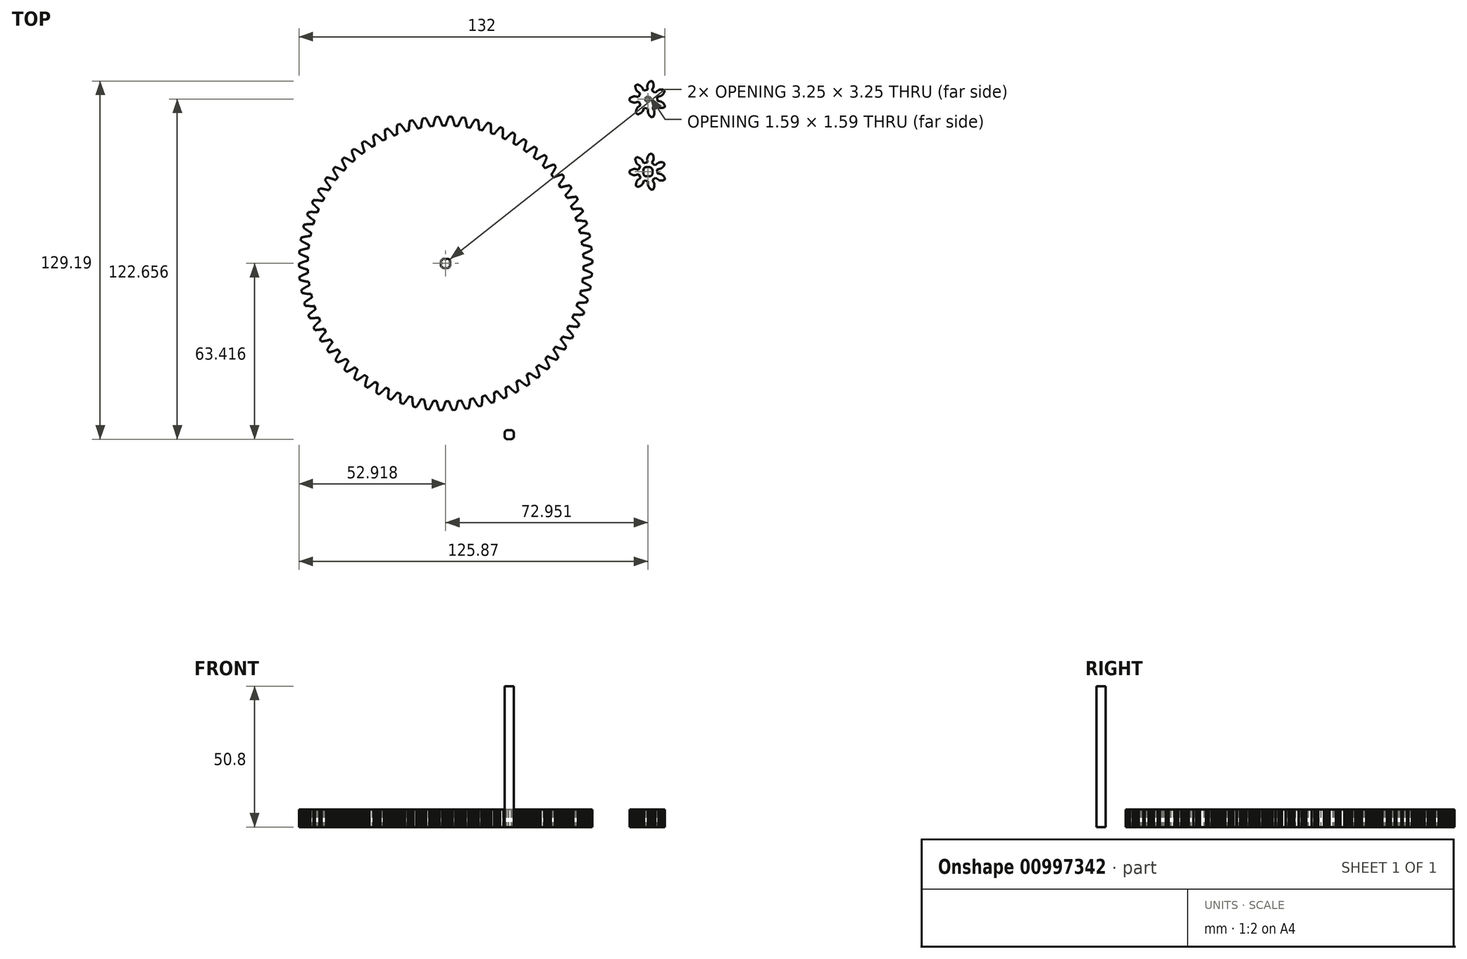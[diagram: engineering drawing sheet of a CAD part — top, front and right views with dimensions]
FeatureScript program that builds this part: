
annotation { "Feature Type Name" : "Feature", "Feature Type Description" : "" }
export const myFeature = defineFeature(function(context is Context, id is Id, definition is map)
    precondition{}
    {
        {
            var Q0;
            Q0=qCreatedBy(makeId("Top.planeOp"),FACE);
            var sketch = newSketch(context, id + "F0", { "sketchPlane" : qUnion([Q0])});
            skLineSegment(sketch, "E0", {"start": v(50.77, 50.5) * mm, "end": v(50.67, 50.68) * mm});
            skLineSegment(sketch, "E1", {"start": v(50.67, 50.68) * mm, "end": v(50.56, 50.86) * mm});
            skLineSegment(sketch, "E2", {"start": v(50.56, 50.86) * mm, "end": v(50.46, 51.01) * mm});
            skLineSegment(sketch, "E3", {"start": v(50.46, 51.01) * mm, "end": v(50.35, 51.16) * mm});
            skLineSegment(sketch, "E4", {"start": v(50.35, 51.16) * mm, "end": v(50.24, 51.28) * mm});
            skLineSegment(sketch, "E5", {"start": v(50.24, 51.28) * mm, "end": v(50.14, 51.4) * mm});
            skLineSegment(sketch, "E6", {"start": v(50.14, 51.4) * mm, "end": v(50.04, 51.5) * mm});
            skLineSegment(sketch, "E7", {"start": v(50.04, 51.5) * mm, "end": v(49.94, 51.58) * mm});
            skLineSegment(sketch, "E8", {"start": v(49.94, 51.58) * mm, "end": v(49.85, 51.66) * mm});
            skLineSegment(sketch, "E9", {"start": v(49.85, 51.66) * mm, "end": v(49.76, 51.72) * mm});
            skLineSegment(sketch, "E10", {"start": v(49.76, 51.72) * mm, "end": v(49.68, 51.77) * mm});
            skLineSegment(sketch, "E11", {"start": v(49.68, 51.77) * mm, "end": v(49.61, 51.81) * mm});
            skLineSegment(sketch, "E12", {"start": v(49.61, 51.81) * mm, "end": v(49.55, 51.85) * mm});
            skLineSegment(sketch, "E13", {"start": v(49.55, 51.85) * mm, "end": v(49.5, 51.87) * mm});
            skLineSegment(sketch, "E14", {"start": v(49.5, 51.87) * mm, "end": v(49.45, 51.89) * mm});
            skLineSegment(sketch, "E15", {"start": v(49.45, 51.89) * mm, "end": v(49.42, 51.9) * mm});
            skLineSegment(sketch, "E16", {"start": v(49.42, 51.9) * mm, "end": v(49.4, 51.9) * mm});
            skLineSegment(sketch, "E17", {"start": v(49.4, 51.9) * mm, "end": v(49.4, 51.9) * mm});
            skLineSegment(sketch, "E18", {"start": v(49.4, 51.9) * mm, "end": v(48.03, 52.16) * mm});
            skLineSegment(sketch, "E19", {"start": v(48.03, 52.16) * mm, "end": v(48, 53.63) * mm});
            skLineSegment(sketch, "E20", {"start": v(48, 53.63) * mm, "end": v(49.33, 53.97) * mm});
            skLineSegment(sketch, "E21", {"start": v(49.33, 53.97) * mm, "end": v(49.34, 53.97) * mm});
            skLineSegment(sketch, "E22", {"start": v(49.34, 53.97) * mm, "end": v(49.36, 53.98) * mm});
            skLineSegment(sketch, "E23", {"start": v(49.36, 53.98) * mm, "end": v(49.4, 53.99) * mm});
            skLineSegment(sketch, "E24", {"start": v(49.4, 53.99) * mm, "end": v(49.44, 54) * mm});
            skLineSegment(sketch, "E25", {"start": v(49.44, 54) * mm, "end": v(49.5, 54.03) * mm});
            skLineSegment(sketch, "E26", {"start": v(49.5, 54.03) * mm, "end": v(49.55, 54.07) * mm});
            skLineSegment(sketch, "E27", {"start": v(49.55, 54.07) * mm, "end": v(49.62, 54.12) * mm});
            skLineSegment(sketch, "E28", {"start": v(49.62, 54.12) * mm, "end": v(49.7, 54.17) * mm});
            skLineSegment(sketch, "E29", {"start": v(49.7, 54.17) * mm, "end": v(49.78, 54.24) * mm});
            skLineSegment(sketch, "E30", {"start": v(49.78, 54.24) * mm, "end": v(49.87, 54.32) * mm});
            skLineSegment(sketch, "E31", {"start": v(49.87, 54.32) * mm, "end": v(49.96, 54.41) * mm});
            skLineSegment(sketch, "E32", {"start": v(49.96, 54.41) * mm, "end": v(50.05, 54.52) * mm});
            skLineSegment(sketch, "E33", {"start": v(50.05, 54.52) * mm, "end": v(50.15, 54.64) * mm});
            skLineSegment(sketch, "E34", {"start": v(50.15, 54.64) * mm, "end": v(50.25, 54.77) * mm});
            skLineSegment(sketch, "E35", {"start": v(50.25, 54.77) * mm, "end": v(50.35, 54.92) * mm});
            skLineSegment(sketch, "E36", {"start": v(50.35, 54.92) * mm, "end": v(50.45, 55.08) * mm});
            skLineSegment(sketch, "E37", {"start": v(50.45, 55.08) * mm, "end": v(50.54, 55.26) * mm});
            skLineSegment(sketch, "E38", {"start": v(50.54, 55.26) * mm, "end": v(50.63, 55.45) * mm});
            skLineSegment(sketch, "E39", {"start": v(50.63, 55.45) * mm, "end": v(50.63, 55.62) * mm});
            skLineSegment(sketch, "E40", {"start": v(50.63, 55.62) * mm, "end": v(50.4, 56.06) * mm});
            skLineSegment(sketch, "E41", {"start": v(50.4, 56.06) * mm, "end": v(50.27, 56.16) * mm});
            skLineSegment(sketch, "E42", {"start": v(50.27, 56.16) * mm, "end": v(50.06, 56.2) * mm});
            skLineSegment(sketch, "E43", {"start": v(50.06, 56.2) * mm, "end": v(49.86, 56.22) * mm});
            skLineSegment(sketch, "E44", {"start": v(49.86, 56.22) * mm, "end": v(49.67, 56.24) * mm});
            skLineSegment(sketch, "E45", {"start": v(49.67, 56.24) * mm, "end": v(49.5, 56.24) * mm});
            skLineSegment(sketch, "E46", {"start": v(49.5, 56.24) * mm, "end": v(49.32, 56.24) * mm});
            skLineSegment(sketch, "E47", {"start": v(49.32, 56.24) * mm, "end": v(49.17, 56.23) * mm});
            skLineSegment(sketch, "E48", {"start": v(49.17, 56.23) * mm, "end": v(49.03, 56.21) * mm});
            skLineSegment(sketch, "E49", {"start": v(49.03, 56.21) * mm, "end": v(48.9, 56.19) * mm});
            skLineSegment(sketch, "E50", {"start": v(48.9, 56.19) * mm, "end": v(48.78, 56.16) * mm});
            skLineSegment(sketch, "E51", {"start": v(48.78, 56.16) * mm, "end": v(48.68, 56.14) * mm});
            skLineSegment(sketch, "E52", {"start": v(48.68, 56.14) * mm, "end": v(48.6, 56.1) * mm});
            skLineSegment(sketch, "E53", {"start": v(48.6, 56.1) * mm, "end": v(48.52, 56.08) * mm});
            skLineSegment(sketch, "E54", {"start": v(48.52, 56.08) * mm, "end": v(48.45, 56.05) * mm});
            skLineSegment(sketch, "E55", {"start": v(48.45, 56.05) * mm, "end": v(48.4, 56.02) * mm});
            skLineSegment(sketch, "E56", {"start": v(48.4, 56.02) * mm, "end": v(48.36, 56) * mm});
            skLineSegment(sketch, "E57", {"start": v(48.36, 56) * mm, "end": v(48.33, 55.98) * mm});
            skLineSegment(sketch, "E58", {"start": v(48.33, 55.98) * mm, "end": v(48.31, 55.97) * mm});
            skLineSegment(sketch, "E59", {"start": v(48.31, 55.97) * mm, "end": v(48.3, 55.96) * mm});
            skLineSegment(sketch, "E60", {"start": v(48.3, 55.96) * mm, "end": v(47.26, 55.06) * mm});
            skLineSegment(sketch, "E61", {"start": v(47.26, 55.06) * mm, "end": v(46.08, 55.94) * mm});
            skLineSegment(sketch, "E62", {"start": v(46.08, 55.94) * mm, "end": v(46.66, 57.2) * mm});
            skLineSegment(sketch, "E63", {"start": v(46.66, 57.2) * mm, "end": v(46.66, 57.2) * mm});
            skLineSegment(sketch, "E64", {"start": v(46.66, 57.2) * mm, "end": v(46.67, 57.23) * mm});
            skLineSegment(sketch, "E65", {"start": v(46.67, 57.23) * mm, "end": v(46.68, 57.26) * mm});
            skLineSegment(sketch, "E66", {"start": v(46.68, 57.26) * mm, "end": v(46.7, 57.3) * mm});
            skLineSegment(sketch, "E67", {"start": v(46.7, 57.3) * mm, "end": v(46.7, 57.36) * mm});
            skLineSegment(sketch, "E68", {"start": v(46.7, 57.36) * mm, "end": v(46.71, 57.43) * mm});
            skLineSegment(sketch, "E69", {"start": v(46.71, 57.43) * mm, "end": v(46.72, 57.52) * mm});
            skLineSegment(sketch, "E70", {"start": v(46.72, 57.52) * mm, "end": v(46.72, 57.61) * mm});
            skLineSegment(sketch, "E71", {"start": v(46.72, 57.61) * mm, "end": v(46.72, 57.72) * mm});
            skLineSegment(sketch, "E72", {"start": v(46.72, 57.72) * mm, "end": v(46.72, 57.83) * mm});
            skLineSegment(sketch, "E73", {"start": v(46.72, 57.83) * mm, "end": v(46.7, 57.96) * mm});
            skLineSegment(sketch, "E74", {"start": v(46.7, 57.96) * mm, "end": v(46.68, 58.1) * mm});
            skLineSegment(sketch, "E75", {"start": v(46.68, 58.1) * mm, "end": v(46.65, 58.26) * mm});
            skLineSegment(sketch, "E76", {"start": v(46.65, 58.26) * mm, "end": v(46.6, 58.42) * mm});
            skLineSegment(sketch, "E77", {"start": v(46.6, 58.42) * mm, "end": v(46.55, 58.59) * mm});
            skLineSegment(sketch, "E78", {"start": v(46.55, 58.59) * mm, "end": v(46.48, 58.77) * mm});
            skLineSegment(sketch, "E79", {"start": v(46.48, 58.77) * mm, "end": v(46.4, 58.95) * mm});
            skLineSegment(sketch, "E80", {"start": v(46.4, 58.95) * mm, "end": v(46.3, 59.14) * mm});
            skLineSegment(sketch, "E81", {"start": v(46.3, 59.14) * mm, "end": v(46.17, 59.24) * mm});
            skLineSegment(sketch, "E82", {"start": v(46.17, 59.24) * mm, "end": v(45.7, 59.34) * mm});
            skLineSegment(sketch, "E83", {"start": v(45.7, 59.34) * mm, "end": v(45.53, 59.3) * mm});
            skLineSegment(sketch, "E84", {"start": v(45.53, 59.3) * mm, "end": v(45.37, 59.16) * mm});
            skLineSegment(sketch, "E85", {"start": v(45.37, 59.16) * mm, "end": v(45.22, 59.02) * mm});
            skLineSegment(sketch, "E86", {"start": v(45.22, 59.02) * mm, "end": v(45.1, 58.88) * mm});
            skLineSegment(sketch, "E87", {"start": v(45.1, 58.88) * mm, "end": v(44.98, 58.74) * mm});
            skLineSegment(sketch, "E88", {"start": v(44.98, 58.74) * mm, "end": v(44.88, 58.6) * mm});
            skLineSegment(sketch, "E89", {"start": v(44.88, 58.6) * mm, "end": v(44.79, 58.48) * mm});
            skLineSegment(sketch, "E90", {"start": v(44.79, 58.48) * mm, "end": v(44.71, 58.36) * mm});
            skLineSegment(sketch, "E91", {"start": v(44.71, 58.36) * mm, "end": v(44.65, 58.25) * mm});
            skLineSegment(sketch, "E92", {"start": v(44.65, 58.25) * mm, "end": v(44.6, 58.14) * mm});
            skLineSegment(sketch, "E93", {"start": v(44.6, 58.14) * mm, "end": v(44.56, 58.04) * mm});
            skLineSegment(sketch, "E94", {"start": v(44.56, 58.04) * mm, "end": v(44.52, 57.95) * mm});
            skLineSegment(sketch, "E95", {"start": v(44.52, 57.95) * mm, "end": v(44.5, 57.88) * mm});
            skLineSegment(sketch, "E96", {"start": v(44.5, 57.88) * mm, "end": v(44.48, 57.8) * mm});
            skLineSegment(sketch, "E97", {"start": v(44.48, 57.8) * mm, "end": v(44.47, 57.75) * mm});
            skLineSegment(sketch, "E98", {"start": v(44.47, 57.75) * mm, "end": v(44.46, 57.7) * mm});
            skLineSegment(sketch, "E99", {"start": v(44.46, 57.7) * mm, "end": v(44.46, 57.67) * mm});
            skLineSegment(sketch, "E100", {"start": v(44.46, 57.67) * mm, "end": v(44.46, 57.65) * mm});
            skLineSegment(sketch, "E101", {"start": v(44.46, 57.65) * mm, "end": v(44.46, 57.64) * mm});
            skLineSegment(sketch, "E102", {"start": v(44.46, 57.64) * mm, "end": v(44.5, 56.26) * mm});
            skLineSegment(sketch, "E103", {"start": v(44.5, 56.26) * mm, "end": v(43.09, 55.9) * mm});
            skLineSegment(sketch, "E104", {"start": v(43.09, 55.9) * mm, "end": v(42.47, 57.13) * mm});
            skLineSegment(sketch, "E105", {"start": v(42.47, 57.13) * mm, "end": v(42.46, 57.13) * mm});
            skLineSegment(sketch, "E106", {"start": v(42.46, 57.13) * mm, "end": v(42.45, 57.15) * mm});
            skLineSegment(sketch, "E107", {"start": v(42.45, 57.15) * mm, "end": v(42.43, 57.18) * mm});
            skLineSegment(sketch, "E108", {"start": v(42.43, 57.18) * mm, "end": v(42.4, 57.22) * mm});
            skLineSegment(sketch, "E109", {"start": v(42.4, 57.22) * mm, "end": v(42.36, 57.26) * mm});
            skLineSegment(sketch, "E110", {"start": v(42.36, 57.26) * mm, "end": v(42.31, 57.31) * mm});
            skLineSegment(sketch, "E111", {"start": v(42.31, 57.31) * mm, "end": v(42.25, 57.37) * mm});
            skLineSegment(sketch, "E112", {"start": v(42.25, 57.37) * mm, "end": v(42.18, 57.43) * mm});
            skLineSegment(sketch, "E113", {"start": v(42.18, 57.43) * mm, "end": v(42.1, 57.5) * mm});
            skLineSegment(sketch, "E114", {"start": v(42.1, 57.5) * mm, "end": v(42, 57.56) * mm});
            skLineSegment(sketch, "E115", {"start": v(42, 57.56) * mm, "end": v(41.9, 57.63) * mm});
            skLineSegment(sketch, "E116", {"start": v(41.9, 57.63) * mm, "end": v(41.77, 57.7) * mm});
            skLineSegment(sketch, "E117", {"start": v(41.77, 57.7) * mm, "end": v(41.63, 57.77) * mm});
            skLineSegment(sketch, "E118", {"start": v(41.63, 57.77) * mm, "end": v(41.48, 57.84) * mm});
            skLineSegment(sketch, "E119", {"start": v(41.48, 57.84) * mm, "end": v(41.31, 57.9) * mm});
            skLineSegment(sketch, "E120", {"start": v(41.31, 57.9) * mm, "end": v(41.13, 57.96) * mm});
            skLineSegment(sketch, "E121", {"start": v(41.13, 57.96) * mm, "end": v(40.93, 58.02) * mm});
            skLineSegment(sketch, "E122", {"start": v(40.93, 58.02) * mm, "end": v(40.72, 58.06) * mm});
            skLineSegment(sketch, "E123", {"start": v(40.72, 58.06) * mm, "end": v(40.56, 58.02) * mm});
            skLineSegment(sketch, "E124", {"start": v(40.56, 58.02) * mm, "end": v(40.2, 57.7) * mm});
            skLineSegment(sketch, "E125", {"start": v(40.2, 57.7) * mm, "end": v(40.12, 57.55) * mm});
            skLineSegment(sketch, "E126", {"start": v(40.12, 57.55) * mm, "end": v(40.13, 57.34) * mm});
            skLineSegment(sketch, "E127", {"start": v(40.13, 57.34) * mm, "end": v(40.15, 57.13) * mm});
            skLineSegment(sketch, "E128", {"start": v(40.15, 57.13) * mm, "end": v(40.18, 56.95) * mm});
            skLineSegment(sketch, "E129", {"start": v(40.18, 56.95) * mm, "end": v(40.21, 56.77) * mm});
            skLineSegment(sketch, "E130", {"start": v(40.21, 56.77) * mm, "end": v(40.25, 56.6) * mm});
            skLineSegment(sketch, "E131", {"start": v(40.25, 56.6) * mm, "end": v(40.3, 56.46) * mm});
            skLineSegment(sketch, "E132", {"start": v(40.3, 56.46) * mm, "end": v(40.34, 56.33) * mm});
            skLineSegment(sketch, "E133", {"start": v(40.34, 56.33) * mm, "end": v(40.4, 56.2) * mm});
            skLineSegment(sketch, "E134", {"start": v(40.4, 56.2) * mm, "end": v(40.44, 56.1) * mm});
            skLineSegment(sketch, "E135", {"start": v(40.44, 56.1) * mm, "end": v(40.5, 56) * mm});
            skLineSegment(sketch, "E136", {"start": v(40.5, 56) * mm, "end": v(40.54, 55.93) * mm});
            skLineSegment(sketch, "E137", {"start": v(40.54, 55.93) * mm, "end": v(40.59, 55.86) * mm});
            skLineSegment(sketch, "E138", {"start": v(40.59, 55.86) * mm, "end": v(40.63, 55.8) * mm});
            skLineSegment(sketch, "E139", {"start": v(40.63, 55.8) * mm, "end": v(40.67, 55.76) * mm});
            skLineSegment(sketch, "E140", {"start": v(40.67, 55.76) * mm, "end": v(40.7, 55.72) * mm});
            skLineSegment(sketch, "E141", {"start": v(40.7, 55.72) * mm, "end": v(40.72, 55.7) * mm});
            skLineSegment(sketch, "E142", {"start": v(40.72, 55.7) * mm, "end": v(40.74, 55.68) * mm});
            skLineSegment(sketch, "E143", {"start": v(40.74, 55.68) * mm, "end": v(40.75, 55.68) * mm});
            skLineSegment(sketch, "E144", {"start": v(40.75, 55.68) * mm, "end": v(41.86, 54.86) * mm});
            skLineSegment(sketch, "E145", {"start": v(41.86, 54.86) * mm, "end": v(41.26, 53.52) * mm});
            skLineSegment(sketch, "E146", {"start": v(41.26, 53.52) * mm, "end": v(39.9, 53.8) * mm});
            skLineSegment(sketch, "E147", {"start": v(39.9, 53.8) * mm, "end": v(39.9, 53.8) * mm});
            skLineSegment(sketch, "E148", {"start": v(39.9, 53.8) * mm, "end": v(39.88, 53.8) * mm});
            skLineSegment(sketch, "E149", {"start": v(39.88, 53.8) * mm, "end": v(39.84, 53.8) * mm});
            skLineSegment(sketch, "E150", {"start": v(39.84, 53.8) * mm, "end": v(39.8, 53.8) * mm});
            skLineSegment(sketch, "E151", {"start": v(39.8, 53.8) * mm, "end": v(39.74, 53.8) * mm});
            skLineSegment(sketch, "E152", {"start": v(39.74, 53.8) * mm, "end": v(39.67, 53.8) * mm});
            skLineSegment(sketch, "E153", {"start": v(39.67, 53.8) * mm, "end": v(39.59, 53.79) * mm});
            skLineSegment(sketch, "E154", {"start": v(39.59, 53.79) * mm, "end": v(39.5, 53.77) * mm});
            skLineSegment(sketch, "E155", {"start": v(39.5, 53.77) * mm, "end": v(39.39, 53.74) * mm});
            skLineSegment(sketch, "E156", {"start": v(39.39, 53.74) * mm, "end": v(39.28, 53.71) * mm});
            skLineSegment(sketch, "E157", {"start": v(39.28, 53.71) * mm, "end": v(39.15, 53.67) * mm});
            skLineSegment(sketch, "E158", {"start": v(39.15, 53.67) * mm, "end": v(39.02, 53.62) * mm});
            skLineSegment(sketch, "E159", {"start": v(39.02, 53.62) * mm, "end": v(38.88, 53.55) * mm});
            skLineSegment(sketch, "E160", {"start": v(38.88, 53.55) * mm, "end": v(38.73, 53.47) * mm});
            skLineSegment(sketch, "E161", {"start": v(38.73, 53.47) * mm, "end": v(38.58, 53.38) * mm});
            skLineSegment(sketch, "E162", {"start": v(38.58, 53.38) * mm, "end": v(38.42, 53.28) * mm});
            skLineSegment(sketch, "E163", {"start": v(38.42, 53.28) * mm, "end": v(38.26, 53.16) * mm});
            skLineSegment(sketch, "E164", {"start": v(38.26, 53.16) * mm, "end": v(38.1, 53.02) * mm});
            skLineSegment(sketch, "E165", {"start": v(38.1, 53.02) * mm, "end": v(38.03, 52.87) * mm});
            skLineSegment(sketch, "E166", {"start": v(38.03, 52.87) * mm, "end": v(38.04, 52.38) * mm});
            skLineSegment(sketch, "E167", {"start": v(38.04, 52.38) * mm, "end": v(38.11, 52.23) * mm});
            skLineSegment(sketch, "E168", {"start": v(38.11, 52.23) * mm, "end": v(38.29, 52.1) * mm});
            skLineSegment(sketch, "E169", {"start": v(38.29, 52.1) * mm, "end": v(38.46, 52) * mm});
            skLineSegment(sketch, "E170", {"start": v(38.46, 52) * mm, "end": v(38.62, 51.9) * mm});
            skLineSegment(sketch, "E171", {"start": v(38.62, 51.9) * mm, "end": v(38.78, 51.82) * mm});
            skLineSegment(sketch, "E172", {"start": v(38.78, 51.82) * mm, "end": v(38.93, 51.75) * mm});
            skLineSegment(sketch, "E173", {"start": v(38.93, 51.75) * mm, "end": v(39.07, 51.69) * mm});
            skLineSegment(sketch, "E174", {"start": v(39.07, 51.69) * mm, "end": v(39.2, 51.64) * mm});
            skLineSegment(sketch, "E175", {"start": v(39.2, 51.64) * mm, "end": v(39.33, 51.6) * mm});
            skLineSegment(sketch, "E176", {"start": v(39.33, 51.6) * mm, "end": v(39.45, 51.58) * mm});
            skLineSegment(sketch, "E177", {"start": v(39.45, 51.58) * mm, "end": v(39.55, 51.56) * mm});
            skLineSegment(sketch, "E178", {"start": v(39.55, 51.56) * mm, "end": v(39.65, 51.55) * mm});
            skLineSegment(sketch, "E179", {"start": v(39.65, 51.55) * mm, "end": v(39.73, 51.54) * mm});
            skLineSegment(sketch, "E180", {"start": v(39.73, 51.54) * mm, "end": v(39.8, 51.54) * mm});
            skLineSegment(sketch, "E181", {"start": v(39.8, 51.54) * mm, "end": v(39.86, 51.54) * mm});
            skLineSegment(sketch, "E182", {"start": v(39.86, 51.54) * mm, "end": v(39.9, 51.54) * mm});
            skLineSegment(sketch, "E183", {"start": v(39.9, 51.54) * mm, "end": v(39.94, 51.55) * mm});
            skLineSegment(sketch, "E184", {"start": v(39.94, 51.55) * mm, "end": v(39.96, 51.55) * mm});
            skLineSegment(sketch, "E185", {"start": v(39.96, 51.55) * mm, "end": v(39.97, 51.55) * mm});
            skLineSegment(sketch, "E186", {"start": v(39.97, 51.55) * mm, "end": v(41.3, 51.91) * mm});
            skLineSegment(sketch, "E187", {"start": v(41.3, 51.91) * mm, "end": v(41.98, 50.6) * mm});
            skLineSegment(sketch, "E188", {"start": v(41.98, 50.6) * mm, "end": v(40.91, 49.73) * mm});
            skLineSegment(sketch, "E189", {"start": v(40.91, 49.73) * mm, "end": v(40.9, 49.72) * mm});
            skLineSegment(sketch, "E190", {"start": v(40.9, 49.72) * mm, "end": v(40.9, 49.7) * mm});
            skLineSegment(sketch, "E191", {"start": v(40.9, 49.7) * mm, "end": v(40.87, 49.68) * mm});
            skLineSegment(sketch, "E192", {"start": v(40.87, 49.68) * mm, "end": v(40.84, 49.64) * mm});
            skLineSegment(sketch, "E193", {"start": v(40.84, 49.64) * mm, "end": v(40.8, 49.6) * mm});
            skLineSegment(sketch, "E194", {"start": v(40.8, 49.6) * mm, "end": v(40.76, 49.54) * mm});
            skLineSegment(sketch, "E195", {"start": v(40.76, 49.54) * mm, "end": v(40.72, 49.47) * mm});
            skLineSegment(sketch, "E196", {"start": v(40.72, 49.47) * mm, "end": v(40.68, 49.38) * mm});
            skLineSegment(sketch, "E197", {"start": v(40.68, 49.38) * mm, "end": v(40.63, 49.29) * mm});
            skLineSegment(sketch, "E198", {"start": v(40.63, 49.29) * mm, "end": v(40.59, 49.18) * mm});
            skLineSegment(sketch, "E199", {"start": v(40.59, 49.18) * mm, "end": v(40.54, 49.05) * mm});
            skLineSegment(sketch, "E200", {"start": v(40.54, 49.05) * mm, "end": v(40.5, 48.92) * mm});
            skLineSegment(sketch, "E201", {"start": v(40.5, 48.92) * mm, "end": v(40.47, 48.77) * mm});
            skLineSegment(sketch, "E202", {"start": v(40.47, 48.77) * mm, "end": v(40.44, 48.6) * mm});
            skLineSegment(sketch, "E203", {"start": v(40.44, 48.6) * mm, "end": v(40.41, 48.43) * mm});
            skLineSegment(sketch, "E204", {"start": v(40.41, 48.43) * mm, "end": v(40.4, 48.24) * mm});
            skLineSegment(sketch, "E205", {"start": v(40.4, 48.24) * mm, "end": v(40.39, 48.03) * mm});
            skLineSegment(sketch, "E206", {"start": v(40.39, 48.03) * mm, "end": v(40.39, 47.82) * mm});
            skLineSegment(sketch, "E207", {"start": v(40.39, 47.82) * mm, "end": v(40.47, 47.67) * mm});
            skLineSegment(sketch, "E208", {"start": v(40.47, 47.67) * mm, "end": v(40.86, 47.38) * mm});
            skLineSegment(sketch, "E209", {"start": v(40.86, 47.38) * mm, "end": v(41.02, 47.34) * mm});
            skLineSegment(sketch, "E210", {"start": v(41.02, 47.34) * mm, "end": v(41.23, 47.4) * mm});
            skLineSegment(sketch, "E211", {"start": v(41.23, 47.4) * mm, "end": v(41.42, 47.46) * mm});
            skLineSegment(sketch, "E212", {"start": v(41.42, 47.46) * mm, "end": v(41.6, 47.53) * mm});
            skLineSegment(sketch, "E213", {"start": v(41.6, 47.53) * mm, "end": v(41.76, 47.6) * mm});
            skLineSegment(sketch, "E214", {"start": v(41.76, 47.6) * mm, "end": v(41.9, 47.68) * mm});
            skLineSegment(sketch, "E215", {"start": v(41.9, 47.68) * mm, "end": v(42.04, 47.76) * mm});
            skLineSegment(sketch, "E216", {"start": v(42.04, 47.76) * mm, "end": v(42.16, 47.83) * mm});
            skLineSegment(sketch, "E217", {"start": v(42.16, 47.83) * mm, "end": v(42.27, 47.9) * mm});
            skLineSegment(sketch, "E218", {"start": v(42.27, 47.9) * mm, "end": v(42.36, 47.98) * mm});
            skLineSegment(sketch, "E219", {"start": v(42.36, 47.98) * mm, "end": v(42.44, 48.05) * mm});
            skLineSegment(sketch, "E220", {"start": v(42.44, 48.05) * mm, "end": v(42.51, 48.12) * mm});
            skLineSegment(sketch, "E221", {"start": v(42.51, 48.12) * mm, "end": v(42.57, 48.18) * mm});
            skLineSegment(sketch, "E222", {"start": v(42.57, 48.18) * mm, "end": v(42.61, 48.23) * mm});
            skLineSegment(sketch, "E223", {"start": v(42.61, 48.23) * mm, "end": v(42.65, 48.28) * mm});
            skLineSegment(sketch, "E224", {"start": v(42.65, 48.28) * mm, "end": v(42.67, 48.32) * mm});
            skLineSegment(sketch, "E225", {"start": v(42.67, 48.32) * mm, "end": v(42.7, 48.35) * mm});
            skLineSegment(sketch, "E226", {"start": v(42.7, 48.35) * mm, "end": v(42.7, 48.37) * mm});
            skLineSegment(sketch, "E227", {"start": v(42.7, 48.37) * mm, "end": v(42.7, 48.37) * mm});
            skLineSegment(sketch, "E228", {"start": v(42.7, 48.37) * mm, "end": v(43.26, 49.64) * mm});
            skLineSegment(sketch, "E229", {"start": v(43.26, 49.64) * mm, "end": v(44.7, 49.35) * mm});
            skLineSegment(sketch, "E230", {"start": v(44.7, 49.35) * mm, "end": v(44.72, 47.97) * mm});
            skLineSegment(sketch, "E231", {"start": v(44.72, 47.97) * mm, "end": v(44.73, 47.96) * mm});
            skLineSegment(sketch, "E232", {"start": v(44.73, 47.96) * mm, "end": v(44.73, 47.94) * mm});
            skLineSegment(sketch, "E233", {"start": v(44.73, 47.94) * mm, "end": v(44.73, 47.9) * mm});
            skLineSegment(sketch, "E234", {"start": v(44.73, 47.9) * mm, "end": v(44.74, 47.86) * mm});
            skLineSegment(sketch, "E235", {"start": v(44.74, 47.86) * mm, "end": v(44.76, 47.8) * mm});
            skLineSegment(sketch, "E236", {"start": v(44.76, 47.8) * mm, "end": v(44.78, 47.74) * mm});
            skLineSegment(sketch, "E237", {"start": v(44.78, 47.74) * mm, "end": v(44.8, 47.66) * mm});
            skLineSegment(sketch, "E238", {"start": v(44.8, 47.66) * mm, "end": v(44.85, 47.57) * mm});
            skLineSegment(sketch, "E239", {"start": v(44.85, 47.57) * mm, "end": v(44.9, 47.48) * mm});
            skLineSegment(sketch, "E240", {"start": v(44.9, 47.48) * mm, "end": v(44.95, 47.37) * mm});
            skLineSegment(sketch, "E241", {"start": v(44.95, 47.37) * mm, "end": v(45.02, 47.26) * mm});
            skLineSegment(sketch, "E242", {"start": v(45.02, 47.26) * mm, "end": v(45.1, 47.15) * mm});
            skLineSegment(sketch, "E243", {"start": v(45.1, 47.15) * mm, "end": v(45.2, 47.03) * mm});
            skLineSegment(sketch, "E244", {"start": v(45.2, 47.03) * mm, "end": v(45.3, 46.9) * mm});
            skLineSegment(sketch, "E245", {"start": v(45.3, 46.9) * mm, "end": v(45.43, 46.77) * mm});
            skLineSegment(sketch, "E246", {"start": v(45.43, 46.77) * mm, "end": v(45.57, 46.64) * mm});
            skLineSegment(sketch, "E247", {"start": v(45.57, 46.64) * mm, "end": v(45.72, 46.5) * mm});
            skLineSegment(sketch, "E248", {"start": v(45.72, 46.5) * mm, "end": v(45.89, 46.37) * mm});
            skLineSegment(sketch, "E249", {"start": v(45.89, 46.37) * mm, "end": v(46.05, 46.34) * mm});
            skLineSegment(sketch, "E250", {"start": v(46.05, 46.34) * mm, "end": v(46.52, 46.47) * mm});
            skLineSegment(sketch, "E251", {"start": v(46.52, 46.47) * mm, "end": v(46.65, 46.57) * mm});
            skLineSegment(sketch, "E252", {"start": v(46.65, 46.57) * mm, "end": v(46.74, 46.77) * mm});
            skLineSegment(sketch, "E253", {"start": v(46.74, 46.77) * mm, "end": v(46.8, 46.96) * mm});
            skLineSegment(sketch, "E254", {"start": v(46.8, 46.96) * mm, "end": v(46.87, 47.14) * mm});
            skLineSegment(sketch, "E255", {"start": v(46.87, 47.14) * mm, "end": v(46.91, 47.31) * mm});
            skLineSegment(sketch, "E256", {"start": v(46.91, 47.31) * mm, "end": v(46.94, 47.48) * mm});
            skLineSegment(sketch, "E257", {"start": v(46.94, 47.48) * mm, "end": v(46.97, 47.63) * mm});
            skLineSegment(sketch, "E258", {"start": v(46.97, 47.63) * mm, "end": v(46.98, 47.77) * mm});
            skLineSegment(sketch, "E259", {"start": v(46.98, 47.77) * mm, "end": v(47, 47.9) * mm});
            skLineSegment(sketch, "E260", {"start": v(47, 47.9) * mm, "end": v(47, 48.02) * mm});
            skLineSegment(sketch, "E261", {"start": v(47, 48.02) * mm, "end": v(46.99, 48.12) * mm});
            skLineSegment(sketch, "E262", {"start": v(46.99, 48.12) * mm, "end": v(46.98, 48.22) * mm});
            skLineSegment(sketch, "E263", {"start": v(46.98, 48.22) * mm, "end": v(46.97, 48.3) * mm});
            skLineSegment(sketch, "E264", {"start": v(46.97, 48.3) * mm, "end": v(46.95, 48.37) * mm});
            skLineSegment(sketch, "E265", {"start": v(46.95, 48.37) * mm, "end": v(46.94, 48.43) * mm});
            skLineSegment(sketch, "E266", {"start": v(46.94, 48.43) * mm, "end": v(46.92, 48.47) * mm});
            skLineSegment(sketch, "E267", {"start": v(46.92, 48.47) * mm, "end": v(46.91, 48.5) * mm});
            skLineSegment(sketch, "E268", {"start": v(46.91, 48.5) * mm, "end": v(46.9, 48.52) * mm});
            skLineSegment(sketch, "E269", {"start": v(46.9, 48.52) * mm, "end": v(46.9, 48.53) * mm});
            skLineSegment(sketch, "E270", {"start": v(46.9, 48.53) * mm, "end": v(46.25, 49.75) * mm});
            skLineSegment(sketch, "E271", {"start": v(46.25, 49.75) * mm, "end": v(47.38, 50.7) * mm});
            skLineSegment(sketch, "E272", {"start": v(47.38, 50.7) * mm, "end": v(48.47, 49.86) * mm});
            skLineSegment(sketch, "E273", {"start": v(48.47, 49.86) * mm, "end": v(48.48, 49.85) * mm});
            skLineSegment(sketch, "E274", {"start": v(48.48, 49.85) * mm, "end": v(48.5, 49.84) * mm});
            skLineSegment(sketch, "E275", {"start": v(48.5, 49.84) * mm, "end": v(48.53, 49.82) * mm});
            skLineSegment(sketch, "E276", {"start": v(48.53, 49.82) * mm, "end": v(48.57, 49.8) * mm});
            skLineSegment(sketch, "E277", {"start": v(48.57, 49.8) * mm, "end": v(48.62, 49.78) * mm});
            skLineSegment(sketch, "E278", {"start": v(48.62, 49.78) * mm, "end": v(48.7, 49.76) * mm});
            skLineSegment(sketch, "E279", {"start": v(48.7, 49.76) * mm, "end": v(48.77, 49.73) * mm});
            skLineSegment(sketch, "E280", {"start": v(48.77, 49.73) * mm, "end": v(48.86, 49.7) * mm});
            skLineSegment(sketch, "E281", {"start": v(48.86, 49.7) * mm, "end": v(48.96, 49.68) * mm});
            skLineSegment(sketch, "E282", {"start": v(48.96, 49.68) * mm, "end": v(49.08, 49.66) * mm});
            skLineSegment(sketch, "E283", {"start": v(49.08, 49.66) * mm, "end": v(49.21, 49.65) * mm});
            skLineSegment(sketch, "E284", {"start": v(49.21, 49.65) * mm, "end": v(49.35, 49.64) * mm});
            skLineSegment(sketch, "E285", {"start": v(49.35, 49.64) * mm, "end": v(49.5, 49.64) * mm});
            skLineSegment(sketch, "E286", {"start": v(49.5, 49.64) * mm, "end": v(49.67, 49.64) * mm});
            skLineSegment(sketch, "E287", {"start": v(49.67, 49.64) * mm, "end": v(49.85, 49.66) * mm});
            skLineSegment(sketch, "E288", {"start": v(49.85, 49.66) * mm, "end": v(50.04, 49.68) * mm});
            skLineSegment(sketch, "E289", {"start": v(50.04, 49.68) * mm, "end": v(50.24, 49.72) * mm});
            skLineSegment(sketch, "E290", {"start": v(50.24, 49.72) * mm, "end": v(50.45, 49.77) * mm});
            skLineSegment(sketch, "E291", {"start": v(50.45, 49.77) * mm, "end": v(50.57, 49.88) * mm});
            skLineSegment(sketch, "E292", {"start": v(50.57, 49.88) * mm, "end": v(50.77, 50.33) * mm});
            skLineSegment(sketch, "E293", {"start": v(50.77, 50.33) * mm, "end": v(50.77, 50.5) * mm});
            skLineSegment(sketch, "E294", {"start": v(50.77, 24.31) * mm, "end": v(50.67, 24.5) * mm});
            skLineSegment(sketch, "E295", {"start": v(50.67, 24.5) * mm, "end": v(50.56, 24.67) * mm});
            skLineSegment(sketch, "E296", {"start": v(50.56, 24.67) * mm, "end": v(50.46, 24.83) * mm});
            skLineSegment(sketch, "E297", {"start": v(50.46, 24.83) * mm, "end": v(50.35, 24.97) * mm});
            skLineSegment(sketch, "E298", {"start": v(50.35, 24.97) * mm, "end": v(50.24, 25.1) * mm});
            skLineSegment(sketch, "E299", {"start": v(50.24, 25.1) * mm, "end": v(50.14, 25.22) * mm});
            skLineSegment(sketch, "E300", {"start": v(50.14, 25.22) * mm, "end": v(50.04, 25.32) * mm});
            skLineSegment(sketch, "E301", {"start": v(50.04, 25.32) * mm, "end": v(49.94, 25.4) * mm});
            skLineSegment(sketch, "E302", {"start": v(49.94, 25.4) * mm, "end": v(49.85, 25.48) * mm});
            skLineSegment(sketch, "E303", {"start": v(49.85, 25.48) * mm, "end": v(49.76, 25.54) * mm});
            skLineSegment(sketch, "E304", {"start": v(49.76, 25.54) * mm, "end": v(49.68, 25.6) * mm});
            skLineSegment(sketch, "E305", {"start": v(49.68, 25.6) * mm, "end": v(49.61, 25.63) * mm});
            skLineSegment(sketch, "E306", {"start": v(49.61, 25.63) * mm, "end": v(49.55, 25.66) * mm});
            skLineSegment(sketch, "E307", {"start": v(49.55, 25.66) * mm, "end": v(49.5, 25.69) * mm});
            skLineSegment(sketch, "E308", {"start": v(49.5, 25.69) * mm, "end": v(49.45, 25.7) * mm});
            skLineSegment(sketch, "E309", {"start": v(49.45, 25.7) * mm, "end": v(49.42, 25.72) * mm});
            skLineSegment(sketch, "E310", {"start": v(49.42, 25.72) * mm, "end": v(49.4, 25.72) * mm});
            skLineSegment(sketch, "E311", {"start": v(49.4, 25.72) * mm, "end": v(49.4, 25.73) * mm});
            skLineSegment(sketch, "E312", {"start": v(49.4, 25.73) * mm, "end": v(48.03, 25.98) * mm});
            skLineSegment(sketch, "E313", {"start": v(48.03, 25.98) * mm, "end": v(48, 27.45) * mm});
            skLineSegment(sketch, "E314", {"start": v(48, 27.45) * mm, "end": v(49.33, 27.78) * mm});
            skLineSegment(sketch, "E315", {"start": v(49.33, 27.78) * mm, "end": v(49.34, 27.79) * mm});
            skLineSegment(sketch, "E316", {"start": v(49.34, 27.79) * mm, "end": v(49.36, 27.8) * mm});
            skLineSegment(sketch, "E317", {"start": v(49.36, 27.8) * mm, "end": v(49.4, 27.8) * mm});
            skLineSegment(sketch, "E318", {"start": v(49.4, 27.8) * mm, "end": v(49.44, 27.83) * mm});
            skLineSegment(sketch, "E319", {"start": v(49.44, 27.83) * mm, "end": v(49.5, 27.85) * mm});
            skLineSegment(sketch, "E320", {"start": v(49.5, 27.85) * mm, "end": v(49.55, 27.89) * mm});
            skLineSegment(sketch, "E321", {"start": v(49.55, 27.89) * mm, "end": v(49.62, 27.93) * mm});
            skLineSegment(sketch, "E322", {"start": v(49.62, 27.93) * mm, "end": v(49.7, 27.99) * mm});
            skLineSegment(sketch, "E323", {"start": v(49.7, 27.99) * mm, "end": v(49.78, 28.06) * mm});
            skLineSegment(sketch, "E324", {"start": v(49.78, 28.06) * mm, "end": v(49.87, 28.14) * mm});
            skLineSegment(sketch, "E325", {"start": v(49.87, 28.14) * mm, "end": v(49.96, 28.23) * mm});
            skLineSegment(sketch, "E326", {"start": v(49.96, 28.23) * mm, "end": v(50.05, 28.33) * mm});
            skLineSegment(sketch, "E327", {"start": v(50.05, 28.33) * mm, "end": v(50.15, 28.45) * mm});
            skLineSegment(sketch, "E328", {"start": v(50.15, 28.45) * mm, "end": v(50.25, 28.59) * mm});
            skLineSegment(sketch, "E329", {"start": v(50.25, 28.59) * mm, "end": v(50.35, 28.74) * mm});
            skLineSegment(sketch, "E330", {"start": v(50.35, 28.74) * mm, "end": v(50.45, 28.9) * mm});
            skLineSegment(sketch, "E331", {"start": v(50.45, 28.9) * mm, "end": v(50.54, 29.08) * mm});
            skLineSegment(sketch, "E332", {"start": v(50.54, 29.08) * mm, "end": v(50.63, 29.27) * mm});
            skLineSegment(sketch, "E333", {"start": v(50.63, 29.27) * mm, "end": v(50.63, 29.44) * mm});
            skLineSegment(sketch, "E334", {"start": v(50.63, 29.44) * mm, "end": v(50.4, 29.87) * mm});
            skLineSegment(sketch, "E335", {"start": v(50.4, 29.87) * mm, "end": v(50.27, 29.98) * mm});
            skLineSegment(sketch, "E336", {"start": v(50.27, 29.98) * mm, "end": v(50.06, 30.01) * mm});
            skLineSegment(sketch, "E337", {"start": v(50.06, 30.01) * mm, "end": v(49.86, 30.04) * mm});
            skLineSegment(sketch, "E338", {"start": v(49.86, 30.04) * mm, "end": v(49.67, 30.05) * mm});
            skLineSegment(sketch, "E339", {"start": v(49.67, 30.05) * mm, "end": v(49.5, 30.06) * mm});
            skLineSegment(sketch, "E340", {"start": v(49.5, 30.06) * mm, "end": v(49.32, 30.06) * mm});
            skLineSegment(sketch, "E341", {"start": v(49.32, 30.06) * mm, "end": v(49.17, 30.05) * mm});
            skLineSegment(sketch, "E342", {"start": v(49.17, 30.05) * mm, "end": v(49.03, 30.03) * mm});
            skLineSegment(sketch, "E343", {"start": v(49.03, 30.03) * mm, "end": v(48.9, 30) * mm});
            skLineSegment(sketch, "E344", {"start": v(48.9, 30) * mm, "end": v(48.78, 29.98) * mm});
            skLineSegment(sketch, "E345", {"start": v(48.78, 29.98) * mm, "end": v(48.68, 29.95) * mm});
            skLineSegment(sketch, "E346", {"start": v(48.68, 29.95) * mm, "end": v(48.6, 29.92) * mm});
            skLineSegment(sketch, "E347", {"start": v(48.6, 29.92) * mm, "end": v(48.52, 29.9) * mm});
            skLineSegment(sketch, "E348", {"start": v(48.52, 29.9) * mm, "end": v(48.45, 29.87) * mm});
            skLineSegment(sketch, "E349", {"start": v(48.45, 29.87) * mm, "end": v(48.4, 29.84) * mm});
            skLineSegment(sketch, "E350", {"start": v(48.4, 29.84) * mm, "end": v(48.36, 29.82) * mm});
            skLineSegment(sketch, "E351", {"start": v(48.36, 29.82) * mm, "end": v(48.33, 29.8) * mm});
            skLineSegment(sketch, "E352", {"start": v(48.33, 29.8) * mm, "end": v(48.31, 29.78) * mm});
            skLineSegment(sketch, "E353", {"start": v(48.31, 29.78) * mm, "end": v(48.3, 29.78) * mm});
            skLineSegment(sketch, "E354", {"start": v(48.3, 29.78) * mm, "end": v(47.26, 28.88) * mm});
            skLineSegment(sketch, "E355", {"start": v(47.26, 28.88) * mm, "end": v(46.08, 29.76) * mm});
            skLineSegment(sketch, "E356", {"start": v(46.08, 29.76) * mm, "end": v(46.66, 31.02) * mm});
            skLineSegment(sketch, "E357", {"start": v(46.66, 31.02) * mm, "end": v(46.66, 31.03) * mm});
            skLineSegment(sketch, "E358", {"start": v(46.66, 31.03) * mm, "end": v(46.67, 31.05) * mm});
            skLineSegment(sketch, "E359", {"start": v(46.67, 31.05) * mm, "end": v(46.68, 31.08) * mm});
            skLineSegment(sketch, "E360", {"start": v(46.68, 31.08) * mm, "end": v(46.7, 31.12) * mm});
            skLineSegment(sketch, "E361", {"start": v(46.7, 31.12) * mm, "end": v(46.7, 31.18) * mm});
            skLineSegment(sketch, "E362", {"start": v(46.7, 31.18) * mm, "end": v(46.71, 31.25) * mm});
            skLineSegment(sketch, "E363", {"start": v(46.71, 31.25) * mm, "end": v(46.72, 31.33) * mm});
            skLineSegment(sketch, "E364", {"start": v(46.72, 31.33) * mm, "end": v(46.72, 31.43) * mm});
            skLineSegment(sketch, "E365", {"start": v(46.72, 31.43) * mm, "end": v(46.72, 31.53) * mm});
            skLineSegment(sketch, "E366", {"start": v(46.72, 31.53) * mm, "end": v(46.72, 31.65) * mm});
            skLineSegment(sketch, "E367", {"start": v(46.72, 31.65) * mm, "end": v(46.7, 31.78) * mm});
            skLineSegment(sketch, "E368", {"start": v(46.7, 31.78) * mm, "end": v(46.68, 31.92) * mm});
            skLineSegment(sketch, "E369", {"start": v(46.68, 31.92) * mm, "end": v(46.65, 32.07) * mm});
            skLineSegment(sketch, "E370", {"start": v(46.65, 32.07) * mm, "end": v(46.6, 32.23) * mm});
            skLineSegment(sketch, "E371", {"start": v(46.6, 32.23) * mm, "end": v(46.55, 32.4) * mm});
            skLineSegment(sketch, "E372", {"start": v(46.55, 32.4) * mm, "end": v(46.48, 32.58) * mm});
            skLineSegment(sketch, "E373", {"start": v(46.48, 32.58) * mm, "end": v(46.4, 32.77) * mm});
            skLineSegment(sketch, "E374", {"start": v(46.4, 32.77) * mm, "end": v(46.3, 32.96) * mm});
            skLineSegment(sketch, "E375", {"start": v(46.3, 32.96) * mm, "end": v(46.17, 33.06) * mm});
            skLineSegment(sketch, "E376", {"start": v(46.17, 33.06) * mm, "end": v(45.7, 33.15) * mm});
            skLineSegment(sketch, "E377", {"start": v(45.7, 33.15) * mm, "end": v(45.53, 33.12) * mm});
            skLineSegment(sketch, "E378", {"start": v(45.53, 33.12) * mm, "end": v(45.37, 32.97) * mm});
            skLineSegment(sketch, "E379", {"start": v(45.37, 32.97) * mm, "end": v(45.22, 32.83) * mm});
            skLineSegment(sketch, "E380", {"start": v(45.22, 32.83) * mm, "end": v(45.1, 32.7) * mm});
            skLineSegment(sketch, "E381", {"start": v(45.1, 32.7) * mm, "end": v(44.98, 32.56) * mm});
            skLineSegment(sketch, "E382", {"start": v(44.98, 32.56) * mm, "end": v(44.88, 32.43) * mm});
            skLineSegment(sketch, "E383", {"start": v(44.88, 32.43) * mm, "end": v(44.79, 32.3) * mm});
            skLineSegment(sketch, "E384", {"start": v(44.79, 32.3) * mm, "end": v(44.71, 32.18) * mm});
            skLineSegment(sketch, "E385", {"start": v(44.71, 32.18) * mm, "end": v(44.65, 32.06) * mm});
            skLineSegment(sketch, "E386", {"start": v(44.65, 32.06) * mm, "end": v(44.6, 31.96) * mm});
            skLineSegment(sketch, "E387", {"start": v(44.6, 31.96) * mm, "end": v(44.56, 31.86) * mm});
            skLineSegment(sketch, "E388", {"start": v(44.56, 31.86) * mm, "end": v(44.52, 31.77) * mm});
            skLineSegment(sketch, "E389", {"start": v(44.52, 31.77) * mm, "end": v(44.5, 31.7) * mm});
            skLineSegment(sketch, "E390", {"start": v(44.5, 31.7) * mm, "end": v(44.48, 31.63) * mm});
            skLineSegment(sketch, "E391", {"start": v(44.48, 31.63) * mm, "end": v(44.47, 31.57) * mm});
            skLineSegment(sketch, "E392", {"start": v(44.47, 31.57) * mm, "end": v(44.46, 31.52) * mm});
            skLineSegment(sketch, "E393", {"start": v(44.46, 31.52) * mm, "end": v(44.46, 31.49) * mm});
            skLineSegment(sketch, "E394", {"start": v(44.46, 31.49) * mm, "end": v(44.46, 31.47) * mm});
            skLineSegment(sketch, "E395", {"start": v(44.46, 31.47) * mm, "end": v(44.46, 31.46) * mm});
            skLineSegment(sketch, "E396", {"start": v(44.46, 31.46) * mm, "end": v(44.5, 30.08) * mm});
            skLineSegment(sketch, "E397", {"start": v(44.5, 30.08) * mm, "end": v(43.09, 29.7) * mm});
            skLineSegment(sketch, "E398", {"start": v(43.09, 29.7) * mm, "end": v(42.47, 30.94) * mm});
            skLineSegment(sketch, "E399", {"start": v(42.47, 30.94) * mm, "end": v(42.46, 30.95) * mm});
            skLineSegment(sketch, "E400", {"start": v(42.46, 30.95) * mm, "end": v(42.45, 30.97) * mm});
            skLineSegment(sketch, "E401", {"start": v(42.45, 30.97) * mm, "end": v(42.43, 31) * mm});
            skLineSegment(sketch, "E402", {"start": v(42.43, 31) * mm, "end": v(42.4, 31.04) * mm});
            skLineSegment(sketch, "E403", {"start": v(42.4, 31.04) * mm, "end": v(42.36, 31.08) * mm});
            skLineSegment(sketch, "E404", {"start": v(42.36, 31.08) * mm, "end": v(42.31, 31.13) * mm});
            skLineSegment(sketch, "E405", {"start": v(42.31, 31.13) * mm, "end": v(42.25, 31.19) * mm});
            skLineSegment(sketch, "E406", {"start": v(42.25, 31.19) * mm, "end": v(42.18, 31.25) * mm});
            skLineSegment(sketch, "E407", {"start": v(42.18, 31.25) * mm, "end": v(42.1, 31.31) * mm});
            skLineSegment(sketch, "E408", {"start": v(42.1, 31.31) * mm, "end": v(42, 31.38) * mm});
            skLineSegment(sketch, "E409", {"start": v(42, 31.38) * mm, "end": v(41.9, 31.45) * mm});
            skLineSegment(sketch, "E410", {"start": v(41.9, 31.45) * mm, "end": v(41.77, 31.52) * mm});
            skLineSegment(sketch, "E411", {"start": v(41.77, 31.52) * mm, "end": v(41.63, 31.6) * mm});
            skLineSegment(sketch, "E412", {"start": v(41.63, 31.6) * mm, "end": v(41.48, 31.66) * mm});
            skLineSegment(sketch, "E413", {"start": v(41.48, 31.66) * mm, "end": v(41.31, 31.72) * mm});
            skLineSegment(sketch, "E414", {"start": v(41.31, 31.72) * mm, "end": v(41.13, 31.78) * mm});
            skLineSegment(sketch, "E415", {"start": v(41.13, 31.78) * mm, "end": v(40.93, 31.83) * mm});
            skLineSegment(sketch, "E416", {"start": v(40.93, 31.83) * mm, "end": v(40.72, 31.88) * mm});
            skLineSegment(sketch, "E417", {"start": v(40.72, 31.88) * mm, "end": v(40.56, 31.83) * mm});
            skLineSegment(sketch, "E418", {"start": v(40.56, 31.83) * mm, "end": v(40.2, 31.52) * mm});
            skLineSegment(sketch, "E419", {"start": v(40.2, 31.52) * mm, "end": v(40.12, 31.37) * mm});
            skLineSegment(sketch, "E420", {"start": v(40.12, 31.37) * mm, "end": v(40.13, 31.15) * mm});
            skLineSegment(sketch, "E421", {"start": v(40.13, 31.15) * mm, "end": v(40.15, 30.95) * mm});
            skLineSegment(sketch, "E422", {"start": v(40.15, 30.95) * mm, "end": v(40.18, 30.76) * mm});
            skLineSegment(sketch, "E423", {"start": v(40.18, 30.76) * mm, "end": v(40.21, 30.59) * mm});
            skLineSegment(sketch, "E424", {"start": v(40.21, 30.59) * mm, "end": v(40.25, 30.43) * mm});
            skLineSegment(sketch, "E425", {"start": v(40.25, 30.43) * mm, "end": v(40.3, 30.28) * mm});
            skLineSegment(sketch, "E426", {"start": v(40.3, 30.28) * mm, "end": v(40.34, 30.15) * mm});
            skLineSegment(sketch, "E427", {"start": v(40.34, 30.15) * mm, "end": v(40.4, 30.02) * mm});
            skLineSegment(sketch, "E428", {"start": v(40.4, 30.02) * mm, "end": v(40.44, 29.92) * mm});
            skLineSegment(sketch, "E429", {"start": v(40.44, 29.92) * mm, "end": v(40.5, 29.82) * mm});
            skLineSegment(sketch, "E430", {"start": v(40.5, 29.82) * mm, "end": v(40.54, 29.74) * mm});
            skLineSegment(sketch, "E431", {"start": v(40.54, 29.74) * mm, "end": v(40.59, 29.68) * mm});
            skLineSegment(sketch, "E432", {"start": v(40.59, 29.68) * mm, "end": v(40.63, 29.62) * mm});
            skLineSegment(sketch, "E433", {"start": v(40.63, 29.62) * mm, "end": v(40.67, 29.57) * mm});
            skLineSegment(sketch, "E434", {"start": v(40.67, 29.57) * mm, "end": v(40.7, 29.54) * mm});
            skLineSegment(sketch, "E435", {"start": v(40.7, 29.54) * mm, "end": v(40.72, 29.52) * mm});
            skLineSegment(sketch, "E436", {"start": v(40.72, 29.52) * mm, "end": v(40.74, 29.5) * mm});
            skLineSegment(sketch, "E437", {"start": v(40.74, 29.5) * mm, "end": v(40.75, 29.5) * mm});
            skLineSegment(sketch, "E438", {"start": v(40.75, 29.5) * mm, "end": v(41.86, 28.67) * mm});
            skLineSegment(sketch, "E439", {"start": v(41.86, 28.67) * mm, "end": v(41.26, 27.33) * mm});
            skLineSegment(sketch, "E440", {"start": v(41.26, 27.33) * mm, "end": v(39.9, 27.62) * mm});
            skLineSegment(sketch, "E441", {"start": v(39.9, 27.62) * mm, "end": v(39.9, 27.62) * mm});
            skLineSegment(sketch, "E442", {"start": v(39.9, 27.62) * mm, "end": v(39.88, 27.62) * mm});
            skLineSegment(sketch, "E443", {"start": v(39.88, 27.62) * mm, "end": v(39.84, 27.62) * mm});
            skLineSegment(sketch, "E444", {"start": v(39.84, 27.62) * mm, "end": v(39.8, 27.62) * mm});
            skLineSegment(sketch, "E445", {"start": v(39.8, 27.62) * mm, "end": v(39.74, 27.62) * mm});
            skLineSegment(sketch, "E446", {"start": v(39.74, 27.62) * mm, "end": v(39.67, 27.62) * mm});
            skLineSegment(sketch, "E447", {"start": v(39.67, 27.62) * mm, "end": v(39.59, 27.6) * mm});
            skLineSegment(sketch, "E448", {"start": v(39.59, 27.6) * mm, "end": v(39.5, 27.59) * mm});
            skLineSegment(sketch, "E449", {"start": v(39.5, 27.59) * mm, "end": v(39.39, 27.56) * mm});
            skLineSegment(sketch, "E450", {"start": v(39.39, 27.56) * mm, "end": v(39.28, 27.53) * mm});
            skLineSegment(sketch, "E451", {"start": v(39.28, 27.53) * mm, "end": v(39.15, 27.49) * mm});
            skLineSegment(sketch, "E452", {"start": v(39.15, 27.49) * mm, "end": v(39.02, 27.43) * mm});
            skLineSegment(sketch, "E453", {"start": v(39.02, 27.43) * mm, "end": v(38.88, 27.37) * mm});
            skLineSegment(sketch, "E454", {"start": v(38.88, 27.37) * mm, "end": v(38.73, 27.3) * mm});
            skLineSegment(sketch, "E455", {"start": v(38.73, 27.3) * mm, "end": v(38.58, 27.2) * mm});
            skLineSegment(sketch, "E456", {"start": v(38.58, 27.2) * mm, "end": v(38.42, 27.1) * mm});
            skLineSegment(sketch, "E457", {"start": v(38.42, 27.1) * mm, "end": v(38.26, 26.97) * mm});
            skLineSegment(sketch, "E458", {"start": v(38.26, 26.97) * mm, "end": v(38.1, 26.84) * mm});
            skLineSegment(sketch, "E459", {"start": v(38.1, 26.84) * mm, "end": v(38.03, 26.69) * mm});
            skLineSegment(sketch, "E460", {"start": v(38.03, 26.69) * mm, "end": v(38.04, 26.2) * mm});
            skLineSegment(sketch, "E461", {"start": v(38.04, 26.2) * mm, "end": v(38.11, 26.05) * mm});
            skLineSegment(sketch, "E462", {"start": v(38.11, 26.05) * mm, "end": v(38.29, 25.92) * mm});
            skLineSegment(sketch, "E463", {"start": v(38.29, 25.92) * mm, "end": v(38.46, 25.81) * mm});
            skLineSegment(sketch, "E464", {"start": v(38.46, 25.81) * mm, "end": v(38.62, 25.72) * mm});
            skLineSegment(sketch, "E465", {"start": v(38.62, 25.72) * mm, "end": v(38.78, 25.63) * mm});
            skLineSegment(sketch, "E466", {"start": v(38.78, 25.63) * mm, "end": v(38.93, 25.56) * mm});
            skLineSegment(sketch, "E467", {"start": v(38.93, 25.56) * mm, "end": v(39.07, 25.5) * mm});
            skLineSegment(sketch, "E468", {"start": v(39.07, 25.5) * mm, "end": v(39.2, 25.46) * mm});
            skLineSegment(sketch, "E469", {"start": v(39.2, 25.46) * mm, "end": v(39.33, 25.42) * mm});
            skLineSegment(sketch, "E470", {"start": v(39.33, 25.42) * mm, "end": v(39.45, 25.4) * mm});
            skLineSegment(sketch, "E471", {"start": v(39.45, 25.4) * mm, "end": v(39.55, 25.38) * mm});
            skLineSegment(sketch, "E472", {"start": v(39.55, 25.38) * mm, "end": v(39.65, 25.37) * mm});
            skLineSegment(sketch, "E473", {"start": v(39.65, 25.37) * mm, "end": v(39.73, 25.36) * mm});
            skLineSegment(sketch, "E474", {"start": v(39.73, 25.36) * mm, "end": v(39.8, 25.36) * mm});
            skLineSegment(sketch, "E475", {"start": v(39.8, 25.36) * mm, "end": v(39.86, 25.36) * mm});
            skLineSegment(sketch, "E476", {"start": v(39.86, 25.36) * mm, "end": v(39.9, 25.36) * mm});
            skLineSegment(sketch, "E477", {"start": v(39.9, 25.36) * mm, "end": v(39.94, 25.37) * mm});
            skLineSegment(sketch, "E478", {"start": v(39.94, 25.37) * mm, "end": v(39.96, 25.37) * mm});
            skLineSegment(sketch, "E479", {"start": v(39.96, 25.37) * mm, "end": v(39.97, 25.37) * mm});
            skLineSegment(sketch, "E480", {"start": v(39.97, 25.37) * mm, "end": v(41.3, 25.73) * mm});
            skLineSegment(sketch, "E481", {"start": v(41.3, 25.73) * mm, "end": v(41.98, 24.42) * mm});
            skLineSegment(sketch, "E482", {"start": v(41.98, 24.42) * mm, "end": v(40.91, 23.54) * mm});
            skLineSegment(sketch, "E483", {"start": v(40.91, 23.54) * mm, "end": v(40.9, 23.54) * mm});
            skLineSegment(sketch, "E484", {"start": v(40.9, 23.54) * mm, "end": v(40.9, 23.52) * mm});
            skLineSegment(sketch, "E485", {"start": v(40.9, 23.52) * mm, "end": v(40.87, 23.5) * mm});
            skLineSegment(sketch, "E486", {"start": v(40.87, 23.5) * mm, "end": v(40.84, 23.46) * mm});
            skLineSegment(sketch, "E487", {"start": v(40.84, 23.46) * mm, "end": v(40.8, 23.41) * mm});
            skLineSegment(sketch, "E488", {"start": v(40.8, 23.41) * mm, "end": v(40.76, 23.35) * mm});
            skLineSegment(sketch, "E489", {"start": v(40.76, 23.35) * mm, "end": v(40.72, 23.28) * mm});
            skLineSegment(sketch, "E490", {"start": v(40.72, 23.28) * mm, "end": v(40.68, 23.2) * mm});
            skLineSegment(sketch, "E491", {"start": v(40.68, 23.2) * mm, "end": v(40.63, 23.1) * mm});
            skLineSegment(sketch, "E492", {"start": v(40.63, 23.1) * mm, "end": v(40.59, 23) * mm});
            skLineSegment(sketch, "E493", {"start": v(40.59, 23) * mm, "end": v(40.54, 22.87) * mm});
            skLineSegment(sketch, "E494", {"start": v(40.54, 22.87) * mm, "end": v(40.5, 22.73) * mm});
            skLineSegment(sketch, "E495", {"start": v(40.5, 22.73) * mm, "end": v(40.47, 22.58) * mm});
            skLineSegment(sketch, "E496", {"start": v(40.47, 22.58) * mm, "end": v(40.44, 22.42) * mm});
            skLineSegment(sketch, "E497", {"start": v(40.44, 22.42) * mm, "end": v(40.41, 22.24) * mm});
            skLineSegment(sketch, "E498", {"start": v(40.41, 22.24) * mm, "end": v(40.4, 22.05) * mm});
            skLineSegment(sketch, "E499", {"start": v(40.4, 22.05) * mm, "end": v(40.39, 21.85) * mm});
            skLineSegment(sketch, "E500", {"start": v(40.39, 21.85) * mm, "end": v(40.39, 21.64) * mm});
            skLineSegment(sketch, "E501", {"start": v(40.39, 21.64) * mm, "end": v(40.47, 21.5) * mm});
            skLineSegment(sketch, "E502", {"start": v(40.47, 21.5) * mm, "end": v(40.86, 21.2) * mm});
            skLineSegment(sketch, "E503", {"start": v(40.86, 21.2) * mm, "end": v(41.02, 21.16) * mm});
            skLineSegment(sketch, "E504", {"start": v(41.02, 21.16) * mm, "end": v(41.23, 21.22) * mm});
            skLineSegment(sketch, "E505", {"start": v(41.23, 21.22) * mm, "end": v(41.42, 21.28) * mm});
            skLineSegment(sketch, "E506", {"start": v(41.42, 21.28) * mm, "end": v(41.6, 21.35) * mm});
            skLineSegment(sketch, "E507", {"start": v(41.6, 21.35) * mm, "end": v(41.76, 21.42) * mm});
            skLineSegment(sketch, "E508", {"start": v(41.76, 21.42) * mm, "end": v(41.9, 21.5) * mm});
            skLineSegment(sketch, "E509", {"start": v(41.9, 21.5) * mm, "end": v(42.04, 21.58) * mm});
            skLineSegment(sketch, "E510", {"start": v(42.04, 21.58) * mm, "end": v(42.16, 21.65) * mm});
            skLineSegment(sketch, "E511", {"start": v(42.16, 21.65) * mm, "end": v(42.27, 21.73) * mm});
            skLineSegment(sketch, "E512", {"start": v(42.27, 21.73) * mm, "end": v(42.36, 21.8) * mm});
            skLineSegment(sketch, "E513", {"start": v(42.36, 21.8) * mm, "end": v(42.44, 21.87) * mm});
            skLineSegment(sketch, "E514", {"start": v(42.44, 21.87) * mm, "end": v(42.51, 21.94) * mm});
            skLineSegment(sketch, "E515", {"start": v(42.51, 21.94) * mm, "end": v(42.57, 22) * mm});
            skLineSegment(sketch, "E516", {"start": v(42.57, 22) * mm, "end": v(42.61, 22.05) * mm});
            skLineSegment(sketch, "E517", {"start": v(42.61, 22.05) * mm, "end": v(42.65, 22.1) * mm});
            skLineSegment(sketch, "E518", {"start": v(42.65, 22.1) * mm, "end": v(42.67, 22.13) * mm});
            skLineSegment(sketch, "E519", {"start": v(42.67, 22.13) * mm, "end": v(42.7, 22.16) * mm});
            skLineSegment(sketch, "E520", {"start": v(42.7, 22.16) * mm, "end": v(42.7, 22.18) * mm});
            skLineSegment(sketch, "E521", {"start": v(42.7, 22.18) * mm, "end": v(42.7, 22.2) * mm});
            skLineSegment(sketch, "E522", {"start": v(42.7, 22.2) * mm, "end": v(43.26, 23.46) * mm});
            skLineSegment(sketch, "E523", {"start": v(43.26, 23.46) * mm, "end": v(44.7, 23.17) * mm});
            skLineSegment(sketch, "E524", {"start": v(44.7, 23.17) * mm, "end": v(44.72, 21.79) * mm});
            skLineSegment(sketch, "E525", {"start": v(44.72, 21.79) * mm, "end": v(44.73, 21.78) * mm});
            skLineSegment(sketch, "E526", {"start": v(44.73, 21.78) * mm, "end": v(44.73, 21.76) * mm});
            skLineSegment(sketch, "E527", {"start": v(44.73, 21.76) * mm, "end": v(44.73, 21.72) * mm});
            skLineSegment(sketch, "E528", {"start": v(44.73, 21.72) * mm, "end": v(44.74, 21.68) * mm});
            skLineSegment(sketch, "E529", {"start": v(44.74, 21.68) * mm, "end": v(44.76, 21.62) * mm});
            skLineSegment(sketch, "E530", {"start": v(44.76, 21.62) * mm, "end": v(44.78, 21.55) * mm});
            skLineSegment(sketch, "E531", {"start": v(44.78, 21.55) * mm, "end": v(44.8, 21.48) * mm});
            skLineSegment(sketch, "E532", {"start": v(44.8, 21.48) * mm, "end": v(44.85, 21.4) * mm});
            skLineSegment(sketch, "E533", {"start": v(44.85, 21.4) * mm, "end": v(44.9, 21.3) * mm});
            skLineSegment(sketch, "E534", {"start": v(44.9, 21.3) * mm, "end": v(44.95, 21.2) * mm});
            skLineSegment(sketch, "E535", {"start": v(44.95, 21.2) * mm, "end": v(45.02, 21.08) * mm});
            skLineSegment(sketch, "E536", {"start": v(45.02, 21.08) * mm, "end": v(45.1, 20.97) * mm});
            skLineSegment(sketch, "E537", {"start": v(45.1, 20.97) * mm, "end": v(45.2, 20.84) * mm});
            skLineSegment(sketch, "E538", {"start": v(45.2, 20.84) * mm, "end": v(45.3, 20.72) * mm});
            skLineSegment(sketch, "E539", {"start": v(45.3, 20.72) * mm, "end": v(45.43, 20.59) * mm});
            skLineSegment(sketch, "E540", {"start": v(45.43, 20.59) * mm, "end": v(45.57, 20.46) * mm});
            skLineSegment(sketch, "E541", {"start": v(45.57, 20.46) * mm, "end": v(45.72, 20.32) * mm});
            skLineSegment(sketch, "E542", {"start": v(45.72, 20.32) * mm, "end": v(45.89, 20.2) * mm});
            skLineSegment(sketch, "E543", {"start": v(45.89, 20.2) * mm, "end": v(46.05, 20.16) * mm});
            skLineSegment(sketch, "E544", {"start": v(46.05, 20.16) * mm, "end": v(46.52, 20.28) * mm});
            skLineSegment(sketch, "E545", {"start": v(46.52, 20.28) * mm, "end": v(46.65, 20.39) * mm});
            skLineSegment(sketch, "E546", {"start": v(46.65, 20.39) * mm, "end": v(46.74, 20.59) * mm});
            skLineSegment(sketch, "E547", {"start": v(46.74, 20.59) * mm, "end": v(46.8, 20.78) * mm});
            skLineSegment(sketch, "E548", {"start": v(46.8, 20.78) * mm, "end": v(46.87, 20.96) * mm});
            skLineSegment(sketch, "E549", {"start": v(46.87, 20.96) * mm, "end": v(46.91, 21.13) * mm});
            skLineSegment(sketch, "E550", {"start": v(46.91, 21.13) * mm, "end": v(46.94, 21.3) * mm});
            skLineSegment(sketch, "E551", {"start": v(46.94, 21.3) * mm, "end": v(46.97, 21.45) * mm});
            skLineSegment(sketch, "E552", {"start": v(46.97, 21.45) * mm, "end": v(46.98, 21.59) * mm});
            skLineSegment(sketch, "E553", {"start": v(46.98, 21.59) * mm, "end": v(47, 21.72) * mm});
            skLineSegment(sketch, "E554", {"start": v(47, 21.72) * mm, "end": v(47, 21.84) * mm});
            skLineSegment(sketch, "E555", {"start": v(47, 21.84) * mm, "end": v(46.99, 21.94) * mm});
            skLineSegment(sketch, "E556", {"start": v(46.99, 21.94) * mm, "end": v(46.98, 22.04) * mm});
            skLineSegment(sketch, "E557", {"start": v(46.98, 22.04) * mm, "end": v(46.97, 22.12) * mm});
            skLineSegment(sketch, "E558", {"start": v(46.97, 22.12) * mm, "end": v(46.95, 22.19) * mm});
            skLineSegment(sketch, "E559", {"start": v(46.95, 22.19) * mm, "end": v(46.94, 22.24) * mm});
            skLineSegment(sketch, "E560", {"start": v(46.94, 22.24) * mm, "end": v(46.92, 22.29) * mm});
            skLineSegment(sketch, "E561", {"start": v(46.92, 22.29) * mm, "end": v(46.91, 22.32) * mm});
            skLineSegment(sketch, "E562", {"start": v(46.91, 22.32) * mm, "end": v(46.9, 22.34) * mm});
            skLineSegment(sketch, "E563", {"start": v(46.9, 22.34) * mm, "end": v(46.9, 22.35) * mm});
            skLineSegment(sketch, "E564", {"start": v(46.9, 22.35) * mm, "end": v(46.25, 23.57) * mm});
            skLineSegment(sketch, "E565", {"start": v(46.25, 23.57) * mm, "end": v(47.38, 24.52) * mm});
            skLineSegment(sketch, "E566", {"start": v(47.38, 24.52) * mm, "end": v(48.47, 23.68) * mm});
            skLineSegment(sketch, "E567", {"start": v(48.47, 23.68) * mm, "end": v(48.48, 23.67) * mm});
            skLineSegment(sketch, "E568", {"start": v(48.48, 23.67) * mm, "end": v(48.5, 23.66) * mm});
            skLineSegment(sketch, "E569", {"start": v(48.5, 23.66) * mm, "end": v(48.53, 23.64) * mm});
            skLineSegment(sketch, "E570", {"start": v(48.53, 23.64) * mm, "end": v(48.57, 23.62) * mm});
            skLineSegment(sketch, "E571", {"start": v(48.57, 23.62) * mm, "end": v(48.62, 23.6) * mm});
            skLineSegment(sketch, "E572", {"start": v(48.62, 23.6) * mm, "end": v(48.7, 23.57) * mm});
            skLineSegment(sketch, "E573", {"start": v(48.7, 23.57) * mm, "end": v(48.77, 23.55) * mm});
            skLineSegment(sketch, "E574", {"start": v(48.77, 23.55) * mm, "end": v(48.86, 23.52) * mm});
            skLineSegment(sketch, "E575", {"start": v(48.86, 23.52) * mm, "end": v(48.96, 23.5) * mm});
            skLineSegment(sketch, "E576", {"start": v(48.96, 23.5) * mm, "end": v(49.08, 23.48) * mm});
            skLineSegment(sketch, "E577", {"start": v(49.08, 23.48) * mm, "end": v(49.21, 23.47) * mm});
            skLineSegment(sketch, "E578", {"start": v(49.21, 23.47) * mm, "end": v(49.35, 23.46) * mm});
            skLineSegment(sketch, "E579", {"start": v(49.35, 23.46) * mm, "end": v(49.5, 23.45) * mm});
            skLineSegment(sketch, "E580", {"start": v(49.5, 23.45) * mm, "end": v(49.67, 23.46) * mm});
            skLineSegment(sketch, "E581", {"start": v(49.67, 23.46) * mm, "end": v(49.85, 23.48) * mm});
            skLineSegment(sketch, "E582", {"start": v(49.85, 23.48) * mm, "end": v(50.04, 23.5) * mm});
            skLineSegment(sketch, "E583", {"start": v(50.04, 23.5) * mm, "end": v(50.24, 23.54) * mm});
            skLineSegment(sketch, "E584", {"start": v(50.24, 23.54) * mm, "end": v(50.45, 23.59) * mm});
            skLineSegment(sketch, "E585", {"start": v(50.45, 23.59) * mm, "end": v(50.57, 23.7) * mm});
            skLineSegment(sketch, "E586", {"start": v(50.57, 23.7) * mm, "end": v(50.77, 24.14) * mm});
            skLineSegment(sketch, "E587", {"start": v(50.77, 24.14) * mm, "end": v(50.77, 24.31) * mm});
            skLineSegment(sketch, "E588", {"start": v(21.43, -7.66) * mm, "end": v(21.45, -7.42) * mm});
            skLineSegment(sketch, "E589", {"start": v(21.45, -7.42) * mm, "end": v(21.5, -7.4) * mm});
            skLineSegment(sketch, "E590", {"start": v(21.5, -7.4) * mm, "end": v(21.56, -7.4) * mm});
            skLineSegment(sketch, "E591", {"start": v(21.56, -7.4) * mm, "end": v(21.62, -7.38) * mm});
            skLineSegment(sketch, "E592", {"start": v(21.62, -7.38) * mm, "end": v(21.68, -7.37) * mm});
            skLineSegment(sketch, "E593", {"start": v(21.68, -7.37) * mm, "end": v(21.75, -7.35) * mm});
            skLineSegment(sketch, "E594", {"start": v(21.75, -7.35) * mm, "end": v(21.8, -7.33) * mm});
            skLineSegment(sketch, "E595", {"start": v(21.8, -7.33) * mm, "end": v(21.87, -7.32) * mm});
            skLineSegment(sketch, "E596", {"start": v(21.87, -7.32) * mm, "end": v(21.94, -7.3) * mm});
            skLineSegment(sketch, "E597", {"start": v(21.94, -7.3) * mm, "end": v(22, -7.28) * mm});
            skLineSegment(sketch, "E598", {"start": v(22, -7.28) * mm, "end": v(22.07, -7.26) * mm});
            skLineSegment(sketch, "E599", {"start": v(22.07, -7.26) * mm, "end": v(22.14, -7.24) * mm});
            skLineSegment(sketch, "E600", {"start": v(22.14, -7.24) * mm, "end": v(22.21, -7.22) * mm});
            skLineSegment(sketch, "E601", {"start": v(22.21, -7.22) * mm, "end": v(22.28, -7.2) * mm});
            skLineSegment(sketch, "E602", {"start": v(22.28, -7.2) * mm, "end": v(22.36, -7.18) * mm});
            skLineSegment(sketch, "E603", {"start": v(22.36, -7.18) * mm, "end": v(22.43, -7.16) * mm});
            skLineSegment(sketch, "E604", {"start": v(22.43, -7.16) * mm, "end": v(22.5, -7.14) * mm});
            skLineSegment(sketch, "E605", {"start": v(22.5, -7.14) * mm, "end": v(22.58, -7.12) * mm});
            skLineSegment(sketch, "E606", {"start": v(22.58, -7.12) * mm, "end": v(22.66, -7.1) * mm});
            skLineSegment(sketch, "E607", {"start": v(22.66, -7.1) * mm, "end": v(22.73, -7.07) * mm});
            skLineSegment(sketch, "E608", {"start": v(22.73, -7.07) * mm, "end": v(22.81, -7.04) * mm});
            skLineSegment(sketch, "E609", {"start": v(22.81, -7.04) * mm, "end": v(22.89, -7.01) * mm});
            skLineSegment(sketch, "E610", {"start": v(22.89, -7.01) * mm, "end": v(22.97, -6.99) * mm});
            skLineSegment(sketch, "E611", {"start": v(22.97, -6.99) * mm, "end": v(23.05, -6.96) * mm});
            skLineSegment(sketch, "E612", {"start": v(23.05, -6.96) * mm, "end": v(23.13, -6.93) * mm});
            skLineSegment(sketch, "E613", {"start": v(23.13, -6.93) * mm, "end": v(23.22, -6.9) * mm});
            skLineSegment(sketch, "E614", {"start": v(23.22, -6.9) * mm, "end": v(23.3, -6.87) * mm});
            skLineSegment(sketch, "E615", {"start": v(23.3, -6.87) * mm, "end": v(23.39, -6.84) * mm});
            skLineSegment(sketch, "E616", {"start": v(23.39, -6.84) * mm, "end": v(23.47, -6.8) * mm});
            skLineSegment(sketch, "E617", {"start": v(23.47, -6.8) * mm, "end": v(23.56, -6.77) * mm});
            skLineSegment(sketch, "E618", {"start": v(23.56, -6.77) * mm, "end": v(23.65, -6.74) * mm});
            skLineSegment(sketch, "E619", {"start": v(23.65, -6.74) * mm, "end": v(23.74, -6.7) * mm});
            skLineSegment(sketch, "E620", {"start": v(23.74, -6.7) * mm, "end": v(23.83, -6.67) * mm});
            skLineSegment(sketch, "E621", {"start": v(23.83, -6.67) * mm, "end": v(23.92, -6.63) * mm});
            skLineSegment(sketch, "E622", {"start": v(23.92, -6.63) * mm, "end": v(24, -6.6) * mm});
            skLineSegment(sketch, "E623", {"start": v(24, -6.6) * mm, "end": v(24.1, -6.56) * mm});
            skLineSegment(sketch, "E624", {"start": v(24.1, -6.56) * mm, "end": v(24.2, -6.52) * mm});
            skLineSegment(sketch, "E625", {"start": v(24.2, -6.52) * mm, "end": v(24.3, -6.48) * mm});
            skLineSegment(sketch, "E626", {"start": v(24.3, -6.48) * mm, "end": v(24.39, -6.44) * mm});
            skLineSegment(sketch, "E627", {"start": v(24.39, -6.44) * mm, "end": v(24.48, -6.4) * mm});
            skLineSegment(sketch, "E628", {"start": v(24.48, -6.4) * mm, "end": v(24.58, -6.35) * mm});
            skLineSegment(sketch, "E629", {"start": v(24.58, -6.35) * mm, "end": v(24.6, -6.3) * mm});
            skLineSegment(sketch, "E630", {"start": v(24.6, -6.3) * mm, "end": v(24.6, -5.27) * mm});
            skLineSegment(sketch, "E631", {"start": v(24.6, -5.27) * mm, "end": v(24.57, -5.22) * mm});
            skLineSegment(sketch, "E632", {"start": v(24.57, -5.22) * mm, "end": v(24.47, -5.18) * mm});
            skLineSegment(sketch, "E633", {"start": v(24.47, -5.18) * mm, "end": v(24.37, -5.14) * mm});
            skLineSegment(sketch, "E634", {"start": v(24.37, -5.14) * mm, "end": v(24.27, -5.1) * mm});
            skLineSegment(sketch, "E635", {"start": v(24.27, -5.1) * mm, "end": v(24.18, -5.07) * mm});
            skLineSegment(sketch, "E636", {"start": v(24.18, -5.07) * mm, "end": v(24.08, -5.03) * mm});
            skLineSegment(sketch, "E637", {"start": v(24.08, -5.03) * mm, "end": v(23.99, -5) * mm});
            skLineSegment(sketch, "E638", {"start": v(23.99, -5) * mm, "end": v(23.9, -4.96) * mm});
            skLineSegment(sketch, "E639", {"start": v(23.9, -4.96) * mm, "end": v(23.8, -4.92) * mm});
            skLineSegment(sketch, "E640", {"start": v(23.8, -4.92) * mm, "end": v(23.71, -4.9) * mm});
            skLineSegment(sketch, "E641", {"start": v(23.71, -4.9) * mm, "end": v(23.62, -4.86) * mm});
            skLineSegment(sketch, "E642", {"start": v(23.62, -4.86) * mm, "end": v(23.54, -4.83) * mm});
            skLineSegment(sketch, "E643", {"start": v(23.54, -4.83) * mm, "end": v(23.45, -4.8) * mm});
            skLineSegment(sketch, "E644", {"start": v(23.45, -4.8) * mm, "end": v(23.36, -4.77) * mm});
            skLineSegment(sketch, "E645", {"start": v(23.36, -4.77) * mm, "end": v(23.28, -4.74) * mm});
            skLineSegment(sketch, "E646", {"start": v(23.28, -4.74) * mm, "end": v(23.19, -4.7) * mm});
            skLineSegment(sketch, "E647", {"start": v(23.19, -4.7) * mm, "end": v(23.1, -4.68) * mm});
            skLineSegment(sketch, "E648", {"start": v(23.1, -4.68) * mm, "end": v(23.02, -4.65) * mm});
            skLineSegment(sketch, "E649", {"start": v(23.02, -4.65) * mm, "end": v(22.94, -4.63) * mm});
            skLineSegment(sketch, "E650", {"start": v(22.94, -4.63) * mm, "end": v(22.86, -4.6) * mm});
            skLineSegment(sketch, "E651", {"start": v(22.86, -4.6) * mm, "end": v(22.78, -4.58) * mm});
            skLineSegment(sketch, "E652", {"start": v(22.78, -4.58) * mm, "end": v(22.7, -4.55) * mm});
            skLineSegment(sketch, "E653", {"start": v(22.7, -4.55) * mm, "end": v(22.62, -4.53) * mm});
            skLineSegment(sketch, "E654", {"start": v(22.62, -4.53) * mm, "end": v(22.55, -4.5) * mm});
            skLineSegment(sketch, "E655", {"start": v(22.55, -4.5) * mm, "end": v(22.47, -4.49) * mm});
            skLineSegment(sketch, "E656", {"start": v(22.47, -4.49) * mm, "end": v(22.4, -4.47) * mm});
            skLineSegment(sketch, "E657", {"start": v(22.4, -4.47) * mm, "end": v(22.32, -4.45) * mm});
            skLineSegment(sketch, "E658", {"start": v(22.32, -4.45) * mm, "end": v(22.25, -4.43) * mm});
            skLineSegment(sketch, "E659", {"start": v(22.25, -4.43) * mm, "end": v(22.18, -4.4) * mm});
            skLineSegment(sketch, "E660", {"start": v(22.18, -4.4) * mm, "end": v(22.1, -4.39) * mm});
            skLineSegment(sketch, "E661", {"start": v(22.1, -4.39) * mm, "end": v(22.04, -4.37) * mm});
            skLineSegment(sketch, "E662", {"start": v(22.04, -4.37) * mm, "end": v(21.97, -4.36) * mm});
            skLineSegment(sketch, "E663", {"start": v(21.97, -4.36) * mm, "end": v(21.9, -4.34) * mm});
            skLineSegment(sketch, "E664", {"start": v(21.9, -4.34) * mm, "end": v(21.84, -4.32) * mm});
            skLineSegment(sketch, "E665", {"start": v(21.84, -4.32) * mm, "end": v(21.77, -4.3) * mm});
            skLineSegment(sketch, "E666", {"start": v(21.77, -4.3) * mm, "end": v(21.7, -4.3) * mm});
            skLineSegment(sketch, "E667", {"start": v(21.7, -4.3) * mm, "end": v(21.65, -4.28) * mm});
            skLineSegment(sketch, "E668", {"start": v(21.65, -4.28) * mm, "end": v(21.58, -4.27) * mm});
            skLineSegment(sketch, "E669", {"start": v(21.58, -4.27) * mm, "end": v(21.52, -4.25) * mm});
            skLineSegment(sketch, "E670", {"start": v(21.52, -4.25) * mm, "end": v(21.46, -4.24) * mm});
            skLineSegment(sketch, "E671", {"start": v(21.46, -4.24) * mm, "end": v(21.4, -4.23) * mm});
            skLineSegment(sketch, "E672", {"start": v(21.4, -4.23) * mm, "end": v(21.39, -4) * mm});
            skLineSegment(sketch, "E673", {"start": v(21.39, -4) * mm, "end": v(21.34, -3.2) * mm});
            skLineSegment(sketch, "E674", {"start": v(21.34, -3.2) * mm, "end": v(21.33, -2.96) * mm});
            skLineSegment(sketch, "E675", {"start": v(21.33, -2.96) * mm, "end": v(21.39, -2.94) * mm});
            skLineSegment(sketch, "E676", {"start": v(21.39, -2.94) * mm, "end": v(21.45, -2.92) * mm});
            skLineSegment(sketch, "E677", {"start": v(21.45, -2.92) * mm, "end": v(21.5, -2.9) * mm});
            skLineSegment(sketch, "E678", {"start": v(21.5, -2.9) * mm, "end": v(21.57, -2.88) * mm});
            skLineSegment(sketch, "E679", {"start": v(21.57, -2.88) * mm, "end": v(21.63, -2.86) * mm});
            skLineSegment(sketch, "E680", {"start": v(21.63, -2.86) * mm, "end": v(21.69, -2.84) * mm});
            skLineSegment(sketch, "E681", {"start": v(21.69, -2.84) * mm, "end": v(21.75, -2.82) * mm});
            skLineSegment(sketch, "E682", {"start": v(21.75, -2.82) * mm, "end": v(21.82, -2.8) * mm});
            skLineSegment(sketch, "E683", {"start": v(21.82, -2.8) * mm, "end": v(21.88, -2.77) * mm});
            skLineSegment(sketch, "E684", {"start": v(21.88, -2.77) * mm, "end": v(21.95, -2.74) * mm});
            skLineSegment(sketch, "E685", {"start": v(21.95, -2.74) * mm, "end": v(22.01, -2.72) * mm});
            skLineSegment(sketch, "E686", {"start": v(22.01, -2.72) * mm, "end": v(22.08, -2.7) * mm});
            skLineSegment(sketch, "E687", {"start": v(22.08, -2.7) * mm, "end": v(22.15, -2.67) * mm});
            skLineSegment(sketch, "E688", {"start": v(22.15, -2.67) * mm, "end": v(22.22, -2.64) * mm});
            skLineSegment(sketch, "E689", {"start": v(22.22, -2.64) * mm, "end": v(22.3, -2.6) * mm});
            skLineSegment(sketch, "E690", {"start": v(22.3, -2.6) * mm, "end": v(22.36, -2.58) * mm});
            skLineSegment(sketch, "E691", {"start": v(22.36, -2.58) * mm, "end": v(22.44, -2.55) * mm});
            skLineSegment(sketch, "E692", {"start": v(22.44, -2.55) * mm, "end": v(22.5, -2.52) * mm});
            skLineSegment(sketch, "E693", {"start": v(22.5, -2.52) * mm, "end": v(22.58, -2.49) * mm});
            skLineSegment(sketch, "E694", {"start": v(22.58, -2.49) * mm, "end": v(22.66, -2.46) * mm});
            skLineSegment(sketch, "E695", {"start": v(22.66, -2.46) * mm, "end": v(22.74, -2.42) * mm});
            skLineSegment(sketch, "E696", {"start": v(22.74, -2.42) * mm, "end": v(22.81, -2.39) * mm});
            skLineSegment(sketch, "E697", {"start": v(22.81, -2.39) * mm, "end": v(22.9, -2.35) * mm});
            skLineSegment(sketch, "E698", {"start": v(22.9, -2.35) * mm, "end": v(22.97, -2.32) * mm});
            skLineSegment(sketch, "E699", {"start": v(22.97, -2.32) * mm, "end": v(23.05, -2.28) * mm});
            skLineSegment(sketch, "E700", {"start": v(23.05, -2.28) * mm, "end": v(23.13, -2.24) * mm});
            skLineSegment(sketch, "E701", {"start": v(23.13, -2.24) * mm, "end": v(23.21, -2.2) * mm});
            skLineSegment(sketch, "E702", {"start": v(23.21, -2.2) * mm, "end": v(23.3, -2.16) * mm});
            skLineSegment(sketch, "E703", {"start": v(23.3, -2.16) * mm, "end": v(23.38, -2.12) * mm});
            skLineSegment(sketch, "E704", {"start": v(23.38, -2.12) * mm, "end": v(23.47, -2.08) * mm});
            skLineSegment(sketch, "E705", {"start": v(23.47, -2.08) * mm, "end": v(23.55, -2.04) * mm});
            skLineSegment(sketch, "E706", {"start": v(23.55, -2.04) * mm, "end": v(23.64, -2) * mm});
            skLineSegment(sketch, "E707", {"start": v(23.64, -2) * mm, "end": v(23.73, -1.95) * mm});
            skLineSegment(sketch, "E708", {"start": v(23.73, -1.95) * mm, "end": v(23.81, -1.9) * mm});
            skLineSegment(sketch, "E709", {"start": v(23.81, -1.9) * mm, "end": v(23.9, -1.86) * mm});
            skLineSegment(sketch, "E710", {"start": v(23.9, -1.86) * mm, "end": v(24, -1.81) * mm});
            skLineSegment(sketch, "E711", {"start": v(24, -1.81) * mm, "end": v(24.08, -1.76) * mm});
            skLineSegment(sketch, "E712", {"start": v(24.08, -1.76) * mm, "end": v(24.17, -1.71) * mm});
            skLineSegment(sketch, "E713", {"start": v(24.17, -1.71) * mm, "end": v(24.27, -1.66) * mm});
            skLineSegment(sketch, "E714", {"start": v(24.27, -1.66) * mm, "end": v(24.36, -1.61) * mm});
            skLineSegment(sketch, "E715", {"start": v(24.36, -1.61) * mm, "end": v(24.38, -1.56) * mm});
            skLineSegment(sketch, "E716", {"start": v(24.38, -1.56) * mm, "end": v(24.27, -0.53) * mm});
            skLineSegment(sketch, "E717", {"start": v(24.27, -0.53) * mm, "end": v(24.24, -0.49) * mm});
            skLineSegment(sketch, "E718", {"start": v(24.24, -0.49) * mm, "end": v(24.14, -0.46) * mm});
            skLineSegment(sketch, "E719", {"start": v(24.14, -0.46) * mm, "end": v(24.04, -0.43) * mm});
            skLineSegment(sketch, "E720", {"start": v(24.04, -0.43) * mm, "end": v(23.94, -0.4) * mm});
            skLineSegment(sketch, "E721", {"start": v(23.94, -0.4) * mm, "end": v(23.84, -0.37) * mm});
            skLineSegment(sketch, "E722", {"start": v(23.84, -0.37) * mm, "end": v(23.75, -0.34) * mm});
            skLineSegment(sketch, "E723", {"start": v(23.75, -0.34) * mm, "end": v(23.65, -0.31) * mm});
            skLineSegment(sketch, "E724", {"start": v(23.65, -0.31) * mm, "end": v(23.55, -0.28) * mm});
            skLineSegment(sketch, "E725", {"start": v(23.55, -0.28) * mm, "end": v(23.46, -0.26) * mm});
            skLineSegment(sketch, "E726", {"start": v(23.46, -0.26) * mm, "end": v(23.37, -0.23) * mm});
            skLineSegment(sketch, "E727", {"start": v(23.37, -0.23) * mm, "end": v(23.27, -0.2) * mm});
            skLineSegment(sketch, "E728", {"start": v(23.27, -0.2) * mm, "end": v(23.18, -0.19) * mm});
            skLineSegment(sketch, "E729", {"start": v(23.18, -0.19) * mm, "end": v(23.1, -0.16) * mm});
            skLineSegment(sketch, "E730", {"start": v(23.1, -0.16) * mm, "end": v(23, -0.14) * mm});
            skLineSegment(sketch, "E731", {"start": v(23, -0.14) * mm, "end": v(22.92, -0.12) * mm});
            skLineSegment(sketch, "E732", {"start": v(22.92, -0.12) * mm, "end": v(22.83, -0.1) * mm});
            skLineSegment(sketch, "E733", {"start": v(22.83, -0.1) * mm, "end": v(22.74, -0.08) * mm});
            skLineSegment(sketch, "E734", {"start": v(22.74, -0.08) * mm, "end": v(22.66, -0.06) * mm});
            skLineSegment(sketch, "E735", {"start": v(22.66, -0.06) * mm, "end": v(22.57, -0.04) * mm});
            skLineSegment(sketch, "E736", {"start": v(22.57, -0.04) * mm, "end": v(22.5, -0.02) * mm});
            skLineSegment(sketch, "E737", {"start": v(22.5, -0.02) * mm, "end": v(22.4, 0) * mm});
            skLineSegment(sketch, "E738", {"start": v(22.4, 0) * mm, "end": v(22.33, 0.01) * mm});
            skLineSegment(sketch, "E739", {"start": v(22.33, 0.01) * mm, "end": v(22.25, 0.03) * mm});
            skLineSegment(sketch, "E740", {"start": v(22.25, 0.03) * mm, "end": v(22.17, 0.04) * mm});
            skLineSegment(sketch, "E741", {"start": v(22.17, 0.04) * mm, "end": v(22.1, 0.06) * mm});
            skLineSegment(sketch, "E742", {"start": v(22.1, 0.06) * mm, "end": v(22.02, 0.07) * mm});
            skLineSegment(sketch, "E743", {"start": v(22.02, 0.07) * mm, "end": v(21.94, 0.08) * mm});
            skLineSegment(sketch, "E744", {"start": v(21.94, 0.08) * mm, "end": v(21.87, 0.1) * mm});
            skLineSegment(sketch, "E745", {"start": v(21.87, 0.1) * mm, "end": v(21.8, 0.1) * mm});
            skLineSegment(sketch, "E746", {"start": v(21.8, 0.1) * mm, "end": v(21.72, 0.12) * mm});
            skLineSegment(sketch, "E747", {"start": v(21.72, 0.12) * mm, "end": v(21.65, 0.13) * mm});
            skLineSegment(sketch, "E748", {"start": v(21.65, 0.13) * mm, "end": v(21.58, 0.14) * mm});
            skLineSegment(sketch, "E749", {"start": v(21.58, 0.14) * mm, "end": v(21.51, 0.15) * mm});
            skLineSegment(sketch, "E750", {"start": v(21.51, 0.15) * mm, "end": v(21.45, 0.16) * mm});
            skLineSegment(sketch, "E751", {"start": v(21.45, 0.16) * mm, "end": v(21.38, 0.17) * mm});
            skLineSegment(sketch, "E752", {"start": v(21.38, 0.17) * mm, "end": v(21.32, 0.18) * mm});
            skLineSegment(sketch, "E753", {"start": v(21.32, 0.18) * mm, "end": v(21.25, 0.19) * mm});
            skLineSegment(sketch, "E754", {"start": v(21.25, 0.19) * mm, "end": v(21.19, 0.2) * mm});
            skLineSegment(sketch, "E755", {"start": v(21.19, 0.2) * mm, "end": v(21.13, 0.2) * mm});
            skLineSegment(sketch, "E756", {"start": v(21.13, 0.2) * mm, "end": v(21.07, 0.21) * mm});
            skLineSegment(sketch, "E757", {"start": v(21.07, 0.21) * mm, "end": v(21, 0.22) * mm});
            skLineSegment(sketch, "E758", {"start": v(21, 0.22) * mm, "end": v(20.97, 0.45) * mm});
            skLineSegment(sketch, "E759", {"start": v(20.97, 0.45) * mm, "end": v(20.85, 1.25) * mm});
            skLineSegment(sketch, "E760", {"start": v(20.85, 1.25) * mm, "end": v(20.82, 1.48) * mm});
            skLineSegment(sketch, "E761", {"start": v(20.82, 1.48) * mm, "end": v(20.88, 1.5) * mm});
            skLineSegment(sketch, "E762", {"start": v(20.88, 1.5) * mm, "end": v(20.93, 1.53) * mm});
            skLineSegment(sketch, "E763", {"start": v(20.93, 1.53) * mm, "end": v(20.99, 1.55) * mm});
            skLineSegment(sketch, "E764", {"start": v(20.99, 1.55) * mm, "end": v(21.05, 1.58) * mm});
            skLineSegment(sketch, "E765", {"start": v(21.05, 1.58) * mm, "end": v(21.1, 1.6) * mm});
            skLineSegment(sketch, "E766", {"start": v(21.1, 1.6) * mm, "end": v(21.17, 1.63) * mm});
            skLineSegment(sketch, "E767", {"start": v(21.17, 1.63) * mm, "end": v(21.23, 1.66) * mm});
            skLineSegment(sketch, "E768", {"start": v(21.23, 1.66) * mm, "end": v(21.29, 1.69) * mm});
            skLineSegment(sketch, "E769", {"start": v(21.29, 1.69) * mm, "end": v(21.35, 1.72) * mm});
            skLineSegment(sketch, "E770", {"start": v(21.35, 1.72) * mm, "end": v(21.41, 1.75) * mm});
            skLineSegment(sketch, "E771", {"start": v(21.41, 1.75) * mm, "end": v(21.48, 1.78) * mm});
            skLineSegment(sketch, "E772", {"start": v(21.48, 1.78) * mm, "end": v(21.54, 1.8) * mm});
            skLineSegment(sketch, "E773", {"start": v(21.54, 1.8) * mm, "end": v(21.6, 1.84) * mm});
            skLineSegment(sketch, "E774", {"start": v(21.6, 1.84) * mm, "end": v(21.68, 1.88) * mm});
            skLineSegment(sketch, "E775", {"start": v(21.68, 1.88) * mm, "end": v(21.74, 1.91) * mm});
            skLineSegment(sketch, "E776", {"start": v(21.74, 1.91) * mm, "end": v(21.81, 1.95) * mm});
            skLineSegment(sketch, "E777", {"start": v(21.81, 1.95) * mm, "end": v(21.88, 1.98) * mm});
            skLineSegment(sketch, "E778", {"start": v(21.88, 1.98) * mm, "end": v(21.95, 2.02) * mm});
            skLineSegment(sketch, "E779", {"start": v(21.95, 2.02) * mm, "end": v(22.03, 2.06) * mm});
            skLineSegment(sketch, "E780", {"start": v(22.03, 2.06) * mm, "end": v(22.1, 2.1) * mm});
            skLineSegment(sketch, "E781", {"start": v(22.1, 2.1) * mm, "end": v(22.17, 2.14) * mm});
            skLineSegment(sketch, "E782", {"start": v(22.17, 2.14) * mm, "end": v(22.24, 2.18) * mm});
            skLineSegment(sketch, "E783", {"start": v(22.24, 2.18) * mm, "end": v(22.32, 2.22) * mm});
            skLineSegment(sketch, "E784", {"start": v(22.32, 2.22) * mm, "end": v(22.4, 2.26) * mm});
            skLineSegment(sketch, "E785", {"start": v(22.4, 2.26) * mm, "end": v(22.47, 2.3) * mm});
            skLineSegment(sketch, "E786", {"start": v(22.47, 2.3) * mm, "end": v(22.55, 2.35) * mm});
            skLineSegment(sketch, "E787", {"start": v(22.55, 2.35) * mm, "end": v(22.63, 2.4) * mm});
            skLineSegment(sketch, "E788", {"start": v(22.63, 2.4) * mm, "end": v(22.7, 2.45) * mm});
            skLineSegment(sketch, "E789", {"start": v(22.7, 2.45) * mm, "end": v(22.79, 2.5) * mm});
            skLineSegment(sketch, "E790", {"start": v(22.79, 2.5) * mm, "end": v(22.87, 2.54) * mm});
            skLineSegment(sketch, "E791", {"start": v(22.87, 2.54) * mm, "end": v(22.95, 2.6) * mm});
            skLineSegment(sketch, "E792", {"start": v(22.95, 2.6) * mm, "end": v(23.03, 2.64) * mm});
            skLineSegment(sketch, "E793", {"start": v(23.03, 2.64) * mm, "end": v(23.11, 2.7) * mm});
            skLineSegment(sketch, "E794", {"start": v(23.11, 2.7) * mm, "end": v(23.2, 2.75) * mm});
            skLineSegment(sketch, "E795", {"start": v(23.2, 2.75) * mm, "end": v(23.28, 2.8) * mm});
            skLineSegment(sketch, "E796", {"start": v(23.28, 2.8) * mm, "end": v(23.37, 2.86) * mm});
            skLineSegment(sketch, "E797", {"start": v(23.37, 2.86) * mm, "end": v(23.45, 2.92) * mm});
            skLineSegment(sketch, "E798", {"start": v(23.45, 2.92) * mm, "end": v(23.54, 2.97) * mm});
            skLineSegment(sketch, "E799", {"start": v(23.54, 2.97) * mm, "end": v(23.63, 3.03) * mm});
            skLineSegment(sketch, "E800", {"start": v(23.63, 3.03) * mm, "end": v(23.72, 3.1) * mm});
            skLineSegment(sketch, "E801", {"start": v(23.72, 3.1) * mm, "end": v(23.73, 3.14) * mm});
            skLineSegment(sketch, "E802", {"start": v(23.73, 3.14) * mm, "end": v(23.53, 4.16) * mm});
            skLineSegment(sketch, "E803", {"start": v(23.53, 4.16) * mm, "end": v(23.5, 4.2) * mm});
            skLineSegment(sketch, "E804", {"start": v(23.5, 4.2) * mm, "end": v(23.4, 4.22) * mm});
            skLineSegment(sketch, "E805", {"start": v(23.4, 4.22) * mm, "end": v(23.3, 4.24) * mm});
            skLineSegment(sketch, "E806", {"start": v(23.3, 4.24) * mm, "end": v(23.2, 4.26) * mm});
            skLineSegment(sketch, "E807", {"start": v(23.2, 4.26) * mm, "end": v(23.1, 4.28) * mm});
            skLineSegment(sketch, "E808", {"start": v(23.1, 4.28) * mm, "end": v(23, 4.3) * mm});
            skLineSegment(sketch, "E809", {"start": v(23, 4.3) * mm, "end": v(22.9, 4.32) * mm});
            skLineSegment(sketch, "E810", {"start": v(22.9, 4.32) * mm, "end": v(22.8, 4.34) * mm});
            skLineSegment(sketch, "E811", {"start": v(22.8, 4.34) * mm, "end": v(22.7, 4.36) * mm});
            skLineSegment(sketch, "E812", {"start": v(22.7, 4.36) * mm, "end": v(22.6, 4.37) * mm});
            skLineSegment(sketch, "E813", {"start": v(22.6, 4.37) * mm, "end": v(22.5, 4.4) * mm});
            skLineSegment(sketch, "E814", {"start": v(22.5, 4.4) * mm, "end": v(22.42, 4.4) * mm});
            skLineSegment(sketch, "E815", {"start": v(22.42, 4.4) * mm, "end": v(22.32, 4.42) * mm});
            skLineSegment(sketch, "E816", {"start": v(22.32, 4.42) * mm, "end": v(22.23, 4.43) * mm});
            skLineSegment(sketch, "E817", {"start": v(22.23, 4.43) * mm, "end": v(22.14, 4.45) * mm});
            skLineSegment(sketch, "E818", {"start": v(22.14, 4.45) * mm, "end": v(22.05, 4.46) * mm});
            skLineSegment(sketch, "E819", {"start": v(22.05, 4.46) * mm, "end": v(21.97, 4.47) * mm});
            skLineSegment(sketch, "E820", {"start": v(21.97, 4.47) * mm, "end": v(21.88, 4.48) * mm});
            skLineSegment(sketch, "E821", {"start": v(21.88, 4.48) * mm, "end": v(21.8, 4.5) * mm});
            skLineSegment(sketch, "E822", {"start": v(21.8, 4.5) * mm, "end": v(21.71, 4.5) * mm});
            skLineSegment(sketch, "E823", {"start": v(21.71, 4.5) * mm, "end": v(21.63, 4.52) * mm});
            skLineSegment(sketch, "E824", {"start": v(21.63, 4.52) * mm, "end": v(21.55, 4.52) * mm});
            skLineSegment(sketch, "E825", {"start": v(21.55, 4.52) * mm, "end": v(21.47, 4.53) * mm});
            skLineSegment(sketch, "E826", {"start": v(21.47, 4.53) * mm, "end": v(21.39, 4.54) * mm});
            skLineSegment(sketch, "E827", {"start": v(21.39, 4.54) * mm, "end": v(21.3, 4.55) * mm});
            skLineSegment(sketch, "E828", {"start": v(21.3, 4.55) * mm, "end": v(21.23, 4.56) * mm});
            skLineSegment(sketch, "E829", {"start": v(21.23, 4.56) * mm, "end": v(21.15, 4.56) * mm});
            skLineSegment(sketch, "E830", {"start": v(21.15, 4.56) * mm, "end": v(21.08, 4.57) * mm});
            skLineSegment(sketch, "E831", {"start": v(21.08, 4.57) * mm, "end": v(21, 4.58) * mm});
            skLineSegment(sketch, "E832", {"start": v(21, 4.58) * mm, "end": v(20.93, 4.58) * mm});
            skLineSegment(sketch, "E833", {"start": v(20.93, 4.58) * mm, "end": v(20.86, 4.59) * mm});
            skLineSegment(sketch, "E834", {"start": v(20.86, 4.59) * mm, "end": v(20.8, 4.59) * mm});
            skLineSegment(sketch, "E835", {"start": v(20.8, 4.59) * mm, "end": v(20.72, 4.6) * mm});
            skLineSegment(sketch, "E836", {"start": v(20.72, 4.6) * mm, "end": v(20.66, 4.6) * mm});
            skLineSegment(sketch, "E837", {"start": v(20.66, 4.6) * mm, "end": v(20.59, 4.6) * mm});
            skLineSegment(sketch, "E838", {"start": v(20.59, 4.6) * mm, "end": v(20.52, 4.6) * mm});
            skLineSegment(sketch, "E839", {"start": v(20.52, 4.6) * mm, "end": v(20.46, 4.6) * mm});
            skLineSegment(sketch, "E840", {"start": v(20.46, 4.6) * mm, "end": v(20.4, 4.6) * mm});
            skLineSegment(sketch, "E841", {"start": v(20.4, 4.6) * mm, "end": v(20.33, 4.6) * mm});
            skLineSegment(sketch, "E842", {"start": v(20.33, 4.6) * mm, "end": v(20.27, 4.61) * mm});
            skLineSegment(sketch, "E843", {"start": v(20.27, 4.61) * mm, "end": v(20.21, 4.61) * mm});
            skLineSegment(sketch, "E844", {"start": v(20.21, 4.61) * mm, "end": v(20.15, 4.84) * mm});
            skLineSegment(sketch, "E845", {"start": v(20.15, 4.84) * mm, "end": v(19.96, 5.62) * mm});
            skLineSegment(sketch, "E846", {"start": v(19.96, 5.62) * mm, "end": v(19.91, 5.85) * mm});
            skLineSegment(sketch, "E847", {"start": v(19.91, 5.85) * mm, "end": v(19.97, 5.88) * mm});
            skLineSegment(sketch, "E848", {"start": v(19.97, 5.88) * mm, "end": v(20.02, 5.9) * mm});
            skLineSegment(sketch, "E849", {"start": v(20.02, 5.9) * mm, "end": v(20.07, 5.94) * mm});
            skLineSegment(sketch, "E850", {"start": v(20.07, 5.94) * mm, "end": v(20.13, 5.97) * mm});
            skLineSegment(sketch, "E851", {"start": v(20.13, 5.97) * mm, "end": v(20.19, 6) * mm});
            skLineSegment(sketch, "E852", {"start": v(20.19, 6) * mm, "end": v(20.24, 6.03) * mm});
            skLineSegment(sketch, "E853", {"start": v(20.24, 6.03) * mm, "end": v(20.3, 6.07) * mm});
            skLineSegment(sketch, "E854", {"start": v(20.3, 6.07) * mm, "end": v(20.36, 6.1) * mm});
            skLineSegment(sketch, "E855", {"start": v(20.36, 6.1) * mm, "end": v(20.42, 6.13) * mm});
            skLineSegment(sketch, "E856", {"start": v(20.42, 6.13) * mm, "end": v(20.48, 6.17) * mm});
            skLineSegment(sketch, "E857", {"start": v(20.48, 6.17) * mm, "end": v(20.54, 6.2) * mm});
            skLineSegment(sketch, "E858", {"start": v(20.54, 6.2) * mm, "end": v(20.6, 6.25) * mm});
            skLineSegment(sketch, "E859", {"start": v(20.6, 6.25) * mm, "end": v(20.67, 6.28) * mm});
            skLineSegment(sketch, "E860", {"start": v(20.67, 6.28) * mm, "end": v(20.73, 6.32) * mm});
            skLineSegment(sketch, "E861", {"start": v(20.73, 6.32) * mm, "end": v(20.8, 6.36) * mm});
            skLineSegment(sketch, "E862", {"start": v(20.8, 6.36) * mm, "end": v(20.86, 6.4) * mm});
            skLineSegment(sketch, "E863", {"start": v(20.86, 6.4) * mm, "end": v(20.93, 6.45) * mm});
            skLineSegment(sketch, "E864", {"start": v(20.93, 6.45) * mm, "end": v(21, 6.5) * mm});
            skLineSegment(sketch, "E865", {"start": v(21, 6.5) * mm, "end": v(21.06, 6.54) * mm});
            skLineSegment(sketch, "E866", {"start": v(21.06, 6.54) * mm, "end": v(21.13, 6.58) * mm});
            skLineSegment(sketch, "E867", {"start": v(21.13, 6.58) * mm, "end": v(21.2, 6.63) * mm});
            skLineSegment(sketch, "E868", {"start": v(21.2, 6.63) * mm, "end": v(21.27, 6.68) * mm});
            skLineSegment(sketch, "E869", {"start": v(21.27, 6.68) * mm, "end": v(21.34, 6.72) * mm});
            skLineSegment(sketch, "E870", {"start": v(21.34, 6.72) * mm, "end": v(21.41, 6.77) * mm});
            skLineSegment(sketch, "E871", {"start": v(21.41, 6.77) * mm, "end": v(21.48, 6.83) * mm});
            skLineSegment(sketch, "E872", {"start": v(21.48, 6.83) * mm, "end": v(21.56, 6.88) * mm});
            skLineSegment(sketch, "E873", {"start": v(21.56, 6.88) * mm, "end": v(21.63, 6.93) * mm});
            skLineSegment(sketch, "E874", {"start": v(21.63, 6.93) * mm, "end": v(21.7, 6.98) * mm});
            skLineSegment(sketch, "E875", {"start": v(21.7, 6.98) * mm, "end": v(21.78, 7.04) * mm});
            skLineSegment(sketch, "E876", {"start": v(21.78, 7.04) * mm, "end": v(21.86, 7.1) * mm});
            skLineSegment(sketch, "E877", {"start": v(21.86, 7.1) * mm, "end": v(21.93, 7.15) * mm});
            skLineSegment(sketch, "E878", {"start": v(21.93, 7.15) * mm, "end": v(22.01, 7.21) * mm});
            skLineSegment(sketch, "E879", {"start": v(22.01, 7.21) * mm, "end": v(22.09, 7.27) * mm});
            skLineSegment(sketch, "E880", {"start": v(22.09, 7.27) * mm, "end": v(22.17, 7.33) * mm});
            skLineSegment(sketch, "E881", {"start": v(22.17, 7.33) * mm, "end": v(22.25, 7.4) * mm});
            skLineSegment(sketch, "E882", {"start": v(22.25, 7.4) * mm, "end": v(22.33, 7.45) * mm});
            skLineSegment(sketch, "E883", {"start": v(22.33, 7.45) * mm, "end": v(22.4, 7.52) * mm});
            skLineSegment(sketch, "E884", {"start": v(22.4, 7.52) * mm, "end": v(22.49, 7.58) * mm});
            skLineSegment(sketch, "E885", {"start": v(22.49, 7.58) * mm, "end": v(22.57, 7.65) * mm});
            skLineSegment(sketch, "E886", {"start": v(22.57, 7.65) * mm, "end": v(22.65, 7.72) * mm});
            skLineSegment(sketch, "E887", {"start": v(22.65, 7.72) * mm, "end": v(22.66, 7.77) * mm});
            skLineSegment(sketch, "E888", {"start": v(22.66, 7.77) * mm, "end": v(22.38, 8.77) * mm});
            skLineSegment(sketch, "E889", {"start": v(22.38, 8.77) * mm, "end": v(22.34, 8.8) * mm});
            skLineSegment(sketch, "E890", {"start": v(22.34, 8.8) * mm, "end": v(22.23, 8.81) * mm});
            skLineSegment(sketch, "E891", {"start": v(22.23, 8.81) * mm, "end": v(22.13, 8.83) * mm});
            skLineSegment(sketch, "E892", {"start": v(22.13, 8.83) * mm, "end": v(22.03, 8.84) * mm});
            skLineSegment(sketch, "E893", {"start": v(22.03, 8.84) * mm, "end": v(21.92, 8.85) * mm});
            skLineSegment(sketch, "E894", {"start": v(21.92, 8.85) * mm, "end": v(21.82, 8.86) * mm});
            skLineSegment(sketch, "E895", {"start": v(21.82, 8.86) * mm, "end": v(21.72, 8.87) * mm});
            skLineSegment(sketch, "E896", {"start": v(21.72, 8.87) * mm, "end": v(21.62, 8.88) * mm});
            skLineSegment(sketch, "E897", {"start": v(21.62, 8.88) * mm, "end": v(21.53, 8.89) * mm});
            skLineSegment(sketch, "E898", {"start": v(21.53, 8.89) * mm, "end": v(21.43, 8.9) * mm});
            skLineSegment(sketch, "E899", {"start": v(21.43, 8.9) * mm, "end": v(21.33, 8.9) * mm});
            skLineSegment(sketch, "E900", {"start": v(21.33, 8.9) * mm, "end": v(21.24, 8.9) * mm});
            skLineSegment(sketch, "E901", {"start": v(21.24, 8.9) * mm, "end": v(21.15, 8.92) * mm});
            skLineSegment(sketch, "E902", {"start": v(21.15, 8.92) * mm, "end": v(21.06, 8.92) * mm});
            skLineSegment(sketch, "E903", {"start": v(21.06, 8.92) * mm, "end": v(20.96, 8.93) * mm});
            skLineSegment(sketch, "E904", {"start": v(20.96, 8.93) * mm, "end": v(20.88, 8.93) * mm});
            skLineSegment(sketch, "E905", {"start": v(20.88, 8.93) * mm, "end": v(20.79, 8.94) * mm});
            skLineSegment(sketch, "E906", {"start": v(20.79, 8.94) * mm, "end": v(20.7, 8.94) * mm});
            skLineSegment(sketch, "E907", {"start": v(20.7, 8.94) * mm, "end": v(20.61, 8.94) * mm});
            skLineSegment(sketch, "E908", {"start": v(20.61, 8.94) * mm, "end": v(20.53, 8.95) * mm});
            skLineSegment(sketch, "E909", {"start": v(20.53, 8.95) * mm, "end": v(20.45, 8.95) * mm});
            skLineSegment(sketch, "E910", {"start": v(20.45, 8.95) * mm, "end": v(20.36, 8.95) * mm});
            skLineSegment(sketch, "E911", {"start": v(20.36, 8.95) * mm, "end": v(20.28, 8.95) * mm});
            skLineSegment(sketch, "E912", {"start": v(20.28, 8.95) * mm, "end": v(20.2, 8.95) * mm});
            skLineSegment(sketch, "E913", {"start": v(20.2, 8.95) * mm, "end": v(20.12, 8.95) * mm});
            skLineSegment(sketch, "E914", {"start": v(20.12, 8.95) * mm, "end": v(20.05, 8.95) * mm});
            skLineSegment(sketch, "E915", {"start": v(20.05, 8.95) * mm, "end": v(19.97, 8.95) * mm});
            skLineSegment(sketch, "E916", {"start": v(19.97, 8.95) * mm, "end": v(19.9, 8.95) * mm});
            skLineSegment(sketch, "E917", {"start": v(19.9, 8.95) * mm, "end": v(19.82, 8.95) * mm});
            skLineSegment(sketch, "E918", {"start": v(19.82, 8.95) * mm, "end": v(19.75, 8.95) * mm});
            skLineSegment(sketch, "E919", {"start": v(19.75, 8.95) * mm, "end": v(19.68, 8.95) * mm});
            skLineSegment(sketch, "E920", {"start": v(19.68, 8.95) * mm, "end": v(19.6, 8.95) * mm});
            skLineSegment(sketch, "E921", {"start": v(19.6, 8.95) * mm, "end": v(19.54, 8.94) * mm});
            skLineSegment(sketch, "E922", {"start": v(19.54, 8.94) * mm, "end": v(19.47, 8.94) * mm});
            skLineSegment(sketch, "E923", {"start": v(19.47, 8.94) * mm, "end": v(19.4, 8.94) * mm});
            skLineSegment(sketch, "E924", {"start": v(19.4, 8.94) * mm, "end": v(19.34, 8.94) * mm});
            skLineSegment(sketch, "E925", {"start": v(19.34, 8.94) * mm, "end": v(19.27, 8.93) * mm});
            skLineSegment(sketch, "E926", {"start": v(19.27, 8.93) * mm, "end": v(19.2, 8.93) * mm});
            skLineSegment(sketch, "E927", {"start": v(19.2, 8.93) * mm, "end": v(19.15, 8.93) * mm});
            skLineSegment(sketch, "E928", {"start": v(19.15, 8.93) * mm, "end": v(19.09, 8.92) * mm});
            skLineSegment(sketch, "E929", {"start": v(19.09, 8.92) * mm, "end": v(19.03, 8.92) * mm});
            skLineSegment(sketch, "E930", {"start": v(19.03, 8.92) * mm, "end": v(18.95, 9.14) * mm});
            skLineSegment(sketch, "E931", {"start": v(18.95, 9.14) * mm, "end": v(18.69, 9.9) * mm});
            skLineSegment(sketch, "E932", {"start": v(18.69, 9.9) * mm, "end": v(18.62, 10.12) * mm});
            skLineSegment(sketch, "E933", {"start": v(18.62, 10.12) * mm, "end": v(18.67, 10.16) * mm});
            skLineSegment(sketch, "E934", {"start": v(18.67, 10.16) * mm, "end": v(18.72, 10.2) * mm});
            skLineSegment(sketch, "E935", {"start": v(18.72, 10.2) * mm, "end": v(18.77, 10.23) * mm});
            skLineSegment(sketch, "E936", {"start": v(18.77, 10.23) * mm, "end": v(18.82, 10.26) * mm});
            skLineSegment(sketch, "E937", {"start": v(18.82, 10.26) * mm, "end": v(18.88, 10.3) * mm});
            skLineSegment(sketch, "E938", {"start": v(18.88, 10.3) * mm, "end": v(18.93, 10.33) * mm});
            skLineSegment(sketch, "E939", {"start": v(18.93, 10.33) * mm, "end": v(18.98, 10.37) * mm});
            skLineSegment(sketch, "E940", {"start": v(18.98, 10.37) * mm, "end": v(19.04, 10.41) * mm});
            skLineSegment(sketch, "E941", {"start": v(19.04, 10.41) * mm, "end": v(19.1, 10.45) * mm});
            skLineSegment(sketch, "E942", {"start": v(19.1, 10.45) * mm, "end": v(19.15, 10.5) * mm});
            skLineSegment(sketch, "E943", {"start": v(19.15, 10.5) * mm, "end": v(19.21, 10.54) * mm});
            skLineSegment(sketch, "E944", {"start": v(19.21, 10.54) * mm, "end": v(19.27, 10.58) * mm});
            skLineSegment(sketch, "E945", {"start": v(19.27, 10.58) * mm, "end": v(19.33, 10.62) * mm});
            skLineSegment(sketch, "E946", {"start": v(19.33, 10.62) * mm, "end": v(19.39, 10.67) * mm});
            skLineSegment(sketch, "E947", {"start": v(19.39, 10.67) * mm, "end": v(19.45, 10.71) * mm});
            skLineSegment(sketch, "E948", {"start": v(19.45, 10.71) * mm, "end": v(19.51, 10.76) * mm});
            skLineSegment(sketch, "E949", {"start": v(19.51, 10.76) * mm, "end": v(19.57, 10.81) * mm});
            skLineSegment(sketch, "E950", {"start": v(19.57, 10.81) * mm, "end": v(19.64, 10.86) * mm});
            skLineSegment(sketch, "E951", {"start": v(19.64, 10.86) * mm, "end": v(19.7, 10.91) * mm});
            skLineSegment(sketch, "E952", {"start": v(19.7, 10.91) * mm, "end": v(19.76, 10.96) * mm});
            skLineSegment(sketch, "E953", {"start": v(19.76, 10.96) * mm, "end": v(19.83, 11.01) * mm});
            skLineSegment(sketch, "E954", {"start": v(19.83, 11.01) * mm, "end": v(19.9, 11.07) * mm});
            skLineSegment(sketch, "E955", {"start": v(19.9, 11.07) * mm, "end": v(19.96, 11.12) * mm});
            skLineSegment(sketch, "E956", {"start": v(19.96, 11.12) * mm, "end": v(20.03, 11.18) * mm});
            skLineSegment(sketch, "E957", {"start": v(20.03, 11.18) * mm, "end": v(20.1, 11.24) * mm});
            skLineSegment(sketch, "E958", {"start": v(20.1, 11.24) * mm, "end": v(20.16, 11.3) * mm});
            skLineSegment(sketch, "E959", {"start": v(20.16, 11.3) * mm, "end": v(20.23, 11.35) * mm});
            skLineSegment(sketch, "E960", {"start": v(20.23, 11.35) * mm, "end": v(20.3, 11.41) * mm});
            skLineSegment(sketch, "E961", {"start": v(20.3, 11.41) * mm, "end": v(20.37, 11.47) * mm});
            skLineSegment(sketch, "E962", {"start": v(20.37, 11.47) * mm, "end": v(20.44, 11.54) * mm});
            skLineSegment(sketch, "E963", {"start": v(20.44, 11.54) * mm, "end": v(20.51, 11.6) * mm});
            skLineSegment(sketch, "E964", {"start": v(20.51, 11.6) * mm, "end": v(20.58, 11.67) * mm});
            skLineSegment(sketch, "E965", {"start": v(20.58, 11.67) * mm, "end": v(20.66, 11.73) * mm});
            skLineSegment(sketch, "E966", {"start": v(20.66, 11.73) * mm, "end": v(20.73, 11.8) * mm});
            skLineSegment(sketch, "E967", {"start": v(20.73, 11.8) * mm, "end": v(20.8, 11.87) * mm});
            skLineSegment(sketch, "E968", {"start": v(20.8, 11.87) * mm, "end": v(20.88, 11.94) * mm});
            skLineSegment(sketch, "E969", {"start": v(20.88, 11.94) * mm, "end": v(20.95, 12) * mm});
            skLineSegment(sketch, "E970", {"start": v(20.95, 12) * mm, "end": v(21.03, 12.08) * mm});
            skLineSegment(sketch, "E971", {"start": v(21.03, 12.08) * mm, "end": v(21.1, 12.15) * mm});
            skLineSegment(sketch, "E972", {"start": v(21.1, 12.15) * mm, "end": v(21.18, 12.23) * mm});
            skLineSegment(sketch, "E973", {"start": v(21.18, 12.23) * mm, "end": v(21.19, 12.28) * mm});
            skLineSegment(sketch, "E974", {"start": v(21.19, 12.28) * mm, "end": v(20.8, 13.25) * mm});
            skLineSegment(sketch, "E975", {"start": v(20.8, 13.25) * mm, "end": v(20.77, 13.28) * mm});
            skLineSegment(sketch, "E976", {"start": v(20.77, 13.28) * mm, "end": v(20.66, 13.28) * mm});
            skLineSegment(sketch, "E977", {"start": v(20.66, 13.28) * mm, "end": v(20.56, 13.29) * mm});
            skLineSegment(sketch, "E978", {"start": v(20.56, 13.29) * mm, "end": v(20.45, 13.29) * mm});
            skLineSegment(sketch, "E979", {"start": v(20.45, 13.29) * mm, "end": v(20.35, 13.29) * mm});
            skLineSegment(sketch, "E980", {"start": v(20.35, 13.29) * mm, "end": v(20.25, 13.3) * mm});
            skLineSegment(sketch, "E981", {"start": v(20.25, 13.3) * mm, "end": v(20.15, 13.3) * mm});
            skLineSegment(sketch, "E982", {"start": v(20.15, 13.3) * mm, "end": v(20.05, 13.3) * mm});
            skLineSegment(sketch, "E983", {"start": v(20.05, 13.3) * mm, "end": v(19.95, 13.3) * mm});
            skLineSegment(sketch, "E984", {"start": v(19.95, 13.3) * mm, "end": v(19.86, 13.3) * mm});
            skLineSegment(sketch, "E985", {"start": v(19.86, 13.3) * mm, "end": v(19.76, 13.3) * mm});
            skLineSegment(sketch, "E986", {"start": v(19.76, 13.3) * mm, "end": v(19.66, 13.29) * mm});
            skLineSegment(sketch, "E987", {"start": v(19.66, 13.29) * mm, "end": v(19.57, 13.29) * mm});
            skLineSegment(sketch, "E988", {"start": v(19.57, 13.29) * mm, "end": v(19.48, 13.28) * mm});
            skLineSegment(sketch, "E989", {"start": v(19.48, 13.28) * mm, "end": v(19.39, 13.28) * mm});
            skLineSegment(sketch, "E990", {"start": v(19.39, 13.28) * mm, "end": v(19.3, 13.28) * mm});
            skLineSegment(sketch, "E991", {"start": v(19.3, 13.28) * mm, "end": v(19.21, 13.27) * mm});
            skLineSegment(sketch, "E992", {"start": v(19.21, 13.27) * mm, "end": v(19.12, 13.27) * mm});
            skLineSegment(sketch, "E993", {"start": v(19.12, 13.27) * mm, "end": v(19.04, 13.27) * mm});
            skLineSegment(sketch, "E994", {"start": v(19.04, 13.27) * mm, "end": v(18.95, 13.26) * mm});
            skLineSegment(sketch, "E995", {"start": v(18.95, 13.26) * mm, "end": v(18.87, 13.26) * mm});
            skLineSegment(sketch, "E996", {"start": v(18.87, 13.26) * mm, "end": v(18.79, 13.25) * mm});
            skLineSegment(sketch, "E997", {"start": v(18.79, 13.25) * mm, "end": v(18.7, 13.25) * mm});
            skLineSegment(sketch, "E998", {"start": v(18.7, 13.25) * mm, "end": v(18.63, 13.24) * mm});
            skLineSegment(sketch, "E999", {"start": v(18.63, 13.24) * mm, "end": v(18.55, 13.23) * mm});
            skLineSegment(sketch, "E1000", {"start": v(18.55, 13.23) * mm, "end": v(18.47, 13.23) * mm});
            skLineSegment(sketch, "E1001", {"start": v(18.47, 13.23) * mm, "end": v(18.4, 13.22) * mm});
            skLineSegment(sketch, "E1002", {"start": v(18.4, 13.22) * mm, "end": v(18.32, 13.21) * mm});
            skLineSegment(sketch, "E1003", {"start": v(18.32, 13.21) * mm, "end": v(18.25, 13.2) * mm});
            skLineSegment(sketch, "E1004", {"start": v(18.25, 13.2) * mm, "end": v(18.18, 13.2) * mm});
            skLineSegment(sketch, "E1005", {"start": v(18.18, 13.2) * mm, "end": v(18.1, 13.19) * mm});
            skLineSegment(sketch, "E1006", {"start": v(18.1, 13.19) * mm, "end": v(18.03, 13.18) * mm});
            skLineSegment(sketch, "E1007", {"start": v(18.03, 13.18) * mm, "end": v(17.97, 13.17) * mm});
            skLineSegment(sketch, "E1008", {"start": v(17.97, 13.17) * mm, "end": v(17.9, 13.16) * mm});
            skLineSegment(sketch, "E1009", {"start": v(17.9, 13.16) * mm, "end": v(17.83, 13.15) * mm});
            skLineSegment(sketch, "E1010", {"start": v(17.83, 13.15) * mm, "end": v(17.77, 13.15) * mm});
            skLineSegment(sketch, "E1011", {"start": v(17.77, 13.15) * mm, "end": v(17.7, 13.14) * mm});
            skLineSegment(sketch, "E1012", {"start": v(17.7, 13.14) * mm, "end": v(17.64, 13.13) * mm});
            skLineSegment(sketch, "E1013", {"start": v(17.64, 13.13) * mm, "end": v(17.58, 13.12) * mm});
            skLineSegment(sketch, "E1014", {"start": v(17.58, 13.12) * mm, "end": v(17.52, 13.1) * mm});
            skLineSegment(sketch, "E1015", {"start": v(17.52, 13.1) * mm, "end": v(17.46, 13.1) * mm});
            skLineSegment(sketch, "E1016", {"start": v(17.46, 13.1) * mm, "end": v(17.36, 13.3) * mm});
            skLineSegment(sketch, "E1017", {"start": v(17.36, 13.3) * mm, "end": v(17.03, 14.05) * mm});
            skLineSegment(sketch, "E1018", {"start": v(17.03, 14.05) * mm, "end": v(16.95, 14.26) * mm});
            skLineSegment(sketch, "E1019", {"start": v(16.95, 14.26) * mm, "end": v(17, 14.3) * mm});
            skLineSegment(sketch, "E1020", {"start": v(17, 14.3) * mm, "end": v(17.04, 14.34) * mm});
            skLineSegment(sketch, "E1021", {"start": v(17.04, 14.34) * mm, "end": v(17.09, 14.38) * mm});
            skLineSegment(sketch, "E1022", {"start": v(17.09, 14.38) * mm, "end": v(17.14, 14.42) * mm});
            skLineSegment(sketch, "E1023", {"start": v(17.14, 14.42) * mm, "end": v(17.19, 14.46) * mm});
            skLineSegment(sketch, "E1024", {"start": v(17.19, 14.46) * mm, "end": v(17.24, 14.5) * mm});
            skLineSegment(sketch, "E1025", {"start": v(17.24, 14.5) * mm, "end": v(17.29, 14.54) * mm});
            skLineSegment(sketch, "E1026", {"start": v(17.29, 14.54) * mm, "end": v(17.34, 14.59) * mm});
            skLineSegment(sketch, "E1027", {"start": v(17.34, 14.59) * mm, "end": v(17.4, 14.63) * mm});
            skLineSegment(sketch, "E1028", {"start": v(17.4, 14.63) * mm, "end": v(17.45, 14.68) * mm});
            skLineSegment(sketch, "E1029", {"start": v(17.45, 14.68) * mm, "end": v(17.5, 14.73) * mm});
            skLineSegment(sketch, "E1030", {"start": v(17.5, 14.73) * mm, "end": v(17.55, 14.78) * mm});
            skLineSegment(sketch, "E1031", {"start": v(17.55, 14.78) * mm, "end": v(17.6, 14.82) * mm});
            skLineSegment(sketch, "E1032", {"start": v(17.6, 14.82) * mm, "end": v(17.66, 14.88) * mm});
            skLineSegment(sketch, "E1033", {"start": v(17.66, 14.88) * mm, "end": v(17.72, 14.93) * mm});
            skLineSegment(sketch, "E1034", {"start": v(17.72, 14.93) * mm, "end": v(17.78, 14.98) * mm});
            skLineSegment(sketch, "E1035", {"start": v(17.78, 14.98) * mm, "end": v(17.83, 15.03) * mm});
            skLineSegment(sketch, "E1036", {"start": v(17.83, 15.03) * mm, "end": v(17.9, 15.09) * mm});
            skLineSegment(sketch, "E1037", {"start": v(17.9, 15.09) * mm, "end": v(17.95, 15.14) * mm});
            skLineSegment(sketch, "E1038", {"start": v(17.95, 15.14) * mm, "end": v(18.01, 15.2) * mm});
            skLineSegment(sketch, "E1039", {"start": v(18.01, 15.2) * mm, "end": v(18.07, 15.26) * mm});
            skLineSegment(sketch, "E1040", {"start": v(18.07, 15.26) * mm, "end": v(18.13, 15.32) * mm});
            skLineSegment(sketch, "E1041", {"start": v(18.13, 15.32) * mm, "end": v(18.2, 15.38) * mm});
            skLineSegment(sketch, "E1042", {"start": v(18.2, 15.38) * mm, "end": v(18.25, 15.44) * mm});
            skLineSegment(sketch, "E1043", {"start": v(18.25, 15.44) * mm, "end": v(18.32, 15.5) * mm});
            skLineSegment(sketch, "E1044", {"start": v(18.32, 15.5) * mm, "end": v(18.38, 15.57) * mm});
            skLineSegment(sketch, "E1045", {"start": v(18.38, 15.57) * mm, "end": v(18.44, 15.63) * mm});
            skLineSegment(sketch, "E1046", {"start": v(18.44, 15.63) * mm, "end": v(18.5, 15.7) * mm});
            skLineSegment(sketch, "E1047", {"start": v(18.5, 15.7) * mm, "end": v(18.57, 15.77) * mm});
            skLineSegment(sketch, "E1048", {"start": v(18.57, 15.77) * mm, "end": v(18.63, 15.84) * mm});
            skLineSegment(sketch, "E1049", {"start": v(18.63, 15.84) * mm, "end": v(18.7, 15.9) * mm});
            skLineSegment(sketch, "E1050", {"start": v(18.7, 15.9) * mm, "end": v(18.77, 15.98) * mm});
            skLineSegment(sketch, "E1051", {"start": v(18.77, 15.98) * mm, "end": v(18.83, 16.05) * mm});
            skLineSegment(sketch, "E1052", {"start": v(18.83, 16.05) * mm, "end": v(18.9, 16.12) * mm});
            skLineSegment(sketch, "E1053", {"start": v(18.9, 16.12) * mm, "end": v(18.97, 16.2) * mm});
            skLineSegment(sketch, "E1054", {"start": v(18.97, 16.2) * mm, "end": v(19.03, 16.27) * mm});
            skLineSegment(sketch, "E1055", {"start": v(19.03, 16.27) * mm, "end": v(19.1, 16.35) * mm});
            skLineSegment(sketch, "E1056", {"start": v(19.1, 16.35) * mm, "end": v(19.17, 16.43) * mm});
            skLineSegment(sketch, "E1057", {"start": v(19.17, 16.43) * mm, "end": v(19.24, 16.5) * mm});
            skLineSegment(sketch, "E1058", {"start": v(19.24, 16.5) * mm, "end": v(19.3, 16.59) * mm});
            skLineSegment(sketch, "E1059", {"start": v(19.3, 16.59) * mm, "end": v(19.3, 16.64) * mm});
            skLineSegment(sketch, "E1060", {"start": v(19.3, 16.64) * mm, "end": v(18.85, 17.57) * mm});
            skLineSegment(sketch, "E1061", {"start": v(18.85, 17.57) * mm, "end": v(18.8, 17.6) * mm});
            skLineSegment(sketch, "E1062", {"start": v(18.8, 17.6) * mm, "end": v(18.7, 17.6) * mm});
            skLineSegment(sketch, "E1063", {"start": v(18.7, 17.6) * mm, "end": v(18.6, 17.59) * mm});
            skLineSegment(sketch, "E1064", {"start": v(18.6, 17.59) * mm, "end": v(18.49, 17.58) * mm});
            skLineSegment(sketch, "E1065", {"start": v(18.49, 17.58) * mm, "end": v(18.39, 17.57) * mm});
            skLineSegment(sketch, "E1066", {"start": v(18.39, 17.57) * mm, "end": v(18.29, 17.56) * mm});
            skLineSegment(sketch, "E1067", {"start": v(18.29, 17.56) * mm, "end": v(18.19, 17.56) * mm});
            skLineSegment(sketch, "E1068", {"start": v(18.19, 17.56) * mm, "end": v(18.09, 17.55) * mm});
            skLineSegment(sketch, "E1069", {"start": v(18.09, 17.55) * mm, "end": v(17.99, 17.54) * mm});
            skLineSegment(sketch, "E1070", {"start": v(17.99, 17.54) * mm, "end": v(17.9, 17.53) * mm});
            skLineSegment(sketch, "E1071", {"start": v(17.9, 17.53) * mm, "end": v(17.8, 17.52) * mm});
            skLineSegment(sketch, "E1072", {"start": v(17.8, 17.52) * mm, "end": v(17.7, 17.51) * mm});
            skLineSegment(sketch, "E1073", {"start": v(17.7, 17.51) * mm, "end": v(17.61, 17.5) * mm});
            skLineSegment(sketch, "E1074", {"start": v(17.61, 17.5) * mm, "end": v(17.52, 17.49) * mm});
            skLineSegment(sketch, "E1075", {"start": v(17.52, 17.49) * mm, "end": v(17.43, 17.48) * mm});
            skLineSegment(sketch, "E1076", {"start": v(17.43, 17.48) * mm, "end": v(17.34, 17.47) * mm});
            skLineSegment(sketch, "E1077", {"start": v(17.34, 17.47) * mm, "end": v(17.25, 17.46) * mm});
            skLineSegment(sketch, "E1078", {"start": v(17.25, 17.46) * mm, "end": v(17.17, 17.44) * mm});
            skLineSegment(sketch, "E1079", {"start": v(17.17, 17.44) * mm, "end": v(17.08, 17.43) * mm});
            skLineSegment(sketch, "E1080", {"start": v(17.08, 17.43) * mm, "end": v(17, 17.42) * mm});
            skLineSegment(sketch, "E1081", {"start": v(17, 17.42) * mm, "end": v(16.92, 17.4) * mm});
            skLineSegment(sketch, "E1082", {"start": v(16.92, 17.4) * mm, "end": v(16.83, 17.4) * mm});
            skLineSegment(sketch, "E1083", {"start": v(16.83, 17.4) * mm, "end": v(16.75, 17.38) * mm});
            skLineSegment(sketch, "E1084", {"start": v(16.75, 17.38) * mm, "end": v(16.68, 17.37) * mm});
            skLineSegment(sketch, "E1085", {"start": v(16.68, 17.37) * mm, "end": v(16.6, 17.35) * mm});
            skLineSegment(sketch, "E1086", {"start": v(16.6, 17.35) * mm, "end": v(16.52, 17.34) * mm});
            skLineSegment(sketch, "E1087", {"start": v(16.52, 17.34) * mm, "end": v(16.45, 17.33) * mm});
            skLineSegment(sketch, "E1088", {"start": v(16.45, 17.33) * mm, "end": v(16.37, 17.31) * mm});
            skLineSegment(sketch, "E1089", {"start": v(16.37, 17.31) * mm, "end": v(16.3, 17.3) * mm});
            skLineSegment(sketch, "E1090", {"start": v(16.3, 17.3) * mm, "end": v(16.23, 17.28) * mm});
            skLineSegment(sketch, "E1091", {"start": v(16.23, 17.28) * mm, "end": v(16.16, 17.27) * mm});
            skLineSegment(sketch, "E1092", {"start": v(16.16, 17.27) * mm, "end": v(16.09, 17.26) * mm});
            skLineSegment(sketch, "E1093", {"start": v(16.09, 17.26) * mm, "end": v(16.02, 17.24) * mm});
            skLineSegment(sketch, "E1094", {"start": v(16.02, 17.24) * mm, "end": v(15.96, 17.23) * mm});
            skLineSegment(sketch, "E1095", {"start": v(15.96, 17.23) * mm, "end": v(15.9, 17.21) * mm});
            skLineSegment(sketch, "E1096", {"start": v(15.9, 17.21) * mm, "end": v(15.83, 17.2) * mm});
            skLineSegment(sketch, "E1097", {"start": v(15.83, 17.2) * mm, "end": v(15.76, 17.18) * mm});
            skLineSegment(sketch, "E1098", {"start": v(15.76, 17.18) * mm, "end": v(15.7, 17.17) * mm});
            skLineSegment(sketch, "E1099", {"start": v(15.7, 17.17) * mm, "end": v(15.64, 17.15) * mm});
            skLineSegment(sketch, "E1100", {"start": v(15.64, 17.15) * mm, "end": v(15.58, 17.14) * mm});
            skLineSegment(sketch, "E1101", {"start": v(15.58, 17.14) * mm, "end": v(15.53, 17.12) * mm});
            skLineSegment(sketch, "E1102", {"start": v(15.53, 17.12) * mm, "end": v(15.4, 17.32) * mm});
            skLineSegment(sketch, "E1103", {"start": v(15.4, 17.32) * mm, "end": v(15.02, 18.03) * mm});
            skLineSegment(sketch, "E1104", {"start": v(15.02, 18.03) * mm, "end": v(14.9, 18.24) * mm});
            skLineSegment(sketch, "E1105", {"start": v(14.9, 18.24) * mm, "end": v(14.95, 18.28) * mm});
            skLineSegment(sketch, "E1106", {"start": v(14.95, 18.28) * mm, "end": v(15, 18.32) * mm});
            skLineSegment(sketch, "E1107", {"start": v(15, 18.32) * mm, "end": v(15.04, 18.36) * mm});
            skLineSegment(sketch, "E1108", {"start": v(15.04, 18.36) * mm, "end": v(15.09, 18.4) * mm});
            skLineSegment(sketch, "E1109", {"start": v(15.09, 18.4) * mm, "end": v(15.13, 18.45) * mm});
            skLineSegment(sketch, "E1110", {"start": v(15.13, 18.45) * mm, "end": v(15.18, 18.5) * mm});
            skLineSegment(sketch, "E1111", {"start": v(15.18, 18.5) * mm, "end": v(15.22, 18.55) * mm});
            skLineSegment(sketch, "E1112", {"start": v(15.22, 18.55) * mm, "end": v(15.27, 18.6) * mm});
            skLineSegment(sketch, "E1113", {"start": v(15.27, 18.6) * mm, "end": v(15.32, 18.65) * mm});
            skLineSegment(sketch, "E1114", {"start": v(15.32, 18.65) * mm, "end": v(15.37, 18.7) * mm});
            skLineSegment(sketch, "E1115", {"start": v(15.37, 18.7) * mm, "end": v(15.42, 18.75) * mm});
            skLineSegment(sketch, "E1116", {"start": v(15.42, 18.75) * mm, "end": v(15.47, 18.8) * mm});
            skLineSegment(sketch, "E1117", {"start": v(15.47, 18.8) * mm, "end": v(15.52, 18.86) * mm});
            skLineSegment(sketch, "E1118", {"start": v(15.52, 18.86) * mm, "end": v(15.57, 18.91) * mm});
            skLineSegment(sketch, "E1119", {"start": v(15.57, 18.91) * mm, "end": v(15.62, 18.97) * mm});
            skLineSegment(sketch, "E1120", {"start": v(15.62, 18.97) * mm, "end": v(15.67, 19.02) * mm});
            skLineSegment(sketch, "E1121", {"start": v(15.67, 19.02) * mm, "end": v(15.72, 19.08) * mm});
            skLineSegment(sketch, "E1122", {"start": v(15.72, 19.08) * mm, "end": v(15.78, 19.14) * mm});
            skLineSegment(sketch, "E1123", {"start": v(15.78, 19.14) * mm, "end": v(15.83, 19.2) * mm});
            skLineSegment(sketch, "E1124", {"start": v(15.83, 19.2) * mm, "end": v(15.89, 19.27) * mm});
            skLineSegment(sketch, "E1125", {"start": v(15.89, 19.27) * mm, "end": v(15.94, 19.33) * mm});
            skLineSegment(sketch, "E1126", {"start": v(15.94, 19.33) * mm, "end": v(16, 19.4) * mm});
            skLineSegment(sketch, "E1127", {"start": v(16, 19.4) * mm, "end": v(16.05, 19.46) * mm});
            skLineSegment(sketch, "E1128", {"start": v(16.05, 19.46) * mm, "end": v(16.1, 19.53) * mm});
            skLineSegment(sketch, "E1129", {"start": v(16.1, 19.53) * mm, "end": v(16.16, 19.6) * mm});
            skLineSegment(sketch, "E1130", {"start": v(16.16, 19.6) * mm, "end": v(16.22, 19.66) * mm});
            skLineSegment(sketch, "E1131", {"start": v(16.22, 19.66) * mm, "end": v(16.28, 19.73) * mm});
            skLineSegment(sketch, "E1132", {"start": v(16.28, 19.73) * mm, "end": v(16.33, 19.8) * mm});
            skLineSegment(sketch, "E1133", {"start": v(16.33, 19.8) * mm, "end": v(16.4, 19.88) * mm});
            skLineSegment(sketch, "E1134", {"start": v(16.4, 19.88) * mm, "end": v(16.45, 19.95) * mm});
            skLineSegment(sketch, "E1135", {"start": v(16.45, 19.95) * mm, "end": v(16.5, 20.03) * mm});
            skLineSegment(sketch, "E1136", {"start": v(16.5, 20.03) * mm, "end": v(16.57, 20.1) * mm});
            skLineSegment(sketch, "E1137", {"start": v(16.57, 20.1) * mm, "end": v(16.63, 20.18) * mm});
            skLineSegment(sketch, "E1138", {"start": v(16.63, 20.18) * mm, "end": v(16.69, 20.26) * mm});
            skLineSegment(sketch, "E1139", {"start": v(16.69, 20.26) * mm, "end": v(16.75, 20.34) * mm});
            skLineSegment(sketch, "E1140", {"start": v(16.75, 20.34) * mm, "end": v(16.8, 20.43) * mm});
            skLineSegment(sketch, "E1141", {"start": v(16.8, 20.43) * mm, "end": v(16.87, 20.5) * mm});
            skLineSegment(sketch, "E1142", {"start": v(16.87, 20.5) * mm, "end": v(16.93, 20.6) * mm});
            skLineSegment(sketch, "E1143", {"start": v(16.93, 20.6) * mm, "end": v(16.99, 20.68) * mm});
            skLineSegment(sketch, "E1144", {"start": v(16.99, 20.68) * mm, "end": v(17.05, 20.77) * mm});
            skLineSegment(sketch, "E1145", {"start": v(17.05, 20.77) * mm, "end": v(17.05, 20.82) * mm});
            skLineSegment(sketch, "E1146", {"start": v(17.05, 20.82) * mm, "end": v(16.5, 21.7) * mm});
            skLineSegment(sketch, "E1147", {"start": v(16.5, 21.7) * mm, "end": v(16.46, 21.73) * mm});
            skLineSegment(sketch, "E1148", {"start": v(16.46, 21.73) * mm, "end": v(16.36, 21.71) * mm});
            skLineSegment(sketch, "E1149", {"start": v(16.36, 21.71) * mm, "end": v(16.25, 21.7) * mm});
            skLineSegment(sketch, "E1150", {"start": v(16.25, 21.7) * mm, "end": v(16.15, 21.68) * mm});
            skLineSegment(sketch, "E1151", {"start": v(16.15, 21.68) * mm, "end": v(16.05, 21.66) * mm});
            skLineSegment(sketch, "E1152", {"start": v(16.05, 21.66) * mm, "end": v(15.95, 21.65) * mm});
            skLineSegment(sketch, "E1153", {"start": v(15.95, 21.65) * mm, "end": v(15.85, 21.63) * mm});
            skLineSegment(sketch, "E1154", {"start": v(15.85, 21.63) * mm, "end": v(15.75, 21.61) * mm});
            skLineSegment(sketch, "E1155", {"start": v(15.75, 21.61) * mm, "end": v(15.65, 21.6) * mm});
            skLineSegment(sketch, "E1156", {"start": v(15.65, 21.6) * mm, "end": v(15.56, 21.58) * mm});
            skLineSegment(sketch, "E1157", {"start": v(15.56, 21.58) * mm, "end": v(15.47, 21.56) * mm});
            skLineSegment(sketch, "E1158", {"start": v(15.47, 21.56) * mm, "end": v(15.37, 21.54) * mm});
            skLineSegment(sketch, "E1159", {"start": v(15.37, 21.54) * mm, "end": v(15.28, 21.52) * mm});
            skLineSegment(sketch, "E1160", {"start": v(15.28, 21.52) * mm, "end": v(15.2, 21.5) * mm});
            skLineSegment(sketch, "E1161", {"start": v(15.2, 21.5) * mm, "end": v(15.1, 21.48) * mm});
            skLineSegment(sketch, "E1162", {"start": v(15.1, 21.48) * mm, "end": v(15.01, 21.46) * mm});
            skLineSegment(sketch, "E1163", {"start": v(15.01, 21.46) * mm, "end": v(14.93, 21.44) * mm});
            skLineSegment(sketch, "E1164", {"start": v(14.93, 21.44) * mm, "end": v(14.84, 21.42) * mm});
            skLineSegment(sketch, "E1165", {"start": v(14.84, 21.42) * mm, "end": v(14.76, 21.4) * mm});
            skLineSegment(sketch, "E1166", {"start": v(14.76, 21.4) * mm, "end": v(14.68, 21.38) * mm});
            skLineSegment(sketch, "E1167", {"start": v(14.68, 21.38) * mm, "end": v(14.6, 21.36) * mm});
            skLineSegment(sketch, "E1168", {"start": v(14.6, 21.36) * mm, "end": v(14.52, 21.34) * mm});
            skLineSegment(sketch, "E1169", {"start": v(14.52, 21.34) * mm, "end": v(14.44, 21.32) * mm});
            skLineSegment(sketch, "E1170", {"start": v(14.44, 21.32) * mm, "end": v(14.36, 21.3) * mm});
            skLineSegment(sketch, "E1171", {"start": v(14.36, 21.3) * mm, "end": v(14.28, 21.28) * mm});
            skLineSegment(sketch, "E1172", {"start": v(14.28, 21.28) * mm, "end": v(14.2, 21.26) * mm});
            skLineSegment(sketch, "E1173", {"start": v(14.2, 21.26) * mm, "end": v(14.14, 21.24) * mm});
            skLineSegment(sketch, "E1174", {"start": v(14.14, 21.24) * mm, "end": v(14.06, 21.22) * mm});
            skLineSegment(sketch, "E1175", {"start": v(14.06, 21.22) * mm, "end": v(14, 21.2) * mm});
            skLineSegment(sketch, "E1176", {"start": v(14, 21.2) * mm, "end": v(13.92, 21.18) * mm});
            skLineSegment(sketch, "E1177", {"start": v(13.92, 21.18) * mm, "end": v(13.85, 21.16) * mm});
            skLineSegment(sketch, "E1178", {"start": v(13.85, 21.16) * mm, "end": v(13.79, 21.14) * mm});
            skLineSegment(sketch, "E1179", {"start": v(13.79, 21.14) * mm, "end": v(13.72, 21.12) * mm});
            skLineSegment(sketch, "E1180", {"start": v(13.72, 21.12) * mm, "end": v(13.66, 21.1) * mm});
            skLineSegment(sketch, "E1181", {"start": v(13.66, 21.1) * mm, "end": v(13.6, 21.08) * mm});
            skLineSegment(sketch, "E1182", {"start": v(13.6, 21.08) * mm, "end": v(13.53, 21.06) * mm});
            skLineSegment(sketch, "E1183", {"start": v(13.53, 21.06) * mm, "end": v(13.47, 21.04) * mm});
            skLineSegment(sketch, "E1184", {"start": v(13.47, 21.04) * mm, "end": v(13.41, 21.02) * mm});
            skLineSegment(sketch, "E1185", {"start": v(13.41, 21.02) * mm, "end": v(13.35, 21) * mm});
            skLineSegment(sketch, "E1186", {"start": v(13.35, 21) * mm, "end": v(13.3, 20.98) * mm});
            skLineSegment(sketch, "E1187", {"start": v(13.3, 20.98) * mm, "end": v(13.24, 20.96) * mm});
            skLineSegment(sketch, "E1188", {"start": v(13.24, 20.96) * mm, "end": v(13.1, 21.15) * mm});
            skLineSegment(sketch, "E1189", {"start": v(13.1, 21.15) * mm, "end": v(12.65, 21.82) * mm});
            skLineSegment(sketch, "E1190", {"start": v(12.65, 21.82) * mm, "end": v(12.52, 22.01) * mm});
            skLineSegment(sketch, "E1191", {"start": v(12.52, 22.01) * mm, "end": v(12.56, 22.06) * mm});
            skLineSegment(sketch, "E1192", {"start": v(12.56, 22.06) * mm, "end": v(12.6, 22.1) * mm});
            skLineSegment(sketch, "E1193", {"start": v(12.6, 22.1) * mm, "end": v(12.64, 22.15) * mm});
            skLineSegment(sketch, "E1194", {"start": v(12.64, 22.15) * mm, "end": v(12.68, 22.2) * mm});
            skLineSegment(sketch, "E1195", {"start": v(12.68, 22.2) * mm, "end": v(12.72, 22.25) * mm});
            skLineSegment(sketch, "E1196", {"start": v(12.72, 22.25) * mm, "end": v(12.77, 22.3) * mm});
            skLineSegment(sketch, "E1197", {"start": v(12.77, 22.3) * mm, "end": v(12.8, 22.35) * mm});
            skLineSegment(sketch, "E1198", {"start": v(12.8, 22.35) * mm, "end": v(12.85, 22.4) * mm});
            skLineSegment(sketch, "E1199", {"start": v(12.85, 22.4) * mm, "end": v(12.9, 22.46) * mm});
            skLineSegment(sketch, "E1200", {"start": v(12.9, 22.46) * mm, "end": v(12.94, 22.51) * mm});
            skLineSegment(sketch, "E1201", {"start": v(12.94, 22.51) * mm, "end": v(12.98, 22.57) * mm});
            skLineSegment(sketch, "E1202", {"start": v(12.98, 22.57) * mm, "end": v(13.03, 22.62) * mm});
            skLineSegment(sketch, "E1203", {"start": v(13.03, 22.62) * mm, "end": v(13.07, 22.68) * mm});
            skLineSegment(sketch, "E1204", {"start": v(13.07, 22.68) * mm, "end": v(13.12, 22.74) * mm});
            skLineSegment(sketch, "E1205", {"start": v(13.12, 22.74) * mm, "end": v(13.17, 22.8) * mm});
            skLineSegment(sketch, "E1206", {"start": v(13.17, 22.8) * mm, "end": v(13.21, 22.86) * mm});
            skLineSegment(sketch, "E1207", {"start": v(13.21, 22.86) * mm, "end": v(13.26, 22.93) * mm});
            skLineSegment(sketch, "E1208", {"start": v(13.26, 22.93) * mm, "end": v(13.3, 23) * mm});
            skLineSegment(sketch, "E1209", {"start": v(13.3, 23) * mm, "end": v(13.36, 23.06) * mm});
            skLineSegment(sketch, "E1210", {"start": v(13.36, 23.06) * mm, "end": v(13.4, 23.12) * mm});
            skLineSegment(sketch, "E1211", {"start": v(13.4, 23.12) * mm, "end": v(13.45, 23.2) * mm});
            skLineSegment(sketch, "E1212", {"start": v(13.45, 23.2) * mm, "end": v(13.5, 23.26) * mm});
            skLineSegment(sketch, "E1213", {"start": v(13.5, 23.26) * mm, "end": v(13.55, 23.33) * mm});
            skLineSegment(sketch, "E1214", {"start": v(13.55, 23.33) * mm, "end": v(13.6, 23.4) * mm});
            skLineSegment(sketch, "E1215", {"start": v(13.6, 23.4) * mm, "end": v(13.65, 23.48) * mm});
            skLineSegment(sketch, "E1216", {"start": v(13.65, 23.48) * mm, "end": v(13.7, 23.55) * mm});
            skLineSegment(sketch, "E1217", {"start": v(13.7, 23.55) * mm, "end": v(13.75, 23.63) * mm});
            skLineSegment(sketch, "E1218", {"start": v(13.75, 23.63) * mm, "end": v(13.8, 23.7) * mm});
            skLineSegment(sketch, "E1219", {"start": v(13.8, 23.7) * mm, "end": v(13.85, 23.78) * mm});
            skLineSegment(sketch, "E1220", {"start": v(13.85, 23.78) * mm, "end": v(13.9, 23.86) * mm});
            skLineSegment(sketch, "E1221", {"start": v(13.9, 23.86) * mm, "end": v(13.96, 23.94) * mm});
            skLineSegment(sketch, "E1222", {"start": v(13.96, 23.94) * mm, "end": v(14, 24.02) * mm});
            skLineSegment(sketch, "E1223", {"start": v(14, 24.02) * mm, "end": v(14.06, 24.1) * mm});
            skLineSegment(sketch, "E1224", {"start": v(14.06, 24.1) * mm, "end": v(14.11, 24.19) * mm});
            skLineSegment(sketch, "E1225", {"start": v(14.11, 24.19) * mm, "end": v(14.16, 24.27) * mm});
            skLineSegment(sketch, "E1226", {"start": v(14.16, 24.27) * mm, "end": v(14.22, 24.36) * mm});
            skLineSegment(sketch, "E1227", {"start": v(14.22, 24.36) * mm, "end": v(14.27, 24.45) * mm});
            skLineSegment(sketch, "E1228", {"start": v(14.27, 24.45) * mm, "end": v(14.32, 24.54) * mm});
            skLineSegment(sketch, "E1229", {"start": v(14.32, 24.54) * mm, "end": v(14.38, 24.63) * mm});
            skLineSegment(sketch, "E1230", {"start": v(14.38, 24.63) * mm, "end": v(14.43, 24.72) * mm});
            skLineSegment(sketch, "E1231", {"start": v(14.43, 24.72) * mm, "end": v(14.42, 24.77) * mm});
            skLineSegment(sketch, "E1232", {"start": v(14.42, 24.77) * mm, "end": v(13.8, 25.6) * mm});
            skLineSegment(sketch, "E1233", {"start": v(13.8, 25.6) * mm, "end": v(13.76, 25.63) * mm});
            skLineSegment(sketch, "E1234", {"start": v(13.76, 25.63) * mm, "end": v(13.65, 25.6) * mm});
            skLineSegment(sketch, "E1235", {"start": v(13.65, 25.6) * mm, "end": v(13.55, 25.58) * mm});
            skLineSegment(sketch, "E1236", {"start": v(13.55, 25.58) * mm, "end": v(13.45, 25.55) * mm});
            skLineSegment(sketch, "E1237", {"start": v(13.45, 25.55) * mm, "end": v(13.35, 25.53) * mm});
            skLineSegment(sketch, "E1238", {"start": v(13.35, 25.53) * mm, "end": v(13.25, 25.5) * mm});
            skLineSegment(sketch, "E1239", {"start": v(13.25, 25.5) * mm, "end": v(13.15, 25.47) * mm});
            skLineSegment(sketch, "E1240", {"start": v(13.15, 25.47) * mm, "end": v(13.06, 25.45) * mm});
            skLineSegment(sketch, "E1241", {"start": v(13.06, 25.45) * mm, "end": v(12.96, 25.42) * mm});
            skLineSegment(sketch, "E1242", {"start": v(12.96, 25.42) * mm, "end": v(12.87, 25.4) * mm});
            skLineSegment(sketch, "E1243", {"start": v(12.87, 25.4) * mm, "end": v(12.78, 25.37) * mm});
            skLineSegment(sketch, "E1244", {"start": v(12.78, 25.37) * mm, "end": v(12.69, 25.34) * mm});
            skLineSegment(sketch, "E1245", {"start": v(12.69, 25.34) * mm, "end": v(12.6, 25.32) * mm});
            skLineSegment(sketch, "E1246", {"start": v(12.6, 25.32) * mm, "end": v(12.51, 25.29) * mm});
            skLineSegment(sketch, "E1247", {"start": v(12.51, 25.29) * mm, "end": v(12.43, 25.26) * mm});
            skLineSegment(sketch, "E1248", {"start": v(12.43, 25.26) * mm, "end": v(12.34, 25.23) * mm});
            skLineSegment(sketch, "E1249", {"start": v(12.34, 25.23) * mm, "end": v(12.26, 25.2) * mm});
            skLineSegment(sketch, "E1250", {"start": v(12.26, 25.2) * mm, "end": v(12.17, 25.18) * mm});
            skLineSegment(sketch, "E1251", {"start": v(12.17, 25.18) * mm, "end": v(12.1, 25.15) * mm});
            skLineSegment(sketch, "E1252", {"start": v(12.1, 25.15) * mm, "end": v(12.01, 25.13) * mm});
            skLineSegment(sketch, "E1253", {"start": v(12.01, 25.13) * mm, "end": v(11.93, 25.1) * mm});
            skLineSegment(sketch, "E1254", {"start": v(11.93, 25.1) * mm, "end": v(11.85, 25.07) * mm});
            skLineSegment(sketch, "E1255", {"start": v(11.85, 25.07) * mm, "end": v(11.78, 25.04) * mm});
            skLineSegment(sketch, "E1256", {"start": v(11.78, 25.04) * mm, "end": v(11.7, 25.02) * mm});
            skLineSegment(sketch, "E1257", {"start": v(11.7, 25.02) * mm, "end": v(11.63, 25) * mm});
            skLineSegment(sketch, "E1258", {"start": v(11.63, 25) * mm, "end": v(11.56, 24.96) * mm});
            skLineSegment(sketch, "E1259", {"start": v(11.56, 24.96) * mm, "end": v(11.48, 24.94) * mm});
            skLineSegment(sketch, "E1260", {"start": v(11.48, 24.94) * mm, "end": v(11.41, 24.9) * mm});
            skLineSegment(sketch, "E1261", {"start": v(11.41, 24.9) * mm, "end": v(11.35, 24.88) * mm});
            skLineSegment(sketch, "E1262", {"start": v(11.35, 24.88) * mm, "end": v(11.28, 24.86) * mm});
            skLineSegment(sketch, "E1263", {"start": v(11.28, 24.86) * mm, "end": v(11.21, 24.83) * mm});
            skLineSegment(sketch, "E1264", {"start": v(11.21, 24.83) * mm, "end": v(11.15, 24.8) * mm});
            skLineSegment(sketch, "E1265", {"start": v(11.15, 24.8) * mm, "end": v(11.08, 24.78) * mm});
            skLineSegment(sketch, "E1266", {"start": v(11.08, 24.78) * mm, "end": v(11.02, 24.75) * mm});
            skLineSegment(sketch, "E1267", {"start": v(11.02, 24.75) * mm, "end": v(10.96, 24.72) * mm});
            skLineSegment(sketch, "E1268", {"start": v(10.96, 24.72) * mm, "end": v(10.9, 24.7) * mm});
            skLineSegment(sketch, "E1269", {"start": v(10.9, 24.7) * mm, "end": v(10.84, 24.67) * mm});
            skLineSegment(sketch, "E1270", {"start": v(10.84, 24.67) * mm, "end": v(10.78, 24.65) * mm});
            skLineSegment(sketch, "E1271", {"start": v(10.78, 24.65) * mm, "end": v(10.72, 24.62) * mm});
            skLineSegment(sketch, "E1272", {"start": v(10.72, 24.62) * mm, "end": v(10.67, 24.6) * mm});
            skLineSegment(sketch, "E1273", {"start": v(10.67, 24.6) * mm, "end": v(10.62, 24.57) * mm});
            skLineSegment(sketch, "E1274", {"start": v(10.62, 24.57) * mm, "end": v(10.46, 24.75) * mm});
            skLineSegment(sketch, "E1275", {"start": v(10.46, 24.75) * mm, "end": v(9.95, 25.37) * mm});
            skLineSegment(sketch, "E1276", {"start": v(9.95, 25.37) * mm, "end": v(9.8, 25.56) * mm});
            skLineSegment(sketch, "E1277", {"start": v(9.8, 25.56) * mm, "end": v(9.84, 25.6) * mm});
            skLineSegment(sketch, "E1278", {"start": v(9.84, 25.6) * mm, "end": v(9.88, 25.66) * mm});
            skLineSegment(sketch, "E1279", {"start": v(9.88, 25.66) * mm, "end": v(9.92, 25.7) * mm});
            skLineSegment(sketch, "E1280", {"start": v(9.92, 25.7) * mm, "end": v(9.95, 25.76) * mm});
            skLineSegment(sketch, "E1281", {"start": v(9.95, 25.76) * mm, "end": v(9.99, 25.81) * mm});
            skLineSegment(sketch, "E1282", {"start": v(9.99, 25.81) * mm, "end": v(10.03, 25.86) * mm});
            skLineSegment(sketch, "E1283", {"start": v(10.03, 25.86) * mm, "end": v(10.06, 25.92) * mm});
            skLineSegment(sketch, "E1284", {"start": v(10.06, 25.92) * mm, "end": v(10.1, 25.98) * mm});
            skLineSegment(sketch, "E1285", {"start": v(10.1, 25.98) * mm, "end": v(10.14, 26.03) * mm});
            skLineSegment(sketch, "E1286", {"start": v(10.14, 26.03) * mm, "end": v(10.18, 26.1) * mm});
            skLineSegment(sketch, "E1287", {"start": v(10.18, 26.1) * mm, "end": v(10.22, 26.15) * mm});
            skLineSegment(sketch, "E1288", {"start": v(10.22, 26.15) * mm, "end": v(10.26, 26.21) * mm});
            skLineSegment(sketch, "E1289", {"start": v(10.26, 26.21) * mm, "end": v(10.3, 26.28) * mm});
            skLineSegment(sketch, "E1290", {"start": v(10.3, 26.28) * mm, "end": v(10.34, 26.34) * mm});
            skLineSegment(sketch, "E1291", {"start": v(10.34, 26.34) * mm, "end": v(10.38, 26.4) * mm});
            skLineSegment(sketch, "E1292", {"start": v(10.38, 26.4) * mm, "end": v(10.42, 26.47) * mm});
            skLineSegment(sketch, "E1293", {"start": v(10.42, 26.47) * mm, "end": v(10.46, 26.54) * mm});
            skLineSegment(sketch, "E1294", {"start": v(10.46, 26.54) * mm, "end": v(10.5, 26.6) * mm});
            skLineSegment(sketch, "E1295", {"start": v(10.5, 26.6) * mm, "end": v(10.54, 26.67) * mm});
            skLineSegment(sketch, "E1296", {"start": v(10.54, 26.67) * mm, "end": v(10.59, 26.74) * mm});
            skLineSegment(sketch, "E1297", {"start": v(10.59, 26.74) * mm, "end": v(10.63, 26.82) * mm});
            skLineSegment(sketch, "E1298", {"start": v(10.63, 26.82) * mm, "end": v(10.67, 26.9) * mm});
            skLineSegment(sketch, "E1299", {"start": v(10.67, 26.9) * mm, "end": v(10.71, 26.96) * mm});
            skLineSegment(sketch, "E1300", {"start": v(10.71, 26.96) * mm, "end": v(10.76, 27.04) * mm});
            skLineSegment(sketch, "E1301", {"start": v(10.76, 27.04) * mm, "end": v(10.8, 27.12) * mm});
            skLineSegment(sketch, "E1302", {"start": v(10.8, 27.12) * mm, "end": v(10.84, 27.2) * mm});
            skLineSegment(sketch, "E1303", {"start": v(10.84, 27.2) * mm, "end": v(10.89, 27.28) * mm});
            skLineSegment(sketch, "E1304", {"start": v(10.89, 27.28) * mm, "end": v(10.93, 27.36) * mm});
            skLineSegment(sketch, "E1305", {"start": v(10.93, 27.36) * mm, "end": v(10.97, 27.44) * mm});
            skLineSegment(sketch, "E1306", {"start": v(10.97, 27.44) * mm, "end": v(11.02, 27.52) * mm});
            skLineSegment(sketch, "E1307", {"start": v(11.02, 27.52) * mm, "end": v(11.06, 27.6) * mm});
            skLineSegment(sketch, "E1308", {"start": v(11.06, 27.6) * mm, "end": v(11.1, 27.7) * mm});
            skLineSegment(sketch, "E1309", {"start": v(11.1, 27.7) * mm, "end": v(11.15, 27.78) * mm});
            skLineSegment(sketch, "E1310", {"start": v(11.15, 27.78) * mm, "end": v(11.2, 27.87) * mm});
            skLineSegment(sketch, "E1311", {"start": v(11.2, 27.87) * mm, "end": v(11.24, 27.96) * mm});
            skLineSegment(sketch, "E1312", {"start": v(11.24, 27.96) * mm, "end": v(11.29, 28.05) * mm});
            skLineSegment(sketch, "E1313", {"start": v(11.29, 28.05) * mm, "end": v(11.33, 28.14) * mm});
            skLineSegment(sketch, "E1314", {"start": v(11.33, 28.14) * mm, "end": v(11.38, 28.24) * mm});
            skLineSegment(sketch, "E1315", {"start": v(11.38, 28.24) * mm, "end": v(11.42, 28.33) * mm});
            skLineSegment(sketch, "E1316", {"start": v(11.42, 28.33) * mm, "end": v(11.46, 28.43) * mm});
            skLineSegment(sketch, "E1317", {"start": v(11.46, 28.43) * mm, "end": v(11.45, 28.48) * mm});
            skLineSegment(sketch, "E1318", {"start": v(11.45, 28.48) * mm, "end": v(10.76, 29.25) * mm});
            skLineSegment(sketch, "E1319", {"start": v(10.76, 29.25) * mm, "end": v(10.71, 29.27) * mm});
            skLineSegment(sketch, "E1320", {"start": v(10.71, 29.27) * mm, "end": v(10.61, 29.23) * mm});
            skLineSegment(sketch, "E1321", {"start": v(10.61, 29.23) * mm, "end": v(10.51, 29.2) * mm});
            skLineSegment(sketch, "E1322", {"start": v(10.51, 29.2) * mm, "end": v(10.41, 29.17) * mm});
            skLineSegment(sketch, "E1323", {"start": v(10.41, 29.17) * mm, "end": v(10.32, 29.13) * mm});
            skLineSegment(sketch, "E1324", {"start": v(10.32, 29.13) * mm, "end": v(10.22, 29.1) * mm});
            skLineSegment(sketch, "E1325", {"start": v(10.22, 29.1) * mm, "end": v(10.13, 29.06) * mm});
            skLineSegment(sketch, "E1326", {"start": v(10.13, 29.06) * mm, "end": v(10.03, 29.03) * mm});
            skLineSegment(sketch, "E1327", {"start": v(10.03, 29.03) * mm, "end": v(9.94, 29) * mm});
            skLineSegment(sketch, "E1328", {"start": v(9.94, 29) * mm, "end": v(9.85, 28.96) * mm});
            skLineSegment(sketch, "E1329", {"start": v(9.85, 28.96) * mm, "end": v(9.76, 28.92) * mm});
            skLineSegment(sketch, "E1330", {"start": v(9.76, 28.92) * mm, "end": v(9.68, 28.89) * mm});
            skLineSegment(sketch, "E1331", {"start": v(9.68, 28.89) * mm, "end": v(9.59, 28.85) * mm});
            skLineSegment(sketch, "E1332", {"start": v(9.59, 28.85) * mm, "end": v(9.5, 28.82) * mm});
            skLineSegment(sketch, "E1333", {"start": v(9.5, 28.82) * mm, "end": v(9.42, 28.79) * mm});
            skLineSegment(sketch, "E1334", {"start": v(9.42, 28.79) * mm, "end": v(9.34, 28.75) * mm});
            skLineSegment(sketch, "E1335", {"start": v(9.34, 28.75) * mm, "end": v(9.26, 28.72) * mm});
            skLineSegment(sketch, "E1336", {"start": v(9.26, 28.72) * mm, "end": v(9.18, 28.68) * mm});
            skLineSegment(sketch, "E1337", {"start": v(9.18, 28.68) * mm, "end": v(9.1, 28.65) * mm});
            skLineSegment(sketch, "E1338", {"start": v(9.1, 28.65) * mm, "end": v(9.02, 28.61) * mm});
            skLineSegment(sketch, "E1339", {"start": v(9.02, 28.61) * mm, "end": v(8.94, 28.58) * mm});
            skLineSegment(sketch, "E1340", {"start": v(8.94, 28.58) * mm, "end": v(8.87, 28.55) * mm});
            skLineSegment(sketch, "E1341", {"start": v(8.87, 28.55) * mm, "end": v(8.8, 28.51) * mm});
            skLineSegment(sketch, "E1342", {"start": v(8.8, 28.51) * mm, "end": v(8.72, 28.48) * mm});
            skLineSegment(sketch, "E1343", {"start": v(8.72, 28.48) * mm, "end": v(8.65, 28.44) * mm});
            skLineSegment(sketch, "E1344", {"start": v(8.65, 28.44) * mm, "end": v(8.58, 28.41) * mm});
            skLineSegment(sketch, "E1345", {"start": v(8.58, 28.41) * mm, "end": v(8.51, 28.38) * mm});
            skLineSegment(sketch, "E1346", {"start": v(8.51, 28.38) * mm, "end": v(8.44, 28.34) * mm});
            skLineSegment(sketch, "E1347", {"start": v(8.44, 28.34) * mm, "end": v(8.38, 28.31) * mm});
            skLineSegment(sketch, "E1348", {"start": v(8.38, 28.31) * mm, "end": v(8.31, 28.28) * mm});
            skLineSegment(sketch, "E1349", {"start": v(8.31, 28.28) * mm, "end": v(8.25, 28.25) * mm});
            skLineSegment(sketch, "E1350", {"start": v(8.25, 28.25) * mm, "end": v(8.19, 28.21) * mm});
            skLineSegment(sketch, "E1351", {"start": v(8.19, 28.21) * mm, "end": v(8.13, 28.18) * mm});
            skLineSegment(sketch, "E1352", {"start": v(8.13, 28.18) * mm, "end": v(8.07, 28.15) * mm});
            skLineSegment(sketch, "E1353", {"start": v(8.07, 28.15) * mm, "end": v(8, 28.12) * mm});
            skLineSegment(sketch, "E1354", {"start": v(8, 28.12) * mm, "end": v(7.95, 28.09) * mm});
            skLineSegment(sketch, "E1355", {"start": v(7.95, 28.09) * mm, "end": v(7.9, 28.06) * mm});
            skLineSegment(sketch, "E1356", {"start": v(7.9, 28.06) * mm, "end": v(7.84, 28.03) * mm});
            skLineSegment(sketch, "E1357", {"start": v(7.84, 28.03) * mm, "end": v(7.78, 28) * mm});
            skLineSegment(sketch, "E1358", {"start": v(7.78, 28) * mm, "end": v(7.73, 27.97) * mm});
            skLineSegment(sketch, "E1359", {"start": v(7.73, 27.97) * mm, "end": v(7.68, 27.94) * mm});
            skLineSegment(sketch, "E1360", {"start": v(7.68, 27.94) * mm, "end": v(7.51, 28.1) * mm});
            skLineSegment(sketch, "E1361", {"start": v(7.51, 28.1) * mm, "end": v(6.95, 28.67) * mm});
            skLineSegment(sketch, "E1362", {"start": v(6.95, 28.67) * mm, "end": v(6.79, 28.85) * mm});
            skLineSegment(sketch, "E1363", {"start": v(6.79, 28.85) * mm, "end": v(6.82, 28.9) * mm});
            skLineSegment(sketch, "E1364", {"start": v(6.82, 28.9) * mm, "end": v(6.85, 28.95) * mm});
            skLineSegment(sketch, "E1365", {"start": v(6.85, 28.95) * mm, "end": v(6.88, 29) * mm});
            skLineSegment(sketch, "E1366", {"start": v(6.88, 29) * mm, "end": v(6.91, 29.06) * mm});
            skLineSegment(sketch, "E1367", {"start": v(6.91, 29.06) * mm, "end": v(6.94, 29.11) * mm});
            skLineSegment(sketch, "E1368", {"start": v(6.94, 29.11) * mm, "end": v(6.98, 29.17) * mm});
            skLineSegment(sketch, "E1369", {"start": v(6.98, 29.17) * mm, "end": v(7, 29.23) * mm});
            skLineSegment(sketch, "E1370", {"start": v(7, 29.23) * mm, "end": v(7.04, 29.29) * mm});
            skLineSegment(sketch, "E1371", {"start": v(7.04, 29.29) * mm, "end": v(7.08, 29.35) * mm});
            skLineSegment(sketch, "E1372", {"start": v(7.08, 29.35) * mm, "end": v(7.1, 29.41) * mm});
            skLineSegment(sketch, "E1373", {"start": v(7.1, 29.41) * mm, "end": v(7.14, 29.47) * mm});
            skLineSegment(sketch, "E1374", {"start": v(7.14, 29.47) * mm, "end": v(7.18, 29.54) * mm});
            skLineSegment(sketch, "E1375", {"start": v(7.18, 29.54) * mm, "end": v(7.21, 29.6) * mm});
            skLineSegment(sketch, "E1376", {"start": v(7.21, 29.6) * mm, "end": v(7.25, 29.67) * mm});
            skLineSegment(sketch, "E1377", {"start": v(7.25, 29.67) * mm, "end": v(7.28, 29.74) * mm});
            skLineSegment(sketch, "E1378", {"start": v(7.28, 29.74) * mm, "end": v(7.31, 29.8) * mm});
            skLineSegment(sketch, "E1379", {"start": v(7.31, 29.8) * mm, "end": v(7.35, 29.88) * mm});
            skLineSegment(sketch, "E1380", {"start": v(7.35, 29.88) * mm, "end": v(7.38, 29.95) * mm});
            skLineSegment(sketch, "E1381", {"start": v(7.38, 29.95) * mm, "end": v(7.42, 30.02) * mm});
            skLineSegment(sketch, "E1382", {"start": v(7.42, 30.02) * mm, "end": v(7.46, 30.1) * mm});
            skLineSegment(sketch, "E1383", {"start": v(7.46, 30.1) * mm, "end": v(7.5, 30.17) * mm});
            skLineSegment(sketch, "E1384", {"start": v(7.5, 30.17) * mm, "end": v(7.53, 30.25) * mm});
            skLineSegment(sketch, "E1385", {"start": v(7.53, 30.25) * mm, "end": v(7.56, 30.33) * mm});
            skLineSegment(sketch, "E1386", {"start": v(7.56, 30.33) * mm, "end": v(7.6, 30.4) * mm});
            skLineSegment(sketch, "E1387", {"start": v(7.6, 30.4) * mm, "end": v(7.64, 30.49) * mm});
            skLineSegment(sketch, "E1388", {"start": v(7.64, 30.49) * mm, "end": v(7.67, 30.57) * mm});
            skLineSegment(sketch, "E1389", {"start": v(7.67, 30.57) * mm, "end": v(7.7, 30.65) * mm});
            skLineSegment(sketch, "E1390", {"start": v(7.7, 30.65) * mm, "end": v(7.74, 30.74) * mm});
            skLineSegment(sketch, "E1391", {"start": v(7.74, 30.74) * mm, "end": v(7.78, 30.82) * mm});
            skLineSegment(sketch, "E1392", {"start": v(7.78, 30.82) * mm, "end": v(7.82, 30.91) * mm});
            skLineSegment(sketch, "E1393", {"start": v(7.82, 30.91) * mm, "end": v(7.85, 31) * mm});
            skLineSegment(sketch, "E1394", {"start": v(7.85, 31) * mm, "end": v(7.89, 31.09) * mm});
            skLineSegment(sketch, "E1395", {"start": v(7.89, 31.09) * mm, "end": v(7.93, 31.18) * mm});
            skLineSegment(sketch, "E1396", {"start": v(7.93, 31.18) * mm, "end": v(7.96, 31.27) * mm});
            skLineSegment(sketch, "E1397", {"start": v(7.96, 31.27) * mm, "end": v(8, 31.37) * mm});
            skLineSegment(sketch, "E1398", {"start": v(8, 31.37) * mm, "end": v(8.03, 31.46) * mm});
            skLineSegment(sketch, "E1399", {"start": v(8.03, 31.46) * mm, "end": v(8.07, 31.56) * mm});
            skLineSegment(sketch, "E1400", {"start": v(8.07, 31.56) * mm, "end": v(8.1, 31.65) * mm});
            skLineSegment(sketch, "E1401", {"start": v(8.1, 31.65) * mm, "end": v(8.14, 31.75) * mm});
            skLineSegment(sketch, "E1402", {"start": v(8.14, 31.75) * mm, "end": v(8.18, 31.85) * mm});
            skLineSegment(sketch, "E1403", {"start": v(8.18, 31.85) * mm, "end": v(8.17, 31.9) * mm});
            skLineSegment(sketch, "E1404", {"start": v(8.17, 31.9) * mm, "end": v(7.4, 32.61) * mm});
            skLineSegment(sketch, "E1405", {"start": v(7.4, 32.61) * mm, "end": v(7.36, 32.62) * mm});
            skLineSegment(sketch, "E1406", {"start": v(7.36, 32.62) * mm, "end": v(7.26, 32.58) * mm});
            skLineSegment(sketch, "E1407", {"start": v(7.26, 32.58) * mm, "end": v(7.16, 32.54) * mm});
            skLineSegment(sketch, "E1408", {"start": v(7.16, 32.54) * mm, "end": v(7.07, 32.5) * mm});
            skLineSegment(sketch, "E1409", {"start": v(7.07, 32.5) * mm, "end": v(6.97, 32.45) * mm});
            skLineSegment(sketch, "E1410", {"start": v(6.97, 32.45) * mm, "end": v(6.88, 32.4) * mm});
            skLineSegment(sketch, "E1411", {"start": v(6.88, 32.4) * mm, "end": v(6.8, 32.36) * mm});
            skLineSegment(sketch, "E1412", {"start": v(6.8, 32.36) * mm, "end": v(6.7, 32.32) * mm});
            skLineSegment(sketch, "E1413", {"start": v(6.7, 32.32) * mm, "end": v(6.61, 32.28) * mm});
            skLineSegment(sketch, "E1414", {"start": v(6.61, 32.28) * mm, "end": v(6.53, 32.24) * mm});
            skLineSegment(sketch, "E1415", {"start": v(6.53, 32.24) * mm, "end": v(6.44, 32.2) * mm});
            skLineSegment(sketch, "E1416", {"start": v(6.44, 32.2) * mm, "end": v(6.36, 32.15) * mm});
            skLineSegment(sketch, "E1417", {"start": v(6.36, 32.15) * mm, "end": v(6.27, 32.1) * mm});
            skLineSegment(sketch, "E1418", {"start": v(6.27, 32.1) * mm, "end": v(6.2, 32.07) * mm});
            skLineSegment(sketch, "E1419", {"start": v(6.2, 32.07) * mm, "end": v(6.11, 32.03) * mm});
            skLineSegment(sketch, "E1420", {"start": v(6.11, 32.03) * mm, "end": v(6.03, 31.98) * mm});
            skLineSegment(sketch, "E1421", {"start": v(6.03, 31.98) * mm, "end": v(5.95, 31.94) * mm});
            skLineSegment(sketch, "E1422", {"start": v(5.95, 31.94) * mm, "end": v(5.88, 31.9) * mm});
            skLineSegment(sketch, "E1423", {"start": v(5.88, 31.9) * mm, "end": v(5.8, 31.86) * mm});
            skLineSegment(sketch, "E1424", {"start": v(5.8, 31.86) * mm, "end": v(5.73, 31.82) * mm});
            skLineSegment(sketch, "E1425", {"start": v(5.73, 31.82) * mm, "end": v(5.65, 31.78) * mm});
            skLineSegment(sketch, "E1426", {"start": v(5.65, 31.78) * mm, "end": v(5.58, 31.74) * mm});
            skLineSegment(sketch, "E1427", {"start": v(5.58, 31.74) * mm, "end": v(5.51, 31.7) * mm});
            skLineSegment(sketch, "E1428", {"start": v(5.51, 31.7) * mm, "end": v(5.44, 31.66) * mm});
            skLineSegment(sketch, "E1429", {"start": v(5.44, 31.66) * mm, "end": v(5.38, 31.62) * mm});
            skLineSegment(sketch, "E1430", {"start": v(5.38, 31.62) * mm, "end": v(5.3, 31.58) * mm});
            skLineSegment(sketch, "E1431", {"start": v(5.3, 31.58) * mm, "end": v(5.24, 31.54) * mm});
            skLineSegment(sketch, "E1432", {"start": v(5.24, 31.54) * mm, "end": v(5.18, 31.5) * mm});
            skLineSegment(sketch, "E1433", {"start": v(5.18, 31.5) * mm, "end": v(5.12, 31.46) * mm});
            skLineSegment(sketch, "E1434", {"start": v(5.12, 31.46) * mm, "end": v(5.05, 31.42) * mm});
            skLineSegment(sketch, "E1435", {"start": v(5.05, 31.42) * mm, "end": v(5, 31.38) * mm});
            skLineSegment(sketch, "E1436", {"start": v(5, 31.38) * mm, "end": v(4.93, 31.35) * mm});
            skLineSegment(sketch, "E1437", {"start": v(4.93, 31.35) * mm, "end": v(4.88, 31.3) * mm});
            skLineSegment(sketch, "E1438", {"start": v(4.88, 31.3) * mm, "end": v(4.82, 31.27) * mm});
            skLineSegment(sketch, "E1439", {"start": v(4.82, 31.27) * mm, "end": v(4.76, 31.24) * mm});
            skLineSegment(sketch, "E1440", {"start": v(4.76, 31.24) * mm, "end": v(4.7, 31.2) * mm});
            skLineSegment(sketch, "E1441", {"start": v(4.7, 31.2) * mm, "end": v(4.66, 31.16) * mm});
            skLineSegment(sketch, "E1442", {"start": v(4.66, 31.16) * mm, "end": v(4.6, 31.13) * mm});
            skLineSegment(sketch, "E1443", {"start": v(4.6, 31.13) * mm, "end": v(4.55, 31.1) * mm});
            skLineSegment(sketch, "E1444", {"start": v(4.55, 31.1) * mm, "end": v(4.5, 31.06) * mm});
            skLineSegment(sketch, "E1445", {"start": v(4.5, 31.06) * mm, "end": v(4.45, 31.02) * mm});
            skLineSegment(sketch, "E1446", {"start": v(4.45, 31.02) * mm, "end": v(4.27, 31.17) * mm});
            skLineSegment(sketch, "E1447", {"start": v(4.27, 31.17) * mm, "end": v(3.66, 31.7) * mm});
            skLineSegment(sketch, "E1448", {"start": v(3.66, 31.7) * mm, "end": v(3.48, 31.85) * mm});
            skLineSegment(sketch, "E1449", {"start": v(3.48, 31.85) * mm, "end": v(3.5, 31.9) * mm});
            skLineSegment(sketch, "E1450", {"start": v(3.5, 31.9) * mm, "end": v(3.54, 31.96) * mm});
            skLineSegment(sketch, "E1451", {"start": v(3.54, 31.96) * mm, "end": v(3.56, 32.02) * mm});
            skLineSegment(sketch, "E1452", {"start": v(3.56, 32.02) * mm, "end": v(3.59, 32.07) * mm});
            skLineSegment(sketch, "E1453", {"start": v(3.59, 32.07) * mm, "end": v(3.62, 32.13) * mm});
            skLineSegment(sketch, "E1454", {"start": v(3.62, 32.13) * mm, "end": v(3.64, 32.2) * mm});
            skLineSegment(sketch, "E1455", {"start": v(3.64, 32.2) * mm, "end": v(3.67, 32.25) * mm});
            skLineSegment(sketch, "E1456", {"start": v(3.67, 32.25) * mm, "end": v(3.7, 32.31) * mm});
            skLineSegment(sketch, "E1457", {"start": v(3.7, 32.31) * mm, "end": v(3.73, 32.38) * mm});
            skLineSegment(sketch, "E1458", {"start": v(3.73, 32.38) * mm, "end": v(3.75, 32.44) * mm});
            skLineSegment(sketch, "E1459", {"start": v(3.75, 32.44) * mm, "end": v(3.78, 32.5) * mm});
            skLineSegment(sketch, "E1460", {"start": v(3.78, 32.5) * mm, "end": v(3.8, 32.58) * mm});
            skLineSegment(sketch, "E1461", {"start": v(3.8, 32.58) * mm, "end": v(3.84, 32.64) * mm});
            skLineSegment(sketch, "E1462", {"start": v(3.84, 32.64) * mm, "end": v(3.87, 32.71) * mm});
            skLineSegment(sketch, "E1463", {"start": v(3.87, 32.71) * mm, "end": v(3.9, 32.78) * mm});
            skLineSegment(sketch, "E1464", {"start": v(3.9, 32.78) * mm, "end": v(3.92, 32.86) * mm});
            skLineSegment(sketch, "E1465", {"start": v(3.92, 32.86) * mm, "end": v(3.95, 32.93) * mm});
            skLineSegment(sketch, "E1466", {"start": v(3.95, 32.93) * mm, "end": v(3.98, 33) * mm});
            skLineSegment(sketch, "E1467", {"start": v(3.98, 33) * mm, "end": v(4, 33.08) * mm});
            skLineSegment(sketch, "E1468", {"start": v(4, 33.08) * mm, "end": v(4.04, 33.16) * mm});
            skLineSegment(sketch, "E1469", {"start": v(4.04, 33.16) * mm, "end": v(4.07, 33.24) * mm});
            skLineSegment(sketch, "E1470", {"start": v(4.07, 33.24) * mm, "end": v(4.1, 33.32) * mm});
            skLineSegment(sketch, "E1471", {"start": v(4.1, 33.32) * mm, "end": v(4.12, 33.4) * mm});
            skLineSegment(sketch, "E1472", {"start": v(4.12, 33.4) * mm, "end": v(4.15, 33.48) * mm});
            skLineSegment(sketch, "E1473", {"start": v(4.15, 33.48) * mm, "end": v(4.18, 33.56) * mm});
            skLineSegment(sketch, "E1474", {"start": v(4.18, 33.56) * mm, "end": v(4.2, 33.65) * mm});
            skLineSegment(sketch, "E1475", {"start": v(4.2, 33.65) * mm, "end": v(4.24, 33.73) * mm});
            skLineSegment(sketch, "E1476", {"start": v(4.24, 33.73) * mm, "end": v(4.27, 33.82) * mm});
            skLineSegment(sketch, "E1477", {"start": v(4.27, 33.82) * mm, "end": v(4.3, 33.9) * mm});
            skLineSegment(sketch, "E1478", {"start": v(4.3, 33.9) * mm, "end": v(4.32, 34) * mm});
            skLineSegment(sketch, "E1479", {"start": v(4.32, 34) * mm, "end": v(4.35, 34.1) * mm});
            skLineSegment(sketch, "E1480", {"start": v(4.35, 34.1) * mm, "end": v(4.38, 34.18) * mm});
            skLineSegment(sketch, "E1481", {"start": v(4.38, 34.18) * mm, "end": v(4.4, 34.28) * mm});
            skLineSegment(sketch, "E1482", {"start": v(4.4, 34.28) * mm, "end": v(4.44, 34.37) * mm});
            skLineSegment(sketch, "E1483", {"start": v(4.44, 34.37) * mm, "end": v(4.46, 34.47) * mm});
            skLineSegment(sketch, "E1484", {"start": v(4.46, 34.47) * mm, "end": v(4.5, 34.57) * mm});
            skLineSegment(sketch, "E1485", {"start": v(4.5, 34.57) * mm, "end": v(4.52, 34.67) * mm});
            skLineSegment(sketch, "E1486", {"start": v(4.52, 34.67) * mm, "end": v(4.55, 34.77) * mm});
            skLineSegment(sketch, "E1487", {"start": v(4.55, 34.77) * mm, "end": v(4.57, 34.87) * mm});
            skLineSegment(sketch, "E1488", {"start": v(4.57, 34.87) * mm, "end": v(4.6, 34.97) * mm});
            skLineSegment(sketch, "E1489", {"start": v(4.6, 34.97) * mm, "end": v(4.58, 35.02) * mm});
            skLineSegment(sketch, "E1490", {"start": v(4.58, 35.02) * mm, "end": v(3.76, 35.66) * mm});
            skLineSegment(sketch, "E1491", {"start": v(3.76, 35.66) * mm, "end": v(3.71, 35.66) * mm});
            skLineSegment(sketch, "E1492", {"start": v(3.71, 35.66) * mm, "end": v(3.62, 35.61) * mm});
            skLineSegment(sketch, "E1493", {"start": v(3.62, 35.61) * mm, "end": v(3.53, 35.56) * mm});
            skLineSegment(sketch, "E1494", {"start": v(3.53, 35.56) * mm, "end": v(3.44, 35.5) * mm});
            skLineSegment(sketch, "E1495", {"start": v(3.44, 35.5) * mm, "end": v(3.35, 35.46) * mm});
            skLineSegment(sketch, "E1496", {"start": v(3.35, 35.46) * mm, "end": v(3.26, 35.4) * mm});
            skLineSegment(sketch, "E1497", {"start": v(3.26, 35.4) * mm, "end": v(3.17, 35.36) * mm});
            skLineSegment(sketch, "E1498", {"start": v(3.17, 35.36) * mm, "end": v(3.09, 35.3) * mm});
            skLineSegment(sketch, "E1499", {"start": v(3.09, 35.3) * mm, "end": v(3, 35.25) * mm});
            skLineSegment(sketch, "E1500", {"start": v(3, 35.25) * mm, "end": v(2.92, 35.2) * mm});
            skLineSegment(sketch, "E1501", {"start": v(2.92, 35.2) * mm, "end": v(2.84, 35.15) * mm});
            skLineSegment(sketch, "E1502", {"start": v(2.84, 35.15) * mm, "end": v(2.76, 35.1) * mm});
            skLineSegment(sketch, "E1503", {"start": v(2.76, 35.1) * mm, "end": v(2.68, 35.05) * mm});
            skLineSegment(sketch, "E1504", {"start": v(2.68, 35.05) * mm, "end": v(2.6, 35) * mm});
            skLineSegment(sketch, "E1505", {"start": v(2.6, 35) * mm, "end": v(2.53, 34.96) * mm});
            skLineSegment(sketch, "E1506", {"start": v(2.53, 34.96) * mm, "end": v(2.45, 34.9) * mm});
            skLineSegment(sketch, "E1507", {"start": v(2.45, 34.9) * mm, "end": v(2.38, 34.86) * mm});
            skLineSegment(sketch, "E1508", {"start": v(2.38, 34.86) * mm, "end": v(2.3, 34.81) * mm});
            skLineSegment(sketch, "E1509", {"start": v(2.3, 34.81) * mm, "end": v(2.23, 34.76) * mm});
            skLineSegment(sketch, "E1510", {"start": v(2.23, 34.76) * mm, "end": v(2.16, 34.72) * mm});
            skLineSegment(sketch, "E1511", {"start": v(2.16, 34.72) * mm, "end": v(2.1, 34.67) * mm});
            skLineSegment(sketch, "E1512", {"start": v(2.1, 34.67) * mm, "end": v(2.03, 34.62) * mm});
            skLineSegment(sketch, "E1513", {"start": v(2.03, 34.62) * mm, "end": v(1.96, 34.58) * mm});
            skLineSegment(sketch, "E1514", {"start": v(1.96, 34.58) * mm, "end": v(1.9, 34.53) * mm});
            skLineSegment(sketch, "E1515", {"start": v(1.9, 34.53) * mm, "end": v(1.83, 34.48) * mm});
            skLineSegment(sketch, "E1516", {"start": v(1.83, 34.48) * mm, "end": v(1.77, 34.44) * mm});
            skLineSegment(sketch, "E1517", {"start": v(1.77, 34.44) * mm, "end": v(1.7, 34.4) * mm});
            skLineSegment(sketch, "E1518", {"start": v(1.7, 34.4) * mm, "end": v(1.64, 34.35) * mm});
            skLineSegment(sketch, "E1519", {"start": v(1.64, 34.35) * mm, "end": v(1.58, 34.3) * mm});
            skLineSegment(sketch, "E1520", {"start": v(1.58, 34.3) * mm, "end": v(1.53, 34.26) * mm});
            skLineSegment(sketch, "E1521", {"start": v(1.53, 34.26) * mm, "end": v(1.47, 34.22) * mm});
            skLineSegment(sketch, "E1522", {"start": v(1.47, 34.22) * mm, "end": v(1.41, 34.17) * mm});
            skLineSegment(sketch, "E1523", {"start": v(1.41, 34.17) * mm, "end": v(1.36, 34.13) * mm});
            skLineSegment(sketch, "E1524", {"start": v(1.36, 34.13) * mm, "end": v(1.3, 34.1) * mm});
            skLineSegment(sketch, "E1525", {"start": v(1.3, 34.1) * mm, "end": v(1.25, 34.05) * mm});
            skLineSegment(sketch, "E1526", {"start": v(1.25, 34.05) * mm, "end": v(1.2, 34) * mm});
            skLineSegment(sketch, "E1527", {"start": v(1.2, 34) * mm, "end": v(1.15, 33.97) * mm});
            skLineSegment(sketch, "E1528", {"start": v(1.15, 33.97) * mm, "end": v(1.1, 33.93) * mm});
            skLineSegment(sketch, "E1529", {"start": v(1.1, 33.93) * mm, "end": v(1.06, 33.89) * mm});
            skLineSegment(sketch, "E1530", {"start": v(1.06, 33.89) * mm, "end": v(1, 33.85) * mm});
            skLineSegment(sketch, "E1531", {"start": v(1, 33.85) * mm, "end": v(0.96, 33.81) * mm});
            skLineSegment(sketch, "E1532", {"start": v(0.96, 33.81) * mm, "end": v(0.77, 33.94) * mm});
            skLineSegment(sketch, "E1533", {"start": v(0.77, 33.94) * mm, "end": v(0.11, 34.4) * mm});
            skLineSegment(sketch, "E1534", {"start": v(0.11, 34.4) * mm, "end": v(-0.08, 34.55) * mm});
            skLineSegment(sketch, "E1535", {"start": v(-0.08, 34.55) * mm, "end": v(-0.06, 34.6) * mm});
            skLineSegment(sketch, "E1536", {"start": v(-0.06, 34.6) * mm, "end": v(-0.03, 34.66) * mm});
            skLineSegment(sketch, "E1537", {"start": v(-0.03, 34.66) * mm, "end": v(-0.01, 34.72) * mm});
            skLineSegment(sketch, "E1538", {"start": v(-0.01, 34.72) * mm, "end": v(0, 34.78) * mm});
            skLineSegment(sketch, "E1539", {"start": v(0, 34.78) * mm, "end": v(0.03, 34.84) * mm});
            skLineSegment(sketch, "E1540", {"start": v(0.03, 34.84) * mm, "end": v(0.05, 34.9) * mm});
            skLineSegment(sketch, "E1541", {"start": v(0.05, 34.9) * mm, "end": v(0.07, 34.96) * mm});
            skLineSegment(sketch, "E1542", {"start": v(0.07, 34.96) * mm, "end": v(0.1, 35.03) * mm});
            skLineSegment(sketch, "E1543", {"start": v(0.1, 35.03) * mm, "end": v(0.12, 35.1) * mm});
            skLineSegment(sketch, "E1544", {"start": v(0.12, 35.1) * mm, "end": v(0.14, 35.16) * mm});
            skLineSegment(sketch, "E1545", {"start": v(0.14, 35.16) * mm, "end": v(0.16, 35.23) * mm});
            skLineSegment(sketch, "E1546", {"start": v(0.16, 35.23) * mm, "end": v(0.18, 35.3) * mm});
            skLineSegment(sketch, "E1547", {"start": v(0.18, 35.3) * mm, "end": v(0.2, 35.37) * mm});
            skLineSegment(sketch, "E1548", {"start": v(0.2, 35.37) * mm, "end": v(0.23, 35.44) * mm});
            skLineSegment(sketch, "E1549", {"start": v(0.23, 35.44) * mm, "end": v(0.25, 35.51) * mm});
            skLineSegment(sketch, "E1550", {"start": v(0.25, 35.51) * mm, "end": v(0.27, 35.59) * mm});
            skLineSegment(sketch, "E1551", {"start": v(0.27, 35.59) * mm, "end": v(0.3, 35.66) * mm});
            skLineSegment(sketch, "E1552", {"start": v(0.3, 35.66) * mm, "end": v(0.31, 35.74) * mm});
            skLineSegment(sketch, "E1553", {"start": v(0.31, 35.74) * mm, "end": v(0.34, 35.82) * mm});
            skLineSegment(sketch, "E1554", {"start": v(0.34, 35.82) * mm, "end": v(0.36, 35.9) * mm});
            skLineSegment(sketch, "E1555", {"start": v(0.36, 35.9) * mm, "end": v(0.38, 35.98) * mm});
            skLineSegment(sketch, "E1556", {"start": v(0.38, 35.98) * mm, "end": v(0.4, 36.06) * mm});
            skLineSegment(sketch, "E1557", {"start": v(0.4, 36.06) * mm, "end": v(0.42, 36.14) * mm});
            skLineSegment(sketch, "E1558", {"start": v(0.42, 36.14) * mm, "end": v(0.44, 36.23) * mm});
            skLineSegment(sketch, "E1559", {"start": v(0.44, 36.23) * mm, "end": v(0.46, 36.31) * mm});
            skLineSegment(sketch, "E1560", {"start": v(0.46, 36.31) * mm, "end": v(0.49, 36.4) * mm});
            skLineSegment(sketch, "E1561", {"start": v(0.49, 36.4) * mm, "end": v(0.5, 36.49) * mm});
            skLineSegment(sketch, "E1562", {"start": v(0.5, 36.49) * mm, "end": v(0.53, 36.58) * mm});
            skLineSegment(sketch, "E1563", {"start": v(0.53, 36.58) * mm, "end": v(0.55, 36.67) * mm});
            skLineSegment(sketch, "E1564", {"start": v(0.55, 36.67) * mm, "end": v(0.57, 36.76) * mm});
            skLineSegment(sketch, "E1565", {"start": v(0.57, 36.76) * mm, "end": v(0.59, 36.86) * mm});
            skLineSegment(sketch, "E1566", {"start": v(0.59, 36.86) * mm, "end": v(0.6, 36.95) * mm});
            skLineSegment(sketch, "E1567", {"start": v(0.6, 36.95) * mm, "end": v(0.63, 37.05) * mm});
            skLineSegment(sketch, "E1568", {"start": v(0.63, 37.05) * mm, "end": v(0.65, 37.14) * mm});
            skLineSegment(sketch, "E1569", {"start": v(0.65, 37.14) * mm, "end": v(0.67, 37.24) * mm});
            skLineSegment(sketch, "E1570", {"start": v(0.67, 37.24) * mm, "end": v(0.68, 37.34) * mm});
            skLineSegment(sketch, "E1571", {"start": v(0.68, 37.34) * mm, "end": v(0.7, 37.44) * mm});
            skLineSegment(sketch, "E1572", {"start": v(0.7, 37.44) * mm, "end": v(0.72, 37.55) * mm});
            skLineSegment(sketch, "E1573", {"start": v(0.72, 37.55) * mm, "end": v(0.74, 37.65) * mm});
            skLineSegment(sketch, "E1574", {"start": v(0.74, 37.65) * mm, "end": v(0.76, 37.75) * mm});
            skLineSegment(sketch, "E1575", {"start": v(0.76, 37.75) * mm, "end": v(0.73, 37.8) * mm});
            skLineSegment(sketch, "E1576", {"start": v(0.73, 37.8) * mm, "end": v(-0.14, 38.36) * mm});
            skLineSegment(sketch, "E1577", {"start": v(-0.14, 38.36) * mm, "end": v(-0.2, 38.36) * mm});
            skLineSegment(sketch, "E1578", {"start": v(-0.2, 38.36) * mm, "end": v(-0.28, 38.3) * mm});
            skLineSegment(sketch, "E1579", {"start": v(-0.28, 38.3) * mm, "end": v(-0.37, 38.24) * mm});
            skLineSegment(sketch, "E1580", {"start": v(-0.37, 38.24) * mm, "end": v(-0.45, 38.19) * mm});
            skLineSegment(sketch, "E1581", {"start": v(-0.45, 38.19) * mm, "end": v(-0.54, 38.13) * mm});
            skLineSegment(sketch, "E1582", {"start": v(-0.54, 38.13) * mm, "end": v(-0.62, 38.07) * mm});
            skLineSegment(sketch, "E1583", {"start": v(-0.62, 38.07) * mm, "end": v(-0.7, 38) * mm});
            skLineSegment(sketch, "E1584", {"start": v(-0.7, 38) * mm, "end": v(-0.78, 37.95) * mm});
            skLineSegment(sketch, "E1585", {"start": v(-0.78, 37.95) * mm, "end": v(-0.86, 37.9) * mm});
            skLineSegment(sketch, "E1586", {"start": v(-0.86, 37.9) * mm, "end": v(-0.94, 37.84) * mm});
            skLineSegment(sketch, "E1587", {"start": v(-0.94, 37.84) * mm, "end": v(-1.01, 37.78) * mm});
            skLineSegment(sketch, "E1588", {"start": v(-1.01, 37.78) * mm, "end": v(-1.1, 37.72) * mm});
            skLineSegment(sketch, "E1589", {"start": v(-1.1, 37.72) * mm, "end": v(-1.16, 37.67) * mm});
            skLineSegment(sketch, "E1590", {"start": v(-1.16, 37.67) * mm, "end": v(-1.24, 37.6) * mm});
            skLineSegment(sketch, "E1591", {"start": v(-1.24, 37.6) * mm, "end": v(-1.3, 37.55) * mm});
            skLineSegment(sketch, "E1592", {"start": v(-1.3, 37.55) * mm, "end": v(-1.38, 37.5) * mm});
            skLineSegment(sketch, "E1593", {"start": v(-1.38, 37.5) * mm, "end": v(-1.45, 37.44) * mm});
            skLineSegment(sketch, "E1594", {"start": v(-1.45, 37.44) * mm, "end": v(-1.52, 37.39) * mm});
            skLineSegment(sketch, "E1595", {"start": v(-1.52, 37.39) * mm, "end": v(-1.58, 37.34) * mm});
            skLineSegment(sketch, "E1596", {"start": v(-1.58, 37.34) * mm, "end": v(-1.65, 37.28) * mm});
            skLineSegment(sketch, "E1597", {"start": v(-1.65, 37.28) * mm, "end": v(-1.71, 37.23) * mm});
            skLineSegment(sketch, "E1598", {"start": v(-1.71, 37.23) * mm, "end": v(-1.78, 37.18) * mm});
            skLineSegment(sketch, "E1599", {"start": v(-1.78, 37.18) * mm, "end": v(-1.84, 37.12) * mm});
            skLineSegment(sketch, "E1600", {"start": v(-1.84, 37.12) * mm, "end": v(-1.9, 37.07) * mm});
            skLineSegment(sketch, "E1601", {"start": v(-1.9, 37.07) * mm, "end": v(-1.96, 37.02) * mm});
            skLineSegment(sketch, "E1602", {"start": v(-1.96, 37.02) * mm, "end": v(-2.02, 36.97) * mm});
            skLineSegment(sketch, "E1603", {"start": v(-2.02, 36.97) * mm, "end": v(-2.08, 36.92) * mm});
            skLineSegment(sketch, "E1604", {"start": v(-2.08, 36.92) * mm, "end": v(-2.13, 36.87) * mm});
            skLineSegment(sketch, "E1605", {"start": v(-2.13, 36.87) * mm, "end": v(-2.19, 36.82) * mm});
            skLineSegment(sketch, "E1606", {"start": v(-2.19, 36.82) * mm, "end": v(-2.24, 36.77) * mm});
            skLineSegment(sketch, "E1607", {"start": v(-2.24, 36.77) * mm, "end": v(-2.3, 36.72) * mm});
            skLineSegment(sketch, "E1608", {"start": v(-2.3, 36.72) * mm, "end": v(-2.35, 36.68) * mm});
            skLineSegment(sketch, "E1609", {"start": v(-2.35, 36.68) * mm, "end": v(-2.4, 36.63) * mm});
            skLineSegment(sketch, "E1610", {"start": v(-2.4, 36.63) * mm, "end": v(-2.45, 36.58) * mm});
            skLineSegment(sketch, "E1611", {"start": v(-2.45, 36.58) * mm, "end": v(-2.5, 36.54) * mm});
            skLineSegment(sketch, "E1612", {"start": v(-2.5, 36.54) * mm, "end": v(-2.54, 36.5) * mm});
            skLineSegment(sketch, "E1613", {"start": v(-2.54, 36.5) * mm, "end": v(-2.59, 36.45) * mm});
            skLineSegment(sketch, "E1614", {"start": v(-2.59, 36.45) * mm, "end": v(-2.63, 36.4) * mm});
            skLineSegment(sketch, "E1615", {"start": v(-2.63, 36.4) * mm, "end": v(-2.68, 36.36) * mm});
            skLineSegment(sketch, "E1616", {"start": v(-2.68, 36.36) * mm, "end": v(-2.72, 36.32) * mm});
            skLineSegment(sketch, "E1617", {"start": v(-2.72, 36.32) * mm, "end": v(-2.76, 36.27) * mm});
            skLineSegment(sketch, "E1618", {"start": v(-2.76, 36.27) * mm, "end": v(-2.97, 36.38) * mm});
            skLineSegment(sketch, "E1619", {"start": v(-2.97, 36.38) * mm, "end": v(-3.66, 36.79) * mm});
            skLineSegment(sketch, "E1620", {"start": v(-3.66, 36.79) * mm, "end": v(-3.86, 36.91) * mm});
            skLineSegment(sketch, "E1621", {"start": v(-3.86, 36.91) * mm, "end": v(-3.85, 36.97) * mm});
            skLineSegment(sketch, "E1622", {"start": v(-3.85, 36.97) * mm, "end": v(-3.83, 37.03) * mm});
            skLineSegment(sketch, "E1623", {"start": v(-3.83, 37.03) * mm, "end": v(-3.82, 37.09) * mm});
            skLineSegment(sketch, "E1624", {"start": v(-3.82, 37.09) * mm, "end": v(-3.8, 37.15) * mm});
            skLineSegment(sketch, "E1625", {"start": v(-3.8, 37.15) * mm, "end": v(-3.78, 37.21) * mm});
            skLineSegment(sketch, "E1626", {"start": v(-3.78, 37.21) * mm, "end": v(-3.77, 37.28) * mm});
            skLineSegment(sketch, "E1627", {"start": v(-3.77, 37.28) * mm, "end": v(-3.75, 37.34) * mm});
            skLineSegment(sketch, "E1628", {"start": v(-3.75, 37.34) * mm, "end": v(-3.74, 37.4) * mm});
            skLineSegment(sketch, "E1629", {"start": v(-3.74, 37.4) * mm, "end": v(-3.72, 37.47) * mm});
            skLineSegment(sketch, "E1630", {"start": v(-3.72, 37.47) * mm, "end": v(-3.7, 37.54) * mm});
            skLineSegment(sketch, "E1631", {"start": v(-3.7, 37.54) * mm, "end": v(-3.69, 37.61) * mm});
            skLineSegment(sketch, "E1632", {"start": v(-3.69, 37.61) * mm, "end": v(-3.67, 37.68) * mm});
            skLineSegment(sketch, "E1633", {"start": v(-3.67, 37.68) * mm, "end": v(-3.66, 37.76) * mm});
            skLineSegment(sketch, "E1634", {"start": v(-3.66, 37.76) * mm, "end": v(-3.64, 37.83) * mm});
            skLineSegment(sketch, "E1635", {"start": v(-3.64, 37.83) * mm, "end": v(-3.63, 37.9) * mm});
            skLineSegment(sketch, "E1636", {"start": v(-3.63, 37.9) * mm, "end": v(-3.61, 37.98) * mm});
            skLineSegment(sketch, "E1637", {"start": v(-3.61, 37.98) * mm, "end": v(-3.6, 38.06) * mm});
            skLineSegment(sketch, "E1638", {"start": v(-3.6, 38.06) * mm, "end": v(-3.58, 38.14) * mm});
            skLineSegment(sketch, "E1639", {"start": v(-3.58, 38.14) * mm, "end": v(-3.57, 38.22) * mm});
            skLineSegment(sketch, "E1640", {"start": v(-3.57, 38.22) * mm, "end": v(-3.55, 38.3) * mm});
            skLineSegment(sketch, "E1641", {"start": v(-3.55, 38.3) * mm, "end": v(-3.54, 38.38) * mm});
            skLineSegment(sketch, "E1642", {"start": v(-3.54, 38.38) * mm, "end": v(-3.52, 38.46) * mm});
            skLineSegment(sketch, "E1643", {"start": v(-3.52, 38.46) * mm, "end": v(-3.51, 38.55) * mm});
            skLineSegment(sketch, "E1644", {"start": v(-3.51, 38.55) * mm, "end": v(-3.5, 38.63) * mm});
            skLineSegment(sketch, "E1645", {"start": v(-3.5, 38.63) * mm, "end": v(-3.48, 38.72) * mm});
            skLineSegment(sketch, "E1646", {"start": v(-3.48, 38.72) * mm, "end": v(-3.47, 38.8) * mm});
            skLineSegment(sketch, "E1647", {"start": v(-3.47, 38.8) * mm, "end": v(-3.46, 38.9) * mm});
            skLineSegment(sketch, "E1648", {"start": v(-3.46, 38.9) * mm, "end": v(-3.44, 39) * mm});
            skLineSegment(sketch, "E1649", {"start": v(-3.44, 39) * mm, "end": v(-3.43, 39.08) * mm});
            skLineSegment(sketch, "E1650", {"start": v(-3.43, 39.08) * mm, "end": v(-3.42, 39.18) * mm});
            skLineSegment(sketch, "E1651", {"start": v(-3.42, 39.18) * mm, "end": v(-3.4, 39.27) * mm});
            skLineSegment(sketch, "E1652", {"start": v(-3.4, 39.27) * mm, "end": v(-3.4, 39.37) * mm});
            skLineSegment(sketch, "E1653", {"start": v(-3.4, 39.37) * mm, "end": v(-3.39, 39.47) * mm});
            skLineSegment(sketch, "E1654", {"start": v(-3.39, 39.47) * mm, "end": v(-3.38, 39.56) * mm});
            skLineSegment(sketch, "E1655", {"start": v(-3.38, 39.56) * mm, "end": v(-3.37, 39.66) * mm});
            skLineSegment(sketch, "E1656", {"start": v(-3.37, 39.66) * mm, "end": v(-3.36, 39.76) * mm});
            skLineSegment(sketch, "E1657", {"start": v(-3.36, 39.76) * mm, "end": v(-3.35, 39.87) * mm});
            skLineSegment(sketch, "E1658", {"start": v(-3.35, 39.87) * mm, "end": v(-3.34, 39.97) * mm});
            skLineSegment(sketch, "E1659", {"start": v(-3.34, 39.97) * mm, "end": v(-3.33, 40.08) * mm});
            skLineSegment(sketch, "E1660", {"start": v(-3.33, 40.08) * mm, "end": v(-3.32, 40.18) * mm});
            skLineSegment(sketch, "E1661", {"start": v(-3.32, 40.18) * mm, "end": v(-3.35, 40.22) * mm});
            skLineSegment(sketch, "E1662", {"start": v(-3.35, 40.22) * mm, "end": v(-4.27, 40.7) * mm});
            skLineSegment(sketch, "E1663", {"start": v(-4.27, 40.7) * mm, "end": v(-4.32, 40.7) * mm});
            skLineSegment(sketch, "E1664", {"start": v(-4.32, 40.7) * mm, "end": v(-4.4, 40.64) * mm});
            skLineSegment(sketch, "E1665", {"start": v(-4.4, 40.64) * mm, "end": v(-4.48, 40.57) * mm});
            skLineSegment(sketch, "E1666", {"start": v(-4.48, 40.57) * mm, "end": v(-4.56, 40.5) * mm});
            skLineSegment(sketch, "E1667", {"start": v(-4.56, 40.5) * mm, "end": v(-4.64, 40.44) * mm});
            skLineSegment(sketch, "E1668", {"start": v(-4.64, 40.44) * mm, "end": v(-4.72, 40.37) * mm});
            skLineSegment(sketch, "E1669", {"start": v(-4.72, 40.37) * mm, "end": v(-4.8, 40.3) * mm});
            skLineSegment(sketch, "E1670", {"start": v(-4.8, 40.3) * mm, "end": v(-4.87, 40.24) * mm});
            skLineSegment(sketch, "E1671", {"start": v(-4.87, 40.24) * mm, "end": v(-4.94, 40.18) * mm});
            skLineSegment(sketch, "E1672", {"start": v(-4.94, 40.18) * mm, "end": v(-5.02, 40.11) * mm});
            skLineSegment(sketch, "E1673", {"start": v(-5.02, 40.11) * mm, "end": v(-5.09, 40.05) * mm});
            skLineSegment(sketch, "E1674", {"start": v(-5.09, 40.05) * mm, "end": v(-5.16, 39.98) * mm});
            skLineSegment(sketch, "E1675", {"start": v(-5.16, 39.98) * mm, "end": v(-5.23, 39.92) * mm});
            skLineSegment(sketch, "E1676", {"start": v(-5.23, 39.92) * mm, "end": v(-5.3, 39.86) * mm});
            skLineSegment(sketch, "E1677", {"start": v(-5.3, 39.86) * mm, "end": v(-5.36, 39.8) * mm});
            skLineSegment(sketch, "E1678", {"start": v(-5.36, 39.8) * mm, "end": v(-5.43, 39.74) * mm});
            skLineSegment(sketch, "E1679", {"start": v(-5.43, 39.74) * mm, "end": v(-5.5, 39.68) * mm});
            skLineSegment(sketch, "E1680", {"start": v(-5.5, 39.68) * mm, "end": v(-5.55, 39.62) * mm});
            skLineSegment(sketch, "E1681", {"start": v(-5.55, 39.62) * mm, "end": v(-5.61, 39.56) * mm});
            skLineSegment(sketch, "E1682", {"start": v(-5.61, 39.56) * mm, "end": v(-5.68, 39.5) * mm});
            skLineSegment(sketch, "E1683", {"start": v(-5.68, 39.5) * mm, "end": v(-5.73, 39.44) * mm});
            skLineSegment(sketch, "E1684", {"start": v(-5.73, 39.44) * mm, "end": v(-5.8, 39.38) * mm});
            skLineSegment(sketch, "E1685", {"start": v(-5.8, 39.38) * mm, "end": v(-5.85, 39.32) * mm});
            skLineSegment(sketch, "E1686", {"start": v(-5.85, 39.32) * mm, "end": v(-5.9, 39.26) * mm});
            skLineSegment(sketch, "E1687", {"start": v(-5.9, 39.26) * mm, "end": v(-5.96, 39.2) * mm});
            skLineSegment(sketch, "E1688", {"start": v(-5.96, 39.2) * mm, "end": v(-6.01, 39.15) * mm});
            skLineSegment(sketch, "E1689", {"start": v(-6.01, 39.15) * mm, "end": v(-6.07, 39.1) * mm});
            skLineSegment(sketch, "E1690", {"start": v(-6.07, 39.1) * mm, "end": v(-6.12, 39.04) * mm});
            skLineSegment(sketch, "E1691", {"start": v(-6.12, 39.04) * mm, "end": v(-6.17, 38.99) * mm});
            skLineSegment(sketch, "E1692", {"start": v(-6.17, 38.99) * mm, "end": v(-6.22, 38.93) * mm});
            skLineSegment(sketch, "E1693", {"start": v(-6.22, 38.93) * mm, "end": v(-6.27, 38.88) * mm});
            skLineSegment(sketch, "E1694", {"start": v(-6.27, 38.88) * mm, "end": v(-6.31, 38.83) * mm});
            skLineSegment(sketch, "E1695", {"start": v(-6.31, 38.83) * mm, "end": v(-6.36, 38.78) * mm});
            skLineSegment(sketch, "E1696", {"start": v(-6.36, 38.78) * mm, "end": v(-6.4, 38.73) * mm});
            skLineSegment(sketch, "E1697", {"start": v(-6.4, 38.73) * mm, "end": v(-6.45, 38.68) * mm});
            skLineSegment(sketch, "E1698", {"start": v(-6.45, 38.68) * mm, "end": v(-6.5, 38.63) * mm});
            skLineSegment(sketch, "E1699", {"start": v(-6.5, 38.63) * mm, "end": v(-6.54, 38.58) * mm});
            skLineSegment(sketch, "E1700", {"start": v(-6.54, 38.58) * mm, "end": v(-6.58, 38.53) * mm});
            skLineSegment(sketch, "E1701", {"start": v(-6.58, 38.53) * mm, "end": v(-6.62, 38.48) * mm});
            skLineSegment(sketch, "E1702", {"start": v(-6.62, 38.48) * mm, "end": v(-6.65, 38.44) * mm});
            skLineSegment(sketch, "E1703", {"start": v(-6.65, 38.44) * mm, "end": v(-6.7, 38.4) * mm});
            skLineSegment(sketch, "E1704", {"start": v(-6.7, 38.4) * mm, "end": v(-6.9, 38.48) * mm});
            skLineSegment(sketch, "E1705", {"start": v(-6.9, 38.48) * mm, "end": v(-7.64, 38.82) * mm});
            skLineSegment(sketch, "E1706", {"start": v(-7.64, 38.82) * mm, "end": v(-7.85, 38.93) * mm});
            skLineSegment(sketch, "E1707", {"start": v(-7.85, 38.93) * mm, "end": v(-7.84, 38.99) * mm});
            skLineSegment(sketch, "E1708", {"start": v(-7.84, 38.99) * mm, "end": v(-7.83, 39.05) * mm});
            skLineSegment(sketch, "E1709", {"start": v(-7.83, 39.05) * mm, "end": v(-7.82, 39.1) * mm});
            skLineSegment(sketch, "E1710", {"start": v(-7.82, 39.1) * mm, "end": v(-7.8, 39.17) * mm});
            skLineSegment(sketch, "E1711", {"start": v(-7.8, 39.17) * mm, "end": v(-7.8, 39.24) * mm});
            skLineSegment(sketch, "E1712", {"start": v(-7.8, 39.24) * mm, "end": v(-7.78, 39.3) * mm});
            skLineSegment(sketch, "E1713", {"start": v(-7.78, 39.3) * mm, "end": v(-7.77, 39.37) * mm});
            skLineSegment(sketch, "E1714", {"start": v(-7.77, 39.37) * mm, "end": v(-7.76, 39.43) * mm});
            skLineSegment(sketch, "E1715", {"start": v(-7.76, 39.43) * mm, "end": v(-7.75, 39.5) * mm});
            skLineSegment(sketch, "E1716", {"start": v(-7.75, 39.5) * mm, "end": v(-7.74, 39.57) * mm});
            skLineSegment(sketch, "E1717", {"start": v(-7.74, 39.57) * mm, "end": v(-7.74, 39.64) * mm});
            skLineSegment(sketch, "E1718", {"start": v(-7.74, 39.64) * mm, "end": v(-7.73, 39.71) * mm});
            skLineSegment(sketch, "E1719", {"start": v(-7.73, 39.71) * mm, "end": v(-7.72, 39.79) * mm});
            skLineSegment(sketch, "E1720", {"start": v(-7.72, 39.79) * mm, "end": v(-7.7, 39.86) * mm});
            skLineSegment(sketch, "E1721", {"start": v(-7.7, 39.86) * mm, "end": v(-7.7, 39.94) * mm});
            skLineSegment(sketch, "E1722", {"start": v(-7.7, 39.94) * mm, "end": v(-7.7, 40.02) * mm});
            skLineSegment(sketch, "E1723", {"start": v(-7.7, 40.02) * mm, "end": v(-7.68, 40.1) * mm});
            skLineSegment(sketch, "E1724", {"start": v(-7.68, 40.1) * mm, "end": v(-7.68, 40.17) * mm});
            skLineSegment(sketch, "E1725", {"start": v(-7.68, 40.17) * mm, "end": v(-7.67, 40.25) * mm});
            skLineSegment(sketch, "E1726", {"start": v(-7.67, 40.25) * mm, "end": v(-7.66, 40.34) * mm});
            skLineSegment(sketch, "E1727", {"start": v(-7.66, 40.34) * mm, "end": v(-7.65, 40.42) * mm});
            skLineSegment(sketch, "E1728", {"start": v(-7.65, 40.42) * mm, "end": v(-7.65, 40.5) * mm});
            skLineSegment(sketch, "E1729", {"start": v(-7.65, 40.5) * mm, "end": v(-7.64, 40.59) * mm});
            skLineSegment(sketch, "E1730", {"start": v(-7.64, 40.59) * mm, "end": v(-7.64, 40.68) * mm});
            skLineSegment(sketch, "E1731", {"start": v(-7.64, 40.68) * mm, "end": v(-7.63, 40.76) * mm});
            skLineSegment(sketch, "E1732", {"start": v(-7.63, 40.76) * mm, "end": v(-7.63, 40.85) * mm});
            skLineSegment(sketch, "E1733", {"start": v(-7.63, 40.85) * mm, "end": v(-7.62, 40.95) * mm});
            skLineSegment(sketch, "E1734", {"start": v(-7.62, 40.95) * mm, "end": v(-7.62, 41.04) * mm});
            skLineSegment(sketch, "E1735", {"start": v(-7.62, 41.04) * mm, "end": v(-7.61, 41.13) * mm});
            skLineSegment(sketch, "E1736", {"start": v(-7.61, 41.13) * mm, "end": v(-7.6, 41.22) * mm});
            skLineSegment(sketch, "E1737", {"start": v(-7.6, 41.22) * mm, "end": v(-7.6, 41.32) * mm});
            skLineSegment(sketch, "E1738", {"start": v(-7.6, 41.32) * mm, "end": v(-7.6, 41.42) * mm});
            skLineSegment(sketch, "E1739", {"start": v(-7.6, 41.42) * mm, "end": v(-7.6, 41.51) * mm});
            skLineSegment(sketch, "E1740", {"start": v(-7.6, 41.51) * mm, "end": v(-7.6, 41.61) * mm});
            skLineSegment(sketch, "E1741", {"start": v(-7.6, 41.61) * mm, "end": v(-7.6, 41.71) * mm});
            skLineSegment(sketch, "E1742", {"start": v(-7.6, 41.71) * mm, "end": v(-7.6, 41.82) * mm});
            skLineSegment(sketch, "E1743", {"start": v(-7.6, 41.82) * mm, "end": v(-7.6, 41.92) * mm});
            skLineSegment(sketch, "E1744", {"start": v(-7.6, 41.92) * mm, "end": v(-7.6, 42.02) * mm});
            skLineSegment(sketch, "E1745", {"start": v(-7.6, 42.02) * mm, "end": v(-7.6, 42.13) * mm});
            skLineSegment(sketch, "E1746", {"start": v(-7.6, 42.13) * mm, "end": v(-7.6, 42.23) * mm});
            skLineSegment(sketch, "E1747", {"start": v(-7.6, 42.23) * mm, "end": v(-7.63, 42.27) * mm});
            skLineSegment(sketch, "E1748", {"start": v(-7.63, 42.27) * mm, "end": v(-8.6, 42.67) * mm});
            skLineSegment(sketch, "E1749", {"start": v(-8.6, 42.67) * mm, "end": v(-8.64, 42.66) * mm});
            skLineSegment(sketch, "E1750", {"start": v(-8.64, 42.66) * mm, "end": v(-8.72, 42.59) * mm});
            skLineSegment(sketch, "E1751", {"start": v(-8.72, 42.59) * mm, "end": v(-8.8, 42.52) * mm});
            skLineSegment(sketch, "E1752", {"start": v(-8.8, 42.52) * mm, "end": v(-8.87, 42.44) * mm});
            skLineSegment(sketch, "E1753", {"start": v(-8.87, 42.44) * mm, "end": v(-8.94, 42.37) * mm});
            skLineSegment(sketch, "E1754", {"start": v(-8.94, 42.37) * mm, "end": v(-9, 42.3) * mm});
            skLineSegment(sketch, "E1755", {"start": v(-9, 42.3) * mm, "end": v(-9.08, 42.23) * mm});
            skLineSegment(sketch, "E1756", {"start": v(-9.08, 42.23) * mm, "end": v(-9.15, 42.15) * mm});
            skLineSegment(sketch, "E1757", {"start": v(-9.15, 42.15) * mm, "end": v(-9.22, 42.08) * mm});
            skLineSegment(sketch, "E1758", {"start": v(-9.22, 42.08) * mm, "end": v(-9.28, 42.01) * mm});
            skLineSegment(sketch, "E1759", {"start": v(-9.28, 42.01) * mm, "end": v(-9.35, 41.94) * mm});
            skLineSegment(sketch, "E1760", {"start": v(-9.35, 41.94) * mm, "end": v(-9.41, 41.87) * mm});
            skLineSegment(sketch, "E1761", {"start": v(-9.41, 41.87) * mm, "end": v(-9.48, 41.8) * mm});
            skLineSegment(sketch, "E1762", {"start": v(-9.48, 41.8) * mm, "end": v(-9.54, 41.74) * mm});
            skLineSegment(sketch, "E1763", {"start": v(-9.54, 41.74) * mm, "end": v(-9.6, 41.67) * mm});
            skLineSegment(sketch, "E1764", {"start": v(-9.6, 41.67) * mm, "end": v(-9.66, 41.6) * mm});
            skLineSegment(sketch, "E1765", {"start": v(-9.66, 41.6) * mm, "end": v(-9.72, 41.54) * mm});
            skLineSegment(sketch, "E1766", {"start": v(-9.72, 41.54) * mm, "end": v(-9.77, 41.47) * mm});
            skLineSegment(sketch, "E1767", {"start": v(-9.77, 41.47) * mm, "end": v(-9.83, 41.4) * mm});
            skLineSegment(sketch, "E1768", {"start": v(-9.83, 41.4) * mm, "end": v(-9.88, 41.34) * mm});
            skLineSegment(sketch, "E1769", {"start": v(-9.88, 41.34) * mm, "end": v(-9.94, 41.28) * mm});
            skLineSegment(sketch, "E1770", {"start": v(-9.94, 41.28) * mm, "end": v(-10, 41.21) * mm});
            skLineSegment(sketch, "E1771", {"start": v(-10, 41.21) * mm, "end": v(-10.04, 41.15) * mm});
            skLineSegment(sketch, "E1772", {"start": v(-10.04, 41.15) * mm, "end": v(-10.1, 41.09) * mm});
            skLineSegment(sketch, "E1773", {"start": v(-10.1, 41.09) * mm, "end": v(-10.14, 41.03) * mm});
            skLineSegment(sketch, "E1774", {"start": v(-10.14, 41.03) * mm, "end": v(-10.2, 40.97) * mm});
            skLineSegment(sketch, "E1775", {"start": v(-10.2, 40.97) * mm, "end": v(-10.24, 40.9) * mm});
            skLineSegment(sketch, "E1776", {"start": v(-10.24, 40.9) * mm, "end": v(-10.28, 40.85) * mm});
            skLineSegment(sketch, "E1777", {"start": v(-10.28, 40.85) * mm, "end": v(-10.33, 40.8) * mm});
            skLineSegment(sketch, "E1778", {"start": v(-10.33, 40.8) * mm, "end": v(-10.37, 40.73) * mm});
            skLineSegment(sketch, "E1779", {"start": v(-10.37, 40.73) * mm, "end": v(-10.42, 40.68) * mm});
            skLineSegment(sketch, "E1780", {"start": v(-10.42, 40.68) * mm, "end": v(-10.46, 40.62) * mm});
            skLineSegment(sketch, "E1781", {"start": v(-10.46, 40.62) * mm, "end": v(-10.5, 40.56) * mm});
            skLineSegment(sketch, "E1782", {"start": v(-10.5, 40.56) * mm, "end": v(-10.54, 40.5) * mm});
            skLineSegment(sketch, "E1783", {"start": v(-10.54, 40.5) * mm, "end": v(-10.58, 40.46) * mm});
            skLineSegment(sketch, "E1784", {"start": v(-10.58, 40.46) * mm, "end": v(-10.62, 40.4) * mm});
            skLineSegment(sketch, "E1785", {"start": v(-10.62, 40.4) * mm, "end": v(-10.66, 40.35) * mm});
            skLineSegment(sketch, "E1786", {"start": v(-10.66, 40.35) * mm, "end": v(-10.7, 40.3) * mm});
            skLineSegment(sketch, "E1787", {"start": v(-10.7, 40.3) * mm, "end": v(-10.73, 40.25) * mm});
            skLineSegment(sketch, "E1788", {"start": v(-10.73, 40.25) * mm, "end": v(-10.76, 40.2) * mm});
            skLineSegment(sketch, "E1789", {"start": v(-10.76, 40.2) * mm, "end": v(-10.8, 40.15) * mm});
            skLineSegment(sketch, "E1790", {"start": v(-10.8, 40.15) * mm, "end": v(-11.02, 40.22) * mm});
            skLineSegment(sketch, "E1791", {"start": v(-11.02, 40.22) * mm, "end": v(-11.78, 40.5) * mm});
            skLineSegment(sketch, "E1792", {"start": v(-11.78, 40.5) * mm, "end": v(-12, 40.58) * mm});
            skLineSegment(sketch, "E1793", {"start": v(-12, 40.58) * mm, "end": v(-12, 40.64) * mm});
            skLineSegment(sketch, "E1794", {"start": v(-12, 40.64) * mm, "end": v(-11.99, 40.7) * mm});
            skLineSegment(sketch, "E1795", {"start": v(-11.99, 40.7) * mm, "end": v(-11.98, 40.76) * mm});
            skLineSegment(sketch, "E1796", {"start": v(-11.98, 40.76) * mm, "end": v(-11.98, 40.83) * mm});
            skLineSegment(sketch, "E1797", {"start": v(-11.98, 40.83) * mm, "end": v(-11.97, 40.9) * mm});
            skLineSegment(sketch, "E1798", {"start": v(-11.97, 40.9) * mm, "end": v(-11.97, 40.96) * mm});
            skLineSegment(sketch, "E1799", {"start": v(-11.97, 40.96) * mm, "end": v(-11.96, 41.02) * mm});
            skLineSegment(sketch, "E1800", {"start": v(-11.96, 41.02) * mm, "end": v(-11.96, 41.1) * mm});
            skLineSegment(sketch, "E1801", {"start": v(-11.96, 41.1) * mm, "end": v(-11.95, 41.16) * mm});
            skLineSegment(sketch, "E1802", {"start": v(-11.95, 41.16) * mm, "end": v(-11.95, 41.23) * mm});
            skLineSegment(sketch, "E1803", {"start": v(-11.95, 41.23) * mm, "end": v(-11.95, 41.3) * mm});
            skLineSegment(sketch, "E1804", {"start": v(-11.95, 41.3) * mm, "end": v(-11.95, 41.37) * mm});
            skLineSegment(sketch, "E1805", {"start": v(-11.95, 41.37) * mm, "end": v(-11.94, 41.45) * mm});
            skLineSegment(sketch, "E1806", {"start": v(-11.94, 41.45) * mm, "end": v(-11.94, 41.52) * mm});
            skLineSegment(sketch, "E1807", {"start": v(-11.94, 41.52) * mm, "end": v(-11.94, 41.6) * mm});
            skLineSegment(sketch, "E1808", {"start": v(-11.94, 41.6) * mm, "end": v(-11.94, 41.68) * mm});
            skLineSegment(sketch, "E1809", {"start": v(-11.94, 41.68) * mm, "end": v(-11.94, 41.76) * mm});
            skLineSegment(sketch, "E1810", {"start": v(-11.94, 41.76) * mm, "end": v(-11.94, 41.84) * mm});
            skLineSegment(sketch, "E1811", {"start": v(-11.94, 41.84) * mm, "end": v(-11.94, 41.92) * mm});
            skLineSegment(sketch, "E1812", {"start": v(-11.94, 41.92) * mm, "end": v(-11.94, 42) * mm});
            skLineSegment(sketch, "E1813", {"start": v(-11.94, 42) * mm, "end": v(-11.94, 42.08) * mm});
            skLineSegment(sketch, "E1814", {"start": v(-11.94, 42.08) * mm, "end": v(-11.94, 42.17) * mm});
            skLineSegment(sketch, "E1815", {"start": v(-11.94, 42.17) * mm, "end": v(-11.94, 42.25) * mm});
            skLineSegment(sketch, "E1816", {"start": v(-11.94, 42.25) * mm, "end": v(-11.94, 42.34) * mm});
            skLineSegment(sketch, "E1817", {"start": v(-11.94, 42.34) * mm, "end": v(-11.94, 42.43) * mm});
            skLineSegment(sketch, "E1818", {"start": v(-11.94, 42.43) * mm, "end": v(-11.95, 42.52) * mm});
            skLineSegment(sketch, "E1819", {"start": v(-11.95, 42.52) * mm, "end": v(-11.95, 42.6) * mm});
            skLineSegment(sketch, "E1820", {"start": v(-11.95, 42.6) * mm, "end": v(-11.96, 42.7) * mm});
            skLineSegment(sketch, "E1821", {"start": v(-11.96, 42.7) * mm, "end": v(-11.96, 42.8) * mm});
            skLineSegment(sketch, "E1822", {"start": v(-11.96, 42.8) * mm, "end": v(-11.96, 42.89) * mm});
            skLineSegment(sketch, "E1823", {"start": v(-11.96, 42.89) * mm, "end": v(-11.97, 42.98) * mm});
            skLineSegment(sketch, "E1824", {"start": v(-11.97, 42.98) * mm, "end": v(-11.98, 43.08) * mm});
            skLineSegment(sketch, "E1825", {"start": v(-11.98, 43.08) * mm, "end": v(-11.98, 43.18) * mm});
            skLineSegment(sketch, "E1826", {"start": v(-11.98, 43.18) * mm, "end": v(-11.99, 43.28) * mm});
            skLineSegment(sketch, "E1827", {"start": v(-11.99, 43.28) * mm, "end": v(-12, 43.38) * mm});
            skLineSegment(sketch, "E1828", {"start": v(-12, 43.38) * mm, "end": v(-12, 43.48) * mm});
            skLineSegment(sketch, "E1829", {"start": v(-12, 43.48) * mm, "end": v(-12.02, 43.58) * mm});
            skLineSegment(sketch, "E1830", {"start": v(-12.02, 43.58) * mm, "end": v(-12.02, 43.68) * mm});
            skLineSegment(sketch, "E1831", {"start": v(-12.02, 43.68) * mm, "end": v(-12.04, 43.79) * mm});
            skLineSegment(sketch, "E1832", {"start": v(-12.04, 43.79) * mm, "end": v(-12.05, 43.9) * mm});
            skLineSegment(sketch, "E1833", {"start": v(-12.05, 43.9) * mm, "end": v(-12.08, 43.93) * mm});
            skLineSegment(sketch, "E1834", {"start": v(-12.08, 43.93) * mm, "end": v(-13.07, 44.24) * mm});
            skLineSegment(sketch, "E1835", {"start": v(-13.07, 44.24) * mm, "end": v(-13.12, 44.23) * mm});
            skLineSegment(sketch, "E1836", {"start": v(-13.12, 44.23) * mm, "end": v(-13.2, 44.15) * mm});
            skLineSegment(sketch, "E1837", {"start": v(-13.2, 44.15) * mm, "end": v(-13.26, 44.07) * mm});
            skLineSegment(sketch, "E1838", {"start": v(-13.26, 44.07) * mm, "end": v(-13.33, 43.99) * mm});
            skLineSegment(sketch, "E1839", {"start": v(-13.33, 43.99) * mm, "end": v(-13.4, 43.9) * mm});
            skLineSegment(sketch, "E1840", {"start": v(-13.4, 43.9) * mm, "end": v(-13.46, 43.83) * mm});
            skLineSegment(sketch, "E1841", {"start": v(-13.46, 43.83) * mm, "end": v(-13.52, 43.75) * mm});
            skLineSegment(sketch, "E1842", {"start": v(-13.52, 43.75) * mm, "end": v(-13.58, 43.68) * mm});
            skLineSegment(sketch, "E1843", {"start": v(-13.58, 43.68) * mm, "end": v(-13.64, 43.6) * mm});
            skLineSegment(sketch, "E1844", {"start": v(-13.64, 43.6) * mm, "end": v(-13.7, 43.52) * mm});
            skLineSegment(sketch, "E1845", {"start": v(-13.7, 43.52) * mm, "end": v(-13.76, 43.45) * mm});
            skLineSegment(sketch, "E1846", {"start": v(-13.76, 43.45) * mm, "end": v(-13.82, 43.37) * mm});
            skLineSegment(sketch, "E1847", {"start": v(-13.82, 43.37) * mm, "end": v(-13.87, 43.3) * mm});
            skLineSegment(sketch, "E1848", {"start": v(-13.87, 43.3) * mm, "end": v(-13.93, 43.23) * mm});
            skLineSegment(sketch, "E1849", {"start": v(-13.93, 43.23) * mm, "end": v(-13.98, 43.15) * mm});
            skLineSegment(sketch, "E1850", {"start": v(-13.98, 43.15) * mm, "end": v(-14.04, 43.08) * mm});
            skLineSegment(sketch, "E1851", {"start": v(-14.04, 43.08) * mm, "end": v(-14.1, 43) * mm});
            skLineSegment(sketch, "E1852", {"start": v(-14.1, 43) * mm, "end": v(-14.14, 42.94) * mm});
            skLineSegment(sketch, "E1853", {"start": v(-14.14, 42.94) * mm, "end": v(-14.2, 42.87) * mm});
            skLineSegment(sketch, "E1854", {"start": v(-14.2, 42.87) * mm, "end": v(-14.24, 42.8) * mm});
            skLineSegment(sketch, "E1855", {"start": v(-14.24, 42.8) * mm, "end": v(-14.29, 42.73) * mm});
            skLineSegment(sketch, "E1856", {"start": v(-14.29, 42.73) * mm, "end": v(-14.34, 42.66) * mm});
            skLineSegment(sketch, "E1857", {"start": v(-14.34, 42.66) * mm, "end": v(-14.38, 42.6) * mm});
            skLineSegment(sketch, "E1858", {"start": v(-14.38, 42.6) * mm, "end": v(-14.43, 42.53) * mm});
            skLineSegment(sketch, "E1859", {"start": v(-14.43, 42.53) * mm, "end": v(-14.47, 42.47) * mm});
            skLineSegment(sketch, "E1860", {"start": v(-14.47, 42.47) * mm, "end": v(-14.51, 42.4) * mm});
            skLineSegment(sketch, "E1861", {"start": v(-14.51, 42.4) * mm, "end": v(-14.55, 42.34) * mm});
            skLineSegment(sketch, "E1862", {"start": v(-14.55, 42.34) * mm, "end": v(-14.6, 42.27) * mm});
            skLineSegment(sketch, "E1863", {"start": v(-14.6, 42.27) * mm, "end": v(-14.64, 42.21) * mm});
            skLineSegment(sketch, "E1864", {"start": v(-14.64, 42.21) * mm, "end": v(-14.68, 42.15) * mm});
            skLineSegment(sketch, "E1865", {"start": v(-14.68, 42.15) * mm, "end": v(-14.71, 42.09) * mm});
            skLineSegment(sketch, "E1866", {"start": v(-14.71, 42.09) * mm, "end": v(-14.75, 42.03) * mm});
            skLineSegment(sketch, "E1867", {"start": v(-14.75, 42.03) * mm, "end": v(-14.79, 41.97) * mm});
            skLineSegment(sketch, "E1868", {"start": v(-14.79, 41.97) * mm, "end": v(-14.82, 41.91) * mm});
            skLineSegment(sketch, "E1869", {"start": v(-14.82, 41.91) * mm, "end": v(-14.86, 41.86) * mm});
            skLineSegment(sketch, "E1870", {"start": v(-14.86, 41.86) * mm, "end": v(-14.89, 41.8) * mm});
            skLineSegment(sketch, "E1871", {"start": v(-14.89, 41.8) * mm, "end": v(-14.92, 41.74) * mm});
            skLineSegment(sketch, "E1872", {"start": v(-14.92, 41.74) * mm, "end": v(-14.95, 41.69) * mm});
            skLineSegment(sketch, "E1873", {"start": v(-14.95, 41.69) * mm, "end": v(-14.98, 41.64) * mm});
            skLineSegment(sketch, "E1874", {"start": v(-14.98, 41.64) * mm, "end": v(-15.01, 41.58) * mm});
            skLineSegment(sketch, "E1875", {"start": v(-15.01, 41.58) * mm, "end": v(-15.04, 41.53) * mm});
            skLineSegment(sketch, "E1876", {"start": v(-15.04, 41.53) * mm, "end": v(-15.27, 41.58) * mm});
            skLineSegment(sketch, "E1877", {"start": v(-15.27, 41.58) * mm, "end": v(-16.05, 41.79) * mm});
            skLineSegment(sketch, "E1878", {"start": v(-16.05, 41.79) * mm, "end": v(-16.28, 41.86) * mm});
            skLineSegment(sketch, "E1879", {"start": v(-16.28, 41.86) * mm, "end": v(-16.28, 41.92) * mm});
            skLineSegment(sketch, "E1880", {"start": v(-16.28, 41.92) * mm, "end": v(-16.28, 41.98) * mm});
            skLineSegment(sketch, "E1881", {"start": v(-16.28, 41.98) * mm, "end": v(-16.28, 42.04) * mm});
            skLineSegment(sketch, "E1882", {"start": v(-16.28, 42.04) * mm, "end": v(-16.28, 42.1) * mm});
            skLineSegment(sketch, "E1883", {"start": v(-16.28, 42.1) * mm, "end": v(-16.28, 42.17) * mm});
            skLineSegment(sketch, "E1884", {"start": v(-16.28, 42.17) * mm, "end": v(-16.28, 42.23) * mm});
            skLineSegment(sketch, "E1885", {"start": v(-16.28, 42.23) * mm, "end": v(-16.28, 42.3) * mm});
            skLineSegment(sketch, "E1886", {"start": v(-16.28, 42.3) * mm, "end": v(-16.28, 42.37) * mm});
            skLineSegment(sketch, "E1887", {"start": v(-16.28, 42.37) * mm, "end": v(-16.29, 42.43) * mm});
            skLineSegment(sketch, "E1888", {"start": v(-16.29, 42.43) * mm, "end": v(-16.3, 42.5) * mm});
            skLineSegment(sketch, "E1889", {"start": v(-16.3, 42.5) * mm, "end": v(-16.3, 42.58) * mm});
            skLineSegment(sketch, "E1890", {"start": v(-16.3, 42.58) * mm, "end": v(-16.3, 42.65) * mm});
            skLineSegment(sketch, "E1891", {"start": v(-16.3, 42.65) * mm, "end": v(-16.3, 42.72) * mm});
            skLineSegment(sketch, "E1892", {"start": v(-16.3, 42.72) * mm, "end": v(-16.3, 42.8) * mm});
            skLineSegment(sketch, "E1893", {"start": v(-16.3, 42.8) * mm, "end": v(-16.31, 42.87) * mm});
            skLineSegment(sketch, "E1894", {"start": v(-16.31, 42.87) * mm, "end": v(-16.32, 42.95) * mm});
            skLineSegment(sketch, "E1895", {"start": v(-16.32, 42.95) * mm, "end": v(-16.32, 43.03) * mm});
            skLineSegment(sketch, "E1896", {"start": v(-16.32, 43.03) * mm, "end": v(-16.33, 43.1) * mm});
            skLineSegment(sketch, "E1897", {"start": v(-16.33, 43.1) * mm, "end": v(-16.34, 43.19) * mm});
            skLineSegment(sketch, "E1898", {"start": v(-16.34, 43.19) * mm, "end": v(-16.34, 43.27) * mm});
            skLineSegment(sketch, "E1899", {"start": v(-16.34, 43.27) * mm, "end": v(-16.35, 43.36) * mm});
            skLineSegment(sketch, "E1900", {"start": v(-16.35, 43.36) * mm, "end": v(-16.36, 43.44) * mm});
            skLineSegment(sketch, "E1901", {"start": v(-16.36, 43.44) * mm, "end": v(-16.37, 43.52) * mm});
            skLineSegment(sketch, "E1902", {"start": v(-16.37, 43.52) * mm, "end": v(-16.38, 43.61) * mm});
            skLineSegment(sketch, "E1903", {"start": v(-16.38, 43.61) * mm, "end": v(-16.4, 43.7) * mm});
            skLineSegment(sketch, "E1904", {"start": v(-16.4, 43.7) * mm, "end": v(-16.4, 43.79) * mm});
            skLineSegment(sketch, "E1905", {"start": v(-16.4, 43.79) * mm, "end": v(-16.41, 43.88) * mm});
            skLineSegment(sketch, "E1906", {"start": v(-16.41, 43.88) * mm, "end": v(-16.43, 43.97) * mm});
            skLineSegment(sketch, "E1907", {"start": v(-16.43, 43.97) * mm, "end": v(-16.44, 44.06) * mm});
            skLineSegment(sketch, "E1908", {"start": v(-16.44, 44.06) * mm, "end": v(-16.45, 44.15) * mm});
            skLineSegment(sketch, "E1909", {"start": v(-16.45, 44.15) * mm, "end": v(-16.47, 44.25) * mm});
            skLineSegment(sketch, "E1910", {"start": v(-16.47, 44.25) * mm, "end": v(-16.48, 44.35) * mm});
            skLineSegment(sketch, "E1911", {"start": v(-16.48, 44.35) * mm, "end": v(-16.5, 44.44) * mm});
            skLineSegment(sketch, "E1912", {"start": v(-16.5, 44.44) * mm, "end": v(-16.51, 44.54) * mm});
            skLineSegment(sketch, "E1913", {"start": v(-16.51, 44.54) * mm, "end": v(-16.53, 44.64) * mm});
            skLineSegment(sketch, "E1914", {"start": v(-16.53, 44.64) * mm, "end": v(-16.55, 44.74) * mm});
            skLineSegment(sketch, "E1915", {"start": v(-16.55, 44.74) * mm, "end": v(-16.56, 44.84) * mm});
            skLineSegment(sketch, "E1916", {"start": v(-16.56, 44.84) * mm, "end": v(-16.58, 44.94) * mm});
            skLineSegment(sketch, "E1917", {"start": v(-16.58, 44.94) * mm, "end": v(-16.6, 45.05) * mm});
            skLineSegment(sketch, "E1918", {"start": v(-16.6, 45.05) * mm, "end": v(-16.62, 45.15) * mm});
            skLineSegment(sketch, "E1919", {"start": v(-16.62, 45.15) * mm, "end": v(-16.66, 45.18) * mm});
            skLineSegment(sketch, "E1920", {"start": v(-16.66, 45.18) * mm, "end": v(-17.68, 45.4) * mm});
            skLineSegment(sketch, "E1921", {"start": v(-17.68, 45.4) * mm, "end": v(-17.73, 45.39) * mm});
            skLineSegment(sketch, "E1922", {"start": v(-17.73, 45.39) * mm, "end": v(-17.79, 45.3) * mm});
            skLineSegment(sketch, "E1923", {"start": v(-17.79, 45.3) * mm, "end": v(-17.85, 45.21) * mm});
            skLineSegment(sketch, "E1924", {"start": v(-17.85, 45.21) * mm, "end": v(-17.9, 45.13) * mm});
            skLineSegment(sketch, "E1925", {"start": v(-17.9, 45.13) * mm, "end": v(-17.96, 45.04) * mm});
            skLineSegment(sketch, "E1926", {"start": v(-17.96, 45.04) * mm, "end": v(-18.02, 44.96) * mm});
            skLineSegment(sketch, "E1927", {"start": v(-18.02, 44.96) * mm, "end": v(-18.08, 44.88) * mm});
            skLineSegment(sketch, "E1928", {"start": v(-18.08, 44.88) * mm, "end": v(-18.13, 44.8) * mm});
            skLineSegment(sketch, "E1929", {"start": v(-18.13, 44.8) * mm, "end": v(-18.19, 44.71) * mm});
            skLineSegment(sketch, "E1930", {"start": v(-18.19, 44.71) * mm, "end": v(-18.24, 44.63) * mm});
            skLineSegment(sketch, "E1931", {"start": v(-18.24, 44.63) * mm, "end": v(-18.3, 44.55) * mm});
            skLineSegment(sketch, "E1932", {"start": v(-18.3, 44.55) * mm, "end": v(-18.34, 44.47) * mm});
            skLineSegment(sketch, "E1933", {"start": v(-18.34, 44.47) * mm, "end": v(-18.4, 44.4) * mm});
            skLineSegment(sketch, "E1934", {"start": v(-18.4, 44.4) * mm, "end": v(-18.44, 44.31) * mm});
            skLineSegment(sketch, "E1935", {"start": v(-18.44, 44.31) * mm, "end": v(-18.49, 44.24) * mm});
            skLineSegment(sketch, "E1936", {"start": v(-18.49, 44.24) * mm, "end": v(-18.53, 44.16) * mm});
            skLineSegment(sketch, "E1937", {"start": v(-18.53, 44.16) * mm, "end": v(-18.58, 44.09) * mm});
            skLineSegment(sketch, "E1938", {"start": v(-18.58, 44.09) * mm, "end": v(-18.62, 44.01) * mm});
            skLineSegment(sketch, "E1939", {"start": v(-18.62, 44.01) * mm, "end": v(-18.67, 43.94) * mm});
            skLineSegment(sketch, "E1940", {"start": v(-18.67, 43.94) * mm, "end": v(-18.71, 43.86) * mm});
            skLineSegment(sketch, "E1941", {"start": v(-18.71, 43.86) * mm, "end": v(-18.75, 43.8) * mm});
            skLineSegment(sketch, "E1942", {"start": v(-18.75, 43.8) * mm, "end": v(-18.8, 43.72) * mm});
            skLineSegment(sketch, "E1943", {"start": v(-18.8, 43.72) * mm, "end": v(-18.83, 43.65) * mm});
            skLineSegment(sketch, "E1944", {"start": v(-18.83, 43.65) * mm, "end": v(-18.87, 43.58) * mm});
            skLineSegment(sketch, "E1945", {"start": v(-18.87, 43.58) * mm, "end": v(-18.9, 43.5) * mm});
            skLineSegment(sketch, "E1946", {"start": v(-18.9, 43.5) * mm, "end": v(-18.95, 43.44) * mm});
            skLineSegment(sketch, "E1947", {"start": v(-18.95, 43.44) * mm, "end": v(-18.98, 43.37) * mm});
            skLineSegment(sketch, "E1948", {"start": v(-18.98, 43.37) * mm, "end": v(-19.02, 43.3) * mm});
            skLineSegment(sketch, "E1949", {"start": v(-19.02, 43.3) * mm, "end": v(-19.05, 43.24) * mm});
            skLineSegment(sketch, "E1950", {"start": v(-19.05, 43.24) * mm, "end": v(-19.08, 43.18) * mm});
            skLineSegment(sketch, "E1951", {"start": v(-19.08, 43.18) * mm, "end": v(-19.12, 43.11) * mm});
            skLineSegment(sketch, "E1952", {"start": v(-19.12, 43.11) * mm, "end": v(-19.15, 43.05) * mm});
            skLineSegment(sketch, "E1953", {"start": v(-19.15, 43.05) * mm, "end": v(-19.18, 42.99) * mm});
            skLineSegment(sketch, "E1954", {"start": v(-19.18, 42.99) * mm, "end": v(-19.2, 42.93) * mm});
            skLineSegment(sketch, "E1955", {"start": v(-19.2, 42.93) * mm, "end": v(-19.24, 42.87) * mm});
            skLineSegment(sketch, "E1956", {"start": v(-19.24, 42.87) * mm, "end": v(-19.27, 42.8) * mm});
            skLineSegment(sketch, "E1957", {"start": v(-19.27, 42.8) * mm, "end": v(-19.3, 42.75) * mm});
            skLineSegment(sketch, "E1958", {"start": v(-19.3, 42.75) * mm, "end": v(-19.32, 42.7) * mm});
            skLineSegment(sketch, "E1959", {"start": v(-19.32, 42.7) * mm, "end": v(-19.35, 42.64) * mm});
            skLineSegment(sketch, "E1960", {"start": v(-19.35, 42.64) * mm, "end": v(-19.37, 42.58) * mm});
            skLineSegment(sketch, "E1961", {"start": v(-19.37, 42.58) * mm, "end": v(-19.4, 42.53) * mm});
            skLineSegment(sketch, "E1962", {"start": v(-19.4, 42.53) * mm, "end": v(-19.63, 42.56) * mm});
            skLineSegment(sketch, "E1963", {"start": v(-19.63, 42.56) * mm, "end": v(-20.42, 42.7) * mm});
            skLineSegment(sketch, "E1964", {"start": v(-20.42, 42.7) * mm, "end": v(-20.65, 42.74) * mm});
            skLineSegment(sketch, "E1965", {"start": v(-20.65, 42.74) * mm, "end": v(-20.66, 42.8) * mm});
            skLineSegment(sketch, "E1966", {"start": v(-20.66, 42.8) * mm, "end": v(-20.66, 42.86) * mm});
            skLineSegment(sketch, "E1967", {"start": v(-20.66, 42.86) * mm, "end": v(-20.67, 42.92) * mm});
            skLineSegment(sketch, "E1968", {"start": v(-20.67, 42.92) * mm, "end": v(-20.68, 42.98) * mm});
            skLineSegment(sketch, "E1969", {"start": v(-20.68, 42.98) * mm, "end": v(-20.68, 43.05) * mm});
            skLineSegment(sketch, "E1970", {"start": v(-20.68, 43.05) * mm, "end": v(-20.7, 43.11) * mm});
            skLineSegment(sketch, "E1971", {"start": v(-20.7, 43.11) * mm, "end": v(-20.7, 43.18) * mm});
            skLineSegment(sketch, "E1972", {"start": v(-20.7, 43.18) * mm, "end": v(-20.7, 43.25) * mm});
            skLineSegment(sketch, "E1973", {"start": v(-20.7, 43.25) * mm, "end": v(-20.72, 43.32) * mm});
            skLineSegment(sketch, "E1974", {"start": v(-20.72, 43.32) * mm, "end": v(-20.73, 43.39) * mm});
            skLineSegment(sketch, "E1975", {"start": v(-20.73, 43.39) * mm, "end": v(-20.73, 43.46) * mm});
            skLineSegment(sketch, "E1976", {"start": v(-20.73, 43.46) * mm, "end": v(-20.75, 43.53) * mm});
            skLineSegment(sketch, "E1977", {"start": v(-20.75, 43.53) * mm, "end": v(-20.76, 43.6) * mm});
            skLineSegment(sketch, "E1978", {"start": v(-20.76, 43.6) * mm, "end": v(-20.77, 43.68) * mm});
            skLineSegment(sketch, "E1979", {"start": v(-20.77, 43.68) * mm, "end": v(-20.78, 43.75) * mm});
            skLineSegment(sketch, "E1980", {"start": v(-20.78, 43.75) * mm, "end": v(-20.8, 43.83) * mm});
            skLineSegment(sketch, "E1981", {"start": v(-20.8, 43.83) * mm, "end": v(-20.8, 43.9) * mm});
            skLineSegment(sketch, "E1982", {"start": v(-20.8, 43.9) * mm, "end": v(-20.82, 43.98) * mm});
            skLineSegment(sketch, "E1983", {"start": v(-20.82, 43.98) * mm, "end": v(-20.83, 44.06) * mm});
            skLineSegment(sketch, "E1984", {"start": v(-20.83, 44.06) * mm, "end": v(-20.85, 44.14) * mm});
            skLineSegment(sketch, "E1985", {"start": v(-20.85, 44.14) * mm, "end": v(-20.86, 44.23) * mm});
            skLineSegment(sketch, "E1986", {"start": v(-20.86, 44.23) * mm, "end": v(-20.88, 44.3) * mm});
            skLineSegment(sketch, "E1987", {"start": v(-20.88, 44.3) * mm, "end": v(-20.9, 44.4) * mm});
            skLineSegment(sketch, "E1988", {"start": v(-20.9, 44.4) * mm, "end": v(-20.91, 44.48) * mm});
            skLineSegment(sketch, "E1989", {"start": v(-20.91, 44.48) * mm, "end": v(-20.93, 44.57) * mm});
            skLineSegment(sketch, "E1990", {"start": v(-20.93, 44.57) * mm, "end": v(-20.95, 44.65) * mm});
            skLineSegment(sketch, "E1991", {"start": v(-20.95, 44.65) * mm, "end": v(-20.97, 44.74) * mm});
            skLineSegment(sketch, "E1992", {"start": v(-20.97, 44.74) * mm, "end": v(-21, 44.83) * mm});
            skLineSegment(sketch, "E1993", {"start": v(-21, 44.83) * mm, "end": v(-21.01, 44.92) * mm});
            skLineSegment(sketch, "E1994", {"start": v(-21.01, 44.92) * mm, "end": v(-21.03, 45.01) * mm});
            skLineSegment(sketch, "E1995", {"start": v(-21.03, 45.01) * mm, "end": v(-21.06, 45.1) * mm});
            skLineSegment(sketch, "E1996", {"start": v(-21.06, 45.1) * mm, "end": v(-21.08, 45.2) * mm});
            skLineSegment(sketch, "E1997", {"start": v(-21.08, 45.2) * mm, "end": v(-21.1, 45.3) * mm});
            skLineSegment(sketch, "E1998", {"start": v(-21.1, 45.3) * mm, "end": v(-21.13, 45.4) * mm});
            skLineSegment(sketch, "E1999", {"start": v(-21.13, 45.4) * mm, "end": v(-21.15, 45.49) * mm});
            skLineSegment(sketch, "E2000", {"start": v(-21.15, 45.49) * mm, "end": v(-21.18, 45.59) * mm});
            skLineSegment(sketch, "E2001", {"start": v(-21.18, 45.59) * mm, "end": v(-21.2, 45.69) * mm});
            skLineSegment(sketch, "E2002", {"start": v(-21.2, 45.69) * mm, "end": v(-21.24, 45.79) * mm});
            skLineSegment(sketch, "E2003", {"start": v(-21.24, 45.79) * mm, "end": v(-21.26, 45.89) * mm});
            skLineSegment(sketch, "E2004", {"start": v(-21.26, 45.89) * mm, "end": v(-21.3, 46) * mm});
            skLineSegment(sketch, "E2005", {"start": v(-21.3, 46) * mm, "end": v(-21.33, 46.02) * mm});
            skLineSegment(sketch, "E2006", {"start": v(-21.33, 46.02) * mm, "end": v(-22.37, 46.15) * mm});
            skLineSegment(sketch, "E2007", {"start": v(-22.37, 46.15) * mm, "end": v(-22.41, 46.13) * mm});
            skLineSegment(sketch, "E2008", {"start": v(-22.41, 46.13) * mm, "end": v(-22.47, 46.04) * mm});
            skLineSegment(sketch, "E2009", {"start": v(-22.47, 46.04) * mm, "end": v(-22.52, 45.94) * mm});
            skLineSegment(sketch, "E2010", {"start": v(-22.52, 45.94) * mm, "end": v(-22.57, 45.85) * mm});
            skLineSegment(sketch, "E2011", {"start": v(-22.57, 45.85) * mm, "end": v(-22.62, 45.76) * mm});
            skLineSegment(sketch, "E2012", {"start": v(-22.62, 45.76) * mm, "end": v(-22.67, 45.68) * mm});
            skLineSegment(sketch, "E2013", {"start": v(-22.67, 45.68) * mm, "end": v(-22.72, 45.59) * mm});
            skLineSegment(sketch, "E2014", {"start": v(-22.72, 45.59) * mm, "end": v(-22.77, 45.5) * mm});
            skLineSegment(sketch, "E2015", {"start": v(-22.77, 45.5) * mm, "end": v(-22.81, 45.41) * mm});
            skLineSegment(sketch, "E2016", {"start": v(-22.81, 45.41) * mm, "end": v(-22.86, 45.33) * mm});
            skLineSegment(sketch, "E2017", {"start": v(-22.86, 45.33) * mm, "end": v(-22.9, 45.24) * mm});
            skLineSegment(sketch, "E2018", {"start": v(-22.9, 45.24) * mm, "end": v(-22.94, 45.16) * mm});
            skLineSegment(sketch, "E2019", {"start": v(-22.94, 45.16) * mm, "end": v(-22.99, 45.08) * mm});
            skLineSegment(sketch, "E2020", {"start": v(-22.99, 45.08) * mm, "end": v(-23.03, 45) * mm});
            skLineSegment(sketch, "E2021", {"start": v(-23.03, 45) * mm, "end": v(-23.07, 44.91) * mm});
            skLineSegment(sketch, "E2022", {"start": v(-23.07, 44.91) * mm, "end": v(-23.1, 44.83) * mm});
            skLineSegment(sketch, "E2023", {"start": v(-23.1, 44.83) * mm, "end": v(-23.15, 44.75) * mm});
            skLineSegment(sketch, "E2024", {"start": v(-23.15, 44.75) * mm, "end": v(-23.18, 44.68) * mm});
            skLineSegment(sketch, "E2025", {"start": v(-23.18, 44.68) * mm, "end": v(-23.22, 44.6) * mm});
            skLineSegment(sketch, "E2026", {"start": v(-23.22, 44.6) * mm, "end": v(-23.26, 44.52) * mm});
            skLineSegment(sketch, "E2027", {"start": v(-23.26, 44.52) * mm, "end": v(-23.3, 44.45) * mm});
            skLineSegment(sketch, "E2028", {"start": v(-23.3, 44.45) * mm, "end": v(-23.33, 44.37) * mm});
            skLineSegment(sketch, "E2029", {"start": v(-23.33, 44.37) * mm, "end": v(-23.36, 44.3) * mm});
            skLineSegment(sketch, "E2030", {"start": v(-23.36, 44.3) * mm, "end": v(-23.4, 44.22) * mm});
            skLineSegment(sketch, "E2031", {"start": v(-23.4, 44.22) * mm, "end": v(-23.42, 44.15) * mm});
            skLineSegment(sketch, "E2032", {"start": v(-23.42, 44.15) * mm, "end": v(-23.45, 44.08) * mm});
            skLineSegment(sketch, "E2033", {"start": v(-23.45, 44.08) * mm, "end": v(-23.48, 44) * mm});
            skLineSegment(sketch, "E2034", {"start": v(-23.48, 44) * mm, "end": v(-23.51, 43.94) * mm});
            skLineSegment(sketch, "E2035", {"start": v(-23.51, 43.94) * mm, "end": v(-23.54, 43.87) * mm});
            skLineSegment(sketch, "E2036", {"start": v(-23.54, 43.87) * mm, "end": v(-23.57, 43.8) * mm});
            skLineSegment(sketch, "E2037", {"start": v(-23.57, 43.8) * mm, "end": v(-23.6, 43.74) * mm});
            skLineSegment(sketch, "E2038", {"start": v(-23.6, 43.74) * mm, "end": v(-23.62, 43.67) * mm});
            skLineSegment(sketch, "E2039", {"start": v(-23.62, 43.67) * mm, "end": v(-23.65, 43.6) * mm});
            skLineSegment(sketch, "E2040", {"start": v(-23.65, 43.6) * mm, "end": v(-23.67, 43.55) * mm});
            skLineSegment(sketch, "E2041", {"start": v(-23.67, 43.55) * mm, "end": v(-23.7, 43.48) * mm});
            skLineSegment(sketch, "E2042", {"start": v(-23.7, 43.48) * mm, "end": v(-23.72, 43.42) * mm});
            skLineSegment(sketch, "E2043", {"start": v(-23.72, 43.42) * mm, "end": v(-23.74, 43.36) * mm});
            skLineSegment(sketch, "E2044", {"start": v(-23.74, 43.36) * mm, "end": v(-23.76, 43.3) * mm});
            skLineSegment(sketch, "E2045", {"start": v(-23.76, 43.3) * mm, "end": v(-23.78, 43.24) * mm});
            skLineSegment(sketch, "E2046", {"start": v(-23.78, 43.24) * mm, "end": v(-23.8, 43.19) * mm});
            skLineSegment(sketch, "E2047", {"start": v(-23.8, 43.19) * mm, "end": v(-23.82, 43.13) * mm});
            skLineSegment(sketch, "E2048", {"start": v(-23.82, 43.13) * mm, "end": v(-24.06, 43.14) * mm});
            skLineSegment(sketch, "E2049", {"start": v(-24.06, 43.14) * mm, "end": v(-24.86, 43.2) * mm});
            skLineSegment(sketch, "E2050", {"start": v(-24.86, 43.2) * mm, "end": v(-25.1, 43.23) * mm});
            skLineSegment(sketch, "E2051", {"start": v(-25.1, 43.23) * mm, "end": v(-25.1, 43.29) * mm});
            skLineSegment(sketch, "E2052", {"start": v(-25.1, 43.29) * mm, "end": v(-25.11, 43.35) * mm});
            skLineSegment(sketch, "E2053", {"start": v(-25.11, 43.35) * mm, "end": v(-25.13, 43.4) * mm});
            skLineSegment(sketch, "E2054", {"start": v(-25.13, 43.4) * mm, "end": v(-25.14, 43.47) * mm});
            skLineSegment(sketch, "E2055", {"start": v(-25.14, 43.47) * mm, "end": v(-25.15, 43.53) * mm});
            skLineSegment(sketch, "E2056", {"start": v(-25.15, 43.53) * mm, "end": v(-25.16, 43.6) * mm});
            skLineSegment(sketch, "E2057", {"start": v(-25.16, 43.6) * mm, "end": v(-25.18, 43.66) * mm});
            skLineSegment(sketch, "E2058", {"start": v(-25.18, 43.66) * mm, "end": v(-25.2, 43.73) * mm});
            skLineSegment(sketch, "E2059", {"start": v(-25.2, 43.73) * mm, "end": v(-25.2, 43.8) * mm});
            skLineSegment(sketch, "E2060", {"start": v(-25.2, 43.8) * mm, "end": v(-25.22, 43.86) * mm});
            skLineSegment(sketch, "E2061", {"start": v(-25.22, 43.86) * mm, "end": v(-25.24, 43.93) * mm});
            skLineSegment(sketch, "E2062", {"start": v(-25.24, 43.93) * mm, "end": v(-25.25, 44) * mm});
            skLineSegment(sketch, "E2063", {"start": v(-25.25, 44) * mm, "end": v(-25.27, 44.08) * mm});
            skLineSegment(sketch, "E2064", {"start": v(-25.27, 44.08) * mm, "end": v(-25.29, 44.15) * mm});
            skLineSegment(sketch, "E2065", {"start": v(-25.29, 44.15) * mm, "end": v(-25.3, 44.22) * mm});
            skLineSegment(sketch, "E2066", {"start": v(-25.3, 44.22) * mm, "end": v(-25.33, 44.3) * mm});
            skLineSegment(sketch, "E2067", {"start": v(-25.33, 44.3) * mm, "end": v(-25.35, 44.37) * mm});
            skLineSegment(sketch, "E2068", {"start": v(-25.35, 44.37) * mm, "end": v(-25.37, 44.45) * mm});
            skLineSegment(sketch, "E2069", {"start": v(-25.37, 44.45) * mm, "end": v(-25.4, 44.53) * mm});
            skLineSegment(sketch, "E2070", {"start": v(-25.4, 44.53) * mm, "end": v(-25.41, 44.6) * mm});
            skLineSegment(sketch, "E2071", {"start": v(-25.41, 44.6) * mm, "end": v(-25.43, 44.7) * mm});
            skLineSegment(sketch, "E2072", {"start": v(-25.43, 44.7) * mm, "end": v(-25.46, 44.77) * mm});
            skLineSegment(sketch, "E2073", {"start": v(-25.46, 44.77) * mm, "end": v(-25.48, 44.85) * mm});
            skLineSegment(sketch, "E2074", {"start": v(-25.48, 44.85) * mm, "end": v(-25.5, 44.94) * mm});
            skLineSegment(sketch, "E2075", {"start": v(-25.5, 44.94) * mm, "end": v(-25.53, 45.02) * mm});
            skLineSegment(sketch, "E2076", {"start": v(-25.53, 45.02) * mm, "end": v(-25.56, 45.1) * mm});
            skLineSegment(sketch, "E2077", {"start": v(-25.56, 45.1) * mm, "end": v(-25.59, 45.2) * mm});
            skLineSegment(sketch, "E2078", {"start": v(-25.59, 45.2) * mm, "end": v(-25.62, 45.28) * mm});
            skLineSegment(sketch, "E2079", {"start": v(-25.62, 45.28) * mm, "end": v(-25.65, 45.37) * mm});
            skLineSegment(sketch, "E2080", {"start": v(-25.65, 45.37) * mm, "end": v(-25.67, 45.46) * mm});
            skLineSegment(sketch, "E2081", {"start": v(-25.67, 45.46) * mm, "end": v(-25.7, 45.55) * mm});
            skLineSegment(sketch, "E2082", {"start": v(-25.7, 45.55) * mm, "end": v(-25.74, 45.64) * mm});
            skLineSegment(sketch, "E2083", {"start": v(-25.74, 45.64) * mm, "end": v(-25.77, 45.73) * mm});
            skLineSegment(sketch, "E2084", {"start": v(-25.77, 45.73) * mm, "end": v(-25.8, 45.83) * mm});
            skLineSegment(sketch, "E2085", {"start": v(-25.8, 45.83) * mm, "end": v(-25.84, 45.92) * mm});
            skLineSegment(sketch, "E2086", {"start": v(-25.84, 45.92) * mm, "end": v(-25.87, 46.02) * mm});
            skLineSegment(sketch, "E2087", {"start": v(-25.87, 46.02) * mm, "end": v(-25.9, 46.11) * mm});
            skLineSegment(sketch, "E2088", {"start": v(-25.9, 46.11) * mm, "end": v(-25.94, 46.21) * mm});
            skLineSegment(sketch, "E2089", {"start": v(-25.94, 46.21) * mm, "end": v(-25.98, 46.3) * mm});
            skLineSegment(sketch, "E2090", {"start": v(-25.98, 46.3) * mm, "end": v(-26.02, 46.4) * mm});
            skLineSegment(sketch, "E2091", {"start": v(-26.02, 46.4) * mm, "end": v(-26.06, 46.44) * mm});
            skLineSegment(sketch, "E2092", {"start": v(-26.06, 46.44) * mm, "end": v(-27.1, 46.47) * mm});
            skLineSegment(sketch, "E2093", {"start": v(-27.1, 46.47) * mm, "end": v(-27.15, 46.44) * mm});
            skLineSegment(sketch, "E2094", {"start": v(-27.15, 46.44) * mm, "end": v(-27.2, 46.35) * mm});
            skLineSegment(sketch, "E2095", {"start": v(-27.2, 46.35) * mm, "end": v(-27.24, 46.25) * mm});
            skLineSegment(sketch, "E2096", {"start": v(-27.24, 46.25) * mm, "end": v(-27.28, 46.16) * mm});
            skLineSegment(sketch, "E2097", {"start": v(-27.28, 46.16) * mm, "end": v(-27.32, 46.06) * mm});
            skLineSegment(sketch, "E2098", {"start": v(-27.32, 46.06) * mm, "end": v(-27.36, 45.97) * mm});
            skLineSegment(sketch, "E2099", {"start": v(-27.36, 45.97) * mm, "end": v(-27.4, 45.88) * mm});
            skLineSegment(sketch, "E2100", {"start": v(-27.4, 45.88) * mm, "end": v(-27.44, 45.79) * mm});
            skLineSegment(sketch, "E2101", {"start": v(-27.44, 45.79) * mm, "end": v(-27.48, 45.7) * mm});
            skLineSegment(sketch, "E2102", {"start": v(-27.48, 45.7) * mm, "end": v(-27.52, 45.6) * mm});
            skLineSegment(sketch, "E2103", {"start": v(-27.52, 45.6) * mm, "end": v(-27.56, 45.52) * mm});
            skLineSegment(sketch, "E2104", {"start": v(-27.56, 45.52) * mm, "end": v(-27.6, 45.43) * mm});
            skLineSegment(sketch, "E2105", {"start": v(-27.6, 45.43) * mm, "end": v(-27.63, 45.35) * mm});
            skLineSegment(sketch, "E2106", {"start": v(-27.63, 45.35) * mm, "end": v(-27.66, 45.26) * mm});
            skLineSegment(sketch, "E2107", {"start": v(-27.66, 45.26) * mm, "end": v(-27.7, 45.18) * mm});
            skLineSegment(sketch, "E2108", {"start": v(-27.7, 45.18) * mm, "end": v(-27.72, 45.1) * mm});
            skLineSegment(sketch, "E2109", {"start": v(-27.72, 45.1) * mm, "end": v(-27.76, 45.01) * mm});
            skLineSegment(sketch, "E2110", {"start": v(-27.76, 45.01) * mm, "end": v(-27.79, 44.93) * mm});
            skLineSegment(sketch, "E2111", {"start": v(-27.79, 44.93) * mm, "end": v(-27.82, 44.85) * mm});
            skLineSegment(sketch, "E2112", {"start": v(-27.82, 44.85) * mm, "end": v(-27.85, 44.77) * mm});
            skLineSegment(sketch, "E2113", {"start": v(-27.85, 44.77) * mm, "end": v(-27.87, 44.7) * mm});
            skLineSegment(sketch, "E2114", {"start": v(-27.87, 44.7) * mm, "end": v(-27.9, 44.61) * mm});
            skLineSegment(sketch, "E2115", {"start": v(-27.9, 44.61) * mm, "end": v(-27.93, 44.54) * mm});
            skLineSegment(sketch, "E2116", {"start": v(-27.93, 44.54) * mm, "end": v(-27.95, 44.46) * mm});
            skLineSegment(sketch, "E2117", {"start": v(-27.95, 44.46) * mm, "end": v(-27.98, 44.39) * mm});
            skLineSegment(sketch, "E2118", {"start": v(-27.98, 44.39) * mm, "end": v(-28, 44.31) * mm});
            skLineSegment(sketch, "E2119", {"start": v(-28, 44.31) * mm, "end": v(-28.03, 44.24) * mm});
            skLineSegment(sketch, "E2120", {"start": v(-28.03, 44.24) * mm, "end": v(-28.05, 44.17) * mm});
            skLineSegment(sketch, "E2121", {"start": v(-28.05, 44.17) * mm, "end": v(-28.07, 44.1) * mm});
            skLineSegment(sketch, "E2122", {"start": v(-28.07, 44.1) * mm, "end": v(-28.1, 44.03) * mm});
            skLineSegment(sketch, "E2123", {"start": v(-28.1, 44.03) * mm, "end": v(-28.11, 43.96) * mm});
            skLineSegment(sketch, "E2124", {"start": v(-28.11, 43.96) * mm, "end": v(-28.13, 43.9) * mm});
            skLineSegment(sketch, "E2125", {"start": v(-28.13, 43.9) * mm, "end": v(-28.15, 43.83) * mm});
            skLineSegment(sketch, "E2126", {"start": v(-28.15, 43.83) * mm, "end": v(-28.17, 43.76) * mm});
            skLineSegment(sketch, "E2127", {"start": v(-28.17, 43.76) * mm, "end": v(-28.19, 43.7) * mm});
            skLineSegment(sketch, "E2128", {"start": v(-28.19, 43.7) * mm, "end": v(-28.2, 43.63) * mm});
            skLineSegment(sketch, "E2129", {"start": v(-28.2, 43.63) * mm, "end": v(-28.22, 43.57) * mm});
            skLineSegment(sketch, "E2130", {"start": v(-28.22, 43.57) * mm, "end": v(-28.24, 43.5) * mm});
            skLineSegment(sketch, "E2131", {"start": v(-28.24, 43.5) * mm, "end": v(-28.25, 43.45) * mm});
            skLineSegment(sketch, "E2132", {"start": v(-28.25, 43.45) * mm, "end": v(-28.27, 43.4) * mm});
            skLineSegment(sketch, "E2133", {"start": v(-28.27, 43.4) * mm, "end": v(-28.28, 43.33) * mm});
            skLineSegment(sketch, "E2134", {"start": v(-28.28, 43.33) * mm, "end": v(-28.52, 43.32) * mm});
            skLineSegment(sketch, "E2135", {"start": v(-28.52, 43.32) * mm, "end": v(-29.32, 43.31) * mm});
            skLineSegment(sketch, "E2136", {"start": v(-29.32, 43.31) * mm, "end": v(-29.56, 43.32) * mm});
            skLineSegment(sketch, "E2137", {"start": v(-29.56, 43.32) * mm, "end": v(-29.57, 43.37) * mm});
            skLineSegment(sketch, "E2138", {"start": v(-29.57, 43.37) * mm, "end": v(-29.59, 43.43) * mm});
            skLineSegment(sketch, "E2139", {"start": v(-29.59, 43.43) * mm, "end": v(-29.6, 43.5) * mm});
            skLineSegment(sketch, "E2140", {"start": v(-29.6, 43.5) * mm, "end": v(-29.62, 43.55) * mm});
            skLineSegment(sketch, "E2141", {"start": v(-29.62, 43.55) * mm, "end": v(-29.64, 43.62) * mm});
            skLineSegment(sketch, "E2142", {"start": v(-29.64, 43.62) * mm, "end": v(-29.66, 43.68) * mm});
            skLineSegment(sketch, "E2143", {"start": v(-29.66, 43.68) * mm, "end": v(-29.68, 43.74) * mm});
            skLineSegment(sketch, "E2144", {"start": v(-29.68, 43.74) * mm, "end": v(-29.7, 43.8) * mm});
            skLineSegment(sketch, "E2145", {"start": v(-29.7, 43.8) * mm, "end": v(-29.72, 43.87) * mm});
            skLineSegment(sketch, "E2146", {"start": v(-29.72, 43.87) * mm, "end": v(-29.74, 43.94) * mm});
            skLineSegment(sketch, "E2147", {"start": v(-29.74, 43.94) * mm, "end": v(-29.76, 44) * mm});
            skLineSegment(sketch, "E2148", {"start": v(-29.76, 44) * mm, "end": v(-29.79, 44.08) * mm});
            skLineSegment(sketch, "E2149", {"start": v(-29.79, 44.08) * mm, "end": v(-29.81, 44.15) * mm});
            skLineSegment(sketch, "E2150", {"start": v(-29.81, 44.15) * mm, "end": v(-29.84, 44.22) * mm});
            skLineSegment(sketch, "E2151", {"start": v(-29.84, 44.22) * mm, "end": v(-29.86, 44.29) * mm});
            skLineSegment(sketch, "E2152", {"start": v(-29.86, 44.29) * mm, "end": v(-29.89, 44.36) * mm});
            skLineSegment(sketch, "E2153", {"start": v(-29.89, 44.36) * mm, "end": v(-29.91, 44.44) * mm});
            skLineSegment(sketch, "E2154", {"start": v(-29.91, 44.44) * mm, "end": v(-29.94, 44.51) * mm});
            skLineSegment(sketch, "E2155", {"start": v(-29.94, 44.51) * mm, "end": v(-29.97, 44.59) * mm});
            skLineSegment(sketch, "E2156", {"start": v(-29.97, 44.59) * mm, "end": v(-30, 44.66) * mm});
            skLineSegment(sketch, "E2157", {"start": v(-30, 44.66) * mm, "end": v(-30.03, 44.74) * mm});
            skLineSegment(sketch, "E2158", {"start": v(-30.03, 44.74) * mm, "end": v(-30.06, 44.82) * mm});
            skLineSegment(sketch, "E2159", {"start": v(-30.06, 44.82) * mm, "end": v(-30.1, 44.9) * mm});
            skLineSegment(sketch, "E2160", {"start": v(-30.1, 44.9) * mm, "end": v(-30.12, 44.98) * mm});
            skLineSegment(sketch, "E2161", {"start": v(-30.12, 44.98) * mm, "end": v(-30.16, 45.06) * mm});
            skLineSegment(sketch, "E2162", {"start": v(-30.16, 45.06) * mm, "end": v(-30.2, 45.15) * mm});
            skLineSegment(sketch, "E2163", {"start": v(-30.2, 45.15) * mm, "end": v(-30.23, 45.23) * mm});
            skLineSegment(sketch, "E2164", {"start": v(-30.23, 45.23) * mm, "end": v(-30.26, 45.31) * mm});
            skLineSegment(sketch, "E2165", {"start": v(-30.26, 45.31) * mm, "end": v(-30.3, 45.4) * mm});
            skLineSegment(sketch, "E2166", {"start": v(-30.3, 45.4) * mm, "end": v(-30.34, 45.49) * mm});
            skLineSegment(sketch, "E2167", {"start": v(-30.34, 45.49) * mm, "end": v(-30.38, 45.57) * mm});
            skLineSegment(sketch, "E2168", {"start": v(-30.38, 45.57) * mm, "end": v(-30.42, 45.66) * mm});
            skLineSegment(sketch, "E2169", {"start": v(-30.42, 45.66) * mm, "end": v(-30.46, 45.75) * mm});
            skLineSegment(sketch, "E2170", {"start": v(-30.46, 45.75) * mm, "end": v(-30.5, 45.84) * mm});
            skLineSegment(sketch, "E2171", {"start": v(-30.5, 45.84) * mm, "end": v(-30.54, 45.93) * mm});
            skLineSegment(sketch, "E2172", {"start": v(-30.54, 45.93) * mm, "end": v(-30.58, 46.02) * mm});
            skLineSegment(sketch, "E2173", {"start": v(-30.58, 46.02) * mm, "end": v(-30.63, 46.12) * mm});
            skLineSegment(sketch, "E2174", {"start": v(-30.63, 46.12) * mm, "end": v(-30.67, 46.21) * mm});
            skLineSegment(sketch, "E2175", {"start": v(-30.67, 46.21) * mm, "end": v(-30.72, 46.3) * mm});
            skLineSegment(sketch, "E2176", {"start": v(-30.72, 46.3) * mm, "end": v(-30.77, 46.4) * mm});
            skLineSegment(sketch, "E2177", {"start": v(-30.77, 46.4) * mm, "end": v(-30.81, 46.42) * mm});
            skLineSegment(sketch, "E2178", {"start": v(-30.81, 46.42) * mm, "end": v(-31.85, 46.36) * mm});
            skLineSegment(sketch, "E2179", {"start": v(-31.85, 46.36) * mm, "end": v(-31.9, 46.34) * mm});
            skLineSegment(sketch, "E2180", {"start": v(-31.9, 46.34) * mm, "end": v(-31.93, 46.24) * mm});
            skLineSegment(sketch, "E2181", {"start": v(-31.93, 46.24) * mm, "end": v(-31.96, 46.14) * mm});
            skLineSegment(sketch, "E2182", {"start": v(-31.96, 46.14) * mm, "end": v(-32, 46.04) * mm});
            skLineSegment(sketch, "E2183", {"start": v(-32, 46.04) * mm, "end": v(-32.03, 45.94) * mm});
            skLineSegment(sketch, "E2184", {"start": v(-32.03, 45.94) * mm, "end": v(-32.06, 45.85) * mm});
            skLineSegment(sketch, "E2185", {"start": v(-32.06, 45.85) * mm, "end": v(-32.1, 45.75) * mm});
            skLineSegment(sketch, "E2186", {"start": v(-32.1, 45.75) * mm, "end": v(-32.13, 45.66) * mm});
            skLineSegment(sketch, "E2187", {"start": v(-32.13, 45.66) * mm, "end": v(-32.16, 45.56) * mm});
            skLineSegment(sketch, "E2188", {"start": v(-32.16, 45.56) * mm, "end": v(-32.19, 45.47) * mm});
            skLineSegment(sketch, "E2189", {"start": v(-32.19, 45.47) * mm, "end": v(-32.22, 45.38) * mm});
            skLineSegment(sketch, "E2190", {"start": v(-32.22, 45.38) * mm, "end": v(-32.24, 45.29) * mm});
            skLineSegment(sketch, "E2191", {"start": v(-32.24, 45.29) * mm, "end": v(-32.27, 45.2) * mm});
            skLineSegment(sketch, "E2192", {"start": v(-32.27, 45.2) * mm, "end": v(-32.3, 45.11) * mm});
            skLineSegment(sketch, "E2193", {"start": v(-32.3, 45.11) * mm, "end": v(-32.32, 45.02) * mm});
            skLineSegment(sketch, "E2194", {"start": v(-32.32, 45.02) * mm, "end": v(-32.35, 44.94) * mm});
            skLineSegment(sketch, "E2195", {"start": v(-32.35, 44.94) * mm, "end": v(-32.37, 44.85) * mm});
            skLineSegment(sketch, "E2196", {"start": v(-32.37, 44.85) * mm, "end": v(-32.4, 44.77) * mm});
            skLineSegment(sketch, "E2197", {"start": v(-32.4, 44.77) * mm, "end": v(-32.42, 44.69) * mm});
            skLineSegment(sketch, "E2198", {"start": v(-32.42, 44.69) * mm, "end": v(-32.44, 44.6) * mm});
            skLineSegment(sketch, "E2199", {"start": v(-32.44, 44.6) * mm, "end": v(-32.46, 44.52) * mm});
            skLineSegment(sketch, "E2200", {"start": v(-32.46, 44.52) * mm, "end": v(-32.48, 44.44) * mm});
            skLineSegment(sketch, "E2201", {"start": v(-32.48, 44.44) * mm, "end": v(-32.5, 44.37) * mm});
            skLineSegment(sketch, "E2202", {"start": v(-32.5, 44.37) * mm, "end": v(-32.52, 44.29) * mm});
            skLineSegment(sketch, "E2203", {"start": v(-32.52, 44.29) * mm, "end": v(-32.53, 44.21) * mm});
            skLineSegment(sketch, "E2204", {"start": v(-32.53, 44.21) * mm, "end": v(-32.55, 44.14) * mm});
            skLineSegment(sketch, "E2205", {"start": v(-32.55, 44.14) * mm, "end": v(-32.57, 44.06) * mm});
            skLineSegment(sketch, "E2206", {"start": v(-32.57, 44.06) * mm, "end": v(-32.59, 43.99) * mm});
            skLineSegment(sketch, "E2207", {"start": v(-32.59, 43.99) * mm, "end": v(-32.6, 43.92) * mm});
            skLineSegment(sketch, "E2208", {"start": v(-32.6, 43.92) * mm, "end": v(-32.62, 43.84) * mm});
            skLineSegment(sketch, "E2209", {"start": v(-32.62, 43.84) * mm, "end": v(-32.63, 43.77) * mm});
            skLineSegment(sketch, "E2210", {"start": v(-32.63, 43.77) * mm, "end": v(-32.64, 43.7) * mm});
            skLineSegment(sketch, "E2211", {"start": v(-32.64, 43.7) * mm, "end": v(-32.66, 43.64) * mm});
            skLineSegment(sketch, "E2212", {"start": v(-32.66, 43.64) * mm, "end": v(-32.67, 43.57) * mm});
            skLineSegment(sketch, "E2213", {"start": v(-32.67, 43.57) * mm, "end": v(-32.68, 43.5) * mm});
            skLineSegment(sketch, "E2214", {"start": v(-32.68, 43.5) * mm, "end": v(-32.7, 43.44) * mm});
            skLineSegment(sketch, "E2215", {"start": v(-32.7, 43.44) * mm, "end": v(-32.7, 43.38) * mm});
            skLineSegment(sketch, "E2216", {"start": v(-32.7, 43.38) * mm, "end": v(-32.72, 43.31) * mm});
            skLineSegment(sketch, "E2217", {"start": v(-32.72, 43.31) * mm, "end": v(-32.73, 43.25) * mm});
            skLineSegment(sketch, "E2218", {"start": v(-32.73, 43.25) * mm, "end": v(-32.73, 43.2) * mm});
            skLineSegment(sketch, "E2219", {"start": v(-32.73, 43.2) * mm, "end": v(-32.74, 43.13) * mm});
            skLineSegment(sketch, "E2220", {"start": v(-32.74, 43.13) * mm, "end": v(-32.98, 43.1) * mm});
            skLineSegment(sketch, "E2221", {"start": v(-32.98, 43.1) * mm, "end": v(-33.78, 43.02) * mm});
            skLineSegment(sketch, "E2222", {"start": v(-33.78, 43.02) * mm, "end": v(-34.01, 43) * mm});
            skLineSegment(sketch, "E2223", {"start": v(-34.01, 43) * mm, "end": v(-34.03, 43.06) * mm});
            skLineSegment(sketch, "E2224", {"start": v(-34.03, 43.06) * mm, "end": v(-34.05, 43.12) * mm});
            skLineSegment(sketch, "E2225", {"start": v(-34.05, 43.12) * mm, "end": v(-34.08, 43.18) * mm});
            skLineSegment(sketch, "E2226", {"start": v(-34.08, 43.18) * mm, "end": v(-34.1, 43.23) * mm});
            skLineSegment(sketch, "E2227", {"start": v(-34.1, 43.23) * mm, "end": v(-34.12, 43.3) * mm});
            skLineSegment(sketch, "E2228", {"start": v(-34.12, 43.3) * mm, "end": v(-34.15, 43.35) * mm});
            skLineSegment(sketch, "E2229", {"start": v(-34.15, 43.35) * mm, "end": v(-34.17, 43.42) * mm});
            skLineSegment(sketch, "E2230", {"start": v(-34.17, 43.42) * mm, "end": v(-34.2, 43.48) * mm});
            skLineSegment(sketch, "E2231", {"start": v(-34.2, 43.48) * mm, "end": v(-34.22, 43.54) * mm});
            skLineSegment(sketch, "E2232", {"start": v(-34.22, 43.54) * mm, "end": v(-34.25, 43.6) * mm});
            skLineSegment(sketch, "E2233", {"start": v(-34.25, 43.6) * mm, "end": v(-34.28, 43.67) * mm});
            skLineSegment(sketch, "E2234", {"start": v(-34.28, 43.67) * mm, "end": v(-34.3, 43.74) * mm});
            skLineSegment(sketch, "E2235", {"start": v(-34.3, 43.74) * mm, "end": v(-34.34, 43.8) * mm});
            skLineSegment(sketch, "E2236", {"start": v(-34.34, 43.8) * mm, "end": v(-34.37, 43.88) * mm});
            skLineSegment(sketch, "E2237", {"start": v(-34.37, 43.88) * mm, "end": v(-34.4, 43.95) * mm});
            skLineSegment(sketch, "E2238", {"start": v(-34.4, 43.95) * mm, "end": v(-34.43, 44.02) * mm});
            skLineSegment(sketch, "E2239", {"start": v(-34.43, 44.02) * mm, "end": v(-34.47, 44.09) * mm});
            skLineSegment(sketch, "E2240", {"start": v(-34.47, 44.09) * mm, "end": v(-34.5, 44.16) * mm});
            skLineSegment(sketch, "E2241", {"start": v(-34.5, 44.16) * mm, "end": v(-34.54, 44.23) * mm});
            skLineSegment(sketch, "E2242", {"start": v(-34.54, 44.23) * mm, "end": v(-34.57, 44.3) * mm});
            skLineSegment(sketch, "E2243", {"start": v(-34.57, 44.3) * mm, "end": v(-34.6, 44.38) * mm});
            skLineSegment(sketch, "E2244", {"start": v(-34.6, 44.38) * mm, "end": v(-34.65, 44.46) * mm});
            skLineSegment(sketch, "E2245", {"start": v(-34.65, 44.46) * mm, "end": v(-34.69, 44.54) * mm});
            skLineSegment(sketch, "E2246", {"start": v(-34.69, 44.54) * mm, "end": v(-34.73, 44.61) * mm});
            skLineSegment(sketch, "E2247", {"start": v(-34.73, 44.61) * mm, "end": v(-34.77, 44.7) * mm});
            skLineSegment(sketch, "E2248", {"start": v(-34.77, 44.7) * mm, "end": v(-34.8, 44.77) * mm});
            skLineSegment(sketch, "E2249", {"start": v(-34.8, 44.77) * mm, "end": v(-34.85, 44.85) * mm});
            skLineSegment(sketch, "E2250", {"start": v(-34.85, 44.85) * mm, "end": v(-34.9, 44.93) * mm});
            skLineSegment(sketch, "E2251", {"start": v(-34.9, 44.93) * mm, "end": v(-34.94, 45.01) * mm});
            skLineSegment(sketch, "E2252", {"start": v(-34.94, 45.01) * mm, "end": v(-34.98, 45.1) * mm});
            skLineSegment(sketch, "E2253", {"start": v(-34.98, 45.1) * mm, "end": v(-35.03, 45.18) * mm});
            skLineSegment(sketch, "E2254", {"start": v(-35.03, 45.18) * mm, "end": v(-35.08, 45.26) * mm});
            skLineSegment(sketch, "E2255", {"start": v(-35.08, 45.26) * mm, "end": v(-35.13, 45.35) * mm});
            skLineSegment(sketch, "E2256", {"start": v(-35.13, 45.35) * mm, "end": v(-35.17, 45.44) * mm});
            skLineSegment(sketch, "E2257", {"start": v(-35.17, 45.44) * mm, "end": v(-35.23, 45.52) * mm});
            skLineSegment(sketch, "E2258", {"start": v(-35.23, 45.52) * mm, "end": v(-35.28, 45.61) * mm});
            skLineSegment(sketch, "E2259", {"start": v(-35.28, 45.61) * mm, "end": v(-35.33, 45.7) * mm});
            skLineSegment(sketch, "E2260", {"start": v(-35.33, 45.7) * mm, "end": v(-35.38, 45.79) * mm});
            skLineSegment(sketch, "E2261", {"start": v(-35.38, 45.79) * mm, "end": v(-35.44, 45.88) * mm});
            skLineSegment(sketch, "E2262", {"start": v(-35.44, 45.88) * mm, "end": v(-35.5, 45.97) * mm});
            skLineSegment(sketch, "E2263", {"start": v(-35.5, 45.97) * mm, "end": v(-35.54, 45.99) * mm});
            skLineSegment(sketch, "E2264", {"start": v(-35.54, 45.99) * mm, "end": v(-36.57, 45.83) * mm});
            skLineSegment(sketch, "E2265", {"start": v(-36.57, 45.83) * mm, "end": v(-36.6, 45.8) * mm});
            skLineSegment(sketch, "E2266", {"start": v(-36.6, 45.8) * mm, "end": v(-36.64, 45.7) * mm});
            skLineSegment(sketch, "E2267", {"start": v(-36.64, 45.7) * mm, "end": v(-36.66, 45.6) * mm});
            skLineSegment(sketch, "E2268", {"start": v(-36.66, 45.6) * mm, "end": v(-36.69, 45.5) * mm});
            skLineSegment(sketch, "E2269", {"start": v(-36.69, 45.5) * mm, "end": v(-36.71, 45.4) * mm});
            skLineSegment(sketch, "E2270", {"start": v(-36.71, 45.4) * mm, "end": v(-36.74, 45.3) * mm});
            skLineSegment(sketch, "E2271", {"start": v(-36.74, 45.3) * mm, "end": v(-36.76, 45.2) * mm});
            skLineSegment(sketch, "E2272", {"start": v(-36.76, 45.2) * mm, "end": v(-36.78, 45.1) * mm});
            skLineSegment(sketch, "E2273", {"start": v(-36.78, 45.1) * mm, "end": v(-36.8, 45) * mm});
            skLineSegment(sketch, "E2274", {"start": v(-36.8, 45) * mm, "end": v(-36.82, 44.91) * mm});
            skLineSegment(sketch, "E2275", {"start": v(-36.82, 44.91) * mm, "end": v(-36.84, 44.82) * mm});
            skLineSegment(sketch, "E2276", {"start": v(-36.84, 44.82) * mm, "end": v(-36.86, 44.73) * mm});
            skLineSegment(sketch, "E2277", {"start": v(-36.86, 44.73) * mm, "end": v(-36.88, 44.64) * mm});
            skLineSegment(sketch, "E2278", {"start": v(-36.88, 44.64) * mm, "end": v(-36.9, 44.55) * mm});
            skLineSegment(sketch, "E2279", {"start": v(-36.9, 44.55) * mm, "end": v(-36.92, 44.46) * mm});
            skLineSegment(sketch, "E2280", {"start": v(-36.92, 44.46) * mm, "end": v(-36.93, 44.37) * mm});
            skLineSegment(sketch, "E2281", {"start": v(-36.93, 44.37) * mm, "end": v(-36.95, 44.28) * mm});
            skLineSegment(sketch, "E2282", {"start": v(-36.95, 44.28) * mm, "end": v(-36.97, 44.2) * mm});
            skLineSegment(sketch, "E2283", {"start": v(-36.97, 44.2) * mm, "end": v(-36.98, 44.11) * mm});
            skLineSegment(sketch, "E2284", {"start": v(-36.98, 44.11) * mm, "end": v(-37, 44.03) * mm});
            skLineSegment(sketch, "E2285", {"start": v(-37, 44.03) * mm, "end": v(-37, 43.95) * mm});
            skLineSegment(sketch, "E2286", {"start": v(-37, 43.95) * mm, "end": v(-37.02, 43.87) * mm});
            skLineSegment(sketch, "E2287", {"start": v(-37.02, 43.87) * mm, "end": v(-37.03, 43.79) * mm});
            skLineSegment(sketch, "E2288", {"start": v(-37.03, 43.79) * mm, "end": v(-37.05, 43.7) * mm});
            skLineSegment(sketch, "E2289", {"start": v(-37.05, 43.7) * mm, "end": v(-37.06, 43.63) * mm});
            skLineSegment(sketch, "E2290", {"start": v(-37.06, 43.63) * mm, "end": v(-37.07, 43.55) * mm});
            skLineSegment(sketch, "E2291", {"start": v(-37.07, 43.55) * mm, "end": v(-37.08, 43.48) * mm});
            skLineSegment(sketch, "E2292", {"start": v(-37.08, 43.48) * mm, "end": v(-37.09, 43.4) * mm});
            skLineSegment(sketch, "E2293", {"start": v(-37.09, 43.4) * mm, "end": v(-37.1, 43.33) * mm});
            skLineSegment(sketch, "E2294", {"start": v(-37.1, 43.33) * mm, "end": v(-37.1, 43.26) * mm});
            skLineSegment(sketch, "E2295", {"start": v(-37.1, 43.26) * mm, "end": v(-37.11, 43.18) * mm});
            skLineSegment(sketch, "E2296", {"start": v(-37.11, 43.18) * mm, "end": v(-37.12, 43.11) * mm});
            skLineSegment(sketch, "E2297", {"start": v(-37.12, 43.11) * mm, "end": v(-37.13, 43.05) * mm});
            skLineSegment(sketch, "E2298", {"start": v(-37.13, 43.05) * mm, "end": v(-37.13, 42.98) * mm});
            skLineSegment(sketch, "E2299", {"start": v(-37.13, 42.98) * mm, "end": v(-37.14, 42.91) * mm});
            skLineSegment(sketch, "E2300", {"start": v(-37.14, 42.91) * mm, "end": v(-37.15, 42.85) * mm});
            skLineSegment(sketch, "E2301", {"start": v(-37.15, 42.85) * mm, "end": v(-37.15, 42.78) * mm});
            skLineSegment(sketch, "E2302", {"start": v(-37.15, 42.78) * mm, "end": v(-37.16, 42.72) * mm});
            skLineSegment(sketch, "E2303", {"start": v(-37.16, 42.72) * mm, "end": v(-37.16, 42.66) * mm});
            skLineSegment(sketch, "E2304", {"start": v(-37.16, 42.66) * mm, "end": v(-37.17, 42.6) * mm});
            skLineSegment(sketch, "E2305", {"start": v(-37.17, 42.6) * mm, "end": v(-37.17, 42.54) * mm});
            skLineSegment(sketch, "E2306", {"start": v(-37.17, 42.54) * mm, "end": v(-37.4, 42.49) * mm});
            skLineSegment(sketch, "E2307", {"start": v(-37.4, 42.49) * mm, "end": v(-38.19, 42.33) * mm});
            skLineSegment(sketch, "E2308", {"start": v(-38.19, 42.33) * mm, "end": v(-38.42, 42.3) * mm});
            skLineSegment(sketch, "E2309", {"start": v(-38.42, 42.3) * mm, "end": v(-38.45, 42.35) * mm});
            skLineSegment(sketch, "E2310", {"start": v(-38.45, 42.35) * mm, "end": v(-38.47, 42.4) * mm});
            skLineSegment(sketch, "E2311", {"start": v(-38.47, 42.4) * mm, "end": v(-38.5, 42.46) * mm});
            skLineSegment(sketch, "E2312", {"start": v(-38.5, 42.46) * mm, "end": v(-38.53, 42.52) * mm});
            skLineSegment(sketch, "E2313", {"start": v(-38.53, 42.52) * mm, "end": v(-38.56, 42.57) * mm});
            skLineSegment(sketch, "E2314", {"start": v(-38.56, 42.57) * mm, "end": v(-38.59, 42.63) * mm});
            skLineSegment(sketch, "E2315", {"start": v(-38.59, 42.63) * mm, "end": v(-38.62, 42.7) * mm});
            skLineSegment(sketch, "E2316", {"start": v(-38.62, 42.7) * mm, "end": v(-38.65, 42.75) * mm});
            skLineSegment(sketch, "E2317", {"start": v(-38.65, 42.75) * mm, "end": v(-38.68, 42.81) * mm});
            skLineSegment(sketch, "E2318", {"start": v(-38.68, 42.81) * mm, "end": v(-38.71, 42.87) * mm});
            skLineSegment(sketch, "E2319", {"start": v(-38.71, 42.87) * mm, "end": v(-38.75, 42.94) * mm});
            skLineSegment(sketch, "E2320", {"start": v(-38.75, 42.94) * mm, "end": v(-38.78, 43) * mm});
            skLineSegment(sketch, "E2321", {"start": v(-38.78, 43) * mm, "end": v(-38.82, 43.07) * mm});
            skLineSegment(sketch, "E2322", {"start": v(-38.82, 43.07) * mm, "end": v(-38.86, 43.13) * mm});
            skLineSegment(sketch, "E2323", {"start": v(-38.86, 43.13) * mm, "end": v(-38.9, 43.2) * mm});
            skLineSegment(sketch, "E2324", {"start": v(-38.9, 43.2) * mm, "end": v(-38.93, 43.26) * mm});
            skLineSegment(sketch, "E2325", {"start": v(-38.93, 43.26) * mm, "end": v(-38.97, 43.33) * mm});
            skLineSegment(sketch, "E2326", {"start": v(-38.97, 43.33) * mm, "end": v(-39.01, 43.4) * mm});
            skLineSegment(sketch, "E2327", {"start": v(-39.01, 43.4) * mm, "end": v(-39.05, 43.47) * mm});
            skLineSegment(sketch, "E2328", {"start": v(-39.05, 43.47) * mm, "end": v(-39.1, 43.54) * mm});
            skLineSegment(sketch, "E2329", {"start": v(-39.1, 43.54) * mm, "end": v(-39.14, 43.61) * mm});
            skLineSegment(sketch, "E2330", {"start": v(-39.14, 43.61) * mm, "end": v(-39.18, 43.69) * mm});
            skLineSegment(sketch, "E2331", {"start": v(-39.18, 43.69) * mm, "end": v(-39.23, 43.76) * mm});
            skLineSegment(sketch, "E2332", {"start": v(-39.23, 43.76) * mm, "end": v(-39.28, 43.83) * mm});
            skLineSegment(sketch, "E2333", {"start": v(-39.28, 43.83) * mm, "end": v(-39.32, 43.9) * mm});
            skLineSegment(sketch, "E2334", {"start": v(-39.32, 43.9) * mm, "end": v(-39.37, 43.98) * mm});
            skLineSegment(sketch, "E2335", {"start": v(-39.37, 43.98) * mm, "end": v(-39.42, 44.06) * mm});
            skLineSegment(sketch, "E2336", {"start": v(-39.42, 44.06) * mm, "end": v(-39.47, 44.14) * mm});
            skLineSegment(sketch, "E2337", {"start": v(-39.47, 44.14) * mm, "end": v(-39.52, 44.21) * mm});
            skLineSegment(sketch, "E2338", {"start": v(-39.52, 44.21) * mm, "end": v(-39.58, 44.3) * mm});
            skLineSegment(sketch, "E2339", {"start": v(-39.58, 44.3) * mm, "end": v(-39.63, 44.37) * mm});
            skLineSegment(sketch, "E2340", {"start": v(-39.63, 44.37) * mm, "end": v(-39.68, 44.45) * mm});
            skLineSegment(sketch, "E2341", {"start": v(-39.68, 44.45) * mm, "end": v(-39.74, 44.53) * mm});
            skLineSegment(sketch, "E2342", {"start": v(-39.74, 44.53) * mm, "end": v(-39.8, 44.61) * mm});
            skLineSegment(sketch, "E2343", {"start": v(-39.8, 44.61) * mm, "end": v(-39.85, 44.7) * mm});
            skLineSegment(sketch, "E2344", {"start": v(-39.85, 44.7) * mm, "end": v(-39.91, 44.78) * mm});
            skLineSegment(sketch, "E2345", {"start": v(-39.91, 44.78) * mm, "end": v(-39.97, 44.86) * mm});
            skLineSegment(sketch, "E2346", {"start": v(-39.97, 44.86) * mm, "end": v(-40.04, 44.94) * mm});
            skLineSegment(sketch, "E2347", {"start": v(-40.04, 44.94) * mm, "end": v(-40.1, 45.03) * mm});
            skLineSegment(sketch, "E2348", {"start": v(-40.1, 45.03) * mm, "end": v(-40.16, 45.11) * mm});
            skLineSegment(sketch, "E2349", {"start": v(-40.16, 45.11) * mm, "end": v(-40.21, 45.13) * mm});
            skLineSegment(sketch, "E2350", {"start": v(-40.21, 45.13) * mm, "end": v(-41.22, 44.88) * mm});
            skLineSegment(sketch, "E2351", {"start": v(-41.22, 44.88) * mm, "end": v(-41.26, 44.85) * mm});
            skLineSegment(sketch, "E2352", {"start": v(-41.26, 44.85) * mm, "end": v(-41.28, 44.74) * mm});
            skLineSegment(sketch, "E2353", {"start": v(-41.28, 44.74) * mm, "end": v(-41.3, 44.64) * mm});
            skLineSegment(sketch, "E2354", {"start": v(-41.3, 44.64) * mm, "end": v(-41.3, 44.54) * mm});
            skLineSegment(sketch, "E2355", {"start": v(-41.3, 44.54) * mm, "end": v(-41.32, 44.44) * mm});
            skLineSegment(sketch, "E2356", {"start": v(-41.32, 44.44) * mm, "end": v(-41.34, 44.34) * mm});
            skLineSegment(sketch, "E2357", {"start": v(-41.34, 44.34) * mm, "end": v(-41.35, 44.24) * mm});
            skLineSegment(sketch, "E2358", {"start": v(-41.35, 44.24) * mm, "end": v(-41.37, 44.14) * mm});
            skLineSegment(sketch, "E2359", {"start": v(-41.37, 44.14) * mm, "end": v(-41.38, 44.04) * mm});
            skLineSegment(sketch, "E2360", {"start": v(-41.38, 44.04) * mm, "end": v(-41.4, 43.94) * mm});
            skLineSegment(sketch, "E2361", {"start": v(-41.4, 43.94) * mm, "end": v(-41.4, 43.85) * mm});
            skLineSegment(sketch, "E2362", {"start": v(-41.4, 43.85) * mm, "end": v(-41.42, 43.76) * mm});
            skLineSegment(sketch, "E2363", {"start": v(-41.42, 43.76) * mm, "end": v(-41.43, 43.66) * mm});
            skLineSegment(sketch, "E2364", {"start": v(-41.43, 43.66) * mm, "end": v(-41.44, 43.57) * mm});
            skLineSegment(sketch, "E2365", {"start": v(-41.44, 43.57) * mm, "end": v(-41.45, 43.48) * mm});
            skLineSegment(sketch, "E2366", {"start": v(-41.45, 43.48) * mm, "end": v(-41.45, 43.4) * mm});
            skLineSegment(sketch, "E2367", {"start": v(-41.45, 43.4) * mm, "end": v(-41.46, 43.3) * mm});
            skLineSegment(sketch, "E2368", {"start": v(-41.46, 43.3) * mm, "end": v(-41.47, 43.22) * mm});
            skLineSegment(sketch, "E2369", {"start": v(-41.47, 43.22) * mm, "end": v(-41.48, 43.13) * mm});
            skLineSegment(sketch, "E2370", {"start": v(-41.48, 43.13) * mm, "end": v(-41.48, 43.05) * mm});
            skLineSegment(sketch, "E2371", {"start": v(-41.48, 43.05) * mm, "end": v(-41.49, 42.96) * mm});
            skLineSegment(sketch, "E2372", {"start": v(-41.49, 42.96) * mm, "end": v(-41.5, 42.88) * mm});
            skLineSegment(sketch, "E2373", {"start": v(-41.5, 42.88) * mm, "end": v(-41.5, 42.8) * mm});
            skLineSegment(sketch, "E2374", {"start": v(-41.5, 42.8) * mm, "end": v(-41.5, 42.72) * mm});
            skLineSegment(sketch, "E2375", {"start": v(-41.5, 42.72) * mm, "end": v(-41.5, 42.64) * mm});
            skLineSegment(sketch, "E2376", {"start": v(-41.5, 42.64) * mm, "end": v(-41.51, 42.57) * mm});
            skLineSegment(sketch, "E2377", {"start": v(-41.51, 42.57) * mm, "end": v(-41.52, 42.49) * mm});
            skLineSegment(sketch, "E2378", {"start": v(-41.52, 42.49) * mm, "end": v(-41.52, 42.41) * mm});
            skLineSegment(sketch, "E2379", {"start": v(-41.52, 42.41) * mm, "end": v(-41.52, 42.34) * mm});
            skLineSegment(sketch, "E2380", {"start": v(-41.52, 42.34) * mm, "end": v(-41.52, 42.27) * mm});
            skLineSegment(sketch, "E2381", {"start": v(-41.52, 42.27) * mm, "end": v(-41.53, 42.2) * mm});
            skLineSegment(sketch, "E2382", {"start": v(-41.53, 42.2) * mm, "end": v(-41.53, 42.13) * mm});
            skLineSegment(sketch, "E2383", {"start": v(-41.53, 42.13) * mm, "end": v(-41.53, 42.06) * mm});
            skLineSegment(sketch, "E2384", {"start": v(-41.53, 42.06) * mm, "end": v(-41.53, 41.99) * mm});
            skLineSegment(sketch, "E2385", {"start": v(-41.53, 41.99) * mm, "end": v(-41.53, 41.92) * mm});
            skLineSegment(sketch, "E2386", {"start": v(-41.53, 41.92) * mm, "end": v(-41.53, 41.86) * mm});
            skLineSegment(sketch, "E2387", {"start": v(-41.53, 41.86) * mm, "end": v(-41.53, 41.8) * mm});
            skLineSegment(sketch, "E2388", {"start": v(-41.53, 41.8) * mm, "end": v(-41.53, 41.73) * mm});
            skLineSegment(sketch, "E2389", {"start": v(-41.53, 41.73) * mm, "end": v(-41.53, 41.67) * mm});
            skLineSegment(sketch, "E2390", {"start": v(-41.53, 41.67) * mm, "end": v(-41.53, 41.6) * mm});
            skLineSegment(sketch, "E2391", {"start": v(-41.53, 41.6) * mm, "end": v(-41.52, 41.55) * mm});
            skLineSegment(sketch, "E2392", {"start": v(-41.52, 41.55) * mm, "end": v(-41.75, 41.47) * mm});
            skLineSegment(sketch, "E2393", {"start": v(-41.75, 41.47) * mm, "end": v(-42.52, 41.25) * mm});
            skLineSegment(sketch, "E2394", {"start": v(-42.52, 41.25) * mm, "end": v(-42.75, 41.2) * mm});
            skLineSegment(sketch, "E2395", {"start": v(-42.75, 41.2) * mm, "end": v(-42.78, 41.24) * mm});
            skLineSegment(sketch, "E2396", {"start": v(-42.78, 41.24) * mm, "end": v(-42.8, 41.3) * mm});
            skLineSegment(sketch, "E2397", {"start": v(-42.8, 41.3) * mm, "end": v(-42.84, 41.35) * mm});
            skLineSegment(sketch, "E2398", {"start": v(-42.84, 41.35) * mm, "end": v(-42.87, 41.4) * mm});
            skLineSegment(sketch, "E2399", {"start": v(-42.87, 41.4) * mm, "end": v(-42.9, 41.46) * mm});
            skLineSegment(sketch, "E2400", {"start": v(-42.9, 41.46) * mm, "end": v(-42.94, 41.51) * mm});
            skLineSegment(sketch, "E2401", {"start": v(-42.94, 41.51) * mm, "end": v(-42.98, 41.57) * mm});
            skLineSegment(sketch, "E2402", {"start": v(-42.98, 41.57) * mm, "end": v(-43.02, 41.63) * mm});
            skLineSegment(sketch, "E2403", {"start": v(-43.02, 41.63) * mm, "end": v(-43.05, 41.68) * mm});
            skLineSegment(sketch, "E2404", {"start": v(-43.05, 41.68) * mm, "end": v(-43.1, 41.74) * mm});
            skLineSegment(sketch, "E2405", {"start": v(-43.1, 41.74) * mm, "end": v(-43.13, 41.8) * mm});
            skLineSegment(sketch, "E2406", {"start": v(-43.13, 41.8) * mm, "end": v(-43.17, 41.86) * mm});
            skLineSegment(sketch, "E2407", {"start": v(-43.17, 41.86) * mm, "end": v(-43.21, 41.92) * mm});
            skLineSegment(sketch, "E2408", {"start": v(-43.21, 41.92) * mm, "end": v(-43.26, 41.99) * mm});
            skLineSegment(sketch, "E2409", {"start": v(-43.26, 41.99) * mm, "end": v(-43.3, 42.05) * mm});
            skLineSegment(sketch, "E2410", {"start": v(-43.3, 42.05) * mm, "end": v(-43.34, 42.11) * mm});
            skLineSegment(sketch, "E2411", {"start": v(-43.34, 42.11) * mm, "end": v(-43.39, 42.18) * mm});
            skLineSegment(sketch, "E2412", {"start": v(-43.39, 42.18) * mm, "end": v(-43.44, 42.24) * mm});
            skLineSegment(sketch, "E2413", {"start": v(-43.44, 42.24) * mm, "end": v(-43.48, 42.3) * mm});
            skLineSegment(sketch, "E2414", {"start": v(-43.48, 42.3) * mm, "end": v(-43.53, 42.37) * mm});
            skLineSegment(sketch, "E2415", {"start": v(-43.53, 42.37) * mm, "end": v(-43.58, 42.44) * mm});
            skLineSegment(sketch, "E2416", {"start": v(-43.58, 42.44) * mm, "end": v(-43.63, 42.5) * mm});
            skLineSegment(sketch, "E2417", {"start": v(-43.63, 42.5) * mm, "end": v(-43.68, 42.58) * mm});
            skLineSegment(sketch, "E2418", {"start": v(-43.68, 42.58) * mm, "end": v(-43.74, 42.65) * mm});
            skLineSegment(sketch, "E2419", {"start": v(-43.74, 42.65) * mm, "end": v(-43.8, 42.72) * mm});
            skLineSegment(sketch, "E2420", {"start": v(-43.8, 42.72) * mm, "end": v(-43.85, 42.79) * mm});
            skLineSegment(sketch, "E2421", {"start": v(-43.85, 42.79) * mm, "end": v(-43.9, 42.86) * mm});
            skLineSegment(sketch, "E2422", {"start": v(-43.9, 42.86) * mm, "end": v(-43.96, 42.93) * mm});
            skLineSegment(sketch, "E2423", {"start": v(-43.96, 42.93) * mm, "end": v(-44.02, 43) * mm});
            skLineSegment(sketch, "E2424", {"start": v(-44.02, 43) * mm, "end": v(-44.08, 43.08) * mm});
            skLineSegment(sketch, "E2425", {"start": v(-44.08, 43.08) * mm, "end": v(-44.14, 43.15) * mm});
            skLineSegment(sketch, "E2426", {"start": v(-44.14, 43.15) * mm, "end": v(-44.2, 43.23) * mm});
            skLineSegment(sketch, "E2427", {"start": v(-44.2, 43.23) * mm, "end": v(-44.26, 43.3) * mm});
            skLineSegment(sketch, "E2428", {"start": v(-44.26, 43.3) * mm, "end": v(-44.33, 43.38) * mm});
            skLineSegment(sketch, "E2429", {"start": v(-44.33, 43.38) * mm, "end": v(-44.4, 43.45) * mm});
            skLineSegment(sketch, "E2430", {"start": v(-44.4, 43.45) * mm, "end": v(-44.46, 43.53) * mm});
            skLineSegment(sketch, "E2431", {"start": v(-44.46, 43.53) * mm, "end": v(-44.53, 43.6) * mm});
            skLineSegment(sketch, "E2432", {"start": v(-44.53, 43.6) * mm, "end": v(-44.6, 43.69) * mm});
            skLineSegment(sketch, "E2433", {"start": v(-44.6, 43.69) * mm, "end": v(-44.66, 43.76) * mm});
            skLineSegment(sketch, "E2434", {"start": v(-44.66, 43.76) * mm, "end": v(-44.73, 43.84) * mm});
            skLineSegment(sketch, "E2435", {"start": v(-44.73, 43.84) * mm, "end": v(-44.78, 43.85) * mm});
            skLineSegment(sketch, "E2436", {"start": v(-44.78, 43.85) * mm, "end": v(-45.77, 43.52) * mm});
            skLineSegment(sketch, "E2437", {"start": v(-45.77, 43.52) * mm, "end": v(-45.8, 43.48) * mm});
            skLineSegment(sketch, "E2438", {"start": v(-45.8, 43.48) * mm, "end": v(-45.81, 43.38) * mm});
            skLineSegment(sketch, "E2439", {"start": v(-45.81, 43.38) * mm, "end": v(-45.82, 43.27) * mm});
            skLineSegment(sketch, "E2440", {"start": v(-45.82, 43.27) * mm, "end": v(-45.83, 43.17) * mm});
            skLineSegment(sketch, "E2441", {"start": v(-45.83, 43.17) * mm, "end": v(-45.83, 43.06) * mm});
            skLineSegment(sketch, "E2442", {"start": v(-45.83, 43.06) * mm, "end": v(-45.84, 42.96) * mm});
            skLineSegment(sketch, "E2443", {"start": v(-45.84, 42.96) * mm, "end": v(-45.84, 42.86) * mm});
            skLineSegment(sketch, "E2444", {"start": v(-45.84, 42.86) * mm, "end": v(-45.85, 42.76) * mm});
            skLineSegment(sketch, "E2445", {"start": v(-45.85, 42.76) * mm, "end": v(-45.85, 42.67) * mm});
            skLineSegment(sketch, "E2446", {"start": v(-45.85, 42.67) * mm, "end": v(-45.86, 42.57) * mm});
            skLineSegment(sketch, "E2447", {"start": v(-45.86, 42.57) * mm, "end": v(-45.86, 42.47) * mm});
            skLineSegment(sketch, "E2448", {"start": v(-45.86, 42.47) * mm, "end": v(-45.86, 42.38) * mm});
            skLineSegment(sketch, "E2449", {"start": v(-45.86, 42.38) * mm, "end": v(-45.86, 42.29) * mm});
            skLineSegment(sketch, "E2450", {"start": v(-45.86, 42.29) * mm, "end": v(-45.87, 42.2) * mm});
            skLineSegment(sketch, "E2451", {"start": v(-45.87, 42.2) * mm, "end": v(-45.87, 42.1) * mm});
            skLineSegment(sketch, "E2452", {"start": v(-45.87, 42.1) * mm, "end": v(-45.87, 42.01) * mm});
            skLineSegment(sketch, "E2453", {"start": v(-45.87, 42.01) * mm, "end": v(-45.87, 41.93) * mm});
            skLineSegment(sketch, "E2454", {"start": v(-45.87, 41.93) * mm, "end": v(-45.87, 41.84) * mm});
            skLineSegment(sketch, "E2455", {"start": v(-45.87, 41.84) * mm, "end": v(-45.87, 41.75) * mm});
            skLineSegment(sketch, "E2456", {"start": v(-45.87, 41.75) * mm, "end": v(-45.87, 41.67) * mm});
            skLineSegment(sketch, "E2457", {"start": v(-45.87, 41.67) * mm, "end": v(-45.86, 41.58) * mm});
            skLineSegment(sketch, "E2458", {"start": v(-45.86, 41.58) * mm, "end": v(-45.86, 41.5) * mm});
            skLineSegment(sketch, "E2459", {"start": v(-45.86, 41.5) * mm, "end": v(-45.86, 41.42) * mm});
            skLineSegment(sketch, "E2460", {"start": v(-45.86, 41.42) * mm, "end": v(-45.86, 41.34) * mm});
            skLineSegment(sketch, "E2461", {"start": v(-45.86, 41.34) * mm, "end": v(-45.86, 41.26) * mm});
            skLineSegment(sketch, "E2462", {"start": v(-45.86, 41.26) * mm, "end": v(-45.85, 41.18) * mm});
            skLineSegment(sketch, "E2463", {"start": v(-45.85, 41.18) * mm, "end": v(-45.85, 41.1) * mm});
            skLineSegment(sketch, "E2464", {"start": v(-45.85, 41.1) * mm, "end": v(-45.84, 41.03) * mm});
            skLineSegment(sketch, "E2465", {"start": v(-45.84, 41.03) * mm, "end": v(-45.84, 40.96) * mm});
            skLineSegment(sketch, "E2466", {"start": v(-45.84, 40.96) * mm, "end": v(-45.84, 40.89) * mm});
            skLineSegment(sketch, "E2467", {"start": v(-45.84, 40.89) * mm, "end": v(-45.83, 40.82) * mm});
            skLineSegment(sketch, "E2468", {"start": v(-45.83, 40.82) * mm, "end": v(-45.83, 40.75) * mm});
            skLineSegment(sketch, "E2469", {"start": v(-45.83, 40.75) * mm, "end": v(-45.82, 40.68) * mm});
            skLineSegment(sketch, "E2470", {"start": v(-45.82, 40.68) * mm, "end": v(-45.82, 40.6) * mm});
            skLineSegment(sketch, "E2471", {"start": v(-45.82, 40.6) * mm, "end": v(-45.81, 40.54) * mm});
            skLineSegment(sketch, "E2472", {"start": v(-45.81, 40.54) * mm, "end": v(-45.8, 40.48) * mm});
            skLineSegment(sketch, "E2473", {"start": v(-45.8, 40.48) * mm, "end": v(-45.8, 40.41) * mm});
            skLineSegment(sketch, "E2474", {"start": v(-45.8, 40.41) * mm, "end": v(-45.8, 40.35) * mm});
            skLineSegment(sketch, "E2475", {"start": v(-45.8, 40.35) * mm, "end": v(-45.78, 40.29) * mm});
            skLineSegment(sketch, "E2476", {"start": v(-45.78, 40.29) * mm, "end": v(-45.78, 40.23) * mm});
            skLineSegment(sketch, "E2477", {"start": v(-45.78, 40.23) * mm, "end": v(-45.77, 40.17) * mm});
            skLineSegment(sketch, "E2478", {"start": v(-45.77, 40.17) * mm, "end": v(-45.99, 40.08) * mm});
            skLineSegment(sketch, "E2479", {"start": v(-45.99, 40.08) * mm, "end": v(-46.74, 39.79) * mm});
            skLineSegment(sketch, "E2480", {"start": v(-46.74, 39.79) * mm, "end": v(-46.96, 39.7) * mm});
            skLineSegment(sketch, "E2481", {"start": v(-46.96, 39.7) * mm, "end": v(-47, 39.76) * mm});
            skLineSegment(sketch, "E2482", {"start": v(-47, 39.76) * mm, "end": v(-47.03, 39.8) * mm});
            skLineSegment(sketch, "E2483", {"start": v(-47.03, 39.8) * mm, "end": v(-47.07, 39.85) * mm});
            skLineSegment(sketch, "E2484", {"start": v(-47.07, 39.85) * mm, "end": v(-47.1, 39.9) * mm});
            skLineSegment(sketch, "E2485", {"start": v(-47.1, 39.9) * mm, "end": v(-47.14, 39.96) * mm});
            skLineSegment(sketch, "E2486", {"start": v(-47.14, 39.96) * mm, "end": v(-47.18, 40) * mm});
            skLineSegment(sketch, "E2487", {"start": v(-47.18, 40) * mm, "end": v(-47.22, 40.06) * mm});
            skLineSegment(sketch, "E2488", {"start": v(-47.22, 40.06) * mm, "end": v(-47.26, 40.11) * mm});
            skLineSegment(sketch, "E2489", {"start": v(-47.26, 40.11) * mm, "end": v(-47.3, 40.17) * mm});
            skLineSegment(sketch, "E2490", {"start": v(-47.3, 40.17) * mm, "end": v(-47.35, 40.22) * mm});
            skLineSegment(sketch, "E2491", {"start": v(-47.35, 40.22) * mm, "end": v(-47.4, 40.28) * mm});
            skLineSegment(sketch, "E2492", {"start": v(-47.4, 40.28) * mm, "end": v(-47.44, 40.34) * mm});
            skLineSegment(sketch, "E2493", {"start": v(-47.44, 40.34) * mm, "end": v(-47.49, 40.4) * mm});
            skLineSegment(sketch, "E2494", {"start": v(-47.49, 40.4) * mm, "end": v(-47.54, 40.45) * mm});
            skLineSegment(sketch, "E2495", {"start": v(-47.54, 40.45) * mm, "end": v(-47.59, 40.51) * mm});
            skLineSegment(sketch, "E2496", {"start": v(-47.59, 40.51) * mm, "end": v(-47.64, 40.57) * mm});
            skLineSegment(sketch, "E2497", {"start": v(-47.64, 40.57) * mm, "end": v(-47.69, 40.63) * mm});
            skLineSegment(sketch, "E2498", {"start": v(-47.69, 40.63) * mm, "end": v(-47.74, 40.69) * mm});
            skLineSegment(sketch, "E2499", {"start": v(-47.74, 40.69) * mm, "end": v(-47.8, 40.75) * mm});
            skLineSegment(sketch, "E2500", {"start": v(-47.8, 40.75) * mm, "end": v(-47.85, 40.81) * mm});
            skLineSegment(sketch, "E2501", {"start": v(-47.85, 40.81) * mm, "end": v(-47.9, 40.88) * mm});
            skLineSegment(sketch, "E2502", {"start": v(-47.9, 40.88) * mm, "end": v(-47.96, 40.94) * mm});
            skLineSegment(sketch, "E2503", {"start": v(-47.96, 40.94) * mm, "end": v(-48.02, 41) * mm});
            skLineSegment(sketch, "E2504", {"start": v(-48.02, 41) * mm, "end": v(-48.07, 41.07) * mm});
            skLineSegment(sketch, "E2505", {"start": v(-48.07, 41.07) * mm, "end": v(-48.13, 41.13) * mm});
            skLineSegment(sketch, "E2506", {"start": v(-48.13, 41.13) * mm, "end": v(-48.2, 41.2) * mm});
            skLineSegment(sketch, "E2507", {"start": v(-48.2, 41.2) * mm, "end": v(-48.26, 41.26) * mm});
            skLineSegment(sketch, "E2508", {"start": v(-48.26, 41.26) * mm, "end": v(-48.32, 41.33) * mm});
            skLineSegment(sketch, "E2509", {"start": v(-48.32, 41.33) * mm, "end": v(-48.39, 41.4) * mm});
            skLineSegment(sketch, "E2510", {"start": v(-48.39, 41.4) * mm, "end": v(-48.45, 41.46) * mm});
            skLineSegment(sketch, "E2511", {"start": v(-48.45, 41.46) * mm, "end": v(-48.52, 41.53) * mm});
            skLineSegment(sketch, "E2512", {"start": v(-48.52, 41.53) * mm, "end": v(-48.59, 41.6) * mm});
            skLineSegment(sketch, "E2513", {"start": v(-48.59, 41.6) * mm, "end": v(-48.66, 41.67) * mm});
            skLineSegment(sketch, "E2514", {"start": v(-48.66, 41.67) * mm, "end": v(-48.73, 41.74) * mm});
            skLineSegment(sketch, "E2515", {"start": v(-48.73, 41.74) * mm, "end": v(-48.8, 41.81) * mm});
            skLineSegment(sketch, "E2516", {"start": v(-48.8, 41.81) * mm, "end": v(-48.87, 41.88) * mm});
            skLineSegment(sketch, "E2517", {"start": v(-48.87, 41.88) * mm, "end": v(-48.95, 41.95) * mm});
            skLineSegment(sketch, "E2518", {"start": v(-48.95, 41.95) * mm, "end": v(-49.02, 42.02) * mm});
            skLineSegment(sketch, "E2519", {"start": v(-49.02, 42.02) * mm, "end": v(-49.1, 42.1) * mm});
            skLineSegment(sketch, "E2520", {"start": v(-49.1, 42.1) * mm, "end": v(-49.18, 42.17) * mm});
            skLineSegment(sketch, "E2521", {"start": v(-49.18, 42.17) * mm, "end": v(-49.23, 42.17) * mm});
            skLineSegment(sketch, "E2522", {"start": v(-49.23, 42.17) * mm, "end": v(-50.18, 41.75) * mm});
            skLineSegment(sketch, "E2523", {"start": v(-50.18, 41.75) * mm, "end": v(-50.2, 41.71) * mm});
            skLineSegment(sketch, "E2524", {"start": v(-50.2, 41.71) * mm, "end": v(-50.2, 41.6) * mm});
            skLineSegment(sketch, "E2525", {"start": v(-50.2, 41.6) * mm, "end": v(-50.2, 41.5) * mm});
            skLineSegment(sketch, "E2526", {"start": v(-50.2, 41.5) * mm, "end": v(-50.2, 41.4) * mm});
            skLineSegment(sketch, "E2527", {"start": v(-50.2, 41.4) * mm, "end": v(-50.2, 41.3) * mm});
            skLineSegment(sketch, "E2528", {"start": v(-50.2, 41.3) * mm, "end": v(-50.2, 41.2) * mm});
            skLineSegment(sketch, "E2529", {"start": v(-50.2, 41.2) * mm, "end": v(-50.2, 41.1) * mm});
            skLineSegment(sketch, "E2530", {"start": v(-50.2, 41.1) * mm, "end": v(-50.19, 41) * mm});
            skLineSegment(sketch, "E2531", {"start": v(-50.19, 41) * mm, "end": v(-50.18, 40.9) * mm});
            skLineSegment(sketch, "E2532", {"start": v(-50.18, 40.9) * mm, "end": v(-50.18, 40.8) * mm});
            skLineSegment(sketch, "E2533", {"start": v(-50.18, 40.8) * mm, "end": v(-50.17, 40.7) * mm});
            skLineSegment(sketch, "E2534", {"start": v(-50.17, 40.7) * mm, "end": v(-50.17, 40.6) * mm});
            skLineSegment(sketch, "E2535", {"start": v(-50.17, 40.6) * mm, "end": v(-50.16, 40.52) * mm});
            skLineSegment(sketch, "E2536", {"start": v(-50.16, 40.52) * mm, "end": v(-50.15, 40.43) * mm});
            skLineSegment(sketch, "E2537", {"start": v(-50.15, 40.43) * mm, "end": v(-50.15, 40.33) * mm});
            skLineSegment(sketch, "E2538", {"start": v(-50.15, 40.33) * mm, "end": v(-50.14, 40.25) * mm});
            skLineSegment(sketch, "E2539", {"start": v(-50.14, 40.25) * mm, "end": v(-50.13, 40.16) * mm});
            skLineSegment(sketch, "E2540", {"start": v(-50.13, 40.16) * mm, "end": v(-50.12, 40.07) * mm});
            skLineSegment(sketch, "E2541", {"start": v(-50.12, 40.07) * mm, "end": v(-50.12, 39.99) * mm});
            skLineSegment(sketch, "E2542", {"start": v(-50.12, 39.99) * mm, "end": v(-50.1, 39.9) * mm});
            skLineSegment(sketch, "E2543", {"start": v(-50.1, 39.9) * mm, "end": v(-50.1, 39.82) * mm});
            skLineSegment(sketch, "E2544", {"start": v(-50.1, 39.82) * mm, "end": v(-50.09, 39.74) * mm});
            skLineSegment(sketch, "E2545", {"start": v(-50.09, 39.74) * mm, "end": v(-50.08, 39.66) * mm});
            skLineSegment(sketch, "E2546", {"start": v(-50.08, 39.66) * mm, "end": v(-50.07, 39.58) * mm});
            skLineSegment(sketch, "E2547", {"start": v(-50.07, 39.58) * mm, "end": v(-50.06, 39.5) * mm});
            skLineSegment(sketch, "E2548", {"start": v(-50.06, 39.5) * mm, "end": v(-50.05, 39.42) * mm});
            skLineSegment(sketch, "E2549", {"start": v(-50.05, 39.42) * mm, "end": v(-50.04, 39.35) * mm});
            skLineSegment(sketch, "E2550", {"start": v(-50.04, 39.35) * mm, "end": v(-50.03, 39.27) * mm});
            skLineSegment(sketch, "E2551", {"start": v(-50.03, 39.27) * mm, "end": v(-50.02, 39.2) * mm});
            skLineSegment(sketch, "E2552", {"start": v(-50.02, 39.2) * mm, "end": v(-50, 39.13) * mm});
            skLineSegment(sketch, "E2553", {"start": v(-50, 39.13) * mm, "end": v(-50, 39.06) * mm});
            skLineSegment(sketch, "E2554", {"start": v(-50, 39.06) * mm, "end": v(-49.99, 38.99) * mm});
            skLineSegment(sketch, "E2555", {"start": v(-49.99, 38.99) * mm, "end": v(-49.97, 38.92) * mm});
            skLineSegment(sketch, "E2556", {"start": v(-49.97, 38.92) * mm, "end": v(-49.96, 38.85) * mm});
            skLineSegment(sketch, "E2557", {"start": v(-49.96, 38.85) * mm, "end": v(-49.95, 38.78) * mm});
            skLineSegment(sketch, "E2558", {"start": v(-49.95, 38.78) * mm, "end": v(-49.94, 38.72) * mm});
            skLineSegment(sketch, "E2559", {"start": v(-49.94, 38.72) * mm, "end": v(-49.93, 38.66) * mm});
            skLineSegment(sketch, "E2560", {"start": v(-49.93, 38.66) * mm, "end": v(-49.91, 38.6) * mm});
            skLineSegment(sketch, "E2561", {"start": v(-49.91, 38.6) * mm, "end": v(-49.9, 38.53) * mm});
            skLineSegment(sketch, "E2562", {"start": v(-49.9, 38.53) * mm, "end": v(-49.9, 38.48) * mm});
            skLineSegment(sketch, "E2563", {"start": v(-49.9, 38.48) * mm, "end": v(-49.88, 38.42) * mm});
            skLineSegment(sketch, "E2564", {"start": v(-49.88, 38.42) * mm, "end": v(-50.08, 38.3) * mm});
            skLineSegment(sketch, "E2565", {"start": v(-50.08, 38.3) * mm, "end": v(-50.8, 37.95) * mm});
            skLineSegment(sketch, "E2566", {"start": v(-50.8, 37.95) * mm, "end": v(-51.02, 37.85) * mm});
            skLineSegment(sketch, "E2567", {"start": v(-51.02, 37.85) * mm, "end": v(-51.06, 37.9) * mm});
            skLineSegment(sketch, "E2568", {"start": v(-51.06, 37.9) * mm, "end": v(-51.1, 37.94) * mm});
            skLineSegment(sketch, "E2569", {"start": v(-51.1, 37.94) * mm, "end": v(-51.14, 37.99) * mm});
            skLineSegment(sketch, "E2570", {"start": v(-51.14, 37.99) * mm, "end": v(-51.18, 38.03) * mm});
            skLineSegment(sketch, "E2571", {"start": v(-51.18, 38.03) * mm, "end": v(-51.23, 38.08) * mm});
            skLineSegment(sketch, "E2572", {"start": v(-51.23, 38.08) * mm, "end": v(-51.27, 38.13) * mm});
            skLineSegment(sketch, "E2573", {"start": v(-51.27, 38.13) * mm, "end": v(-51.31, 38.18) * mm});
            skLineSegment(sketch, "E2574", {"start": v(-51.31, 38.18) * mm, "end": v(-51.36, 38.23) * mm});
            skLineSegment(sketch, "E2575", {"start": v(-51.36, 38.23) * mm, "end": v(-51.4, 38.28) * mm});
            skLineSegment(sketch, "E2576", {"start": v(-51.4, 38.28) * mm, "end": v(-51.46, 38.33) * mm});
            skLineSegment(sketch, "E2577", {"start": v(-51.46, 38.33) * mm, "end": v(-51.5, 38.38) * mm});
            skLineSegment(sketch, "E2578", {"start": v(-51.5, 38.38) * mm, "end": v(-51.56, 38.43) * mm});
            skLineSegment(sketch, "E2579", {"start": v(-51.56, 38.43) * mm, "end": v(-51.6, 38.49) * mm});
            skLineSegment(sketch, "E2580", {"start": v(-51.6, 38.49) * mm, "end": v(-51.66, 38.54) * mm});
            skLineSegment(sketch, "E2581", {"start": v(-51.66, 38.54) * mm, "end": v(-51.72, 38.6) * mm});
            skLineSegment(sketch, "E2582", {"start": v(-51.72, 38.6) * mm, "end": v(-51.77, 38.65) * mm});
            skLineSegment(sketch, "E2583", {"start": v(-51.77, 38.65) * mm, "end": v(-51.83, 38.7) * mm});
            skLineSegment(sketch, "E2584", {"start": v(-51.83, 38.7) * mm, "end": v(-51.88, 38.76) * mm});
            skLineSegment(sketch, "E2585", {"start": v(-51.88, 38.76) * mm, "end": v(-51.94, 38.82) * mm});
            skLineSegment(sketch, "E2586", {"start": v(-51.94, 38.82) * mm, "end": v(-52, 38.87) * mm});
            skLineSegment(sketch, "E2587", {"start": v(-52, 38.87) * mm, "end": v(-52.06, 38.93) * mm});
            skLineSegment(sketch, "E2588", {"start": v(-52.06, 38.93) * mm, "end": v(-52.13, 38.99) * mm});
            skLineSegment(sketch, "E2589", {"start": v(-52.13, 38.99) * mm, "end": v(-52.19, 39.05) * mm});
            skLineSegment(sketch, "E2590", {"start": v(-52.19, 39.05) * mm, "end": v(-52.25, 39.1) * mm});
            skLineSegment(sketch, "E2591", {"start": v(-52.25, 39.1) * mm, "end": v(-52.32, 39.16) * mm});
            skLineSegment(sketch, "E2592", {"start": v(-52.32, 39.16) * mm, "end": v(-52.39, 39.22) * mm});
            skLineSegment(sketch, "E2593", {"start": v(-52.39, 39.22) * mm, "end": v(-52.45, 39.28) * mm});
            skLineSegment(sketch, "E2594", {"start": v(-52.45, 39.28) * mm, "end": v(-52.52, 39.34) * mm});
            skLineSegment(sketch, "E2595", {"start": v(-52.52, 39.34) * mm, "end": v(-52.6, 39.4) * mm});
            skLineSegment(sketch, "E2596", {"start": v(-52.6, 39.4) * mm, "end": v(-52.66, 39.47) * mm});
            skLineSegment(sketch, "E2597", {"start": v(-52.66, 39.47) * mm, "end": v(-52.74, 39.53) * mm});
            skLineSegment(sketch, "E2598", {"start": v(-52.74, 39.53) * mm, "end": v(-52.81, 39.6) * mm});
            skLineSegment(sketch, "E2599", {"start": v(-52.81, 39.6) * mm, "end": v(-52.89, 39.65) * mm});
            skLineSegment(sketch, "E2600", {"start": v(-52.89, 39.65) * mm, "end": v(-52.96, 39.72) * mm});
            skLineSegment(sketch, "E2601", {"start": v(-52.96, 39.72) * mm, "end": v(-53.04, 39.78) * mm});
            skLineSegment(sketch, "E2602", {"start": v(-53.04, 39.78) * mm, "end": v(-53.12, 39.84) * mm});
            skLineSegment(sketch, "E2603", {"start": v(-53.12, 39.84) * mm, "end": v(-53.2, 39.9) * mm});
            skLineSegment(sketch, "E2604", {"start": v(-53.2, 39.9) * mm, "end": v(-53.28, 39.97) * mm});
            skLineSegment(sketch, "E2605", {"start": v(-53.28, 39.97) * mm, "end": v(-53.36, 40.04) * mm});
            skLineSegment(sketch, "E2606", {"start": v(-53.36, 40.04) * mm, "end": v(-53.45, 40.1) * mm});
            skLineSegment(sketch, "E2607", {"start": v(-53.45, 40.1) * mm, "end": v(-53.5, 40.1) * mm});
            skLineSegment(sketch, "E2608", {"start": v(-53.5, 40.1) * mm, "end": v(-54.4, 39.6) * mm});
            skLineSegment(sketch, "E2609", {"start": v(-54.4, 39.6) * mm, "end": v(-54.43, 39.56) * mm});
            skLineSegment(sketch, "E2610", {"start": v(-54.43, 39.56) * mm, "end": v(-54.42, 39.45) * mm});
            skLineSegment(sketch, "E2611", {"start": v(-54.42, 39.45) * mm, "end": v(-54.41, 39.35) * mm});
            skLineSegment(sketch, "E2612", {"start": v(-54.41, 39.35) * mm, "end": v(-54.4, 39.24) * mm});
            skLineSegment(sketch, "E2613", {"start": v(-54.4, 39.24) * mm, "end": v(-54.39, 39.14) * mm});
            skLineSegment(sketch, "E2614", {"start": v(-54.39, 39.14) * mm, "end": v(-54.38, 39.04) * mm});
            skLineSegment(sketch, "E2615", {"start": v(-54.38, 39.04) * mm, "end": v(-54.36, 38.94) * mm});
            skLineSegment(sketch, "E2616", {"start": v(-54.36, 38.94) * mm, "end": v(-54.35, 38.84) * mm});
            skLineSegment(sketch, "E2617", {"start": v(-54.35, 38.84) * mm, "end": v(-54.34, 38.75) * mm});
            skLineSegment(sketch, "E2618", {"start": v(-54.34, 38.75) * mm, "end": v(-54.32, 38.65) * mm});
            skLineSegment(sketch, "E2619", {"start": v(-54.32, 38.65) * mm, "end": v(-54.3, 38.55) * mm});
            skLineSegment(sketch, "E2620", {"start": v(-54.3, 38.55) * mm, "end": v(-54.3, 38.46) * mm});
            skLineSegment(sketch, "E2621", {"start": v(-54.3, 38.46) * mm, "end": v(-54.28, 38.37) * mm});
            skLineSegment(sketch, "E2622", {"start": v(-54.28, 38.37) * mm, "end": v(-54.27, 38.28) * mm});
            skLineSegment(sketch, "E2623", {"start": v(-54.27, 38.28) * mm, "end": v(-54.25, 38.19) * mm});
            skLineSegment(sketch, "E2624", {"start": v(-54.25, 38.19) * mm, "end": v(-54.24, 38.1) * mm});
            skLineSegment(sketch, "E2625", {"start": v(-54.24, 38.1) * mm, "end": v(-54.22, 38.01) * mm});
            skLineSegment(sketch, "E2626", {"start": v(-54.22, 38.01) * mm, "end": v(-54.2, 37.93) * mm});
            skLineSegment(sketch, "E2627", {"start": v(-54.2, 37.93) * mm, "end": v(-54.19, 37.84) * mm});
            skLineSegment(sketch, "E2628", {"start": v(-54.19, 37.84) * mm, "end": v(-54.17, 37.76) * mm});
            skLineSegment(sketch, "E2629", {"start": v(-54.17, 37.76) * mm, "end": v(-54.16, 37.68) * mm});
            skLineSegment(sketch, "E2630", {"start": v(-54.16, 37.68) * mm, "end": v(-54.14, 37.6) * mm});
            skLineSegment(sketch, "E2631", {"start": v(-54.14, 37.6) * mm, "end": v(-54.12, 37.52) * mm});
            skLineSegment(sketch, "E2632", {"start": v(-54.12, 37.52) * mm, "end": v(-54.1, 37.44) * mm});
            skLineSegment(sketch, "E2633", {"start": v(-54.1, 37.44) * mm, "end": v(-54.1, 37.36) * mm});
            skLineSegment(sketch, "E2634", {"start": v(-54.1, 37.36) * mm, "end": v(-54.07, 37.29) * mm});
            skLineSegment(sketch, "E2635", {"start": v(-54.07, 37.29) * mm, "end": v(-54.06, 37.21) * mm});
            skLineSegment(sketch, "E2636", {"start": v(-54.06, 37.21) * mm, "end": v(-54.04, 37.14) * mm});
            skLineSegment(sketch, "E2637", {"start": v(-54.04, 37.14) * mm, "end": v(-54.02, 37.07) * mm});
            skLineSegment(sketch, "E2638", {"start": v(-54.02, 37.07) * mm, "end": v(-54, 37) * mm});
            skLineSegment(sketch, "E2639", {"start": v(-54, 37) * mm, "end": v(-53.99, 36.93) * mm});
            skLineSegment(sketch, "E2640", {"start": v(-53.99, 36.93) * mm, "end": v(-53.97, 36.86) * mm});
            skLineSegment(sketch, "E2641", {"start": v(-53.97, 36.86) * mm, "end": v(-53.95, 36.8) * mm});
            skLineSegment(sketch, "E2642", {"start": v(-53.95, 36.8) * mm, "end": v(-53.93, 36.73) * mm});
            skLineSegment(sketch, "E2643", {"start": v(-53.93, 36.73) * mm, "end": v(-53.92, 36.66) * mm});
            skLineSegment(sketch, "E2644", {"start": v(-53.92, 36.66) * mm, "end": v(-53.9, 36.6) * mm});
            skLineSegment(sketch, "E2645", {"start": v(-53.9, 36.6) * mm, "end": v(-53.88, 36.54) * mm});
            skLineSegment(sketch, "E2646", {"start": v(-53.88, 36.54) * mm, "end": v(-53.86, 36.48) * mm});
            skLineSegment(sketch, "E2647", {"start": v(-53.86, 36.48) * mm, "end": v(-53.85, 36.42) * mm});
            skLineSegment(sketch, "E2648", {"start": v(-53.85, 36.42) * mm, "end": v(-53.83, 36.36) * mm});
            skLineSegment(sketch, "E2649", {"start": v(-53.83, 36.36) * mm, "end": v(-53.81, 36.3) * mm});
            skLineSegment(sketch, "E2650", {"start": v(-53.81, 36.3) * mm, "end": v(-54, 36.17) * mm});
            skLineSegment(sketch, "E2651", {"start": v(-54, 36.17) * mm, "end": v(-54.7, 35.75) * mm});
            skLineSegment(sketch, "E2652", {"start": v(-54.7, 35.75) * mm, "end": v(-54.9, 35.64) * mm});
            skLineSegment(sketch, "E2653", {"start": v(-54.9, 35.64) * mm, "end": v(-54.94, 35.68) * mm});
            skLineSegment(sketch, "E2654", {"start": v(-54.94, 35.68) * mm, "end": v(-54.98, 35.72) * mm});
            skLineSegment(sketch, "E2655", {"start": v(-54.98, 35.72) * mm, "end": v(-55.03, 35.76) * mm});
            skLineSegment(sketch, "E2656", {"start": v(-55.03, 35.76) * mm, "end": v(-55.08, 35.8) * mm});
            skLineSegment(sketch, "E2657", {"start": v(-55.08, 35.8) * mm, "end": v(-55.12, 35.85) * mm});
            skLineSegment(sketch, "E2658", {"start": v(-55.12, 35.85) * mm, "end": v(-55.17, 35.9) * mm});
            skLineSegment(sketch, "E2659", {"start": v(-55.17, 35.9) * mm, "end": v(-55.22, 35.94) * mm});
            skLineSegment(sketch, "E2660", {"start": v(-55.22, 35.94) * mm, "end": v(-55.27, 35.98) * mm});
            skLineSegment(sketch, "E2661", {"start": v(-55.27, 35.98) * mm, "end": v(-55.32, 36.03) * mm});
            skLineSegment(sketch, "E2662", {"start": v(-55.32, 36.03) * mm, "end": v(-55.38, 36.07) * mm});
            skLineSegment(sketch, "E2663", {"start": v(-55.38, 36.07) * mm, "end": v(-55.43, 36.12) * mm});
            skLineSegment(sketch, "E2664", {"start": v(-55.43, 36.12) * mm, "end": v(-55.49, 36.17) * mm});
            skLineSegment(sketch, "E2665", {"start": v(-55.49, 36.17) * mm, "end": v(-55.54, 36.22) * mm});
            skLineSegment(sketch, "E2666", {"start": v(-55.54, 36.22) * mm, "end": v(-55.6, 36.27) * mm});
            skLineSegment(sketch, "E2667", {"start": v(-55.6, 36.27) * mm, "end": v(-55.66, 36.31) * mm});
            skLineSegment(sketch, "E2668", {"start": v(-55.66, 36.31) * mm, "end": v(-55.72, 36.36) * mm});
            skLineSegment(sketch, "E2669", {"start": v(-55.72, 36.36) * mm, "end": v(-55.78, 36.41) * mm});
            skLineSegment(sketch, "E2670", {"start": v(-55.78, 36.41) * mm, "end": v(-55.84, 36.46) * mm});
            skLineSegment(sketch, "E2671", {"start": v(-55.84, 36.46) * mm, "end": v(-55.9, 36.51) * mm});
            skLineSegment(sketch, "E2672", {"start": v(-55.9, 36.51) * mm, "end": v(-55.97, 36.57) * mm});
            skLineSegment(sketch, "E2673", {"start": v(-55.97, 36.57) * mm, "end": v(-56.03, 36.62) * mm});
            skLineSegment(sketch, "E2674", {"start": v(-56.03, 36.62) * mm, "end": v(-56.1, 36.67) * mm});
            skLineSegment(sketch, "E2675", {"start": v(-56.1, 36.67) * mm, "end": v(-56.17, 36.72) * mm});
            skLineSegment(sketch, "E2676", {"start": v(-56.17, 36.72) * mm, "end": v(-56.24, 36.77) * mm});
            skLineSegment(sketch, "E2677", {"start": v(-56.24, 36.77) * mm, "end": v(-56.3, 36.83) * mm});
            skLineSegment(sketch, "E2678", {"start": v(-56.3, 36.83) * mm, "end": v(-56.38, 36.88) * mm});
            skLineSegment(sketch, "E2679", {"start": v(-56.38, 36.88) * mm, "end": v(-56.45, 36.93) * mm});
            skLineSegment(sketch, "E2680", {"start": v(-56.45, 36.93) * mm, "end": v(-56.53, 36.99) * mm});
            skLineSegment(sketch, "E2681", {"start": v(-56.53, 36.99) * mm, "end": v(-56.6, 37.04) * mm});
            skLineSegment(sketch, "E2682", {"start": v(-56.6, 37.04) * mm, "end": v(-56.68, 37.1) * mm});
            skLineSegment(sketch, "E2683", {"start": v(-56.68, 37.1) * mm, "end": v(-56.76, 37.15) * mm});
            skLineSegment(sketch, "E2684", {"start": v(-56.76, 37.15) * mm, "end": v(-56.84, 37.2) * mm});
            skLineSegment(sketch, "E2685", {"start": v(-56.84, 37.2) * mm, "end": v(-56.92, 37.27) * mm});
            skLineSegment(sketch, "E2686", {"start": v(-56.92, 37.27) * mm, "end": v(-57, 37.32) * mm});
            skLineSegment(sketch, "E2687", {"start": v(-57, 37.32) * mm, "end": v(-57.08, 37.38) * mm});
            skLineSegment(sketch, "E2688", {"start": v(-57.08, 37.38) * mm, "end": v(-57.17, 37.43) * mm});
            skLineSegment(sketch, "E2689", {"start": v(-57.17, 37.43) * mm, "end": v(-57.25, 37.5) * mm});
            skLineSegment(sketch, "E2690", {"start": v(-57.25, 37.5) * mm, "end": v(-57.34, 37.55) * mm});
            skLineSegment(sketch, "E2691", {"start": v(-57.34, 37.55) * mm, "end": v(-57.43, 37.6) * mm});
            skLineSegment(sketch, "E2692", {"start": v(-57.43, 37.6) * mm, "end": v(-57.52, 37.66) * mm});
            skLineSegment(sketch, "E2693", {"start": v(-57.52, 37.66) * mm, "end": v(-57.57, 37.66) * mm});
            skLineSegment(sketch, "E2694", {"start": v(-57.57, 37.66) * mm, "end": v(-58.43, 37.08) * mm});
            skLineSegment(sketch, "E2695", {"start": v(-58.43, 37.08) * mm, "end": v(-58.45, 37.03) * mm});
            skLineSegment(sketch, "E2696", {"start": v(-58.45, 37.03) * mm, "end": v(-58.43, 36.93) * mm});
            skLineSegment(sketch, "E2697", {"start": v(-58.43, 36.93) * mm, "end": v(-58.41, 36.82) * mm});
            skLineSegment(sketch, "E2698", {"start": v(-58.41, 36.82) * mm, "end": v(-58.4, 36.72) * mm});
            skLineSegment(sketch, "E2699", {"start": v(-58.4, 36.72) * mm, "end": v(-58.37, 36.62) * mm});
            skLineSegment(sketch, "E2700", {"start": v(-58.37, 36.62) * mm, "end": v(-58.35, 36.52) * mm});
            skLineSegment(sketch, "E2701", {"start": v(-58.35, 36.52) * mm, "end": v(-58.33, 36.42) * mm});
            skLineSegment(sketch, "E2702", {"start": v(-58.33, 36.42) * mm, "end": v(-58.3, 36.33) * mm});
            skLineSegment(sketch, "E2703", {"start": v(-58.3, 36.33) * mm, "end": v(-58.28, 36.23) * mm});
            skLineSegment(sketch, "E2704", {"start": v(-58.28, 36.23) * mm, "end": v(-58.26, 36.14) * mm});
            skLineSegment(sketch, "E2705", {"start": v(-58.26, 36.14) * mm, "end": v(-58.24, 36.04) * mm});
            skLineSegment(sketch, "E2706", {"start": v(-58.24, 36.04) * mm, "end": v(-58.22, 35.95) * mm});
            skLineSegment(sketch, "E2707", {"start": v(-58.22, 35.95) * mm, "end": v(-58.2, 35.86) * mm});
            skLineSegment(sketch, "E2708", {"start": v(-58.2, 35.86) * mm, "end": v(-58.17, 35.77) * mm});
            skLineSegment(sketch, "E2709", {"start": v(-58.17, 35.77) * mm, "end": v(-58.15, 35.68) * mm});
            skLineSegment(sketch, "E2710", {"start": v(-58.15, 35.68) * mm, "end": v(-58.12, 35.6) * mm});
            skLineSegment(sketch, "E2711", {"start": v(-58.12, 35.6) * mm, "end": v(-58.1, 35.51) * mm});
            skLineSegment(sketch, "E2712", {"start": v(-58.1, 35.51) * mm, "end": v(-58.08, 35.43) * mm});
            skLineSegment(sketch, "E2713", {"start": v(-58.08, 35.43) * mm, "end": v(-58.05, 35.35) * mm});
            skLineSegment(sketch, "E2714", {"start": v(-58.05, 35.35) * mm, "end": v(-58.03, 35.26) * mm});
            skLineSegment(sketch, "E2715", {"start": v(-58.03, 35.26) * mm, "end": v(-58, 35.18) * mm});
            skLineSegment(sketch, "E2716", {"start": v(-58, 35.18) * mm, "end": v(-57.98, 35.1) * mm});
            skLineSegment(sketch, "E2717", {"start": v(-57.98, 35.1) * mm, "end": v(-57.96, 35.03) * mm});
            skLineSegment(sketch, "E2718", {"start": v(-57.96, 35.03) * mm, "end": v(-57.94, 34.95) * mm});
            skLineSegment(sketch, "E2719", {"start": v(-57.94, 34.95) * mm, "end": v(-57.91, 34.88) * mm});
            skLineSegment(sketch, "E2720", {"start": v(-57.91, 34.88) * mm, "end": v(-57.89, 34.8) * mm});
            skLineSegment(sketch, "E2721", {"start": v(-57.89, 34.8) * mm, "end": v(-57.86, 34.73) * mm});
            skLineSegment(sketch, "E2722", {"start": v(-57.86, 34.73) * mm, "end": v(-57.84, 34.66) * mm});
            skLineSegment(sketch, "E2723", {"start": v(-57.84, 34.66) * mm, "end": v(-57.82, 34.59) * mm});
            skLineSegment(sketch, "E2724", {"start": v(-57.82, 34.59) * mm, "end": v(-57.8, 34.52) * mm});
            skLineSegment(sketch, "E2725", {"start": v(-57.8, 34.52) * mm, "end": v(-57.77, 34.45) * mm});
            skLineSegment(sketch, "E2726", {"start": v(-57.77, 34.45) * mm, "end": v(-57.75, 34.39) * mm});
            skLineSegment(sketch, "E2727", {"start": v(-57.75, 34.39) * mm, "end": v(-57.72, 34.32) * mm});
            skLineSegment(sketch, "E2728", {"start": v(-57.72, 34.32) * mm, "end": v(-57.7, 34.26) * mm});
            skLineSegment(sketch, "E2729", {"start": v(-57.7, 34.26) * mm, "end": v(-57.68, 34.2) * mm});
            skLineSegment(sketch, "E2730", {"start": v(-57.68, 34.2) * mm, "end": v(-57.65, 34.13) * mm});
            skLineSegment(sketch, "E2731", {"start": v(-57.65, 34.13) * mm, "end": v(-57.63, 34.07) * mm});
            skLineSegment(sketch, "E2732", {"start": v(-57.63, 34.07) * mm, "end": v(-57.6, 34.01) * mm});
            skLineSegment(sketch, "E2733", {"start": v(-57.6, 34.01) * mm, "end": v(-57.59, 33.96) * mm});
            skLineSegment(sketch, "E2734", {"start": v(-57.59, 33.96) * mm, "end": v(-57.56, 33.9) * mm});
            skLineSegment(sketch, "E2735", {"start": v(-57.56, 33.9) * mm, "end": v(-57.54, 33.85) * mm});
            skLineSegment(sketch, "E2736", {"start": v(-57.54, 33.85) * mm, "end": v(-57.72, 33.7) * mm});
            skLineSegment(sketch, "E2737", {"start": v(-57.72, 33.7) * mm, "end": v(-58.37, 33.22) * mm});
            skLineSegment(sketch, "E2738", {"start": v(-58.37, 33.22) * mm, "end": v(-58.56, 33.08) * mm});
            skLineSegment(sketch, "E2739", {"start": v(-58.56, 33.08) * mm, "end": v(-58.6, 33.12) * mm});
            skLineSegment(sketch, "E2740", {"start": v(-58.6, 33.12) * mm, "end": v(-58.66, 33.16) * mm});
            skLineSegment(sketch, "E2741", {"start": v(-58.66, 33.16) * mm, "end": v(-58.7, 33.2) * mm});
            skLineSegment(sketch, "E2742", {"start": v(-58.7, 33.2) * mm, "end": v(-58.75, 33.24) * mm});
            skLineSegment(sketch, "E2743", {"start": v(-58.75, 33.24) * mm, "end": v(-58.8, 33.27) * mm});
            skLineSegment(sketch, "E2744", {"start": v(-58.8, 33.27) * mm, "end": v(-58.86, 33.31) * mm});
            skLineSegment(sketch, "E2745", {"start": v(-58.86, 33.31) * mm, "end": v(-58.91, 33.35) * mm});
            skLineSegment(sketch, "E2746", {"start": v(-58.91, 33.35) * mm, "end": v(-58.97, 33.4) * mm});
            skLineSegment(sketch, "E2747", {"start": v(-58.97, 33.4) * mm, "end": v(-59.02, 33.44) * mm});
            skLineSegment(sketch, "E2748", {"start": v(-59.02, 33.44) * mm, "end": v(-59.08, 33.48) * mm});
            skLineSegment(sketch, "E2749", {"start": v(-59.08, 33.48) * mm, "end": v(-59.14, 33.52) * mm});
            skLineSegment(sketch, "E2750", {"start": v(-59.14, 33.52) * mm, "end": v(-59.2, 33.56) * mm});
            skLineSegment(sketch, "E2751", {"start": v(-59.2, 33.56) * mm, "end": v(-59.26, 33.6) * mm});
            skLineSegment(sketch, "E2752", {"start": v(-59.26, 33.6) * mm, "end": v(-59.32, 33.65) * mm});
            skLineSegment(sketch, "E2753", {"start": v(-59.32, 33.65) * mm, "end": v(-59.38, 33.7) * mm});
            skLineSegment(sketch, "E2754", {"start": v(-59.38, 33.7) * mm, "end": v(-59.44, 33.73) * mm});
            skLineSegment(sketch, "E2755", {"start": v(-59.44, 33.73) * mm, "end": v(-59.5, 33.78) * mm});
            skLineSegment(sketch, "E2756", {"start": v(-59.5, 33.78) * mm, "end": v(-59.58, 33.82) * mm});
            skLineSegment(sketch, "E2757", {"start": v(-59.58, 33.82) * mm, "end": v(-59.64, 33.87) * mm});
            skLineSegment(sketch, "E2758", {"start": v(-59.64, 33.87) * mm, "end": v(-59.71, 33.91) * mm});
            skLineSegment(sketch, "E2759", {"start": v(-59.71, 33.91) * mm, "end": v(-59.78, 33.96) * mm});
            skLineSegment(sketch, "E2760", {"start": v(-59.78, 33.96) * mm, "end": v(-59.85, 34) * mm});
            skLineSegment(sketch, "E2761", {"start": v(-59.85, 34) * mm, "end": v(-59.93, 34.05) * mm});
            skLineSegment(sketch, "E2762", {"start": v(-59.93, 34.05) * mm, "end": v(-60, 34.1) * mm});
            skLineSegment(sketch, "E2763", {"start": v(-60, 34.1) * mm, "end": v(-60.07, 34.14) * mm});
            skLineSegment(sketch, "E2764", {"start": v(-60.07, 34.14) * mm, "end": v(-60.15, 34.2) * mm});
            skLineSegment(sketch, "E2765", {"start": v(-60.15, 34.2) * mm, "end": v(-60.23, 34.24) * mm});
            skLineSegment(sketch, "E2766", {"start": v(-60.23, 34.24) * mm, "end": v(-60.3, 34.28) * mm});
            skLineSegment(sketch, "E2767", {"start": v(-60.3, 34.28) * mm, "end": v(-60.39, 34.33) * mm});
            skLineSegment(sketch, "E2768", {"start": v(-60.39, 34.33) * mm, "end": v(-60.47, 34.38) * mm});
            skLineSegment(sketch, "E2769", {"start": v(-60.47, 34.38) * mm, "end": v(-60.55, 34.43) * mm});
            skLineSegment(sketch, "E2770", {"start": v(-60.55, 34.43) * mm, "end": v(-60.64, 34.48) * mm});
            skLineSegment(sketch, "E2771", {"start": v(-60.64, 34.48) * mm, "end": v(-60.72, 34.52) * mm});
            skLineSegment(sketch, "E2772", {"start": v(-60.72, 34.52) * mm, "end": v(-60.8, 34.57) * mm});
            skLineSegment(sketch, "E2773", {"start": v(-60.8, 34.57) * mm, "end": v(-60.9, 34.62) * mm});
            skLineSegment(sketch, "E2774", {"start": v(-60.9, 34.62) * mm, "end": v(-60.98, 34.67) * mm});
            skLineSegment(sketch, "E2775", {"start": v(-60.98, 34.67) * mm, "end": v(-61.07, 34.72) * mm});
            skLineSegment(sketch, "E2776", {"start": v(-61.07, 34.72) * mm, "end": v(-61.17, 34.77) * mm});
            skLineSegment(sketch, "E2777", {"start": v(-61.17, 34.77) * mm, "end": v(-61.26, 34.82) * mm});
            skLineSegment(sketch, "E2778", {"start": v(-61.26, 34.82) * mm, "end": v(-61.35, 34.87) * mm});
            skLineSegment(sketch, "E2779", {"start": v(-61.35, 34.87) * mm, "end": v(-61.4, 34.86) * mm});
            skLineSegment(sketch, "E2780", {"start": v(-61.4, 34.86) * mm, "end": v(-62.2, 34.2) * mm});
            skLineSegment(sketch, "E2781", {"start": v(-62.2, 34.2) * mm, "end": v(-62.23, 34.15) * mm});
            skLineSegment(sketch, "E2782", {"start": v(-62.23, 34.15) * mm, "end": v(-62.2, 34.05) * mm});
            skLineSegment(sketch, "E2783", {"start": v(-62.2, 34.05) * mm, "end": v(-62.17, 33.95) * mm});
            skLineSegment(sketch, "E2784", {"start": v(-62.17, 33.95) * mm, "end": v(-62.14, 33.85) * mm});
            skLineSegment(sketch, "E2785", {"start": v(-62.14, 33.85) * mm, "end": v(-62.1, 33.75) * mm});
            skLineSegment(sketch, "E2786", {"start": v(-62.1, 33.75) * mm, "end": v(-62.08, 33.66) * mm});
            skLineSegment(sketch, "E2787", {"start": v(-62.08, 33.66) * mm, "end": v(-62.05, 33.56) * mm});
            skLineSegment(sketch, "E2788", {"start": v(-62.05, 33.56) * mm, "end": v(-62.02, 33.47) * mm});
            skLineSegment(sketch, "E2789", {"start": v(-62.02, 33.47) * mm, "end": v(-61.99, 33.37) * mm});
            skLineSegment(sketch, "E2790", {"start": v(-61.99, 33.37) * mm, "end": v(-61.96, 33.28) * mm});
            skLineSegment(sketch, "E2791", {"start": v(-61.96, 33.28) * mm, "end": v(-61.93, 33.19) * mm});
            skLineSegment(sketch, "E2792", {"start": v(-61.93, 33.19) * mm, "end": v(-61.9, 33.1) * mm});
            skLineSegment(sketch, "E2793", {"start": v(-61.9, 33.1) * mm, "end": v(-61.86, 33.01) * mm});
            skLineSegment(sketch, "E2794", {"start": v(-61.86, 33.01) * mm, "end": v(-61.83, 32.93) * mm});
            skLineSegment(sketch, "E2795", {"start": v(-61.83, 32.93) * mm, "end": v(-61.8, 32.84) * mm});
            skLineSegment(sketch, "E2796", {"start": v(-61.8, 32.84) * mm, "end": v(-61.77, 32.76) * mm});
            skLineSegment(sketch, "E2797", {"start": v(-61.77, 32.76) * mm, "end": v(-61.74, 32.67) * mm});
            skLineSegment(sketch, "E2798", {"start": v(-61.74, 32.67) * mm, "end": v(-61.7, 32.6) * mm});
            skLineSegment(sketch, "E2799", {"start": v(-61.7, 32.6) * mm, "end": v(-61.68, 32.51) * mm});
            skLineSegment(sketch, "E2800", {"start": v(-61.68, 32.51) * mm, "end": v(-61.65, 32.43) * mm});
            skLineSegment(sketch, "E2801", {"start": v(-61.65, 32.43) * mm, "end": v(-61.62, 32.35) * mm});
            skLineSegment(sketch, "E2802", {"start": v(-61.62, 32.35) * mm, "end": v(-61.59, 32.28) * mm});
            skLineSegment(sketch, "E2803", {"start": v(-61.59, 32.28) * mm, "end": v(-61.56, 32.2) * mm});
            skLineSegment(sketch, "E2804", {"start": v(-61.56, 32.2) * mm, "end": v(-61.53, 32.13) * mm});
            skLineSegment(sketch, "E2805", {"start": v(-61.53, 32.13) * mm, "end": v(-61.5, 32.06) * mm});
            skLineSegment(sketch, "E2806", {"start": v(-61.5, 32.06) * mm, "end": v(-61.47, 31.99) * mm});
            skLineSegment(sketch, "E2807", {"start": v(-61.47, 31.99) * mm, "end": v(-61.44, 31.91) * mm});
            skLineSegment(sketch, "E2808", {"start": v(-61.44, 31.91) * mm, "end": v(-61.4, 31.85) * mm});
            skLineSegment(sketch, "E2809", {"start": v(-61.4, 31.85) * mm, "end": v(-61.38, 31.78) * mm});
            skLineSegment(sketch, "E2810", {"start": v(-61.38, 31.78) * mm, "end": v(-61.35, 31.71) * mm});
            skLineSegment(sketch, "E2811", {"start": v(-61.35, 31.71) * mm, "end": v(-61.32, 31.65) * mm});
            skLineSegment(sketch, "E2812", {"start": v(-61.32, 31.65) * mm, "end": v(-61.29, 31.58) * mm});
            skLineSegment(sketch, "E2813", {"start": v(-61.29, 31.58) * mm, "end": v(-61.26, 31.52) * mm});
            skLineSegment(sketch, "E2814", {"start": v(-61.26, 31.52) * mm, "end": v(-61.23, 31.46) * mm});
            skLineSegment(sketch, "E2815", {"start": v(-61.23, 31.46) * mm, "end": v(-61.2, 31.4) * mm});
            skLineSegment(sketch, "E2816", {"start": v(-61.2, 31.4) * mm, "end": v(-61.17, 31.34) * mm});
            skLineSegment(sketch, "E2817", {"start": v(-61.17, 31.34) * mm, "end": v(-61.14, 31.28) * mm});
            skLineSegment(sketch, "E2818", {"start": v(-61.14, 31.28) * mm, "end": v(-61.12, 31.23) * mm});
            skLineSegment(sketch, "E2819", {"start": v(-61.12, 31.23) * mm, "end": v(-61.09, 31.17) * mm});
            skLineSegment(sketch, "E2820", {"start": v(-61.09, 31.17) * mm, "end": v(-61.06, 31.12) * mm});
            skLineSegment(sketch, "E2821", {"start": v(-61.06, 31.12) * mm, "end": v(-61.03, 31.06) * mm});
            skLineSegment(sketch, "E2822", {"start": v(-61.03, 31.06) * mm, "end": v(-61.2, 30.9) * mm});
            skLineSegment(sketch, "E2823", {"start": v(-61.2, 30.9) * mm, "end": v(-61.8, 30.36) * mm});
            skLineSegment(sketch, "E2824", {"start": v(-61.8, 30.36) * mm, "end": v(-61.98, 30.21) * mm});
            skLineSegment(sketch, "E2825", {"start": v(-61.98, 30.21) * mm, "end": v(-62.03, 30.25) * mm});
            skLineSegment(sketch, "E2826", {"start": v(-62.03, 30.25) * mm, "end": v(-62.08, 30.28) * mm});
            skLineSegment(sketch, "E2827", {"start": v(-62.08, 30.28) * mm, "end": v(-62.13, 30.31) * mm});
            skLineSegment(sketch, "E2828", {"start": v(-62.13, 30.31) * mm, "end": v(-62.19, 30.35) * mm});
            skLineSegment(sketch, "E2829", {"start": v(-62.19, 30.35) * mm, "end": v(-62.24, 30.38) * mm});
            skLineSegment(sketch, "E2830", {"start": v(-62.24, 30.38) * mm, "end": v(-62.3, 30.42) * mm});
            skLineSegment(sketch, "E2831", {"start": v(-62.3, 30.42) * mm, "end": v(-62.35, 30.45) * mm});
            skLineSegment(sketch, "E2832", {"start": v(-62.35, 30.45) * mm, "end": v(-62.41, 30.49) * mm});
            skLineSegment(sketch, "E2833", {"start": v(-62.41, 30.49) * mm, "end": v(-62.47, 30.52) * mm});
            skLineSegment(sketch, "E2834", {"start": v(-62.47, 30.52) * mm, "end": v(-62.53, 30.56) * mm});
            skLineSegment(sketch, "E2835", {"start": v(-62.53, 30.56) * mm, "end": v(-62.6, 30.6) * mm});
            skLineSegment(sketch, "E2836", {"start": v(-62.6, 30.6) * mm, "end": v(-62.66, 30.63) * mm});
            skLineSegment(sketch, "E2837", {"start": v(-62.66, 30.63) * mm, "end": v(-62.72, 30.67) * mm});
            skLineSegment(sketch, "E2838", {"start": v(-62.72, 30.67) * mm, "end": v(-62.78, 30.7) * mm});
            skLineSegment(sketch, "E2839", {"start": v(-62.78, 30.7) * mm, "end": v(-62.85, 30.74) * mm});
            skLineSegment(sketch, "E2840", {"start": v(-62.85, 30.74) * mm, "end": v(-62.92, 30.78) * mm});
            skLineSegment(sketch, "E2841", {"start": v(-62.92, 30.78) * mm, "end": v(-62.99, 30.82) * mm});
            skLineSegment(sketch, "E2842", {"start": v(-62.99, 30.82) * mm, "end": v(-63.06, 30.86) * mm});
            skLineSegment(sketch, "E2843", {"start": v(-63.06, 30.86) * mm, "end": v(-63.13, 30.9) * mm});
            skLineSegment(sketch, "E2844", {"start": v(-63.13, 30.9) * mm, "end": v(-63.2, 30.94) * mm});
            skLineSegment(sketch, "E2845", {"start": v(-63.2, 30.94) * mm, "end": v(-63.28, 30.98) * mm});
            skLineSegment(sketch, "E2846", {"start": v(-63.28, 30.98) * mm, "end": v(-63.35, 31.01) * mm});
            skLineSegment(sketch, "E2847", {"start": v(-63.35, 31.01) * mm, "end": v(-63.43, 31.05) * mm});
            skLineSegment(sketch, "E2848", {"start": v(-63.43, 31.05) * mm, "end": v(-63.5, 31.1) * mm});
            skLineSegment(sketch, "E2849", {"start": v(-63.5, 31.1) * mm, "end": v(-63.58, 31.13) * mm});
            skLineSegment(sketch, "E2850", {"start": v(-63.58, 31.13) * mm, "end": v(-63.66, 31.17) * mm});
            skLineSegment(sketch, "E2851", {"start": v(-63.66, 31.17) * mm, "end": v(-63.75, 31.21) * mm});
            skLineSegment(sketch, "E2852", {"start": v(-63.75, 31.21) * mm, "end": v(-63.83, 31.25) * mm});
            skLineSegment(sketch, "E2853", {"start": v(-63.83, 31.25) * mm, "end": v(-63.91, 31.3) * mm});
            skLineSegment(sketch, "E2854", {"start": v(-63.91, 31.3) * mm, "end": v(-64, 31.33) * mm});
            skLineSegment(sketch, "E2855", {"start": v(-64, 31.33) * mm, "end": v(-64.08, 31.37) * mm});
            skLineSegment(sketch, "E2856", {"start": v(-64.08, 31.37) * mm, "end": v(-64.17, 31.41) * mm});
            skLineSegment(sketch, "E2857", {"start": v(-64.17, 31.41) * mm, "end": v(-64.26, 31.45) * mm});
            skLineSegment(sketch, "E2858", {"start": v(-64.26, 31.45) * mm, "end": v(-64.35, 31.5) * mm});
            skLineSegment(sketch, "E2859", {"start": v(-64.35, 31.5) * mm, "end": v(-64.44, 31.54) * mm});
            skLineSegment(sketch, "E2860", {"start": v(-64.44, 31.54) * mm, "end": v(-64.54, 31.58) * mm});
            skLineSegment(sketch, "E2861", {"start": v(-64.54, 31.58) * mm, "end": v(-64.63, 31.62) * mm});
            skLineSegment(sketch, "E2862", {"start": v(-64.63, 31.62) * mm, "end": v(-64.73, 31.66) * mm});
            skLineSegment(sketch, "E2863", {"start": v(-64.73, 31.66) * mm, "end": v(-64.82, 31.7) * mm});
            skLineSegment(sketch, "E2864", {"start": v(-64.82, 31.7) * mm, "end": v(-64.92, 31.74) * mm});
            skLineSegment(sketch, "E2865", {"start": v(-64.92, 31.74) * mm, "end": v(-64.97, 31.73) * mm});
            skLineSegment(sketch, "E2866", {"start": v(-64.97, 31.73) * mm, "end": v(-65.71, 31) * mm});
            skLineSegment(sketch, "E2867", {"start": v(-65.71, 31) * mm, "end": v(-65.73, 30.95) * mm});
            skLineSegment(sketch, "E2868", {"start": v(-65.73, 30.95) * mm, "end": v(-65.69, 30.85) * mm});
            skLineSegment(sketch, "E2869", {"start": v(-65.69, 30.85) * mm, "end": v(-65.65, 30.75) * mm});
            skLineSegment(sketch, "E2870", {"start": v(-65.65, 30.75) * mm, "end": v(-65.61, 30.66) * mm});
            skLineSegment(sketch, "E2871", {"start": v(-65.61, 30.66) * mm, "end": v(-65.57, 30.56) * mm});
            skLineSegment(sketch, "E2872", {"start": v(-65.57, 30.56) * mm, "end": v(-65.53, 30.47) * mm});
            skLineSegment(sketch, "E2873", {"start": v(-65.53, 30.47) * mm, "end": v(-65.5, 30.37) * mm});
            skLineSegment(sketch, "E2874", {"start": v(-65.5, 30.37) * mm, "end": v(-65.46, 30.28) * mm});
            skLineSegment(sketch, "E2875", {"start": v(-65.46, 30.28) * mm, "end": v(-65.42, 30.2) * mm});
            skLineSegment(sketch, "E2876", {"start": v(-65.42, 30.2) * mm, "end": v(-65.38, 30.1) * mm});
            skLineSegment(sketch, "E2877", {"start": v(-65.38, 30.1) * mm, "end": v(-65.34, 30.02) * mm});
            skLineSegment(sketch, "E2878", {"start": v(-65.34, 30.02) * mm, "end": v(-65.3, 29.93) * mm});
            skLineSegment(sketch, "E2879", {"start": v(-65.3, 29.93) * mm, "end": v(-65.26, 29.85) * mm});
            skLineSegment(sketch, "E2880", {"start": v(-65.26, 29.85) * mm, "end": v(-65.23, 29.76) * mm});
            skLineSegment(sketch, "E2881", {"start": v(-65.23, 29.76) * mm, "end": v(-65.19, 29.68) * mm});
            skLineSegment(sketch, "E2882", {"start": v(-65.19, 29.68) * mm, "end": v(-65.15, 29.6) * mm});
            skLineSegment(sketch, "E2883", {"start": v(-65.15, 29.6) * mm, "end": v(-65.11, 29.52) * mm});
            skLineSegment(sketch, "E2884", {"start": v(-65.11, 29.52) * mm, "end": v(-65.07, 29.44) * mm});
            skLineSegment(sketch, "E2885", {"start": v(-65.07, 29.44) * mm, "end": v(-65.04, 29.36) * mm});
            skLineSegment(sketch, "E2886", {"start": v(-65.04, 29.36) * mm, "end": v(-65, 29.29) * mm});
            skLineSegment(sketch, "E2887", {"start": v(-65, 29.29) * mm, "end": v(-64.96, 29.21) * mm});
            skLineSegment(sketch, "E2888", {"start": v(-64.96, 29.21) * mm, "end": v(-64.92, 29.14) * mm});
            skLineSegment(sketch, "E2889", {"start": v(-64.92, 29.14) * mm, "end": v(-64.89, 29.07) * mm});
            skLineSegment(sketch, "E2890", {"start": v(-64.89, 29.07) * mm, "end": v(-64.85, 29) * mm});
            skLineSegment(sketch, "E2891", {"start": v(-64.85, 29) * mm, "end": v(-64.81, 28.93) * mm});
            skLineSegment(sketch, "E2892", {"start": v(-64.81, 28.93) * mm, "end": v(-64.78, 28.86) * mm});
            skLineSegment(sketch, "E2893", {"start": v(-64.78, 28.86) * mm, "end": v(-64.74, 28.8) * mm});
            skLineSegment(sketch, "E2894", {"start": v(-64.74, 28.8) * mm, "end": v(-64.7, 28.73) * mm});
            skLineSegment(sketch, "E2895", {"start": v(-64.7, 28.73) * mm, "end": v(-64.67, 28.66) * mm});
            skLineSegment(sketch, "E2896", {"start": v(-64.67, 28.66) * mm, "end": v(-64.63, 28.6) * mm});
            skLineSegment(sketch, "E2897", {"start": v(-64.63, 28.6) * mm, "end": v(-64.6, 28.54) * mm});
            skLineSegment(sketch, "E2898", {"start": v(-64.6, 28.54) * mm, "end": v(-64.56, 28.47) * mm});
            skLineSegment(sketch, "E2899", {"start": v(-64.56, 28.47) * mm, "end": v(-64.53, 28.41) * mm});
            skLineSegment(sketch, "E2900", {"start": v(-64.53, 28.41) * mm, "end": v(-64.5, 28.36) * mm});
            skLineSegment(sketch, "E2901", {"start": v(-64.5, 28.36) * mm, "end": v(-64.46, 28.3) * mm});
            skLineSegment(sketch, "E2902", {"start": v(-64.46, 28.3) * mm, "end": v(-64.43, 28.24) * mm});
            skLineSegment(sketch, "E2903", {"start": v(-64.43, 28.24) * mm, "end": v(-64.4, 28.19) * mm});
            skLineSegment(sketch, "E2904", {"start": v(-64.4, 28.19) * mm, "end": v(-64.36, 28.13) * mm});
            skLineSegment(sketch, "E2905", {"start": v(-64.36, 28.13) * mm, "end": v(-64.33, 28.08) * mm});
            skLineSegment(sketch, "E2906", {"start": v(-64.33, 28.08) * mm, "end": v(-64.3, 28.03) * mm});
            skLineSegment(sketch, "E2907", {"start": v(-64.3, 28.03) * mm, "end": v(-64.26, 27.98) * mm});
            skLineSegment(sketch, "E2908", {"start": v(-64.26, 27.98) * mm, "end": v(-64.42, 27.8) * mm});
            skLineSegment(sketch, "E2909", {"start": v(-64.42, 27.8) * mm, "end": v(-64.97, 27.21) * mm});
            skLineSegment(sketch, "E2910", {"start": v(-64.97, 27.21) * mm, "end": v(-65.13, 27.05) * mm});
            skLineSegment(sketch, "E2911", {"start": v(-65.13, 27.05) * mm, "end": v(-65.18, 27.08) * mm});
            skLineSegment(sketch, "E2912", {"start": v(-65.18, 27.08) * mm, "end": v(-65.24, 27.1) * mm});
            skLineSegment(sketch, "E2913", {"start": v(-65.24, 27.1) * mm, "end": v(-65.3, 27.13) * mm});
            skLineSegment(sketch, "E2914", {"start": v(-65.3, 27.13) * mm, "end": v(-65.35, 27.16) * mm});
            skLineSegment(sketch, "E2915", {"start": v(-65.35, 27.16) * mm, "end": v(-65.4, 27.2) * mm});
            skLineSegment(sketch, "E2916", {"start": v(-65.4, 27.2) * mm, "end": v(-65.46, 27.22) * mm});
            skLineSegment(sketch, "E2917", {"start": v(-65.46, 27.22) * mm, "end": v(-65.52, 27.25) * mm});
            skLineSegment(sketch, "E2918", {"start": v(-65.52, 27.25) * mm, "end": v(-65.58, 27.28) * mm});
            skLineSegment(sketch, "E2919", {"start": v(-65.58, 27.28) * mm, "end": v(-65.65, 27.31) * mm});
            skLineSegment(sketch, "E2920", {"start": v(-65.65, 27.31) * mm, "end": v(-65.7, 27.34) * mm});
            skLineSegment(sketch, "E2921", {"start": v(-65.7, 27.34) * mm, "end": v(-65.77, 27.37) * mm});
            skLineSegment(sketch, "E2922", {"start": v(-65.77, 27.37) * mm, "end": v(-65.84, 27.4) * mm});
            skLineSegment(sketch, "E2923", {"start": v(-65.84, 27.4) * mm, "end": v(-65.9, 27.44) * mm});
            skLineSegment(sketch, "E2924", {"start": v(-65.9, 27.44) * mm, "end": v(-65.98, 27.47) * mm});
            skLineSegment(sketch, "E2925", {"start": v(-65.98, 27.47) * mm, "end": v(-66.04, 27.5) * mm});
            skLineSegment(sketch, "E2926", {"start": v(-66.04, 27.5) * mm, "end": v(-66.12, 27.53) * mm});
            skLineSegment(sketch, "E2927", {"start": v(-66.12, 27.53) * mm, "end": v(-66.19, 27.56) * mm});
            skLineSegment(sketch, "E2928", {"start": v(-66.19, 27.56) * mm, "end": v(-66.26, 27.6) * mm});
            skLineSegment(sketch, "E2929", {"start": v(-66.26, 27.6) * mm, "end": v(-66.34, 27.63) * mm});
            skLineSegment(sketch, "E2930", {"start": v(-66.34, 27.63) * mm, "end": v(-66.41, 27.66) * mm});
            skLineSegment(sketch, "E2931", {"start": v(-66.41, 27.66) * mm, "end": v(-66.49, 27.7) * mm});
            skLineSegment(sketch, "E2932", {"start": v(-66.49, 27.7) * mm, "end": v(-66.57, 27.72) * mm});
            skLineSegment(sketch, "E2933", {"start": v(-66.57, 27.72) * mm, "end": v(-66.65, 27.76) * mm});
            skLineSegment(sketch, "E2934", {"start": v(-66.65, 27.76) * mm, "end": v(-66.73, 27.79) * mm});
            skLineSegment(sketch, "E2935", {"start": v(-66.73, 27.79) * mm, "end": v(-66.8, 27.82) * mm});
            skLineSegment(sketch, "E2936", {"start": v(-66.8, 27.82) * mm, "end": v(-66.9, 27.85) * mm});
            skLineSegment(sketch, "E2937", {"start": v(-66.9, 27.85) * mm, "end": v(-66.98, 27.89) * mm});
            skLineSegment(sketch, "E2938", {"start": v(-66.98, 27.89) * mm, "end": v(-67.06, 27.92) * mm});
            skLineSegment(sketch, "E2939", {"start": v(-67.06, 27.92) * mm, "end": v(-67.15, 27.95) * mm});
            skLineSegment(sketch, "E2940", {"start": v(-67.15, 27.95) * mm, "end": v(-67.24, 27.98) * mm});
            skLineSegment(sketch, "E2941", {"start": v(-67.24, 27.98) * mm, "end": v(-67.33, 28.02) * mm});
            skLineSegment(sketch, "E2942", {"start": v(-67.33, 28.02) * mm, "end": v(-67.42, 28.05) * mm});
            skLineSegment(sketch, "E2943", {"start": v(-67.42, 28.05) * mm, "end": v(-67.51, 28.08) * mm});
            skLineSegment(sketch, "E2944", {"start": v(-67.51, 28.08) * mm, "end": v(-67.6, 28.11) * mm});
            skLineSegment(sketch, "E2945", {"start": v(-67.6, 28.11) * mm, "end": v(-67.7, 28.14) * mm});
            skLineSegment(sketch, "E2946", {"start": v(-67.7, 28.14) * mm, "end": v(-67.8, 28.18) * mm});
            skLineSegment(sketch, "E2947", {"start": v(-67.8, 28.18) * mm, "end": v(-67.9, 28.2) * mm});
            skLineSegment(sketch, "E2948", {"start": v(-67.9, 28.2) * mm, "end": v(-68, 28.24) * mm});
            skLineSegment(sketch, "E2949", {"start": v(-68, 28.24) * mm, "end": v(-68.1, 28.27) * mm});
            skLineSegment(sketch, "E2950", {"start": v(-68.1, 28.27) * mm, "end": v(-68.2, 28.3) * mm});
            skLineSegment(sketch, "E2951", {"start": v(-68.2, 28.3) * mm, "end": v(-68.24, 28.29) * mm});
            skLineSegment(sketch, "E2952", {"start": v(-68.24, 28.29) * mm, "end": v(-68.92, 27.5) * mm});
            skLineSegment(sketch, "E2953", {"start": v(-68.92, 27.5) * mm, "end": v(-68.93, 27.45) * mm});
            skLineSegment(sketch, "E2954", {"start": v(-68.93, 27.45) * mm, "end": v(-68.88, 27.35) * mm});
            skLineSegment(sketch, "E2955", {"start": v(-68.88, 27.35) * mm, "end": v(-68.83, 27.26) * mm});
            skLineSegment(sketch, "E2956", {"start": v(-68.83, 27.26) * mm, "end": v(-68.79, 27.16) * mm});
            skLineSegment(sketch, "E2957", {"start": v(-68.79, 27.16) * mm, "end": v(-68.74, 27.07) * mm});
            skLineSegment(sketch, "E2958", {"start": v(-68.74, 27.07) * mm, "end": v(-68.7, 26.98) * mm});
            skLineSegment(sketch, "E2959", {"start": v(-68.7, 26.98) * mm, "end": v(-68.65, 26.9) * mm});
            skLineSegment(sketch, "E2960", {"start": v(-68.65, 26.9) * mm, "end": v(-68.6, 26.8) * mm});
            skLineSegment(sketch, "E2961", {"start": v(-68.6, 26.8) * mm, "end": v(-68.55, 26.72) * mm});
            skLineSegment(sketch, "E2962", {"start": v(-68.55, 26.72) * mm, "end": v(-68.5, 26.63) * mm});
            skLineSegment(sketch, "E2963", {"start": v(-68.5, 26.63) * mm, "end": v(-68.46, 26.55) * mm});
            skLineSegment(sketch, "E2964", {"start": v(-68.46, 26.55) * mm, "end": v(-68.41, 26.47) * mm});
            skLineSegment(sketch, "E2965", {"start": v(-68.41, 26.47) * mm, "end": v(-68.37, 26.39) * mm});
            skLineSegment(sketch, "E2966", {"start": v(-68.37, 26.39) * mm, "end": v(-68.32, 26.3) * mm});
            skLineSegment(sketch, "E2967", {"start": v(-68.32, 26.3) * mm, "end": v(-68.28, 26.23) * mm});
            skLineSegment(sketch, "E2968", {"start": v(-68.28, 26.23) * mm, "end": v(-68.23, 26.15) * mm});
            skLineSegment(sketch, "E2969", {"start": v(-68.23, 26.15) * mm, "end": v(-68.19, 26.08) * mm});
            skLineSegment(sketch, "E2970", {"start": v(-68.19, 26.08) * mm, "end": v(-68.14, 26) * mm});
            skLineSegment(sketch, "E2971", {"start": v(-68.14, 26) * mm, "end": v(-68.1, 25.93) * mm});
            skLineSegment(sketch, "E2972", {"start": v(-68.1, 25.93) * mm, "end": v(-68.05, 25.86) * mm});
            skLineSegment(sketch, "E2973", {"start": v(-68.05, 25.86) * mm, "end": v(-68, 25.78) * mm});
            skLineSegment(sketch, "E2974", {"start": v(-68, 25.78) * mm, "end": v(-67.96, 25.71) * mm});
            skLineSegment(sketch, "E2975", {"start": v(-67.96, 25.71) * mm, "end": v(-67.92, 25.65) * mm});
            skLineSegment(sketch, "E2976", {"start": v(-67.92, 25.65) * mm, "end": v(-67.88, 25.58) * mm});
            skLineSegment(sketch, "E2977", {"start": v(-67.88, 25.58) * mm, "end": v(-67.84, 25.51) * mm});
            skLineSegment(sketch, "E2978", {"start": v(-67.84, 25.51) * mm, "end": v(-67.8, 25.45) * mm});
            skLineSegment(sketch, "E2979", {"start": v(-67.8, 25.45) * mm, "end": v(-67.75, 25.38) * mm});
            skLineSegment(sketch, "E2980", {"start": v(-67.75, 25.38) * mm, "end": v(-67.7, 25.32) * mm});
            skLineSegment(sketch, "E2981", {"start": v(-67.7, 25.32) * mm, "end": v(-67.67, 25.26) * mm});
            skLineSegment(sketch, "E2982", {"start": v(-67.67, 25.26) * mm, "end": v(-67.63, 25.2) * mm});
            skLineSegment(sketch, "E2983", {"start": v(-67.63, 25.2) * mm, "end": v(-67.59, 25.14) * mm});
            skLineSegment(sketch, "E2984", {"start": v(-67.59, 25.14) * mm, "end": v(-67.55, 25.08) * mm});
            skLineSegment(sketch, "E2985", {"start": v(-67.55, 25.08) * mm, "end": v(-67.5, 25.03) * mm});
            skLineSegment(sketch, "E2986", {"start": v(-67.5, 25.03) * mm, "end": v(-67.47, 24.97) * mm});
            skLineSegment(sketch, "E2987", {"start": v(-67.47, 24.97) * mm, "end": v(-67.43, 24.92) * mm});
            skLineSegment(sketch, "E2988", {"start": v(-67.43, 24.92) * mm, "end": v(-67.39, 24.87) * mm});
            skLineSegment(sketch, "E2989", {"start": v(-67.39, 24.87) * mm, "end": v(-67.35, 24.81) * mm});
            skLineSegment(sketch, "E2990", {"start": v(-67.35, 24.81) * mm, "end": v(-67.31, 24.76) * mm});
            skLineSegment(sketch, "E2991", {"start": v(-67.31, 24.76) * mm, "end": v(-67.28, 24.71) * mm});
            skLineSegment(sketch, "E2992", {"start": v(-67.28, 24.71) * mm, "end": v(-67.24, 24.66) * mm});
            skLineSegment(sketch, "E2993", {"start": v(-67.24, 24.66) * mm, "end": v(-67.2, 24.62) * mm});
            skLineSegment(sketch, "E2994", {"start": v(-67.2, 24.62) * mm, "end": v(-67.34, 24.43) * mm});
            skLineSegment(sketch, "E2995", {"start": v(-67.34, 24.43) * mm, "end": v(-67.84, 23.8) * mm});
            skLineSegment(sketch, "E2996", {"start": v(-67.84, 23.8) * mm, "end": v(-67.98, 23.61) * mm});
            skLineSegment(sketch, "E2997", {"start": v(-67.98, 23.61) * mm, "end": v(-68.04, 23.64) * mm});
            skLineSegment(sketch, "E2998", {"start": v(-68.04, 23.64) * mm, "end": v(-68.1, 23.66) * mm});
            skLineSegment(sketch, "E2999", {"start": v(-68.1, 23.66) * mm, "end": v(-68.15, 23.68) * mm});
            skLineSegment(sketch, "E3000", {"start": v(-68.15, 23.68) * mm, "end": v(-68.21, 23.7) * mm});
            skLineSegment(sketch, "E3001", {"start": v(-68.21, 23.7) * mm, "end": v(-68.27, 23.73) * mm});
            skLineSegment(sketch, "E3002", {"start": v(-68.27, 23.73) * mm, "end": v(-68.33, 23.76) * mm});
            skLineSegment(sketch, "E3003", {"start": v(-68.33, 23.76) * mm, "end": v(-68.4, 23.78) * mm});
            skLineSegment(sketch, "E3004", {"start": v(-68.4, 23.78) * mm, "end": v(-68.46, 23.8) * mm});
            skLineSegment(sketch, "E3005", {"start": v(-68.46, 23.8) * mm, "end": v(-68.52, 23.83) * mm});
            skLineSegment(sketch, "E3006", {"start": v(-68.52, 23.83) * mm, "end": v(-68.59, 23.85) * mm});
            skLineSegment(sketch, "E3007", {"start": v(-68.59, 23.85) * mm, "end": v(-68.65, 23.88) * mm});
            skLineSegment(sketch, "E3008", {"start": v(-68.65, 23.88) * mm, "end": v(-68.72, 23.9) * mm});
            skLineSegment(sketch, "E3009", {"start": v(-68.72, 23.9) * mm, "end": v(-68.8, 23.93) * mm});
            skLineSegment(sketch, "E3010", {"start": v(-68.8, 23.93) * mm, "end": v(-68.86, 23.95) * mm});
            skLineSegment(sketch, "E3011", {"start": v(-68.86, 23.95) * mm, "end": v(-68.93, 23.98) * mm});
            skLineSegment(sketch, "E3012", {"start": v(-68.93, 23.98) * mm, "end": v(-69, 24) * mm});
            skLineSegment(sketch, "E3013", {"start": v(-69, 24) * mm, "end": v(-69.08, 24.03) * mm});
            skLineSegment(sketch, "E3014", {"start": v(-69.08, 24.03) * mm, "end": v(-69.16, 24.06) * mm});
            skLineSegment(sketch, "E3015", {"start": v(-69.16, 24.06) * mm, "end": v(-69.24, 24.08) * mm});
            skLineSegment(sketch, "E3016", {"start": v(-69.24, 24.08) * mm, "end": v(-69.31, 24.1) * mm});
            skLineSegment(sketch, "E3017", {"start": v(-69.31, 24.1) * mm, "end": v(-69.4, 24.13) * mm});
            skLineSegment(sketch, "E3018", {"start": v(-69.4, 24.13) * mm, "end": v(-69.47, 24.16) * mm});
            skLineSegment(sketch, "E3019", {"start": v(-69.47, 24.16) * mm, "end": v(-69.56, 24.18) * mm});
            skLineSegment(sketch, "E3020", {"start": v(-69.56, 24.18) * mm, "end": v(-69.64, 24.2) * mm});
            skLineSegment(sketch, "E3021", {"start": v(-69.64, 24.2) * mm, "end": v(-69.72, 24.23) * mm});
            skLineSegment(sketch, "E3022", {"start": v(-69.72, 24.23) * mm, "end": v(-69.81, 24.26) * mm});
            skLineSegment(sketch, "E3023", {"start": v(-69.81, 24.26) * mm, "end": v(-69.9, 24.28) * mm});
            skLineSegment(sketch, "E3024", {"start": v(-69.9, 24.28) * mm, "end": v(-69.99, 24.3) * mm});
            skLineSegment(sketch, "E3025", {"start": v(-69.99, 24.3) * mm, "end": v(-70.08, 24.33) * mm});
            skLineSegment(sketch, "E3026", {"start": v(-70.08, 24.33) * mm, "end": v(-70.17, 24.35) * mm});
            skLineSegment(sketch, "E3027", {"start": v(-70.17, 24.35) * mm, "end": v(-70.26, 24.38) * mm});
            skLineSegment(sketch, "E3028", {"start": v(-70.26, 24.38) * mm, "end": v(-70.35, 24.4) * mm});
            skLineSegment(sketch, "E3029", {"start": v(-70.35, 24.4) * mm, "end": v(-70.45, 24.43) * mm});
            skLineSegment(sketch, "E3030", {"start": v(-70.45, 24.43) * mm, "end": v(-70.55, 24.45) * mm});
            skLineSegment(sketch, "E3031", {"start": v(-70.55, 24.45) * mm, "end": v(-70.64, 24.47) * mm});
            skLineSegment(sketch, "E3032", {"start": v(-70.64, 24.47) * mm, "end": v(-70.74, 24.5) * mm});
            skLineSegment(sketch, "E3033", {"start": v(-70.74, 24.5) * mm, "end": v(-70.84, 24.52) * mm});
            skLineSegment(sketch, "E3034", {"start": v(-70.84, 24.52) * mm, "end": v(-70.94, 24.54) * mm});
            skLineSegment(sketch, "E3035", {"start": v(-70.94, 24.54) * mm, "end": v(-71.05, 24.57) * mm});
            skLineSegment(sketch, "E3036", {"start": v(-71.05, 24.57) * mm, "end": v(-71.15, 24.59) * mm});
            skLineSegment(sketch, "E3037", {"start": v(-71.15, 24.59) * mm, "end": v(-71.2, 24.57) * mm});
            skLineSegment(sketch, "E3038", {"start": v(-71.2, 24.57) * mm, "end": v(-71.8, 23.72) * mm});
            skLineSegment(sketch, "E3039", {"start": v(-71.8, 23.72) * mm, "end": v(-71.8, 23.67) * mm});
            skLineSegment(sketch, "E3040", {"start": v(-71.8, 23.67) * mm, "end": v(-71.75, 23.58) * mm});
            skLineSegment(sketch, "E3041", {"start": v(-71.75, 23.58) * mm, "end": v(-71.7, 23.49) * mm});
            skLineSegment(sketch, "E3042", {"start": v(-71.7, 23.49) * mm, "end": v(-71.64, 23.4) * mm});
            skLineSegment(sketch, "E3043", {"start": v(-71.64, 23.4) * mm, "end": v(-71.58, 23.31) * mm});
            skLineSegment(sketch, "E3044", {"start": v(-71.58, 23.31) * mm, "end": v(-71.53, 23.23) * mm});
            skLineSegment(sketch, "E3045", {"start": v(-71.53, 23.23) * mm, "end": v(-71.47, 23.14) * mm});
            skLineSegment(sketch, "E3046", {"start": v(-71.47, 23.14) * mm, "end": v(-71.42, 23.06) * mm});
            skLineSegment(sketch, "E3047", {"start": v(-71.42, 23.06) * mm, "end": v(-71.36, 22.98) * mm});
            skLineSegment(sketch, "E3048", {"start": v(-71.36, 22.98) * mm, "end": v(-71.3, 22.9) * mm});
            skLineSegment(sketch, "E3049", {"start": v(-71.3, 22.9) * mm, "end": v(-71.25, 22.82) * mm});
            skLineSegment(sketch, "E3050", {"start": v(-71.25, 22.82) * mm, "end": v(-71.2, 22.74) * mm});
            skLineSegment(sketch, "E3051", {"start": v(-71.2, 22.74) * mm, "end": v(-71.15, 22.66) * mm});
            skLineSegment(sketch, "E3052", {"start": v(-71.15, 22.66) * mm, "end": v(-71.1, 22.59) * mm});
            skLineSegment(sketch, "E3053", {"start": v(-71.1, 22.59) * mm, "end": v(-71.04, 22.52) * mm});
            skLineSegment(sketch, "E3054", {"start": v(-71.04, 22.52) * mm, "end": v(-71, 22.44) * mm});
            skLineSegment(sketch, "E3055", {"start": v(-71, 22.44) * mm, "end": v(-70.94, 22.37) * mm});
            skLineSegment(sketch, "E3056", {"start": v(-70.94, 22.37) * mm, "end": v(-70.89, 22.3) * mm});
            skLineSegment(sketch, "E3057", {"start": v(-70.89, 22.3) * mm, "end": v(-70.84, 22.23) * mm});
            skLineSegment(sketch, "E3058", {"start": v(-70.84, 22.23) * mm, "end": v(-70.79, 22.16) * mm});
            skLineSegment(sketch, "E3059", {"start": v(-70.79, 22.16) * mm, "end": v(-70.74, 22.1) * mm});
            skLineSegment(sketch, "E3060", {"start": v(-70.74, 22.1) * mm, "end": v(-70.69, 22.03) * mm});
            skLineSegment(sketch, "E3061", {"start": v(-70.69, 22.03) * mm, "end": v(-70.64, 21.97) * mm});
            skLineSegment(sketch, "E3062", {"start": v(-70.64, 21.97) * mm, "end": v(-70.59, 21.9) * mm});
            skLineSegment(sketch, "E3063", {"start": v(-70.59, 21.9) * mm, "end": v(-70.54, 21.84) * mm});
            skLineSegment(sketch, "E3064", {"start": v(-70.54, 21.84) * mm, "end": v(-70.5, 21.78) * mm});
            skLineSegment(sketch, "E3065", {"start": v(-70.5, 21.78) * mm, "end": v(-70.44, 21.72) * mm});
            skLineSegment(sketch, "E3066", {"start": v(-70.44, 21.72) * mm, "end": v(-70.4, 21.66) * mm});
            skLineSegment(sketch, "E3067", {"start": v(-70.4, 21.66) * mm, "end": v(-70.35, 21.6) * mm});
            skLineSegment(sketch, "E3068", {"start": v(-70.35, 21.6) * mm, "end": v(-70.3, 21.55) * mm});
            skLineSegment(sketch, "E3069", {"start": v(-70.3, 21.55) * mm, "end": v(-70.26, 21.5) * mm});
            skLineSegment(sketch, "E3070", {"start": v(-70.26, 21.5) * mm, "end": v(-70.21, 21.44) * mm});
            skLineSegment(sketch, "E3071", {"start": v(-70.21, 21.44) * mm, "end": v(-70.17, 21.39) * mm});
            skLineSegment(sketch, "E3072", {"start": v(-70.17, 21.39) * mm, "end": v(-70.12, 21.34) * mm});
            skLineSegment(sketch, "E3073", {"start": v(-70.12, 21.34) * mm, "end": v(-70.08, 21.29) * mm});
            skLineSegment(sketch, "E3074", {"start": v(-70.08, 21.29) * mm, "end": v(-70.04, 21.24) * mm});
            skLineSegment(sketch, "E3075", {"start": v(-70.04, 21.24) * mm, "end": v(-70, 21.19) * mm});
            skLineSegment(sketch, "E3076", {"start": v(-70, 21.19) * mm, "end": v(-69.95, 21.14) * mm});
            skLineSegment(sketch, "E3077", {"start": v(-69.95, 21.14) * mm, "end": v(-69.91, 21.1) * mm});
            skLineSegment(sketch, "E3078", {"start": v(-69.91, 21.1) * mm, "end": v(-69.87, 21.05) * mm});
            skLineSegment(sketch, "E3079", {"start": v(-69.87, 21.05) * mm, "end": v(-69.83, 21) * mm});
            skLineSegment(sketch, "E3080", {"start": v(-69.83, 21) * mm, "end": v(-69.95, 20.8) * mm});
            skLineSegment(sketch, "E3081", {"start": v(-69.95, 20.8) * mm, "end": v(-70.39, 20.13) * mm});
            skLineSegment(sketch, "E3082", {"start": v(-70.39, 20.13) * mm, "end": v(-70.52, 19.93) * mm});
            skLineSegment(sketch, "E3083", {"start": v(-70.52, 19.93) * mm, "end": v(-70.57, 19.95) * mm});
            skLineSegment(sketch, "E3084", {"start": v(-70.57, 19.95) * mm, "end": v(-70.63, 19.97) * mm});
            skLineSegment(sketch, "E3085", {"start": v(-70.63, 19.97) * mm, "end": v(-70.7, 20) * mm});
            skLineSegment(sketch, "E3086", {"start": v(-70.7, 20) * mm, "end": v(-70.75, 20) * mm});
            skLineSegment(sketch, "E3087", {"start": v(-70.75, 20) * mm, "end": v(-70.81, 20.03) * mm});
            skLineSegment(sketch, "E3088", {"start": v(-70.81, 20.03) * mm, "end": v(-70.88, 20.05) * mm});
            skLineSegment(sketch, "E3089", {"start": v(-70.88, 20.05) * mm, "end": v(-70.94, 20.07) * mm});
            skLineSegment(sketch, "E3090", {"start": v(-70.94, 20.07) * mm, "end": v(-71, 20.08) * mm});
            skLineSegment(sketch, "E3091", {"start": v(-71, 20.08) * mm, "end": v(-71.07, 20.1) * mm});
            skLineSegment(sketch, "E3092", {"start": v(-71.07, 20.1) * mm, "end": v(-71.14, 20.12) * mm});
            skLineSegment(sketch, "E3093", {"start": v(-71.14, 20.12) * mm, "end": v(-71.2, 20.14) * mm});
            skLineSegment(sketch, "E3094", {"start": v(-71.2, 20.14) * mm, "end": v(-71.28, 20.16) * mm});
            skLineSegment(sketch, "E3095", {"start": v(-71.28, 20.16) * mm, "end": v(-71.35, 20.18) * mm});
            skLineSegment(sketch, "E3096", {"start": v(-71.35, 20.18) * mm, "end": v(-71.42, 20.2) * mm});
            skLineSegment(sketch, "E3097", {"start": v(-71.42, 20.2) * mm, "end": v(-71.5, 20.22) * mm});
            skLineSegment(sketch, "E3098", {"start": v(-71.5, 20.22) * mm, "end": v(-71.57, 20.23) * mm});
            skLineSegment(sketch, "E3099", {"start": v(-71.57, 20.23) * mm, "end": v(-71.65, 20.25) * mm});
            skLineSegment(sketch, "E3100", {"start": v(-71.65, 20.25) * mm, "end": v(-71.73, 20.27) * mm});
            skLineSegment(sketch, "E3101", {"start": v(-71.73, 20.27) * mm, "end": v(-71.8, 20.29) * mm});
            skLineSegment(sketch, "E3102", {"start": v(-71.8, 20.29) * mm, "end": v(-71.89, 20.3) * mm});
            skLineSegment(sketch, "E3103", {"start": v(-71.89, 20.3) * mm, "end": v(-71.97, 20.33) * mm});
            skLineSegment(sketch, "E3104", {"start": v(-71.97, 20.33) * mm, "end": v(-72.05, 20.34) * mm});
            skLineSegment(sketch, "E3105", {"start": v(-72.05, 20.34) * mm, "end": v(-72.13, 20.36) * mm});
            skLineSegment(sketch, "E3106", {"start": v(-72.13, 20.36) * mm, "end": v(-72.22, 20.38) * mm});
            skLineSegment(sketch, "E3107", {"start": v(-72.22, 20.38) * mm, "end": v(-72.3, 20.4) * mm});
            skLineSegment(sketch, "E3108", {"start": v(-72.3, 20.4) * mm, "end": v(-72.4, 20.41) * mm});
            skLineSegment(sketch, "E3109", {"start": v(-72.4, 20.41) * mm, "end": v(-72.48, 20.43) * mm});
            skLineSegment(sketch, "E3110", {"start": v(-72.48, 20.43) * mm, "end": v(-72.57, 20.45) * mm});
            skLineSegment(sketch, "E3111", {"start": v(-72.57, 20.45) * mm, "end": v(-72.67, 20.46) * mm});
            skLineSegment(sketch, "E3112", {"start": v(-72.67, 20.46) * mm, "end": v(-72.76, 20.48) * mm});
            skLineSegment(sketch, "E3113", {"start": v(-72.76, 20.48) * mm, "end": v(-72.85, 20.5) * mm});
            skLineSegment(sketch, "E3114", {"start": v(-72.85, 20.5) * mm, "end": v(-72.95, 20.51) * mm});
            skLineSegment(sketch, "E3115", {"start": v(-72.95, 20.51) * mm, "end": v(-73.05, 20.53) * mm});
            skLineSegment(sketch, "E3116", {"start": v(-73.05, 20.53) * mm, "end": v(-73.14, 20.54) * mm});
            skLineSegment(sketch, "E3117", {"start": v(-73.14, 20.54) * mm, "end": v(-73.24, 20.56) * mm});
            skLineSegment(sketch, "E3118", {"start": v(-73.24, 20.56) * mm, "end": v(-73.34, 20.57) * mm});
            skLineSegment(sketch, "E3119", {"start": v(-73.34, 20.57) * mm, "end": v(-73.45, 20.58) * mm});
            skLineSegment(sketch, "E3120", {"start": v(-73.45, 20.58) * mm, "end": v(-73.55, 20.6) * mm});
            skLineSegment(sketch, "E3121", {"start": v(-73.55, 20.6) * mm, "end": v(-73.65, 20.61) * mm});
            skLineSegment(sketch, "E3122", {"start": v(-73.65, 20.61) * mm, "end": v(-73.76, 20.62) * mm});
            skLineSegment(sketch, "E3123", {"start": v(-73.76, 20.62) * mm, "end": v(-73.8, 20.6) * mm});
            skLineSegment(sketch, "E3124", {"start": v(-73.8, 20.6) * mm, "end": v(-74.33, 19.7) * mm});
            skLineSegment(sketch, "E3125", {"start": v(-74.33, 19.7) * mm, "end": v(-74.32, 19.65) * mm});
            skLineSegment(sketch, "E3126", {"start": v(-74.32, 19.65) * mm, "end": v(-74.26, 19.56) * mm});
            skLineSegment(sketch, "E3127", {"start": v(-74.26, 19.56) * mm, "end": v(-74.2, 19.48) * mm});
            skLineSegment(sketch, "E3128", {"start": v(-74.2, 19.48) * mm, "end": v(-74.14, 19.4) * mm});
            skLineSegment(sketch, "E3129", {"start": v(-74.14, 19.4) * mm, "end": v(-74.07, 19.31) * mm});
            skLineSegment(sketch, "E3130", {"start": v(-74.07, 19.31) * mm, "end": v(-74.01, 19.23) * mm});
            skLineSegment(sketch, "E3131", {"start": v(-74.01, 19.23) * mm, "end": v(-73.95, 19.16) * mm});
            skLineSegment(sketch, "E3132", {"start": v(-73.95, 19.16) * mm, "end": v(-73.89, 19.08) * mm});
            skLineSegment(sketch, "E3133", {"start": v(-73.89, 19.08) * mm, "end": v(-73.83, 19) * mm});
            skLineSegment(sketch, "E3134", {"start": v(-73.83, 19) * mm, "end": v(-73.76, 18.93) * mm});
            skLineSegment(sketch, "E3135", {"start": v(-73.76, 18.93) * mm, "end": v(-73.7, 18.85) * mm});
            skLineSegment(sketch, "E3136", {"start": v(-73.7, 18.85) * mm, "end": v(-73.64, 18.78) * mm});
            skLineSegment(sketch, "E3137", {"start": v(-73.64, 18.78) * mm, "end": v(-73.58, 18.7) * mm});
            skLineSegment(sketch, "E3138", {"start": v(-73.58, 18.7) * mm, "end": v(-73.53, 18.64) * mm});
            skLineSegment(sketch, "E3139", {"start": v(-73.53, 18.64) * mm, "end": v(-73.47, 18.57) * mm});
            skLineSegment(sketch, "E3140", {"start": v(-73.47, 18.57) * mm, "end": v(-73.4, 18.5) * mm});
            skLineSegment(sketch, "E3141", {"start": v(-73.4, 18.5) * mm, "end": v(-73.35, 18.43) * mm});
            skLineSegment(sketch, "E3142", {"start": v(-73.35, 18.43) * mm, "end": v(-73.3, 18.37) * mm});
            skLineSegment(sketch, "E3143", {"start": v(-73.3, 18.37) * mm, "end": v(-73.24, 18.3) * mm});
            skLineSegment(sketch, "E3144", {"start": v(-73.24, 18.3) * mm, "end": v(-73.18, 18.24) * mm});
            skLineSegment(sketch, "E3145", {"start": v(-73.18, 18.24) * mm, "end": v(-73.12, 18.18) * mm});
            skLineSegment(sketch, "E3146", {"start": v(-73.12, 18.18) * mm, "end": v(-73.07, 18.12) * mm});
            skLineSegment(sketch, "E3147", {"start": v(-73.07, 18.12) * mm, "end": v(-73.01, 18.06) * mm});
            skLineSegment(sketch, "E3148", {"start": v(-73.01, 18.06) * mm, "end": v(-72.96, 18) * mm});
            skLineSegment(sketch, "E3149", {"start": v(-72.96, 18) * mm, "end": v(-72.9, 17.94) * mm});
            skLineSegment(sketch, "E3150", {"start": v(-72.9, 17.94) * mm, "end": v(-72.85, 17.89) * mm});
            skLineSegment(sketch, "E3151", {"start": v(-72.85, 17.89) * mm, "end": v(-72.8, 17.83) * mm});
            skLineSegment(sketch, "E3152", {"start": v(-72.8, 17.83) * mm, "end": v(-72.75, 17.78) * mm});
            skLineSegment(sketch, "E3153", {"start": v(-72.75, 17.78) * mm, "end": v(-72.7, 17.72) * mm});
            skLineSegment(sketch, "E3154", {"start": v(-72.7, 17.72) * mm, "end": v(-72.64, 17.67) * mm});
            skLineSegment(sketch, "E3155", {"start": v(-72.64, 17.67) * mm, "end": v(-72.6, 17.62) * mm});
            skLineSegment(sketch, "E3156", {"start": v(-72.6, 17.62) * mm, "end": v(-72.54, 17.57) * mm});
            skLineSegment(sketch, "E3157", {"start": v(-72.54, 17.57) * mm, "end": v(-72.5, 17.52) * mm});
            skLineSegment(sketch, "E3158", {"start": v(-72.5, 17.52) * mm, "end": v(-72.44, 17.48) * mm});
            skLineSegment(sketch, "E3159", {"start": v(-72.44, 17.48) * mm, "end": v(-72.4, 17.43) * mm});
            skLineSegment(sketch, "E3160", {"start": v(-72.4, 17.43) * mm, "end": v(-72.35, 17.38) * mm});
            skLineSegment(sketch, "E3161", {"start": v(-72.35, 17.38) * mm, "end": v(-72.3, 17.34) * mm});
            skLineSegment(sketch, "E3162", {"start": v(-72.3, 17.34) * mm, "end": v(-72.26, 17.3) * mm});
            skLineSegment(sketch, "E3163", {"start": v(-72.26, 17.3) * mm, "end": v(-72.21, 17.26) * mm});
            skLineSegment(sketch, "E3164", {"start": v(-72.21, 17.26) * mm, "end": v(-72.17, 17.21) * mm});
            skLineSegment(sketch, "E3165", {"start": v(-72.17, 17.21) * mm, "end": v(-72.12, 17.17) * mm});
            skLineSegment(sketch, "E3166", {"start": v(-72.12, 17.17) * mm, "end": v(-72.22, 16.96) * mm});
            skLineSegment(sketch, "E3167", {"start": v(-72.22, 16.96) * mm, "end": v(-72.6, 16.25) * mm});
            skLineSegment(sketch, "E3168", {"start": v(-72.6, 16.25) * mm, "end": v(-72.71, 16.05) * mm});
            skLineSegment(sketch, "E3169", {"start": v(-72.71, 16.05) * mm, "end": v(-72.77, 16.06) * mm});
            skLineSegment(sketch, "E3170", {"start": v(-72.77, 16.06) * mm, "end": v(-72.83, 16.07) * mm});
            skLineSegment(sketch, "E3171", {"start": v(-72.83, 16.07) * mm, "end": v(-72.89, 16.09) * mm});
            skLineSegment(sketch, "E3172", {"start": v(-72.89, 16.09) * mm, "end": v(-72.95, 16.1) * mm});
            skLineSegment(sketch, "E3173", {"start": v(-72.95, 16.1) * mm, "end": v(-73.01, 16.11) * mm});
            skLineSegment(sketch, "E3174", {"start": v(-73.01, 16.11) * mm, "end": v(-73.08, 16.12) * mm});
            skLineSegment(sketch, "E3175", {"start": v(-73.08, 16.12) * mm, "end": v(-73.14, 16.14) * mm});
            skLineSegment(sketch, "E3176", {"start": v(-73.14, 16.14) * mm, "end": v(-73.21, 16.15) * mm});
            skLineSegment(sketch, "E3177", {"start": v(-73.21, 16.15) * mm, "end": v(-73.28, 16.16) * mm});
            skLineSegment(sketch, "E3178", {"start": v(-73.28, 16.16) * mm, "end": v(-73.35, 16.18) * mm});
            skLineSegment(sketch, "E3179", {"start": v(-73.35, 16.18) * mm, "end": v(-73.42, 16.19) * mm});
            skLineSegment(sketch, "E3180", {"start": v(-73.42, 16.19) * mm, "end": v(-73.49, 16.2) * mm});
            skLineSegment(sketch, "E3181", {"start": v(-73.49, 16.2) * mm, "end": v(-73.56, 16.21) * mm});
            skLineSegment(sketch, "E3182", {"start": v(-73.56, 16.21) * mm, "end": v(-73.64, 16.23) * mm});
            skLineSegment(sketch, "E3183", {"start": v(-73.64, 16.23) * mm, "end": v(-73.71, 16.24) * mm});
            skLineSegment(sketch, "E3184", {"start": v(-73.71, 16.24) * mm, "end": v(-73.79, 16.25) * mm});
            skLineSegment(sketch, "E3185", {"start": v(-73.79, 16.25) * mm, "end": v(-73.87, 16.26) * mm});
            skLineSegment(sketch, "E3186", {"start": v(-73.87, 16.26) * mm, "end": v(-73.95, 16.27) * mm});
            skLineSegment(sketch, "E3187", {"start": v(-73.95, 16.27) * mm, "end": v(-74.03, 16.28) * mm});
            skLineSegment(sketch, "E3188", {"start": v(-74.03, 16.28) * mm, "end": v(-74.1, 16.3) * mm});
            skLineSegment(sketch, "E3189", {"start": v(-74.1, 16.3) * mm, "end": v(-74.2, 16.3) * mm});
            skLineSegment(sketch, "E3190", {"start": v(-74.2, 16.3) * mm, "end": v(-74.27, 16.31) * mm});
            skLineSegment(sketch, "E3191", {"start": v(-74.27, 16.31) * mm, "end": v(-74.36, 16.32) * mm});
            skLineSegment(sketch, "E3192", {"start": v(-74.36, 16.32) * mm, "end": v(-74.45, 16.33) * mm});
            skLineSegment(sketch, "E3193", {"start": v(-74.45, 16.33) * mm, "end": v(-74.53, 16.34) * mm});
            skLineSegment(sketch, "E3194", {"start": v(-74.53, 16.34) * mm, "end": v(-74.62, 16.35) * mm});
            skLineSegment(sketch, "E3195", {"start": v(-74.62, 16.35) * mm, "end": v(-74.71, 16.36) * mm});
            skLineSegment(sketch, "E3196", {"start": v(-74.71, 16.36) * mm, "end": v(-74.8, 16.37) * mm});
            skLineSegment(sketch, "E3197", {"start": v(-74.8, 16.37) * mm, "end": v(-74.9, 16.38) * mm});
            skLineSegment(sketch, "E3198", {"start": v(-74.9, 16.38) * mm, "end": v(-75, 16.39) * mm});
            skLineSegment(sketch, "E3199", {"start": v(-75, 16.39) * mm, "end": v(-75.09, 16.4) * mm});
            skLineSegment(sketch, "E3200", {"start": v(-75.09, 16.4) * mm, "end": v(-75.18, 16.4) * mm});
            skLineSegment(sketch, "E3201", {"start": v(-75.18, 16.4) * mm, "end": v(-75.28, 16.4) * mm});
            skLineSegment(sketch, "E3202", {"start": v(-75.28, 16.4) * mm, "end": v(-75.38, 16.41) * mm});
            skLineSegment(sketch, "E3203", {"start": v(-75.38, 16.41) * mm, "end": v(-75.48, 16.42) * mm});
            skLineSegment(sketch, "E3204", {"start": v(-75.48, 16.42) * mm, "end": v(-75.58, 16.42) * mm});
            skLineSegment(sketch, "E3205", {"start": v(-75.58, 16.42) * mm, "end": v(-75.69, 16.43) * mm});
            skLineSegment(sketch, "E3206", {"start": v(-75.69, 16.43) * mm, "end": v(-75.79, 16.43) * mm});
            skLineSegment(sketch, "E3207", {"start": v(-75.79, 16.43) * mm, "end": v(-75.9, 16.44) * mm});
            skLineSegment(sketch, "E3208", {"start": v(-75.9, 16.44) * mm, "end": v(-76, 16.44) * mm});
            skLineSegment(sketch, "E3209", {"start": v(-76, 16.44) * mm, "end": v(-76.04, 16.41) * mm});
            skLineSegment(sketch, "E3210", {"start": v(-76.04, 16.41) * mm, "end": v(-76.48, 15.47) * mm});
            skLineSegment(sketch, "E3211", {"start": v(-76.48, 15.47) * mm, "end": v(-76.48, 15.42) * mm});
            skLineSegment(sketch, "E3212", {"start": v(-76.48, 15.42) * mm, "end": v(-76.4, 15.34) * mm});
            skLineSegment(sketch, "E3213", {"start": v(-76.4, 15.34) * mm, "end": v(-76.34, 15.26) * mm});
            skLineSegment(sketch, "E3214", {"start": v(-76.34, 15.26) * mm, "end": v(-76.27, 15.18) * mm});
            skLineSegment(sketch, "E3215", {"start": v(-76.27, 15.18) * mm, "end": v(-76.2, 15.1) * mm});
            skLineSegment(sketch, "E3216", {"start": v(-76.2, 15.1) * mm, "end": v(-76.13, 15.03) * mm});
            skLineSegment(sketch, "E3217", {"start": v(-76.13, 15.03) * mm, "end": v(-76.06, 14.96) * mm});
            skLineSegment(sketch, "E3218", {"start": v(-76.06, 14.96) * mm, "end": v(-76, 14.89) * mm});
            skLineSegment(sketch, "E3219", {"start": v(-76, 14.89) * mm, "end": v(-75.92, 14.82) * mm});
            skLineSegment(sketch, "E3220", {"start": v(-75.92, 14.82) * mm, "end": v(-75.86, 14.75) * mm});
            skLineSegment(sketch, "E3221", {"start": v(-75.86, 14.75) * mm, "end": v(-75.79, 14.68) * mm});
            skLineSegment(sketch, "E3222", {"start": v(-75.79, 14.68) * mm, "end": v(-75.72, 14.61) * mm});
            skLineSegment(sketch, "E3223", {"start": v(-75.72, 14.61) * mm, "end": v(-75.66, 14.55) * mm});
            skLineSegment(sketch, "E3224", {"start": v(-75.66, 14.55) * mm, "end": v(-75.6, 14.48) * mm});
            skLineSegment(sketch, "E3225", {"start": v(-75.6, 14.48) * mm, "end": v(-75.53, 14.42) * mm});
            skLineSegment(sketch, "E3226", {"start": v(-75.53, 14.42) * mm, "end": v(-75.46, 14.36) * mm});
            skLineSegment(sketch, "E3227", {"start": v(-75.46, 14.36) * mm, "end": v(-75.4, 14.3) * mm});
            skLineSegment(sketch, "E3228", {"start": v(-75.4, 14.3) * mm, "end": v(-75.33, 14.24) * mm});
            skLineSegment(sketch, "E3229", {"start": v(-75.33, 14.24) * mm, "end": v(-75.27, 14.18) * mm});
            skLineSegment(sketch, "E3230", {"start": v(-75.27, 14.18) * mm, "end": v(-75.21, 14.12) * mm});
            skLineSegment(sketch, "E3231", {"start": v(-75.21, 14.12) * mm, "end": v(-75.15, 14.06) * mm});
            skLineSegment(sketch, "E3232", {"start": v(-75.15, 14.06) * mm, "end": v(-75.09, 14) * mm});
            skLineSegment(sketch, "E3233", {"start": v(-75.09, 14) * mm, "end": v(-75.03, 13.95) * mm});
            skLineSegment(sketch, "E3234", {"start": v(-75.03, 13.95) * mm, "end": v(-74.97, 13.9) * mm});
            skLineSegment(sketch, "E3235", {"start": v(-74.97, 13.9) * mm, "end": v(-74.91, 13.85) * mm});
            skLineSegment(sketch, "E3236", {"start": v(-74.91, 13.85) * mm, "end": v(-74.85, 13.8) * mm});
            skLineSegment(sketch, "E3237", {"start": v(-74.85, 13.8) * mm, "end": v(-74.8, 13.75) * mm});
            skLineSegment(sketch, "E3238", {"start": v(-74.8, 13.75) * mm, "end": v(-74.74, 13.7) * mm});
            skLineSegment(sketch, "E3239", {"start": v(-74.74, 13.7) * mm, "end": v(-74.68, 13.65) * mm});
            skLineSegment(sketch, "E3240", {"start": v(-74.68, 13.65) * mm, "end": v(-74.63, 13.6) * mm});
            skLineSegment(sketch, "E3241", {"start": v(-74.63, 13.6) * mm, "end": v(-74.57, 13.56) * mm});
            skLineSegment(sketch, "E3242", {"start": v(-74.57, 13.56) * mm, "end": v(-74.52, 13.51) * mm});
            skLineSegment(sketch, "E3243", {"start": v(-74.52, 13.51) * mm, "end": v(-74.46, 13.47) * mm});
            skLineSegment(sketch, "E3244", {"start": v(-74.46, 13.47) * mm, "end": v(-74.41, 13.42) * mm});
            skLineSegment(sketch, "E3245", {"start": v(-74.41, 13.42) * mm, "end": v(-74.36, 13.38) * mm});
            skLineSegment(sketch, "E3246", {"start": v(-74.36, 13.38) * mm, "end": v(-74.3, 13.34) * mm});
            skLineSegment(sketch, "E3247", {"start": v(-74.3, 13.34) * mm, "end": v(-74.26, 13.3) * mm});
            skLineSegment(sketch, "E3248", {"start": v(-74.26, 13.3) * mm, "end": v(-74.2, 13.26) * mm});
            skLineSegment(sketch, "E3249", {"start": v(-74.2, 13.26) * mm, "end": v(-74.16, 13.22) * mm});
            skLineSegment(sketch, "E3250", {"start": v(-74.16, 13.22) * mm, "end": v(-74.1, 13.19) * mm});
            skLineSegment(sketch, "E3251", {"start": v(-74.1, 13.19) * mm, "end": v(-74.06, 13.15) * mm});
            skLineSegment(sketch, "E3252", {"start": v(-74.06, 13.15) * mm, "end": v(-74.14, 12.93) * mm});
            skLineSegment(sketch, "E3253", {"start": v(-74.14, 12.93) * mm, "end": v(-74.45, 12.19) * mm});
            skLineSegment(sketch, "E3254", {"start": v(-74.45, 12.19) * mm, "end": v(-74.55, 11.97) * mm});
            skLineSegment(sketch, "E3255", {"start": v(-74.55, 11.97) * mm, "end": v(-74.6, 11.98) * mm});
            skLineSegment(sketch, "E3256", {"start": v(-74.6, 11.98) * mm, "end": v(-74.67, 12) * mm});
            skLineSegment(sketch, "E3257", {"start": v(-74.67, 12) * mm, "end": v(-74.73, 12) * mm});
            skLineSegment(sketch, "E3258", {"start": v(-74.73, 12) * mm, "end": v(-74.8, 12) * mm});
            skLineSegment(sketch, "E3259", {"start": v(-74.8, 12) * mm, "end": v(-74.86, 12.01) * mm});
            skLineSegment(sketch, "E3260", {"start": v(-74.86, 12.01) * mm, "end": v(-74.92, 12.02) * mm});
            skLineSegment(sketch, "E3261", {"start": v(-74.92, 12.02) * mm, "end": v(-74.99, 12.03) * mm});
            skLineSegment(sketch, "E3262", {"start": v(-74.99, 12.03) * mm, "end": v(-75.05, 12.04) * mm});
            skLineSegment(sketch, "E3263", {"start": v(-75.05, 12.04) * mm, "end": v(-75.12, 12.04) * mm});
            skLineSegment(sketch, "E3264", {"start": v(-75.12, 12.04) * mm, "end": v(-75.2, 12.05) * mm});
            skLineSegment(sketch, "E3265", {"start": v(-75.2, 12.05) * mm, "end": v(-75.26, 12.05) * mm});
            skLineSegment(sketch, "E3266", {"start": v(-75.26, 12.05) * mm, "end": v(-75.34, 12.06) * mm});
            skLineSegment(sketch, "E3267", {"start": v(-75.34, 12.06) * mm, "end": v(-75.41, 12.07) * mm});
            skLineSegment(sketch, "E3268", {"start": v(-75.41, 12.07) * mm, "end": v(-75.49, 12.07) * mm});
            skLineSegment(sketch, "E3269", {"start": v(-75.49, 12.07) * mm, "end": v(-75.56, 12.08) * mm});
            skLineSegment(sketch, "E3270", {"start": v(-75.56, 12.08) * mm, "end": v(-75.64, 12.08) * mm});
            skLineSegment(sketch, "E3271", {"start": v(-75.64, 12.08) * mm, "end": v(-75.72, 12.09) * mm});
            skLineSegment(sketch, "E3272", {"start": v(-75.72, 12.09) * mm, "end": v(-75.8, 12.09) * mm});
            skLineSegment(sketch, "E3273", {"start": v(-75.8, 12.09) * mm, "end": v(-75.88, 12.1) * mm});
            skLineSegment(sketch, "E3274", {"start": v(-75.88, 12.1) * mm, "end": v(-75.96, 12.1) * mm});
            skLineSegment(sketch, "E3275", {"start": v(-75.96, 12.1) * mm, "end": v(-76.04, 12.1) * mm});
            skLineSegment(sketch, "E3276", {"start": v(-76.04, 12.1) * mm, "end": v(-76.13, 12.1) * mm});
            skLineSegment(sketch, "E3277", {"start": v(-76.13, 12.1) * mm, "end": v(-76.22, 12.1) * mm});
            skLineSegment(sketch, "E3278", {"start": v(-76.22, 12.1) * mm, "end": v(-76.3, 12.1) * mm});
            skLineSegment(sketch, "E3279", {"start": v(-76.3, 12.1) * mm, "end": v(-76.4, 12.1) * mm});
            skLineSegment(sketch, "E3280", {"start": v(-76.4, 12.1) * mm, "end": v(-76.48, 12.1) * mm});
            skLineSegment(sketch, "E3281", {"start": v(-76.48, 12.1) * mm, "end": v(-76.57, 12.11) * mm});
            skLineSegment(sketch, "E3282", {"start": v(-76.57, 12.11) * mm, "end": v(-76.66, 12.11) * mm});
            skLineSegment(sketch, "E3283", {"start": v(-76.66, 12.11) * mm, "end": v(-76.76, 12.11) * mm});
            skLineSegment(sketch, "E3284", {"start": v(-76.76, 12.11) * mm, "end": v(-76.85, 12.1) * mm});
            skLineSegment(sketch, "E3285", {"start": v(-76.85, 12.1) * mm, "end": v(-76.95, 12.1) * mm});
            skLineSegment(sketch, "E3286", {"start": v(-76.95, 12.1) * mm, "end": v(-77.04, 12.1) * mm});
            skLineSegment(sketch, "E3287", {"start": v(-77.04, 12.1) * mm, "end": v(-77.14, 12.1) * mm});
            skLineSegment(sketch, "E3288", {"start": v(-77.14, 12.1) * mm, "end": v(-77.24, 12.1) * mm});
            skLineSegment(sketch, "E3289", {"start": v(-77.24, 12.1) * mm, "end": v(-77.34, 12.1) * mm});
            skLineSegment(sketch, "E3290", {"start": v(-77.34, 12.1) * mm, "end": v(-77.44, 12.1) * mm});
            skLineSegment(sketch, "E3291", {"start": v(-77.44, 12.1) * mm, "end": v(-77.54, 12.1) * mm});
            skLineSegment(sketch, "E3292", {"start": v(-77.54, 12.1) * mm, "end": v(-77.65, 12.09) * mm});
            skLineSegment(sketch, "E3293", {"start": v(-77.65, 12.09) * mm, "end": v(-77.75, 12.08) * mm});
            skLineSegment(sketch, "E3294", {"start": v(-77.75, 12.08) * mm, "end": v(-77.86, 12.07) * mm});
            skLineSegment(sketch, "E3295", {"start": v(-77.86, 12.07) * mm, "end": v(-77.9, 12.04) * mm});
            skLineSegment(sketch, "E3296", {"start": v(-77.9, 12.04) * mm, "end": v(-78.25, 11.06) * mm});
            skLineSegment(sketch, "E3297", {"start": v(-78.25, 11.06) * mm, "end": v(-78.24, 11.01) * mm});
            skLineSegment(sketch, "E3298", {"start": v(-78.24, 11.01) * mm, "end": v(-78.16, 10.94) * mm});
            skLineSegment(sketch, "E3299", {"start": v(-78.16, 10.94) * mm, "end": v(-78.09, 10.87) * mm});
            skLineSegment(sketch, "E3300", {"start": v(-78.09, 10.87) * mm, "end": v(-78.01, 10.8) * mm});
            skLineSegment(sketch, "E3301", {"start": v(-78.01, 10.8) * mm, "end": v(-77.93, 10.73) * mm});
            skLineSegment(sketch, "E3302", {"start": v(-77.93, 10.73) * mm, "end": v(-77.86, 10.66) * mm});
            skLineSegment(sketch, "E3303", {"start": v(-77.86, 10.66) * mm, "end": v(-77.78, 10.6) * mm});
            skLineSegment(sketch, "E3304", {"start": v(-77.78, 10.6) * mm, "end": v(-77.7, 10.53) * mm});
            skLineSegment(sketch, "E3305", {"start": v(-77.7, 10.53) * mm, "end": v(-77.64, 10.47) * mm});
            skLineSegment(sketch, "E3306", {"start": v(-77.64, 10.47) * mm, "end": v(-77.56, 10.4) * mm});
            skLineSegment(sketch, "E3307", {"start": v(-77.56, 10.4) * mm, "end": v(-77.49, 10.34) * mm});
            skLineSegment(sketch, "E3308", {"start": v(-77.49, 10.34) * mm, "end": v(-77.42, 10.28) * mm});
            skLineSegment(sketch, "E3309", {"start": v(-77.42, 10.28) * mm, "end": v(-77.35, 10.22) * mm});
            skLineSegment(sketch, "E3310", {"start": v(-77.35, 10.22) * mm, "end": v(-77.28, 10.16) * mm});
            skLineSegment(sketch, "E3311", {"start": v(-77.28, 10.16) * mm, "end": v(-77.2, 10.1) * mm});
            skLineSegment(sketch, "E3312", {"start": v(-77.2, 10.1) * mm, "end": v(-77.14, 10.05) * mm});
            skLineSegment(sketch, "E3313", {"start": v(-77.14, 10.05) * mm, "end": v(-77.07, 10) * mm});
            skLineSegment(sketch, "E3314", {"start": v(-77.07, 10) * mm, "end": v(-77, 9.94) * mm});
            skLineSegment(sketch, "E3315", {"start": v(-77, 9.94) * mm, "end": v(-76.93, 9.88) * mm});
            skLineSegment(sketch, "E3316", {"start": v(-76.93, 9.88) * mm, "end": v(-76.86, 9.83) * mm});
            skLineSegment(sketch, "E3317", {"start": v(-76.86, 9.83) * mm, "end": v(-76.8, 9.78) * mm});
            skLineSegment(sketch, "E3318", {"start": v(-76.8, 9.78) * mm, "end": v(-76.73, 9.73) * mm});
            skLineSegment(sketch, "E3319", {"start": v(-76.73, 9.73) * mm, "end": v(-76.67, 9.68) * mm});
            skLineSegment(sketch, "E3320", {"start": v(-76.67, 9.68) * mm, "end": v(-76.6, 9.63) * mm});
            skLineSegment(sketch, "E3321", {"start": v(-76.6, 9.63) * mm, "end": v(-76.54, 9.59) * mm});
            skLineSegment(sketch, "E3322", {"start": v(-76.54, 9.59) * mm, "end": v(-76.48, 9.54) * mm});
            skLineSegment(sketch, "E3323", {"start": v(-76.48, 9.54) * mm, "end": v(-76.42, 9.5) * mm});
            skLineSegment(sketch, "E3324", {"start": v(-76.42, 9.5) * mm, "end": v(-76.36, 9.45) * mm});
            skLineSegment(sketch, "E3325", {"start": v(-76.36, 9.45) * mm, "end": v(-76.3, 9.41) * mm});
            skLineSegment(sketch, "E3326", {"start": v(-76.3, 9.41) * mm, "end": v(-76.24, 9.37) * mm});
            skLineSegment(sketch, "E3327", {"start": v(-76.24, 9.37) * mm, "end": v(-76.18, 9.33) * mm});
            skLineSegment(sketch, "E3328", {"start": v(-76.18, 9.33) * mm, "end": v(-76.12, 9.29) * mm});
            skLineSegment(sketch, "E3329", {"start": v(-76.12, 9.29) * mm, "end": v(-76.06, 9.25) * mm});
            skLineSegment(sketch, "E3330", {"start": v(-76.06, 9.25) * mm, "end": v(-76, 9.21) * mm});
            skLineSegment(sketch, "E3331", {"start": v(-76, 9.21) * mm, "end": v(-75.95, 9.17) * mm});
            skLineSegment(sketch, "E3332", {"start": v(-75.95, 9.17) * mm, "end": v(-75.9, 9.14) * mm});
            skLineSegment(sketch, "E3333", {"start": v(-75.9, 9.14) * mm, "end": v(-75.84, 9.1) * mm});
            skLineSegment(sketch, "E3334", {"start": v(-75.84, 9.1) * mm, "end": v(-75.79, 9.07) * mm});
            skLineSegment(sketch, "E3335", {"start": v(-75.79, 9.07) * mm, "end": v(-75.74, 9.04) * mm});
            skLineSegment(sketch, "E3336", {"start": v(-75.74, 9.04) * mm, "end": v(-75.68, 9) * mm});
            skLineSegment(sketch, "E3337", {"start": v(-75.68, 9) * mm, "end": v(-75.63, 8.97) * mm});
            skLineSegment(sketch, "E3338", {"start": v(-75.63, 8.97) * mm, "end": v(-75.7, 8.75) * mm});
            skLineSegment(sketch, "E3339", {"start": v(-75.7, 8.75) * mm, "end": v(-75.94, 7.98) * mm});
            skLineSegment(sketch, "E3340", {"start": v(-75.94, 7.98) * mm, "end": v(-76.01, 7.76) * mm});
            skLineSegment(sketch, "E3341", {"start": v(-76.01, 7.76) * mm, "end": v(-76.07, 7.76) * mm});
            skLineSegment(sketch, "E3342", {"start": v(-76.07, 7.76) * mm, "end": v(-76.13, 7.76) * mm});
            skLineSegment(sketch, "E3343", {"start": v(-76.13, 7.76) * mm, "end": v(-76.2, 7.76) * mm});
            skLineSegment(sketch, "E3344", {"start": v(-76.2, 7.76) * mm, "end": v(-76.26, 7.77) * mm});
            skLineSegment(sketch, "E3345", {"start": v(-76.26, 7.77) * mm, "end": v(-76.32, 7.77) * mm});
            skLineSegment(sketch, "E3346", {"start": v(-76.32, 7.77) * mm, "end": v(-76.39, 7.77) * mm});
            skLineSegment(sketch, "E3347", {"start": v(-76.39, 7.77) * mm, "end": v(-76.45, 7.77) * mm});
            skLineSegment(sketch, "E3348", {"start": v(-76.45, 7.77) * mm, "end": v(-76.52, 7.77) * mm});
            skLineSegment(sketch, "E3349", {"start": v(-76.52, 7.77) * mm, "end": v(-76.6, 7.77) * mm});
            skLineSegment(sketch, "E3350", {"start": v(-76.6, 7.77) * mm, "end": v(-76.66, 7.77) * mm});
            skLineSegment(sketch, "E3351", {"start": v(-76.66, 7.77) * mm, "end": v(-76.73, 7.77) * mm});
            skLineSegment(sketch, "E3352", {"start": v(-76.73, 7.77) * mm, "end": v(-76.8, 7.77) * mm});
            skLineSegment(sketch, "E3353", {"start": v(-76.8, 7.77) * mm, "end": v(-76.88, 7.77) * mm});
            skLineSegment(sketch, "E3354", {"start": v(-76.88, 7.77) * mm, "end": v(-76.95, 7.77) * mm});
            skLineSegment(sketch, "E3355", {"start": v(-76.95, 7.77) * mm, "end": v(-77.03, 7.77) * mm});
            skLineSegment(sketch, "E3356", {"start": v(-77.03, 7.77) * mm, "end": v(-77.1, 7.76) * mm});
            skLineSegment(sketch, "E3357", {"start": v(-77.1, 7.76) * mm, "end": v(-77.19, 7.76) * mm});
            skLineSegment(sketch, "E3358", {"start": v(-77.19, 7.76) * mm, "end": v(-77.27, 7.76) * mm});
            skLineSegment(sketch, "E3359", {"start": v(-77.27, 7.76) * mm, "end": v(-77.35, 7.76) * mm});
            skLineSegment(sketch, "E3360", {"start": v(-77.35, 7.76) * mm, "end": v(-77.43, 7.75) * mm});
            skLineSegment(sketch, "E3361", {"start": v(-77.43, 7.75) * mm, "end": v(-77.51, 7.75) * mm});
            skLineSegment(sketch, "E3362", {"start": v(-77.51, 7.75) * mm, "end": v(-77.6, 7.74) * mm});
            skLineSegment(sketch, "E3363", {"start": v(-77.6, 7.74) * mm, "end": v(-77.68, 7.74) * mm});
            skLineSegment(sketch, "E3364", {"start": v(-77.68, 7.74) * mm, "end": v(-77.77, 7.73) * mm});
            skLineSegment(sketch, "E3365", {"start": v(-77.77, 7.73) * mm, "end": v(-77.86, 7.72) * mm});
            skLineSegment(sketch, "E3366", {"start": v(-77.86, 7.72) * mm, "end": v(-77.95, 7.72) * mm});
            skLineSegment(sketch, "E3367", {"start": v(-77.95, 7.72) * mm, "end": v(-78.04, 7.71) * mm});
            skLineSegment(sketch, "E3368", {"start": v(-78.04, 7.71) * mm, "end": v(-78.13, 7.7) * mm});
            skLineSegment(sketch, "E3369", {"start": v(-78.13, 7.7) * mm, "end": v(-78.22, 7.7) * mm});
            skLineSegment(sketch, "E3370", {"start": v(-78.22, 7.7) * mm, "end": v(-78.32, 7.68) * mm});
            skLineSegment(sketch, "E3371", {"start": v(-78.32, 7.68) * mm, "end": v(-78.41, 7.67) * mm});
            skLineSegment(sketch, "E3372", {"start": v(-78.41, 7.67) * mm, "end": v(-78.5, 7.66) * mm});
            skLineSegment(sketch, "E3373", {"start": v(-78.5, 7.66) * mm, "end": v(-78.6, 7.65) * mm});
            skLineSegment(sketch, "E3374", {"start": v(-78.6, 7.65) * mm, "end": v(-78.7, 7.64) * mm});
            skLineSegment(sketch, "E3375", {"start": v(-78.7, 7.64) * mm, "end": v(-78.8, 7.63) * mm});
            skLineSegment(sketch, "E3376", {"start": v(-78.8, 7.63) * mm, "end": v(-78.9, 7.62) * mm});
            skLineSegment(sketch, "E3377", {"start": v(-78.9, 7.62) * mm, "end": v(-79, 7.6) * mm});
            skLineSegment(sketch, "E3378", {"start": v(-79, 7.6) * mm, "end": v(-79.1, 7.59) * mm});
            skLineSegment(sketch, "E3379", {"start": v(-79.1, 7.59) * mm, "end": v(-79.21, 7.57) * mm});
            skLineSegment(sketch, "E3380", {"start": v(-79.21, 7.57) * mm, "end": v(-79.32, 7.56) * mm});
            skLineSegment(sketch, "E3381", {"start": v(-79.32, 7.56) * mm, "end": v(-79.35, 7.52) * mm});
            skLineSegment(sketch, "E3382", {"start": v(-79.35, 7.52) * mm, "end": v(-79.62, 6.52) * mm});
            skLineSegment(sketch, "E3383", {"start": v(-79.62, 6.52) * mm, "end": v(-79.6, 6.47) * mm});
            skLineSegment(sketch, "E3384", {"start": v(-79.6, 6.47) * mm, "end": v(-79.52, 6.4) * mm});
            skLineSegment(sketch, "E3385", {"start": v(-79.52, 6.4) * mm, "end": v(-79.44, 6.34) * mm});
            skLineSegment(sketch, "E3386", {"start": v(-79.44, 6.34) * mm, "end": v(-79.36, 6.27) * mm});
            skLineSegment(sketch, "E3387", {"start": v(-79.36, 6.27) * mm, "end": v(-79.27, 6.21) * mm});
            skLineSegment(sketch, "E3388", {"start": v(-79.27, 6.21) * mm, "end": v(-79.2, 6.15) * mm});
            skLineSegment(sketch, "E3389", {"start": v(-79.2, 6.15) * mm, "end": v(-79.11, 6.1) * mm});
            skLineSegment(sketch, "E3390", {"start": v(-79.11, 6.1) * mm, "end": v(-79.03, 6.03) * mm});
            skLineSegment(sketch, "E3391", {"start": v(-79.03, 6.03) * mm, "end": v(-78.95, 5.98) * mm});
            skLineSegment(sketch, "E3392", {"start": v(-78.95, 5.98) * mm, "end": v(-78.87, 5.92) * mm});
            skLineSegment(sketch, "E3393", {"start": v(-78.87, 5.92) * mm, "end": v(-78.8, 5.86) * mm});
            skLineSegment(sketch, "E3394", {"start": v(-78.8, 5.86) * mm, "end": v(-78.72, 5.81) * mm});
            skLineSegment(sketch, "E3395", {"start": v(-78.72, 5.81) * mm, "end": v(-78.64, 5.76) * mm});
            skLineSegment(sketch, "E3396", {"start": v(-78.64, 5.76) * mm, "end": v(-78.57, 5.7) * mm});
            skLineSegment(sketch, "E3397", {"start": v(-78.57, 5.7) * mm, "end": v(-78.5, 5.65) * mm});
            skLineSegment(sketch, "E3398", {"start": v(-78.5, 5.65) * mm, "end": v(-78.42, 5.6) * mm});
            skLineSegment(sketch, "E3399", {"start": v(-78.42, 5.6) * mm, "end": v(-78.34, 5.56) * mm});
            skLineSegment(sketch, "E3400", {"start": v(-78.34, 5.56) * mm, "end": v(-78.27, 5.5) * mm});
            skLineSegment(sketch, "E3401", {"start": v(-78.27, 5.5) * mm, "end": v(-78.2, 5.46) * mm});
            skLineSegment(sketch, "E3402", {"start": v(-78.2, 5.46) * mm, "end": v(-78.13, 5.41) * mm});
            skLineSegment(sketch, "E3403", {"start": v(-78.13, 5.41) * mm, "end": v(-78.06, 5.37) * mm});
            skLineSegment(sketch, "E3404", {"start": v(-78.06, 5.37) * mm, "end": v(-77.99, 5.33) * mm});
            skLineSegment(sketch, "E3405", {"start": v(-77.99, 5.33) * mm, "end": v(-77.92, 5.28) * mm});
            skLineSegment(sketch, "E3406", {"start": v(-77.92, 5.28) * mm, "end": v(-77.85, 5.24) * mm});
            skLineSegment(sketch, "E3407", {"start": v(-77.85, 5.24) * mm, "end": v(-77.78, 5.2) * mm});
            skLineSegment(sketch, "E3408", {"start": v(-77.78, 5.2) * mm, "end": v(-77.72, 5.16) * mm});
            skLineSegment(sketch, "E3409", {"start": v(-77.72, 5.16) * mm, "end": v(-77.65, 5.12) * mm});
            skLineSegment(sketch, "E3410", {"start": v(-77.65, 5.12) * mm, "end": v(-77.59, 5.08) * mm});
            skLineSegment(sketch, "E3411", {"start": v(-77.59, 5.08) * mm, "end": v(-77.52, 5.05) * mm});
            skLineSegment(sketch, "E3412", {"start": v(-77.52, 5.05) * mm, "end": v(-77.46, 5) * mm});
            skLineSegment(sketch, "E3413", {"start": v(-77.46, 5) * mm, "end": v(-77.4, 4.97) * mm});
            skLineSegment(sketch, "E3414", {"start": v(-77.4, 4.97) * mm, "end": v(-77.34, 4.94) * mm});
            skLineSegment(sketch, "E3415", {"start": v(-77.34, 4.94) * mm, "end": v(-77.27, 4.9) * mm});
            skLineSegment(sketch, "E3416", {"start": v(-77.27, 4.9) * mm, "end": v(-77.22, 4.87) * mm});
            skLineSegment(sketch, "E3417", {"start": v(-77.22, 4.87) * mm, "end": v(-77.16, 4.84) * mm});
            skLineSegment(sketch, "E3418", {"start": v(-77.16, 4.84) * mm, "end": v(-77.1, 4.81) * mm});
            skLineSegment(sketch, "E3419", {"start": v(-77.1, 4.81) * mm, "end": v(-77.04, 4.78) * mm});
            skLineSegment(sketch, "E3420", {"start": v(-77.04, 4.78) * mm, "end": v(-76.99, 4.75) * mm});
            skLineSegment(sketch, "E3421", {"start": v(-76.99, 4.75) * mm, "end": v(-76.93, 4.72) * mm});
            skLineSegment(sketch, "E3422", {"start": v(-76.93, 4.72) * mm, "end": v(-76.88, 4.7) * mm});
            skLineSegment(sketch, "E3423", {"start": v(-76.88, 4.7) * mm, "end": v(-76.82, 4.67) * mm});
            skLineSegment(sketch, "E3424", {"start": v(-76.82, 4.67) * mm, "end": v(-76.87, 4.44) * mm});
            skLineSegment(sketch, "E3425", {"start": v(-76.87, 4.44) * mm, "end": v(-77.04, 3.65) * mm});
            skLineSegment(sketch, "E3426", {"start": v(-77.04, 3.65) * mm, "end": v(-77.1, 3.42) * mm});
            skLineSegment(sketch, "E3427", {"start": v(-77.1, 3.42) * mm, "end": v(-77.15, 3.42) * mm});
            skLineSegment(sketch, "E3428", {"start": v(-77.15, 3.42) * mm, "end": v(-77.21, 3.42) * mm});
            skLineSegment(sketch, "E3429", {"start": v(-77.21, 3.42) * mm, "end": v(-77.27, 3.41) * mm});
            skLineSegment(sketch, "E3430", {"start": v(-77.27, 3.41) * mm, "end": v(-77.34, 3.41) * mm});
            skLineSegment(sketch, "E3431", {"start": v(-77.34, 3.41) * mm, "end": v(-77.4, 3.4) * mm});
            skLineSegment(sketch, "E3432", {"start": v(-77.4, 3.4) * mm, "end": v(-77.47, 3.4) * mm});
            skLineSegment(sketch, "E3433", {"start": v(-77.47, 3.4) * mm, "end": v(-77.53, 3.4) * mm});
            skLineSegment(sketch, "E3434", {"start": v(-77.53, 3.4) * mm, "end": v(-77.6, 3.4) * mm});
            skLineSegment(sketch, "E3435", {"start": v(-77.6, 3.4) * mm, "end": v(-77.67, 3.39) * mm});
            skLineSegment(sketch, "E3436", {"start": v(-77.67, 3.39) * mm, "end": v(-77.74, 3.38) * mm});
            skLineSegment(sketch, "E3437", {"start": v(-77.74, 3.38) * mm, "end": v(-77.81, 3.37) * mm});
            skLineSegment(sketch, "E3438", {"start": v(-77.81, 3.37) * mm, "end": v(-77.88, 3.37) * mm});
            skLineSegment(sketch, "E3439", {"start": v(-77.88, 3.37) * mm, "end": v(-77.96, 3.36) * mm});
            skLineSegment(sketch, "E3440", {"start": v(-77.96, 3.36) * mm, "end": v(-78.03, 3.35) * mm});
            skLineSegment(sketch, "E3441", {"start": v(-78.03, 3.35) * mm, "end": v(-78.1, 3.34) * mm});
            skLineSegment(sketch, "E3442", {"start": v(-78.1, 3.34) * mm, "end": v(-78.18, 3.33) * mm});
            skLineSegment(sketch, "E3443", {"start": v(-78.18, 3.33) * mm, "end": v(-78.26, 3.32) * mm});
            skLineSegment(sketch, "E3444", {"start": v(-78.26, 3.32) * mm, "end": v(-78.34, 3.31) * mm});
            skLineSegment(sketch, "E3445", {"start": v(-78.34, 3.31) * mm, "end": v(-78.42, 3.3) * mm});
            skLineSegment(sketch, "E3446", {"start": v(-78.42, 3.3) * mm, "end": v(-78.5, 3.3) * mm});
            skLineSegment(sketch, "E3447", {"start": v(-78.5, 3.3) * mm, "end": v(-78.59, 3.28) * mm});
            skLineSegment(sketch, "E3448", {"start": v(-78.59, 3.28) * mm, "end": v(-78.67, 3.27) * mm});
            skLineSegment(sketch, "E3449", {"start": v(-78.67, 3.27) * mm, "end": v(-78.76, 3.25) * mm});
            skLineSegment(sketch, "E3450", {"start": v(-78.76, 3.25) * mm, "end": v(-78.84, 3.24) * mm});
            skLineSegment(sketch, "E3451", {"start": v(-78.84, 3.24) * mm, "end": v(-78.93, 3.23) * mm});
            skLineSegment(sketch, "E3452", {"start": v(-78.93, 3.23) * mm, "end": v(-79.02, 3.21) * mm});
            skLineSegment(sketch, "E3453", {"start": v(-79.02, 3.21) * mm, "end": v(-79.1, 3.2) * mm});
            skLineSegment(sketch, "E3454", {"start": v(-79.1, 3.2) * mm, "end": v(-79.2, 3.18) * mm});
            skLineSegment(sketch, "E3455", {"start": v(-79.2, 3.18) * mm, "end": v(-79.29, 3.16) * mm});
            skLineSegment(sketch, "E3456", {"start": v(-79.29, 3.16) * mm, "end": v(-79.38, 3.14) * mm});
            skLineSegment(sketch, "E3457", {"start": v(-79.38, 3.14) * mm, "end": v(-79.48, 3.13) * mm});
            skLineSegment(sketch, "E3458", {"start": v(-79.48, 3.13) * mm, "end": v(-79.57, 3.1) * mm});
            skLineSegment(sketch, "E3459", {"start": v(-79.57, 3.1) * mm, "end": v(-79.67, 3.09) * mm});
            skLineSegment(sketch, "E3460", {"start": v(-79.67, 3.09) * mm, "end": v(-79.76, 3.07) * mm});
            skLineSegment(sketch, "E3461", {"start": v(-79.76, 3.07) * mm, "end": v(-79.86, 3.05) * mm});
            skLineSegment(sketch, "E3462", {"start": v(-79.86, 3.05) * mm, "end": v(-79.96, 3.02) * mm});
            skLineSegment(sketch, "E3463", {"start": v(-79.96, 3.02) * mm, "end": v(-80.06, 3) * mm});
            skLineSegment(sketch, "E3464", {"start": v(-80.06, 3) * mm, "end": v(-80.16, 2.98) * mm});
            skLineSegment(sketch, "E3465", {"start": v(-80.16, 2.98) * mm, "end": v(-80.26, 2.95) * mm});
            skLineSegment(sketch, "E3466", {"start": v(-80.26, 2.95) * mm, "end": v(-80.37, 2.93) * mm});
            skLineSegment(sketch, "E3467", {"start": v(-80.37, 2.93) * mm, "end": v(-80.4, 2.9) * mm});
            skLineSegment(sketch, "E3468", {"start": v(-80.4, 2.9) * mm, "end": v(-80.57, 1.86) * mm});
            skLineSegment(sketch, "E3469", {"start": v(-80.57, 1.86) * mm, "end": v(-80.56, 1.82) * mm});
            skLineSegment(sketch, "E3470", {"start": v(-80.56, 1.82) * mm, "end": v(-80.47, 1.76) * mm});
            skLineSegment(sketch, "E3471", {"start": v(-80.47, 1.76) * mm, "end": v(-80.38, 1.7) * mm});
            skLineSegment(sketch, "E3472", {"start": v(-80.38, 1.7) * mm, "end": v(-80.29, 1.65) * mm});
            skLineSegment(sketch, "E3473", {"start": v(-80.29, 1.65) * mm, "end": v(-80.2, 1.6) * mm});
            skLineSegment(sketch, "E3474", {"start": v(-80.2, 1.6) * mm, "end": v(-80.12, 1.54) * mm});
            skLineSegment(sketch, "E3475", {"start": v(-80.12, 1.54) * mm, "end": v(-80.03, 1.49) * mm});
            skLineSegment(sketch, "E3476", {"start": v(-80.03, 1.49) * mm, "end": v(-79.94, 1.44) * mm});
            skLineSegment(sketch, "E3477", {"start": v(-79.94, 1.44) * mm, "end": v(-79.86, 1.39) * mm});
            skLineSegment(sketch, "E3478", {"start": v(-79.86, 1.39) * mm, "end": v(-79.78, 1.34) * mm});
            skLineSegment(sketch, "E3479", {"start": v(-79.78, 1.34) * mm, "end": v(-79.7, 1.29) * mm});
            skLineSegment(sketch, "E3480", {"start": v(-79.7, 1.29) * mm, "end": v(-79.61, 1.24) * mm});
            skLineSegment(sketch, "E3481", {"start": v(-79.61, 1.24) * mm, "end": v(-79.53, 1.2) * mm});
            skLineSegment(sketch, "E3482", {"start": v(-79.53, 1.2) * mm, "end": v(-79.45, 1.15) * mm});
            skLineSegment(sketch, "E3483", {"start": v(-79.45, 1.15) * mm, "end": v(-79.37, 1.1) * mm});
            skLineSegment(sketch, "E3484", {"start": v(-79.37, 1.1) * mm, "end": v(-79.3, 1.06) * mm});
            skLineSegment(sketch, "E3485", {"start": v(-79.3, 1.06) * mm, "end": v(-79.22, 1.02) * mm});
            skLineSegment(sketch, "E3486", {"start": v(-79.22, 1.02) * mm, "end": v(-79.14, 0.98) * mm});
            skLineSegment(sketch, "E3487", {"start": v(-79.14, 0.98) * mm, "end": v(-79.06, 0.94) * mm});
            skLineSegment(sketch, "E3488", {"start": v(-79.06, 0.94) * mm, "end": v(-78.99, 0.9) * mm});
            skLineSegment(sketch, "E3489", {"start": v(-78.99, 0.9) * mm, "end": v(-78.91, 0.86) * mm});
            skLineSegment(sketch, "E3490", {"start": v(-78.91, 0.86) * mm, "end": v(-78.84, 0.83) * mm});
            skLineSegment(sketch, "E3491", {"start": v(-78.84, 0.83) * mm, "end": v(-78.77, 0.79) * mm});
            skLineSegment(sketch, "E3492", {"start": v(-78.77, 0.79) * mm, "end": v(-78.7, 0.75) * mm});
            skLineSegment(sketch, "E3493", {"start": v(-78.7, 0.75) * mm, "end": v(-78.63, 0.72) * mm});
            skLineSegment(sketch, "E3494", {"start": v(-78.63, 0.72) * mm, "end": v(-78.56, 0.68) * mm});
            skLineSegment(sketch, "E3495", {"start": v(-78.56, 0.68) * mm, "end": v(-78.49, 0.65) * mm});
            skLineSegment(sketch, "E3496", {"start": v(-78.49, 0.65) * mm, "end": v(-78.42, 0.62) * mm});
            skLineSegment(sketch, "E3497", {"start": v(-78.42, 0.62) * mm, "end": v(-78.35, 0.59) * mm});
            skLineSegment(sketch, "E3498", {"start": v(-78.35, 0.59) * mm, "end": v(-78.29, 0.56) * mm});
            skLineSegment(sketch, "E3499", {"start": v(-78.29, 0.56) * mm, "end": v(-78.22, 0.53) * mm});
            skLineSegment(sketch, "E3500", {"start": v(-78.22, 0.53) * mm, "end": v(-78.16, 0.5) * mm});
            skLineSegment(sketch, "E3501", {"start": v(-78.16, 0.5) * mm, "end": v(-78.1, 0.47) * mm});
            skLineSegment(sketch, "E3502", {"start": v(-78.1, 0.47) * mm, "end": v(-78.03, 0.44) * mm});
            skLineSegment(sketch, "E3503", {"start": v(-78.03, 0.44) * mm, "end": v(-77.97, 0.42) * mm});
            skLineSegment(sketch, "E3504", {"start": v(-77.97, 0.42) * mm, "end": v(-77.91, 0.4) * mm});
            skLineSegment(sketch, "E3505", {"start": v(-77.91, 0.4) * mm, "end": v(-77.85, 0.37) * mm});
            skLineSegment(sketch, "E3506", {"start": v(-77.85, 0.37) * mm, "end": v(-77.8, 0.34) * mm});
            skLineSegment(sketch, "E3507", {"start": v(-77.8, 0.34) * mm, "end": v(-77.74, 0.32) * mm});
            skLineSegment(sketch, "E3508", {"start": v(-77.74, 0.32) * mm, "end": v(-77.68, 0.3) * mm});
            skLineSegment(sketch, "E3509", {"start": v(-77.68, 0.3) * mm, "end": v(-77.62, 0.28) * mm});
            skLineSegment(sketch, "E3510", {"start": v(-77.62, 0.28) * mm, "end": v(-77.64, 0.04) * mm});
            skLineSegment(sketch, "E3511", {"start": v(-77.64, 0.04) * mm, "end": v(-77.74, -0.76) * mm});
            skLineSegment(sketch, "E3512", {"start": v(-77.74, -0.76) * mm, "end": v(-77.78, -0.99) * mm});
            skLineSegment(sketch, "E3513", {"start": v(-77.78, -0.99) * mm, "end": v(-77.84, -1) * mm});
            skLineSegment(sketch, "E3514", {"start": v(-77.84, -1) * mm, "end": v(-77.9, -1) * mm});
            skLineSegment(sketch, "E3515", {"start": v(-77.9, -1) * mm, "end": v(-77.96, -1.01) * mm});
            skLineSegment(sketch, "E3516", {"start": v(-77.96, -1.01) * mm, "end": v(-78.02, -1.02) * mm});
            skLineSegment(sketch, "E3517", {"start": v(-78.02, -1.02) * mm, "end": v(-78.09, -1.03) * mm});
            skLineSegment(sketch, "E3518", {"start": v(-78.09, -1.03) * mm, "end": v(-78.15, -1.04) * mm});
            skLineSegment(sketch, "E3519", {"start": v(-78.15, -1.04) * mm, "end": v(-78.22, -1.05) * mm});
            skLineSegment(sketch, "E3520", {"start": v(-78.22, -1.05) * mm, "end": v(-78.28, -1.07) * mm});
            skLineSegment(sketch, "E3521", {"start": v(-78.28, -1.07) * mm, "end": v(-78.35, -1.08) * mm});
            skLineSegment(sketch, "E3522", {"start": v(-78.35, -1.08) * mm, "end": v(-78.42, -1.09) * mm});
            skLineSegment(sketch, "E3523", {"start": v(-78.42, -1.09) * mm, "end": v(-78.5, -1.1) * mm});
            skLineSegment(sketch, "E3524", {"start": v(-78.5, -1.1) * mm, "end": v(-78.56, -1.12) * mm});
            skLineSegment(sketch, "E3525", {"start": v(-78.56, -1.12) * mm, "end": v(-78.63, -1.13) * mm});
            skLineSegment(sketch, "E3526", {"start": v(-78.63, -1.13) * mm, "end": v(-78.7, -1.15) * mm});
            skLineSegment(sketch, "E3527", {"start": v(-78.7, -1.15) * mm, "end": v(-78.78, -1.16) * mm});
            skLineSegment(sketch, "E3528", {"start": v(-78.78, -1.16) * mm, "end": v(-78.86, -1.18) * mm});
            skLineSegment(sketch, "E3529", {"start": v(-78.86, -1.18) * mm, "end": v(-78.94, -1.2) * mm});
            skLineSegment(sketch, "E3530", {"start": v(-78.94, -1.2) * mm, "end": v(-79.01, -1.21) * mm});
            skLineSegment(sketch, "E3531", {"start": v(-79.01, -1.21) * mm, "end": v(-79.1, -1.23) * mm});
            skLineSegment(sketch, "E3532", {"start": v(-79.1, -1.23) * mm, "end": v(-79.17, -1.25) * mm});
            skLineSegment(sketch, "E3533", {"start": v(-79.17, -1.25) * mm, "end": v(-79.26, -1.27) * mm});
            skLineSegment(sketch, "E3534", {"start": v(-79.26, -1.27) * mm, "end": v(-79.34, -1.29) * mm});
            skLineSegment(sketch, "E3535", {"start": v(-79.34, -1.29) * mm, "end": v(-79.42, -1.3) * mm});
            skLineSegment(sketch, "E3536", {"start": v(-79.42, -1.3) * mm, "end": v(-79.5, -1.33) * mm});
            skLineSegment(sketch, "E3537", {"start": v(-79.5, -1.33) * mm, "end": v(-79.6, -1.35) * mm});
            skLineSegment(sketch, "E3538", {"start": v(-79.6, -1.35) * mm, "end": v(-79.68, -1.37) * mm});
            skLineSegment(sketch, "E3539", {"start": v(-79.68, -1.37) * mm, "end": v(-79.77, -1.4) * mm});
            skLineSegment(sketch, "E3540", {"start": v(-79.77, -1.4) * mm, "end": v(-79.85, -1.42) * mm});
            skLineSegment(sketch, "E3541", {"start": v(-79.85, -1.42) * mm, "end": v(-79.94, -1.45) * mm});
            skLineSegment(sketch, "E3542", {"start": v(-79.94, -1.45) * mm, "end": v(-80.03, -1.47) * mm});
            skLineSegment(sketch, "E3543", {"start": v(-80.03, -1.47) * mm, "end": v(-80.13, -1.5) * mm});
            skLineSegment(sketch, "E3544", {"start": v(-80.13, -1.5) * mm, "end": v(-80.22, -1.53) * mm});
            skLineSegment(sketch, "E3545", {"start": v(-80.22, -1.53) * mm, "end": v(-80.31, -1.55) * mm});
            skLineSegment(sketch, "E3546", {"start": v(-80.31, -1.55) * mm, "end": v(-80.4, -1.58) * mm});
            skLineSegment(sketch, "E3547", {"start": v(-80.4, -1.58) * mm, "end": v(-80.5, -1.61) * mm});
            skLineSegment(sketch, "E3548", {"start": v(-80.5, -1.61) * mm, "end": v(-80.6, -1.64) * mm});
            skLineSegment(sketch, "E3549", {"start": v(-80.6, -1.64) * mm, "end": v(-80.7, -1.67) * mm});
            skLineSegment(sketch, "E3550", {"start": v(-80.7, -1.67) * mm, "end": v(-80.8, -1.7) * mm});
            skLineSegment(sketch, "E3551", {"start": v(-80.8, -1.7) * mm, "end": v(-80.9, -1.74) * mm});
            skLineSegment(sketch, "E3552", {"start": v(-80.9, -1.74) * mm, "end": v(-81, -1.77) * mm});
            skLineSegment(sketch, "E3553", {"start": v(-81, -1.77) * mm, "end": v(-81.03, -1.82) * mm});
            skLineSegment(sketch, "E3554", {"start": v(-81.03, -1.82) * mm, "end": v(-81.1, -2.85) * mm});
            skLineSegment(sketch, "E3555", {"start": v(-81.1, -2.85) * mm, "end": v(-81.08, -2.9) * mm});
            skLineSegment(sketch, "E3556", {"start": v(-81.08, -2.9) * mm, "end": v(-81, -2.95) * mm});
            skLineSegment(sketch, "E3557", {"start": v(-81, -2.95) * mm, "end": v(-80.9, -3) * mm});
            skLineSegment(sketch, "E3558", {"start": v(-80.9, -3) * mm, "end": v(-80.8, -3.04) * mm});
            skLineSegment(sketch, "E3559", {"start": v(-80.8, -3.04) * mm, "end": v(-80.71, -3.1) * mm});
            skLineSegment(sketch, "E3560", {"start": v(-80.71, -3.1) * mm, "end": v(-80.62, -3.14) * mm});
            skLineSegment(sketch, "E3561", {"start": v(-80.62, -3.14) * mm, "end": v(-80.53, -3.18) * mm});
            skLineSegment(sketch, "E3562", {"start": v(-80.53, -3.18) * mm, "end": v(-80.44, -3.22) * mm});
            skLineSegment(sketch, "E3563", {"start": v(-80.44, -3.22) * mm, "end": v(-80.35, -3.27) * mm});
            skLineSegment(sketch, "E3564", {"start": v(-80.35, -3.27) * mm, "end": v(-80.27, -3.3) * mm});
            skLineSegment(sketch, "E3565", {"start": v(-80.27, -3.3) * mm, "end": v(-80.18, -3.35) * mm});
            skLineSegment(sketch, "E3566", {"start": v(-80.18, -3.35) * mm, "end": v(-80.1, -3.39) * mm});
            skLineSegment(sketch, "E3567", {"start": v(-80.1, -3.39) * mm, "end": v(-80, -3.43) * mm});
            skLineSegment(sketch, "E3568", {"start": v(-80, -3.43) * mm, "end": v(-79.93, -3.46) * mm});
            skLineSegment(sketch, "E3569", {"start": v(-79.93, -3.46) * mm, "end": v(-79.84, -3.5) * mm});
            skLineSegment(sketch, "E3570", {"start": v(-79.84, -3.5) * mm, "end": v(-79.76, -3.54) * mm});
            skLineSegment(sketch, "E3571", {"start": v(-79.76, -3.54) * mm, "end": v(-79.68, -3.57) * mm});
            skLineSegment(sketch, "E3572", {"start": v(-79.68, -3.57) * mm, "end": v(-79.6, -3.6) * mm});
            skLineSegment(sketch, "E3573", {"start": v(-79.6, -3.6) * mm, "end": v(-79.52, -3.64) * mm});
            skLineSegment(sketch, "E3574", {"start": v(-79.52, -3.64) * mm, "end": v(-79.44, -3.67) * mm});
            skLineSegment(sketch, "E3575", {"start": v(-79.44, -3.67) * mm, "end": v(-79.36, -3.7) * mm});
            skLineSegment(sketch, "E3576", {"start": v(-79.36, -3.7) * mm, "end": v(-79.29, -3.73) * mm});
            skLineSegment(sketch, "E3577", {"start": v(-79.29, -3.73) * mm, "end": v(-79.21, -3.76) * mm});
            skLineSegment(sketch, "E3578", {"start": v(-79.21, -3.76) * mm, "end": v(-79.14, -3.8) * mm});
            skLineSegment(sketch, "E3579", {"start": v(-79.14, -3.8) * mm, "end": v(-79.06, -3.82) * mm});
            skLineSegment(sketch, "E3580", {"start": v(-79.06, -3.82) * mm, "end": v(-79, -3.85) * mm});
            skLineSegment(sketch, "E3581", {"start": v(-79, -3.85) * mm, "end": v(-78.92, -3.87) * mm});
            skLineSegment(sketch, "E3582", {"start": v(-78.92, -3.87) * mm, "end": v(-78.85, -3.9) * mm});
            skLineSegment(sketch, "E3583", {"start": v(-78.85, -3.9) * mm, "end": v(-78.78, -3.93) * mm});
            skLineSegment(sketch, "E3584", {"start": v(-78.78, -3.93) * mm, "end": v(-78.71, -3.95) * mm});
            skLineSegment(sketch, "E3585", {"start": v(-78.71, -3.95) * mm, "end": v(-78.64, -3.97) * mm});
            skLineSegment(sketch, "E3586", {"start": v(-78.64, -3.97) * mm, "end": v(-78.58, -4) * mm});
            skLineSegment(sketch, "E3587", {"start": v(-78.58, -4) * mm, "end": v(-78.51, -4.02) * mm});
            skLineSegment(sketch, "E3588", {"start": v(-78.51, -4.02) * mm, "end": v(-78.45, -4.04) * mm});
            skLineSegment(sketch, "E3589", {"start": v(-78.45, -4.04) * mm, "end": v(-78.38, -4.06) * mm});
            skLineSegment(sketch, "E3590", {"start": v(-78.38, -4.06) * mm, "end": v(-78.32, -4.08) * mm});
            skLineSegment(sketch, "E3591", {"start": v(-78.32, -4.08) * mm, "end": v(-78.26, -4.1) * mm});
            skLineSegment(sketch, "E3592", {"start": v(-78.26, -4.1) * mm, "end": v(-78.2, -4.12) * mm});
            skLineSegment(sketch, "E3593", {"start": v(-78.2, -4.12) * mm, "end": v(-78.14, -4.14) * mm});
            skLineSegment(sketch, "E3594", {"start": v(-78.14, -4.14) * mm, "end": v(-78.08, -4.16) * mm});
            skLineSegment(sketch, "E3595", {"start": v(-78.08, -4.16) * mm, "end": v(-78.03, -4.17) * mm});
            skLineSegment(sketch, "E3596", {"start": v(-78.03, -4.17) * mm, "end": v(-78.03, -4.4) * mm});
            skLineSegment(sketch, "E3597", {"start": v(-78.03, -4.4) * mm, "end": v(-78.05, -5.21) * mm});
            skLineSegment(sketch, "E3598", {"start": v(-78.05, -5.21) * mm, "end": v(-78.07, -5.45) * mm});
            skLineSegment(sketch, "E3599", {"start": v(-78.07, -5.45) * mm, "end": v(-78.13, -5.46) * mm});
            skLineSegment(sketch, "E3600", {"start": v(-78.13, -5.46) * mm, "end": v(-78.19, -5.47) * mm});
            skLineSegment(sketch, "E3601", {"start": v(-78.19, -5.47) * mm, "end": v(-78.25, -5.49) * mm});
            skLineSegment(sketch, "E3602", {"start": v(-78.25, -5.49) * mm, "end": v(-78.3, -5.5) * mm});
            skLineSegment(sketch, "E3603", {"start": v(-78.3, -5.5) * mm, "end": v(-78.37, -5.52) * mm});
            skLineSegment(sketch, "E3604", {"start": v(-78.37, -5.52) * mm, "end": v(-78.43, -5.53) * mm});
            skLineSegment(sketch, "E3605", {"start": v(-78.43, -5.53) * mm, "end": v(-78.5, -5.55) * mm});
            skLineSegment(sketch, "E3606", {"start": v(-78.5, -5.55) * mm, "end": v(-78.56, -5.57) * mm});
            skLineSegment(sketch, "E3607", {"start": v(-78.56, -5.57) * mm, "end": v(-78.63, -5.58) * mm});
            skLineSegment(sketch, "E3608", {"start": v(-78.63, -5.58) * mm, "end": v(-78.7, -5.6) * mm});
            skLineSegment(sketch, "E3609", {"start": v(-78.7, -5.6) * mm, "end": v(-78.77, -5.62) * mm});
            skLineSegment(sketch, "E3610", {"start": v(-78.77, -5.62) * mm, "end": v(-78.84, -5.64) * mm});
            skLineSegment(sketch, "E3611", {"start": v(-78.84, -5.64) * mm, "end": v(-78.9, -5.66) * mm});
            skLineSegment(sketch, "E3612", {"start": v(-78.9, -5.66) * mm, "end": v(-78.98, -5.68) * mm});
            skLineSegment(sketch, "E3613", {"start": v(-78.98, -5.68) * mm, "end": v(-79.05, -5.7) * mm});
            skLineSegment(sketch, "E3614", {"start": v(-79.05, -5.7) * mm, "end": v(-79.13, -5.73) * mm});
            skLineSegment(sketch, "E3615", {"start": v(-79.13, -5.73) * mm, "end": v(-79.2, -5.75) * mm});
            skLineSegment(sketch, "E3616", {"start": v(-79.2, -5.75) * mm, "end": v(-79.28, -5.78) * mm});
            skLineSegment(sketch, "E3617", {"start": v(-79.28, -5.78) * mm, "end": v(-79.36, -5.8) * mm});
            skLineSegment(sketch, "E3618", {"start": v(-79.36, -5.8) * mm, "end": v(-79.43, -5.83) * mm});
            skLineSegment(sketch, "E3619", {"start": v(-79.43, -5.83) * mm, "end": v(-79.51, -5.85) * mm});
            skLineSegment(sketch, "E3620", {"start": v(-79.51, -5.85) * mm, "end": v(-79.6, -5.88) * mm});
            skLineSegment(sketch, "E3621", {"start": v(-79.6, -5.88) * mm, "end": v(-79.67, -5.9) * mm});
            skLineSegment(sketch, "E3622", {"start": v(-79.67, -5.9) * mm, "end": v(-79.76, -5.94) * mm});
            skLineSegment(sketch, "E3623", {"start": v(-79.76, -5.94) * mm, "end": v(-79.84, -5.97) * mm});
            skLineSegment(sketch, "E3624", {"start": v(-79.84, -5.97) * mm, "end": v(-79.92, -6) * mm});
            skLineSegment(sketch, "E3625", {"start": v(-79.92, -6) * mm, "end": v(-80, -6.03) * mm});
            skLineSegment(sketch, "E3626", {"start": v(-80, -6.03) * mm, "end": v(-80.1, -6.06) * mm});
            skLineSegment(sketch, "E3627", {"start": v(-80.1, -6.06) * mm, "end": v(-80.18, -6.1) * mm});
            skLineSegment(sketch, "E3628", {"start": v(-80.18, -6.1) * mm, "end": v(-80.27, -6.13) * mm});
            skLineSegment(sketch, "E3629", {"start": v(-80.27, -6.13) * mm, "end": v(-80.36, -6.16) * mm});
            skLineSegment(sketch, "E3630", {"start": v(-80.36, -6.16) * mm, "end": v(-80.45, -6.2) * mm});
            skLineSegment(sketch, "E3631", {"start": v(-80.45, -6.2) * mm, "end": v(-80.54, -6.23) * mm});
            skLineSegment(sketch, "E3632", {"start": v(-80.54, -6.23) * mm, "end": v(-80.63, -6.27) * mm});
            skLineSegment(sketch, "E3633", {"start": v(-80.63, -6.27) * mm, "end": v(-80.73, -6.31) * mm});
            skLineSegment(sketch, "E3634", {"start": v(-80.73, -6.31) * mm, "end": v(-80.82, -6.35) * mm});
            skLineSegment(sketch, "E3635", {"start": v(-80.82, -6.35) * mm, "end": v(-80.91, -6.4) * mm});
            skLineSegment(sketch, "E3636", {"start": v(-80.91, -6.4) * mm, "end": v(-81, -6.43) * mm});
            skLineSegment(sketch, "E3637", {"start": v(-81, -6.43) * mm, "end": v(-81.1, -6.47) * mm});
            skLineSegment(sketch, "E3638", {"start": v(-81.1, -6.47) * mm, "end": v(-81.2, -6.52) * mm});
            skLineSegment(sketch, "E3639", {"start": v(-81.2, -6.52) * mm, "end": v(-81.23, -6.56) * mm});
            skLineSegment(sketch, "E3640", {"start": v(-81.23, -6.56) * mm, "end": v(-81.22, -7.6) * mm});
            skLineSegment(sketch, "E3641", {"start": v(-81.22, -7.6) * mm, "end": v(-81.19, -7.64) * mm});
            skLineSegment(sketch, "E3642", {"start": v(-81.19, -7.64) * mm, "end": v(-81.1, -7.68) * mm});
            skLineSegment(sketch, "E3643", {"start": v(-81.1, -7.68) * mm, "end": v(-81, -7.72) * mm});
            skLineSegment(sketch, "E3644", {"start": v(-81, -7.72) * mm, "end": v(-80.9, -7.76) * mm});
            skLineSegment(sketch, "E3645", {"start": v(-80.9, -7.76) * mm, "end": v(-80.8, -7.8) * mm});
            skLineSegment(sketch, "E3646", {"start": v(-80.8, -7.8) * mm, "end": v(-80.7, -7.84) * mm});
            skLineSegment(sketch, "E3647", {"start": v(-80.7, -7.84) * mm, "end": v(-80.61, -7.87) * mm});
            skLineSegment(sketch, "E3648", {"start": v(-80.61, -7.87) * mm, "end": v(-80.52, -7.9) * mm});
            skLineSegment(sketch, "E3649", {"start": v(-80.52, -7.9) * mm, "end": v(-80.43, -7.94) * mm});
            skLineSegment(sketch, "E3650", {"start": v(-80.43, -7.94) * mm, "end": v(-80.34, -7.98) * mm});
            skLineSegment(sketch, "E3651", {"start": v(-80.34, -7.98) * mm, "end": v(-80.25, -8) * mm});
            skLineSegment(sketch, "E3652", {"start": v(-80.25, -8) * mm, "end": v(-80.16, -8.04) * mm});
            skLineSegment(sketch, "E3653", {"start": v(-80.16, -8.04) * mm, "end": v(-80.07, -8.07) * mm});
            skLineSegment(sketch, "E3654", {"start": v(-80.07, -8.07) * mm, "end": v(-79.98, -8.1) * mm});
            skLineSegment(sketch, "E3655", {"start": v(-79.98, -8.1) * mm, "end": v(-79.9, -8.13) * mm});
            skLineSegment(sketch, "E3656", {"start": v(-79.9, -8.13) * mm, "end": v(-79.81, -8.16) * mm});
            skLineSegment(sketch, "E3657", {"start": v(-79.81, -8.16) * mm, "end": v(-79.73, -8.19) * mm});
            skLineSegment(sketch, "E3658", {"start": v(-79.73, -8.19) * mm, "end": v(-79.65, -8.21) * mm});
            skLineSegment(sketch, "E3659", {"start": v(-79.65, -8.21) * mm, "end": v(-79.56, -8.24) * mm});
            skLineSegment(sketch, "E3660", {"start": v(-79.56, -8.24) * mm, "end": v(-79.48, -8.27) * mm});
            skLineSegment(sketch, "E3661", {"start": v(-79.48, -8.27) * mm, "end": v(-79.4, -8.29) * mm});
            skLineSegment(sketch, "E3662", {"start": v(-79.4, -8.29) * mm, "end": v(-79.33, -8.31) * mm});
            skLineSegment(sketch, "E3663", {"start": v(-79.33, -8.31) * mm, "end": v(-79.25, -8.34) * mm});
            skLineSegment(sketch, "E3664", {"start": v(-79.25, -8.34) * mm, "end": v(-79.17, -8.36) * mm});
            skLineSegment(sketch, "E3665", {"start": v(-79.17, -8.36) * mm, "end": v(-79.1, -8.38) * mm});
            skLineSegment(sketch, "E3666", {"start": v(-79.1, -8.38) * mm, "end": v(-79.02, -8.4) * mm});
            skLineSegment(sketch, "E3667", {"start": v(-79.02, -8.4) * mm, "end": v(-78.95, -8.42) * mm});
            skLineSegment(sketch, "E3668", {"start": v(-78.95, -8.42) * mm, "end": v(-78.87, -8.44) * mm});
            skLineSegment(sketch, "E3669", {"start": v(-78.87, -8.44) * mm, "end": v(-78.8, -8.46) * mm});
            skLineSegment(sketch, "E3670", {"start": v(-78.8, -8.46) * mm, "end": v(-78.73, -8.48) * mm});
            skLineSegment(sketch, "E3671", {"start": v(-78.73, -8.48) * mm, "end": v(-78.66, -8.5) * mm});
            skLineSegment(sketch, "E3672", {"start": v(-78.66, -8.5) * mm, "end": v(-78.6, -8.51) * mm});
            skLineSegment(sketch, "E3673", {"start": v(-78.6, -8.51) * mm, "end": v(-78.53, -8.53) * mm});
            skLineSegment(sketch, "E3674", {"start": v(-78.53, -8.53) * mm, "end": v(-78.46, -8.54) * mm});
            skLineSegment(sketch, "E3675", {"start": v(-78.46, -8.54) * mm, "end": v(-78.4, -8.56) * mm});
            skLineSegment(sketch, "E3676", {"start": v(-78.4, -8.56) * mm, "end": v(-78.33, -8.57) * mm});
            skLineSegment(sketch, "E3677", {"start": v(-78.33, -8.57) * mm, "end": v(-78.27, -8.59) * mm});
            skLineSegment(sketch, "E3678", {"start": v(-78.27, -8.59) * mm, "end": v(-78.2, -8.6) * mm});
            skLineSegment(sketch, "E3679", {"start": v(-78.2, -8.6) * mm, "end": v(-78.15, -8.61) * mm});
            skLineSegment(sketch, "E3680", {"start": v(-78.15, -8.61) * mm, "end": v(-78.09, -8.63) * mm});
            skLineSegment(sketch, "E3681", {"start": v(-78.09, -8.63) * mm, "end": v(-78.03, -8.64) * mm});
            skLineSegment(sketch, "E3682", {"start": v(-78.03, -8.64) * mm, "end": v(-78, -8.87) * mm});
            skLineSegment(sketch, "E3683", {"start": v(-78, -8.87) * mm, "end": v(-77.96, -9.68) * mm});
            skLineSegment(sketch, "E3684", {"start": v(-77.96, -9.68) * mm, "end": v(-77.96, -9.9) * mm});
            skLineSegment(sketch, "E3685", {"start": v(-77.96, -9.9) * mm, "end": v(-78.01, -9.93) * mm});
            skLineSegment(sketch, "E3686", {"start": v(-78.01, -9.93) * mm, "end": v(-78.07, -9.95) * mm});
            skLineSegment(sketch, "E3687", {"start": v(-78.07, -9.95) * mm, "end": v(-78.13, -9.97) * mm});
            skLineSegment(sketch, "E3688", {"start": v(-78.13, -9.97) * mm, "end": v(-78.19, -9.99) * mm});
            skLineSegment(sketch, "E3689", {"start": v(-78.19, -9.99) * mm, "end": v(-78.25, -10) * mm});
            skLineSegment(sketch, "E3690", {"start": v(-78.25, -10) * mm, "end": v(-78.31, -10.03) * mm});
            skLineSegment(sketch, "E3691", {"start": v(-78.31, -10.03) * mm, "end": v(-78.37, -10.05) * mm});
            skLineSegment(sketch, "E3692", {"start": v(-78.37, -10.05) * mm, "end": v(-78.44, -10.07) * mm});
            skLineSegment(sketch, "E3693", {"start": v(-78.44, -10.07) * mm, "end": v(-78.5, -10.1) * mm});
            skLineSegment(sketch, "E3694", {"start": v(-78.5, -10.1) * mm, "end": v(-78.57, -10.12) * mm});
            skLineSegment(sketch, "E3695", {"start": v(-78.57, -10.12) * mm, "end": v(-78.64, -10.15) * mm});
            skLineSegment(sketch, "E3696", {"start": v(-78.64, -10.15) * mm, "end": v(-78.7, -10.17) * mm});
            skLineSegment(sketch, "E3697", {"start": v(-78.7, -10.17) * mm, "end": v(-78.77, -10.2) * mm});
            skLineSegment(sketch, "E3698", {"start": v(-78.77, -10.2) * mm, "end": v(-78.84, -10.23) * mm});
            skLineSegment(sketch, "E3699", {"start": v(-78.84, -10.23) * mm, "end": v(-78.91, -10.26) * mm});
            skLineSegment(sketch, "E3700", {"start": v(-78.91, -10.26) * mm, "end": v(-78.99, -10.29) * mm});
            skLineSegment(sketch, "E3701", {"start": v(-78.99, -10.29) * mm, "end": v(-79.06, -10.32) * mm});
            skLineSegment(sketch, "E3702", {"start": v(-79.06, -10.32) * mm, "end": v(-79.13, -10.35) * mm});
            skLineSegment(sketch, "E3703", {"start": v(-79.13, -10.35) * mm, "end": v(-79.2, -10.38) * mm});
            skLineSegment(sketch, "E3704", {"start": v(-79.2, -10.38) * mm, "end": v(-79.28, -10.41) * mm});
            skLineSegment(sketch, "E3705", {"start": v(-79.28, -10.41) * mm, "end": v(-79.36, -10.45) * mm});
            skLineSegment(sketch, "E3706", {"start": v(-79.36, -10.45) * mm, "end": v(-79.44, -10.48) * mm});
            skLineSegment(sketch, "E3707", {"start": v(-79.44, -10.48) * mm, "end": v(-79.51, -10.52) * mm});
            skLineSegment(sketch, "E3708", {"start": v(-79.51, -10.52) * mm, "end": v(-79.6, -10.55) * mm});
            skLineSegment(sketch, "E3709", {"start": v(-79.6, -10.55) * mm, "end": v(-79.67, -10.59) * mm});
            skLineSegment(sketch, "E3710", {"start": v(-79.67, -10.59) * mm, "end": v(-79.76, -10.63) * mm});
            skLineSegment(sketch, "E3711", {"start": v(-79.76, -10.63) * mm, "end": v(-79.84, -10.66) * mm});
            skLineSegment(sketch, "E3712", {"start": v(-79.84, -10.66) * mm, "end": v(-79.92, -10.7) * mm});
            skLineSegment(sketch, "E3713", {"start": v(-79.92, -10.7) * mm, "end": v(-80, -10.75) * mm});
            skLineSegment(sketch, "E3714", {"start": v(-80, -10.75) * mm, "end": v(-80.09, -10.79) * mm});
            skLineSegment(sketch, "E3715", {"start": v(-80.09, -10.79) * mm, "end": v(-80.17, -10.83) * mm});
            skLineSegment(sketch, "E3716", {"start": v(-80.17, -10.83) * mm, "end": v(-80.26, -10.87) * mm});
            skLineSegment(sketch, "E3717", {"start": v(-80.26, -10.87) * mm, "end": v(-80.35, -10.92) * mm});
            skLineSegment(sketch, "E3718", {"start": v(-80.35, -10.92) * mm, "end": v(-80.44, -10.96) * mm});
            skLineSegment(sketch, "E3719", {"start": v(-80.44, -10.96) * mm, "end": v(-80.53, -11) * mm});
            skLineSegment(sketch, "E3720", {"start": v(-80.53, -11) * mm, "end": v(-80.62, -11.06) * mm});
            skLineSegment(sketch, "E3721", {"start": v(-80.62, -11.06) * mm, "end": v(-80.7, -11.1) * mm});
            skLineSegment(sketch, "E3722", {"start": v(-80.7, -11.1) * mm, "end": v(-80.8, -11.16) * mm});
            skLineSegment(sketch, "E3723", {"start": v(-80.8, -11.16) * mm, "end": v(-80.89, -11.2) * mm});
            skLineSegment(sketch, "E3724", {"start": v(-80.89, -11.2) * mm, "end": v(-80.98, -11.26) * mm});
            skLineSegment(sketch, "E3725", {"start": v(-80.98, -11.26) * mm, "end": v(-81, -11.3) * mm});
            skLineSegment(sketch, "E3726", {"start": v(-81, -11.3) * mm, "end": v(-80.9, -12.34) * mm});
            skLineSegment(sketch, "E3727", {"start": v(-80.9, -12.34) * mm, "end": v(-80.87, -12.38) * mm});
            skLineSegment(sketch, "E3728", {"start": v(-80.87, -12.38) * mm, "end": v(-80.77, -12.41) * mm});
            skLineSegment(sketch, "E3729", {"start": v(-80.77, -12.41) * mm, "end": v(-80.67, -12.44) * mm});
            skLineSegment(sketch, "E3730", {"start": v(-80.67, -12.44) * mm, "end": v(-80.57, -12.47) * mm});
            skLineSegment(sketch, "E3731", {"start": v(-80.57, -12.47) * mm, "end": v(-80.47, -12.5) * mm});
            skLineSegment(sketch, "E3732", {"start": v(-80.47, -12.5) * mm, "end": v(-80.37, -12.53) * mm});
            skLineSegment(sketch, "E3733", {"start": v(-80.37, -12.53) * mm, "end": v(-80.27, -12.56) * mm});
            skLineSegment(sketch, "E3734", {"start": v(-80.27, -12.56) * mm, "end": v(-80.18, -12.58) * mm});
            skLineSegment(sketch, "E3735", {"start": v(-80.18, -12.58) * mm, "end": v(-80.08, -12.6) * mm});
            skLineSegment(sketch, "E3736", {"start": v(-80.08, -12.6) * mm, "end": v(-79.99, -12.63) * mm});
            skLineSegment(sketch, "E3737", {"start": v(-79.99, -12.63) * mm, "end": v(-79.9, -12.66) * mm});
            skLineSegment(sketch, "E3738", {"start": v(-79.9, -12.66) * mm, "end": v(-79.8, -12.68) * mm});
            skLineSegment(sketch, "E3739", {"start": v(-79.8, -12.68) * mm, "end": v(-79.72, -12.7) * mm});
            skLineSegment(sketch, "E3740", {"start": v(-79.72, -12.7) * mm, "end": v(-79.63, -12.73) * mm});
            skLineSegment(sketch, "E3741", {"start": v(-79.63, -12.73) * mm, "end": v(-79.54, -12.75) * mm});
            skLineSegment(sketch, "E3742", {"start": v(-79.54, -12.75) * mm, "end": v(-79.45, -12.77) * mm});
            skLineSegment(sketch, "E3743", {"start": v(-79.45, -12.77) * mm, "end": v(-79.37, -12.79) * mm});
            skLineSegment(sketch, "E3744", {"start": v(-79.37, -12.79) * mm, "end": v(-79.28, -12.8) * mm});
            skLineSegment(sketch, "E3745", {"start": v(-79.28, -12.8) * mm, "end": v(-79.2, -12.83) * mm});
            skLineSegment(sketch, "E3746", {"start": v(-79.2, -12.83) * mm, "end": v(-79.11, -12.84) * mm});
            skLineSegment(sketch, "E3747", {"start": v(-79.11, -12.84) * mm, "end": v(-79.03, -12.86) * mm});
            skLineSegment(sketch, "E3748", {"start": v(-79.03, -12.86) * mm, "end": v(-78.95, -12.88) * mm});
            skLineSegment(sketch, "E3749", {"start": v(-78.95, -12.88) * mm, "end": v(-78.87, -12.9) * mm});
            skLineSegment(sketch, "E3750", {"start": v(-78.87, -12.9) * mm, "end": v(-78.8, -12.91) * mm});
            skLineSegment(sketch, "E3751", {"start": v(-78.8, -12.91) * mm, "end": v(-78.72, -12.92) * mm});
            skLineSegment(sketch, "E3752", {"start": v(-78.72, -12.92) * mm, "end": v(-78.64, -12.94) * mm});
            skLineSegment(sketch, "E3753", {"start": v(-78.64, -12.94) * mm, "end": v(-78.56, -12.95) * mm});
            skLineSegment(sketch, "E3754", {"start": v(-78.56, -12.95) * mm, "end": v(-78.5, -12.97) * mm});
            skLineSegment(sketch, "E3755", {"start": v(-78.5, -12.97) * mm, "end": v(-78.42, -12.98) * mm});
            skLineSegment(sketch, "E3756", {"start": v(-78.42, -12.98) * mm, "end": v(-78.35, -12.99) * mm});
            skLineSegment(sketch, "E3757", {"start": v(-78.35, -12.99) * mm, "end": v(-78.27, -13) * mm});
            skLineSegment(sketch, "E3758", {"start": v(-78.27, -13) * mm, "end": v(-78.2, -13.01) * mm});
            skLineSegment(sketch, "E3759", {"start": v(-78.2, -13.01) * mm, "end": v(-78.14, -13.02) * mm});
            skLineSegment(sketch, "E3760", {"start": v(-78.14, -13.02) * mm, "end": v(-78.07, -13.03) * mm});
            skLineSegment(sketch, "E3761", {"start": v(-78.07, -13.03) * mm, "end": v(-78, -13.04) * mm});
            skLineSegment(sketch, "E3762", {"start": v(-78, -13.04) * mm, "end": v(-77.94, -13.05) * mm});
            skLineSegment(sketch, "E3763", {"start": v(-77.94, -13.05) * mm, "end": v(-77.88, -13.06) * mm});
            skLineSegment(sketch, "E3764", {"start": v(-77.88, -13.06) * mm, "end": v(-77.81, -13.07) * mm});
            skLineSegment(sketch, "E3765", {"start": v(-77.81, -13.07) * mm, "end": v(-77.75, -13.07) * mm});
            skLineSegment(sketch, "E3766", {"start": v(-77.75, -13.07) * mm, "end": v(-77.7, -13.08) * mm});
            skLineSegment(sketch, "E3767", {"start": v(-77.7, -13.08) * mm, "end": v(-77.63, -13.09) * mm});
            skLineSegment(sketch, "E3768", {"start": v(-77.63, -13.09) * mm, "end": v(-77.59, -13.32) * mm});
            skLineSegment(sketch, "E3769", {"start": v(-77.59, -13.32) * mm, "end": v(-77.47, -14.11) * mm});
            skLineSegment(sketch, "E3770", {"start": v(-77.47, -14.11) * mm, "end": v(-77.45, -14.35) * mm});
            skLineSegment(sketch, "E3771", {"start": v(-77.45, -14.35) * mm, "end": v(-77.5, -14.37) * mm});
            skLineSegment(sketch, "E3772", {"start": v(-77.5, -14.37) * mm, "end": v(-77.56, -14.4) * mm});
            skLineSegment(sketch, "E3773", {"start": v(-77.56, -14.4) * mm, "end": v(-77.61, -14.42) * mm});
            skLineSegment(sketch, "E3774", {"start": v(-77.61, -14.42) * mm, "end": v(-77.67, -14.44) * mm});
            skLineSegment(sketch, "E3775", {"start": v(-77.67, -14.44) * mm, "end": v(-77.73, -14.47) * mm});
            skLineSegment(sketch, "E3776", {"start": v(-77.73, -14.47) * mm, "end": v(-77.79, -14.5) * mm});
            skLineSegment(sketch, "E3777", {"start": v(-77.79, -14.5) * mm, "end": v(-77.85, -14.53) * mm});
            skLineSegment(sketch, "E3778", {"start": v(-77.85, -14.53) * mm, "end": v(-77.91, -14.55) * mm});
            skLineSegment(sketch, "E3779", {"start": v(-77.91, -14.55) * mm, "end": v(-77.97, -14.58) * mm});
            skLineSegment(sketch, "E3780", {"start": v(-77.97, -14.58) * mm, "end": v(-78.04, -14.61) * mm});
            skLineSegment(sketch, "E3781", {"start": v(-78.04, -14.61) * mm, "end": v(-78.1, -14.65) * mm});
            skLineSegment(sketch, "E3782", {"start": v(-78.1, -14.65) * mm, "end": v(-78.17, -14.68) * mm});
            skLineSegment(sketch, "E3783", {"start": v(-78.17, -14.68) * mm, "end": v(-78.23, -14.7) * mm});
            skLineSegment(sketch, "E3784", {"start": v(-78.23, -14.7) * mm, "end": v(-78.3, -14.74) * mm});
            skLineSegment(sketch, "E3785", {"start": v(-78.3, -14.74) * mm, "end": v(-78.37, -14.78) * mm});
            skLineSegment(sketch, "E3786", {"start": v(-78.37, -14.78) * mm, "end": v(-78.44, -14.81) * mm});
            skLineSegment(sketch, "E3787", {"start": v(-78.44, -14.81) * mm, "end": v(-78.5, -14.85) * mm});
            skLineSegment(sketch, "E3788", {"start": v(-78.5, -14.85) * mm, "end": v(-78.58, -14.89) * mm});
            skLineSegment(sketch, "E3789", {"start": v(-78.58, -14.89) * mm, "end": v(-78.65, -14.93) * mm});
            skLineSegment(sketch, "E3790", {"start": v(-78.65, -14.93) * mm, "end": v(-78.72, -14.97) * mm});
            skLineSegment(sketch, "E3791", {"start": v(-78.72, -14.97) * mm, "end": v(-78.8, -15) * mm});
            skLineSegment(sketch, "E3792", {"start": v(-78.8, -15) * mm, "end": v(-78.87, -15.05) * mm});
            skLineSegment(sketch, "E3793", {"start": v(-78.87, -15.05) * mm, "end": v(-78.94, -15.09) * mm});
            skLineSegment(sketch, "E3794", {"start": v(-78.94, -15.09) * mm, "end": v(-79.02, -15.13) * mm});
            skLineSegment(sketch, "E3795", {"start": v(-79.02, -15.13) * mm, "end": v(-79.1, -15.18) * mm});
            skLineSegment(sketch, "E3796", {"start": v(-79.1, -15.18) * mm, "end": v(-79.17, -15.22) * mm});
            skLineSegment(sketch, "E3797", {"start": v(-79.17, -15.22) * mm, "end": v(-79.25, -15.27) * mm});
            skLineSegment(sketch, "E3798", {"start": v(-79.25, -15.27) * mm, "end": v(-79.33, -15.31) * mm});
            skLineSegment(sketch, "E3799", {"start": v(-79.33, -15.31) * mm, "end": v(-79.4, -15.36) * mm});
            skLineSegment(sketch, "E3800", {"start": v(-79.4, -15.36) * mm, "end": v(-79.5, -15.41) * mm});
            skLineSegment(sketch, "E3801", {"start": v(-79.5, -15.41) * mm, "end": v(-79.57, -15.46) * mm});
            skLineSegment(sketch, "E3802", {"start": v(-79.57, -15.46) * mm, "end": v(-79.65, -15.51) * mm});
            skLineSegment(sketch, "E3803", {"start": v(-79.65, -15.51) * mm, "end": v(-79.74, -15.56) * mm});
            skLineSegment(sketch, "E3804", {"start": v(-79.74, -15.56) * mm, "end": v(-79.82, -15.62) * mm});
            skLineSegment(sketch, "E3805", {"start": v(-79.82, -15.62) * mm, "end": v(-79.9, -15.67) * mm});
            skLineSegment(sketch, "E3806", {"start": v(-79.9, -15.67) * mm, "end": v(-80, -15.73) * mm});
            skLineSegment(sketch, "E3807", {"start": v(-80, -15.73) * mm, "end": v(-80.08, -15.78) * mm});
            skLineSegment(sketch, "E3808", {"start": v(-80.08, -15.78) * mm, "end": v(-80.16, -15.84) * mm});
            skLineSegment(sketch, "E3809", {"start": v(-80.16, -15.84) * mm, "end": v(-80.25, -15.9) * mm});
            skLineSegment(sketch, "E3810", {"start": v(-80.25, -15.9) * mm, "end": v(-80.34, -15.96) * mm});
            skLineSegment(sketch, "E3811", {"start": v(-80.34, -15.96) * mm, "end": v(-80.36, -16) * mm});
            skLineSegment(sketch, "E3812", {"start": v(-80.36, -16) * mm, "end": v(-80.16, -17.03) * mm});
            skLineSegment(sketch, "E3813", {"start": v(-80.16, -17.03) * mm, "end": v(-80.12, -17.07) * mm});
            skLineSegment(sketch, "E3814", {"start": v(-80.12, -17.07) * mm, "end": v(-80.02, -17.09) * mm});
            skLineSegment(sketch, "E3815", {"start": v(-80.02, -17.09) * mm, "end": v(-79.92, -17.11) * mm});
            skLineSegment(sketch, "E3816", {"start": v(-79.92, -17.11) * mm, "end": v(-79.81, -17.13) * mm});
            skLineSegment(sketch, "E3817", {"start": v(-79.81, -17.13) * mm, "end": v(-79.71, -17.15) * mm});
            skLineSegment(sketch, "E3818", {"start": v(-79.71, -17.15) * mm, "end": v(-79.61, -17.17) * mm});
            skLineSegment(sketch, "E3819", {"start": v(-79.61, -17.17) * mm, "end": v(-79.52, -17.19) * mm});
            skLineSegment(sketch, "E3820", {"start": v(-79.52, -17.19) * mm, "end": v(-79.42, -17.2) * mm});
            skLineSegment(sketch, "E3821", {"start": v(-79.42, -17.2) * mm, "end": v(-79.32, -17.22) * mm});
            skLineSegment(sketch, "E3822", {"start": v(-79.32, -17.22) * mm, "end": v(-79.23, -17.24) * mm});
            skLineSegment(sketch, "E3823", {"start": v(-79.23, -17.24) * mm, "end": v(-79.13, -17.26) * mm});
            skLineSegment(sketch, "E3824", {"start": v(-79.13, -17.26) * mm, "end": v(-79.04, -17.27) * mm});
            skLineSegment(sketch, "E3825", {"start": v(-79.04, -17.27) * mm, "end": v(-78.95, -17.29) * mm});
            skLineSegment(sketch, "E3826", {"start": v(-78.95, -17.29) * mm, "end": v(-78.86, -17.3) * mm});
            skLineSegment(sketch, "E3827", {"start": v(-78.86, -17.3) * mm, "end": v(-78.77, -17.31) * mm});
            skLineSegment(sketch, "E3828", {"start": v(-78.77, -17.31) * mm, "end": v(-78.68, -17.33) * mm});
            skLineSegment(sketch, "E3829", {"start": v(-78.68, -17.33) * mm, "end": v(-78.59, -17.34) * mm});
            skLineSegment(sketch, "E3830", {"start": v(-78.59, -17.34) * mm, "end": v(-78.5, -17.35) * mm});
            skLineSegment(sketch, "E3831", {"start": v(-78.5, -17.35) * mm, "end": v(-78.42, -17.36) * mm});
            skLineSegment(sketch, "E3832", {"start": v(-78.42, -17.36) * mm, "end": v(-78.33, -17.37) * mm});
            skLineSegment(sketch, "E3833", {"start": v(-78.33, -17.37) * mm, "end": v(-78.25, -17.38) * mm});
            skLineSegment(sketch, "E3834", {"start": v(-78.25, -17.38) * mm, "end": v(-78.17, -17.4) * mm});
            skLineSegment(sketch, "E3835", {"start": v(-78.17, -17.4) * mm, "end": v(-78.09, -17.4) * mm});
            skLineSegment(sketch, "E3836", {"start": v(-78.09, -17.4) * mm, "end": v(-78, -17.4) * mm});
            skLineSegment(sketch, "E3837", {"start": v(-78, -17.4) * mm, "end": v(-77.93, -17.42) * mm});
            skLineSegment(sketch, "E3838", {"start": v(-77.93, -17.42) * mm, "end": v(-77.85, -17.42) * mm});
            skLineSegment(sketch, "E3839", {"start": v(-77.85, -17.42) * mm, "end": v(-77.78, -17.43) * mm});
            skLineSegment(sketch, "E3840", {"start": v(-77.78, -17.43) * mm, "end": v(-77.7, -17.44) * mm});
            skLineSegment(sketch, "E3841", {"start": v(-77.7, -17.44) * mm, "end": v(-77.63, -17.44) * mm});
            skLineSegment(sketch, "E3842", {"start": v(-77.63, -17.44) * mm, "end": v(-77.56, -17.45) * mm});
            skLineSegment(sketch, "E3843", {"start": v(-77.56, -17.45) * mm, "end": v(-77.49, -17.45) * mm});
            skLineSegment(sketch, "E3844", {"start": v(-77.49, -17.45) * mm, "end": v(-77.42, -17.46) * mm});
            skLineSegment(sketch, "E3845", {"start": v(-77.42, -17.46) * mm, "end": v(-77.35, -17.46) * mm});
            skLineSegment(sketch, "E3846", {"start": v(-77.35, -17.46) * mm, "end": v(-77.28, -17.47) * mm});
            skLineSegment(sketch, "E3847", {"start": v(-77.28, -17.47) * mm, "end": v(-77.21, -17.47) * mm});
            skLineSegment(sketch, "E3848", {"start": v(-77.21, -17.47) * mm, "end": v(-77.15, -17.47) * mm});
            skLineSegment(sketch, "E3849", {"start": v(-77.15, -17.47) * mm, "end": v(-77.08, -17.47) * mm});
            skLineSegment(sketch, "E3850", {"start": v(-77.08, -17.47) * mm, "end": v(-77.02, -17.48) * mm});
            skLineSegment(sketch, "E3851", {"start": v(-77.02, -17.48) * mm, "end": v(-76.96, -17.48) * mm});
            skLineSegment(sketch, "E3852", {"start": v(-76.96, -17.48) * mm, "end": v(-76.9, -17.48) * mm});
            skLineSegment(sketch, "E3853", {"start": v(-76.9, -17.48) * mm, "end": v(-76.84, -17.48) * mm});
            skLineSegment(sketch, "E3854", {"start": v(-76.84, -17.48) * mm, "end": v(-76.77, -17.7) * mm});
            skLineSegment(sketch, "E3855", {"start": v(-76.77, -17.7) * mm, "end": v(-76.59, -18.49) * mm});
            skLineSegment(sketch, "E3856", {"start": v(-76.59, -18.49) * mm, "end": v(-76.54, -18.72) * mm});
            skLineSegment(sketch, "E3857", {"start": v(-76.54, -18.72) * mm, "end": v(-76.6, -18.75) * mm});
            skLineSegment(sketch, "E3858", {"start": v(-76.6, -18.75) * mm, "end": v(-76.64, -18.77) * mm});
            skLineSegment(sketch, "E3859", {"start": v(-76.64, -18.77) * mm, "end": v(-76.7, -18.8) * mm});
            skLineSegment(sketch, "E3860", {"start": v(-76.7, -18.8) * mm, "end": v(-76.75, -18.84) * mm});
            skLineSegment(sketch, "E3861", {"start": v(-76.75, -18.84) * mm, "end": v(-76.8, -18.87) * mm});
            skLineSegment(sketch, "E3862", {"start": v(-76.8, -18.87) * mm, "end": v(-76.87, -18.9) * mm});
            skLineSegment(sketch, "E3863", {"start": v(-76.87, -18.9) * mm, "end": v(-76.92, -18.93) * mm});
            skLineSegment(sketch, "E3864", {"start": v(-76.92, -18.93) * mm, "end": v(-76.98, -18.97) * mm});
            skLineSegment(sketch, "E3865", {"start": v(-76.98, -18.97) * mm, "end": v(-77.04, -19) * mm});
            skLineSegment(sketch, "E3866", {"start": v(-77.04, -19) * mm, "end": v(-77.1, -19.04) * mm});
            skLineSegment(sketch, "E3867", {"start": v(-77.1, -19.04) * mm, "end": v(-77.16, -19.07) * mm});
            skLineSegment(sketch, "E3868", {"start": v(-77.16, -19.07) * mm, "end": v(-77.23, -19.11) * mm});
            skLineSegment(sketch, "E3869", {"start": v(-77.23, -19.11) * mm, "end": v(-77.29, -19.15) * mm});
            skLineSegment(sketch, "E3870", {"start": v(-77.29, -19.15) * mm, "end": v(-77.35, -19.2) * mm});
            skLineSegment(sketch, "E3871", {"start": v(-77.35, -19.2) * mm, "end": v(-77.42, -19.23) * mm});
            skLineSegment(sketch, "E3872", {"start": v(-77.42, -19.23) * mm, "end": v(-77.48, -19.27) * mm});
            skLineSegment(sketch, "E3873", {"start": v(-77.48, -19.27) * mm, "end": v(-77.55, -19.32) * mm});
            skLineSegment(sketch, "E3874", {"start": v(-77.55, -19.32) * mm, "end": v(-77.62, -19.36) * mm});
            skLineSegment(sketch, "E3875", {"start": v(-77.62, -19.36) * mm, "end": v(-77.68, -19.4) * mm});
            skLineSegment(sketch, "E3876", {"start": v(-77.68, -19.4) * mm, "end": v(-77.75, -19.45) * mm});
            skLineSegment(sketch, "E3877", {"start": v(-77.75, -19.45) * mm, "end": v(-77.82, -19.5) * mm});
            skLineSegment(sketch, "E3878", {"start": v(-77.82, -19.5) * mm, "end": v(-77.9, -19.54) * mm});
            skLineSegment(sketch, "E3879", {"start": v(-77.9, -19.54) * mm, "end": v(-77.96, -19.6) * mm});
            skLineSegment(sketch, "E3880", {"start": v(-77.96, -19.6) * mm, "end": v(-78.03, -19.64) * mm});
            skLineSegment(sketch, "E3881", {"start": v(-78.03, -19.64) * mm, "end": v(-78.1, -19.7) * mm});
            skLineSegment(sketch, "E3882", {"start": v(-78.1, -19.7) * mm, "end": v(-78.18, -19.74) * mm});
            skLineSegment(sketch, "E3883", {"start": v(-78.18, -19.74) * mm, "end": v(-78.25, -19.8) * mm});
            skLineSegment(sketch, "E3884", {"start": v(-78.25, -19.8) * mm, "end": v(-78.33, -19.85) * mm});
            skLineSegment(sketch, "E3885", {"start": v(-78.33, -19.85) * mm, "end": v(-78.4, -19.9) * mm});
            skLineSegment(sketch, "E3886", {"start": v(-78.4, -19.9) * mm, "end": v(-78.48, -19.96) * mm});
            skLineSegment(sketch, "E3887", {"start": v(-78.48, -19.96) * mm, "end": v(-78.56, -20.02) * mm});
            skLineSegment(sketch, "E3888", {"start": v(-78.56, -20.02) * mm, "end": v(-78.63, -20.08) * mm});
            skLineSegment(sketch, "E3889", {"start": v(-78.63, -20.08) * mm, "end": v(-78.71, -20.14) * mm});
            skLineSegment(sketch, "E3890", {"start": v(-78.71, -20.14) * mm, "end": v(-78.8, -20.2) * mm});
            skLineSegment(sketch, "E3891", {"start": v(-78.8, -20.2) * mm, "end": v(-78.87, -20.26) * mm});
            skLineSegment(sketch, "E3892", {"start": v(-78.87, -20.26) * mm, "end": v(-78.95, -20.32) * mm});
            skLineSegment(sketch, "E3893", {"start": v(-78.95, -20.32) * mm, "end": v(-79.03, -20.39) * mm});
            skLineSegment(sketch, "E3894", {"start": v(-79.03, -20.39) * mm, "end": v(-79.11, -20.45) * mm});
            skLineSegment(sketch, "E3895", {"start": v(-79.11, -20.45) * mm, "end": v(-79.2, -20.52) * mm});
            skLineSegment(sketch, "E3896", {"start": v(-79.2, -20.52) * mm, "end": v(-79.28, -20.58) * mm});
            skLineSegment(sketch, "E3897", {"start": v(-79.28, -20.58) * mm, "end": v(-79.29, -20.63) * mm});
            skLineSegment(sketch, "E3898", {"start": v(-79.29, -20.63) * mm, "end": v(-79, -21.63) * mm});
            skLineSegment(sketch, "E3899", {"start": v(-79, -21.63) * mm, "end": v(-78.96, -21.67) * mm});
            skLineSegment(sketch, "E3900", {"start": v(-78.96, -21.67) * mm, "end": v(-78.86, -21.68) * mm});
            skLineSegment(sketch, "E3901", {"start": v(-78.86, -21.68) * mm, "end": v(-78.75, -21.7) * mm});
            skLineSegment(sketch, "E3902", {"start": v(-78.75, -21.7) * mm, "end": v(-78.65, -21.7) * mm});
            skLineSegment(sketch, "E3903", {"start": v(-78.65, -21.7) * mm, "end": v(-78.55, -21.72) * mm});
            skLineSegment(sketch, "E3904", {"start": v(-78.55, -21.72) * mm, "end": v(-78.45, -21.73) * mm});
            skLineSegment(sketch, "E3905", {"start": v(-78.45, -21.73) * mm, "end": v(-78.35, -21.74) * mm});
            skLineSegment(sketch, "E3906", {"start": v(-78.35, -21.74) * mm, "end": v(-78.25, -21.75) * mm});
            skLineSegment(sketch, "E3907", {"start": v(-78.25, -21.75) * mm, "end": v(-78.15, -21.75) * mm});
            skLineSegment(sketch, "E3908", {"start": v(-78.15, -21.75) * mm, "end": v(-78.05, -21.76) * mm});
            skLineSegment(sketch, "E3909", {"start": v(-78.05, -21.76) * mm, "end": v(-77.96, -21.77) * mm});
            skLineSegment(sketch, "E3910", {"start": v(-77.96, -21.77) * mm, "end": v(-77.86, -21.78) * mm});
            skLineSegment(sketch, "E3911", {"start": v(-77.86, -21.78) * mm, "end": v(-77.77, -21.78) * mm});
            skLineSegment(sketch, "E3912", {"start": v(-77.77, -21.78) * mm, "end": v(-77.68, -21.79) * mm});
            skLineSegment(sketch, "E3913", {"start": v(-77.68, -21.79) * mm, "end": v(-77.59, -21.8) * mm});
            skLineSegment(sketch, "E3914", {"start": v(-77.59, -21.8) * mm, "end": v(-77.5, -21.8) * mm});
            skLineSegment(sketch, "E3915", {"start": v(-77.5, -21.8) * mm, "end": v(-77.4, -21.8) * mm});
            skLineSegment(sketch, "E3916", {"start": v(-77.4, -21.8) * mm, "end": v(-77.32, -21.8) * mm});
            skLineSegment(sketch, "E3917", {"start": v(-77.32, -21.8) * mm, "end": v(-77.24, -21.81) * mm});
            skLineSegment(sketch, "E3918", {"start": v(-77.24, -21.81) * mm, "end": v(-77.15, -21.81) * mm});
            skLineSegment(sketch, "E3919", {"start": v(-77.15, -21.81) * mm, "end": v(-77.07, -21.81) * mm});
            skLineSegment(sketch, "E3920", {"start": v(-77.07, -21.81) * mm, "end": v(-76.99, -21.82) * mm});
            skLineSegment(sketch, "E3921", {"start": v(-76.99, -21.82) * mm, "end": v(-76.9, -21.82) * mm});
            skLineSegment(sketch, "E3922", {"start": v(-76.9, -21.82) * mm, "end": v(-76.83, -21.82) * mm});
            skLineSegment(sketch, "E3923", {"start": v(-76.83, -21.82) * mm, "end": v(-76.75, -21.82) * mm});
            skLineSegment(sketch, "E3924", {"start": v(-76.75, -21.82) * mm, "end": v(-76.67, -21.82) * mm});
            skLineSegment(sketch, "E3925", {"start": v(-76.67, -21.82) * mm, "end": v(-76.6, -21.82) * mm});
            skLineSegment(sketch, "E3926", {"start": v(-76.6, -21.82) * mm, "end": v(-76.52, -21.82) * mm});
            skLineSegment(sketch, "E3927", {"start": v(-76.52, -21.82) * mm, "end": v(-76.44, -21.82) * mm});
            skLineSegment(sketch, "E3928", {"start": v(-76.44, -21.82) * mm, "end": v(-76.37, -21.82) * mm});
            skLineSegment(sketch, "E3929", {"start": v(-76.37, -21.82) * mm, "end": v(-76.3, -21.82) * mm});
            skLineSegment(sketch, "E3930", {"start": v(-76.3, -21.82) * mm, "end": v(-76.23, -21.81) * mm});
            skLineSegment(sketch, "E3931", {"start": v(-76.23, -21.81) * mm, "end": v(-76.16, -21.81) * mm});
            skLineSegment(sketch, "E3932", {"start": v(-76.16, -21.81) * mm, "end": v(-76.1, -21.8) * mm});
            skLineSegment(sketch, "E3933", {"start": v(-76.1, -21.8) * mm, "end": v(-76.03, -21.8) * mm});
            skLineSegment(sketch, "E3934", {"start": v(-76.03, -21.8) * mm, "end": v(-75.96, -21.8) * mm});
            skLineSegment(sketch, "E3935", {"start": v(-75.96, -21.8) * mm, "end": v(-75.9, -21.8) * mm});
            skLineSegment(sketch, "E3936", {"start": v(-75.9, -21.8) * mm, "end": v(-75.83, -21.8) * mm});
            skLineSegment(sketch, "E3937", {"start": v(-75.83, -21.8) * mm, "end": v(-75.77, -21.8) * mm});
            skLineSegment(sketch, "E3938", {"start": v(-75.77, -21.8) * mm, "end": v(-75.71, -21.79) * mm});
            skLineSegment(sketch, "E3939", {"start": v(-75.71, -21.79) * mm, "end": v(-75.65, -21.78) * mm});
            skLineSegment(sketch, "E3940", {"start": v(-75.65, -21.78) * mm, "end": v(-75.57, -22) * mm});
            skLineSegment(sketch, "E3941", {"start": v(-75.57, -22) * mm, "end": v(-75.31, -22.77) * mm});
            skLineSegment(sketch, "E3942", {"start": v(-75.31, -22.77) * mm, "end": v(-75.24, -23) * mm});
            skLineSegment(sketch, "E3943", {"start": v(-75.24, -23) * mm, "end": v(-75.3, -23.02) * mm});
            skLineSegment(sketch, "E3944", {"start": v(-75.3, -23.02) * mm, "end": v(-75.34, -23.06) * mm});
            skLineSegment(sketch, "E3945", {"start": v(-75.34, -23.06) * mm, "end": v(-75.4, -23.1) * mm});
            skLineSegment(sketch, "E3946", {"start": v(-75.4, -23.1) * mm, "end": v(-75.45, -23.13) * mm});
            skLineSegment(sketch, "E3947", {"start": v(-75.45, -23.13) * mm, "end": v(-75.5, -23.16) * mm});
            skLineSegment(sketch, "E3948", {"start": v(-75.5, -23.16) * mm, "end": v(-75.55, -23.2) * mm});
            skLineSegment(sketch, "E3949", {"start": v(-75.55, -23.2) * mm, "end": v(-75.6, -23.24) * mm});
            skLineSegment(sketch, "E3950", {"start": v(-75.6, -23.24) * mm, "end": v(-75.66, -23.28) * mm});
            skLineSegment(sketch, "E3951", {"start": v(-75.66, -23.28) * mm, "end": v(-75.72, -23.32) * mm});
            skLineSegment(sketch, "E3952", {"start": v(-75.72, -23.32) * mm, "end": v(-75.78, -23.36) * mm});
            skLineSegment(sketch, "E3953", {"start": v(-75.78, -23.36) * mm, "end": v(-75.83, -23.4) * mm});
            skLineSegment(sketch, "E3954", {"start": v(-75.83, -23.4) * mm, "end": v(-75.9, -23.45) * mm});
            skLineSegment(sketch, "E3955", {"start": v(-75.9, -23.45) * mm, "end": v(-75.95, -23.5) * mm});
            skLineSegment(sketch, "E3956", {"start": v(-75.95, -23.5) * mm, "end": v(-76.01, -23.54) * mm});
            skLineSegment(sketch, "E3957", {"start": v(-76.01, -23.54) * mm, "end": v(-76.07, -23.58) * mm});
            skLineSegment(sketch, "E3958", {"start": v(-76.07, -23.58) * mm, "end": v(-76.13, -23.63) * mm});
            skLineSegment(sketch, "E3959", {"start": v(-76.13, -23.63) * mm, "end": v(-76.2, -23.68) * mm});
            skLineSegment(sketch, "E3960", {"start": v(-76.2, -23.68) * mm, "end": v(-76.26, -23.73) * mm});
            skLineSegment(sketch, "E3961", {"start": v(-76.26, -23.73) * mm, "end": v(-76.32, -23.78) * mm});
            skLineSegment(sketch, "E3962", {"start": v(-76.32, -23.78) * mm, "end": v(-76.39, -23.83) * mm});
            skLineSegment(sketch, "E3963", {"start": v(-76.39, -23.83) * mm, "end": v(-76.45, -23.88) * mm});
            skLineSegment(sketch, "E3964", {"start": v(-76.45, -23.88) * mm, "end": v(-76.52, -23.94) * mm});
            skLineSegment(sketch, "E3965", {"start": v(-76.52, -23.94) * mm, "end": v(-76.58, -24) * mm});
            skLineSegment(sketch, "E3966", {"start": v(-76.58, -24) * mm, "end": v(-76.65, -24.05) * mm});
            skLineSegment(sketch, "E3967", {"start": v(-76.65, -24.05) * mm, "end": v(-76.72, -24.1) * mm});
            skLineSegment(sketch, "E3968", {"start": v(-76.72, -24.1) * mm, "end": v(-76.79, -24.16) * mm});
            skLineSegment(sketch, "E3969", {"start": v(-76.79, -24.16) * mm, "end": v(-76.86, -24.22) * mm});
            skLineSegment(sketch, "E3970", {"start": v(-76.86, -24.22) * mm, "end": v(-76.92, -24.28) * mm});
            skLineSegment(sketch, "E3971", {"start": v(-76.92, -24.28) * mm, "end": v(-77, -24.34) * mm});
            skLineSegment(sketch, "E3972", {"start": v(-77, -24.34) * mm, "end": v(-77.07, -24.4) * mm});
            skLineSegment(sketch, "E3973", {"start": v(-77.07, -24.4) * mm, "end": v(-77.14, -24.47) * mm});
            skLineSegment(sketch, "E3974", {"start": v(-77.14, -24.47) * mm, "end": v(-77.2, -24.53) * mm});
            skLineSegment(sketch, "E3975", {"start": v(-77.2, -24.53) * mm, "end": v(-77.28, -24.6) * mm});
            skLineSegment(sketch, "E3976", {"start": v(-77.28, -24.6) * mm, "end": v(-77.35, -24.67) * mm});
            skLineSegment(sketch, "E3977", {"start": v(-77.35, -24.67) * mm, "end": v(-77.43, -24.74) * mm});
            skLineSegment(sketch, "E3978", {"start": v(-77.43, -24.74) * mm, "end": v(-77.5, -24.8) * mm});
            skLineSegment(sketch, "E3979", {"start": v(-77.5, -24.8) * mm, "end": v(-77.57, -24.88) * mm});
            skLineSegment(sketch, "E3980", {"start": v(-77.57, -24.88) * mm, "end": v(-77.65, -24.95) * mm});
            skLineSegment(sketch, "E3981", {"start": v(-77.65, -24.95) * mm, "end": v(-77.73, -25.02) * mm});
            skLineSegment(sketch, "E3982", {"start": v(-77.73, -25.02) * mm, "end": v(-77.8, -25.1) * mm});
            skLineSegment(sketch, "E3983", {"start": v(-77.8, -25.1) * mm, "end": v(-77.8, -25.15) * mm});
            skLineSegment(sketch, "E3984", {"start": v(-77.8, -25.15) * mm, "end": v(-77.43, -26.12) * mm});
            skLineSegment(sketch, "E3985", {"start": v(-77.43, -26.12) * mm, "end": v(-77.4, -26.15) * mm});
            skLineSegment(sketch, "E3986", {"start": v(-77.4, -26.15) * mm, "end": v(-77.29, -26.15) * mm});
            skLineSegment(sketch, "E3987", {"start": v(-77.29, -26.15) * mm, "end": v(-77.18, -26.15) * mm});
            skLineSegment(sketch, "E3988", {"start": v(-77.18, -26.15) * mm, "end": v(-77.08, -26.16) * mm});
            skLineSegment(sketch, "E3989", {"start": v(-77.08, -26.16) * mm, "end": v(-76.97, -26.16) * mm});
            skLineSegment(sketch, "E3990", {"start": v(-76.97, -26.16) * mm, "end": v(-76.87, -26.16) * mm});
            skLineSegment(sketch, "E3991", {"start": v(-76.87, -26.16) * mm, "end": v(-76.77, -26.16) * mm});
            skLineSegment(sketch, "E3992", {"start": v(-76.77, -26.16) * mm, "end": v(-76.67, -26.16) * mm});
            skLineSegment(sketch, "E3993", {"start": v(-76.67, -26.16) * mm, "end": v(-76.57, -26.16) * mm});
            skLineSegment(sketch, "E3994", {"start": v(-76.57, -26.16) * mm, "end": v(-76.48, -26.16) * mm});
            skLineSegment(sketch, "E3995", {"start": v(-76.48, -26.16) * mm, "end": v(-76.38, -26.16) * mm});
            skLineSegment(sketch, "E3996", {"start": v(-76.38, -26.16) * mm, "end": v(-76.29, -26.16) * mm});
            skLineSegment(sketch, "E3997", {"start": v(-76.29, -26.16) * mm, "end": v(-76.2, -26.15) * mm});
            skLineSegment(sketch, "E3998", {"start": v(-76.2, -26.15) * mm, "end": v(-76.1, -26.15) * mm});
            skLineSegment(sketch, "E3999", {"start": v(-76.1, -26.15) * mm, "end": v(-76.01, -26.15) * mm});
            skLineSegment(sketch, "E4000", {"start": v(-76.01, -26.15) * mm, "end": v(-75.92, -26.15) * mm});
            skLineSegment(sketch, "E4001", {"start": v(-75.92, -26.15) * mm, "end": v(-75.83, -26.14) * mm});
            skLineSegment(sketch, "E4002", {"start": v(-75.83, -26.14) * mm, "end": v(-75.75, -26.14) * mm});
            skLineSegment(sketch, "E4003", {"start": v(-75.75, -26.14) * mm, "end": v(-75.66, -26.13) * mm});
            skLineSegment(sketch, "E4004", {"start": v(-75.66, -26.13) * mm, "end": v(-75.58, -26.13) * mm});
            skLineSegment(sketch, "E4005", {"start": v(-75.58, -26.13) * mm, "end": v(-75.5, -26.12) * mm});
            skLineSegment(sketch, "E4006", {"start": v(-75.5, -26.12) * mm, "end": v(-75.41, -26.12) * mm});
            skLineSegment(sketch, "E4007", {"start": v(-75.41, -26.12) * mm, "end": v(-75.33, -26.11) * mm});
            skLineSegment(sketch, "E4008", {"start": v(-75.33, -26.11) * mm, "end": v(-75.25, -26.1) * mm});
            skLineSegment(sketch, "E4009", {"start": v(-75.25, -26.1) * mm, "end": v(-75.17, -26.1) * mm});
            skLineSegment(sketch, "E4010", {"start": v(-75.17, -26.1) * mm, "end": v(-75.1, -26.1) * mm});
            skLineSegment(sketch, "E4011", {"start": v(-75.1, -26.1) * mm, "end": v(-75.02, -26.09) * mm});
            skLineSegment(sketch, "E4012", {"start": v(-75.02, -26.09) * mm, "end": v(-74.94, -26.08) * mm});
            skLineSegment(sketch, "E4013", {"start": v(-74.94, -26.08) * mm, "end": v(-74.87, -26.07) * mm});
            skLineSegment(sketch, "E4014", {"start": v(-74.87, -26.07) * mm, "end": v(-74.8, -26.06) * mm});
            skLineSegment(sketch, "E4015", {"start": v(-74.8, -26.06) * mm, "end": v(-74.73, -26.06) * mm});
            skLineSegment(sketch, "E4016", {"start": v(-74.73, -26.06) * mm, "end": v(-74.66, -26.05) * mm});
            skLineSegment(sketch, "E4017", {"start": v(-74.66, -26.05) * mm, "end": v(-74.59, -26.04) * mm});
            skLineSegment(sketch, "E4018", {"start": v(-74.59, -26.04) * mm, "end": v(-74.52, -26.03) * mm});
            skLineSegment(sketch, "E4019", {"start": v(-74.52, -26.03) * mm, "end": v(-74.46, -26.02) * mm});
            skLineSegment(sketch, "E4020", {"start": v(-74.46, -26.02) * mm, "end": v(-74.4, -26.01) * mm});
            skLineSegment(sketch, "E4021", {"start": v(-74.4, -26.01) * mm, "end": v(-74.33, -26) * mm});
            skLineSegment(sketch, "E4022", {"start": v(-74.33, -26) * mm, "end": v(-74.26, -26) * mm});
            skLineSegment(sketch, "E4023", {"start": v(-74.26, -26) * mm, "end": v(-74.2, -25.99) * mm});
            skLineSegment(sketch, "E4024", {"start": v(-74.2, -25.99) * mm, "end": v(-74.14, -25.98) * mm});
            skLineSegment(sketch, "E4025", {"start": v(-74.14, -25.98) * mm, "end": v(-74.08, -25.97) * mm});
            skLineSegment(sketch, "E4026", {"start": v(-74.08, -25.97) * mm, "end": v(-73.98, -26.18) * mm});
            skLineSegment(sketch, "E4027", {"start": v(-73.98, -26.18) * mm, "end": v(-73.66, -26.92) * mm});
            skLineSegment(sketch, "E4028", {"start": v(-73.66, -26.92) * mm, "end": v(-73.57, -27.13) * mm});
            skLineSegment(sketch, "E4029", {"start": v(-73.57, -27.13) * mm, "end": v(-73.62, -27.17) * mm});
            skLineSegment(sketch, "E4030", {"start": v(-73.62, -27.17) * mm, "end": v(-73.66, -27.2) * mm});
            skLineSegment(sketch, "E4031", {"start": v(-73.66, -27.2) * mm, "end": v(-73.71, -27.25) * mm});
            skLineSegment(sketch, "E4032", {"start": v(-73.71, -27.25) * mm, "end": v(-73.76, -27.29) * mm});
            skLineSegment(sketch, "E4033", {"start": v(-73.76, -27.29) * mm, "end": v(-73.8, -27.33) * mm});
            skLineSegment(sketch, "E4034", {"start": v(-73.8, -27.33) * mm, "end": v(-73.86, -27.37) * mm});
            skLineSegment(sketch, "E4035", {"start": v(-73.86, -27.37) * mm, "end": v(-73.91, -27.41) * mm});
            skLineSegment(sketch, "E4036", {"start": v(-73.91, -27.41) * mm, "end": v(-73.96, -27.46) * mm});
            skLineSegment(sketch, "E4037", {"start": v(-73.96, -27.46) * mm, "end": v(-74.02, -27.5) * mm});
            skLineSegment(sketch, "E4038", {"start": v(-74.02, -27.5) * mm, "end": v(-74.07, -27.55) * mm});
            skLineSegment(sketch, "E4039", {"start": v(-74.07, -27.55) * mm, "end": v(-74.12, -27.6) * mm});
            skLineSegment(sketch, "E4040", {"start": v(-74.12, -27.6) * mm, "end": v(-74.18, -27.64) * mm});
            skLineSegment(sketch, "E4041", {"start": v(-74.18, -27.64) * mm, "end": v(-74.23, -27.7) * mm});
            skLineSegment(sketch, "E4042", {"start": v(-74.23, -27.7) * mm, "end": v(-74.29, -27.74) * mm});
            skLineSegment(sketch, "E4043", {"start": v(-74.29, -27.74) * mm, "end": v(-74.34, -27.8) * mm});
            skLineSegment(sketch, "E4044", {"start": v(-74.34, -27.8) * mm, "end": v(-74.4, -27.85) * mm});
            skLineSegment(sketch, "E4045", {"start": v(-74.4, -27.85) * mm, "end": v(-74.46, -27.9) * mm});
            skLineSegment(sketch, "E4046", {"start": v(-74.46, -27.9) * mm, "end": v(-74.52, -27.96) * mm});
            skLineSegment(sketch, "E4047", {"start": v(-74.52, -27.96) * mm, "end": v(-74.57, -28.01) * mm});
            skLineSegment(sketch, "E4048", {"start": v(-74.57, -28.01) * mm, "end": v(-74.63, -28.07) * mm});
            skLineSegment(sketch, "E4049", {"start": v(-74.63, -28.07) * mm, "end": v(-74.7, -28.13) * mm});
            skLineSegment(sketch, "E4050", {"start": v(-74.7, -28.13) * mm, "end": v(-74.75, -28.19) * mm});
            skLineSegment(sketch, "E4051", {"start": v(-74.75, -28.19) * mm, "end": v(-74.82, -28.25) * mm});
            skLineSegment(sketch, "E4052", {"start": v(-74.82, -28.25) * mm, "end": v(-74.88, -28.3) * mm});
            skLineSegment(sketch, "E4053", {"start": v(-74.88, -28.3) * mm, "end": v(-74.94, -28.37) * mm});
            skLineSegment(sketch, "E4054", {"start": v(-74.94, -28.37) * mm, "end": v(-75, -28.44) * mm});
            skLineSegment(sketch, "E4055", {"start": v(-75, -28.44) * mm, "end": v(-75.07, -28.5) * mm});
            skLineSegment(sketch, "E4056", {"start": v(-75.07, -28.5) * mm, "end": v(-75.13, -28.57) * mm});
            skLineSegment(sketch, "E4057", {"start": v(-75.13, -28.57) * mm, "end": v(-75.2, -28.63) * mm});
            skLineSegment(sketch, "E4058", {"start": v(-75.2, -28.63) * mm, "end": v(-75.26, -28.7) * mm});
            skLineSegment(sketch, "E4059", {"start": v(-75.26, -28.7) * mm, "end": v(-75.32, -28.77) * mm});
            skLineSegment(sketch, "E4060", {"start": v(-75.32, -28.77) * mm, "end": v(-75.39, -28.84) * mm});
            skLineSegment(sketch, "E4061", {"start": v(-75.39, -28.84) * mm, "end": v(-75.45, -28.92) * mm});
            skLineSegment(sketch, "E4062", {"start": v(-75.45, -28.92) * mm, "end": v(-75.52, -28.99) * mm});
            skLineSegment(sketch, "E4063", {"start": v(-75.52, -28.99) * mm, "end": v(-75.59, -29.06) * mm});
            skLineSegment(sketch, "E4064", {"start": v(-75.59, -29.06) * mm, "end": v(-75.66, -29.14) * mm});
            skLineSegment(sketch, "E4065", {"start": v(-75.66, -29.14) * mm, "end": v(-75.72, -29.22) * mm});
            skLineSegment(sketch, "E4066", {"start": v(-75.72, -29.22) * mm, "end": v(-75.8, -29.3) * mm});
            skLineSegment(sketch, "E4067", {"start": v(-75.8, -29.3) * mm, "end": v(-75.86, -29.38) * mm});
            skLineSegment(sketch, "E4068", {"start": v(-75.86, -29.38) * mm, "end": v(-75.93, -29.46) * mm});
            skLineSegment(sketch, "E4069", {"start": v(-75.93, -29.46) * mm, "end": v(-75.93, -29.5) * mm});
            skLineSegment(sketch, "E4070", {"start": v(-75.93, -29.5) * mm, "end": v(-75.47, -30.44) * mm});
            skLineSegment(sketch, "E4071", {"start": v(-75.47, -30.44) * mm, "end": v(-75.43, -30.47) * mm});
            skLineSegment(sketch, "E4072", {"start": v(-75.43, -30.47) * mm, "end": v(-75.32, -30.46) * mm});
            skLineSegment(sketch, "E4073", {"start": v(-75.32, -30.46) * mm, "end": v(-75.22, -30.45) * mm});
            skLineSegment(sketch, "E4074", {"start": v(-75.22, -30.45) * mm, "end": v(-75.11, -30.45) * mm});
            skLineSegment(sketch, "E4075", {"start": v(-75.11, -30.45) * mm, "end": v(-75.01, -30.44) * mm});
            skLineSegment(sketch, "E4076", {"start": v(-75.01, -30.44) * mm, "end": v(-74.9, -30.43) * mm});
            skLineSegment(sketch, "E4077", {"start": v(-74.9, -30.43) * mm, "end": v(-74.8, -30.42) * mm});
            skLineSegment(sketch, "E4078", {"start": v(-74.8, -30.42) * mm, "end": v(-74.7, -30.42) * mm});
            skLineSegment(sketch, "E4079", {"start": v(-74.7, -30.42) * mm, "end": v(-74.61, -30.4) * mm});
            skLineSegment(sketch, "E4080", {"start": v(-74.61, -30.4) * mm, "end": v(-74.52, -30.4) * mm});
            skLineSegment(sketch, "E4081", {"start": v(-74.52, -30.4) * mm, "end": v(-74.42, -30.39) * mm});
            skLineSegment(sketch, "E4082", {"start": v(-74.42, -30.39) * mm, "end": v(-74.33, -30.38) * mm});
            skLineSegment(sketch, "E4083", {"start": v(-74.33, -30.38) * mm, "end": v(-74.23, -30.37) * mm});
            skLineSegment(sketch, "E4084", {"start": v(-74.23, -30.37) * mm, "end": v(-74.14, -30.36) * mm});
            skLineSegment(sketch, "E4085", {"start": v(-74.14, -30.36) * mm, "end": v(-74.05, -30.35) * mm});
            skLineSegment(sketch, "E4086", {"start": v(-74.05, -30.35) * mm, "end": v(-73.96, -30.33) * mm});
            skLineSegment(sketch, "E4087", {"start": v(-73.96, -30.33) * mm, "end": v(-73.88, -30.32) * mm});
            skLineSegment(sketch, "E4088", {"start": v(-73.88, -30.32) * mm, "end": v(-73.8, -30.31) * mm});
            skLineSegment(sketch, "E4089", {"start": v(-73.8, -30.31) * mm, "end": v(-73.7, -30.3) * mm});
            skLineSegment(sketch, "E4090", {"start": v(-73.7, -30.3) * mm, "end": v(-73.62, -30.29) * mm});
            skLineSegment(sketch, "E4091", {"start": v(-73.62, -30.29) * mm, "end": v(-73.54, -30.27) * mm});
            skLineSegment(sketch, "E4092", {"start": v(-73.54, -30.27) * mm, "end": v(-73.46, -30.26) * mm});
            skLineSegment(sketch, "E4093", {"start": v(-73.46, -30.26) * mm, "end": v(-73.38, -30.25) * mm});
            skLineSegment(sketch, "E4094", {"start": v(-73.38, -30.25) * mm, "end": v(-73.3, -30.23) * mm});
            skLineSegment(sketch, "E4095", {"start": v(-73.3, -30.23) * mm, "end": v(-73.22, -30.22) * mm});
            skLineSegment(sketch, "E4096", {"start": v(-73.22, -30.22) * mm, "end": v(-73.14, -30.2) * mm});
            skLineSegment(sketch, "E4097", {"start": v(-73.14, -30.2) * mm, "end": v(-73.07, -30.2) * mm});
            skLineSegment(sketch, "E4098", {"start": v(-73.07, -30.2) * mm, "end": v(-73, -30.18) * mm});
            skLineSegment(sketch, "E4099", {"start": v(-73, -30.18) * mm, "end": v(-72.92, -30.17) * mm});
            skLineSegment(sketch, "E4100", {"start": v(-72.92, -30.17) * mm, "end": v(-72.85, -30.15) * mm});
            skLineSegment(sketch, "E4101", {"start": v(-72.85, -30.15) * mm, "end": v(-72.78, -30.14) * mm});
            skLineSegment(sketch, "E4102", {"start": v(-72.78, -30.14) * mm, "end": v(-72.71, -30.12) * mm});
            skLineSegment(sketch, "E4103", {"start": v(-72.71, -30.12) * mm, "end": v(-72.65, -30.1) * mm});
            skLineSegment(sketch, "E4104", {"start": v(-72.65, -30.1) * mm, "end": v(-72.58, -30.1) * mm});
            skLineSegment(sketch, "E4105", {"start": v(-72.58, -30.1) * mm, "end": v(-72.51, -30.08) * mm});
            skLineSegment(sketch, "E4106", {"start": v(-72.51, -30.08) * mm, "end": v(-72.45, -30.06) * mm});
            skLineSegment(sketch, "E4107", {"start": v(-72.45, -30.06) * mm, "end": v(-72.39, -30.05) * mm});
            skLineSegment(sketch, "E4108", {"start": v(-72.39, -30.05) * mm, "end": v(-72.33, -30.04) * mm});
            skLineSegment(sketch, "E4109", {"start": v(-72.33, -30.04) * mm, "end": v(-72.27, -30.02) * mm});
            skLineSegment(sketch, "E4110", {"start": v(-72.27, -30.02) * mm, "end": v(-72.2, -30) * mm});
            skLineSegment(sketch, "E4111", {"start": v(-72.2, -30) * mm, "end": v(-72.15, -30) * mm});
            skLineSegment(sketch, "E4112", {"start": v(-72.15, -30) * mm, "end": v(-72.03, -30.2) * mm});
            skLineSegment(sketch, "E4113", {"start": v(-72.03, -30.2) * mm, "end": v(-71.64, -30.9) * mm});
            skLineSegment(sketch, "E4114", {"start": v(-71.64, -30.9) * mm, "end": v(-71.53, -31.1) * mm});
            skLineSegment(sketch, "E4115", {"start": v(-71.53, -31.1) * mm, "end": v(-71.57, -31.15) * mm});
            skLineSegment(sketch, "E4116", {"start": v(-71.57, -31.15) * mm, "end": v(-71.62, -31.19) * mm});
            skLineSegment(sketch, "E4117", {"start": v(-71.62, -31.19) * mm, "end": v(-71.66, -31.23) * mm});
            skLineSegment(sketch, "E4118", {"start": v(-71.66, -31.23) * mm, "end": v(-71.7, -31.28) * mm});
            skLineSegment(sketch, "E4119", {"start": v(-71.7, -31.28) * mm, "end": v(-71.75, -31.32) * mm});
            skLineSegment(sketch, "E4120", {"start": v(-71.75, -31.32) * mm, "end": v(-71.8, -31.37) * mm});
            skLineSegment(sketch, "E4121", {"start": v(-71.8, -31.37) * mm, "end": v(-71.85, -31.42) * mm});
            skLineSegment(sketch, "E4122", {"start": v(-71.85, -31.42) * mm, "end": v(-71.9, -31.46) * mm});
            skLineSegment(sketch, "E4123", {"start": v(-71.9, -31.46) * mm, "end": v(-71.94, -31.51) * mm});
            skLineSegment(sketch, "E4124", {"start": v(-71.94, -31.51) * mm, "end": v(-72, -31.56) * mm});
            skLineSegment(sketch, "E4125", {"start": v(-72, -31.56) * mm, "end": v(-72.04, -31.62) * mm});
            skLineSegment(sketch, "E4126", {"start": v(-72.04, -31.62) * mm, "end": v(-72.1, -31.67) * mm});
            skLineSegment(sketch, "E4127", {"start": v(-72.1, -31.67) * mm, "end": v(-72.14, -31.72) * mm});
            skLineSegment(sketch, "E4128", {"start": v(-72.14, -31.72) * mm, "end": v(-72.2, -31.78) * mm});
            skLineSegment(sketch, "E4129", {"start": v(-72.2, -31.78) * mm, "end": v(-72.24, -31.83) * mm});
            skLineSegment(sketch, "E4130", {"start": v(-72.24, -31.83) * mm, "end": v(-72.3, -31.9) * mm});
            skLineSegment(sketch, "E4131", {"start": v(-72.3, -31.9) * mm, "end": v(-72.35, -31.95) * mm});
            skLineSegment(sketch, "E4132", {"start": v(-72.35, -31.95) * mm, "end": v(-72.4, -32.01) * mm});
            skLineSegment(sketch, "E4133", {"start": v(-72.4, -32.01) * mm, "end": v(-72.45, -32.07) * mm});
            skLineSegment(sketch, "E4134", {"start": v(-72.45, -32.07) * mm, "end": v(-72.5, -32.13) * mm});
            skLineSegment(sketch, "E4135", {"start": v(-72.5, -32.13) * mm, "end": v(-72.56, -32.2) * mm});
            skLineSegment(sketch, "E4136", {"start": v(-72.56, -32.2) * mm, "end": v(-72.62, -32.26) * mm});
            skLineSegment(sketch, "E4137", {"start": v(-72.62, -32.26) * mm, "end": v(-72.67, -32.33) * mm});
            skLineSegment(sketch, "E4138", {"start": v(-72.67, -32.33) * mm, "end": v(-72.73, -32.4) * mm});
            skLineSegment(sketch, "E4139", {"start": v(-72.73, -32.4) * mm, "end": v(-72.79, -32.46) * mm});
            skLineSegment(sketch, "E4140", {"start": v(-72.79, -32.46) * mm, "end": v(-72.84, -32.53) * mm});
            skLineSegment(sketch, "E4141", {"start": v(-72.84, -32.53) * mm, "end": v(-72.9, -32.6) * mm});
            skLineSegment(sketch, "E4142", {"start": v(-72.9, -32.6) * mm, "end": v(-72.96, -32.67) * mm});
            skLineSegment(sketch, "E4143", {"start": v(-72.96, -32.67) * mm, "end": v(-73.01, -32.75) * mm});
            skLineSegment(sketch, "E4144", {"start": v(-73.01, -32.75) * mm, "end": v(-73.07, -32.82) * mm});
            skLineSegment(sketch, "E4145", {"start": v(-73.07, -32.82) * mm, "end": v(-73.13, -32.9) * mm});
            skLineSegment(sketch, "E4146", {"start": v(-73.13, -32.9) * mm, "end": v(-73.2, -32.97) * mm});
            skLineSegment(sketch, "E4147", {"start": v(-73.2, -32.97) * mm, "end": v(-73.25, -33.05) * mm});
            skLineSegment(sketch, "E4148", {"start": v(-73.25, -33.05) * mm, "end": v(-73.3, -33.13) * mm});
            skLineSegment(sketch, "E4149", {"start": v(-73.3, -33.13) * mm, "end": v(-73.37, -33.21) * mm});
            skLineSegment(sketch, "E4150", {"start": v(-73.37, -33.21) * mm, "end": v(-73.43, -33.3) * mm});
            skLineSegment(sketch, "E4151", {"start": v(-73.43, -33.3) * mm, "end": v(-73.5, -33.38) * mm});
            skLineSegment(sketch, "E4152", {"start": v(-73.5, -33.38) * mm, "end": v(-73.55, -33.46) * mm});
            skLineSegment(sketch, "E4153", {"start": v(-73.55, -33.46) * mm, "end": v(-73.61, -33.55) * mm});
            skLineSegment(sketch, "E4154", {"start": v(-73.61, -33.55) * mm, "end": v(-73.67, -33.63) * mm});
            skLineSegment(sketch, "E4155", {"start": v(-73.67, -33.63) * mm, "end": v(-73.67, -33.68) * mm});
            skLineSegment(sketch, "E4156", {"start": v(-73.67, -33.68) * mm, "end": v(-73.13, -34.57) * mm});
            skLineSegment(sketch, "E4157", {"start": v(-73.13, -34.57) * mm, "end": v(-73.08, -34.6) * mm});
            skLineSegment(sketch, "E4158", {"start": v(-73.08, -34.6) * mm, "end": v(-72.98, -34.58) * mm});
            skLineSegment(sketch, "E4159", {"start": v(-72.98, -34.58) * mm, "end": v(-72.87, -34.56) * mm});
            skLineSegment(sketch, "E4160", {"start": v(-72.87, -34.56) * mm, "end": v(-72.77, -34.55) * mm});
            skLineSegment(sketch, "E4161", {"start": v(-72.77, -34.55) * mm, "end": v(-72.67, -34.53) * mm});
            skLineSegment(sketch, "E4162", {"start": v(-72.67, -34.53) * mm, "end": v(-72.57, -34.51) * mm});
            skLineSegment(sketch, "E4163", {"start": v(-72.57, -34.51) * mm, "end": v(-72.47, -34.5) * mm});
            skLineSegment(sketch, "E4164", {"start": v(-72.47, -34.5) * mm, "end": v(-72.37, -34.48) * mm});
            skLineSegment(sketch, "E4165", {"start": v(-72.37, -34.48) * mm, "end": v(-72.28, -34.46) * mm});
            skLineSegment(sketch, "E4166", {"start": v(-72.28, -34.46) * mm, "end": v(-72.18, -34.44) * mm});
            skLineSegment(sketch, "E4167", {"start": v(-72.18, -34.44) * mm, "end": v(-72.09, -34.42) * mm});
            skLineSegment(sketch, "E4168", {"start": v(-72.09, -34.42) * mm, "end": v(-72, -34.4) * mm});
            skLineSegment(sketch, "E4169", {"start": v(-72, -34.4) * mm, "end": v(-71.9, -34.39) * mm});
            skLineSegment(sketch, "E4170", {"start": v(-71.9, -34.39) * mm, "end": v(-71.81, -34.37) * mm});
            skLineSegment(sketch, "E4171", {"start": v(-71.81, -34.37) * mm, "end": v(-71.73, -34.35) * mm});
            skLineSegment(sketch, "E4172", {"start": v(-71.73, -34.35) * mm, "end": v(-71.64, -34.33) * mm});
            skLineSegment(sketch, "E4173", {"start": v(-71.64, -34.33) * mm, "end": v(-71.55, -34.31) * mm});
            skLineSegment(sketch, "E4174", {"start": v(-71.55, -34.31) * mm, "end": v(-71.47, -34.3) * mm});
            skLineSegment(sketch, "E4175", {"start": v(-71.47, -34.3) * mm, "end": v(-71.38, -34.27) * mm});
            skLineSegment(sketch, "E4176", {"start": v(-71.38, -34.27) * mm, "end": v(-71.3, -34.25) * mm});
            skLineSegment(sketch, "E4177", {"start": v(-71.3, -34.25) * mm, "end": v(-71.22, -34.23) * mm});
            skLineSegment(sketch, "E4178", {"start": v(-71.22, -34.23) * mm, "end": v(-71.14, -34.21) * mm});
            skLineSegment(sketch, "E4179", {"start": v(-71.14, -34.21) * mm, "end": v(-71.06, -34.2) * mm});
            skLineSegment(sketch, "E4180", {"start": v(-71.06, -34.2) * mm, "end": v(-70.98, -34.17) * mm});
            skLineSegment(sketch, "E4181", {"start": v(-70.98, -34.17) * mm, "end": v(-70.9, -34.15) * mm});
            skLineSegment(sketch, "E4182", {"start": v(-70.9, -34.15) * mm, "end": v(-70.83, -34.13) * mm});
            skLineSegment(sketch, "E4183", {"start": v(-70.83, -34.13) * mm, "end": v(-70.76, -34.11) * mm});
            skLineSegment(sketch, "E4184", {"start": v(-70.76, -34.11) * mm, "end": v(-70.69, -34.09) * mm});
            skLineSegment(sketch, "E4185", {"start": v(-70.69, -34.09) * mm, "end": v(-70.62, -34.07) * mm});
            skLineSegment(sketch, "E4186", {"start": v(-70.62, -34.07) * mm, "end": v(-70.55, -34.05) * mm});
            skLineSegment(sketch, "E4187", {"start": v(-70.55, -34.05) * mm, "end": v(-70.48, -34.03) * mm});
            skLineSegment(sketch, "E4188", {"start": v(-70.48, -34.03) * mm, "end": v(-70.41, -34) * mm});
            skLineSegment(sketch, "E4189", {"start": v(-70.41, -34) * mm, "end": v(-70.34, -33.99) * mm});
            skLineSegment(sketch, "E4190", {"start": v(-70.34, -33.99) * mm, "end": v(-70.28, -33.97) * mm});
            skLineSegment(sketch, "E4191", {"start": v(-70.28, -33.97) * mm, "end": v(-70.22, -33.95) * mm});
            skLineSegment(sketch, "E4192", {"start": v(-70.22, -33.95) * mm, "end": v(-70.15, -33.93) * mm});
            skLineSegment(sketch, "E4193", {"start": v(-70.15, -33.93) * mm, "end": v(-70.1, -33.9) * mm});
            skLineSegment(sketch, "E4194", {"start": v(-70.1, -33.9) * mm, "end": v(-70.03, -33.89) * mm});
            skLineSegment(sketch, "E4195", {"start": v(-70.03, -33.89) * mm, "end": v(-69.97, -33.87) * mm});
            skLineSegment(sketch, "E4196", {"start": v(-69.97, -33.87) * mm, "end": v(-69.92, -33.85) * mm});
            skLineSegment(sketch, "E4197", {"start": v(-69.92, -33.85) * mm, "end": v(-69.86, -33.83) * mm});
            skLineSegment(sketch, "E4198", {"start": v(-69.86, -33.83) * mm, "end": v(-69.72, -34.02) * mm});
            skLineSegment(sketch, "E4199", {"start": v(-69.72, -34.02) * mm, "end": v(-69.27, -34.68) * mm});
            skLineSegment(sketch, "E4200", {"start": v(-69.27, -34.68) * mm, "end": v(-69.15, -34.88) * mm});
            skLineSegment(sketch, "E4201", {"start": v(-69.15, -34.88) * mm, "end": v(-69.19, -34.93) * mm});
            skLineSegment(sketch, "E4202", {"start": v(-69.19, -34.93) * mm, "end": v(-69.23, -34.97) * mm});
            skLineSegment(sketch, "E4203", {"start": v(-69.23, -34.97) * mm, "end": v(-69.27, -35.02) * mm});
            skLineSegment(sketch, "E4204", {"start": v(-69.27, -35.02) * mm, "end": v(-69.3, -35.07) * mm});
            skLineSegment(sketch, "E4205", {"start": v(-69.3, -35.07) * mm, "end": v(-69.35, -35.12) * mm});
            skLineSegment(sketch, "E4206", {"start": v(-69.35, -35.12) * mm, "end": v(-69.4, -35.17) * mm});
            skLineSegment(sketch, "E4207", {"start": v(-69.4, -35.17) * mm, "end": v(-69.43, -35.22) * mm});
            skLineSegment(sketch, "E4208", {"start": v(-69.43, -35.22) * mm, "end": v(-69.48, -35.27) * mm});
            skLineSegment(sketch, "E4209", {"start": v(-69.48, -35.27) * mm, "end": v(-69.52, -35.32) * mm});
            skLineSegment(sketch, "E4210", {"start": v(-69.52, -35.32) * mm, "end": v(-69.56, -35.38) * mm});
            skLineSegment(sketch, "E4211", {"start": v(-69.56, -35.38) * mm, "end": v(-69.6, -35.43) * mm});
            skLineSegment(sketch, "E4212", {"start": v(-69.6, -35.43) * mm, "end": v(-69.65, -35.5) * mm});
            skLineSegment(sketch, "E4213", {"start": v(-69.65, -35.5) * mm, "end": v(-69.7, -35.55) * mm});
            skLineSegment(sketch, "E4214", {"start": v(-69.7, -35.55) * mm, "end": v(-69.74, -35.6) * mm});
            skLineSegment(sketch, "E4215", {"start": v(-69.74, -35.6) * mm, "end": v(-69.79, -35.67) * mm});
            skLineSegment(sketch, "E4216", {"start": v(-69.79, -35.67) * mm, "end": v(-69.84, -35.73) * mm});
            skLineSegment(sketch, "E4217", {"start": v(-69.84, -35.73) * mm, "end": v(-69.88, -35.8) * mm});
            skLineSegment(sketch, "E4218", {"start": v(-69.88, -35.8) * mm, "end": v(-69.93, -35.86) * mm});
            skLineSegment(sketch, "E4219", {"start": v(-69.93, -35.86) * mm, "end": v(-69.98, -35.93) * mm});
            skLineSegment(sketch, "E4220", {"start": v(-69.98, -35.93) * mm, "end": v(-70.03, -36) * mm});
            skLineSegment(sketch, "E4221", {"start": v(-70.03, -36) * mm, "end": v(-70.08, -36.06) * mm});
            skLineSegment(sketch, "E4222", {"start": v(-70.08, -36.06) * mm, "end": v(-70.12, -36.13) * mm});
            skLineSegment(sketch, "E4223", {"start": v(-70.12, -36.13) * mm, "end": v(-70.17, -36.2) * mm});
            skLineSegment(sketch, "E4224", {"start": v(-70.17, -36.2) * mm, "end": v(-70.22, -36.27) * mm});
            skLineSegment(sketch, "E4225", {"start": v(-70.22, -36.27) * mm, "end": v(-70.27, -36.34) * mm});
            skLineSegment(sketch, "E4226", {"start": v(-70.27, -36.34) * mm, "end": v(-70.32, -36.42) * mm});
            skLineSegment(sketch, "E4227", {"start": v(-70.32, -36.42) * mm, "end": v(-70.37, -36.5) * mm});
            skLineSegment(sketch, "E4228", {"start": v(-70.37, -36.5) * mm, "end": v(-70.42, -36.57) * mm});
            skLineSegment(sketch, "E4229", {"start": v(-70.42, -36.57) * mm, "end": v(-70.48, -36.65) * mm});
            skLineSegment(sketch, "E4230", {"start": v(-70.48, -36.65) * mm, "end": v(-70.53, -36.73) * mm});
            skLineSegment(sketch, "E4231", {"start": v(-70.53, -36.73) * mm, "end": v(-70.58, -36.8) * mm});
            skLineSegment(sketch, "E4232", {"start": v(-70.58, -36.8) * mm, "end": v(-70.63, -36.89) * mm});
            skLineSegment(sketch, "E4233", {"start": v(-70.63, -36.89) * mm, "end": v(-70.68, -36.97) * mm});
            skLineSegment(sketch, "E4234", {"start": v(-70.68, -36.97) * mm, "end": v(-70.74, -37.06) * mm});
            skLineSegment(sketch, "E4235", {"start": v(-70.74, -37.06) * mm, "end": v(-70.79, -37.14) * mm});
            skLineSegment(sketch, "E4236", {"start": v(-70.79, -37.14) * mm, "end": v(-70.84, -37.23) * mm});
            skLineSegment(sketch, "E4237", {"start": v(-70.84, -37.23) * mm, "end": v(-70.9, -37.32) * mm});
            skLineSegment(sketch, "E4238", {"start": v(-70.9, -37.32) * mm, "end": v(-70.95, -37.4) * mm});
            skLineSegment(sketch, "E4239", {"start": v(-70.95, -37.4) * mm, "end": v(-71, -37.5) * mm});
            skLineSegment(sketch, "E4240", {"start": v(-71, -37.5) * mm, "end": v(-71.05, -37.59) * mm});
            skLineSegment(sketch, "E4241", {"start": v(-71.05, -37.59) * mm, "end": v(-71.05, -37.64) * mm});
            skLineSegment(sketch, "E4242", {"start": v(-71.05, -37.64) * mm, "end": v(-70.43, -38.47) * mm});
            skLineSegment(sketch, "E4243", {"start": v(-70.43, -38.47) * mm, "end": v(-70.38, -38.5) * mm});
            skLineSegment(sketch, "E4244", {"start": v(-70.38, -38.5) * mm, "end": v(-70.28, -38.47) * mm});
            skLineSegment(sketch, "E4245", {"start": v(-70.28, -38.47) * mm, "end": v(-70.17, -38.44) * mm});
            skLineSegment(sketch, "E4246", {"start": v(-70.17, -38.44) * mm, "end": v(-70.07, -38.42) * mm});
            skLineSegment(sketch, "E4247", {"start": v(-70.07, -38.42) * mm, "end": v(-69.97, -38.4) * mm});
            skLineSegment(sketch, "E4248", {"start": v(-69.97, -38.4) * mm, "end": v(-69.87, -38.37) * mm});
            skLineSegment(sketch, "E4249", {"start": v(-69.87, -38.37) * mm, "end": v(-69.78, -38.34) * mm});
            skLineSegment(sketch, "E4250", {"start": v(-69.78, -38.34) * mm, "end": v(-69.68, -38.31) * mm});
            skLineSegment(sketch, "E4251", {"start": v(-69.68, -38.31) * mm, "end": v(-69.59, -38.29) * mm});
            skLineSegment(sketch, "E4252", {"start": v(-69.59, -38.29) * mm, "end": v(-69.5, -38.26) * mm});
            skLineSegment(sketch, "E4253", {"start": v(-69.5, -38.26) * mm, "end": v(-69.4, -38.24) * mm});
            skLineSegment(sketch, "E4254", {"start": v(-69.4, -38.24) * mm, "end": v(-69.31, -38.2) * mm});
            skLineSegment(sketch, "E4255", {"start": v(-69.31, -38.2) * mm, "end": v(-69.22, -38.18) * mm});
            skLineSegment(sketch, "E4256", {"start": v(-69.22, -38.18) * mm, "end": v(-69.14, -38.16) * mm});
            skLineSegment(sketch, "E4257", {"start": v(-69.14, -38.16) * mm, "end": v(-69.05, -38.13) * mm});
            skLineSegment(sketch, "E4258", {"start": v(-69.05, -38.13) * mm, "end": v(-68.96, -38.1) * mm});
            skLineSegment(sketch, "E4259", {"start": v(-68.96, -38.1) * mm, "end": v(-68.88, -38.08) * mm});
            skLineSegment(sketch, "E4260", {"start": v(-68.88, -38.08) * mm, "end": v(-68.8, -38.05) * mm});
            skLineSegment(sketch, "E4261", {"start": v(-68.8, -38.05) * mm, "end": v(-68.71, -38.02) * mm});
            skLineSegment(sketch, "E4262", {"start": v(-68.71, -38.02) * mm, "end": v(-68.63, -38) * mm});
            skLineSegment(sketch, "E4263", {"start": v(-68.63, -38) * mm, "end": v(-68.56, -37.97) * mm});
            skLineSegment(sketch, "E4264", {"start": v(-68.56, -37.97) * mm, "end": v(-68.48, -37.94) * mm});
            skLineSegment(sketch, "E4265", {"start": v(-68.48, -37.94) * mm, "end": v(-68.4, -37.91) * mm});
            skLineSegment(sketch, "E4266", {"start": v(-68.4, -37.91) * mm, "end": v(-68.33, -37.88) * mm});
            skLineSegment(sketch, "E4267", {"start": v(-68.33, -37.88) * mm, "end": v(-68.25, -37.86) * mm});
            skLineSegment(sketch, "E4268", {"start": v(-68.25, -37.86) * mm, "end": v(-68.18, -37.83) * mm});
            skLineSegment(sketch, "E4269", {"start": v(-68.18, -37.83) * mm, "end": v(-68.1, -37.8) * mm});
            skLineSegment(sketch, "E4270", {"start": v(-68.1, -37.8) * mm, "end": v(-68.04, -37.78) * mm});
            skLineSegment(sketch, "E4271", {"start": v(-68.04, -37.78) * mm, "end": v(-67.97, -37.75) * mm});
            skLineSegment(sketch, "E4272", {"start": v(-67.97, -37.75) * mm, "end": v(-67.9, -37.72) * mm});
            skLineSegment(sketch, "E4273", {"start": v(-67.9, -37.72) * mm, "end": v(-67.83, -37.7) * mm});
            skLineSegment(sketch, "E4274", {"start": v(-67.83, -37.7) * mm, "end": v(-67.77, -37.67) * mm});
            skLineSegment(sketch, "E4275", {"start": v(-67.77, -37.67) * mm, "end": v(-67.7, -37.64) * mm});
            skLineSegment(sketch, "E4276", {"start": v(-67.7, -37.64) * mm, "end": v(-67.64, -37.62) * mm});
            skLineSegment(sketch, "E4277", {"start": v(-67.64, -37.62) * mm, "end": v(-67.58, -37.6) * mm});
            skLineSegment(sketch, "E4278", {"start": v(-67.58, -37.6) * mm, "end": v(-67.52, -37.57) * mm});
            skLineSegment(sketch, "E4279", {"start": v(-67.52, -37.57) * mm, "end": v(-67.46, -37.54) * mm});
            skLineSegment(sketch, "E4280", {"start": v(-67.46, -37.54) * mm, "end": v(-67.4, -37.51) * mm});
            skLineSegment(sketch, "E4281", {"start": v(-67.4, -37.51) * mm, "end": v(-67.35, -37.5) * mm});
            skLineSegment(sketch, "E4282", {"start": v(-67.35, -37.5) * mm, "end": v(-67.3, -37.46) * mm});
            skLineSegment(sketch, "E4283", {"start": v(-67.3, -37.46) * mm, "end": v(-67.24, -37.44) * mm});
            skLineSegment(sketch, "E4284", {"start": v(-67.24, -37.44) * mm, "end": v(-67.08, -37.62) * mm});
            skLineSegment(sketch, "E4285", {"start": v(-67.08, -37.62) * mm, "end": v(-66.57, -38.24) * mm});
            skLineSegment(sketch, "E4286", {"start": v(-66.57, -38.24) * mm, "end": v(-66.43, -38.43) * mm});
            skLineSegment(sketch, "E4287", {"start": v(-66.43, -38.43) * mm, "end": v(-66.47, -38.47) * mm});
            skLineSegment(sketch, "E4288", {"start": v(-66.47, -38.47) * mm, "end": v(-66.5, -38.52) * mm});
            skLineSegment(sketch, "E4289", {"start": v(-66.5, -38.52) * mm, "end": v(-66.54, -38.57) * mm});
            skLineSegment(sketch, "E4290", {"start": v(-66.54, -38.57) * mm, "end": v(-66.58, -38.63) * mm});
            skLineSegment(sketch, "E4291", {"start": v(-66.58, -38.63) * mm, "end": v(-66.61, -38.68) * mm});
            skLineSegment(sketch, "E4292", {"start": v(-66.61, -38.68) * mm, "end": v(-66.65, -38.73) * mm});
            skLineSegment(sketch, "E4293", {"start": v(-66.65, -38.73) * mm, "end": v(-66.69, -38.79) * mm});
            skLineSegment(sketch, "E4294", {"start": v(-66.69, -38.79) * mm, "end": v(-66.72, -38.84) * mm});
            skLineSegment(sketch, "E4295", {"start": v(-66.72, -38.84) * mm, "end": v(-66.76, -38.9) * mm});
            skLineSegment(sketch, "E4296", {"start": v(-66.76, -38.9) * mm, "end": v(-66.8, -38.96) * mm});
            skLineSegment(sketch, "E4297", {"start": v(-66.8, -38.96) * mm, "end": v(-66.84, -39.02) * mm});
            skLineSegment(sketch, "E4298", {"start": v(-66.84, -39.02) * mm, "end": v(-66.88, -39.08) * mm});
            skLineSegment(sketch, "E4299", {"start": v(-66.88, -39.08) * mm, "end": v(-66.92, -39.14) * mm});
            skLineSegment(sketch, "E4300", {"start": v(-66.92, -39.14) * mm, "end": v(-66.96, -39.2) * mm});
            skLineSegment(sketch, "E4301", {"start": v(-66.96, -39.2) * mm, "end": v(-67, -39.27) * mm});
            skLineSegment(sketch, "E4302", {"start": v(-67, -39.27) * mm, "end": v(-67.04, -39.34) * mm});
            skLineSegment(sketch, "E4303", {"start": v(-67.04, -39.34) * mm, "end": v(-67.08, -39.4) * mm});
            skLineSegment(sketch, "E4304", {"start": v(-67.08, -39.4) * mm, "end": v(-67.13, -39.47) * mm});
            skLineSegment(sketch, "E4305", {"start": v(-67.13, -39.47) * mm, "end": v(-67.17, -39.54) * mm});
            skLineSegment(sketch, "E4306", {"start": v(-67.17, -39.54) * mm, "end": v(-67.2, -39.61) * mm});
            skLineSegment(sketch, "E4307", {"start": v(-67.2, -39.61) * mm, "end": v(-67.25, -39.68) * mm});
            skLineSegment(sketch, "E4308", {"start": v(-67.25, -39.68) * mm, "end": v(-67.3, -39.76) * mm});
            skLineSegment(sketch, "E4309", {"start": v(-67.3, -39.76) * mm, "end": v(-67.34, -39.83) * mm});
            skLineSegment(sketch, "E4310", {"start": v(-67.34, -39.83) * mm, "end": v(-67.38, -39.9) * mm});
            skLineSegment(sketch, "E4311", {"start": v(-67.38, -39.9) * mm, "end": v(-67.42, -39.99) * mm});
            skLineSegment(sketch, "E4312", {"start": v(-67.42, -39.99) * mm, "end": v(-67.47, -40.06) * mm});
            skLineSegment(sketch, "E4313", {"start": v(-67.47, -40.06) * mm, "end": v(-67.51, -40.14) * mm});
            skLineSegment(sketch, "E4314", {"start": v(-67.51, -40.14) * mm, "end": v(-67.55, -40.22) * mm});
            skLineSegment(sketch, "E4315", {"start": v(-67.55, -40.22) * mm, "end": v(-67.6, -40.3) * mm});
            skLineSegment(sketch, "E4316", {"start": v(-67.6, -40.3) * mm, "end": v(-67.64, -40.39) * mm});
            skLineSegment(sketch, "E4317", {"start": v(-67.64, -40.39) * mm, "end": v(-67.69, -40.47) * mm});
            skLineSegment(sketch, "E4318", {"start": v(-67.69, -40.47) * mm, "end": v(-67.73, -40.56) * mm});
            skLineSegment(sketch, "E4319", {"start": v(-67.73, -40.56) * mm, "end": v(-67.77, -40.65) * mm});
            skLineSegment(sketch, "E4320", {"start": v(-67.77, -40.65) * mm, "end": v(-67.82, -40.74) * mm});
            skLineSegment(sketch, "E4321", {"start": v(-67.82, -40.74) * mm, "end": v(-67.86, -40.83) * mm});
            skLineSegment(sketch, "E4322", {"start": v(-67.86, -40.83) * mm, "end": v(-67.9, -40.92) * mm});
            skLineSegment(sketch, "E4323", {"start": v(-67.9, -40.92) * mm, "end": v(-67.95, -41) * mm});
            skLineSegment(sketch, "E4324", {"start": v(-67.95, -41) * mm, "end": v(-68, -41.1) * mm});
            skLineSegment(sketch, "E4325", {"start": v(-68, -41.1) * mm, "end": v(-68.04, -41.2) * mm});
            skLineSegment(sketch, "E4326", {"start": v(-68.04, -41.2) * mm, "end": v(-68.09, -41.3) * mm});
            skLineSegment(sketch, "E4327", {"start": v(-68.09, -41.3) * mm, "end": v(-68.08, -41.35) * mm});
            skLineSegment(sketch, "E4328", {"start": v(-68.08, -41.35) * mm, "end": v(-67.38, -42.12) * mm});
            skLineSegment(sketch, "E4329", {"start": v(-67.38, -42.12) * mm, "end": v(-67.34, -42.14) * mm});
            skLineSegment(sketch, "E4330", {"start": v(-67.34, -42.14) * mm, "end": v(-67.24, -42.1) * mm});
            skLineSegment(sketch, "E4331", {"start": v(-67.24, -42.1) * mm, "end": v(-67.14, -42.07) * mm});
            skLineSegment(sketch, "E4332", {"start": v(-67.14, -42.07) * mm, "end": v(-67.04, -42.03) * mm});
            skLineSegment(sketch, "E4333", {"start": v(-67.04, -42.03) * mm, "end": v(-66.94, -42) * mm});
            skLineSegment(sketch, "E4334", {"start": v(-66.94, -42) * mm, "end": v(-66.85, -41.96) * mm});
            skLineSegment(sketch, "E4335", {"start": v(-66.85, -41.96) * mm, "end": v(-66.75, -41.93) * mm});
            skLineSegment(sketch, "E4336", {"start": v(-66.75, -41.93) * mm, "end": v(-66.66, -41.9) * mm});
            skLineSegment(sketch, "E4337", {"start": v(-66.66, -41.9) * mm, "end": v(-66.57, -41.86) * mm});
            skLineSegment(sketch, "E4338", {"start": v(-66.57, -41.86) * mm, "end": v(-66.48, -41.83) * mm});
            skLineSegment(sketch, "E4339", {"start": v(-66.48, -41.83) * mm, "end": v(-66.39, -41.8) * mm});
            skLineSegment(sketch, "E4340", {"start": v(-66.39, -41.8) * mm, "end": v(-66.3, -41.76) * mm});
            skLineSegment(sketch, "E4341", {"start": v(-66.3, -41.76) * mm, "end": v(-66.21, -41.72) * mm});
            skLineSegment(sketch, "E4342", {"start": v(-66.21, -41.72) * mm, "end": v(-66.13, -41.69) * mm});
            skLineSegment(sketch, "E4343", {"start": v(-66.13, -41.69) * mm, "end": v(-66.04, -41.65) * mm});
            skLineSegment(sketch, "E4344", {"start": v(-66.04, -41.65) * mm, "end": v(-65.96, -41.62) * mm});
            skLineSegment(sketch, "E4345", {"start": v(-65.96, -41.62) * mm, "end": v(-65.88, -41.58) * mm});
            skLineSegment(sketch, "E4346", {"start": v(-65.88, -41.58) * mm, "end": v(-65.8, -41.55) * mm});
            skLineSegment(sketch, "E4347", {"start": v(-65.8, -41.55) * mm, "end": v(-65.72, -41.52) * mm});
            skLineSegment(sketch, "E4348", {"start": v(-65.72, -41.52) * mm, "end": v(-65.64, -41.48) * mm});
            skLineSegment(sketch, "E4349", {"start": v(-65.64, -41.48) * mm, "end": v(-65.57, -41.45) * mm});
            skLineSegment(sketch, "E4350", {"start": v(-65.57, -41.45) * mm, "end": v(-65.5, -41.41) * mm});
            skLineSegment(sketch, "E4351", {"start": v(-65.5, -41.41) * mm, "end": v(-65.42, -41.38) * mm});
            skLineSegment(sketch, "E4352", {"start": v(-65.42, -41.38) * mm, "end": v(-65.35, -41.35) * mm});
            skLineSegment(sketch, "E4353", {"start": v(-65.35, -41.35) * mm, "end": v(-65.27, -41.31) * mm});
            skLineSegment(sketch, "E4354", {"start": v(-65.27, -41.31) * mm, "end": v(-65.2, -41.28) * mm});
            skLineSegment(sketch, "E4355", {"start": v(-65.2, -41.28) * mm, "end": v(-65.14, -41.25) * mm});
            skLineSegment(sketch, "E4356", {"start": v(-65.14, -41.25) * mm, "end": v(-65.07, -41.21) * mm});
            skLineSegment(sketch, "E4357", {"start": v(-65.07, -41.21) * mm, "end": v(-65, -41.18) * mm});
            skLineSegment(sketch, "E4358", {"start": v(-65, -41.18) * mm, "end": v(-64.94, -41.15) * mm});
            skLineSegment(sketch, "E4359", {"start": v(-64.94, -41.15) * mm, "end": v(-64.87, -41.11) * mm});
            skLineSegment(sketch, "E4360", {"start": v(-64.87, -41.11) * mm, "end": v(-64.81, -41.08) * mm});
            skLineSegment(sketch, "E4361", {"start": v(-64.81, -41.08) * mm, "end": v(-64.75, -41.05) * mm});
            skLineSegment(sketch, "E4362", {"start": v(-64.75, -41.05) * mm, "end": v(-64.69, -41.02) * mm});
            skLineSegment(sketch, "E4363", {"start": v(-64.69, -41.02) * mm, "end": v(-64.63, -40.99) * mm});
            skLineSegment(sketch, "E4364", {"start": v(-64.63, -40.99) * mm, "end": v(-64.57, -40.96) * mm});
            skLineSegment(sketch, "E4365", {"start": v(-64.57, -40.96) * mm, "end": v(-64.52, -40.92) * mm});
            skLineSegment(sketch, "E4366", {"start": v(-64.52, -40.92) * mm, "end": v(-64.46, -40.9) * mm});
            skLineSegment(sketch, "E4367", {"start": v(-64.46, -40.9) * mm, "end": v(-64.4, -40.86) * mm});
            skLineSegment(sketch, "E4368", {"start": v(-64.4, -40.86) * mm, "end": v(-64.35, -40.83) * mm});
            skLineSegment(sketch, "E4369", {"start": v(-64.35, -40.83) * mm, "end": v(-64.3, -40.8) * mm});
            skLineSegment(sketch, "E4370", {"start": v(-64.3, -40.8) * mm, "end": v(-64.13, -40.97) * mm});
            skLineSegment(sketch, "E4371", {"start": v(-64.13, -40.97) * mm, "end": v(-63.57, -41.54) * mm});
            skLineSegment(sketch, "E4372", {"start": v(-63.57, -41.54) * mm, "end": v(-63.41, -41.71) * mm});
            skLineSegment(sketch, "E4373", {"start": v(-63.41, -41.71) * mm, "end": v(-63.44, -41.77) * mm});
            skLineSegment(sketch, "E4374", {"start": v(-63.44, -41.77) * mm, "end": v(-63.47, -41.82) * mm});
            skLineSegment(sketch, "E4375", {"start": v(-63.47, -41.82) * mm, "end": v(-63.5, -41.87) * mm});
            skLineSegment(sketch, "E4376", {"start": v(-63.5, -41.87) * mm, "end": v(-63.54, -41.93) * mm});
            skLineSegment(sketch, "E4377", {"start": v(-63.54, -41.93) * mm, "end": v(-63.57, -41.98) * mm});
            skLineSegment(sketch, "E4378", {"start": v(-63.57, -41.98) * mm, "end": v(-63.6, -42.04) * mm});
            skLineSegment(sketch, "E4379", {"start": v(-63.6, -42.04) * mm, "end": v(-63.63, -42.1) * mm});
            skLineSegment(sketch, "E4380", {"start": v(-63.63, -42.1) * mm, "end": v(-63.67, -42.16) * mm});
            skLineSegment(sketch, "E4381", {"start": v(-63.67, -42.16) * mm, "end": v(-63.7, -42.22) * mm});
            skLineSegment(sketch, "E4382", {"start": v(-63.7, -42.22) * mm, "end": v(-63.73, -42.28) * mm});
            skLineSegment(sketch, "E4383", {"start": v(-63.73, -42.28) * mm, "end": v(-63.77, -42.34) * mm});
            skLineSegment(sketch, "E4384", {"start": v(-63.77, -42.34) * mm, "end": v(-63.8, -42.4) * mm});
            skLineSegment(sketch, "E4385", {"start": v(-63.8, -42.4) * mm, "end": v(-63.83, -42.47) * mm});
            skLineSegment(sketch, "E4386", {"start": v(-63.83, -42.47) * mm, "end": v(-63.87, -42.54) * mm});
            skLineSegment(sketch, "E4387", {"start": v(-63.87, -42.54) * mm, "end": v(-63.9, -42.6) * mm});
            skLineSegment(sketch, "E4388", {"start": v(-63.9, -42.6) * mm, "end": v(-63.94, -42.68) * mm});
            skLineSegment(sketch, "E4389", {"start": v(-63.94, -42.68) * mm, "end": v(-63.97, -42.75) * mm});
            skLineSegment(sketch, "E4390", {"start": v(-63.97, -42.75) * mm, "end": v(-64, -42.82) * mm});
            skLineSegment(sketch, "E4391", {"start": v(-64, -42.82) * mm, "end": v(-64.04, -42.9) * mm});
            skLineSegment(sketch, "E4392", {"start": v(-64.04, -42.9) * mm, "end": v(-64.08, -42.97) * mm});
            skLineSegment(sketch, "E4393", {"start": v(-64.08, -42.97) * mm, "end": v(-64.11, -43.04) * mm});
            skLineSegment(sketch, "E4394", {"start": v(-64.11, -43.04) * mm, "end": v(-64.15, -43.12) * mm});
            skLineSegment(sketch, "E4395", {"start": v(-64.15, -43.12) * mm, "end": v(-64.19, -43.2) * mm});
            skLineSegment(sketch, "E4396", {"start": v(-64.19, -43.2) * mm, "end": v(-64.22, -43.28) * mm});
            skLineSegment(sketch, "E4397", {"start": v(-64.22, -43.28) * mm, "end": v(-64.26, -43.36) * mm});
            skLineSegment(sketch, "E4398", {"start": v(-64.26, -43.36) * mm, "end": v(-64.3, -43.44) * mm});
            skLineSegment(sketch, "E4399", {"start": v(-64.3, -43.44) * mm, "end": v(-64.33, -43.52) * mm});
            skLineSegment(sketch, "E4400", {"start": v(-64.33, -43.52) * mm, "end": v(-64.37, -43.6) * mm});
            skLineSegment(sketch, "E4401", {"start": v(-64.37, -43.6) * mm, "end": v(-64.4, -43.7) * mm});
            skLineSegment(sketch, "E4402", {"start": v(-64.4, -43.7) * mm, "end": v(-64.44, -43.78) * mm});
            skLineSegment(sketch, "E4403", {"start": v(-64.44, -43.78) * mm, "end": v(-64.48, -43.87) * mm});
            skLineSegment(sketch, "E4404", {"start": v(-64.48, -43.87) * mm, "end": v(-64.51, -43.96) * mm});
            skLineSegment(sketch, "E4405", {"start": v(-64.51, -43.96) * mm, "end": v(-64.55, -44.05) * mm});
            skLineSegment(sketch, "E4406", {"start": v(-64.55, -44.05) * mm, "end": v(-64.59, -44.14) * mm});
            skLineSegment(sketch, "E4407", {"start": v(-64.59, -44.14) * mm, "end": v(-64.62, -44.23) * mm});
            skLineSegment(sketch, "E4408", {"start": v(-64.62, -44.23) * mm, "end": v(-64.66, -44.33) * mm});
            skLineSegment(sketch, "E4409", {"start": v(-64.66, -44.33) * mm, "end": v(-64.7, -44.42) * mm});
            skLineSegment(sketch, "E4410", {"start": v(-64.7, -44.42) * mm, "end": v(-64.73, -44.52) * mm});
            skLineSegment(sketch, "E4411", {"start": v(-64.73, -44.52) * mm, "end": v(-64.77, -44.62) * mm});
            skLineSegment(sketch, "E4412", {"start": v(-64.77, -44.62) * mm, "end": v(-64.8, -44.72) * mm});
            skLineSegment(sketch, "E4413", {"start": v(-64.8, -44.72) * mm, "end": v(-64.79, -44.77) * mm});
            skLineSegment(sketch, "E4414", {"start": v(-64.79, -44.77) * mm, "end": v(-64.03, -45.48) * mm});
            skLineSegment(sketch, "E4415", {"start": v(-64.03, -45.48) * mm, "end": v(-63.98, -45.49) * mm});
            skLineSegment(sketch, "E4416", {"start": v(-63.98, -45.49) * mm, "end": v(-63.88, -45.45) * mm});
            skLineSegment(sketch, "E4417", {"start": v(-63.88, -45.45) * mm, "end": v(-63.79, -45.4) * mm});
            skLineSegment(sketch, "E4418", {"start": v(-63.79, -45.4) * mm, "end": v(-63.7, -45.36) * mm});
            skLineSegment(sketch, "E4419", {"start": v(-63.7, -45.36) * mm, "end": v(-63.6, -45.32) * mm});
            skLineSegment(sketch, "E4420", {"start": v(-63.6, -45.32) * mm, "end": v(-63.5, -45.28) * mm});
            skLineSegment(sketch, "E4421", {"start": v(-63.5, -45.28) * mm, "end": v(-63.41, -45.23) * mm});
            skLineSegment(sketch, "E4422", {"start": v(-63.41, -45.23) * mm, "end": v(-63.32, -45.19) * mm});
            skLineSegment(sketch, "E4423", {"start": v(-63.32, -45.19) * mm, "end": v(-63.24, -45.15) * mm});
            skLineSegment(sketch, "E4424", {"start": v(-63.24, -45.15) * mm, "end": v(-63.15, -45.1) * mm});
            skLineSegment(sketch, "E4425", {"start": v(-63.15, -45.1) * mm, "end": v(-63.06, -45.06) * mm});
            skLineSegment(sketch, "E4426", {"start": v(-63.06, -45.06) * mm, "end": v(-62.98, -45.02) * mm});
            skLineSegment(sketch, "E4427", {"start": v(-62.98, -45.02) * mm, "end": v(-62.9, -44.98) * mm});
            skLineSegment(sketch, "E4428", {"start": v(-62.9, -44.98) * mm, "end": v(-62.82, -44.93) * mm});
            skLineSegment(sketch, "E4429", {"start": v(-62.82, -44.93) * mm, "end": v(-62.73, -44.9) * mm});
            skLineSegment(sketch, "E4430", {"start": v(-62.73, -44.9) * mm, "end": v(-62.66, -44.85) * mm});
            skLineSegment(sketch, "E4431", {"start": v(-62.66, -44.85) * mm, "end": v(-62.58, -44.8) * mm});
            skLineSegment(sketch, "E4432", {"start": v(-62.58, -44.8) * mm, "end": v(-62.5, -44.77) * mm});
            skLineSegment(sketch, "E4433", {"start": v(-62.5, -44.77) * mm, "end": v(-62.43, -44.73) * mm});
            skLineSegment(sketch, "E4434", {"start": v(-62.43, -44.73) * mm, "end": v(-62.35, -44.69) * mm});
            skLineSegment(sketch, "E4435", {"start": v(-62.35, -44.69) * mm, "end": v(-62.28, -44.65) * mm});
            skLineSegment(sketch, "E4436", {"start": v(-62.28, -44.65) * mm, "end": v(-62.2, -44.6) * mm});
            skLineSegment(sketch, "E4437", {"start": v(-62.2, -44.6) * mm, "end": v(-62.14, -44.56) * mm});
            skLineSegment(sketch, "E4438", {"start": v(-62.14, -44.56) * mm, "end": v(-62.07, -44.52) * mm});
            skLineSegment(sketch, "E4439", {"start": v(-62.07, -44.52) * mm, "end": v(-62, -44.48) * mm});
            skLineSegment(sketch, "E4440", {"start": v(-62, -44.48) * mm, "end": v(-61.93, -44.45) * mm});
            skLineSegment(sketch, "E4441", {"start": v(-61.93, -44.45) * mm, "end": v(-61.87, -44.4) * mm});
            skLineSegment(sketch, "E4442", {"start": v(-61.87, -44.4) * mm, "end": v(-61.8, -44.37) * mm});
            skLineSegment(sketch, "E4443", {"start": v(-61.8, -44.37) * mm, "end": v(-61.74, -44.33) * mm});
            skLineSegment(sketch, "E4444", {"start": v(-61.74, -44.33) * mm, "end": v(-61.68, -44.3) * mm});
            skLineSegment(sketch, "E4445", {"start": v(-61.68, -44.3) * mm, "end": v(-61.62, -44.25) * mm});
            skLineSegment(sketch, "E4446", {"start": v(-61.62, -44.25) * mm, "end": v(-61.56, -44.21) * mm});
            skLineSegment(sketch, "E4447", {"start": v(-61.56, -44.21) * mm, "end": v(-61.5, -44.18) * mm});
            skLineSegment(sketch, "E4448", {"start": v(-61.5, -44.18) * mm, "end": v(-61.44, -44.14) * mm});
            skLineSegment(sketch, "E4449", {"start": v(-61.44, -44.14) * mm, "end": v(-61.39, -44.1) * mm});
            skLineSegment(sketch, "E4450", {"start": v(-61.39, -44.1) * mm, "end": v(-61.33, -44.07) * mm});
            skLineSegment(sketch, "E4451", {"start": v(-61.33, -44.07) * mm, "end": v(-61.28, -44.03) * mm});
            skLineSegment(sketch, "E4452", {"start": v(-61.28, -44.03) * mm, "end": v(-61.23, -44) * mm});
            skLineSegment(sketch, "E4453", {"start": v(-61.23, -44) * mm, "end": v(-61.18, -43.96) * mm});
            skLineSegment(sketch, "E4454", {"start": v(-61.18, -43.96) * mm, "end": v(-61.13, -43.93) * mm});
            skLineSegment(sketch, "E4455", {"start": v(-61.13, -43.93) * mm, "end": v(-61.08, -43.9) * mm});
            skLineSegment(sketch, "E4456", {"start": v(-61.08, -43.9) * mm, "end": v(-60.9, -44.04) * mm});
            skLineSegment(sketch, "E4457", {"start": v(-60.9, -44.04) * mm, "end": v(-60.28, -44.56) * mm});
            skLineSegment(sketch, "E4458", {"start": v(-60.28, -44.56) * mm, "end": v(-60.1, -44.72) * mm});
            skLineSegment(sketch, "E4459", {"start": v(-60.1, -44.72) * mm, "end": v(-60.13, -44.77) * mm});
            skLineSegment(sketch, "E4460", {"start": v(-60.13, -44.77) * mm, "end": v(-60.16, -44.83) * mm});
            skLineSegment(sketch, "E4461", {"start": v(-60.16, -44.83) * mm, "end": v(-60.19, -44.88) * mm});
            skLineSegment(sketch, "E4462", {"start": v(-60.19, -44.88) * mm, "end": v(-60.21, -44.94) * mm});
            skLineSegment(sketch, "E4463", {"start": v(-60.21, -44.94) * mm, "end": v(-60.24, -45) * mm});
            skLineSegment(sketch, "E4464", {"start": v(-60.24, -45) * mm, "end": v(-60.27, -45.06) * mm});
            skLineSegment(sketch, "E4465", {"start": v(-60.27, -45.06) * mm, "end": v(-60.3, -45.12) * mm});
            skLineSegment(sketch, "E4466", {"start": v(-60.3, -45.12) * mm, "end": v(-60.32, -45.18) * mm});
            skLineSegment(sketch, "E4467", {"start": v(-60.32, -45.18) * mm, "end": v(-60.35, -45.25) * mm});
            skLineSegment(sketch, "E4468", {"start": v(-60.35, -45.25) * mm, "end": v(-60.38, -45.3) * mm});
            skLineSegment(sketch, "E4469", {"start": v(-60.38, -45.3) * mm, "end": v(-60.4, -45.38) * mm});
            skLineSegment(sketch, "E4470", {"start": v(-60.4, -45.38) * mm, "end": v(-60.43, -45.44) * mm});
            skLineSegment(sketch, "E4471", {"start": v(-60.43, -45.44) * mm, "end": v(-60.46, -45.51) * mm});
            skLineSegment(sketch, "E4472", {"start": v(-60.46, -45.51) * mm, "end": v(-60.49, -45.58) * mm});
            skLineSegment(sketch, "E4473", {"start": v(-60.49, -45.58) * mm, "end": v(-60.52, -45.65) * mm});
            skLineSegment(sketch, "E4474", {"start": v(-60.52, -45.65) * mm, "end": v(-60.55, -45.72) * mm});
            skLineSegment(sketch, "E4475", {"start": v(-60.55, -45.72) * mm, "end": v(-60.57, -45.8) * mm});
            skLineSegment(sketch, "E4476", {"start": v(-60.57, -45.8) * mm, "end": v(-60.6, -45.87) * mm});
            skLineSegment(sketch, "E4477", {"start": v(-60.6, -45.87) * mm, "end": v(-60.63, -45.95) * mm});
            skLineSegment(sketch, "E4478", {"start": v(-60.63, -45.95) * mm, "end": v(-60.66, -46.02) * mm});
            skLineSegment(sketch, "E4479", {"start": v(-60.66, -46.02) * mm, "end": v(-60.69, -46.1) * mm});
            skLineSegment(sketch, "E4480", {"start": v(-60.69, -46.1) * mm, "end": v(-60.72, -46.18) * mm});
            skLineSegment(sketch, "E4481", {"start": v(-60.72, -46.18) * mm, "end": v(-60.75, -46.26) * mm});
            skLineSegment(sketch, "E4482", {"start": v(-60.75, -46.26) * mm, "end": v(-60.77, -46.35) * mm});
            skLineSegment(sketch, "E4483", {"start": v(-60.77, -46.35) * mm, "end": v(-60.8, -46.43) * mm});
            skLineSegment(sketch, "E4484", {"start": v(-60.8, -46.43) * mm, "end": v(-60.83, -46.51) * mm});
            skLineSegment(sketch, "E4485", {"start": v(-60.83, -46.51) * mm, "end": v(-60.86, -46.6) * mm});
            skLineSegment(sketch, "E4486", {"start": v(-60.86, -46.6) * mm, "end": v(-60.89, -46.69) * mm});
            skLineSegment(sketch, "E4487", {"start": v(-60.89, -46.69) * mm, "end": v(-60.92, -46.78) * mm});
            skLineSegment(sketch, "E4488", {"start": v(-60.92, -46.78) * mm, "end": v(-60.95, -46.87) * mm});
            skLineSegment(sketch, "E4489", {"start": v(-60.95, -46.87) * mm, "end": v(-60.98, -46.96) * mm});
            skLineSegment(sketch, "E4490", {"start": v(-60.98, -46.96) * mm, "end": v(-61, -47.05) * mm});
            skLineSegment(sketch, "E4491", {"start": v(-61, -47.05) * mm, "end": v(-61.03, -47.14) * mm});
            skLineSegment(sketch, "E4492", {"start": v(-61.03, -47.14) * mm, "end": v(-61.06, -47.24) * mm});
            skLineSegment(sketch, "E4493", {"start": v(-61.06, -47.24) * mm, "end": v(-61.09, -47.34) * mm});
            skLineSegment(sketch, "E4494", {"start": v(-61.09, -47.34) * mm, "end": v(-61.11, -47.43) * mm});
            skLineSegment(sketch, "E4495", {"start": v(-61.11, -47.43) * mm, "end": v(-61.14, -47.53) * mm});
            skLineSegment(sketch, "E4496", {"start": v(-61.14, -47.53) * mm, "end": v(-61.17, -47.63) * mm});
            skLineSegment(sketch, "E4497", {"start": v(-61.17, -47.63) * mm, "end": v(-61.2, -47.73) * mm});
            skLineSegment(sketch, "E4498", {"start": v(-61.2, -47.73) * mm, "end": v(-61.22, -47.84) * mm});
            skLineSegment(sketch, "E4499", {"start": v(-61.22, -47.84) * mm, "end": v(-61.2, -47.88) * mm});
            skLineSegment(sketch, "E4500", {"start": v(-61.2, -47.88) * mm, "end": v(-60.38, -48.52) * mm});
            skLineSegment(sketch, "E4501", {"start": v(-60.38, -48.52) * mm, "end": v(-60.33, -48.53) * mm});
            skLineSegment(sketch, "E4502", {"start": v(-60.33, -48.53) * mm, "end": v(-60.24, -48.48) * mm});
            skLineSegment(sketch, "E4503", {"start": v(-60.24, -48.48) * mm, "end": v(-60.15, -48.43) * mm});
            skLineSegment(sketch, "E4504", {"start": v(-60.15, -48.43) * mm, "end": v(-60.06, -48.38) * mm});
            skLineSegment(sketch, "E4505", {"start": v(-60.06, -48.38) * mm, "end": v(-59.97, -48.32) * mm});
            skLineSegment(sketch, "E4506", {"start": v(-59.97, -48.32) * mm, "end": v(-59.88, -48.27) * mm});
            skLineSegment(sketch, "E4507", {"start": v(-59.88, -48.27) * mm, "end": v(-59.8, -48.22) * mm});
            skLineSegment(sketch, "E4508", {"start": v(-59.8, -48.22) * mm, "end": v(-59.7, -48.17) * mm});
            skLineSegment(sketch, "E4509", {"start": v(-59.7, -48.17) * mm, "end": v(-59.63, -48.12) * mm});
            skLineSegment(sketch, "E4510", {"start": v(-59.63, -48.12) * mm, "end": v(-59.54, -48.07) * mm});
            skLineSegment(sketch, "E4511", {"start": v(-59.54, -48.07) * mm, "end": v(-59.46, -48.02) * mm});
            skLineSegment(sketch, "E4512", {"start": v(-59.46, -48.02) * mm, "end": v(-59.38, -47.97) * mm});
            skLineSegment(sketch, "E4513", {"start": v(-59.38, -47.97) * mm, "end": v(-59.3, -47.92) * mm});
            skLineSegment(sketch, "E4514", {"start": v(-59.3, -47.92) * mm, "end": v(-59.22, -47.87) * mm});
            skLineSegment(sketch, "E4515", {"start": v(-59.22, -47.87) * mm, "end": v(-59.15, -47.82) * mm});
            skLineSegment(sketch, "E4516", {"start": v(-59.15, -47.82) * mm, "end": v(-59.07, -47.78) * mm});
            skLineSegment(sketch, "E4517", {"start": v(-59.07, -47.78) * mm, "end": v(-59, -47.73) * mm});
            skLineSegment(sketch, "E4518", {"start": v(-59, -47.73) * mm, "end": v(-58.93, -47.68) * mm});
            skLineSegment(sketch, "E4519", {"start": v(-58.93, -47.68) * mm, "end": v(-58.86, -47.63) * mm});
            skLineSegment(sketch, "E4520", {"start": v(-58.86, -47.63) * mm, "end": v(-58.79, -47.58) * mm});
            skLineSegment(sketch, "E4521", {"start": v(-58.79, -47.58) * mm, "end": v(-58.72, -47.54) * mm});
            skLineSegment(sketch, "E4522", {"start": v(-58.72, -47.54) * mm, "end": v(-58.65, -47.49) * mm});
            skLineSegment(sketch, "E4523", {"start": v(-58.65, -47.49) * mm, "end": v(-58.58, -47.44) * mm});
            skLineSegment(sketch, "E4524", {"start": v(-58.58, -47.44) * mm, "end": v(-58.52, -47.4) * mm});
            skLineSegment(sketch, "E4525", {"start": v(-58.52, -47.4) * mm, "end": v(-58.45, -47.35) * mm});
            skLineSegment(sketch, "E4526", {"start": v(-58.45, -47.35) * mm, "end": v(-58.39, -47.3) * mm});
            skLineSegment(sketch, "E4527", {"start": v(-58.39, -47.3) * mm, "end": v(-58.33, -47.26) * mm});
            skLineSegment(sketch, "E4528", {"start": v(-58.33, -47.26) * mm, "end": v(-58.27, -47.22) * mm});
            skLineSegment(sketch, "E4529", {"start": v(-58.27, -47.22) * mm, "end": v(-58.2, -47.17) * mm});
            skLineSegment(sketch, "E4530", {"start": v(-58.2, -47.17) * mm, "end": v(-58.15, -47.13) * mm});
            skLineSegment(sketch, "E4531", {"start": v(-58.15, -47.13) * mm, "end": v(-58.1, -47.08) * mm});
            skLineSegment(sketch, "E4532", {"start": v(-58.1, -47.08) * mm, "end": v(-58.04, -47.04) * mm});
            skLineSegment(sketch, "E4533", {"start": v(-58.04, -47.04) * mm, "end": v(-57.98, -47) * mm});
            skLineSegment(sketch, "E4534", {"start": v(-57.98, -47) * mm, "end": v(-57.93, -46.96) * mm});
            skLineSegment(sketch, "E4535", {"start": v(-57.93, -46.96) * mm, "end": v(-57.88, -46.92) * mm});
            skLineSegment(sketch, "E4536", {"start": v(-57.88, -46.92) * mm, "end": v(-57.83, -46.88) * mm});
            skLineSegment(sketch, "E4537", {"start": v(-57.83, -46.88) * mm, "end": v(-57.78, -46.84) * mm});
            skLineSegment(sketch, "E4538", {"start": v(-57.78, -46.84) * mm, "end": v(-57.73, -46.8) * mm});
            skLineSegment(sketch, "E4539", {"start": v(-57.73, -46.8) * mm, "end": v(-57.68, -46.76) * mm});
            skLineSegment(sketch, "E4540", {"start": v(-57.68, -46.76) * mm, "end": v(-57.63, -46.72) * mm});
            skLineSegment(sketch, "E4541", {"start": v(-57.63, -46.72) * mm, "end": v(-57.59, -46.68) * mm});
            skLineSegment(sketch, "E4542", {"start": v(-57.59, -46.68) * mm, "end": v(-57.4, -46.8) * mm});
            skLineSegment(sketch, "E4543", {"start": v(-57.4, -46.8) * mm, "end": v(-56.73, -47.27) * mm});
            skLineSegment(sketch, "E4544", {"start": v(-56.73, -47.27) * mm, "end": v(-56.55, -47.41) * mm});
            skLineSegment(sketch, "E4545", {"start": v(-56.55, -47.41) * mm, "end": v(-56.57, -47.47) * mm});
            skLineSegment(sketch, "E4546", {"start": v(-56.57, -47.47) * mm, "end": v(-56.59, -47.53) * mm});
            skLineSegment(sketch, "E4547", {"start": v(-56.59, -47.53) * mm, "end": v(-56.61, -47.59) * mm});
            skLineSegment(sketch, "E4548", {"start": v(-56.61, -47.59) * mm, "end": v(-56.63, -47.64) * mm});
            skLineSegment(sketch, "E4549", {"start": v(-56.63, -47.64) * mm, "end": v(-56.65, -47.7) * mm});
            skLineSegment(sketch, "E4550", {"start": v(-56.65, -47.7) * mm, "end": v(-56.68, -47.77) * mm});
            skLineSegment(sketch, "E4551", {"start": v(-56.68, -47.77) * mm, "end": v(-56.7, -47.83) * mm});
            skLineSegment(sketch, "E4552", {"start": v(-56.7, -47.83) * mm, "end": v(-56.72, -47.9) * mm});
            skLineSegment(sketch, "E4553", {"start": v(-56.72, -47.9) * mm, "end": v(-56.74, -47.96) * mm});
            skLineSegment(sketch, "E4554", {"start": v(-56.74, -47.96) * mm, "end": v(-56.76, -48.03) * mm});
            skLineSegment(sketch, "E4555", {"start": v(-56.76, -48.03) * mm, "end": v(-56.78, -48.1) * mm});
            skLineSegment(sketch, "E4556", {"start": v(-56.78, -48.1) * mm, "end": v(-56.8, -48.16) * mm});
            skLineSegment(sketch, "E4557", {"start": v(-56.8, -48.16) * mm, "end": v(-56.83, -48.24) * mm});
            skLineSegment(sketch, "E4558", {"start": v(-56.83, -48.24) * mm, "end": v(-56.85, -48.3) * mm});
            skLineSegment(sketch, "E4559", {"start": v(-56.85, -48.3) * mm, "end": v(-56.87, -48.38) * mm});
            skLineSegment(sketch, "E4560", {"start": v(-56.87, -48.38) * mm, "end": v(-56.9, -48.45) * mm});
            skLineSegment(sketch, "E4561", {"start": v(-56.9, -48.45) * mm, "end": v(-56.92, -48.53) * mm});
            skLineSegment(sketch, "E4562", {"start": v(-56.92, -48.53) * mm, "end": v(-56.94, -48.6) * mm});
            skLineSegment(sketch, "E4563", {"start": v(-56.94, -48.6) * mm, "end": v(-56.96, -48.69) * mm});
            skLineSegment(sketch, "E4564", {"start": v(-56.96, -48.69) * mm, "end": v(-56.98, -48.77) * mm});
            skLineSegment(sketch, "E4565", {"start": v(-56.98, -48.77) * mm, "end": v(-57, -48.85) * mm});
            skLineSegment(sketch, "E4566", {"start": v(-57, -48.85) * mm, "end": v(-57.02, -48.93) * mm});
            skLineSegment(sketch, "E4567", {"start": v(-57.02, -48.93) * mm, "end": v(-57.05, -49.01) * mm});
            skLineSegment(sketch, "E4568", {"start": v(-57.05, -49.01) * mm, "end": v(-57.07, -49.1) * mm});
            skLineSegment(sketch, "E4569", {"start": v(-57.07, -49.1) * mm, "end": v(-57.09, -49.18) * mm});
            skLineSegment(sketch, "E4570", {"start": v(-57.09, -49.18) * mm, "end": v(-57.1, -49.27) * mm});
            skLineSegment(sketch, "E4571", {"start": v(-57.1, -49.27) * mm, "end": v(-57.13, -49.36) * mm});
            skLineSegment(sketch, "E4572", {"start": v(-57.13, -49.36) * mm, "end": v(-57.15, -49.45) * mm});
            skLineSegment(sketch, "E4573", {"start": v(-57.15, -49.45) * mm, "end": v(-57.17, -49.54) * mm});
            skLineSegment(sketch, "E4574", {"start": v(-57.17, -49.54) * mm, "end": v(-57.2, -49.63) * mm});
            skLineSegment(sketch, "E4575", {"start": v(-57.2, -49.63) * mm, "end": v(-57.21, -49.72) * mm});
            skLineSegment(sketch, "E4576", {"start": v(-57.21, -49.72) * mm, "end": v(-57.23, -49.82) * mm});
            skLineSegment(sketch, "E4577", {"start": v(-57.23, -49.82) * mm, "end": v(-57.25, -49.91) * mm});
            skLineSegment(sketch, "E4578", {"start": v(-57.25, -49.91) * mm, "end": v(-57.27, -50.01) * mm});
            skLineSegment(sketch, "E4579", {"start": v(-57.27, -50.01) * mm, "end": v(-57.29, -50.1) * mm});
            skLineSegment(sketch, "E4580", {"start": v(-57.29, -50.1) * mm, "end": v(-57.3, -50.2) * mm});
            skLineSegment(sketch, "E4581", {"start": v(-57.3, -50.2) * mm, "end": v(-57.33, -50.31) * mm});
            skLineSegment(sketch, "E4582", {"start": v(-57.33, -50.31) * mm, "end": v(-57.34, -50.41) * mm});
            skLineSegment(sketch, "E4583", {"start": v(-57.34, -50.41) * mm, "end": v(-57.36, -50.52) * mm});
            skLineSegment(sketch, "E4584", {"start": v(-57.36, -50.52) * mm, "end": v(-57.38, -50.62) * mm});
            skLineSegment(sketch, "E4585", {"start": v(-57.38, -50.62) * mm, "end": v(-57.36, -50.67) * mm});
            skLineSegment(sketch, "E4586", {"start": v(-57.36, -50.67) * mm, "end": v(-56.48, -51.23) * mm});
            skLineSegment(sketch, "E4587", {"start": v(-56.48, -51.23) * mm, "end": v(-56.43, -51.23) * mm});
            skLineSegment(sketch, "E4588", {"start": v(-56.43, -51.23) * mm, "end": v(-56.34, -51.17) * mm});
            skLineSegment(sketch, "E4589", {"start": v(-56.34, -51.17) * mm, "end": v(-56.26, -51.11) * mm});
            skLineSegment(sketch, "E4590", {"start": v(-56.26, -51.11) * mm, "end": v(-56.17, -51.05) * mm});
            skLineSegment(sketch, "E4591", {"start": v(-56.17, -51.05) * mm, "end": v(-56.09, -51) * mm});
            skLineSegment(sketch, "E4592", {"start": v(-56.09, -51) * mm, "end": v(-56, -50.93) * mm});
            skLineSegment(sketch, "E4593", {"start": v(-56, -50.93) * mm, "end": v(-55.92, -50.88) * mm});
            skLineSegment(sketch, "E4594", {"start": v(-55.92, -50.88) * mm, "end": v(-55.84, -50.82) * mm});
            skLineSegment(sketch, "E4595", {"start": v(-55.84, -50.82) * mm, "end": v(-55.76, -50.76) * mm});
            skLineSegment(sketch, "E4596", {"start": v(-55.76, -50.76) * mm, "end": v(-55.69, -50.7) * mm});
            skLineSegment(sketch, "E4597", {"start": v(-55.69, -50.7) * mm, "end": v(-55.6, -50.65) * mm});
            skLineSegment(sketch, "E4598", {"start": v(-55.6, -50.65) * mm, "end": v(-55.53, -50.59) * mm});
            skLineSegment(sketch, "E4599", {"start": v(-55.53, -50.59) * mm, "end": v(-55.46, -50.53) * mm});
            skLineSegment(sketch, "E4600", {"start": v(-55.46, -50.53) * mm, "end": v(-55.39, -50.48) * mm});
            skLineSegment(sketch, "E4601", {"start": v(-55.39, -50.48) * mm, "end": v(-55.31, -50.42) * mm});
            skLineSegment(sketch, "E4602", {"start": v(-55.31, -50.42) * mm, "end": v(-55.24, -50.37) * mm});
            skLineSegment(sketch, "E4603", {"start": v(-55.24, -50.37) * mm, "end": v(-55.17, -50.31) * mm});
            skLineSegment(sketch, "E4604", {"start": v(-55.17, -50.31) * mm, "end": v(-55.1, -50.26) * mm});
            skLineSegment(sketch, "E4605", {"start": v(-55.1, -50.26) * mm, "end": v(-55.04, -50.2) * mm});
            skLineSegment(sketch, "E4606", {"start": v(-55.04, -50.2) * mm, "end": v(-54.97, -50.15) * mm});
            skLineSegment(sketch, "E4607", {"start": v(-54.97, -50.15) * mm, "end": v(-54.9, -50.1) * mm});
            skLineSegment(sketch, "E4608", {"start": v(-54.9, -50.1) * mm, "end": v(-54.85, -50.04) * mm});
            skLineSegment(sketch, "E4609", {"start": v(-54.85, -50.04) * mm, "end": v(-54.78, -50) * mm});
            skLineSegment(sketch, "E4610", {"start": v(-54.78, -50) * mm, "end": v(-54.72, -49.94) * mm});
            skLineSegment(sketch, "E4611", {"start": v(-54.72, -49.94) * mm, "end": v(-54.66, -49.89) * mm});
            skLineSegment(sketch, "E4612", {"start": v(-54.66, -49.89) * mm, "end": v(-54.6, -49.84) * mm});
            skLineSegment(sketch, "E4613", {"start": v(-54.6, -49.84) * mm, "end": v(-54.55, -49.79) * mm});
            skLineSegment(sketch, "E4614", {"start": v(-54.55, -49.79) * mm, "end": v(-54.5, -49.74) * mm});
            skLineSegment(sketch, "E4615", {"start": v(-54.5, -49.74) * mm, "end": v(-54.44, -49.69) * mm});
            skLineSegment(sketch, "E4616", {"start": v(-54.44, -49.69) * mm, "end": v(-54.38, -49.64) * mm});
            skLineSegment(sketch, "E4617", {"start": v(-54.38, -49.64) * mm, "end": v(-54.33, -49.6) * mm});
            skLineSegment(sketch, "E4618", {"start": v(-54.33, -49.6) * mm, "end": v(-54.28, -49.54) * mm});
            skLineSegment(sketch, "E4619", {"start": v(-54.28, -49.54) * mm, "end": v(-54.23, -49.5) * mm});
            skLineSegment(sketch, "E4620", {"start": v(-54.23, -49.5) * mm, "end": v(-54.18, -49.45) * mm});
            skLineSegment(sketch, "E4621", {"start": v(-54.18, -49.45) * mm, "end": v(-54.13, -49.4) * mm});
            skLineSegment(sketch, "E4622", {"start": v(-54.13, -49.4) * mm, "end": v(-54.08, -49.36) * mm});
            skLineSegment(sketch, "E4623", {"start": v(-54.08, -49.36) * mm, "end": v(-54.04, -49.31) * mm});
            skLineSegment(sketch, "E4624", {"start": v(-54.04, -49.31) * mm, "end": v(-54, -49.27) * mm});
            skLineSegment(sketch, "E4625", {"start": v(-54, -49.27) * mm, "end": v(-53.95, -49.23) * mm});
            skLineSegment(sketch, "E4626", {"start": v(-53.95, -49.23) * mm, "end": v(-53.9, -49.18) * mm});
            skLineSegment(sketch, "E4627", {"start": v(-53.9, -49.18) * mm, "end": v(-53.86, -49.14) * mm});
            skLineSegment(sketch, "E4628", {"start": v(-53.86, -49.14) * mm, "end": v(-53.66, -49.25) * mm});
            skLineSegment(sketch, "E4629", {"start": v(-53.66, -49.25) * mm, "end": v(-52.96, -49.66) * mm});
            skLineSegment(sketch, "E4630", {"start": v(-52.96, -49.66) * mm, "end": v(-52.76, -49.78) * mm});
            skLineSegment(sketch, "E4631", {"start": v(-52.76, -49.78) * mm, "end": v(-52.78, -49.84) * mm});
            skLineSegment(sketch, "E4632", {"start": v(-52.78, -49.84) * mm, "end": v(-52.8, -49.9) * mm});
            skLineSegment(sketch, "E4633", {"start": v(-52.8, -49.9) * mm, "end": v(-52.8, -49.96) * mm});
            skLineSegment(sketch, "E4634", {"start": v(-52.8, -49.96) * mm, "end": v(-52.82, -50.02) * mm});
            skLineSegment(sketch, "E4635", {"start": v(-52.82, -50.02) * mm, "end": v(-52.84, -50.08) * mm});
            skLineSegment(sketch, "E4636", {"start": v(-52.84, -50.08) * mm, "end": v(-52.86, -50.14) * mm});
            skLineSegment(sketch, "E4637", {"start": v(-52.86, -50.14) * mm, "end": v(-52.87, -50.2) * mm});
            skLineSegment(sketch, "E4638", {"start": v(-52.87, -50.2) * mm, "end": v(-52.89, -50.27) * mm});
            skLineSegment(sketch, "E4639", {"start": v(-52.89, -50.27) * mm, "end": v(-52.9, -50.34) * mm});
            skLineSegment(sketch, "E4640", {"start": v(-52.9, -50.34) * mm, "end": v(-52.92, -50.4) * mm});
            skLineSegment(sketch, "E4641", {"start": v(-52.92, -50.4) * mm, "end": v(-52.93, -50.48) * mm});
            skLineSegment(sketch, "E4642", {"start": v(-52.93, -50.48) * mm, "end": v(-52.95, -50.55) * mm});
            skLineSegment(sketch, "E4643", {"start": v(-52.95, -50.55) * mm, "end": v(-52.97, -50.62) * mm});
            skLineSegment(sketch, "E4644", {"start": v(-52.97, -50.62) * mm, "end": v(-52.98, -50.7) * mm});
            skLineSegment(sketch, "E4645", {"start": v(-52.98, -50.7) * mm, "end": v(-53, -50.77) * mm});
            skLineSegment(sketch, "E4646", {"start": v(-53, -50.77) * mm, "end": v(-53.01, -50.85) * mm});
            skLineSegment(sketch, "E4647", {"start": v(-53.01, -50.85) * mm, "end": v(-53.03, -50.92) * mm});
            skLineSegment(sketch, "E4648", {"start": v(-53.03, -50.92) * mm, "end": v(-53.04, -51) * mm});
            skLineSegment(sketch, "E4649", {"start": v(-53.04, -51) * mm, "end": v(-53.06, -51.08) * mm});
            skLineSegment(sketch, "E4650", {"start": v(-53.06, -51.08) * mm, "end": v(-53.07, -51.16) * mm});
            skLineSegment(sketch, "E4651", {"start": v(-53.07, -51.16) * mm, "end": v(-53.09, -51.25) * mm});
            skLineSegment(sketch, "E4652", {"start": v(-53.09, -51.25) * mm, "end": v(-53.1, -51.33) * mm});
            skLineSegment(sketch, "E4653", {"start": v(-53.1, -51.33) * mm, "end": v(-53.11, -51.42) * mm});
            skLineSegment(sketch, "E4654", {"start": v(-53.11, -51.42) * mm, "end": v(-53.13, -51.5) * mm});
            skLineSegment(sketch, "E4655", {"start": v(-53.13, -51.5) * mm, "end": v(-53.14, -51.59) * mm});
            skLineSegment(sketch, "E4656", {"start": v(-53.14, -51.59) * mm, "end": v(-53.15, -51.68) * mm});
            skLineSegment(sketch, "E4657", {"start": v(-53.15, -51.68) * mm, "end": v(-53.17, -51.77) * mm});
            skLineSegment(sketch, "E4658", {"start": v(-53.17, -51.77) * mm, "end": v(-53.18, -51.86) * mm});
            skLineSegment(sketch, "E4659", {"start": v(-53.18, -51.86) * mm, "end": v(-53.2, -51.95) * mm});
            skLineSegment(sketch, "E4660", {"start": v(-53.2, -51.95) * mm, "end": v(-53.2, -52.04) * mm});
            skLineSegment(sketch, "E4661", {"start": v(-53.2, -52.04) * mm, "end": v(-53.21, -52.14) * mm});
            skLineSegment(sketch, "E4662", {"start": v(-53.21, -52.14) * mm, "end": v(-53.23, -52.24) * mm});
            skLineSegment(sketch, "E4663", {"start": v(-53.23, -52.24) * mm, "end": v(-53.24, -52.33) * mm});
            skLineSegment(sketch, "E4664", {"start": v(-53.24, -52.33) * mm, "end": v(-53.25, -52.43) * mm});
            skLineSegment(sketch, "E4665", {"start": v(-53.25, -52.43) * mm, "end": v(-53.26, -52.53) * mm});
            skLineSegment(sketch, "E4666", {"start": v(-53.26, -52.53) * mm, "end": v(-53.27, -52.63) * mm});
            skLineSegment(sketch, "E4667", {"start": v(-53.27, -52.63) * mm, "end": v(-53.28, -52.73) * mm});
            skLineSegment(sketch, "E4668", {"start": v(-53.28, -52.73) * mm, "end": v(-53.29, -52.84) * mm});
            skLineSegment(sketch, "E4669", {"start": v(-53.29, -52.84) * mm, "end": v(-53.3, -52.94) * mm});
            skLineSegment(sketch, "E4670", {"start": v(-53.3, -52.94) * mm, "end": v(-53.3, -53.05) * mm});
            skLineSegment(sketch, "E4671", {"start": v(-53.3, -53.05) * mm, "end": v(-53.28, -53.1) * mm});
            skLineSegment(sketch, "E4672", {"start": v(-53.28, -53.1) * mm, "end": v(-52.35, -53.57) * mm});
            skLineSegment(sketch, "E4673", {"start": v(-52.35, -53.57) * mm, "end": v(-52.3, -53.57) * mm});
            skLineSegment(sketch, "E4674", {"start": v(-52.3, -53.57) * mm, "end": v(-52.22, -53.5) * mm});
            skLineSegment(sketch, "E4675", {"start": v(-52.22, -53.5) * mm, "end": v(-52.14, -53.44) * mm});
            skLineSegment(sketch, "E4676", {"start": v(-52.14, -53.44) * mm, "end": v(-52.06, -53.37) * mm});
            skLineSegment(sketch, "E4677", {"start": v(-52.06, -53.37) * mm, "end": v(-51.98, -53.3) * mm});
            skLineSegment(sketch, "E4678", {"start": v(-51.98, -53.3) * mm, "end": v(-51.9, -53.24) * mm});
            skLineSegment(sketch, "E4679", {"start": v(-51.9, -53.24) * mm, "end": v(-51.83, -53.17) * mm});
            skLineSegment(sketch, "E4680", {"start": v(-51.83, -53.17) * mm, "end": v(-51.75, -53.1) * mm});
            skLineSegment(sketch, "E4681", {"start": v(-51.75, -53.1) * mm, "end": v(-51.68, -53.04) * mm});
            skLineSegment(sketch, "E4682", {"start": v(-51.68, -53.04) * mm, "end": v(-51.6, -52.98) * mm});
            skLineSegment(sketch, "E4683", {"start": v(-51.6, -52.98) * mm, "end": v(-51.54, -52.92) * mm});
            skLineSegment(sketch, "E4684", {"start": v(-51.54, -52.92) * mm, "end": v(-51.47, -52.85) * mm});
            skLineSegment(sketch, "E4685", {"start": v(-51.47, -52.85) * mm, "end": v(-51.4, -52.79) * mm});
            skLineSegment(sketch, "E4686", {"start": v(-51.4, -52.79) * mm, "end": v(-51.33, -52.73) * mm});
            skLineSegment(sketch, "E4687", {"start": v(-51.33, -52.73) * mm, "end": v(-51.26, -52.67) * mm});
            skLineSegment(sketch, "E4688", {"start": v(-51.26, -52.67) * mm, "end": v(-51.2, -52.6) * mm});
            skLineSegment(sketch, "E4689", {"start": v(-51.2, -52.6) * mm, "end": v(-51.13, -52.54) * mm});
            skLineSegment(sketch, "E4690", {"start": v(-51.13, -52.54) * mm, "end": v(-51.07, -52.48) * mm});
            skLineSegment(sketch, "E4691", {"start": v(-51.07, -52.48) * mm, "end": v(-51, -52.42) * mm});
            skLineSegment(sketch, "E4692", {"start": v(-51, -52.42) * mm, "end": v(-50.95, -52.36) * mm});
            skLineSegment(sketch, "E4693", {"start": v(-50.95, -52.36) * mm, "end": v(-50.89, -52.3) * mm});
            skLineSegment(sketch, "E4694", {"start": v(-50.89, -52.3) * mm, "end": v(-50.83, -52.25) * mm});
            skLineSegment(sketch, "E4695", {"start": v(-50.83, -52.25) * mm, "end": v(-50.77, -52.19) * mm});
            skLineSegment(sketch, "E4696", {"start": v(-50.77, -52.19) * mm, "end": v(-50.72, -52.13) * mm});
            skLineSegment(sketch, "E4697", {"start": v(-50.72, -52.13) * mm, "end": v(-50.66, -52.08) * mm});
            skLineSegment(sketch, "E4698", {"start": v(-50.66, -52.08) * mm, "end": v(-50.6, -52.02) * mm});
            skLineSegment(sketch, "E4699", {"start": v(-50.6, -52.02) * mm, "end": v(-50.56, -51.96) * mm});
            skLineSegment(sketch, "E4700", {"start": v(-50.56, -51.96) * mm, "end": v(-50.5, -51.9) * mm});
            skLineSegment(sketch, "E4701", {"start": v(-50.5, -51.9) * mm, "end": v(-50.45, -51.86) * mm});
            skLineSegment(sketch, "E4702", {"start": v(-50.45, -51.86) * mm, "end": v(-50.4, -51.8) * mm});
            skLineSegment(sketch, "E4703", {"start": v(-50.4, -51.8) * mm, "end": v(-50.36, -51.75) * mm});
            skLineSegment(sketch, "E4704", {"start": v(-50.36, -51.75) * mm, "end": v(-50.3, -51.7) * mm});
            skLineSegment(sketch, "E4705", {"start": v(-50.3, -51.7) * mm, "end": v(-50.26, -51.65) * mm});
            skLineSegment(sketch, "E4706", {"start": v(-50.26, -51.65) * mm, "end": v(-50.22, -51.6) * mm});
            skLineSegment(sketch, "E4707", {"start": v(-50.22, -51.6) * mm, "end": v(-50.17, -51.54) * mm});
            skLineSegment(sketch, "E4708", {"start": v(-50.17, -51.54) * mm, "end": v(-50.13, -51.5) * mm});
            skLineSegment(sketch, "E4709", {"start": v(-50.13, -51.5) * mm, "end": v(-50.09, -51.45) * mm});
            skLineSegment(sketch, "E4710", {"start": v(-50.09, -51.45) * mm, "end": v(-50.05, -51.4) * mm});
            skLineSegment(sketch, "E4711", {"start": v(-50.05, -51.4) * mm, "end": v(-50, -51.35) * mm});
            skLineSegment(sketch, "E4712", {"start": v(-50, -51.35) * mm, "end": v(-49.97, -51.3) * mm});
            skLineSegment(sketch, "E4713", {"start": v(-49.97, -51.3) * mm, "end": v(-49.93, -51.26) * mm});
            skLineSegment(sketch, "E4714", {"start": v(-49.93, -51.26) * mm, "end": v(-49.72, -51.35) * mm});
            skLineSegment(sketch, "E4715", {"start": v(-49.72, -51.35) * mm, "end": v(-48.98, -51.7) * mm});
            skLineSegment(sketch, "E4716", {"start": v(-48.98, -51.7) * mm, "end": v(-48.78, -51.8) * mm});
            skLineSegment(sketch, "E4717", {"start": v(-48.78, -51.8) * mm, "end": v(-48.79, -51.86) * mm});
            skLineSegment(sketch, "E4718", {"start": v(-48.79, -51.86) * mm, "end": v(-48.8, -51.92) * mm});
            skLineSegment(sketch, "E4719", {"start": v(-48.8, -51.92) * mm, "end": v(-48.8, -51.98) * mm});
            skLineSegment(sketch, "E4720", {"start": v(-48.8, -51.98) * mm, "end": v(-48.82, -52.04) * mm});
            skLineSegment(sketch, "E4721", {"start": v(-48.82, -52.04) * mm, "end": v(-48.83, -52.1) * mm});
            skLineSegment(sketch, "E4722", {"start": v(-48.83, -52.1) * mm, "end": v(-48.84, -52.17) * mm});
            skLineSegment(sketch, "E4723", {"start": v(-48.84, -52.17) * mm, "end": v(-48.85, -52.23) * mm});
            skLineSegment(sketch, "E4724", {"start": v(-48.85, -52.23) * mm, "end": v(-48.86, -52.3) * mm});
            skLineSegment(sketch, "E4725", {"start": v(-48.86, -52.3) * mm, "end": v(-48.87, -52.37) * mm});
            skLineSegment(sketch, "E4726", {"start": v(-48.87, -52.37) * mm, "end": v(-48.88, -52.44) * mm});
            skLineSegment(sketch, "E4727", {"start": v(-48.88, -52.44) * mm, "end": v(-48.89, -52.51) * mm});
            skLineSegment(sketch, "E4728", {"start": v(-48.89, -52.51) * mm, "end": v(-48.9, -52.58) * mm});
            skLineSegment(sketch, "E4729", {"start": v(-48.9, -52.58) * mm, "end": v(-48.9, -52.66) * mm});
            skLineSegment(sketch, "E4730", {"start": v(-48.9, -52.66) * mm, "end": v(-48.91, -52.73) * mm});
            skLineSegment(sketch, "E4731", {"start": v(-48.91, -52.73) * mm, "end": v(-48.92, -52.8) * mm});
            skLineSegment(sketch, "E4732", {"start": v(-48.92, -52.8) * mm, "end": v(-48.93, -52.88) * mm});
            skLineSegment(sketch, "E4733", {"start": v(-48.93, -52.88) * mm, "end": v(-48.94, -52.96) * mm});
            skLineSegment(sketch, "E4734", {"start": v(-48.94, -52.96) * mm, "end": v(-48.95, -53.04) * mm});
            skLineSegment(sketch, "E4735", {"start": v(-48.95, -53.04) * mm, "end": v(-48.95, -53.12) * mm});
            skLineSegment(sketch, "E4736", {"start": v(-48.95, -53.12) * mm, "end": v(-48.96, -53.2) * mm});
            skLineSegment(sketch, "E4737", {"start": v(-48.96, -53.2) * mm, "end": v(-48.97, -53.29) * mm});
            skLineSegment(sketch, "E4738", {"start": v(-48.97, -53.29) * mm, "end": v(-48.98, -53.37) * mm});
            skLineSegment(sketch, "E4739", {"start": v(-48.98, -53.37) * mm, "end": v(-48.98, -53.46) * mm});
            skLineSegment(sketch, "E4740", {"start": v(-48.98, -53.46) * mm, "end": v(-48.99, -53.54) * mm});
            skLineSegment(sketch, "E4741", {"start": v(-48.99, -53.54) * mm, "end": v(-49, -53.63) * mm});
            skLineSegment(sketch, "E4742", {"start": v(-49, -53.63) * mm, "end": v(-49, -53.72) * mm});
            skLineSegment(sketch, "E4743", {"start": v(-49, -53.72) * mm, "end": v(-49, -53.81) * mm});
            skLineSegment(sketch, "E4744", {"start": v(-49, -53.81) * mm, "end": v(-49, -53.9) * mm});
            skLineSegment(sketch, "E4745", {"start": v(-49, -53.9) * mm, "end": v(-49.01, -54) * mm});
            skLineSegment(sketch, "E4746", {"start": v(-49.01, -54) * mm, "end": v(-49.01, -54.1) * mm});
            skLineSegment(sketch, "E4747", {"start": v(-49.01, -54.1) * mm, "end": v(-49.02, -54.19) * mm});
            skLineSegment(sketch, "E4748", {"start": v(-49.02, -54.19) * mm, "end": v(-49.02, -54.28) * mm});
            skLineSegment(sketch, "E4749", {"start": v(-49.02, -54.28) * mm, "end": v(-49.02, -54.38) * mm});
            skLineSegment(sketch, "E4750", {"start": v(-49.02, -54.38) * mm, "end": v(-49.02, -54.48) * mm});
            skLineSegment(sketch, "E4751", {"start": v(-49.02, -54.48) * mm, "end": v(-49.02, -54.58) * mm});
            skLineSegment(sketch, "E4752", {"start": v(-49.02, -54.58) * mm, "end": v(-49.03, -54.68) * mm});
            skLineSegment(sketch, "E4753", {"start": v(-49.03, -54.68) * mm, "end": v(-49.03, -54.79) * mm});
            skLineSegment(sketch, "E4754", {"start": v(-49.03, -54.79) * mm, "end": v(-49.03, -54.89) * mm});
            skLineSegment(sketch, "E4755", {"start": v(-49.03, -54.89) * mm, "end": v(-49.02, -55) * mm});
            skLineSegment(sketch, "E4756", {"start": v(-49.02, -55) * mm, "end": v(-49.02, -55.1) * mm});
            skLineSegment(sketch, "E4757", {"start": v(-49.02, -55.1) * mm, "end": v(-49, -55.14) * mm});
            skLineSegment(sketch, "E4758", {"start": v(-49, -55.14) * mm, "end": v(-48.03, -55.54) * mm});
            skLineSegment(sketch, "E4759", {"start": v(-48.03, -55.54) * mm, "end": v(-47.98, -55.53) * mm});
            skLineSegment(sketch, "E4760", {"start": v(-47.98, -55.53) * mm, "end": v(-47.9, -55.46) * mm});
            skLineSegment(sketch, "E4761", {"start": v(-47.9, -55.46) * mm, "end": v(-47.83, -55.38) * mm});
            skLineSegment(sketch, "E4762", {"start": v(-47.83, -55.38) * mm, "end": v(-47.76, -55.31) * mm});
            skLineSegment(sketch, "E4763", {"start": v(-47.76, -55.31) * mm, "end": v(-47.68, -55.24) * mm});
            skLineSegment(sketch, "E4764", {"start": v(-47.68, -55.24) * mm, "end": v(-47.61, -55.16) * mm});
            skLineSegment(sketch, "E4765", {"start": v(-47.61, -55.16) * mm, "end": v(-47.54, -55.1) * mm});
            skLineSegment(sketch, "E4766", {"start": v(-47.54, -55.1) * mm, "end": v(-47.47, -55.02) * mm});
            skLineSegment(sketch, "E4767", {"start": v(-47.47, -55.02) * mm, "end": v(-47.4, -54.95) * mm});
            skLineSegment(sketch, "E4768", {"start": v(-47.4, -54.95) * mm, "end": v(-47.34, -54.88) * mm});
            skLineSegment(sketch, "E4769", {"start": v(-47.34, -54.88) * mm, "end": v(-47.28, -54.8) * mm});
            skLineSegment(sketch, "E4770", {"start": v(-47.28, -54.8) * mm, "end": v(-47.21, -54.74) * mm});
            skLineSegment(sketch, "E4771", {"start": v(-47.21, -54.74) * mm, "end": v(-47.15, -54.67) * mm});
            skLineSegment(sketch, "E4772", {"start": v(-47.15, -54.67) * mm, "end": v(-47.09, -54.6) * mm});
            skLineSegment(sketch, "E4773", {"start": v(-47.09, -54.6) * mm, "end": v(-47.03, -54.54) * mm});
            skLineSegment(sketch, "E4774", {"start": v(-47.03, -54.54) * mm, "end": v(-46.97, -54.47) * mm});
            skLineSegment(sketch, "E4775", {"start": v(-46.97, -54.47) * mm, "end": v(-46.9, -54.4) * mm});
            skLineSegment(sketch, "E4776", {"start": v(-46.9, -54.4) * mm, "end": v(-46.85, -54.34) * mm});
            skLineSegment(sketch, "E4777", {"start": v(-46.85, -54.34) * mm, "end": v(-46.8, -54.27) * mm});
            skLineSegment(sketch, "E4778", {"start": v(-46.8, -54.27) * mm, "end": v(-46.74, -54.2) * mm});
            skLineSegment(sketch, "E4779", {"start": v(-46.74, -54.2) * mm, "end": v(-46.69, -54.14) * mm});
            skLineSegment(sketch, "E4780", {"start": v(-46.69, -54.14) * mm, "end": v(-46.63, -54.08) * mm});
            skLineSegment(sketch, "E4781", {"start": v(-46.63, -54.08) * mm, "end": v(-46.58, -54.02) * mm});
            skLineSegment(sketch, "E4782", {"start": v(-46.58, -54.02) * mm, "end": v(-46.53, -53.96) * mm});
            skLineSegment(sketch, "E4783", {"start": v(-46.53, -53.96) * mm, "end": v(-46.48, -53.9) * mm});
            skLineSegment(sketch, "E4784", {"start": v(-46.48, -53.9) * mm, "end": v(-46.43, -53.84) * mm});
            skLineSegment(sketch, "E4785", {"start": v(-46.43, -53.84) * mm, "end": v(-46.38, -53.78) * mm});
            skLineSegment(sketch, "E4786", {"start": v(-46.38, -53.78) * mm, "end": v(-46.34, -53.72) * mm});
            skLineSegment(sketch, "E4787", {"start": v(-46.34, -53.72) * mm, "end": v(-46.3, -53.66) * mm});
            skLineSegment(sketch, "E4788", {"start": v(-46.3, -53.66) * mm, "end": v(-46.25, -53.6) * mm});
            skLineSegment(sketch, "E4789", {"start": v(-46.25, -53.6) * mm, "end": v(-46.2, -53.54) * mm});
            skLineSegment(sketch, "E4790", {"start": v(-46.2, -53.54) * mm, "end": v(-46.16, -53.49) * mm});
            skLineSegment(sketch, "E4791", {"start": v(-46.16, -53.49) * mm, "end": v(-46.12, -53.43) * mm});
            skLineSegment(sketch, "E4792", {"start": v(-46.12, -53.43) * mm, "end": v(-46.08, -53.38) * mm});
            skLineSegment(sketch, "E4793", {"start": v(-46.08, -53.38) * mm, "end": v(-46.04, -53.32) * mm});
            skLineSegment(sketch, "E4794", {"start": v(-46.04, -53.32) * mm, "end": v(-46, -53.27) * mm});
            skLineSegment(sketch, "E4795", {"start": v(-46, -53.27) * mm, "end": v(-45.97, -53.22) * mm});
            skLineSegment(sketch, "E4796", {"start": v(-45.97, -53.22) * mm, "end": v(-45.93, -53.17) * mm});
            skLineSegment(sketch, "E4797", {"start": v(-45.93, -53.17) * mm, "end": v(-45.9, -53.12) * mm});
            skLineSegment(sketch, "E4798", {"start": v(-45.9, -53.12) * mm, "end": v(-45.86, -53.07) * mm});
            skLineSegment(sketch, "E4799", {"start": v(-45.86, -53.07) * mm, "end": v(-45.83, -53.02) * mm});
            skLineSegment(sketch, "E4800", {"start": v(-45.83, -53.02) * mm, "end": v(-45.6, -53.09) * mm});
            skLineSegment(sketch, "E4801", {"start": v(-45.6, -53.09) * mm, "end": v(-44.84, -53.36) * mm});
            skLineSegment(sketch, "E4802", {"start": v(-44.84, -53.36) * mm, "end": v(-44.63, -53.45) * mm});
            skLineSegment(sketch, "E4803", {"start": v(-44.63, -53.45) * mm, "end": v(-44.63, -53.5) * mm});
            skLineSegment(sketch, "E4804", {"start": v(-44.63, -53.5) * mm, "end": v(-44.64, -53.57) * mm});
            skLineSegment(sketch, "E4805", {"start": v(-44.64, -53.57) * mm, "end": v(-44.64, -53.63) * mm});
            skLineSegment(sketch, "E4806", {"start": v(-44.64, -53.63) * mm, "end": v(-44.65, -53.7) * mm});
            skLineSegment(sketch, "E4807", {"start": v(-44.65, -53.7) * mm, "end": v(-44.65, -53.76) * mm});
            skLineSegment(sketch, "E4808", {"start": v(-44.65, -53.76) * mm, "end": v(-44.66, -53.82) * mm});
            skLineSegment(sketch, "E4809", {"start": v(-44.66, -53.82) * mm, "end": v(-44.66, -53.9) * mm});
            skLineSegment(sketch, "E4810", {"start": v(-44.66, -53.9) * mm, "end": v(-44.66, -53.96) * mm});
            skLineSegment(sketch, "E4811", {"start": v(-44.66, -53.96) * mm, "end": v(-44.67, -54.03) * mm});
            skLineSegment(sketch, "E4812", {"start": v(-44.67, -54.03) * mm, "end": v(-44.67, -54.1) * mm});
            skLineSegment(sketch, "E4813", {"start": v(-44.67, -54.1) * mm, "end": v(-44.67, -54.17) * mm});
            skLineSegment(sketch, "E4814", {"start": v(-44.67, -54.17) * mm, "end": v(-44.68, -54.24) * mm});
            skLineSegment(sketch, "E4815", {"start": v(-44.68, -54.24) * mm, "end": v(-44.68, -54.32) * mm});
            skLineSegment(sketch, "E4816", {"start": v(-44.68, -54.32) * mm, "end": v(-44.68, -54.4) * mm});
            skLineSegment(sketch, "E4817", {"start": v(-44.68, -54.4) * mm, "end": v(-44.68, -54.47) * mm});
            skLineSegment(sketch, "E4818", {"start": v(-44.68, -54.47) * mm, "end": v(-44.68, -54.54) * mm});
            skLineSegment(sketch, "E4819", {"start": v(-44.68, -54.54) * mm, "end": v(-44.69, -54.62) * mm});
            skLineSegment(sketch, "E4820", {"start": v(-44.69, -54.62) * mm, "end": v(-44.69, -54.7) * mm});
            skLineSegment(sketch, "E4821", {"start": v(-44.69, -54.7) * mm, "end": v(-44.69, -54.78) * mm});
            skLineSegment(sketch, "E4822", {"start": v(-44.69, -54.78) * mm, "end": v(-44.69, -54.87) * mm});
            skLineSegment(sketch, "E4823", {"start": v(-44.69, -54.87) * mm, "end": v(-44.69, -54.95) * mm});
            skLineSegment(sketch, "E4824", {"start": v(-44.69, -54.95) * mm, "end": v(-44.68, -55.03) * mm});
            skLineSegment(sketch, "E4825", {"start": v(-44.68, -55.03) * mm, "end": v(-44.68, -55.12) * mm});
            skLineSegment(sketch, "E4826", {"start": v(-44.68, -55.12) * mm, "end": v(-44.68, -55.2) * mm});
            skLineSegment(sketch, "E4827", {"start": v(-44.68, -55.2) * mm, "end": v(-44.68, -55.3) * mm});
            skLineSegment(sketch, "E4828", {"start": v(-44.68, -55.3) * mm, "end": v(-44.68, -55.39) * mm});
            skLineSegment(sketch, "E4829", {"start": v(-44.68, -55.39) * mm, "end": v(-44.67, -55.48) * mm});
            skLineSegment(sketch, "E4830", {"start": v(-44.67, -55.48) * mm, "end": v(-44.67, -55.57) * mm});
            skLineSegment(sketch, "E4831", {"start": v(-44.67, -55.57) * mm, "end": v(-44.66, -55.66) * mm});
            skLineSegment(sketch, "E4832", {"start": v(-44.66, -55.66) * mm, "end": v(-44.66, -55.76) * mm});
            skLineSegment(sketch, "E4833", {"start": v(-44.66, -55.76) * mm, "end": v(-44.65, -55.85) * mm});
            skLineSegment(sketch, "E4834", {"start": v(-44.65, -55.85) * mm, "end": v(-44.65, -55.95) * mm});
            skLineSegment(sketch, "E4835", {"start": v(-44.65, -55.95) * mm, "end": v(-44.64, -56.05) * mm});
            skLineSegment(sketch, "E4836", {"start": v(-44.64, -56.05) * mm, "end": v(-44.63, -56.14) * mm});
            skLineSegment(sketch, "E4837", {"start": v(-44.63, -56.14) * mm, "end": v(-44.63, -56.24) * mm});
            skLineSegment(sketch, "E4838", {"start": v(-44.63, -56.24) * mm, "end": v(-44.62, -56.35) * mm});
            skLineSegment(sketch, "E4839", {"start": v(-44.62, -56.35) * mm, "end": v(-44.6, -56.45) * mm});
            skLineSegment(sketch, "E4840", {"start": v(-44.6, -56.45) * mm, "end": v(-44.6, -56.55) * mm});
            skLineSegment(sketch, "E4841", {"start": v(-44.6, -56.55) * mm, "end": v(-44.59, -56.66) * mm});
            skLineSegment(sketch, "E4842", {"start": v(-44.59, -56.66) * mm, "end": v(-44.58, -56.76) * mm});
            skLineSegment(sketch, "E4843", {"start": v(-44.58, -56.76) * mm, "end": v(-44.54, -56.8) * mm});
            skLineSegment(sketch, "E4844", {"start": v(-44.54, -56.8) * mm, "end": v(-43.55, -57.1) * mm});
            skLineSegment(sketch, "E4845", {"start": v(-43.55, -57.1) * mm, "end": v(-43.5, -57.1) * mm});
            skLineSegment(sketch, "E4846", {"start": v(-43.5, -57.1) * mm, "end": v(-43.43, -57.02) * mm});
            skLineSegment(sketch, "E4847", {"start": v(-43.43, -57.02) * mm, "end": v(-43.36, -56.94) * mm});
            skLineSegment(sketch, "E4848", {"start": v(-43.36, -56.94) * mm, "end": v(-43.3, -56.86) * mm});
            skLineSegment(sketch, "E4849", {"start": v(-43.3, -56.86) * mm, "end": v(-43.23, -56.78) * mm});
            skLineSegment(sketch, "E4850", {"start": v(-43.23, -56.78) * mm, "end": v(-43.17, -56.7) * mm});
            skLineSegment(sketch, "E4851", {"start": v(-43.17, -56.7) * mm, "end": v(-43.1, -56.62) * mm});
            skLineSegment(sketch, "E4852", {"start": v(-43.1, -56.62) * mm, "end": v(-43.04, -56.54) * mm});
            skLineSegment(sketch, "E4853", {"start": v(-43.04, -56.54) * mm, "end": v(-42.98, -56.47) * mm});
            skLineSegment(sketch, "E4854", {"start": v(-42.98, -56.47) * mm, "end": v(-42.92, -56.4) * mm});
            skLineSegment(sketch, "E4855", {"start": v(-42.92, -56.4) * mm, "end": v(-42.86, -56.31) * mm});
            skLineSegment(sketch, "E4856", {"start": v(-42.86, -56.31) * mm, "end": v(-42.8, -56.24) * mm});
            skLineSegment(sketch, "E4857", {"start": v(-42.8, -56.24) * mm, "end": v(-42.75, -56.17) * mm});
            skLineSegment(sketch, "E4858", {"start": v(-42.75, -56.17) * mm, "end": v(-42.7, -56.1) * mm});
            skLineSegment(sketch, "E4859", {"start": v(-42.7, -56.1) * mm, "end": v(-42.64, -56.02) * mm});
            skLineSegment(sketch, "E4860", {"start": v(-42.64, -56.02) * mm, "end": v(-42.59, -55.95) * mm});
            skLineSegment(sketch, "E4861", {"start": v(-42.59, -55.95) * mm, "end": v(-42.53, -55.88) * mm});
            skLineSegment(sketch, "E4862", {"start": v(-42.53, -55.88) * mm, "end": v(-42.48, -55.8) * mm});
            skLineSegment(sketch, "E4863", {"start": v(-42.48, -55.8) * mm, "end": v(-42.43, -55.74) * mm});
            skLineSegment(sketch, "E4864", {"start": v(-42.43, -55.74) * mm, "end": v(-42.38, -55.67) * mm});
            skLineSegment(sketch, "E4865", {"start": v(-42.38, -55.67) * mm, "end": v(-42.34, -55.6) * mm});
            skLineSegment(sketch, "E4866", {"start": v(-42.34, -55.6) * mm, "end": v(-42.29, -55.53) * mm});
            skLineSegment(sketch, "E4867", {"start": v(-42.29, -55.53) * mm, "end": v(-42.24, -55.46) * mm});
            skLineSegment(sketch, "E4868", {"start": v(-42.24, -55.46) * mm, "end": v(-42.2, -55.4) * mm});
            skLineSegment(sketch, "E4869", {"start": v(-42.2, -55.4) * mm, "end": v(-42.15, -55.33) * mm});
            skLineSegment(sketch, "E4870", {"start": v(-42.15, -55.33) * mm, "end": v(-42.11, -55.27) * mm});
            skLineSegment(sketch, "E4871", {"start": v(-42.11, -55.27) * mm, "end": v(-42.07, -55.2) * mm});
            skLineSegment(sketch, "E4872", {"start": v(-42.07, -55.2) * mm, "end": v(-42.03, -55.14) * mm});
            skLineSegment(sketch, "E4873", {"start": v(-42.03, -55.14) * mm, "end": v(-41.99, -55.08) * mm});
            skLineSegment(sketch, "E4874", {"start": v(-41.99, -55.08) * mm, "end": v(-41.95, -55.02) * mm});
            skLineSegment(sketch, "E4875", {"start": v(-41.95, -55.02) * mm, "end": v(-41.91, -54.96) * mm});
            skLineSegment(sketch, "E4876", {"start": v(-41.91, -54.96) * mm, "end": v(-41.87, -54.9) * mm});
            skLineSegment(sketch, "E4877", {"start": v(-41.87, -54.9) * mm, "end": v(-41.84, -54.84) * mm});
            skLineSegment(sketch, "E4878", {"start": v(-41.84, -54.84) * mm, "end": v(-41.8, -54.78) * mm});
            skLineSegment(sketch, "E4879", {"start": v(-41.8, -54.78) * mm, "end": v(-41.77, -54.72) * mm});
            skLineSegment(sketch, "E4880", {"start": v(-41.77, -54.72) * mm, "end": v(-41.73, -54.67) * mm});
            skLineSegment(sketch, "E4881", {"start": v(-41.73, -54.67) * mm, "end": v(-41.7, -54.61) * mm});
            skLineSegment(sketch, "E4882", {"start": v(-41.7, -54.61) * mm, "end": v(-41.67, -54.56) * mm});
            skLineSegment(sketch, "E4883", {"start": v(-41.67, -54.56) * mm, "end": v(-41.64, -54.5) * mm});
            skLineSegment(sketch, "E4884", {"start": v(-41.64, -54.5) * mm, "end": v(-41.6, -54.45) * mm});
            skLineSegment(sketch, "E4885", {"start": v(-41.6, -54.45) * mm, "end": v(-41.58, -54.4) * mm});
            skLineSegment(sketch, "E4886", {"start": v(-41.58, -54.4) * mm, "end": v(-41.35, -54.45) * mm});
            skLineSegment(sketch, "E4887", {"start": v(-41.35, -54.45) * mm, "end": v(-40.57, -54.66) * mm});
            skLineSegment(sketch, "E4888", {"start": v(-40.57, -54.66) * mm, "end": v(-40.35, -54.72) * mm});
            skLineSegment(sketch, "E4889", {"start": v(-40.35, -54.72) * mm, "end": v(-40.35, -54.78) * mm});
            skLineSegment(sketch, "E4890", {"start": v(-40.35, -54.78) * mm, "end": v(-40.35, -54.84) * mm});
            skLineSegment(sketch, "E4891", {"start": v(-40.35, -54.84) * mm, "end": v(-40.35, -54.9) * mm});
            skLineSegment(sketch, "E4892", {"start": v(-40.35, -54.9) * mm, "end": v(-40.35, -54.97) * mm});
            skLineSegment(sketch, "E4893", {"start": v(-40.35, -54.97) * mm, "end": v(-40.34, -55.03) * mm});
            skLineSegment(sketch, "E4894", {"start": v(-40.34, -55.03) * mm, "end": v(-40.34, -55.1) * mm});
            skLineSegment(sketch, "E4895", {"start": v(-40.34, -55.1) * mm, "end": v(-40.34, -55.16) * mm});
            skLineSegment(sketch, "E4896", {"start": v(-40.34, -55.16) * mm, "end": v(-40.34, -55.23) * mm});
            skLineSegment(sketch, "E4897", {"start": v(-40.34, -55.23) * mm, "end": v(-40.34, -55.3) * mm});
            skLineSegment(sketch, "E4898", {"start": v(-40.34, -55.3) * mm, "end": v(-40.33, -55.37) * mm});
            skLineSegment(sketch, "E4899", {"start": v(-40.33, -55.37) * mm, "end": v(-40.33, -55.44) * mm});
            skLineSegment(sketch, "E4900", {"start": v(-40.33, -55.44) * mm, "end": v(-40.33, -55.52) * mm});
            skLineSegment(sketch, "E4901", {"start": v(-40.33, -55.52) * mm, "end": v(-40.32, -55.59) * mm});
            skLineSegment(sketch, "E4902", {"start": v(-40.32, -55.59) * mm, "end": v(-40.32, -55.66) * mm});
            skLineSegment(sketch, "E4903", {"start": v(-40.32, -55.66) * mm, "end": v(-40.31, -55.74) * mm});
            skLineSegment(sketch, "E4904", {"start": v(-40.31, -55.74) * mm, "end": v(-40.3, -55.82) * mm});
            skLineSegment(sketch, "E4905", {"start": v(-40.3, -55.82) * mm, "end": v(-40.3, -55.9) * mm});
            skLineSegment(sketch, "E4906", {"start": v(-40.3, -55.9) * mm, "end": v(-40.3, -55.98) * mm});
            skLineSegment(sketch, "E4907", {"start": v(-40.3, -55.98) * mm, "end": v(-40.29, -56.06) * mm});
            skLineSegment(sketch, "E4908", {"start": v(-40.29, -56.06) * mm, "end": v(-40.28, -56.14) * mm});
            skLineSegment(sketch, "E4909", {"start": v(-40.28, -56.14) * mm, "end": v(-40.27, -56.22) * mm});
            skLineSegment(sketch, "E4910", {"start": v(-40.27, -56.22) * mm, "end": v(-40.26, -56.3) * mm});
            skLineSegment(sketch, "E4911", {"start": v(-40.26, -56.3) * mm, "end": v(-40.25, -56.4) * mm});
            skLineSegment(sketch, "E4912", {"start": v(-40.25, -56.4) * mm, "end": v(-40.24, -56.48) * mm});
            skLineSegment(sketch, "E4913", {"start": v(-40.24, -56.48) * mm, "end": v(-40.23, -56.57) * mm});
            skLineSegment(sketch, "E4914", {"start": v(-40.23, -56.57) * mm, "end": v(-40.22, -56.66) * mm});
            skLineSegment(sketch, "E4915", {"start": v(-40.22, -56.66) * mm, "end": v(-40.21, -56.75) * mm});
            skLineSegment(sketch, "E4916", {"start": v(-40.21, -56.75) * mm, "end": v(-40.2, -56.84) * mm});
            skLineSegment(sketch, "E4917", {"start": v(-40.2, -56.84) * mm, "end": v(-40.18, -56.93) * mm});
            skLineSegment(sketch, "E4918", {"start": v(-40.18, -56.93) * mm, "end": v(-40.17, -57.02) * mm});
            skLineSegment(sketch, "E4919", {"start": v(-40.17, -57.02) * mm, "end": v(-40.16, -57.12) * mm});
            skLineSegment(sketch, "E4920", {"start": v(-40.16, -57.12) * mm, "end": v(-40.14, -57.21) * mm});
            skLineSegment(sketch, "E4921", {"start": v(-40.14, -57.21) * mm, "end": v(-40.13, -57.3) * mm});
            skLineSegment(sketch, "E4922", {"start": v(-40.13, -57.3) * mm, "end": v(-40.11, -57.4) * mm});
            skLineSegment(sketch, "E4923", {"start": v(-40.11, -57.4) * mm, "end": v(-40.1, -57.5) * mm});
            skLineSegment(sketch, "E4924", {"start": v(-40.1, -57.5) * mm, "end": v(-40.08, -57.6) * mm});
            skLineSegment(sketch, "E4925", {"start": v(-40.08, -57.6) * mm, "end": v(-40.06, -57.7) * mm});
            skLineSegment(sketch, "E4926", {"start": v(-40.06, -57.7) * mm, "end": v(-40.04, -57.8) * mm});
            skLineSegment(sketch, "E4927", {"start": v(-40.04, -57.8) * mm, "end": v(-40.02, -57.91) * mm});
            skLineSegment(sketch, "E4928", {"start": v(-40.02, -57.91) * mm, "end": v(-40, -58.02) * mm});
            skLineSegment(sketch, "E4929", {"start": v(-40, -58.02) * mm, "end": v(-39.96, -58.05) * mm});
            skLineSegment(sketch, "E4930", {"start": v(-39.96, -58.05) * mm, "end": v(-38.95, -58.27) * mm});
            skLineSegment(sketch, "E4931", {"start": v(-38.95, -58.27) * mm, "end": v(-38.9, -58.25) * mm});
            skLineSegment(sketch, "E4932", {"start": v(-38.9, -58.25) * mm, "end": v(-38.84, -58.17) * mm});
            skLineSegment(sketch, "E4933", {"start": v(-38.84, -58.17) * mm, "end": v(-38.78, -58.08) * mm});
            skLineSegment(sketch, "E4934", {"start": v(-38.78, -58.08) * mm, "end": v(-38.72, -58) * mm});
            skLineSegment(sketch, "E4935", {"start": v(-38.72, -58) * mm, "end": v(-38.66, -57.91) * mm});
            skLineSegment(sketch, "E4936", {"start": v(-38.66, -57.91) * mm, "end": v(-38.6, -57.83) * mm});
            skLineSegment(sketch, "E4937", {"start": v(-38.6, -57.83) * mm, "end": v(-38.55, -57.74) * mm});
            skLineSegment(sketch, "E4938", {"start": v(-38.55, -57.74) * mm, "end": v(-38.5, -57.66) * mm});
            skLineSegment(sketch, "E4939", {"start": v(-38.5, -57.66) * mm, "end": v(-38.44, -57.58) * mm});
            skLineSegment(sketch, "E4940", {"start": v(-38.44, -57.58) * mm, "end": v(-38.38, -57.5) * mm});
            skLineSegment(sketch, "E4941", {"start": v(-38.38, -57.5) * mm, "end": v(-38.33, -57.42) * mm});
            skLineSegment(sketch, "E4942", {"start": v(-38.33, -57.42) * mm, "end": v(-38.28, -57.34) * mm});
            skLineSegment(sketch, "E4943", {"start": v(-38.28, -57.34) * mm, "end": v(-38.23, -57.26) * mm});
            skLineSegment(sketch, "E4944", {"start": v(-38.23, -57.26) * mm, "end": v(-38.18, -57.18) * mm});
            skLineSegment(sketch, "E4945", {"start": v(-38.18, -57.18) * mm, "end": v(-38.14, -57.1) * mm});
            skLineSegment(sketch, "E4946", {"start": v(-38.14, -57.1) * mm, "end": v(-38.09, -57.03) * mm});
            skLineSegment(sketch, "E4947", {"start": v(-38.09, -57.03) * mm, "end": v(-38.04, -56.95) * mm});
            skLineSegment(sketch, "E4948", {"start": v(-38.04, -56.95) * mm, "end": v(-38, -56.88) * mm});
            skLineSegment(sketch, "E4949", {"start": v(-38, -56.88) * mm, "end": v(-37.96, -56.8) * mm});
            skLineSegment(sketch, "E4950", {"start": v(-37.96, -56.8) * mm, "end": v(-37.91, -56.73) * mm});
            skLineSegment(sketch, "E4951", {"start": v(-37.91, -56.73) * mm, "end": v(-37.87, -56.66) * mm});
            skLineSegment(sketch, "E4952", {"start": v(-37.87, -56.66) * mm, "end": v(-37.83, -56.59) * mm});
            skLineSegment(sketch, "E4953", {"start": v(-37.83, -56.59) * mm, "end": v(-37.8, -56.52) * mm});
            skLineSegment(sketch, "E4954", {"start": v(-37.8, -56.52) * mm, "end": v(-37.75, -56.45) * mm});
            skLineSegment(sketch, "E4955", {"start": v(-37.75, -56.45) * mm, "end": v(-37.71, -56.38) * mm});
            skLineSegment(sketch, "E4956", {"start": v(-37.71, -56.38) * mm, "end": v(-37.68, -56.3) * mm});
            skLineSegment(sketch, "E4957", {"start": v(-37.68, -56.3) * mm, "end": v(-37.64, -56.24) * mm});
            skLineSegment(sketch, "E4958", {"start": v(-37.64, -56.24) * mm, "end": v(-37.6, -56.17) * mm});
            skLineSegment(sketch, "E4959", {"start": v(-37.6, -56.17) * mm, "end": v(-37.57, -56.1) * mm});
            skLineSegment(sketch, "E4960", {"start": v(-37.57, -56.1) * mm, "end": v(-37.54, -56.04) * mm});
            skLineSegment(sketch, "E4961", {"start": v(-37.54, -56.04) * mm, "end": v(-37.5, -55.98) * mm});
            skLineSegment(sketch, "E4962", {"start": v(-37.5, -55.98) * mm, "end": v(-37.47, -55.92) * mm});
            skLineSegment(sketch, "E4963", {"start": v(-37.47, -55.92) * mm, "end": v(-37.44, -55.86) * mm});
            skLineSegment(sketch, "E4964", {"start": v(-37.44, -55.86) * mm, "end": v(-37.41, -55.8) * mm});
            skLineSegment(sketch, "E4965", {"start": v(-37.41, -55.8) * mm, "end": v(-37.38, -55.74) * mm});
            skLineSegment(sketch, "E4966", {"start": v(-37.38, -55.74) * mm, "end": v(-37.36, -55.68) * mm});
            skLineSegment(sketch, "E4967", {"start": v(-37.36, -55.68) * mm, "end": v(-37.33, -55.62) * mm});
            skLineSegment(sketch, "E4968", {"start": v(-37.33, -55.62) * mm, "end": v(-37.3, -55.56) * mm});
            skLineSegment(sketch, "E4969", {"start": v(-37.3, -55.56) * mm, "end": v(-37.28, -55.5) * mm});
            skLineSegment(sketch, "E4970", {"start": v(-37.28, -55.5) * mm, "end": v(-37.25, -55.45) * mm});
            skLineSegment(sketch, "E4971", {"start": v(-37.25, -55.45) * mm, "end": v(-37.23, -55.4) * mm});
            skLineSegment(sketch, "E4972", {"start": v(-37.23, -55.4) * mm, "end": v(-37, -55.43) * mm});
            skLineSegment(sketch, "E4973", {"start": v(-37, -55.43) * mm, "end": v(-36.2, -55.56) * mm});
            skLineSegment(sketch, "E4974", {"start": v(-36.2, -55.56) * mm, "end": v(-35.97, -55.6) * mm});
            skLineSegment(sketch, "E4975", {"start": v(-35.97, -55.6) * mm, "end": v(-35.96, -55.67) * mm});
            skLineSegment(sketch, "E4976", {"start": v(-35.96, -55.67) * mm, "end": v(-35.96, -55.73) * mm});
            skLineSegment(sketch, "E4977", {"start": v(-35.96, -55.73) * mm, "end": v(-35.95, -55.79) * mm});
            skLineSegment(sketch, "E4978", {"start": v(-35.95, -55.79) * mm, "end": v(-35.95, -55.85) * mm});
            skLineSegment(sketch, "E4979", {"start": v(-35.95, -55.85) * mm, "end": v(-35.94, -55.92) * mm});
            skLineSegment(sketch, "E4980", {"start": v(-35.94, -55.92) * mm, "end": v(-35.93, -55.98) * mm});
            skLineSegment(sketch, "E4981", {"start": v(-35.93, -55.98) * mm, "end": v(-35.92, -56.05) * mm});
            skLineSegment(sketch, "E4982", {"start": v(-35.92, -56.05) * mm, "end": v(-35.92, -56.11) * mm});
            skLineSegment(sketch, "E4983", {"start": v(-35.92, -56.11) * mm, "end": v(-35.9, -56.18) * mm});
            skLineSegment(sketch, "E4984", {"start": v(-35.9, -56.18) * mm, "end": v(-35.9, -56.25) * mm});
            skLineSegment(sketch, "E4985", {"start": v(-35.9, -56.25) * mm, "end": v(-35.89, -56.32) * mm});
            skLineSegment(sketch, "E4986", {"start": v(-35.89, -56.32) * mm, "end": v(-35.88, -56.4) * mm});
            skLineSegment(sketch, "E4987", {"start": v(-35.88, -56.4) * mm, "end": v(-35.87, -56.47) * mm});
            skLineSegment(sketch, "E4988", {"start": v(-35.87, -56.47) * mm, "end": v(-35.86, -56.54) * mm});
            skLineSegment(sketch, "E4989", {"start": v(-35.86, -56.54) * mm, "end": v(-35.84, -56.62) * mm});
            skLineSegment(sketch, "E4990", {"start": v(-35.84, -56.62) * mm, "end": v(-35.83, -56.7) * mm});
            skLineSegment(sketch, "E4991", {"start": v(-35.83, -56.7) * mm, "end": v(-35.82, -56.77) * mm});
            skLineSegment(sketch, "E4992", {"start": v(-35.82, -56.77) * mm, "end": v(-35.8, -56.85) * mm});
            skLineSegment(sketch, "E4993", {"start": v(-35.8, -56.85) * mm, "end": v(-35.8, -56.93) * mm});
            skLineSegment(sketch, "E4994", {"start": v(-35.8, -56.93) * mm, "end": v(-35.77, -57.01) * mm});
            skLineSegment(sketch, "E4995", {"start": v(-35.77, -57.01) * mm, "end": v(-35.76, -57.1) * mm});
            skLineSegment(sketch, "E4996", {"start": v(-35.76, -57.1) * mm, "end": v(-35.74, -57.18) * mm});
            skLineSegment(sketch, "E4997", {"start": v(-35.74, -57.18) * mm, "end": v(-35.73, -57.26) * mm});
            skLineSegment(sketch, "E4998", {"start": v(-35.73, -57.26) * mm, "end": v(-35.7, -57.35) * mm});
            skLineSegment(sketch, "E4999", {"start": v(-35.7, -57.35) * mm, "end": v(-35.7, -57.43) * mm});
            skLineSegment(sketch, "E5000", {"start": v(-35.7, -57.43) * mm, "end": v(-35.67, -57.52) * mm});
            skLineSegment(sketch, "E5001", {"start": v(-35.67, -57.52) * mm, "end": v(-35.65, -57.6) * mm});
            skLineSegment(sketch, "E5002", {"start": v(-35.65, -57.6) * mm, "end": v(-35.63, -57.7) * mm});
            skLineSegment(sketch, "E5003", {"start": v(-35.63, -57.7) * mm, "end": v(-35.61, -57.79) * mm});
            skLineSegment(sketch, "E5004", {"start": v(-35.61, -57.79) * mm, "end": v(-35.59, -57.88) * mm});
            skLineSegment(sketch, "E5005", {"start": v(-35.59, -57.88) * mm, "end": v(-35.57, -57.97) * mm});
            skLineSegment(sketch, "E5006", {"start": v(-35.57, -57.97) * mm, "end": v(-35.54, -58.07) * mm});
            skLineSegment(sketch, "E5007", {"start": v(-35.54, -58.07) * mm, "end": v(-35.52, -58.16) * mm});
            skLineSegment(sketch, "E5008", {"start": v(-35.52, -58.16) * mm, "end": v(-35.5, -58.26) * mm});
            skLineSegment(sketch, "E5009", {"start": v(-35.5, -58.26) * mm, "end": v(-35.47, -58.36) * mm});
            skLineSegment(sketch, "E5010", {"start": v(-35.47, -58.36) * mm, "end": v(-35.44, -58.45) * mm});
            skLineSegment(sketch, "E5011", {"start": v(-35.44, -58.45) * mm, "end": v(-35.42, -58.55) * mm});
            skLineSegment(sketch, "E5012", {"start": v(-35.42, -58.55) * mm, "end": v(-35.39, -58.65) * mm});
            skLineSegment(sketch, "E5013", {"start": v(-35.39, -58.65) * mm, "end": v(-35.36, -58.76) * mm});
            skLineSegment(sketch, "E5014", {"start": v(-35.36, -58.76) * mm, "end": v(-35.33, -58.86) * mm});
            skLineSegment(sketch, "E5015", {"start": v(-35.33, -58.86) * mm, "end": v(-35.29, -58.89) * mm});
            skLineSegment(sketch, "E5016", {"start": v(-35.29, -58.89) * mm, "end": v(-34.26, -59.01) * mm});
            skLineSegment(sketch, "E5017", {"start": v(-34.26, -59.01) * mm, "end": v(-34.21, -59) * mm});
            skLineSegment(sketch, "E5018", {"start": v(-34.21, -59) * mm, "end": v(-34.16, -58.9) * mm});
            skLineSegment(sketch, "E5019", {"start": v(-34.16, -58.9) * mm, "end": v(-34.1, -58.81) * mm});
            skLineSegment(sketch, "E5020", {"start": v(-34.1, -58.81) * mm, "end": v(-34.05, -58.72) * mm});
            skLineSegment(sketch, "E5021", {"start": v(-34.05, -58.72) * mm, "end": v(-34, -58.63) * mm});
            skLineSegment(sketch, "E5022", {"start": v(-34, -58.63) * mm, "end": v(-33.95, -58.54) * mm});
            skLineSegment(sketch, "E5023", {"start": v(-33.95, -58.54) * mm, "end": v(-33.9, -58.46) * mm});
            skLineSegment(sketch, "E5024", {"start": v(-33.9, -58.46) * mm, "end": v(-33.86, -58.37) * mm});
            skLineSegment(sketch, "E5025", {"start": v(-33.86, -58.37) * mm, "end": v(-33.81, -58.28) * mm});
            skLineSegment(sketch, "E5026", {"start": v(-33.81, -58.28) * mm, "end": v(-33.77, -58.2) * mm});
            skLineSegment(sketch, "E5027", {"start": v(-33.77, -58.2) * mm, "end": v(-33.72, -58.11) * mm});
            skLineSegment(sketch, "E5028", {"start": v(-33.72, -58.11) * mm, "end": v(-33.68, -58.03) * mm});
            skLineSegment(sketch, "E5029", {"start": v(-33.68, -58.03) * mm, "end": v(-33.64, -57.94) * mm});
            skLineSegment(sketch, "E5030", {"start": v(-33.64, -57.94) * mm, "end": v(-33.6, -57.86) * mm});
            skLineSegment(sketch, "E5031", {"start": v(-33.6, -57.86) * mm, "end": v(-33.55, -57.78) * mm});
            skLineSegment(sketch, "E5032", {"start": v(-33.55, -57.78) * mm, "end": v(-33.51, -57.7) * mm});
            skLineSegment(sketch, "E5033", {"start": v(-33.51, -57.7) * mm, "end": v(-33.48, -57.62) * mm});
            skLineSegment(sketch, "E5034", {"start": v(-33.48, -57.62) * mm, "end": v(-33.44, -57.54) * mm});
            skLineSegment(sketch, "E5035", {"start": v(-33.44, -57.54) * mm, "end": v(-33.4, -57.47) * mm});
            skLineSegment(sketch, "E5036", {"start": v(-33.4, -57.47) * mm, "end": v(-33.37, -57.39) * mm});
            skLineSegment(sketch, "E5037", {"start": v(-33.37, -57.39) * mm, "end": v(-33.33, -57.31) * mm});
            skLineSegment(sketch, "E5038", {"start": v(-33.33, -57.31) * mm, "end": v(-33.3, -57.24) * mm});
            skLineSegment(sketch, "E5039", {"start": v(-33.3, -57.24) * mm, "end": v(-33.26, -57.16) * mm});
            skLineSegment(sketch, "E5040", {"start": v(-33.26, -57.16) * mm, "end": v(-33.23, -57.1) * mm});
            skLineSegment(sketch, "E5041", {"start": v(-33.23, -57.1) * mm, "end": v(-33.2, -57.02) * mm});
            skLineSegment(sketch, "E5042", {"start": v(-33.2, -57.02) * mm, "end": v(-33.17, -56.95) * mm});
            skLineSegment(sketch, "E5043", {"start": v(-33.17, -56.95) * mm, "end": v(-33.14, -56.88) * mm});
            skLineSegment(sketch, "E5044", {"start": v(-33.14, -56.88) * mm, "end": v(-33.1, -56.8) * mm});
            skLineSegment(sketch, "E5045", {"start": v(-33.1, -56.8) * mm, "end": v(-33.08, -56.74) * mm});
            skLineSegment(sketch, "E5046", {"start": v(-33.08, -56.74) * mm, "end": v(-33.05, -56.67) * mm});
            skLineSegment(sketch, "E5047", {"start": v(-33.05, -56.67) * mm, "end": v(-33.03, -56.6) * mm});
            skLineSegment(sketch, "E5048", {"start": v(-33.03, -56.6) * mm, "end": v(-33, -56.54) * mm});
            skLineSegment(sketch, "E5049", {"start": v(-33, -56.54) * mm, "end": v(-32.98, -56.48) * mm});
            skLineSegment(sketch, "E5050", {"start": v(-32.98, -56.48) * mm, "end": v(-32.95, -56.41) * mm});
            skLineSegment(sketch, "E5051", {"start": v(-32.95, -56.41) * mm, "end": v(-32.93, -56.35) * mm});
            skLineSegment(sketch, "E5052", {"start": v(-32.93, -56.35) * mm, "end": v(-32.9, -56.29) * mm});
            skLineSegment(sketch, "E5053", {"start": v(-32.9, -56.29) * mm, "end": v(-32.88, -56.23) * mm});
            skLineSegment(sketch, "E5054", {"start": v(-32.88, -56.23) * mm, "end": v(-32.86, -56.17) * mm});
            skLineSegment(sketch, "E5055", {"start": v(-32.86, -56.17) * mm, "end": v(-32.84, -56.11) * mm});
            skLineSegment(sketch, "E5056", {"start": v(-32.84, -56.11) * mm, "end": v(-32.82, -56.05) * mm});
            skLineSegment(sketch, "E5057", {"start": v(-32.82, -56.05) * mm, "end": v(-32.8, -56) * mm});
            skLineSegment(sketch, "E5058", {"start": v(-32.8, -56) * mm, "end": v(-32.57, -56) * mm});
            skLineSegment(sketch, "E5059", {"start": v(-32.57, -56) * mm, "end": v(-31.76, -56.07) * mm});
            skLineSegment(sketch, "E5060", {"start": v(-31.76, -56.07) * mm, "end": v(-31.53, -56.1) * mm});
            skLineSegment(sketch, "E5061", {"start": v(-31.53, -56.1) * mm, "end": v(-31.52, -56.15) * mm});
            skLineSegment(sketch, "E5062", {"start": v(-31.52, -56.15) * mm, "end": v(-31.5, -56.21) * mm});
            skLineSegment(sketch, "E5063", {"start": v(-31.5, -56.21) * mm, "end": v(-31.5, -56.27) * mm});
            skLineSegment(sketch, "E5064", {"start": v(-31.5, -56.27) * mm, "end": v(-31.49, -56.34) * mm});
            skLineSegment(sketch, "E5065", {"start": v(-31.49, -56.34) * mm, "end": v(-31.47, -56.4) * mm});
            skLineSegment(sketch, "E5066", {"start": v(-31.47, -56.4) * mm, "end": v(-31.46, -56.46) * mm});
            skLineSegment(sketch, "E5067", {"start": v(-31.46, -56.46) * mm, "end": v(-31.45, -56.53) * mm});
            skLineSegment(sketch, "E5068", {"start": v(-31.45, -56.53) * mm, "end": v(-31.43, -56.6) * mm});
            skLineSegment(sketch, "E5069", {"start": v(-31.43, -56.6) * mm, "end": v(-31.42, -56.66) * mm});
            skLineSegment(sketch, "E5070", {"start": v(-31.42, -56.66) * mm, "end": v(-31.4, -56.73) * mm});
            skLineSegment(sketch, "E5071", {"start": v(-31.4, -56.73) * mm, "end": v(-31.39, -56.8) * mm});
            skLineSegment(sketch, "E5072", {"start": v(-31.39, -56.8) * mm, "end": v(-31.37, -56.87) * mm});
            skLineSegment(sketch, "E5073", {"start": v(-31.37, -56.87) * mm, "end": v(-31.35, -56.94) * mm});
            skLineSegment(sketch, "E5074", {"start": v(-31.35, -56.94) * mm, "end": v(-31.33, -57.02) * mm});
            skLineSegment(sketch, "E5075", {"start": v(-31.33, -57.02) * mm, "end": v(-31.31, -57.1) * mm});
            skLineSegment(sketch, "E5076", {"start": v(-31.31, -57.1) * mm, "end": v(-31.3, -57.17) * mm});
            skLineSegment(sketch, "E5077", {"start": v(-31.3, -57.17) * mm, "end": v(-31.28, -57.24) * mm});
            skLineSegment(sketch, "E5078", {"start": v(-31.28, -57.24) * mm, "end": v(-31.25, -57.32) * mm});
            skLineSegment(sketch, "E5079", {"start": v(-31.25, -57.32) * mm, "end": v(-31.23, -57.4) * mm});
            skLineSegment(sketch, "E5080", {"start": v(-31.23, -57.4) * mm, "end": v(-31.21, -57.48) * mm});
            skLineSegment(sketch, "E5081", {"start": v(-31.21, -57.48) * mm, "end": v(-31.19, -57.56) * mm});
            skLineSegment(sketch, "E5082", {"start": v(-31.19, -57.56) * mm, "end": v(-31.16, -57.64) * mm});
            skLineSegment(sketch, "E5083", {"start": v(-31.16, -57.64) * mm, "end": v(-31.14, -57.72) * mm});
            skLineSegment(sketch, "E5084", {"start": v(-31.14, -57.72) * mm, "end": v(-31.12, -57.8) * mm});
            skLineSegment(sketch, "E5085", {"start": v(-31.12, -57.8) * mm, "end": v(-31.09, -57.89) * mm});
            skLineSegment(sketch, "E5086", {"start": v(-31.09, -57.89) * mm, "end": v(-31.06, -57.98) * mm});
            skLineSegment(sketch, "E5087", {"start": v(-31.06, -57.98) * mm, "end": v(-31.04, -58.06) * mm});
            skLineSegment(sketch, "E5088", {"start": v(-31.04, -58.06) * mm, "end": v(-31, -58.15) * mm});
            skLineSegment(sketch, "E5089", {"start": v(-31, -58.15) * mm, "end": v(-30.98, -58.24) * mm});
            skLineSegment(sketch, "E5090", {"start": v(-30.98, -58.24) * mm, "end": v(-30.95, -58.33) * mm});
            skLineSegment(sketch, "E5091", {"start": v(-30.95, -58.33) * mm, "end": v(-30.92, -58.42) * mm});
            skLineSegment(sketch, "E5092", {"start": v(-30.92, -58.42) * mm, "end": v(-30.89, -58.5) * mm});
            skLineSegment(sketch, "E5093", {"start": v(-30.89, -58.5) * mm, "end": v(-30.85, -58.6) * mm});
            skLineSegment(sketch, "E5094", {"start": v(-30.85, -58.6) * mm, "end": v(-30.82, -58.7) * mm});
            skLineSegment(sketch, "E5095", {"start": v(-30.82, -58.7) * mm, "end": v(-30.79, -58.79) * mm});
            skLineSegment(sketch, "E5096", {"start": v(-30.79, -58.79) * mm, "end": v(-30.75, -58.88) * mm});
            skLineSegment(sketch, "E5097", {"start": v(-30.75, -58.88) * mm, "end": v(-30.72, -58.98) * mm});
            skLineSegment(sketch, "E5098", {"start": v(-30.72, -58.98) * mm, "end": v(-30.68, -59.08) * mm});
            skLineSegment(sketch, "E5099", {"start": v(-30.68, -59.08) * mm, "end": v(-30.64, -59.18) * mm});
            skLineSegment(sketch, "E5100", {"start": v(-30.64, -59.18) * mm, "end": v(-30.6, -59.28) * mm});
            skLineSegment(sketch, "E5101", {"start": v(-30.6, -59.28) * mm, "end": v(-30.56, -59.3) * mm});
            skLineSegment(sketch, "E5102", {"start": v(-30.56, -59.3) * mm, "end": v(-29.52, -59.34) * mm});
            skLineSegment(sketch, "E5103", {"start": v(-29.52, -59.34) * mm, "end": v(-29.48, -59.31) * mm});
            skLineSegment(sketch, "E5104", {"start": v(-29.48, -59.31) * mm, "end": v(-29.43, -59.22) * mm});
            skLineSegment(sketch, "E5105", {"start": v(-29.43, -59.22) * mm, "end": v(-29.39, -59.12) * mm});
            skLineSegment(sketch, "E5106", {"start": v(-29.39, -59.12) * mm, "end": v(-29.34, -59.03) * mm});
            skLineSegment(sketch, "E5107", {"start": v(-29.34, -59.03) * mm, "end": v(-29.3, -58.93) * mm});
            skLineSegment(sketch, "E5108", {"start": v(-29.3, -58.93) * mm, "end": v(-29.26, -58.84) * mm});
            skLineSegment(sketch, "E5109", {"start": v(-29.26, -58.84) * mm, "end": v(-29.22, -58.75) * mm});
            skLineSegment(sketch, "E5110", {"start": v(-29.22, -58.75) * mm, "end": v(-29.18, -58.66) * mm});
            skLineSegment(sketch, "E5111", {"start": v(-29.18, -58.66) * mm, "end": v(-29.14, -58.57) * mm});
            skLineSegment(sketch, "E5112", {"start": v(-29.14, -58.57) * mm, "end": v(-29.1, -58.48) * mm});
            skLineSegment(sketch, "E5113", {"start": v(-29.1, -58.48) * mm, "end": v(-29.07, -58.39) * mm});
            skLineSegment(sketch, "E5114", {"start": v(-29.07, -58.39) * mm, "end": v(-29.03, -58.3) * mm});
            skLineSegment(sketch, "E5115", {"start": v(-29.03, -58.3) * mm, "end": v(-29, -58.21) * mm});
            skLineSegment(sketch, "E5116", {"start": v(-29, -58.21) * mm, "end": v(-28.96, -58.13) * mm});
            skLineSegment(sketch, "E5117", {"start": v(-28.96, -58.13) * mm, "end": v(-28.93, -58.04) * mm});
            skLineSegment(sketch, "E5118", {"start": v(-28.93, -58.04) * mm, "end": v(-28.9, -57.96) * mm});
            skLineSegment(sketch, "E5119", {"start": v(-28.9, -57.96) * mm, "end": v(-28.87, -57.88) * mm});
            skLineSegment(sketch, "E5120", {"start": v(-28.87, -57.88) * mm, "end": v(-28.84, -57.8) * mm});
            skLineSegment(sketch, "E5121", {"start": v(-28.84, -57.8) * mm, "end": v(-28.8, -57.72) * mm});
            skLineSegment(sketch, "E5122", {"start": v(-28.8, -57.72) * mm, "end": v(-28.78, -57.64) * mm});
            skLineSegment(sketch, "E5123", {"start": v(-28.78, -57.64) * mm, "end": v(-28.75, -57.56) * mm});
            skLineSegment(sketch, "E5124", {"start": v(-28.75, -57.56) * mm, "end": v(-28.72, -57.48) * mm});
            skLineSegment(sketch, "E5125", {"start": v(-28.72, -57.48) * mm, "end": v(-28.7, -57.4) * mm});
            skLineSegment(sketch, "E5126", {"start": v(-28.7, -57.4) * mm, "end": v(-28.67, -57.33) * mm});
            skLineSegment(sketch, "E5127", {"start": v(-28.67, -57.33) * mm, "end": v(-28.65, -57.25) * mm});
            skLineSegment(sketch, "E5128", {"start": v(-28.65, -57.25) * mm, "end": v(-28.62, -57.18) * mm});
            skLineSegment(sketch, "E5129", {"start": v(-28.62, -57.18) * mm, "end": v(-28.6, -57.1) * mm});
            skLineSegment(sketch, "E5130", {"start": v(-28.6, -57.1) * mm, "end": v(-28.58, -57.03) * mm});
            skLineSegment(sketch, "E5131", {"start": v(-28.58, -57.03) * mm, "end": v(-28.55, -56.96) * mm});
            skLineSegment(sketch, "E5132", {"start": v(-28.55, -56.96) * mm, "end": v(-28.53, -56.9) * mm});
            skLineSegment(sketch, "E5133", {"start": v(-28.53, -56.9) * mm, "end": v(-28.51, -56.83) * mm});
            skLineSegment(sketch, "E5134", {"start": v(-28.51, -56.83) * mm, "end": v(-28.5, -56.76) * mm});
            skLineSegment(sketch, "E5135", {"start": v(-28.5, -56.76) * mm, "end": v(-28.47, -56.7) * mm});
            skLineSegment(sketch, "E5136", {"start": v(-28.47, -56.7) * mm, "end": v(-28.45, -56.63) * mm});
            skLineSegment(sketch, "E5137", {"start": v(-28.45, -56.63) * mm, "end": v(-28.44, -56.56) * mm});
            skLineSegment(sketch, "E5138", {"start": v(-28.44, -56.56) * mm, "end": v(-28.42, -56.5) * mm});
            skLineSegment(sketch, "E5139", {"start": v(-28.42, -56.5) * mm, "end": v(-28.4, -56.44) * mm});
            skLineSegment(sketch, "E5140", {"start": v(-28.4, -56.44) * mm, "end": v(-28.39, -56.38) * mm});
            skLineSegment(sketch, "E5141", {"start": v(-28.39, -56.38) * mm, "end": v(-28.37, -56.32) * mm});
            skLineSegment(sketch, "E5142", {"start": v(-28.37, -56.32) * mm, "end": v(-28.35, -56.26) * mm});
            skLineSegment(sketch, "E5143", {"start": v(-28.35, -56.26) * mm, "end": v(-28.34, -56.2) * mm});
            skLineSegment(sketch, "E5144", {"start": v(-28.34, -56.2) * mm, "end": v(-28.1, -56.19) * mm});
            skLineSegment(sketch, "E5145", {"start": v(-28.1, -56.19) * mm, "end": v(-27.3, -56.18) * mm});
            skLineSegment(sketch, "E5146", {"start": v(-27.3, -56.18) * mm, "end": v(-27.07, -56.18) * mm});
            skLineSegment(sketch, "E5147", {"start": v(-27.07, -56.18) * mm, "end": v(-27.05, -56.24) * mm});
            skLineSegment(sketch, "E5148", {"start": v(-27.05, -56.24) * mm, "end": v(-27.03, -56.3) * mm});
            skLineSegment(sketch, "E5149", {"start": v(-27.03, -56.3) * mm, "end": v(-27.02, -56.36) * mm});
            skLineSegment(sketch, "E5150", {"start": v(-27.02, -56.36) * mm, "end": v(-27, -56.42) * mm});
            skLineSegment(sketch, "E5151", {"start": v(-27, -56.42) * mm, "end": v(-26.98, -56.48) * mm});
            skLineSegment(sketch, "E5152", {"start": v(-26.98, -56.48) * mm, "end": v(-26.96, -56.54) * mm});
            skLineSegment(sketch, "E5153", {"start": v(-26.96, -56.54) * mm, "end": v(-26.94, -56.6) * mm});
            skLineSegment(sketch, "E5154", {"start": v(-26.94, -56.6) * mm, "end": v(-26.92, -56.67) * mm});
            skLineSegment(sketch, "E5155", {"start": v(-26.92, -56.67) * mm, "end": v(-26.9, -56.74) * mm});
            skLineSegment(sketch, "E5156", {"start": v(-26.9, -56.74) * mm, "end": v(-26.88, -56.8) * mm});
            skLineSegment(sketch, "E5157", {"start": v(-26.88, -56.8) * mm, "end": v(-26.86, -56.87) * mm});
            skLineSegment(sketch, "E5158", {"start": v(-26.86, -56.87) * mm, "end": v(-26.84, -56.94) * mm});
            skLineSegment(sketch, "E5159", {"start": v(-26.84, -56.94) * mm, "end": v(-26.81, -57.01) * mm});
            skLineSegment(sketch, "E5160", {"start": v(-26.81, -57.01) * mm, "end": v(-26.79, -57.08) * mm});
            skLineSegment(sketch, "E5161", {"start": v(-26.79, -57.08) * mm, "end": v(-26.76, -57.16) * mm});
            skLineSegment(sketch, "E5162", {"start": v(-26.76, -57.16) * mm, "end": v(-26.74, -57.23) * mm});
            skLineSegment(sketch, "E5163", {"start": v(-26.74, -57.23) * mm, "end": v(-26.7, -57.3) * mm});
            skLineSegment(sketch, "E5164", {"start": v(-26.7, -57.3) * mm, "end": v(-26.68, -57.38) * mm});
            skLineSegment(sketch, "E5165", {"start": v(-26.68, -57.38) * mm, "end": v(-26.65, -57.45) * mm});
            skLineSegment(sketch, "E5166", {"start": v(-26.65, -57.45) * mm, "end": v(-26.62, -57.53) * mm});
            skLineSegment(sketch, "E5167", {"start": v(-26.62, -57.53) * mm, "end": v(-26.6, -57.6) * mm});
            skLineSegment(sketch, "E5168", {"start": v(-26.6, -57.6) * mm, "end": v(-26.56, -57.69) * mm});
            skLineSegment(sketch, "E5169", {"start": v(-26.56, -57.69) * mm, "end": v(-26.53, -57.77) * mm});
            skLineSegment(sketch, "E5170", {"start": v(-26.53, -57.77) * mm, "end": v(-26.5, -57.85) * mm});
            skLineSegment(sketch, "E5171", {"start": v(-26.5, -57.85) * mm, "end": v(-26.47, -57.93) * mm});
            skLineSegment(sketch, "E5172", {"start": v(-26.47, -57.93) * mm, "end": v(-26.43, -58.01) * mm});
            skLineSegment(sketch, "E5173", {"start": v(-26.43, -58.01) * mm, "end": v(-26.4, -58.1) * mm});
            skLineSegment(sketch, "E5174", {"start": v(-26.4, -58.1) * mm, "end": v(-26.36, -58.18) * mm});
            skLineSegment(sketch, "E5175", {"start": v(-26.36, -58.18) * mm, "end": v(-26.32, -58.27) * mm});
            skLineSegment(sketch, "E5176", {"start": v(-26.32, -58.27) * mm, "end": v(-26.29, -58.35) * mm});
            skLineSegment(sketch, "E5177", {"start": v(-26.29, -58.35) * mm, "end": v(-26.25, -58.44) * mm});
            skLineSegment(sketch, "E5178", {"start": v(-26.25, -58.44) * mm, "end": v(-26.2, -58.53) * mm});
            skLineSegment(sketch, "E5179", {"start": v(-26.2, -58.53) * mm, "end": v(-26.17, -58.62) * mm});
            skLineSegment(sketch, "E5180", {"start": v(-26.17, -58.62) * mm, "end": v(-26.13, -58.7) * mm});
            skLineSegment(sketch, "E5181", {"start": v(-26.13, -58.7) * mm, "end": v(-26.08, -58.8) * mm});
            skLineSegment(sketch, "E5182", {"start": v(-26.08, -58.8) * mm, "end": v(-26.04, -58.9) * mm});
            skLineSegment(sketch, "E5183", {"start": v(-26.04, -58.9) * mm, "end": v(-26, -58.98) * mm});
            skLineSegment(sketch, "E5184", {"start": v(-26, -58.98) * mm, "end": v(-25.95, -59.08) * mm});
            skLineSegment(sketch, "E5185", {"start": v(-25.95, -59.08) * mm, "end": v(-25.9, -59.17) * mm});
            skLineSegment(sketch, "E5186", {"start": v(-25.9, -59.17) * mm, "end": v(-25.86, -59.27) * mm});
            skLineSegment(sketch, "E5187", {"start": v(-25.86, -59.27) * mm, "end": v(-25.81, -59.3) * mm});
            skLineSegment(sketch, "E5188", {"start": v(-25.81, -59.3) * mm, "end": v(-24.77, -59.23) * mm});
            skLineSegment(sketch, "E5189", {"start": v(-24.77, -59.23) * mm, "end": v(-24.73, -59.2) * mm});
            skLineSegment(sketch, "E5190", {"start": v(-24.73, -59.2) * mm, "end": v(-24.7, -59.1) * mm});
            skLineSegment(sketch, "E5191", {"start": v(-24.7, -59.1) * mm, "end": v(-24.66, -59) * mm});
            skLineSegment(sketch, "E5192", {"start": v(-24.66, -59) * mm, "end": v(-24.62, -58.9) * mm});
            skLineSegment(sketch, "E5193", {"start": v(-24.62, -58.9) * mm, "end": v(-24.6, -58.8) * mm});
            skLineSegment(sketch, "E5194", {"start": v(-24.6, -58.8) * mm, "end": v(-24.56, -58.71) * mm});
            skLineSegment(sketch, "E5195", {"start": v(-24.56, -58.71) * mm, "end": v(-24.53, -58.62) * mm});
            skLineSegment(sketch, "E5196", {"start": v(-24.53, -58.62) * mm, "end": v(-24.5, -58.52) * mm});
            skLineSegment(sketch, "E5197", {"start": v(-24.5, -58.52) * mm, "end": v(-24.47, -58.43) * mm});
            skLineSegment(sketch, "E5198", {"start": v(-24.47, -58.43) * mm, "end": v(-24.44, -58.34) * mm});
            skLineSegment(sketch, "E5199", {"start": v(-24.44, -58.34) * mm, "end": v(-24.4, -58.25) * mm});
            skLineSegment(sketch, "E5200", {"start": v(-24.4, -58.25) * mm, "end": v(-24.38, -58.16) * mm});
            skLineSegment(sketch, "E5201", {"start": v(-24.38, -58.16) * mm, "end": v(-24.35, -58.07) * mm});
            skLineSegment(sketch, "E5202", {"start": v(-24.35, -58.07) * mm, "end": v(-24.33, -57.98) * mm});
            skLineSegment(sketch, "E5203", {"start": v(-24.33, -57.98) * mm, "end": v(-24.3, -57.9) * mm});
            skLineSegment(sketch, "E5204", {"start": v(-24.3, -57.9) * mm, "end": v(-24.28, -57.8) * mm});
            skLineSegment(sketch, "E5205", {"start": v(-24.28, -57.8) * mm, "end": v(-24.25, -57.72) * mm});
            skLineSegment(sketch, "E5206", {"start": v(-24.25, -57.72) * mm, "end": v(-24.23, -57.64) * mm});
            skLineSegment(sketch, "E5207", {"start": v(-24.23, -57.64) * mm, "end": v(-24.2, -57.55) * mm});
            skLineSegment(sketch, "E5208", {"start": v(-24.2, -57.55) * mm, "end": v(-24.19, -57.47) * mm});
            skLineSegment(sketch, "E5209", {"start": v(-24.19, -57.47) * mm, "end": v(-24.17, -57.4) * mm});
            skLineSegment(sketch, "E5210", {"start": v(-24.17, -57.4) * mm, "end": v(-24.15, -57.31) * mm});
            skLineSegment(sketch, "E5211", {"start": v(-24.15, -57.31) * mm, "end": v(-24.13, -57.23) * mm});
            skLineSegment(sketch, "E5212", {"start": v(-24.13, -57.23) * mm, "end": v(-24.1, -57.15) * mm});
            skLineSegment(sketch, "E5213", {"start": v(-24.1, -57.15) * mm, "end": v(-24.09, -57.08) * mm});
            skLineSegment(sketch, "E5214", {"start": v(-24.09, -57.08) * mm, "end": v(-24.07, -57) * mm});
            skLineSegment(sketch, "E5215", {"start": v(-24.07, -57) * mm, "end": v(-24.05, -56.93) * mm});
            skLineSegment(sketch, "E5216", {"start": v(-24.05, -56.93) * mm, "end": v(-24.04, -56.85) * mm});
            skLineSegment(sketch, "E5217", {"start": v(-24.04, -56.85) * mm, "end": v(-24.02, -56.78) * mm});
            skLineSegment(sketch, "E5218", {"start": v(-24.02, -56.78) * mm, "end": v(-24, -56.71) * mm});
            skLineSegment(sketch, "E5219", {"start": v(-24, -56.71) * mm, "end": v(-24, -56.64) * mm});
            skLineSegment(sketch, "E5220", {"start": v(-24, -56.64) * mm, "end": v(-23.98, -56.57) * mm});
            skLineSegment(sketch, "E5221", {"start": v(-23.98, -56.57) * mm, "end": v(-23.97, -56.5) * mm});
            skLineSegment(sketch, "E5222", {"start": v(-23.97, -56.5) * mm, "end": v(-23.95, -56.44) * mm});
            skLineSegment(sketch, "E5223", {"start": v(-23.95, -56.44) * mm, "end": v(-23.94, -56.37) * mm});
            skLineSegment(sketch, "E5224", {"start": v(-23.94, -56.37) * mm, "end": v(-23.93, -56.3) * mm});
            skLineSegment(sketch, "E5225", {"start": v(-23.93, -56.3) * mm, "end": v(-23.92, -56.24) * mm});
            skLineSegment(sketch, "E5226", {"start": v(-23.92, -56.24) * mm, "end": v(-23.9, -56.18) * mm});
            skLineSegment(sketch, "E5227", {"start": v(-23.9, -56.18) * mm, "end": v(-23.9, -56.12) * mm});
            skLineSegment(sketch, "E5228", {"start": v(-23.9, -56.12) * mm, "end": v(-23.89, -56.06) * mm});
            skLineSegment(sketch, "E5229", {"start": v(-23.89, -56.06) * mm, "end": v(-23.88, -56) * mm});
            skLineSegment(sketch, "E5230", {"start": v(-23.88, -56) * mm, "end": v(-23.65, -55.97) * mm});
            skLineSegment(sketch, "E5231", {"start": v(-23.65, -55.97) * mm, "end": v(-22.85, -55.89) * mm});
            skLineSegment(sketch, "E5232", {"start": v(-22.85, -55.89) * mm, "end": v(-22.61, -55.87) * mm});
            skLineSegment(sketch, "E5233", {"start": v(-22.61, -55.87) * mm, "end": v(-22.6, -55.93) * mm});
            skLineSegment(sketch, "E5234", {"start": v(-22.6, -55.93) * mm, "end": v(-22.57, -55.99) * mm});
            skLineSegment(sketch, "E5235", {"start": v(-22.57, -55.99) * mm, "end": v(-22.55, -56.04) * mm});
            skLineSegment(sketch, "E5236", {"start": v(-22.55, -56.04) * mm, "end": v(-22.52, -56.1) * mm});
            skLineSegment(sketch, "E5237", {"start": v(-22.52, -56.1) * mm, "end": v(-22.5, -56.16) * mm});
            skLineSegment(sketch, "E5238", {"start": v(-22.5, -56.16) * mm, "end": v(-22.48, -56.22) * mm});
            skLineSegment(sketch, "E5239", {"start": v(-22.48, -56.22) * mm, "end": v(-22.45, -56.28) * mm});
            skLineSegment(sketch, "E5240", {"start": v(-22.45, -56.28) * mm, "end": v(-22.43, -56.35) * mm});
            skLineSegment(sketch, "E5241", {"start": v(-22.43, -56.35) * mm, "end": v(-22.4, -56.41) * mm});
            skLineSegment(sketch, "E5242", {"start": v(-22.4, -56.41) * mm, "end": v(-22.37, -56.48) * mm});
            skLineSegment(sketch, "E5243", {"start": v(-22.37, -56.48) * mm, "end": v(-22.34, -56.54) * mm});
            skLineSegment(sketch, "E5244", {"start": v(-22.34, -56.54) * mm, "end": v(-22.31, -56.6) * mm});
            skLineSegment(sketch, "E5245", {"start": v(-22.31, -56.6) * mm, "end": v(-22.28, -56.67) * mm});
            skLineSegment(sketch, "E5246", {"start": v(-22.28, -56.67) * mm, "end": v(-22.25, -56.74) * mm});
            skLineSegment(sketch, "E5247", {"start": v(-22.25, -56.74) * mm, "end": v(-22.22, -56.81) * mm});
            skLineSegment(sketch, "E5248", {"start": v(-22.22, -56.81) * mm, "end": v(-22.19, -56.88) * mm});
            skLineSegment(sketch, "E5249", {"start": v(-22.19, -56.88) * mm, "end": v(-22.16, -56.95) * mm});
            skLineSegment(sketch, "E5250", {"start": v(-22.16, -56.95) * mm, "end": v(-22.12, -57.03) * mm});
            skLineSegment(sketch, "E5251", {"start": v(-22.12, -57.03) * mm, "end": v(-22.09, -57.1) * mm});
            skLineSegment(sketch, "E5252", {"start": v(-22.09, -57.1) * mm, "end": v(-22.05, -57.17) * mm});
            skLineSegment(sketch, "E5253", {"start": v(-22.05, -57.17) * mm, "end": v(-22.01, -57.25) * mm});
            skLineSegment(sketch, "E5254", {"start": v(-22.01, -57.25) * mm, "end": v(-21.98, -57.33) * mm});
            skLineSegment(sketch, "E5255", {"start": v(-21.98, -57.33) * mm, "end": v(-21.94, -57.4) * mm});
            skLineSegment(sketch, "E5256", {"start": v(-21.94, -57.4) * mm, "end": v(-21.9, -57.48) * mm});
            skLineSegment(sketch, "E5257", {"start": v(-21.9, -57.48) * mm, "end": v(-21.86, -57.56) * mm});
            skLineSegment(sketch, "E5258", {"start": v(-21.86, -57.56) * mm, "end": v(-21.82, -57.64) * mm});
            skLineSegment(sketch, "E5259", {"start": v(-21.82, -57.64) * mm, "end": v(-21.77, -57.72) * mm});
            skLineSegment(sketch, "E5260", {"start": v(-21.77, -57.72) * mm, "end": v(-21.73, -57.8) * mm});
            skLineSegment(sketch, "E5261", {"start": v(-21.73, -57.8) * mm, "end": v(-21.69, -57.88) * mm});
            skLineSegment(sketch, "E5262", {"start": v(-21.69, -57.88) * mm, "end": v(-21.64, -57.96) * mm});
            skLineSegment(sketch, "E5263", {"start": v(-21.64, -57.96) * mm, "end": v(-21.6, -58.05) * mm});
            skLineSegment(sketch, "E5264", {"start": v(-21.6, -58.05) * mm, "end": v(-21.55, -58.13) * mm});
            skLineSegment(sketch, "E5265", {"start": v(-21.55, -58.13) * mm, "end": v(-21.5, -58.22) * mm});
            skLineSegment(sketch, "E5266", {"start": v(-21.5, -58.22) * mm, "end": v(-21.45, -58.3) * mm});
            skLineSegment(sketch, "E5267", {"start": v(-21.45, -58.3) * mm, "end": v(-21.4, -58.39) * mm});
            skLineSegment(sketch, "E5268", {"start": v(-21.4, -58.39) * mm, "end": v(-21.35, -58.48) * mm});
            skLineSegment(sketch, "E5269", {"start": v(-21.35, -58.48) * mm, "end": v(-21.3, -58.57) * mm});
            skLineSegment(sketch, "E5270", {"start": v(-21.3, -58.57) * mm, "end": v(-21.24, -58.65) * mm});
            skLineSegment(sketch, "E5271", {"start": v(-21.24, -58.65) * mm, "end": v(-21.19, -58.74) * mm});
            skLineSegment(sketch, "E5272", {"start": v(-21.19, -58.74) * mm, "end": v(-21.13, -58.84) * mm});
            skLineSegment(sketch, "E5273", {"start": v(-21.13, -58.84) * mm, "end": v(-21.08, -58.85) * mm});
            skLineSegment(sketch, "E5274", {"start": v(-21.08, -58.85) * mm, "end": v(-20.05, -58.7) * mm});
            skLineSegment(sketch, "E5275", {"start": v(-20.05, -58.7) * mm, "end": v(-20.01, -58.67) * mm});
            skLineSegment(sketch, "E5276", {"start": v(-20.01, -58.67) * mm, "end": v(-19.99, -58.57) * mm});
            skLineSegment(sketch, "E5277", {"start": v(-19.99, -58.57) * mm, "end": v(-19.96, -58.47) * mm});
            skLineSegment(sketch, "E5278", {"start": v(-19.96, -58.47) * mm, "end": v(-19.94, -58.36) * mm});
            skLineSegment(sketch, "E5279", {"start": v(-19.94, -58.36) * mm, "end": v(-19.91, -58.27) * mm});
            skLineSegment(sketch, "E5280", {"start": v(-19.91, -58.27) * mm, "end": v(-19.89, -58.17) * mm});
            skLineSegment(sketch, "E5281", {"start": v(-19.89, -58.17) * mm, "end": v(-19.86, -58.07) * mm});
            skLineSegment(sketch, "E5282", {"start": v(-19.86, -58.07) * mm, "end": v(-19.84, -57.97) * mm});
            skLineSegment(sketch, "E5283", {"start": v(-19.84, -57.97) * mm, "end": v(-19.82, -57.88) * mm});
            skLineSegment(sketch, "E5284", {"start": v(-19.82, -57.88) * mm, "end": v(-19.8, -57.78) * mm});
            skLineSegment(sketch, "E5285", {"start": v(-19.8, -57.78) * mm, "end": v(-19.78, -57.69) * mm});
            skLineSegment(sketch, "E5286", {"start": v(-19.78, -57.69) * mm, "end": v(-19.76, -57.6) * mm});
            skLineSegment(sketch, "E5287", {"start": v(-19.76, -57.6) * mm, "end": v(-19.74, -57.5) * mm});
            skLineSegment(sketch, "E5288", {"start": v(-19.74, -57.5) * mm, "end": v(-19.72, -57.41) * mm});
            skLineSegment(sketch, "E5289", {"start": v(-19.72, -57.41) * mm, "end": v(-19.7, -57.33) * mm});
            skLineSegment(sketch, "E5290", {"start": v(-19.7, -57.33) * mm, "end": v(-19.69, -57.24) * mm});
            skLineSegment(sketch, "E5291", {"start": v(-19.69, -57.24) * mm, "end": v(-19.67, -57.15) * mm});
            skLineSegment(sketch, "E5292", {"start": v(-19.67, -57.15) * mm, "end": v(-19.66, -57.06) * mm});
            skLineSegment(sketch, "E5293", {"start": v(-19.66, -57.06) * mm, "end": v(-19.64, -56.98) * mm});
            skLineSegment(sketch, "E5294", {"start": v(-19.64, -56.98) * mm, "end": v(-19.63, -56.9) * mm});
            skLineSegment(sketch, "E5295", {"start": v(-19.63, -56.9) * mm, "end": v(-19.61, -56.81) * mm});
            skLineSegment(sketch, "E5296", {"start": v(-19.61, -56.81) * mm, "end": v(-19.6, -56.73) * mm});
            skLineSegment(sketch, "E5297", {"start": v(-19.6, -56.73) * mm, "end": v(-19.59, -56.65) * mm});
            skLineSegment(sketch, "E5298", {"start": v(-19.59, -56.65) * mm, "end": v(-19.58, -56.57) * mm});
            skLineSegment(sketch, "E5299", {"start": v(-19.58, -56.57) * mm, "end": v(-19.57, -56.5) * mm});
            skLineSegment(sketch, "E5300", {"start": v(-19.57, -56.5) * mm, "end": v(-19.56, -56.42) * mm});
            skLineSegment(sketch, "E5301", {"start": v(-19.56, -56.42) * mm, "end": v(-19.55, -56.34) * mm});
            skLineSegment(sketch, "E5302", {"start": v(-19.55, -56.34) * mm, "end": v(-19.54, -56.27) * mm});
            skLineSegment(sketch, "E5303", {"start": v(-19.54, -56.27) * mm, "end": v(-19.53, -56.2) * mm});
            skLineSegment(sketch, "E5304", {"start": v(-19.53, -56.2) * mm, "end": v(-19.52, -56.12) * mm});
            skLineSegment(sketch, "E5305", {"start": v(-19.52, -56.12) * mm, "end": v(-19.5, -56.05) * mm});
            skLineSegment(sketch, "E5306", {"start": v(-19.5, -56.05) * mm, "end": v(-19.5, -55.98) * mm});
            skLineSegment(sketch, "E5307", {"start": v(-19.5, -55.98) * mm, "end": v(-19.5, -55.91) * mm});
            skLineSegment(sketch, "E5308", {"start": v(-19.5, -55.91) * mm, "end": v(-19.49, -55.85) * mm});
            skLineSegment(sketch, "E5309", {"start": v(-19.49, -55.85) * mm, "end": v(-19.48, -55.78) * mm});
            skLineSegment(sketch, "E5310", {"start": v(-19.48, -55.78) * mm, "end": v(-19.48, -55.71) * mm});
            skLineSegment(sketch, "E5311", {"start": v(-19.48, -55.71) * mm, "end": v(-19.47, -55.65) * mm});
            skLineSegment(sketch, "E5312", {"start": v(-19.47, -55.65) * mm, "end": v(-19.47, -55.59) * mm});
            skLineSegment(sketch, "E5313", {"start": v(-19.47, -55.59) * mm, "end": v(-19.46, -55.53) * mm});
            skLineSegment(sketch, "E5314", {"start": v(-19.46, -55.53) * mm, "end": v(-19.46, -55.47) * mm});
            skLineSegment(sketch, "E5315", {"start": v(-19.46, -55.47) * mm, "end": v(-19.45, -55.4) * mm});
            skLineSegment(sketch, "E5316", {"start": v(-19.45, -55.4) * mm, "end": v(-19.23, -55.35) * mm});
            skLineSegment(sketch, "E5317", {"start": v(-19.23, -55.35) * mm, "end": v(-18.43, -55.2) * mm});
            skLineSegment(sketch, "E5318", {"start": v(-18.43, -55.2) * mm, "end": v(-18.2, -55.16) * mm});
            skLineSegment(sketch, "E5319", {"start": v(-18.2, -55.16) * mm, "end": v(-18.18, -55.22) * mm});
            skLineSegment(sketch, "E5320", {"start": v(-18.18, -55.22) * mm, "end": v(-18.15, -55.27) * mm});
            skLineSegment(sketch, "E5321", {"start": v(-18.15, -55.27) * mm, "end": v(-18.12, -55.33) * mm});
            skLineSegment(sketch, "E5322", {"start": v(-18.12, -55.33) * mm, "end": v(-18.1, -55.38) * mm});
            skLineSegment(sketch, "E5323", {"start": v(-18.1, -55.38) * mm, "end": v(-18.07, -55.44) * mm});
            skLineSegment(sketch, "E5324", {"start": v(-18.07, -55.44) * mm, "end": v(-18.04, -55.5) * mm});
            skLineSegment(sketch, "E5325", {"start": v(-18.04, -55.5) * mm, "end": v(-18, -55.56) * mm});
            skLineSegment(sketch, "E5326", {"start": v(-18, -55.56) * mm, "end": v(-17.97, -55.62) * mm});
            skLineSegment(sketch, "E5327", {"start": v(-17.97, -55.62) * mm, "end": v(-17.94, -55.68) * mm});
            skLineSegment(sketch, "E5328", {"start": v(-17.94, -55.68) * mm, "end": v(-17.9, -55.74) * mm});
            skLineSegment(sketch, "E5329", {"start": v(-17.9, -55.74) * mm, "end": v(-17.88, -55.8) * mm});
            skLineSegment(sketch, "E5330", {"start": v(-17.88, -55.8) * mm, "end": v(-17.84, -55.87) * mm});
            skLineSegment(sketch, "E5331", {"start": v(-17.84, -55.87) * mm, "end": v(-17.8, -55.93) * mm});
            skLineSegment(sketch, "E5332", {"start": v(-17.8, -55.93) * mm, "end": v(-17.77, -56) * mm});
            skLineSegment(sketch, "E5333", {"start": v(-17.77, -56) * mm, "end": v(-17.73, -56.06) * mm});
            skLineSegment(sketch, "E5334", {"start": v(-17.73, -56.06) * mm, "end": v(-17.7, -56.13) * mm});
            skLineSegment(sketch, "E5335", {"start": v(-17.7, -56.13) * mm, "end": v(-17.65, -56.2) * mm});
            skLineSegment(sketch, "E5336", {"start": v(-17.65, -56.2) * mm, "end": v(-17.61, -56.27) * mm});
            skLineSegment(sketch, "E5337", {"start": v(-17.61, -56.27) * mm, "end": v(-17.57, -56.34) * mm});
            skLineSegment(sketch, "E5338", {"start": v(-17.57, -56.34) * mm, "end": v(-17.53, -56.4) * mm});
            skLineSegment(sketch, "E5339", {"start": v(-17.53, -56.4) * mm, "end": v(-17.48, -56.48) * mm});
            skLineSegment(sketch, "E5340", {"start": v(-17.48, -56.48) * mm, "end": v(-17.44, -56.55) * mm});
            skLineSegment(sketch, "E5341", {"start": v(-17.44, -56.55) * mm, "end": v(-17.4, -56.63) * mm});
            skLineSegment(sketch, "E5342", {"start": v(-17.4, -56.63) * mm, "end": v(-17.35, -56.7) * mm});
            skLineSegment(sketch, "E5343", {"start": v(-17.35, -56.7) * mm, "end": v(-17.3, -56.77) * mm});
            skLineSegment(sketch, "E5344", {"start": v(-17.3, -56.77) * mm, "end": v(-17.25, -56.85) * mm});
            skLineSegment(sketch, "E5345", {"start": v(-17.25, -56.85) * mm, "end": v(-17.2, -56.93) * mm});
            skLineSegment(sketch, "E5346", {"start": v(-17.2, -56.93) * mm, "end": v(-17.15, -57) * mm});
            skLineSegment(sketch, "E5347", {"start": v(-17.15, -57) * mm, "end": v(-17.1, -57.08) * mm});
            skLineSegment(sketch, "E5348", {"start": v(-17.1, -57.08) * mm, "end": v(-17.05, -57.16) * mm});
            skLineSegment(sketch, "E5349", {"start": v(-17.05, -57.16) * mm, "end": v(-17, -57.24) * mm});
            skLineSegment(sketch, "E5350", {"start": v(-17, -57.24) * mm, "end": v(-16.94, -57.32) * mm});
            skLineSegment(sketch, "E5351", {"start": v(-16.94, -57.32) * mm, "end": v(-16.88, -57.4) * mm});
            skLineSegment(sketch, "E5352", {"start": v(-16.88, -57.4) * mm, "end": v(-16.83, -57.48) * mm});
            skLineSegment(sketch, "E5353", {"start": v(-16.83, -57.48) * mm, "end": v(-16.77, -57.56) * mm});
            skLineSegment(sketch, "E5354", {"start": v(-16.77, -57.56) * mm, "end": v(-16.7, -57.64) * mm});
            skLineSegment(sketch, "E5355", {"start": v(-16.7, -57.64) * mm, "end": v(-16.65, -57.73) * mm});
            skLineSegment(sketch, "E5356", {"start": v(-16.65, -57.73) * mm, "end": v(-16.59, -57.81) * mm});
            skLineSegment(sketch, "E5357", {"start": v(-16.59, -57.81) * mm, "end": v(-16.53, -57.9) * mm});
            skLineSegment(sketch, "E5358", {"start": v(-16.53, -57.9) * mm, "end": v(-16.46, -57.98) * mm});
            skLineSegment(sketch, "E5359", {"start": v(-16.46, -57.98) * mm, "end": v(-16.41, -58) * mm});
            skLineSegment(sketch, "E5360", {"start": v(-16.41, -58) * mm, "end": v(-15.4, -57.75) * mm});
            skLineSegment(sketch, "E5361", {"start": v(-15.4, -57.75) * mm, "end": v(-15.37, -57.72) * mm});
            skLineSegment(sketch, "E5362", {"start": v(-15.37, -57.72) * mm, "end": v(-15.35, -57.61) * mm});
            skLineSegment(sketch, "E5363", {"start": v(-15.35, -57.61) * mm, "end": v(-15.33, -57.5) * mm});
            skLineSegment(sketch, "E5364", {"start": v(-15.33, -57.5) * mm, "end": v(-15.31, -57.4) * mm});
            skLineSegment(sketch, "E5365", {"start": v(-15.31, -57.4) * mm, "end": v(-15.3, -57.3) * mm});
            skLineSegment(sketch, "E5366", {"start": v(-15.3, -57.3) * mm, "end": v(-15.28, -57.2) * mm});
            skLineSegment(sketch, "E5367", {"start": v(-15.28, -57.2) * mm, "end": v(-15.27, -57.1) * mm});
            skLineSegment(sketch, "E5368", {"start": v(-15.27, -57.1) * mm, "end": v(-15.26, -57) * mm});
            skLineSegment(sketch, "E5369", {"start": v(-15.26, -57) * mm, "end": v(-15.24, -56.9) * mm});
            skLineSegment(sketch, "E5370", {"start": v(-15.24, -56.9) * mm, "end": v(-15.23, -56.81) * mm});
            skLineSegment(sketch, "E5371", {"start": v(-15.23, -56.81) * mm, "end": v(-15.22, -56.72) * mm});
            skLineSegment(sketch, "E5372", {"start": v(-15.22, -56.72) * mm, "end": v(-15.2, -56.62) * mm});
            skLineSegment(sketch, "E5373", {"start": v(-15.2, -56.62) * mm, "end": v(-15.2, -56.53) * mm});
            skLineSegment(sketch, "E5374", {"start": v(-15.2, -56.53) * mm, "end": v(-15.19, -56.44) * mm});
            skLineSegment(sketch, "E5375", {"start": v(-15.19, -56.44) * mm, "end": v(-15.18, -56.35) * mm});
            skLineSegment(sketch, "E5376", {"start": v(-15.18, -56.35) * mm, "end": v(-15.17, -56.26) * mm});
            skLineSegment(sketch, "E5377", {"start": v(-15.17, -56.26) * mm, "end": v(-15.16, -56.17) * mm});
            skLineSegment(sketch, "E5378", {"start": v(-15.16, -56.17) * mm, "end": v(-15.15, -56.09) * mm});
            skLineSegment(sketch, "E5379", {"start": v(-15.15, -56.09) * mm, "end": v(-15.15, -56) * mm});
            skLineSegment(sketch, "E5380", {"start": v(-15.15, -56) * mm, "end": v(-15.14, -55.92) * mm});
            skLineSegment(sketch, "E5381", {"start": v(-15.14, -55.92) * mm, "end": v(-15.13, -55.83) * mm});
            skLineSegment(sketch, "E5382", {"start": v(-15.13, -55.83) * mm, "end": v(-15.13, -55.75) * mm});
            skLineSegment(sketch, "E5383", {"start": v(-15.13, -55.75) * mm, "end": v(-15.12, -55.67) * mm});
            skLineSegment(sketch, "E5384", {"start": v(-15.12, -55.67) * mm, "end": v(-15.12, -55.59) * mm});
            skLineSegment(sketch, "E5385", {"start": v(-15.12, -55.59) * mm, "end": v(-15.11, -55.51) * mm});
            skLineSegment(sketch, "E5386", {"start": v(-15.11, -55.51) * mm, "end": v(-15.1, -55.43) * mm});
            skLineSegment(sketch, "E5387", {"start": v(-15.1, -55.43) * mm, "end": v(-15.1, -55.36) * mm});
            skLineSegment(sketch, "E5388", {"start": v(-15.1, -55.36) * mm, "end": v(-15.1, -55.28) * mm});
            skLineSegment(sketch, "E5389", {"start": v(-15.1, -55.28) * mm, "end": v(-15.1, -55.2) * mm});
            skLineSegment(sketch, "E5390", {"start": v(-15.1, -55.2) * mm, "end": v(-15.1, -55.14) * mm});
            skLineSegment(sketch, "E5391", {"start": v(-15.1, -55.14) * mm, "end": v(-15.1, -55.06) * mm});
            skLineSegment(sketch, "E5392", {"start": v(-15.1, -55.06) * mm, "end": v(-15.1, -55) * mm});
            skLineSegment(sketch, "E5393", {"start": v(-15.1, -55) * mm, "end": v(-15.1, -54.92) * mm});
            skLineSegment(sketch, "E5394", {"start": v(-15.1, -54.92) * mm, "end": v(-15.1, -54.86) * mm});
            skLineSegment(sketch, "E5395", {"start": v(-15.1, -54.86) * mm, "end": v(-15.1, -54.79) * mm});
            skLineSegment(sketch, "E5396", {"start": v(-15.1, -54.79) * mm, "end": v(-15.1, -54.72) * mm});
            skLineSegment(sketch, "E5397", {"start": v(-15.1, -54.72) * mm, "end": v(-15.1, -54.66) * mm});
            skLineSegment(sketch, "E5398", {"start": v(-15.1, -54.66) * mm, "end": v(-15.1, -54.6) * mm});
            skLineSegment(sketch, "E5399", {"start": v(-15.1, -54.6) * mm, "end": v(-15.1, -54.53) * mm});
            skLineSegment(sketch, "E5400", {"start": v(-15.1, -54.53) * mm, "end": v(-15.1, -54.47) * mm});
            skLineSegment(sketch, "E5401", {"start": v(-15.1, -54.47) * mm, "end": v(-15.1, -54.41) * mm});
            skLineSegment(sketch, "E5402", {"start": v(-15.1, -54.41) * mm, "end": v(-14.88, -54.34) * mm});
            skLineSegment(sketch, "E5403", {"start": v(-14.88, -54.34) * mm, "end": v(-14.1, -54.12) * mm});
            skLineSegment(sketch, "E5404", {"start": v(-14.1, -54.12) * mm, "end": v(-13.88, -54.06) * mm});
            skLineSegment(sketch, "E5405", {"start": v(-13.88, -54.06) * mm, "end": v(-13.85, -54.11) * mm});
            skLineSegment(sketch, "E5406", {"start": v(-13.85, -54.11) * mm, "end": v(-13.81, -54.16) * mm});
            skLineSegment(sketch, "E5407", {"start": v(-13.81, -54.16) * mm, "end": v(-13.78, -54.22) * mm});
            skLineSegment(sketch, "E5408", {"start": v(-13.78, -54.22) * mm, "end": v(-13.75, -54.27) * mm});
            skLineSegment(sketch, "E5409", {"start": v(-13.75, -54.27) * mm, "end": v(-13.71, -54.32) * mm});
            skLineSegment(sketch, "E5410", {"start": v(-13.71, -54.32) * mm, "end": v(-13.68, -54.38) * mm});
            skLineSegment(sketch, "E5411", {"start": v(-13.68, -54.38) * mm, "end": v(-13.64, -54.44) * mm});
            skLineSegment(sketch, "E5412", {"start": v(-13.64, -54.44) * mm, "end": v(-13.6, -54.5) * mm});
            skLineSegment(sketch, "E5413", {"start": v(-13.6, -54.5) * mm, "end": v(-13.57, -54.55) * mm});
            skLineSegment(sketch, "E5414", {"start": v(-13.57, -54.55) * mm, "end": v(-13.53, -54.61) * mm});
            skLineSegment(sketch, "E5415", {"start": v(-13.53, -54.61) * mm, "end": v(-13.5, -54.67) * mm});
            skLineSegment(sketch, "E5416", {"start": v(-13.5, -54.67) * mm, "end": v(-13.45, -54.73) * mm});
            skLineSegment(sketch, "E5417", {"start": v(-13.45, -54.73) * mm, "end": v(-13.4, -54.8) * mm});
            skLineSegment(sketch, "E5418", {"start": v(-13.4, -54.8) * mm, "end": v(-13.37, -54.85) * mm});
            skLineSegment(sketch, "E5419", {"start": v(-13.37, -54.85) * mm, "end": v(-13.32, -54.92) * mm});
            skLineSegment(sketch, "E5420", {"start": v(-13.32, -54.92) * mm, "end": v(-13.28, -54.98) * mm});
            skLineSegment(sketch, "E5421", {"start": v(-13.28, -54.98) * mm, "end": v(-13.23, -55.04) * mm});
            skLineSegment(sketch, "E5422", {"start": v(-13.23, -55.04) * mm, "end": v(-13.19, -55.1) * mm});
            skLineSegment(sketch, "E5423", {"start": v(-13.19, -55.1) * mm, "end": v(-13.14, -55.18) * mm});
            skLineSegment(sketch, "E5424", {"start": v(-13.14, -55.18) * mm, "end": v(-13.1, -55.24) * mm});
            skLineSegment(sketch, "E5425", {"start": v(-13.1, -55.24) * mm, "end": v(-13.04, -55.3) * mm});
            skLineSegment(sketch, "E5426", {"start": v(-13.04, -55.3) * mm, "end": v(-13, -55.38) * mm});
            skLineSegment(sketch, "E5427", {"start": v(-13, -55.38) * mm, "end": v(-12.94, -55.45) * mm});
            skLineSegment(sketch, "E5428", {"start": v(-12.94, -55.45) * mm, "end": v(-12.89, -55.51) * mm});
            skLineSegment(sketch, "E5429", {"start": v(-12.89, -55.51) * mm, "end": v(-12.83, -55.58) * mm});
            skLineSegment(sketch, "E5430", {"start": v(-12.83, -55.58) * mm, "end": v(-12.78, -55.66) * mm});
            skLineSegment(sketch, "E5431", {"start": v(-12.78, -55.66) * mm, "end": v(-12.72, -55.73) * mm});
            skLineSegment(sketch, "E5432", {"start": v(-12.72, -55.73) * mm, "end": v(-12.66, -55.8) * mm});
            skLineSegment(sketch, "E5433", {"start": v(-12.66, -55.8) * mm, "end": v(-12.6, -55.87) * mm});
            skLineSegment(sketch, "E5434", {"start": v(-12.6, -55.87) * mm, "end": v(-12.55, -55.94) * mm});
            skLineSegment(sketch, "E5435", {"start": v(-12.55, -55.94) * mm, "end": v(-12.49, -56.02) * mm});
            skLineSegment(sketch, "E5436", {"start": v(-12.49, -56.02) * mm, "end": v(-12.42, -56.1) * mm});
            skLineSegment(sketch, "E5437", {"start": v(-12.42, -56.1) * mm, "end": v(-12.36, -56.17) * mm});
            skLineSegment(sketch, "E5438", {"start": v(-12.36, -56.17) * mm, "end": v(-12.3, -56.24) * mm});
            skLineSegment(sketch, "E5439", {"start": v(-12.3, -56.24) * mm, "end": v(-12.23, -56.32) * mm});
            skLineSegment(sketch, "E5440", {"start": v(-12.23, -56.32) * mm, "end": v(-12.17, -56.4) * mm});
            skLineSegment(sketch, "E5441", {"start": v(-12.17, -56.4) * mm, "end": v(-12.1, -56.47) * mm});
            skLineSegment(sketch, "E5442", {"start": v(-12.1, -56.47) * mm, "end": v(-12.03, -56.55) * mm});
            skLineSegment(sketch, "E5443", {"start": v(-12.03, -56.55) * mm, "end": v(-11.96, -56.63) * mm});
            skLineSegment(sketch, "E5444", {"start": v(-11.96, -56.63) * mm, "end": v(-11.89, -56.71) * mm});
            skLineSegment(sketch, "E5445", {"start": v(-11.89, -56.71) * mm, "end": v(-11.84, -56.72) * mm});
            skLineSegment(sketch, "E5446", {"start": v(-11.84, -56.72) * mm, "end": v(-10.85, -56.39) * mm});
            skLineSegment(sketch, "E5447", {"start": v(-10.85, -56.39) * mm, "end": v(-10.82, -56.35) * mm});
            skLineSegment(sketch, "E5448", {"start": v(-10.82, -56.35) * mm, "end": v(-10.81, -56.24) * mm});
            skLineSegment(sketch, "E5449", {"start": v(-10.81, -56.24) * mm, "end": v(-10.8, -56.14) * mm});
            skLineSegment(sketch, "E5450", {"start": v(-10.8, -56.14) * mm, "end": v(-10.8, -56.03) * mm});
            skLineSegment(sketch, "E5451", {"start": v(-10.8, -56.03) * mm, "end": v(-10.8, -55.93) * mm});
            skLineSegment(sketch, "E5452", {"start": v(-10.8, -55.93) * mm, "end": v(-10.79, -55.83) * mm});
            skLineSegment(sketch, "E5453", {"start": v(-10.79, -55.83) * mm, "end": v(-10.78, -55.73) * mm});
            skLineSegment(sketch, "E5454", {"start": v(-10.78, -55.73) * mm, "end": v(-10.78, -55.63) * mm});
            skLineSegment(sketch, "E5455", {"start": v(-10.78, -55.63) * mm, "end": v(-10.77, -55.53) * mm});
            skLineSegment(sketch, "E5456", {"start": v(-10.77, -55.53) * mm, "end": v(-10.77, -55.44) * mm});
            skLineSegment(sketch, "E5457", {"start": v(-10.77, -55.44) * mm, "end": v(-10.76, -55.34) * mm});
            skLineSegment(sketch, "E5458", {"start": v(-10.76, -55.34) * mm, "end": v(-10.76, -55.25) * mm});
            skLineSegment(sketch, "E5459", {"start": v(-10.76, -55.25) * mm, "end": v(-10.76, -55.15) * mm});
            skLineSegment(sketch, "E5460", {"start": v(-10.76, -55.15) * mm, "end": v(-10.76, -55.06) * mm});
            skLineSegment(sketch, "E5461", {"start": v(-10.76, -55.06) * mm, "end": v(-10.76, -54.97) * mm});
            skLineSegment(sketch, "E5462", {"start": v(-10.76, -54.97) * mm, "end": v(-10.76, -54.88) * mm});
            skLineSegment(sketch, "E5463", {"start": v(-10.76, -54.88) * mm, "end": v(-10.76, -54.8) * mm});
            skLineSegment(sketch, "E5464", {"start": v(-10.76, -54.8) * mm, "end": v(-10.76, -54.7) * mm});
            skLineSegment(sketch, "E5465", {"start": v(-10.76, -54.7) * mm, "end": v(-10.76, -54.62) * mm});
            skLineSegment(sketch, "E5466", {"start": v(-10.76, -54.62) * mm, "end": v(-10.76, -54.54) * mm});
            skLineSegment(sketch, "E5467", {"start": v(-10.76, -54.54) * mm, "end": v(-10.76, -54.45) * mm});
            skLineSegment(sketch, "E5468", {"start": v(-10.76, -54.45) * mm, "end": v(-10.76, -54.37) * mm});
            skLineSegment(sketch, "E5469", {"start": v(-10.76, -54.37) * mm, "end": v(-10.76, -54.29) * mm});
            skLineSegment(sketch, "E5470", {"start": v(-10.76, -54.29) * mm, "end": v(-10.76, -54.2) * mm});
            skLineSegment(sketch, "E5471", {"start": v(-10.76, -54.2) * mm, "end": v(-10.77, -54.13) * mm});
            skLineSegment(sketch, "E5472", {"start": v(-10.77, -54.13) * mm, "end": v(-10.77, -54.05) * mm});
            skLineSegment(sketch, "E5473", {"start": v(-10.77, -54.05) * mm, "end": v(-10.77, -53.98) * mm});
            skLineSegment(sketch, "E5474", {"start": v(-10.77, -53.98) * mm, "end": v(-10.78, -53.9) * mm});
            skLineSegment(sketch, "E5475", {"start": v(-10.78, -53.9) * mm, "end": v(-10.78, -53.83) * mm});
            skLineSegment(sketch, "E5476", {"start": v(-10.78, -53.83) * mm, "end": v(-10.79, -53.75) * mm});
            skLineSegment(sketch, "E5477", {"start": v(-10.79, -53.75) * mm, "end": v(-10.8, -53.68) * mm});
            skLineSegment(sketch, "E5478", {"start": v(-10.8, -53.68) * mm, "end": v(-10.8, -53.61) * mm});
            skLineSegment(sketch, "E5479", {"start": v(-10.8, -53.61) * mm, "end": v(-10.8, -53.54) * mm});
            skLineSegment(sketch, "E5480", {"start": v(-10.8, -53.54) * mm, "end": v(-10.8, -53.48) * mm});
            skLineSegment(sketch, "E5481", {"start": v(-10.8, -53.48) * mm, "end": v(-10.81, -53.4) * mm});
            skLineSegment(sketch, "E5482", {"start": v(-10.81, -53.4) * mm, "end": v(-10.82, -53.34) * mm});
            skLineSegment(sketch, "E5483", {"start": v(-10.82, -53.34) * mm, "end": v(-10.83, -53.28) * mm});
            skLineSegment(sketch, "E5484", {"start": v(-10.83, -53.28) * mm, "end": v(-10.83, -53.22) * mm});
            skLineSegment(sketch, "E5485", {"start": v(-10.83, -53.22) * mm, "end": v(-10.84, -53.16) * mm});
            skLineSegment(sketch, "E5486", {"start": v(-10.84, -53.16) * mm, "end": v(-10.85, -53.1) * mm});
            skLineSegment(sketch, "E5487", {"start": v(-10.85, -53.1) * mm, "end": v(-10.85, -53.04) * mm});
            skLineSegment(sketch, "E5488", {"start": v(-10.85, -53.04) * mm, "end": v(-10.64, -52.94) * mm});
            skLineSegment(sketch, "E5489", {"start": v(-10.64, -52.94) * mm, "end": v(-9.89, -52.65) * mm});
            skLineSegment(sketch, "E5490", {"start": v(-9.89, -52.65) * mm, "end": v(-9.66, -52.57) * mm});
            skLineSegment(sketch, "E5491", {"start": v(-9.66, -52.57) * mm, "end": v(-9.63, -52.62) * mm});
            skLineSegment(sketch, "E5492", {"start": v(-9.63, -52.62) * mm, "end": v(-9.6, -52.67) * mm});
            skLineSegment(sketch, "E5493", {"start": v(-9.6, -52.67) * mm, "end": v(-9.56, -52.72) * mm});
            skLineSegment(sketch, "E5494", {"start": v(-9.56, -52.72) * mm, "end": v(-9.52, -52.77) * mm});
            skLineSegment(sketch, "E5495", {"start": v(-9.52, -52.77) * mm, "end": v(-9.48, -52.82) * mm});
            skLineSegment(sketch, "E5496", {"start": v(-9.48, -52.82) * mm, "end": v(-9.44, -52.88) * mm});
            skLineSegment(sketch, "E5497", {"start": v(-9.44, -52.88) * mm, "end": v(-9.4, -52.93) * mm});
            skLineSegment(sketch, "E5498", {"start": v(-9.4, -52.93) * mm, "end": v(-9.36, -52.98) * mm});
            skLineSegment(sketch, "E5499", {"start": v(-9.36, -52.98) * mm, "end": v(-9.32, -53.04) * mm});
            skLineSegment(sketch, "E5500", {"start": v(-9.32, -53.04) * mm, "end": v(-9.27, -53.1) * mm});
            skLineSegment(sketch, "E5501", {"start": v(-9.27, -53.1) * mm, "end": v(-9.23, -53.15) * mm});
            skLineSegment(sketch, "E5502", {"start": v(-9.23, -53.15) * mm, "end": v(-9.18, -53.2) * mm});
            skLineSegment(sketch, "E5503", {"start": v(-9.18, -53.2) * mm, "end": v(-9.13, -53.26) * mm});
            skLineSegment(sketch, "E5504", {"start": v(-9.13, -53.26) * mm, "end": v(-9.09, -53.32) * mm});
            skLineSegment(sketch, "E5505", {"start": v(-9.09, -53.32) * mm, "end": v(-9.04, -53.38) * mm});
            skLineSegment(sketch, "E5506", {"start": v(-9.04, -53.38) * mm, "end": v(-8.99, -53.44) * mm});
            skLineSegment(sketch, "E5507", {"start": v(-8.99, -53.44) * mm, "end": v(-8.94, -53.5) * mm});
            skLineSegment(sketch, "E5508", {"start": v(-8.94, -53.5) * mm, "end": v(-8.88, -53.56) * mm});
            skLineSegment(sketch, "E5509", {"start": v(-8.88, -53.56) * mm, "end": v(-8.83, -53.62) * mm});
            skLineSegment(sketch, "E5510", {"start": v(-8.83, -53.62) * mm, "end": v(-8.78, -53.68) * mm});
            skLineSegment(sketch, "E5511", {"start": v(-8.78, -53.68) * mm, "end": v(-8.72, -53.74) * mm});
            skLineSegment(sketch, "E5512", {"start": v(-8.72, -53.74) * mm, "end": v(-8.67, -53.8) * mm});
            skLineSegment(sketch, "E5513", {"start": v(-8.67, -53.8) * mm, "end": v(-8.6, -53.87) * mm});
            skLineSegment(sketch, "E5514", {"start": v(-8.6, -53.87) * mm, "end": v(-8.55, -53.93) * mm});
            skLineSegment(sketch, "E5515", {"start": v(-8.55, -53.93) * mm, "end": v(-8.49, -54) * mm});
            skLineSegment(sketch, "E5516", {"start": v(-8.49, -54) * mm, "end": v(-8.43, -54.06) * mm});
            skLineSegment(sketch, "E5517", {"start": v(-8.43, -54.06) * mm, "end": v(-8.37, -54.13) * mm});
            skLineSegment(sketch, "E5518", {"start": v(-8.37, -54.13) * mm, "end": v(-8.3, -54.2) * mm});
            skLineSegment(sketch, "E5519", {"start": v(-8.3, -54.2) * mm, "end": v(-8.24, -54.26) * mm});
            skLineSegment(sketch, "E5520", {"start": v(-8.24, -54.26) * mm, "end": v(-8.17, -54.33) * mm});
            skLineSegment(sketch, "E5521", {"start": v(-8.17, -54.33) * mm, "end": v(-8.1, -54.4) * mm});
            skLineSegment(sketch, "E5522", {"start": v(-8.1, -54.4) * mm, "end": v(-8.04, -54.47) * mm});
            skLineSegment(sketch, "E5523", {"start": v(-8.04, -54.47) * mm, "end": v(-7.97, -54.54) * mm});
            skLineSegment(sketch, "E5524", {"start": v(-7.97, -54.54) * mm, "end": v(-7.9, -54.6) * mm});
            skLineSegment(sketch, "E5525", {"start": v(-7.9, -54.6) * mm, "end": v(-7.82, -54.68) * mm});
            skLineSegment(sketch, "E5526", {"start": v(-7.82, -54.68) * mm, "end": v(-7.75, -54.75) * mm});
            skLineSegment(sketch, "E5527", {"start": v(-7.75, -54.75) * mm, "end": v(-7.68, -54.82) * mm});
            skLineSegment(sketch, "E5528", {"start": v(-7.68, -54.82) * mm, "end": v(-7.6, -54.9) * mm});
            skLineSegment(sketch, "E5529", {"start": v(-7.6, -54.9) * mm, "end": v(-7.53, -54.96) * mm});
            skLineSegment(sketch, "E5530", {"start": v(-7.53, -54.96) * mm, "end": v(-7.45, -55.04) * mm});
            skLineSegment(sketch, "E5531", {"start": v(-7.45, -55.04) * mm, "end": v(-7.4, -55.04) * mm});
            skLineSegment(sketch, "E5532", {"start": v(-7.4, -55.04) * mm, "end": v(-6.45, -54.62) * mm});
            skLineSegment(sketch, "E5533", {"start": v(-6.45, -54.62) * mm, "end": v(-6.42, -54.58) * mm});
            skLineSegment(sketch, "E5534", {"start": v(-6.42, -54.58) * mm, "end": v(-6.42, -54.47) * mm});
            skLineSegment(sketch, "E5535", {"start": v(-6.42, -54.47) * mm, "end": v(-6.42, -54.37) * mm});
            skLineSegment(sketch, "E5536", {"start": v(-6.42, -54.37) * mm, "end": v(-6.42, -54.26) * mm});
            skLineSegment(sketch, "E5537", {"start": v(-6.42, -54.26) * mm, "end": v(-6.42, -54.16) * mm});
            skLineSegment(sketch, "E5538", {"start": v(-6.42, -54.16) * mm, "end": v(-6.43, -54.06) * mm});
            skLineSegment(sketch, "E5539", {"start": v(-6.43, -54.06) * mm, "end": v(-6.43, -53.96) * mm});
            skLineSegment(sketch, "E5540", {"start": v(-6.43, -53.96) * mm, "end": v(-6.44, -53.86) * mm});
            skLineSegment(sketch, "E5541", {"start": v(-6.44, -53.86) * mm, "end": v(-6.44, -53.76) * mm});
            skLineSegment(sketch, "E5542", {"start": v(-6.44, -53.76) * mm, "end": v(-6.45, -53.67) * mm});
            skLineSegment(sketch, "E5543", {"start": v(-6.45, -53.67) * mm, "end": v(-6.45, -53.57) * mm});
            skLineSegment(sketch, "E5544", {"start": v(-6.45, -53.57) * mm, "end": v(-6.46, -53.48) * mm});
            skLineSegment(sketch, "E5545", {"start": v(-6.46, -53.48) * mm, "end": v(-6.46, -53.38) * mm});
            skLineSegment(sketch, "E5546", {"start": v(-6.46, -53.38) * mm, "end": v(-6.47, -53.3) * mm});
            skLineSegment(sketch, "E5547", {"start": v(-6.47, -53.3) * mm, "end": v(-6.48, -53.2) * mm});
            skLineSegment(sketch, "E5548", {"start": v(-6.48, -53.2) * mm, "end": v(-6.48, -53.11) * mm});
            skLineSegment(sketch, "E5549", {"start": v(-6.48, -53.11) * mm, "end": v(-6.5, -53.02) * mm});
            skLineSegment(sketch, "E5550", {"start": v(-6.5, -53.02) * mm, "end": v(-6.5, -52.94) * mm});
            skLineSegment(sketch, "E5551", {"start": v(-6.5, -52.94) * mm, "end": v(-6.5, -52.85) * mm});
            skLineSegment(sketch, "E5552", {"start": v(-6.5, -52.85) * mm, "end": v(-6.52, -52.77) * mm});
            skLineSegment(sketch, "E5553", {"start": v(-6.52, -52.77) * mm, "end": v(-6.52, -52.69) * mm});
            skLineSegment(sketch, "E5554", {"start": v(-6.52, -52.69) * mm, "end": v(-6.53, -52.6) * mm});
            skLineSegment(sketch, "E5555", {"start": v(-6.53, -52.6) * mm, "end": v(-6.54, -52.52) * mm});
            skLineSegment(sketch, "E5556", {"start": v(-6.54, -52.52) * mm, "end": v(-6.55, -52.44) * mm});
            skLineSegment(sketch, "E5557", {"start": v(-6.55, -52.44) * mm, "end": v(-6.56, -52.37) * mm});
            skLineSegment(sketch, "E5558", {"start": v(-6.56, -52.37) * mm, "end": v(-6.57, -52.29) * mm});
            skLineSegment(sketch, "E5559", {"start": v(-6.57, -52.29) * mm, "end": v(-6.58, -52.21) * mm});
            skLineSegment(sketch, "E5560", {"start": v(-6.58, -52.21) * mm, "end": v(-6.6, -52.14) * mm});
            skLineSegment(sketch, "E5561", {"start": v(-6.6, -52.14) * mm, "end": v(-6.6, -52.06) * mm});
            skLineSegment(sketch, "E5562", {"start": v(-6.6, -52.06) * mm, "end": v(-6.62, -52) * mm});
            skLineSegment(sketch, "E5563", {"start": v(-6.62, -52) * mm, "end": v(-6.63, -51.92) * mm});
            skLineSegment(sketch, "E5564", {"start": v(-6.63, -51.92) * mm, "end": v(-6.64, -51.85) * mm});
            skLineSegment(sketch, "E5565", {"start": v(-6.64, -51.85) * mm, "end": v(-6.65, -51.79) * mm});
            skLineSegment(sketch, "E5566", {"start": v(-6.65, -51.79) * mm, "end": v(-6.66, -51.72) * mm});
            skLineSegment(sketch, "E5567", {"start": v(-6.66, -51.72) * mm, "end": v(-6.67, -51.65) * mm});
            skLineSegment(sketch, "E5568", {"start": v(-6.67, -51.65) * mm, "end": v(-6.68, -51.59) * mm});
            skLineSegment(sketch, "E5569", {"start": v(-6.68, -51.59) * mm, "end": v(-6.7, -51.52) * mm});
            skLineSegment(sketch, "E5570", {"start": v(-6.7, -51.52) * mm, "end": v(-6.7, -51.46) * mm});
            skLineSegment(sketch, "E5571", {"start": v(-6.7, -51.46) * mm, "end": v(-6.72, -51.4) * mm});
            skLineSegment(sketch, "E5572", {"start": v(-6.72, -51.4) * mm, "end": v(-6.73, -51.34) * mm});
            skLineSegment(sketch, "E5573", {"start": v(-6.73, -51.34) * mm, "end": v(-6.74, -51.28) * mm});
            skLineSegment(sketch, "E5574", {"start": v(-6.74, -51.28) * mm, "end": v(-6.54, -51.17) * mm});
            skLineSegment(sketch, "E5575", {"start": v(-6.54, -51.17) * mm, "end": v(-5.82, -50.81) * mm});
            skLineSegment(sketch, "E5576", {"start": v(-5.82, -50.81) * mm, "end": v(-5.6, -50.72) * mm});
            skLineSegment(sketch, "E5577", {"start": v(-5.6, -50.72) * mm, "end": v(-5.56, -50.76) * mm});
            skLineSegment(sketch, "E5578", {"start": v(-5.56, -50.76) * mm, "end": v(-5.52, -50.8) * mm});
            skLineSegment(sketch, "E5579", {"start": v(-5.52, -50.8) * mm, "end": v(-5.48, -50.85) * mm});
            skLineSegment(sketch, "E5580", {"start": v(-5.48, -50.85) * mm, "end": v(-5.44, -50.9) * mm});
            skLineSegment(sketch, "E5581", {"start": v(-5.44, -50.9) * mm, "end": v(-5.4, -50.95) * mm});
            skLineSegment(sketch, "E5582", {"start": v(-5.4, -50.95) * mm, "end": v(-5.35, -51) * mm});
            skLineSegment(sketch, "E5583", {"start": v(-5.35, -51) * mm, "end": v(-5.3, -51.05) * mm});
            skLineSegment(sketch, "E5584", {"start": v(-5.3, -51.05) * mm, "end": v(-5.26, -51.1) * mm});
            skLineSegment(sketch, "E5585", {"start": v(-5.26, -51.1) * mm, "end": v(-5.21, -51.15) * mm});
            skLineSegment(sketch, "E5586", {"start": v(-5.21, -51.15) * mm, "end": v(-5.17, -51.2) * mm});
            skLineSegment(sketch, "E5587", {"start": v(-5.17, -51.2) * mm, "end": v(-5.12, -51.25) * mm});
            skLineSegment(sketch, "E5588", {"start": v(-5.12, -51.25) * mm, "end": v(-5.07, -51.3) * mm});
            skLineSegment(sketch, "E5589", {"start": v(-5.07, -51.3) * mm, "end": v(-5.01, -51.35) * mm});
            skLineSegment(sketch, "E5590", {"start": v(-5.01, -51.35) * mm, "end": v(-4.96, -51.4) * mm});
            skLineSegment(sketch, "E5591", {"start": v(-4.96, -51.4) * mm, "end": v(-4.9, -51.46) * mm});
            skLineSegment(sketch, "E5592", {"start": v(-4.9, -51.46) * mm, "end": v(-4.85, -51.52) * mm});
            skLineSegment(sketch, "E5593", {"start": v(-4.85, -51.52) * mm, "end": v(-4.8, -51.57) * mm});
            skLineSegment(sketch, "E5594", {"start": v(-4.8, -51.57) * mm, "end": v(-4.74, -51.63) * mm});
            skLineSegment(sketch, "E5595", {"start": v(-4.74, -51.63) * mm, "end": v(-4.68, -51.68) * mm});
            skLineSegment(sketch, "E5596", {"start": v(-4.68, -51.68) * mm, "end": v(-4.62, -51.74) * mm});
            skLineSegment(sketch, "E5597", {"start": v(-4.62, -51.74) * mm, "end": v(-4.56, -51.8) * mm});
            skLineSegment(sketch, "E5598", {"start": v(-4.56, -51.8) * mm, "end": v(-4.5, -51.85) * mm});
            skLineSegment(sketch, "E5599", {"start": v(-4.5, -51.85) * mm, "end": v(-4.43, -51.91) * mm});
            skLineSegment(sketch, "E5600", {"start": v(-4.43, -51.91) * mm, "end": v(-4.37, -51.97) * mm});
            skLineSegment(sketch, "E5601", {"start": v(-4.37, -51.97) * mm, "end": v(-4.3, -52.03) * mm});
            skLineSegment(sketch, "E5602", {"start": v(-4.3, -52.03) * mm, "end": v(-4.24, -52.1) * mm});
            skLineSegment(sketch, "E5603", {"start": v(-4.24, -52.1) * mm, "end": v(-4.17, -52.15) * mm});
            skLineSegment(sketch, "E5604", {"start": v(-4.17, -52.15) * mm, "end": v(-4.1, -52.21) * mm});
            skLineSegment(sketch, "E5605", {"start": v(-4.1, -52.21) * mm, "end": v(-4.03, -52.27) * mm});
            skLineSegment(sketch, "E5606", {"start": v(-4.03, -52.27) * mm, "end": v(-3.96, -52.33) * mm});
            skLineSegment(sketch, "E5607", {"start": v(-3.96, -52.33) * mm, "end": v(-3.89, -52.4) * mm});
            skLineSegment(sketch, "E5608", {"start": v(-3.89, -52.4) * mm, "end": v(-3.81, -52.46) * mm});
            skLineSegment(sketch, "E5609", {"start": v(-3.81, -52.46) * mm, "end": v(-3.74, -52.52) * mm});
            skLineSegment(sketch, "E5610", {"start": v(-3.74, -52.52) * mm, "end": v(-3.66, -52.58) * mm});
            skLineSegment(sketch, "E5611", {"start": v(-3.66, -52.58) * mm, "end": v(-3.58, -52.65) * mm});
            skLineSegment(sketch, "E5612", {"start": v(-3.58, -52.65) * mm, "end": v(-3.5, -52.71) * mm});
            skLineSegment(sketch, "E5613", {"start": v(-3.5, -52.71) * mm, "end": v(-3.42, -52.78) * mm});
            skLineSegment(sketch, "E5614", {"start": v(-3.42, -52.78) * mm, "end": v(-3.34, -52.84) * mm});
            skLineSegment(sketch, "E5615", {"start": v(-3.34, -52.84) * mm, "end": v(-3.26, -52.9) * mm});
            skLineSegment(sketch, "E5616", {"start": v(-3.26, -52.9) * mm, "end": v(-3.18, -52.97) * mm});
            skLineSegment(sketch, "E5617", {"start": v(-3.18, -52.97) * mm, "end": v(-3.12, -52.97) * mm});
            skLineSegment(sketch, "E5618", {"start": v(-3.12, -52.97) * mm, "end": v(-2.21, -52.47) * mm});
            skLineSegment(sketch, "E5619", {"start": v(-2.21, -52.47) * mm, "end": v(-2.19, -52.42) * mm});
            skLineSegment(sketch, "E5620", {"start": v(-2.19, -52.42) * mm, "end": v(-2.2, -52.32) * mm});
            skLineSegment(sketch, "E5621", {"start": v(-2.2, -52.32) * mm, "end": v(-2.21, -52.21) * mm});
            skLineSegment(sketch, "E5622", {"start": v(-2.21, -52.21) * mm, "end": v(-2.22, -52.11) * mm});
            skLineSegment(sketch, "E5623", {"start": v(-2.22, -52.11) * mm, "end": v(-2.23, -52) * mm});
            skLineSegment(sketch, "E5624", {"start": v(-2.23, -52) * mm, "end": v(-2.25, -51.9) * mm});
            skLineSegment(sketch, "E5625", {"start": v(-2.25, -51.9) * mm, "end": v(-2.26, -51.8) * mm});
            skLineSegment(sketch, "E5626", {"start": v(-2.26, -51.8) * mm, "end": v(-2.27, -51.7) * mm});
            skLineSegment(sketch, "E5627", {"start": v(-2.27, -51.7) * mm, "end": v(-2.29, -51.61) * mm});
            skLineSegment(sketch, "E5628", {"start": v(-2.29, -51.61) * mm, "end": v(-2.3, -51.52) * mm});
            skLineSegment(sketch, "E5629", {"start": v(-2.3, -51.52) * mm, "end": v(-2.31, -51.42) * mm});
            skLineSegment(sketch, "E5630", {"start": v(-2.31, -51.42) * mm, "end": v(-2.33, -51.33) * mm});
            skLineSegment(sketch, "E5631", {"start": v(-2.33, -51.33) * mm, "end": v(-2.34, -51.24) * mm});
            skLineSegment(sketch, "E5632", {"start": v(-2.34, -51.24) * mm, "end": v(-2.36, -51.15) * mm});
            skLineSegment(sketch, "E5633", {"start": v(-2.36, -51.15) * mm, "end": v(-2.37, -51.06) * mm});
            skLineSegment(sketch, "E5634", {"start": v(-2.37, -51.06) * mm, "end": v(-2.39, -50.97) * mm});
            skLineSegment(sketch, "E5635", {"start": v(-2.39, -50.97) * mm, "end": v(-2.4, -50.88) * mm});
            skLineSegment(sketch, "E5636", {"start": v(-2.4, -50.88) * mm, "end": v(-2.42, -50.8) * mm});
            skLineSegment(sketch, "E5637", {"start": v(-2.42, -50.8) * mm, "end": v(-2.43, -50.71) * mm});
            skLineSegment(sketch, "E5638", {"start": v(-2.43, -50.71) * mm, "end": v(-2.45, -50.63) * mm});
            skLineSegment(sketch, "E5639", {"start": v(-2.45, -50.63) * mm, "end": v(-2.47, -50.55) * mm});
            skLineSegment(sketch, "E5640", {"start": v(-2.47, -50.55) * mm, "end": v(-2.48, -50.47) * mm});
            skLineSegment(sketch, "E5641", {"start": v(-2.48, -50.47) * mm, "end": v(-2.5, -50.39) * mm});
            skLineSegment(sketch, "E5642", {"start": v(-2.5, -50.39) * mm, "end": v(-2.52, -50.3) * mm});
            skLineSegment(sketch, "E5643", {"start": v(-2.52, -50.3) * mm, "end": v(-2.53, -50.23) * mm});
            skLineSegment(sketch, "E5644", {"start": v(-2.53, -50.23) * mm, "end": v(-2.55, -50.15) * mm});
            skLineSegment(sketch, "E5645", {"start": v(-2.55, -50.15) * mm, "end": v(-2.57, -50.08) * mm});
            skLineSegment(sketch, "E5646", {"start": v(-2.57, -50.08) * mm, "end": v(-2.58, -50) * mm});
            skLineSegment(sketch, "E5647", {"start": v(-2.58, -50) * mm, "end": v(-2.6, -49.94) * mm});
            skLineSegment(sketch, "E5648", {"start": v(-2.6, -49.94) * mm, "end": v(-2.62, -49.86) * mm});
            skLineSegment(sketch, "E5649", {"start": v(-2.62, -49.86) * mm, "end": v(-2.64, -49.8) * mm});
            skLineSegment(sketch, "E5650", {"start": v(-2.64, -49.8) * mm, "end": v(-2.65, -49.73) * mm});
            skLineSegment(sketch, "E5651", {"start": v(-2.65, -49.73) * mm, "end": v(-2.67, -49.66) * mm});
            skLineSegment(sketch, "E5652", {"start": v(-2.67, -49.66) * mm, "end": v(-2.69, -49.6) * mm});
            skLineSegment(sketch, "E5653", {"start": v(-2.69, -49.6) * mm, "end": v(-2.7, -49.53) * mm});
            skLineSegment(sketch, "E5654", {"start": v(-2.7, -49.53) * mm, "end": v(-2.72, -49.47) * mm});
            skLineSegment(sketch, "E5655", {"start": v(-2.72, -49.47) * mm, "end": v(-2.74, -49.4) * mm});
            skLineSegment(sketch, "E5656", {"start": v(-2.74, -49.4) * mm, "end": v(-2.76, -49.34) * mm});
            skLineSegment(sketch, "E5657", {"start": v(-2.76, -49.34) * mm, "end": v(-2.78, -49.29) * mm});
            skLineSegment(sketch, "E5658", {"start": v(-2.78, -49.29) * mm, "end": v(-2.8, -49.23) * mm});
            skLineSegment(sketch, "E5659", {"start": v(-2.8, -49.23) * mm, "end": v(-2.81, -49.17) * mm});
            skLineSegment(sketch, "E5660", {"start": v(-2.81, -49.17) * mm, "end": v(-2.62, -49.04) * mm});
            skLineSegment(sketch, "E5661", {"start": v(-2.62, -49.04) * mm, "end": v(-1.93, -48.62) * mm});
            skLineSegment(sketch, "E5662", {"start": v(-1.93, -48.62) * mm, "end": v(-1.73, -48.5) * mm});
            skLineSegment(sketch, "E5663", {"start": v(-1.73, -48.5) * mm, "end": v(-1.68, -48.54) * mm});
            skLineSegment(sketch, "E5664", {"start": v(-1.68, -48.54) * mm, "end": v(-1.64, -48.59) * mm});
            skLineSegment(sketch, "E5665", {"start": v(-1.64, -48.59) * mm, "end": v(-1.6, -48.63) * mm});
            skLineSegment(sketch, "E5666", {"start": v(-1.6, -48.63) * mm, "end": v(-1.55, -48.67) * mm});
            skLineSegment(sketch, "E5667", {"start": v(-1.55, -48.67) * mm, "end": v(-1.5, -48.72) * mm});
            skLineSegment(sketch, "E5668", {"start": v(-1.5, -48.72) * mm, "end": v(-1.45, -48.76) * mm});
            skLineSegment(sketch, "E5669", {"start": v(-1.45, -48.76) * mm, "end": v(-1.4, -48.8) * mm});
            skLineSegment(sketch, "E5670", {"start": v(-1.4, -48.8) * mm, "end": v(-1.35, -48.85) * mm});
            skLineSegment(sketch, "E5671", {"start": v(-1.35, -48.85) * mm, "end": v(-1.3, -48.9) * mm});
            skLineSegment(sketch, "E5672", {"start": v(-1.3, -48.9) * mm, "end": v(-1.25, -48.94) * mm});
            skLineSegment(sketch, "E5673", {"start": v(-1.25, -48.94) * mm, "end": v(-1.2, -48.99) * mm});
            skLineSegment(sketch, "E5674", {"start": v(-1.2, -48.99) * mm, "end": v(-1.14, -49.04) * mm});
            skLineSegment(sketch, "E5675", {"start": v(-1.14, -49.04) * mm, "end": v(-1.08, -49.08) * mm});
            skLineSegment(sketch, "E5676", {"start": v(-1.08, -49.08) * mm, "end": v(-1.02, -49.13) * mm});
            skLineSegment(sketch, "E5677", {"start": v(-1.02, -49.13) * mm, "end": v(-0.97, -49.18) * mm});
            skLineSegment(sketch, "E5678", {"start": v(-0.97, -49.18) * mm, "end": v(-0.9, -49.23) * mm});
            skLineSegment(sketch, "E5679", {"start": v(-0.9, -49.23) * mm, "end": v(-0.84, -49.28) * mm});
            skLineSegment(sketch, "E5680", {"start": v(-0.84, -49.28) * mm, "end": v(-0.78, -49.33) * mm});
            skLineSegment(sketch, "E5681", {"start": v(-0.78, -49.33) * mm, "end": v(-0.72, -49.38) * mm});
            skLineSegment(sketch, "E5682", {"start": v(-0.72, -49.38) * mm, "end": v(-0.65, -49.43) * mm});
            skLineSegment(sketch, "E5683", {"start": v(-0.65, -49.43) * mm, "end": v(-0.59, -49.48) * mm});
            skLineSegment(sketch, "E5684", {"start": v(-0.59, -49.48) * mm, "end": v(-0.52, -49.54) * mm});
            skLineSegment(sketch, "E5685", {"start": v(-0.52, -49.54) * mm, "end": v(-0.45, -49.59) * mm});
            skLineSegment(sketch, "E5686", {"start": v(-0.45, -49.59) * mm, "end": v(-0.38, -49.64) * mm});
            skLineSegment(sketch, "E5687", {"start": v(-0.38, -49.64) * mm, "end": v(-0.31, -49.7) * mm});
            skLineSegment(sketch, "E5688", {"start": v(-0.31, -49.7) * mm, "end": v(-0.24, -49.75) * mm});
            skLineSegment(sketch, "E5689", {"start": v(-0.24, -49.75) * mm, "end": v(-0.17, -49.8) * mm});
            skLineSegment(sketch, "E5690", {"start": v(-0.17, -49.8) * mm, "end": v(-0.1, -49.86) * mm});
            skLineSegment(sketch, "E5691", {"start": v(-0.1, -49.86) * mm, "end": v(-0.02, -49.91) * mm});
            skLineSegment(sketch, "E5692", {"start": v(-0.02, -49.91) * mm, "end": v(0.06, -49.97) * mm});
            skLineSegment(sketch, "E5693", {"start": v(0.06, -49.97) * mm, "end": v(0.14, -50.02) * mm});
            skLineSegment(sketch, "E5694", {"start": v(0.14, -50.02) * mm, "end": v(0.21, -50.08) * mm});
            skLineSegment(sketch, "E5695", {"start": v(0.21, -50.08) * mm, "end": v(0.3, -50.13) * mm});
            skLineSegment(sketch, "E5696", {"start": v(0.3, -50.13) * mm, "end": v(0.38, -50.19) * mm});
            skLineSegment(sketch, "E5697", {"start": v(0.38, -50.19) * mm, "end": v(0.46, -50.24) * mm});
            skLineSegment(sketch, "E5698", {"start": v(0.46, -50.24) * mm, "end": v(0.54, -50.3) * mm});
            skLineSegment(sketch, "E5699", {"start": v(0.54, -50.3) * mm, "end": v(0.63, -50.36) * mm});
            skLineSegment(sketch, "E5700", {"start": v(0.63, -50.36) * mm, "end": v(0.72, -50.42) * mm});
            skLineSegment(sketch, "E5701", {"start": v(0.72, -50.42) * mm, "end": v(0.8, -50.47) * mm});
            skLineSegment(sketch, "E5702", {"start": v(0.8, -50.47) * mm, "end": v(0.9, -50.53) * mm});
            skLineSegment(sketch, "E5703", {"start": v(0.9, -50.53) * mm, "end": v(0.95, -50.53) * mm});
            skLineSegment(sketch, "E5704", {"start": v(0.95, -50.53) * mm, "end": v(1.8, -49.94) * mm});
            skLineSegment(sketch, "E5705", {"start": v(1.8, -49.94) * mm, "end": v(1.83, -49.9) * mm});
            skLineSegment(sketch, "E5706", {"start": v(1.83, -49.9) * mm, "end": v(1.8, -49.8) * mm});
            skLineSegment(sketch, "E5707", {"start": v(1.8, -49.8) * mm, "end": v(1.79, -49.69) * mm});
            skLineSegment(sketch, "E5708", {"start": v(1.79, -49.69) * mm, "end": v(1.77, -49.59) * mm});
            skLineSegment(sketch, "E5709", {"start": v(1.77, -49.59) * mm, "end": v(1.75, -49.49) * mm});
            skLineSegment(sketch, "E5710", {"start": v(1.75, -49.49) * mm, "end": v(1.72, -49.39) * mm});
            skLineSegment(sketch, "E5711", {"start": v(1.72, -49.39) * mm, "end": v(1.7, -49.29) * mm});
            skLineSegment(sketch, "E5712", {"start": v(1.7, -49.29) * mm, "end": v(1.68, -49.2) * mm});
            skLineSegment(sketch, "E5713", {"start": v(1.68, -49.2) * mm, "end": v(1.66, -49.1) * mm});
            skLineSegment(sketch, "E5714", {"start": v(1.66, -49.1) * mm, "end": v(1.64, -49) * mm});
            skLineSegment(sketch, "E5715", {"start": v(1.64, -49) * mm, "end": v(1.61, -48.91) * mm});
            skLineSegment(sketch, "E5716", {"start": v(1.61, -48.91) * mm, "end": v(1.6, -48.82) * mm});
            skLineSegment(sketch, "E5717", {"start": v(1.6, -48.82) * mm, "end": v(1.57, -48.73) * mm});
            skLineSegment(sketch, "E5718", {"start": v(1.57, -48.73) * mm, "end": v(1.55, -48.64) * mm});
            skLineSegment(sketch, "E5719", {"start": v(1.55, -48.64) * mm, "end": v(1.52, -48.55) * mm});
            skLineSegment(sketch, "E5720", {"start": v(1.52, -48.55) * mm, "end": v(1.5, -48.46) * mm});
            skLineSegment(sketch, "E5721", {"start": v(1.5, -48.46) * mm, "end": v(1.48, -48.38) * mm});
            skLineSegment(sketch, "E5722", {"start": v(1.48, -48.38) * mm, "end": v(1.45, -48.3) * mm});
            skLineSegment(sketch, "E5723", {"start": v(1.45, -48.3) * mm, "end": v(1.43, -48.21) * mm});
            skLineSegment(sketch, "E5724", {"start": v(1.43, -48.21) * mm, "end": v(1.4, -48.13) * mm});
            skLineSegment(sketch, "E5725", {"start": v(1.4, -48.13) * mm, "end": v(1.38, -48.05) * mm});
            skLineSegment(sketch, "E5726", {"start": v(1.38, -48.05) * mm, "end": v(1.36, -47.97) * mm});
            skLineSegment(sketch, "E5727", {"start": v(1.36, -47.97) * mm, "end": v(1.34, -47.9) * mm});
            skLineSegment(sketch, "E5728", {"start": v(1.34, -47.9) * mm, "end": v(1.31, -47.82) * mm});
            skLineSegment(sketch, "E5729", {"start": v(1.31, -47.82) * mm, "end": v(1.29, -47.74) * mm});
            skLineSegment(sketch, "E5730", {"start": v(1.29, -47.74) * mm, "end": v(1.27, -47.67) * mm});
            skLineSegment(sketch, "E5731", {"start": v(1.27, -47.67) * mm, "end": v(1.24, -47.6) * mm});
            skLineSegment(sketch, "E5732", {"start": v(1.24, -47.6) * mm, "end": v(1.22, -47.53) * mm});
            skLineSegment(sketch, "E5733", {"start": v(1.22, -47.53) * mm, "end": v(1.2, -47.46) * mm});
            skLineSegment(sketch, "E5734", {"start": v(1.2, -47.46) * mm, "end": v(1.17, -47.39) * mm});
            skLineSegment(sketch, "E5735", {"start": v(1.17, -47.39) * mm, "end": v(1.15, -47.32) * mm});
            skLineSegment(sketch, "E5736", {"start": v(1.15, -47.32) * mm, "end": v(1.12, -47.25) * mm});
            skLineSegment(sketch, "E5737", {"start": v(1.12, -47.25) * mm, "end": v(1.1, -47.19) * mm});
            skLineSegment(sketch, "E5738", {"start": v(1.1, -47.19) * mm, "end": v(1.08, -47.12) * mm});
            skLineSegment(sketch, "E5739", {"start": v(1.08, -47.12) * mm, "end": v(1.05, -47.06) * mm});
            skLineSegment(sketch, "E5740", {"start": v(1.05, -47.06) * mm, "end": v(1.03, -47) * mm});
            skLineSegment(sketch, "E5741", {"start": v(1.03, -47) * mm, "end": v(1, -46.94) * mm});
            skLineSegment(sketch, "E5742", {"start": v(1, -46.94) * mm, "end": v(0.98, -46.88) * mm});
            skLineSegment(sketch, "E5743", {"start": v(0.98, -46.88) * mm, "end": v(0.96, -46.82) * mm});
            skLineSegment(sketch, "E5744", {"start": v(0.96, -46.82) * mm, "end": v(0.94, -46.77) * mm});
            skLineSegment(sketch, "E5745", {"start": v(0.94, -46.77) * mm, "end": v(0.92, -46.71) * mm});
            skLineSegment(sketch, "E5746", {"start": v(0.92, -46.71) * mm, "end": v(1.1, -46.57) * mm});
            skLineSegment(sketch, "E5747", {"start": v(1.1, -46.57) * mm, "end": v(1.75, -46.08) * mm});
            skLineSegment(sketch, "E5748", {"start": v(1.75, -46.08) * mm, "end": v(1.94, -45.95) * mm});
            skLineSegment(sketch, "E5749", {"start": v(1.94, -45.95) * mm, "end": v(1.99, -45.99) * mm});
            skLineSegment(sketch, "E5750", {"start": v(1.99, -45.99) * mm, "end": v(2.03, -46.03) * mm});
            skLineSegment(sketch, "E5751", {"start": v(2.03, -46.03) * mm, "end": v(2.08, -46.06) * mm});
            skLineSegment(sketch, "E5752", {"start": v(2.08, -46.06) * mm, "end": v(2.13, -46.1) * mm});
            skLineSegment(sketch, "E5753", {"start": v(2.13, -46.1) * mm, "end": v(2.18, -46.14) * mm});
            skLineSegment(sketch, "E5754", {"start": v(2.18, -46.14) * mm, "end": v(2.23, -46.18) * mm});
            skLineSegment(sketch, "E5755", {"start": v(2.23, -46.18) * mm, "end": v(2.29, -46.22) * mm});
            skLineSegment(sketch, "E5756", {"start": v(2.29, -46.22) * mm, "end": v(2.34, -46.26) * mm});
            skLineSegment(sketch, "E5757", {"start": v(2.34, -46.26) * mm, "end": v(2.4, -46.3) * mm});
            skLineSegment(sketch, "E5758", {"start": v(2.4, -46.3) * mm, "end": v(2.45, -46.35) * mm});
            skLineSegment(sketch, "E5759", {"start": v(2.45, -46.35) * mm, "end": v(2.51, -46.39) * mm});
            skLineSegment(sketch, "E5760", {"start": v(2.51, -46.39) * mm, "end": v(2.57, -46.43) * mm});
            skLineSegment(sketch, "E5761", {"start": v(2.57, -46.43) * mm, "end": v(2.63, -46.47) * mm});
            skLineSegment(sketch, "E5762", {"start": v(2.63, -46.47) * mm, "end": v(2.7, -46.51) * mm});
            skLineSegment(sketch, "E5763", {"start": v(2.7, -46.51) * mm, "end": v(2.76, -46.56) * mm});
            skLineSegment(sketch, "E5764", {"start": v(2.76, -46.56) * mm, "end": v(2.82, -46.6) * mm});
            skLineSegment(sketch, "E5765", {"start": v(2.82, -46.6) * mm, "end": v(2.89, -46.65) * mm});
            skLineSegment(sketch, "E5766", {"start": v(2.89, -46.65) * mm, "end": v(2.95, -46.7) * mm});
            skLineSegment(sketch, "E5767", {"start": v(2.95, -46.7) * mm, "end": v(3.02, -46.74) * mm});
            skLineSegment(sketch, "E5768", {"start": v(3.02, -46.74) * mm, "end": v(3.09, -46.78) * mm});
            skLineSegment(sketch, "E5769", {"start": v(3.09, -46.78) * mm, "end": v(3.16, -46.83) * mm});
            skLineSegment(sketch, "E5770", {"start": v(3.16, -46.83) * mm, "end": v(3.23, -46.87) * mm});
            skLineSegment(sketch, "E5771", {"start": v(3.23, -46.87) * mm, "end": v(3.3, -46.92) * mm});
            skLineSegment(sketch, "E5772", {"start": v(3.3, -46.92) * mm, "end": v(3.38, -46.96) * mm});
            skLineSegment(sketch, "E5773", {"start": v(3.38, -46.96) * mm, "end": v(3.45, -47.01) * mm});
            skLineSegment(sketch, "E5774", {"start": v(3.45, -47.01) * mm, "end": v(3.53, -47.06) * mm});
            skLineSegment(sketch, "E5775", {"start": v(3.53, -47.06) * mm, "end": v(3.6, -47.1) * mm});
            skLineSegment(sketch, "E5776", {"start": v(3.6, -47.1) * mm, "end": v(3.68, -47.15) * mm});
            skLineSegment(sketch, "E5777", {"start": v(3.68, -47.15) * mm, "end": v(3.76, -47.2) * mm});
            skLineSegment(sketch, "E5778", {"start": v(3.76, -47.2) * mm, "end": v(3.85, -47.25) * mm});
            skLineSegment(sketch, "E5779", {"start": v(3.85, -47.25) * mm, "end": v(3.93, -47.3) * mm});
            skLineSegment(sketch, "E5780", {"start": v(3.93, -47.3) * mm, "end": v(4.01, -47.34) * mm});
            skLineSegment(sketch, "E5781", {"start": v(4.01, -47.34) * mm, "end": v(4.1, -47.4) * mm});
            skLineSegment(sketch, "E5782", {"start": v(4.1, -47.4) * mm, "end": v(4.18, -47.44) * mm});
            skLineSegment(sketch, "E5783", {"start": v(4.18, -47.44) * mm, "end": v(4.27, -47.49) * mm});
            skLineSegment(sketch, "E5784", {"start": v(4.27, -47.49) * mm, "end": v(4.36, -47.54) * mm});
            skLineSegment(sketch, "E5785", {"start": v(4.36, -47.54) * mm, "end": v(4.45, -47.59) * mm});
            skLineSegment(sketch, "E5786", {"start": v(4.45, -47.59) * mm, "end": v(4.54, -47.64) * mm});
            skLineSegment(sketch, "E5787", {"start": v(4.54, -47.64) * mm, "end": v(4.64, -47.68) * mm});
            skLineSegment(sketch, "E5788", {"start": v(4.64, -47.68) * mm, "end": v(4.73, -47.73) * mm});
            skLineSegment(sketch, "E5789", {"start": v(4.73, -47.73) * mm, "end": v(4.78, -47.73) * mm});
            skLineSegment(sketch, "E5790", {"start": v(4.78, -47.73) * mm, "end": v(5.59, -47.07) * mm});
            skLineSegment(sketch, "E5791", {"start": v(5.59, -47.07) * mm, "end": v(5.6, -47.02) * mm});
            skLineSegment(sketch, "E5792", {"start": v(5.6, -47.02) * mm, "end": v(5.57, -46.92) * mm});
            skLineSegment(sketch, "E5793", {"start": v(5.57, -46.92) * mm, "end": v(5.54, -46.82) * mm});
            skLineSegment(sketch, "E5794", {"start": v(5.54, -46.82) * mm, "end": v(5.51, -46.72) * mm});
            skLineSegment(sketch, "E5795", {"start": v(5.51, -46.72) * mm, "end": v(5.48, -46.62) * mm});
            skLineSegment(sketch, "E5796", {"start": v(5.48, -46.62) * mm, "end": v(5.45, -46.52) * mm});
            skLineSegment(sketch, "E5797", {"start": v(5.45, -46.52) * mm, "end": v(5.42, -46.43) * mm});
            skLineSegment(sketch, "E5798", {"start": v(5.42, -46.43) * mm, "end": v(5.4, -46.33) * mm});
            skLineSegment(sketch, "E5799", {"start": v(5.4, -46.33) * mm, "end": v(5.36, -46.24) * mm});
            skLineSegment(sketch, "E5800", {"start": v(5.36, -46.24) * mm, "end": v(5.33, -46.15) * mm});
            skLineSegment(sketch, "E5801", {"start": v(5.33, -46.15) * mm, "end": v(5.3, -46.06) * mm});
            skLineSegment(sketch, "E5802", {"start": v(5.3, -46.06) * mm, "end": v(5.27, -45.97) * mm});
            skLineSegment(sketch, "E5803", {"start": v(5.27, -45.97) * mm, "end": v(5.24, -45.88) * mm});
            skLineSegment(sketch, "E5804", {"start": v(5.24, -45.88) * mm, "end": v(5.21, -45.8) * mm});
            skLineSegment(sketch, "E5805", {"start": v(5.21, -45.8) * mm, "end": v(5.18, -45.7) * mm});
            skLineSegment(sketch, "E5806", {"start": v(5.18, -45.7) * mm, "end": v(5.15, -45.62) * mm});
            skLineSegment(sketch, "E5807", {"start": v(5.15, -45.62) * mm, "end": v(5.12, -45.54) * mm});
            skLineSegment(sketch, "E5808", {"start": v(5.12, -45.54) * mm, "end": v(5.09, -45.46) * mm});
            skLineSegment(sketch, "E5809", {"start": v(5.09, -45.46) * mm, "end": v(5.06, -45.38) * mm});
            skLineSegment(sketch, "E5810", {"start": v(5.06, -45.38) * mm, "end": v(5.03, -45.3) * mm});
            skLineSegment(sketch, "E5811", {"start": v(5.03, -45.3) * mm, "end": v(5, -45.22) * mm});
            skLineSegment(sketch, "E5812", {"start": v(5, -45.22) * mm, "end": v(4.96, -45.15) * mm});
            skLineSegment(sketch, "E5813", {"start": v(4.96, -45.15) * mm, "end": v(4.93, -45.07) * mm});
            skLineSegment(sketch, "E5814", {"start": v(4.93, -45.07) * mm, "end": v(4.9, -45) * mm});
            skLineSegment(sketch, "E5815", {"start": v(4.9, -45) * mm, "end": v(4.87, -44.92) * mm});
            skLineSegment(sketch, "E5816", {"start": v(4.87, -44.92) * mm, "end": v(4.84, -44.85) * mm});
            skLineSegment(sketch, "E5817", {"start": v(4.84, -44.85) * mm, "end": v(4.81, -44.78) * mm});
            skLineSegment(sketch, "E5818", {"start": v(4.81, -44.78) * mm, "end": v(4.78, -44.71) * mm});
            skLineSegment(sketch, "E5819", {"start": v(4.78, -44.71) * mm, "end": v(4.75, -44.65) * mm});
            skLineSegment(sketch, "E5820", {"start": v(4.75, -44.65) * mm, "end": v(4.72, -44.58) * mm});
            skLineSegment(sketch, "E5821", {"start": v(4.72, -44.58) * mm, "end": v(4.7, -44.51) * mm});
            skLineSegment(sketch, "E5822", {"start": v(4.7, -44.51) * mm, "end": v(4.66, -44.45) * mm});
            skLineSegment(sketch, "E5823", {"start": v(4.66, -44.45) * mm, "end": v(4.64, -44.39) * mm});
            skLineSegment(sketch, "E5824", {"start": v(4.64, -44.39) * mm, "end": v(4.6, -44.33) * mm});
            skLineSegment(sketch, "E5825", {"start": v(4.6, -44.33) * mm, "end": v(4.58, -44.27) * mm});
            skLineSegment(sketch, "E5826", {"start": v(4.58, -44.27) * mm, "end": v(4.55, -44.2) * mm});
            skLineSegment(sketch, "E5827", {"start": v(4.55, -44.2) * mm, "end": v(4.52, -44.15) * mm});
            skLineSegment(sketch, "E5828", {"start": v(4.52, -44.15) * mm, "end": v(4.5, -44.1) * mm});
            skLineSegment(sketch, "E5829", {"start": v(4.5, -44.1) * mm, "end": v(4.46, -44.04) * mm});
            skLineSegment(sketch, "E5830", {"start": v(4.46, -44.04) * mm, "end": v(4.44, -43.98) * mm});
            skLineSegment(sketch, "E5831", {"start": v(4.44, -43.98) * mm, "end": v(4.4, -43.93) * mm});
            skLineSegment(sketch, "E5832", {"start": v(4.4, -43.93) * mm, "end": v(4.58, -43.77) * mm});
            skLineSegment(sketch, "E5833", {"start": v(4.58, -43.77) * mm, "end": v(5.18, -43.23) * mm});
            skLineSegment(sketch, "E5834", {"start": v(5.18, -43.23) * mm, "end": v(5.36, -43.08) * mm});
            skLineSegment(sketch, "E5835", {"start": v(5.36, -43.08) * mm, "end": v(5.4, -43.11) * mm});
            skLineSegment(sketch, "E5836", {"start": v(5.4, -43.11) * mm, "end": v(5.46, -43.15) * mm});
            skLineSegment(sketch, "E5837", {"start": v(5.46, -43.15) * mm, "end": v(5.51, -43.18) * mm});
            skLineSegment(sketch, "E5838", {"start": v(5.51, -43.18) * mm, "end": v(5.56, -43.21) * mm});
            skLineSegment(sketch, "E5839", {"start": v(5.56, -43.21) * mm, "end": v(5.62, -43.25) * mm});
            skLineSegment(sketch, "E5840", {"start": v(5.62, -43.25) * mm, "end": v(5.67, -43.28) * mm});
            skLineSegment(sketch, "E5841", {"start": v(5.67, -43.28) * mm, "end": v(5.73, -43.32) * mm});
            skLineSegment(sketch, "E5842", {"start": v(5.73, -43.32) * mm, "end": v(5.79, -43.35) * mm});
            skLineSegment(sketch, "E5843", {"start": v(5.79, -43.35) * mm, "end": v(5.85, -43.4) * mm});
            skLineSegment(sketch, "E5844", {"start": v(5.85, -43.4) * mm, "end": v(5.9, -43.43) * mm});
            skLineSegment(sketch, "E5845", {"start": v(5.9, -43.43) * mm, "end": v(5.97, -43.46) * mm});
            skLineSegment(sketch, "E5846", {"start": v(5.97, -43.46) * mm, "end": v(6.03, -43.5) * mm});
            skLineSegment(sketch, "E5847", {"start": v(6.03, -43.5) * mm, "end": v(6.1, -43.54) * mm});
            skLineSegment(sketch, "E5848", {"start": v(6.1, -43.54) * mm, "end": v(6.16, -43.57) * mm});
            skLineSegment(sketch, "E5849", {"start": v(6.16, -43.57) * mm, "end": v(6.23, -43.61) * mm});
            skLineSegment(sketch, "E5850", {"start": v(6.23, -43.61) * mm, "end": v(6.3, -43.65) * mm});
            skLineSegment(sketch, "E5851", {"start": v(6.3, -43.65) * mm, "end": v(6.36, -43.69) * mm});
            skLineSegment(sketch, "E5852", {"start": v(6.36, -43.69) * mm, "end": v(6.43, -43.73) * mm});
            skLineSegment(sketch, "E5853", {"start": v(6.43, -43.73) * mm, "end": v(6.5, -43.77) * mm});
            skLineSegment(sketch, "E5854", {"start": v(6.5, -43.77) * mm, "end": v(6.58, -43.8) * mm});
            skLineSegment(sketch, "E5855", {"start": v(6.58, -43.8) * mm, "end": v(6.65, -43.84) * mm});
            skLineSegment(sketch, "E5856", {"start": v(6.65, -43.84) * mm, "end": v(6.73, -43.88) * mm});
            skLineSegment(sketch, "E5857", {"start": v(6.73, -43.88) * mm, "end": v(6.8, -43.92) * mm});
            skLineSegment(sketch, "E5858", {"start": v(6.8, -43.92) * mm, "end": v(6.88, -43.96) * mm});
            skLineSegment(sketch, "E5859", {"start": v(6.88, -43.96) * mm, "end": v(6.96, -44) * mm});
            skLineSegment(sketch, "E5860", {"start": v(6.96, -44) * mm, "end": v(7.04, -44.04) * mm});
            skLineSegment(sketch, "E5861", {"start": v(7.04, -44.04) * mm, "end": v(7.12, -44.08) * mm});
            skLineSegment(sketch, "E5862", {"start": v(7.12, -44.08) * mm, "end": v(7.2, -44.12) * mm});
            skLineSegment(sketch, "E5863", {"start": v(7.2, -44.12) * mm, "end": v(7.29, -44.16) * mm});
            skLineSegment(sketch, "E5864", {"start": v(7.29, -44.16) * mm, "end": v(7.37, -44.2) * mm});
            skLineSegment(sketch, "E5865", {"start": v(7.37, -44.2) * mm, "end": v(7.46, -44.24) * mm});
            skLineSegment(sketch, "E5866", {"start": v(7.46, -44.24) * mm, "end": v(7.55, -44.28) * mm});
            skLineSegment(sketch, "E5867", {"start": v(7.55, -44.28) * mm, "end": v(7.64, -44.32) * mm});
            skLineSegment(sketch, "E5868", {"start": v(7.64, -44.32) * mm, "end": v(7.73, -44.36) * mm});
            skLineSegment(sketch, "E5869", {"start": v(7.73, -44.36) * mm, "end": v(7.82, -44.4) * mm});
            skLineSegment(sketch, "E5870", {"start": v(7.82, -44.4) * mm, "end": v(7.91, -44.44) * mm});
            skLineSegment(sketch, "E5871", {"start": v(7.91, -44.44) * mm, "end": v(8, -44.48) * mm});
            skLineSegment(sketch, "E5872", {"start": v(8, -44.48) * mm, "end": v(8.1, -44.53) * mm});
            skLineSegment(sketch, "E5873", {"start": v(8.1, -44.53) * mm, "end": v(8.2, -44.57) * mm});
            skLineSegment(sketch, "E5874", {"start": v(8.2, -44.57) * mm, "end": v(8.3, -44.6) * mm});
            skLineSegment(sketch, "E5875", {"start": v(8.3, -44.6) * mm, "end": v(8.35, -44.6) * mm});
            skLineSegment(sketch, "E5876", {"start": v(8.35, -44.6) * mm, "end": v(9.1, -43.87) * mm});
            skLineSegment(sketch, "E5877", {"start": v(9.1, -43.87) * mm, "end": v(9.1, -43.82) * mm});
            skLineSegment(sketch, "E5878", {"start": v(9.1, -43.82) * mm, "end": v(9.07, -43.72) * mm});
            skLineSegment(sketch, "E5879", {"start": v(9.07, -43.72) * mm, "end": v(9.03, -43.62) * mm});
            skLineSegment(sketch, "E5880", {"start": v(9.03, -43.62) * mm, "end": v(8.99, -43.52) * mm});
            skLineSegment(sketch, "E5881", {"start": v(8.99, -43.52) * mm, "end": v(8.95, -43.43) * mm});
            skLineSegment(sketch, "E5882", {"start": v(8.95, -43.43) * mm, "end": v(8.91, -43.33) * mm});
            skLineSegment(sketch, "E5883", {"start": v(8.91, -43.33) * mm, "end": v(8.87, -43.24) * mm});
            skLineSegment(sketch, "E5884", {"start": v(8.87, -43.24) * mm, "end": v(8.83, -43.15) * mm});
            skLineSegment(sketch, "E5885", {"start": v(8.83, -43.15) * mm, "end": v(8.8, -43.06) * mm});
            skLineSegment(sketch, "E5886", {"start": v(8.8, -43.06) * mm, "end": v(8.76, -42.97) * mm});
            skLineSegment(sketch, "E5887", {"start": v(8.76, -42.97) * mm, "end": v(8.72, -42.88) * mm});
            skLineSegment(sketch, "E5888", {"start": v(8.72, -42.88) * mm, "end": v(8.68, -42.8) * mm});
            skLineSegment(sketch, "E5889", {"start": v(8.68, -42.8) * mm, "end": v(8.64, -42.71) * mm});
            skLineSegment(sketch, "E5890", {"start": v(8.64, -42.71) * mm, "end": v(8.6, -42.63) * mm});
            skLineSegment(sketch, "E5891", {"start": v(8.6, -42.63) * mm, "end": v(8.56, -42.55) * mm});
            skLineSegment(sketch, "E5892", {"start": v(8.56, -42.55) * mm, "end": v(8.53, -42.47) * mm});
            skLineSegment(sketch, "E5893", {"start": v(8.53, -42.47) * mm, "end": v(8.49, -42.39) * mm});
            skLineSegment(sketch, "E5894", {"start": v(8.49, -42.39) * mm, "end": v(8.45, -42.3) * mm});
            skLineSegment(sketch, "E5895", {"start": v(8.45, -42.3) * mm, "end": v(8.41, -42.23) * mm});
            skLineSegment(sketch, "E5896", {"start": v(8.41, -42.23) * mm, "end": v(8.38, -42.15) * mm});
            skLineSegment(sketch, "E5897", {"start": v(8.38, -42.15) * mm, "end": v(8.34, -42.08) * mm});
            skLineSegment(sketch, "E5898", {"start": v(8.34, -42.08) * mm, "end": v(8.3, -42) * mm});
            skLineSegment(sketch, "E5899", {"start": v(8.3, -42) * mm, "end": v(8.26, -41.93) * mm});
            skLineSegment(sketch, "E5900", {"start": v(8.26, -41.93) * mm, "end": v(8.23, -41.86) * mm});
            skLineSegment(sketch, "E5901", {"start": v(8.23, -41.86) * mm, "end": v(8.19, -41.8) * mm});
            skLineSegment(sketch, "E5902", {"start": v(8.19, -41.8) * mm, "end": v(8.15, -41.73) * mm});
            skLineSegment(sketch, "E5903", {"start": v(8.15, -41.73) * mm, "end": v(8.12, -41.66) * mm});
            skLineSegment(sketch, "E5904", {"start": v(8.12, -41.66) * mm, "end": v(8.08, -41.6) * mm});
            skLineSegment(sketch, "E5905", {"start": v(8.08, -41.6) * mm, "end": v(8.04, -41.53) * mm});
            skLineSegment(sketch, "E5906", {"start": v(8.04, -41.53) * mm, "end": v(8, -41.46) * mm});
            skLineSegment(sketch, "E5907", {"start": v(8, -41.46) * mm, "end": v(7.97, -41.4) * mm});
            skLineSegment(sketch, "E5908", {"start": v(7.97, -41.4) * mm, "end": v(7.94, -41.34) * mm});
            skLineSegment(sketch, "E5909", {"start": v(7.94, -41.34) * mm, "end": v(7.9, -41.28) * mm});
            skLineSegment(sketch, "E5910", {"start": v(7.9, -41.28) * mm, "end": v(7.87, -41.22) * mm});
            skLineSegment(sketch, "E5911", {"start": v(7.87, -41.22) * mm, "end": v(7.84, -41.17) * mm});
            skLineSegment(sketch, "E5912", {"start": v(7.84, -41.17) * mm, "end": v(7.8, -41.1) * mm});
            skLineSegment(sketch, "E5913", {"start": v(7.8, -41.1) * mm, "end": v(7.77, -41.05) * mm});
            skLineSegment(sketch, "E5914", {"start": v(7.77, -41.05) * mm, "end": v(7.74, -41) * mm});
            skLineSegment(sketch, "E5915", {"start": v(7.74, -41) * mm, "end": v(7.7, -40.95) * mm});
            skLineSegment(sketch, "E5916", {"start": v(7.7, -40.95) * mm, "end": v(7.67, -40.9) * mm});
            skLineSegment(sketch, "E5917", {"start": v(7.67, -40.9) * mm, "end": v(7.64, -40.85) * mm});
            skLineSegment(sketch, "E5918", {"start": v(7.64, -40.85) * mm, "end": v(7.8, -40.67) * mm});
            skLineSegment(sketch, "E5919", {"start": v(7.8, -40.67) * mm, "end": v(8.34, -40.08) * mm});
            skLineSegment(sketch, "E5920", {"start": v(8.34, -40.08) * mm, "end": v(8.5, -39.91) * mm});
            skLineSegment(sketch, "E5921", {"start": v(8.5, -39.91) * mm, "end": v(8.56, -39.94) * mm});
            skLineSegment(sketch, "E5922", {"start": v(8.56, -39.94) * mm, "end": v(8.61, -39.97) * mm});
            skLineSegment(sketch, "E5923", {"start": v(8.61, -39.97) * mm, "end": v(8.67, -40) * mm});
            skLineSegment(sketch, "E5924", {"start": v(8.67, -40) * mm, "end": v(8.73, -40.03) * mm});
            skLineSegment(sketch, "E5925", {"start": v(8.73, -40.03) * mm, "end": v(8.78, -40.06) * mm});
            skLineSegment(sketch, "E5926", {"start": v(8.78, -40.06) * mm, "end": v(8.84, -40.09) * mm});
            skLineSegment(sketch, "E5927", {"start": v(8.84, -40.09) * mm, "end": v(8.9, -40.12) * mm});
            skLineSegment(sketch, "E5928", {"start": v(8.9, -40.12) * mm, "end": v(8.96, -40.15) * mm});
            skLineSegment(sketch, "E5929", {"start": v(8.96, -40.15) * mm, "end": v(9.02, -40.18) * mm});
            skLineSegment(sketch, "E5930", {"start": v(9.02, -40.18) * mm, "end": v(9.09, -40.21) * mm});
            skLineSegment(sketch, "E5931", {"start": v(9.09, -40.21) * mm, "end": v(9.15, -40.24) * mm});
            skLineSegment(sketch, "E5932", {"start": v(9.15, -40.24) * mm, "end": v(9.22, -40.27) * mm});
            skLineSegment(sketch, "E5933", {"start": v(9.22, -40.27) * mm, "end": v(9.28, -40.3) * mm});
            skLineSegment(sketch, "E5934", {"start": v(9.28, -40.3) * mm, "end": v(9.35, -40.33) * mm});
            skLineSegment(sketch, "E5935", {"start": v(9.35, -40.33) * mm, "end": v(9.42, -40.37) * mm});
            skLineSegment(sketch, "E5936", {"start": v(9.42, -40.37) * mm, "end": v(9.5, -40.4) * mm});
            skLineSegment(sketch, "E5937", {"start": v(9.5, -40.4) * mm, "end": v(9.56, -40.43) * mm});
            skLineSegment(sketch, "E5938", {"start": v(9.56, -40.43) * mm, "end": v(9.64, -40.46) * mm});
            skLineSegment(sketch, "E5939", {"start": v(9.64, -40.46) * mm, "end": v(9.71, -40.5) * mm});
            skLineSegment(sketch, "E5940", {"start": v(9.71, -40.5) * mm, "end": v(9.79, -40.53) * mm});
            skLineSegment(sketch, "E5941", {"start": v(9.79, -40.53) * mm, "end": v(9.87, -40.56) * mm});
            skLineSegment(sketch, "E5942", {"start": v(9.87, -40.56) * mm, "end": v(9.94, -40.6) * mm});
            skLineSegment(sketch, "E5943", {"start": v(9.94, -40.6) * mm, "end": v(10.02, -40.62) * mm});
            skLineSegment(sketch, "E5944", {"start": v(10.02, -40.62) * mm, "end": v(10.1, -40.66) * mm});
            skLineSegment(sketch, "E5945", {"start": v(10.1, -40.66) * mm, "end": v(10.19, -40.69) * mm});
            skLineSegment(sketch, "E5946", {"start": v(10.19, -40.69) * mm, "end": v(10.27, -40.72) * mm});
            skLineSegment(sketch, "E5947", {"start": v(10.27, -40.72) * mm, "end": v(10.35, -40.75) * mm});
            skLineSegment(sketch, "E5948", {"start": v(10.35, -40.75) * mm, "end": v(10.44, -40.79) * mm});
            skLineSegment(sketch, "E5949", {"start": v(10.44, -40.79) * mm, "end": v(10.53, -40.82) * mm});
            skLineSegment(sketch, "E5950", {"start": v(10.53, -40.82) * mm, "end": v(10.62, -40.85) * mm});
            skLineSegment(sketch, "E5951", {"start": v(10.62, -40.85) * mm, "end": v(10.7, -40.88) * mm});
            skLineSegment(sketch, "E5952", {"start": v(10.7, -40.88) * mm, "end": v(10.8, -40.91) * mm});
            skLineSegment(sketch, "E5953", {"start": v(10.8, -40.91) * mm, "end": v(10.89, -40.95) * mm});
            skLineSegment(sketch, "E5954", {"start": v(10.89, -40.95) * mm, "end": v(10.98, -40.98) * mm});
            skLineSegment(sketch, "E5955", {"start": v(10.98, -40.98) * mm, "end": v(11.08, -41.01) * mm});
            skLineSegment(sketch, "E5956", {"start": v(11.08, -41.01) * mm, "end": v(11.18, -41.04) * mm});
            skLineSegment(sketch, "E5957", {"start": v(11.18, -41.04) * mm, "end": v(11.27, -41.08) * mm});
            skLineSegment(sketch, "E5958", {"start": v(11.27, -41.08) * mm, "end": v(11.37, -41.1) * mm});
            skLineSegment(sketch, "E5959", {"start": v(11.37, -41.1) * mm, "end": v(11.47, -41.14) * mm});
            skLineSegment(sketch, "E5960", {"start": v(11.47, -41.14) * mm, "end": v(11.57, -41.17) * mm});
            skLineSegment(sketch, "E5961", {"start": v(11.57, -41.17) * mm, "end": v(11.62, -41.15) * mm});
            skLineSegment(sketch, "E5962", {"start": v(11.62, -41.15) * mm, "end": v(12.3, -40.36) * mm});
            skLineSegment(sketch, "E5963", {"start": v(12.3, -40.36) * mm, "end": v(12.3, -40.31) * mm});
            skLineSegment(sketch, "E5964", {"start": v(12.3, -40.31) * mm, "end": v(12.26, -40.22) * mm});
            skLineSegment(sketch, "E5965", {"start": v(12.26, -40.22) * mm, "end": v(12.21, -40.12) * mm});
            skLineSegment(sketch, "E5966", {"start": v(12.21, -40.12) * mm, "end": v(12.16, -40.03) * mm});
            skLineSegment(sketch, "E5967", {"start": v(12.16, -40.03) * mm, "end": v(12.12, -39.94) * mm});
            skLineSegment(sketch, "E5968", {"start": v(12.12, -39.94) * mm, "end": v(12.07, -39.85) * mm});
            skLineSegment(sketch, "E5969", {"start": v(12.07, -39.85) * mm, "end": v(12.02, -39.76) * mm});
            skLineSegment(sketch, "E5970", {"start": v(12.02, -39.76) * mm, "end": v(11.98, -39.67) * mm});
            skLineSegment(sketch, "E5971", {"start": v(11.98, -39.67) * mm, "end": v(11.93, -39.59) * mm});
            skLineSegment(sketch, "E5972", {"start": v(11.93, -39.59) * mm, "end": v(11.88, -39.5) * mm});
            skLineSegment(sketch, "E5973", {"start": v(11.88, -39.5) * mm, "end": v(11.84, -39.42) * mm});
            skLineSegment(sketch, "E5974", {"start": v(11.84, -39.42) * mm, "end": v(11.8, -39.34) * mm});
            skLineSegment(sketch, "E5975", {"start": v(11.8, -39.34) * mm, "end": v(11.74, -39.25) * mm});
            skLineSegment(sketch, "E5976", {"start": v(11.74, -39.25) * mm, "end": v(11.7, -39.17) * mm});
            skLineSegment(sketch, "E5977", {"start": v(11.7, -39.17) * mm, "end": v(11.65, -39.1) * mm});
            skLineSegment(sketch, "E5978", {"start": v(11.65, -39.1) * mm, "end": v(11.6, -39.02) * mm});
            skLineSegment(sketch, "E5979", {"start": v(11.6, -39.02) * mm, "end": v(11.56, -38.94) * mm});
            skLineSegment(sketch, "E5980", {"start": v(11.56, -38.94) * mm, "end": v(11.52, -38.87) * mm});
            skLineSegment(sketch, "E5981", {"start": v(11.52, -38.87) * mm, "end": v(11.47, -38.8) * mm});
            skLineSegment(sketch, "E5982", {"start": v(11.47, -38.8) * mm, "end": v(11.43, -38.72) * mm});
            skLineSegment(sketch, "E5983", {"start": v(11.43, -38.72) * mm, "end": v(11.39, -38.65) * mm});
            skLineSegment(sketch, "E5984", {"start": v(11.39, -38.65) * mm, "end": v(11.34, -38.58) * mm});
            skLineSegment(sketch, "E5985", {"start": v(11.34, -38.58) * mm, "end": v(11.3, -38.51) * mm});
            skLineSegment(sketch, "E5986", {"start": v(11.3, -38.51) * mm, "end": v(11.26, -38.45) * mm});
            skLineSegment(sketch, "E5987", {"start": v(11.26, -38.45) * mm, "end": v(11.21, -38.38) * mm});
            skLineSegment(sketch, "E5988", {"start": v(11.21, -38.38) * mm, "end": v(11.17, -38.31) * mm});
            skLineSegment(sketch, "E5989", {"start": v(11.17, -38.31) * mm, "end": v(11.13, -38.25) * mm});
            skLineSegment(sketch, "E5990", {"start": v(11.13, -38.25) * mm, "end": v(11.09, -38.19) * mm});
            skLineSegment(sketch, "E5991", {"start": v(11.09, -38.19) * mm, "end": v(11.04, -38.13) * mm});
            skLineSegment(sketch, "E5992", {"start": v(11.04, -38.13) * mm, "end": v(11, -38.07) * mm});
            skLineSegment(sketch, "E5993", {"start": v(11, -38.07) * mm, "end": v(10.96, -38) * mm});
            skLineSegment(sketch, "E5994", {"start": v(10.96, -38) * mm, "end": v(10.92, -37.95) * mm});
            skLineSegment(sketch, "E5995", {"start": v(10.92, -37.95) * mm, "end": v(10.88, -37.9) * mm});
            skLineSegment(sketch, "E5996", {"start": v(10.88, -37.9) * mm, "end": v(10.84, -37.84) * mm});
            skLineSegment(sketch, "E5997", {"start": v(10.84, -37.84) * mm, "end": v(10.8, -37.79) * mm});
            skLineSegment(sketch, "E5998", {"start": v(10.8, -37.79) * mm, "end": v(10.77, -37.73) * mm});
            skLineSegment(sketch, "E5999", {"start": v(10.77, -37.73) * mm, "end": v(10.73, -37.68) * mm});
            skLineSegment(sketch, "E6000", {"start": v(10.73, -37.68) * mm, "end": v(10.69, -37.63) * mm});
            skLineSegment(sketch, "E6001", {"start": v(10.69, -37.63) * mm, "end": v(10.65, -37.58) * mm});
            skLineSegment(sketch, "E6002", {"start": v(10.65, -37.58) * mm, "end": v(10.62, -37.53) * mm});
            skLineSegment(sketch, "E6003", {"start": v(10.62, -37.53) * mm, "end": v(10.58, -37.49) * mm});
            skLineSegment(sketch, "E6004", {"start": v(10.58, -37.49) * mm, "end": v(10.72, -37.3) * mm});
            skLineSegment(sketch, "E6005", {"start": v(10.72, -37.3) * mm, "end": v(11.21, -36.66) * mm});
            skLineSegment(sketch, "E6006", {"start": v(11.21, -36.66) * mm, "end": v(11.36, -36.48) * mm});
            skLineSegment(sketch, "E6007", {"start": v(11.36, -36.48) * mm, "end": v(11.42, -36.5) * mm});
            skLineSegment(sketch, "E6008", {"start": v(11.42, -36.5) * mm, "end": v(11.47, -36.53) * mm});
            skLineSegment(sketch, "E6009", {"start": v(11.47, -36.53) * mm, "end": v(11.53, -36.55) * mm});
            skLineSegment(sketch, "E6010", {"start": v(11.53, -36.55) * mm, "end": v(11.59, -36.57) * mm});
            skLineSegment(sketch, "E6011", {"start": v(11.59, -36.57) * mm, "end": v(11.65, -36.6) * mm});
            skLineSegment(sketch, "E6012", {"start": v(11.65, -36.6) * mm, "end": v(11.7, -36.62) * mm});
            skLineSegment(sketch, "E6013", {"start": v(11.7, -36.62) * mm, "end": v(11.77, -36.65) * mm});
            skLineSegment(sketch, "E6014", {"start": v(11.77, -36.65) * mm, "end": v(11.83, -36.67) * mm});
            skLineSegment(sketch, "E6015", {"start": v(11.83, -36.67) * mm, "end": v(11.9, -36.7) * mm});
            skLineSegment(sketch, "E6016", {"start": v(11.9, -36.7) * mm, "end": v(11.96, -36.72) * mm});
            skLineSegment(sketch, "E6017", {"start": v(11.96, -36.72) * mm, "end": v(12.03, -36.75) * mm});
            skLineSegment(sketch, "E6018", {"start": v(12.03, -36.75) * mm, "end": v(12.1, -36.77) * mm});
            skLineSegment(sketch, "E6019", {"start": v(12.1, -36.77) * mm, "end": v(12.17, -36.8) * mm});
            skLineSegment(sketch, "E6020", {"start": v(12.17, -36.8) * mm, "end": v(12.24, -36.82) * mm});
            skLineSegment(sketch, "E6021", {"start": v(12.24, -36.82) * mm, "end": v(12.31, -36.85) * mm});
            skLineSegment(sketch, "E6022", {"start": v(12.31, -36.85) * mm, "end": v(12.38, -36.87) * mm});
            skLineSegment(sketch, "E6023", {"start": v(12.38, -36.87) * mm, "end": v(12.46, -36.9) * mm});
            skLineSegment(sketch, "E6024", {"start": v(12.46, -36.9) * mm, "end": v(12.53, -36.92) * mm});
            skLineSegment(sketch, "E6025", {"start": v(12.53, -36.92) * mm, "end": v(12.61, -36.95) * mm});
            skLineSegment(sketch, "E6026", {"start": v(12.61, -36.95) * mm, "end": v(12.7, -36.97) * mm});
            skLineSegment(sketch, "E6027", {"start": v(12.7, -36.97) * mm, "end": v(12.77, -37) * mm});
            skLineSegment(sketch, "E6028", {"start": v(12.77, -37) * mm, "end": v(12.85, -37.02) * mm});
            skLineSegment(sketch, "E6029", {"start": v(12.85, -37.02) * mm, "end": v(12.93, -37.05) * mm});
            skLineSegment(sketch, "E6030", {"start": v(12.93, -37.05) * mm, "end": v(13.02, -37.07) * mm});
            skLineSegment(sketch, "E6031", {"start": v(13.02, -37.07) * mm, "end": v(13.1, -37.1) * mm});
            skLineSegment(sketch, "E6032", {"start": v(13.1, -37.1) * mm, "end": v(13.19, -37.12) * mm});
            skLineSegment(sketch, "E6033", {"start": v(13.19, -37.12) * mm, "end": v(13.27, -37.15) * mm});
            skLineSegment(sketch, "E6034", {"start": v(13.27, -37.15) * mm, "end": v(13.36, -37.17) * mm});
            skLineSegment(sketch, "E6035", {"start": v(13.36, -37.17) * mm, "end": v(13.45, -37.2) * mm});
            skLineSegment(sketch, "E6036", {"start": v(13.45, -37.2) * mm, "end": v(13.54, -37.22) * mm});
            skLineSegment(sketch, "E6037", {"start": v(13.54, -37.22) * mm, "end": v(13.64, -37.25) * mm});
            skLineSegment(sketch, "E6038", {"start": v(13.64, -37.25) * mm, "end": v(13.73, -37.27) * mm});
            skLineSegment(sketch, "E6039", {"start": v(13.73, -37.27) * mm, "end": v(13.83, -37.3) * mm});
            skLineSegment(sketch, "E6040", {"start": v(13.83, -37.3) * mm, "end": v(13.92, -37.32) * mm});
            skLineSegment(sketch, "E6041", {"start": v(13.92, -37.32) * mm, "end": v(14.02, -37.34) * mm});
            skLineSegment(sketch, "E6042", {"start": v(14.02, -37.34) * mm, "end": v(14.12, -37.36) * mm});
            skLineSegment(sketch, "E6043", {"start": v(14.12, -37.36) * mm, "end": v(14.22, -37.39) * mm});
            skLineSegment(sketch, "E6044", {"start": v(14.22, -37.39) * mm, "end": v(14.32, -37.41) * mm});
            skLineSegment(sketch, "E6045", {"start": v(14.32, -37.41) * mm, "end": v(14.42, -37.43) * mm});
            skLineSegment(sketch, "E6046", {"start": v(14.42, -37.43) * mm, "end": v(14.53, -37.46) * mm});
            skLineSegment(sketch, "E6047", {"start": v(14.53, -37.46) * mm, "end": v(14.57, -37.44) * mm});
            skLineSegment(sketch, "E6048", {"start": v(14.57, -37.44) * mm, "end": v(15.17, -36.59) * mm});
            skLineSegment(sketch, "E6049", {"start": v(15.17, -36.59) * mm, "end": v(15.18, -36.54) * mm});
            skLineSegment(sketch, "E6050", {"start": v(15.18, -36.54) * mm, "end": v(15.12, -36.44) * mm});
            skLineSegment(sketch, "E6051", {"start": v(15.12, -36.44) * mm, "end": v(15.07, -36.36) * mm});
            skLineSegment(sketch, "E6052", {"start": v(15.07, -36.36) * mm, "end": v(15.01, -36.27) * mm});
            skLineSegment(sketch, "E6053", {"start": v(15.01, -36.27) * mm, "end": v(14.96, -36.18) * mm});
            skLineSegment(sketch, "E6054", {"start": v(14.96, -36.18) * mm, "end": v(14.9, -36.1) * mm});
            skLineSegment(sketch, "E6055", {"start": v(14.9, -36.1) * mm, "end": v(14.85, -36.01) * mm});
            skLineSegment(sketch, "E6056", {"start": v(14.85, -36.01) * mm, "end": v(14.8, -35.93) * mm});
            skLineSegment(sketch, "E6057", {"start": v(14.8, -35.93) * mm, "end": v(14.74, -35.85) * mm});
            skLineSegment(sketch, "E6058", {"start": v(14.74, -35.85) * mm, "end": v(14.69, -35.77) * mm});
            skLineSegment(sketch, "E6059", {"start": v(14.69, -35.77) * mm, "end": v(14.63, -35.69) * mm});
            skLineSegment(sketch, "E6060", {"start": v(14.63, -35.69) * mm, "end": v(14.58, -35.6) * mm});
            skLineSegment(sketch, "E6061", {"start": v(14.58, -35.6) * mm, "end": v(14.53, -35.53) * mm});
            skLineSegment(sketch, "E6062", {"start": v(14.53, -35.53) * mm, "end": v(14.47, -35.46) * mm});
            skLineSegment(sketch, "E6063", {"start": v(14.47, -35.46) * mm, "end": v(14.42, -35.38) * mm});
            skLineSegment(sketch, "E6064", {"start": v(14.42, -35.38) * mm, "end": v(14.37, -35.3) * mm});
            skLineSegment(sketch, "E6065", {"start": v(14.37, -35.3) * mm, "end": v(14.32, -35.24) * mm});
            skLineSegment(sketch, "E6066", {"start": v(14.32, -35.24) * mm, "end": v(14.27, -35.17) * mm});
            skLineSegment(sketch, "E6067", {"start": v(14.27, -35.17) * mm, "end": v(14.21, -35.1) * mm});
            skLineSegment(sketch, "E6068", {"start": v(14.21, -35.1) * mm, "end": v(14.16, -35.03) * mm});
            skLineSegment(sketch, "E6069", {"start": v(14.16, -35.03) * mm, "end": v(14.11, -34.96) * mm});
            skLineSegment(sketch, "E6070", {"start": v(14.11, -34.96) * mm, "end": v(14.06, -34.9) * mm});
            skLineSegment(sketch, "E6071", {"start": v(14.06, -34.9) * mm, "end": v(14.01, -34.83) * mm});
            skLineSegment(sketch, "E6072", {"start": v(14.01, -34.83) * mm, "end": v(13.97, -34.77) * mm});
            skLineSegment(sketch, "E6073", {"start": v(13.97, -34.77) * mm, "end": v(13.92, -34.7) * mm});
            skLineSegment(sketch, "E6074", {"start": v(13.92, -34.7) * mm, "end": v(13.87, -34.65) * mm});
            skLineSegment(sketch, "E6075", {"start": v(13.87, -34.65) * mm, "end": v(13.82, -34.59) * mm});
            skLineSegment(sketch, "E6076", {"start": v(13.82, -34.59) * mm, "end": v(13.77, -34.53) * mm});
            skLineSegment(sketch, "E6077", {"start": v(13.77, -34.53) * mm, "end": v(13.73, -34.47) * mm});
            skLineSegment(sketch, "E6078", {"start": v(13.73, -34.47) * mm, "end": v(13.68, -34.42) * mm});
            skLineSegment(sketch, "E6079", {"start": v(13.68, -34.42) * mm, "end": v(13.63, -34.36) * mm});
            skLineSegment(sketch, "E6080", {"start": v(13.63, -34.36) * mm, "end": v(13.59, -34.3) * mm});
            skLineSegment(sketch, "E6081", {"start": v(13.59, -34.3) * mm, "end": v(13.54, -34.26) * mm});
            skLineSegment(sketch, "E6082", {"start": v(13.54, -34.26) * mm, "end": v(13.5, -34.2) * mm});
            skLineSegment(sketch, "E6083", {"start": v(13.5, -34.2) * mm, "end": v(13.46, -34.15) * mm});
            skLineSegment(sketch, "E6084", {"start": v(13.46, -34.15) * mm, "end": v(13.41, -34.1) * mm});
            skLineSegment(sketch, "E6085", {"start": v(13.41, -34.1) * mm, "end": v(13.37, -34.06) * mm});
            skLineSegment(sketch, "E6086", {"start": v(13.37, -34.06) * mm, "end": v(13.33, -34) * mm});
            skLineSegment(sketch, "E6087", {"start": v(13.33, -34) * mm, "end": v(13.29, -33.96) * mm});
            skLineSegment(sketch, "E6088", {"start": v(13.29, -33.96) * mm, "end": v(13.25, -33.92) * mm});
            skLineSegment(sketch, "E6089", {"start": v(13.25, -33.92) * mm, "end": v(13.2, -33.87) * mm});
            skLineSegment(sketch, "E6090", {"start": v(13.2, -33.87) * mm, "end": v(13.33, -33.67) * mm});
            skLineSegment(sketch, "E6091", {"start": v(13.33, -33.67) * mm, "end": v(13.76, -33) * mm});
            skLineSegment(sketch, "E6092", {"start": v(13.76, -33) * mm, "end": v(13.9, -32.8) * mm});
            skLineSegment(sketch, "E6093", {"start": v(13.9, -32.8) * mm, "end": v(13.95, -32.82) * mm});
            skLineSegment(sketch, "E6094", {"start": v(13.95, -32.82) * mm, "end": v(14, -32.84) * mm});
            skLineSegment(sketch, "E6095", {"start": v(14, -32.84) * mm, "end": v(14.07, -32.86) * mm});
            skLineSegment(sketch, "E6096", {"start": v(14.07, -32.86) * mm, "end": v(14.13, -32.88) * mm});
            skLineSegment(sketch, "E6097", {"start": v(14.13, -32.88) * mm, "end": v(14.2, -32.9) * mm});
            skLineSegment(sketch, "E6098", {"start": v(14.2, -32.9) * mm, "end": v(14.25, -32.91) * mm});
            skLineSegment(sketch, "E6099", {"start": v(14.25, -32.91) * mm, "end": v(14.32, -32.93) * mm});
            skLineSegment(sketch, "E6100", {"start": v(14.32, -32.93) * mm, "end": v(14.38, -32.95) * mm});
            skLineSegment(sketch, "E6101", {"start": v(14.38, -32.95) * mm, "end": v(14.45, -32.97) * mm});
            skLineSegment(sketch, "E6102", {"start": v(14.45, -32.97) * mm, "end": v(14.52, -32.99) * mm});
            skLineSegment(sketch, "E6103", {"start": v(14.52, -32.99) * mm, "end": v(14.59, -33) * mm});
            skLineSegment(sketch, "E6104", {"start": v(14.59, -33) * mm, "end": v(14.66, -33.03) * mm});
            skLineSegment(sketch, "E6105", {"start": v(14.66, -33.03) * mm, "end": v(14.73, -33.05) * mm});
            skLineSegment(sketch, "E6106", {"start": v(14.73, -33.05) * mm, "end": v(14.8, -33.06) * mm});
            skLineSegment(sketch, "E6107", {"start": v(14.8, -33.06) * mm, "end": v(14.87, -33.08) * mm});
            skLineSegment(sketch, "E6108", {"start": v(14.87, -33.08) * mm, "end": v(14.95, -33.1) * mm});
            skLineSegment(sketch, "E6109", {"start": v(14.95, -33.1) * mm, "end": v(15.03, -33.12) * mm});
            skLineSegment(sketch, "E6110", {"start": v(15.03, -33.12) * mm, "end": v(15.1, -33.14) * mm});
            skLineSegment(sketch, "E6111", {"start": v(15.1, -33.14) * mm, "end": v(15.18, -33.16) * mm});
            skLineSegment(sketch, "E6112", {"start": v(15.18, -33.16) * mm, "end": v(15.26, -33.17) * mm});
            skLineSegment(sketch, "E6113", {"start": v(15.26, -33.17) * mm, "end": v(15.34, -33.2) * mm});
            skLineSegment(sketch, "E6114", {"start": v(15.34, -33.2) * mm, "end": v(15.43, -33.21) * mm});
            skLineSegment(sketch, "E6115", {"start": v(15.43, -33.21) * mm, "end": v(15.51, -33.23) * mm});
            skLineSegment(sketch, "E6116", {"start": v(15.51, -33.23) * mm, "end": v(15.6, -33.25) * mm});
            skLineSegment(sketch, "E6117", {"start": v(15.6, -33.25) * mm, "end": v(15.68, -33.26) * mm});
            skLineSegment(sketch, "E6118", {"start": v(15.68, -33.26) * mm, "end": v(15.77, -33.28) * mm});
            skLineSegment(sketch, "E6119", {"start": v(15.77, -33.28) * mm, "end": v(15.86, -33.3) * mm});
            skLineSegment(sketch, "E6120", {"start": v(15.86, -33.3) * mm, "end": v(15.95, -33.31) * mm});
            skLineSegment(sketch, "E6121", {"start": v(15.95, -33.31) * mm, "end": v(16.04, -33.33) * mm});
            skLineSegment(sketch, "E6122", {"start": v(16.04, -33.33) * mm, "end": v(16.14, -33.35) * mm});
            skLineSegment(sketch, "E6123", {"start": v(16.14, -33.35) * mm, "end": v(16.23, -33.36) * mm});
            skLineSegment(sketch, "E6124", {"start": v(16.23, -33.36) * mm, "end": v(16.33, -33.38) * mm});
            skLineSegment(sketch, "E6125", {"start": v(16.33, -33.38) * mm, "end": v(16.42, -33.4) * mm});
            skLineSegment(sketch, "E6126", {"start": v(16.42, -33.4) * mm, "end": v(16.52, -33.4) * mm});
            skLineSegment(sketch, "E6127", {"start": v(16.52, -33.4) * mm, "end": v(16.62, -33.42) * mm});
            skLineSegment(sketch, "E6128", {"start": v(16.62, -33.42) * mm, "end": v(16.72, -33.44) * mm});
            skLineSegment(sketch, "E6129", {"start": v(16.72, -33.44) * mm, "end": v(16.82, -33.45) * mm});
            skLineSegment(sketch, "E6130", {"start": v(16.82, -33.45) * mm, "end": v(16.93, -33.46) * mm});
            skLineSegment(sketch, "E6131", {"start": v(16.93, -33.46) * mm, "end": v(17.03, -33.48) * mm});
            skLineSegment(sketch, "E6132", {"start": v(17.03, -33.48) * mm, "end": v(17.14, -33.5) * mm});
            skLineSegment(sketch, "E6133", {"start": v(17.14, -33.5) * mm, "end": v(17.18, -33.47) * mm});
            skLineSegment(sketch, "E6134", {"start": v(17.18, -33.47) * mm, "end": v(17.7, -32.57) * mm});
            skLineSegment(sketch, "E6135", {"start": v(17.7, -32.57) * mm, "end": v(17.7, -32.52) * mm});
            skLineSegment(sketch, "E6136", {"start": v(17.7, -32.52) * mm, "end": v(17.64, -32.43) * mm});
            skLineSegment(sketch, "E6137", {"start": v(17.64, -32.43) * mm, "end": v(17.57, -32.35) * mm});
            skLineSegment(sketch, "E6138", {"start": v(17.57, -32.35) * mm, "end": v(17.51, -32.26) * mm});
            skLineSegment(sketch, "E6139", {"start": v(17.51, -32.26) * mm, "end": v(17.45, -32.18) * mm});
            skLineSegment(sketch, "E6140", {"start": v(17.45, -32.18) * mm, "end": v(17.39, -32.1) * mm});
            skLineSegment(sketch, "E6141", {"start": v(17.39, -32.1) * mm, "end": v(17.33, -32.02) * mm});
            skLineSegment(sketch, "E6142", {"start": v(17.33, -32.02) * mm, "end": v(17.26, -31.94) * mm});
            skLineSegment(sketch, "E6143", {"start": v(17.26, -31.94) * mm, "end": v(17.2, -31.87) * mm});
            skLineSegment(sketch, "E6144", {"start": v(17.2, -31.87) * mm, "end": v(17.14, -31.8) * mm});
            skLineSegment(sketch, "E6145", {"start": v(17.14, -31.8) * mm, "end": v(17.08, -31.72) * mm});
            skLineSegment(sketch, "E6146", {"start": v(17.08, -31.72) * mm, "end": v(17.02, -31.65) * mm});
            skLineSegment(sketch, "E6147", {"start": v(17.02, -31.65) * mm, "end": v(16.96, -31.57) * mm});
            skLineSegment(sketch, "E6148", {"start": v(16.96, -31.57) * mm, "end": v(16.9, -31.5) * mm});
            skLineSegment(sketch, "E6149", {"start": v(16.9, -31.5) * mm, "end": v(16.84, -31.44) * mm});
            skLineSegment(sketch, "E6150", {"start": v(16.84, -31.44) * mm, "end": v(16.79, -31.37) * mm});
            skLineSegment(sketch, "E6151", {"start": v(16.79, -31.37) * mm, "end": v(16.73, -31.3) * mm});
            skLineSegment(sketch, "E6152", {"start": v(16.73, -31.3) * mm, "end": v(16.67, -31.24) * mm});
            skLineSegment(sketch, "E6153", {"start": v(16.67, -31.24) * mm, "end": v(16.61, -31.17) * mm});
            skLineSegment(sketch, "E6154", {"start": v(16.61, -31.17) * mm, "end": v(16.56, -31.1) * mm});
            skLineSegment(sketch, "E6155", {"start": v(16.56, -31.1) * mm, "end": v(16.5, -31.05) * mm});
            skLineSegment(sketch, "E6156", {"start": v(16.5, -31.05) * mm, "end": v(16.44, -30.99) * mm});
            skLineSegment(sketch, "E6157", {"start": v(16.44, -30.99) * mm, "end": v(16.39, -30.93) * mm});
            skLineSegment(sketch, "E6158", {"start": v(16.39, -30.93) * mm, "end": v(16.34, -30.87) * mm});
            skLineSegment(sketch, "E6159", {"start": v(16.34, -30.87) * mm, "end": v(16.28, -30.8) * mm});
            skLineSegment(sketch, "E6160", {"start": v(16.28, -30.8) * mm, "end": v(16.23, -30.75) * mm});
            skLineSegment(sketch, "E6161", {"start": v(16.23, -30.75) * mm, "end": v(16.18, -30.7) * mm});
            skLineSegment(sketch, "E6162", {"start": v(16.18, -30.7) * mm, "end": v(16.12, -30.64) * mm});
            skLineSegment(sketch, "E6163", {"start": v(16.12, -30.64) * mm, "end": v(16.07, -30.6) * mm});
            skLineSegment(sketch, "E6164", {"start": v(16.07, -30.6) * mm, "end": v(16.02, -30.54) * mm});
            skLineSegment(sketch, "E6165", {"start": v(16.02, -30.54) * mm, "end": v(15.97, -30.49) * mm});
            skLineSegment(sketch, "E6166", {"start": v(15.97, -30.49) * mm, "end": v(15.92, -30.44) * mm});
            skLineSegment(sketch, "E6167", {"start": v(15.92, -30.44) * mm, "end": v(15.87, -30.4) * mm});
            skLineSegment(sketch, "E6168", {"start": v(15.87, -30.4) * mm, "end": v(15.82, -30.34) * mm});
            skLineSegment(sketch, "E6169", {"start": v(15.82, -30.34) * mm, "end": v(15.77, -30.3) * mm});
            skLineSegment(sketch, "E6170", {"start": v(15.77, -30.3) * mm, "end": v(15.73, -30.25) * mm});
            skLineSegment(sketch, "E6171", {"start": v(15.73, -30.25) * mm, "end": v(15.68, -30.2) * mm});
            skLineSegment(sketch, "E6172", {"start": v(15.68, -30.2) * mm, "end": v(15.63, -30.17) * mm});
            skLineSegment(sketch, "E6173", {"start": v(15.63, -30.17) * mm, "end": v(15.59, -30.12) * mm});
            skLineSegment(sketch, "E6174", {"start": v(15.59, -30.12) * mm, "end": v(15.54, -30.08) * mm});
            skLineSegment(sketch, "E6175", {"start": v(15.54, -30.08) * mm, "end": v(15.5, -30.04) * mm});
            skLineSegment(sketch, "E6176", {"start": v(15.5, -30.04) * mm, "end": v(15.6, -29.83) * mm});
            skLineSegment(sketch, "E6177", {"start": v(15.6, -29.83) * mm, "end": v(15.97, -29.12) * mm});
            skLineSegment(sketch, "E6178", {"start": v(15.97, -29.12) * mm, "end": v(16.09, -28.91) * mm});
            skLineSegment(sketch, "E6179", {"start": v(16.09, -28.91) * mm, "end": v(16.15, -28.93) * mm});
            skLineSegment(sketch, "E6180", {"start": v(16.15, -28.93) * mm, "end": v(16.2, -28.94) * mm});
            skLineSegment(sketch, "E6181", {"start": v(16.2, -28.94) * mm, "end": v(16.27, -28.95) * mm});
            skLineSegment(sketch, "E6182", {"start": v(16.27, -28.95) * mm, "end": v(16.33, -28.97) * mm});
            skLineSegment(sketch, "E6183", {"start": v(16.33, -28.97) * mm, "end": v(16.4, -28.98) * mm});
            skLineSegment(sketch, "E6184", {"start": v(16.4, -28.98) * mm, "end": v(16.46, -29) * mm});
            skLineSegment(sketch, "E6185", {"start": v(16.46, -29) * mm, "end": v(16.52, -29) * mm});
            skLineSegment(sketch, "E6186", {"start": v(16.52, -29) * mm, "end": v(16.59, -29.02) * mm});
            skLineSegment(sketch, "E6187", {"start": v(16.59, -29.02) * mm, "end": v(16.66, -29.03) * mm});
            skLineSegment(sketch, "E6188", {"start": v(16.66, -29.03) * mm, "end": v(16.72, -29.04) * mm});
            skLineSegment(sketch, "E6189", {"start": v(16.72, -29.04) * mm, "end": v(16.8, -29.06) * mm});
            skLineSegment(sketch, "E6190", {"start": v(16.8, -29.06) * mm, "end": v(16.87, -29.07) * mm});
            skLineSegment(sketch, "E6191", {"start": v(16.87, -29.07) * mm, "end": v(16.94, -29.08) * mm});
            skLineSegment(sketch, "E6192", {"start": v(16.94, -29.08) * mm, "end": v(17.01, -29.1) * mm});
            skLineSegment(sketch, "E6193", {"start": v(17.01, -29.1) * mm, "end": v(17.09, -29.1) * mm});
            skLineSegment(sketch, "E6194", {"start": v(17.09, -29.1) * mm, "end": v(17.17, -29.12) * mm});
            skLineSegment(sketch, "E6195", {"start": v(17.17, -29.12) * mm, "end": v(17.24, -29.13) * mm});
            skLineSegment(sketch, "E6196", {"start": v(17.24, -29.13) * mm, "end": v(17.32, -29.14) * mm});
            skLineSegment(sketch, "E6197", {"start": v(17.32, -29.14) * mm, "end": v(17.4, -29.15) * mm});
            skLineSegment(sketch, "E6198", {"start": v(17.4, -29.15) * mm, "end": v(17.48, -29.16) * mm});
            skLineSegment(sketch, "E6199", {"start": v(17.48, -29.16) * mm, "end": v(17.57, -29.17) * mm});
            skLineSegment(sketch, "E6200", {"start": v(17.57, -29.17) * mm, "end": v(17.65, -29.18) * mm});
            skLineSegment(sketch, "E6201", {"start": v(17.65, -29.18) * mm, "end": v(17.74, -29.2) * mm});
            skLineSegment(sketch, "E6202", {"start": v(17.74, -29.2) * mm, "end": v(17.82, -29.2) * mm});
            skLineSegment(sketch, "E6203", {"start": v(17.82, -29.2) * mm, "end": v(17.91, -29.21) * mm});
            skLineSegment(sketch, "E6204", {"start": v(17.91, -29.21) * mm, "end": v(18, -29.22) * mm});
            skLineSegment(sketch, "E6205", {"start": v(18, -29.22) * mm, "end": v(18.1, -29.23) * mm});
            skLineSegment(sketch, "E6206", {"start": v(18.1, -29.23) * mm, "end": v(18.18, -29.24) * mm});
            skLineSegment(sketch, "E6207", {"start": v(18.18, -29.24) * mm, "end": v(18.28, -29.25) * mm});
            skLineSegment(sketch, "E6208", {"start": v(18.28, -29.25) * mm, "end": v(18.37, -29.25) * mm});
            skLineSegment(sketch, "E6209", {"start": v(18.37, -29.25) * mm, "end": v(18.46, -29.26) * mm});
            skLineSegment(sketch, "E6210", {"start": v(18.46, -29.26) * mm, "end": v(18.56, -29.27) * mm});
            skLineSegment(sketch, "E6211", {"start": v(18.56, -29.27) * mm, "end": v(18.66, -29.27) * mm});
            skLineSegment(sketch, "E6212", {"start": v(18.66, -29.27) * mm, "end": v(18.76, -29.28) * mm});
            skLineSegment(sketch, "E6213", {"start": v(18.76, -29.28) * mm, "end": v(18.86, -29.29) * mm});
            skLineSegment(sketch, "E6214", {"start": v(18.86, -29.29) * mm, "end": v(18.96, -29.3) * mm});
            skLineSegment(sketch, "E6215", {"start": v(18.96, -29.3) * mm, "end": v(19.06, -29.3) * mm});
            skLineSegment(sketch, "E6216", {"start": v(19.06, -29.3) * mm, "end": v(19.17, -29.3) * mm});
            skLineSegment(sketch, "E6217", {"start": v(19.17, -29.3) * mm, "end": v(19.27, -29.3) * mm});
            skLineSegment(sketch, "E6218", {"start": v(19.27, -29.3) * mm, "end": v(19.38, -29.3) * mm});
            skLineSegment(sketch, "E6219", {"start": v(19.38, -29.3) * mm, "end": v(19.42, -29.28) * mm});
            skLineSegment(sketch, "E6220", {"start": v(19.42, -29.28) * mm, "end": v(19.86, -28.34) * mm});
            skLineSegment(sketch, "E6221", {"start": v(19.86, -28.34) * mm, "end": v(19.85, -28.29) * mm});
            skLineSegment(sketch, "E6222", {"start": v(19.85, -28.29) * mm, "end": v(19.78, -28.2) * mm});
            skLineSegment(sketch, "E6223", {"start": v(19.78, -28.2) * mm, "end": v(19.71, -28.13) * mm});
            skLineSegment(sketch, "E6224", {"start": v(19.71, -28.13) * mm, "end": v(19.64, -28.05) * mm});
            skLineSegment(sketch, "E6225", {"start": v(19.64, -28.05) * mm, "end": v(19.57, -27.98) * mm});
            skLineSegment(sketch, "E6226", {"start": v(19.57, -27.98) * mm, "end": v(19.5, -27.9) * mm});
            skLineSegment(sketch, "E6227", {"start": v(19.5, -27.9) * mm, "end": v(19.44, -27.83) * mm});
            skLineSegment(sketch, "E6228", {"start": v(19.44, -27.83) * mm, "end": v(19.37, -27.76) * mm});
            skLineSegment(sketch, "E6229", {"start": v(19.37, -27.76) * mm, "end": v(19.3, -27.69) * mm});
            skLineSegment(sketch, "E6230", {"start": v(19.3, -27.69) * mm, "end": v(19.23, -27.62) * mm});
            skLineSegment(sketch, "E6231", {"start": v(19.23, -27.62) * mm, "end": v(19.17, -27.55) * mm});
            skLineSegment(sketch, "E6232", {"start": v(19.17, -27.55) * mm, "end": v(19.1, -27.48) * mm});
            skLineSegment(sketch, "E6233", {"start": v(19.1, -27.48) * mm, "end": v(19.03, -27.42) * mm});
            skLineSegment(sketch, "E6234", {"start": v(19.03, -27.42) * mm, "end": v(18.97, -27.35) * mm});
            skLineSegment(sketch, "E6235", {"start": v(18.97, -27.35) * mm, "end": v(18.9, -27.29) * mm});
            skLineSegment(sketch, "E6236", {"start": v(18.9, -27.29) * mm, "end": v(18.84, -27.23) * mm});
            skLineSegment(sketch, "E6237", {"start": v(18.84, -27.23) * mm, "end": v(18.78, -27.16) * mm});
            skLineSegment(sketch, "E6238", {"start": v(18.78, -27.16) * mm, "end": v(18.71, -27.1) * mm});
            skLineSegment(sketch, "E6239", {"start": v(18.71, -27.1) * mm, "end": v(18.65, -27.04) * mm});
            skLineSegment(sketch, "E6240", {"start": v(18.65, -27.04) * mm, "end": v(18.59, -26.99) * mm});
            skLineSegment(sketch, "E6241", {"start": v(18.59, -26.99) * mm, "end": v(18.53, -26.93) * mm});
            skLineSegment(sketch, "E6242", {"start": v(18.53, -26.93) * mm, "end": v(18.47, -26.87) * mm});
            skLineSegment(sketch, "E6243", {"start": v(18.47, -26.87) * mm, "end": v(18.4, -26.82) * mm});
            skLineSegment(sketch, "E6244", {"start": v(18.4, -26.82) * mm, "end": v(18.35, -26.77) * mm});
            skLineSegment(sketch, "E6245", {"start": v(18.35, -26.77) * mm, "end": v(18.29, -26.71) * mm});
            skLineSegment(sketch, "E6246", {"start": v(18.29, -26.71) * mm, "end": v(18.23, -26.66) * mm});
            skLineSegment(sketch, "E6247", {"start": v(18.23, -26.66) * mm, "end": v(18.17, -26.61) * mm});
            skLineSegment(sketch, "E6248", {"start": v(18.17, -26.61) * mm, "end": v(18.11, -26.56) * mm});
            skLineSegment(sketch, "E6249", {"start": v(18.11, -26.56) * mm, "end": v(18.06, -26.52) * mm});
            skLineSegment(sketch, "E6250", {"start": v(18.06, -26.52) * mm, "end": v(18, -26.47) * mm});
            skLineSegment(sketch, "E6251", {"start": v(18, -26.47) * mm, "end": v(17.95, -26.42) * mm});
            skLineSegment(sketch, "E6252", {"start": v(17.95, -26.42) * mm, "end": v(17.9, -26.38) * mm});
            skLineSegment(sketch, "E6253", {"start": v(17.9, -26.38) * mm, "end": v(17.84, -26.33) * mm});
            skLineSegment(sketch, "E6254", {"start": v(17.84, -26.33) * mm, "end": v(17.79, -26.3) * mm});
            skLineSegment(sketch, "E6255", {"start": v(17.79, -26.3) * mm, "end": v(17.74, -26.25) * mm});
            skLineSegment(sketch, "E6256", {"start": v(17.74, -26.25) * mm, "end": v(17.68, -26.2) * mm});
            skLineSegment(sketch, "E6257", {"start": v(17.68, -26.2) * mm, "end": v(17.63, -26.17) * mm});
            skLineSegment(sketch, "E6258", {"start": v(17.63, -26.17) * mm, "end": v(17.58, -26.13) * mm});
            skLineSegment(sketch, "E6259", {"start": v(17.58, -26.13) * mm, "end": v(17.53, -26.1) * mm});
            skLineSegment(sketch, "E6260", {"start": v(17.53, -26.1) * mm, "end": v(17.49, -26.06) * mm});
            skLineSegment(sketch, "E6261", {"start": v(17.49, -26.06) * mm, "end": v(17.44, -26.02) * mm});
            skLineSegment(sketch, "E6262", {"start": v(17.44, -26.02) * mm, "end": v(17.52, -25.8) * mm});
            skLineSegment(sketch, "E6263", {"start": v(17.52, -25.8) * mm, "end": v(17.83, -25.06) * mm});
            skLineSegment(sketch, "E6264", {"start": v(17.83, -25.06) * mm, "end": v(17.93, -24.84) * mm});
            skLineSegment(sketch, "E6265", {"start": v(17.93, -24.84) * mm, "end": v(17.98, -24.85) * mm});
            skLineSegment(sketch, "E6266", {"start": v(17.98, -24.85) * mm, "end": v(18.04, -24.86) * mm});
            skLineSegment(sketch, "E6267", {"start": v(18.04, -24.86) * mm, "end": v(18.1, -24.87) * mm});
            skLineSegment(sketch, "E6268", {"start": v(18.1, -24.87) * mm, "end": v(18.17, -24.87) * mm});
            skLineSegment(sketch, "E6269", {"start": v(18.17, -24.87) * mm, "end": v(18.23, -24.88) * mm});
            skLineSegment(sketch, "E6270", {"start": v(18.23, -24.88) * mm, "end": v(18.3, -24.89) * mm});
            skLineSegment(sketch, "E6271", {"start": v(18.3, -24.89) * mm, "end": v(18.36, -24.9) * mm});
            skLineSegment(sketch, "E6272", {"start": v(18.36, -24.9) * mm, "end": v(18.43, -24.9) * mm});
            skLineSegment(sketch, "E6273", {"start": v(18.43, -24.9) * mm, "end": v(18.5, -24.9) * mm});
            skLineSegment(sketch, "E6274", {"start": v(18.5, -24.9) * mm, "end": v(18.57, -24.92) * mm});
            skLineSegment(sketch, "E6275", {"start": v(18.57, -24.92) * mm, "end": v(18.64, -24.92) * mm});
            skLineSegment(sketch, "E6276", {"start": v(18.64, -24.92) * mm, "end": v(18.71, -24.93) * mm});
            skLineSegment(sketch, "E6277", {"start": v(18.71, -24.93) * mm, "end": v(18.79, -24.93) * mm});
            skLineSegment(sketch, "E6278", {"start": v(18.79, -24.93) * mm, "end": v(18.86, -24.94) * mm});
            skLineSegment(sketch, "E6279", {"start": v(18.86, -24.94) * mm, "end": v(18.94, -24.94) * mm});
            skLineSegment(sketch, "E6280", {"start": v(18.94, -24.94) * mm, "end": v(19.02, -24.95) * mm});
            skLineSegment(sketch, "E6281", {"start": v(19.02, -24.95) * mm, "end": v(19.1, -24.95) * mm});
            skLineSegment(sketch, "E6282", {"start": v(19.1, -24.95) * mm, "end": v(19.17, -24.96) * mm});
            skLineSegment(sketch, "E6283", {"start": v(19.17, -24.96) * mm, "end": v(19.26, -24.96) * mm});
            skLineSegment(sketch, "E6284", {"start": v(19.26, -24.96) * mm, "end": v(19.34, -24.96) * mm});
            skLineSegment(sketch, "E6285", {"start": v(19.34, -24.96) * mm, "end": v(19.42, -24.97) * mm});
            skLineSegment(sketch, "E6286", {"start": v(19.42, -24.97) * mm, "end": v(19.5, -24.97) * mm});
            skLineSegment(sketch, "E6287", {"start": v(19.5, -24.97) * mm, "end": v(19.6, -24.97) * mm});
            skLineSegment(sketch, "E6288", {"start": v(19.6, -24.97) * mm, "end": v(19.68, -24.97) * mm});
            skLineSegment(sketch, "E6289", {"start": v(19.68, -24.97) * mm, "end": v(19.77, -24.98) * mm});
            skLineSegment(sketch, "E6290", {"start": v(19.77, -24.98) * mm, "end": v(19.86, -24.98) * mm});
            skLineSegment(sketch, "E6291", {"start": v(19.86, -24.98) * mm, "end": v(19.95, -24.98) * mm});
            skLineSegment(sketch, "E6292", {"start": v(19.95, -24.98) * mm, "end": v(20.04, -24.98) * mm});
            skLineSegment(sketch, "E6293", {"start": v(20.04, -24.98) * mm, "end": v(20.13, -24.98) * mm});
            skLineSegment(sketch, "E6294", {"start": v(20.13, -24.98) * mm, "end": v(20.23, -24.98) * mm});
            skLineSegment(sketch, "E6295", {"start": v(20.23, -24.98) * mm, "end": v(20.32, -24.98) * mm});
            skLineSegment(sketch, "E6296", {"start": v(20.32, -24.98) * mm, "end": v(20.42, -24.97) * mm});
            skLineSegment(sketch, "E6297", {"start": v(20.42, -24.97) * mm, "end": v(20.52, -24.97) * mm});
            skLineSegment(sketch, "E6298", {"start": v(20.52, -24.97) * mm, "end": v(20.62, -24.97) * mm});
            skLineSegment(sketch, "E6299", {"start": v(20.62, -24.97) * mm, "end": v(20.72, -24.97) * mm});
            skLineSegment(sketch, "E6300", {"start": v(20.72, -24.97) * mm, "end": v(20.82, -24.96) * mm});
            skLineSegment(sketch, "E6301", {"start": v(20.82, -24.96) * mm, "end": v(20.92, -24.96) * mm});
            skLineSegment(sketch, "E6302", {"start": v(20.92, -24.96) * mm, "end": v(21.03, -24.95) * mm});
            skLineSegment(sketch, "E6303", {"start": v(21.03, -24.95) * mm, "end": v(21.13, -24.95) * mm});
            skLineSegment(sketch, "E6304", {"start": v(21.13, -24.95) * mm, "end": v(21.24, -24.94) * mm});
            skLineSegment(sketch, "E6305", {"start": v(21.24, -24.94) * mm, "end": v(21.28, -24.9) * mm});
            skLineSegment(sketch, "E6306", {"start": v(21.28, -24.9) * mm, "end": v(21.63, -23.93) * mm});
            skLineSegment(sketch, "E6307", {"start": v(21.63, -23.93) * mm, "end": v(21.62, -23.88) * mm});
            skLineSegment(sketch, "E6308", {"start": v(21.62, -23.88) * mm, "end": v(21.54, -23.8) * mm});
            skLineSegment(sketch, "E6309", {"start": v(21.54, -23.8) * mm, "end": v(21.46, -23.74) * mm});
            skLineSegment(sketch, "E6310", {"start": v(21.46, -23.74) * mm, "end": v(21.39, -23.67) * mm});
            skLineSegment(sketch, "E6311", {"start": v(21.39, -23.67) * mm, "end": v(21.31, -23.6) * mm});
            skLineSegment(sketch, "E6312", {"start": v(21.31, -23.6) * mm, "end": v(21.24, -23.53) * mm});
            skLineSegment(sketch, "E6313", {"start": v(21.24, -23.53) * mm, "end": v(21.16, -23.46) * mm});
            skLineSegment(sketch, "E6314", {"start": v(21.16, -23.46) * mm, "end": v(21.09, -23.4) * mm});
            skLineSegment(sketch, "E6315", {"start": v(21.09, -23.4) * mm, "end": v(21.01, -23.33) * mm});
            skLineSegment(sketch, "E6316", {"start": v(21.01, -23.33) * mm, "end": v(20.94, -23.27) * mm});
            skLineSegment(sketch, "E6317", {"start": v(20.94, -23.27) * mm, "end": v(20.87, -23.2) * mm});
            skLineSegment(sketch, "E6318", {"start": v(20.87, -23.2) * mm, "end": v(20.8, -23.15) * mm});
            skLineSegment(sketch, "E6319", {"start": v(20.8, -23.15) * mm, "end": v(20.72, -23.09) * mm});
            skLineSegment(sketch, "E6320", {"start": v(20.72, -23.09) * mm, "end": v(20.65, -23.03) * mm});
            skLineSegment(sketch, "E6321", {"start": v(20.65, -23.03) * mm, "end": v(20.58, -22.97) * mm});
            skLineSegment(sketch, "E6322", {"start": v(20.58, -22.97) * mm, "end": v(20.51, -22.91) * mm});
            skLineSegment(sketch, "E6323", {"start": v(20.51, -22.91) * mm, "end": v(20.44, -22.86) * mm});
            skLineSegment(sketch, "E6324", {"start": v(20.44, -22.86) * mm, "end": v(20.38, -22.8) * mm});
            skLineSegment(sketch, "E6325", {"start": v(20.38, -22.8) * mm, "end": v(20.3, -22.75) * mm});
            skLineSegment(sketch, "E6326", {"start": v(20.3, -22.75) * mm, "end": v(20.24, -22.7) * mm});
            skLineSegment(sketch, "E6327", {"start": v(20.24, -22.7) * mm, "end": v(20.17, -22.65) * mm});
            skLineSegment(sketch, "E6328", {"start": v(20.17, -22.65) * mm, "end": v(20.1, -22.6) * mm});
            skLineSegment(sketch, "E6329", {"start": v(20.1, -22.6) * mm, "end": v(20.04, -22.55) * mm});
            skLineSegment(sketch, "E6330", {"start": v(20.04, -22.55) * mm, "end": v(19.98, -22.5) * mm});
            skLineSegment(sketch, "E6331", {"start": v(19.98, -22.5) * mm, "end": v(19.92, -22.46) * mm});
            skLineSegment(sketch, "E6332", {"start": v(19.92, -22.46) * mm, "end": v(19.85, -22.4) * mm});
            skLineSegment(sketch, "E6333", {"start": v(19.85, -22.4) * mm, "end": v(19.8, -22.36) * mm});
            skLineSegment(sketch, "E6334", {"start": v(19.8, -22.36) * mm, "end": v(19.73, -22.32) * mm});
            skLineSegment(sketch, "E6335", {"start": v(19.73, -22.32) * mm, "end": v(19.67, -22.28) * mm});
            skLineSegment(sketch, "E6336", {"start": v(19.67, -22.28) * mm, "end": v(19.61, -22.24) * mm});
            skLineSegment(sketch, "E6337", {"start": v(19.61, -22.24) * mm, "end": v(19.55, -22.2) * mm});
            skLineSegment(sketch, "E6338", {"start": v(19.55, -22.2) * mm, "end": v(19.5, -22.16) * mm});
            skLineSegment(sketch, "E6339", {"start": v(19.5, -22.16) * mm, "end": v(19.44, -22.12) * mm});
            skLineSegment(sketch, "E6340", {"start": v(19.44, -22.12) * mm, "end": v(19.38, -22.08) * mm});
            skLineSegment(sketch, "E6341", {"start": v(19.38, -22.08) * mm, "end": v(19.33, -22.04) * mm});
            skLineSegment(sketch, "E6342", {"start": v(19.33, -22.04) * mm, "end": v(19.27, -22) * mm});
            skLineSegment(sketch, "E6343", {"start": v(19.27, -22) * mm, "end": v(19.22, -21.97) * mm});
            skLineSegment(sketch, "E6344", {"start": v(19.22, -21.97) * mm, "end": v(19.16, -21.94) * mm});
            skLineSegment(sketch, "E6345", {"start": v(19.16, -21.94) * mm, "end": v(19.11, -21.9) * mm});
            skLineSegment(sketch, "E6346", {"start": v(19.11, -21.9) * mm, "end": v(19.06, -21.87) * mm});
            skLineSegment(sketch, "E6347", {"start": v(19.06, -21.87) * mm, "end": v(19.01, -21.84) * mm});
            skLineSegment(sketch, "E6348", {"start": v(19.01, -21.84) * mm, "end": v(19.07, -21.61) * mm});
            skLineSegment(sketch, "E6349", {"start": v(19.07, -21.61) * mm, "end": v(19.31, -20.84) * mm});
            skLineSegment(sketch, "E6350", {"start": v(19.31, -20.84) * mm, "end": v(19.39, -20.62) * mm});
            skLineSegment(sketch, "E6351", {"start": v(19.39, -20.62) * mm, "end": v(19.45, -20.63) * mm});
            skLineSegment(sketch, "E6352", {"start": v(19.45, -20.63) * mm, "end": v(19.5, -20.63) * mm});
            skLineSegment(sketch, "E6353", {"start": v(19.5, -20.63) * mm, "end": v(19.57, -20.63) * mm});
            skLineSegment(sketch, "E6354", {"start": v(19.57, -20.63) * mm, "end": v(19.63, -20.63) * mm});
            skLineSegment(sketch, "E6355", {"start": v(19.63, -20.63) * mm, "end": v(19.7, -20.63) * mm});
            skLineSegment(sketch, "E6356", {"start": v(19.7, -20.63) * mm, "end": v(19.76, -20.64) * mm});
            skLineSegment(sketch, "E6357", {"start": v(19.76, -20.64) * mm, "end": v(19.83, -20.64) * mm});
            skLineSegment(sketch, "E6358", {"start": v(19.83, -20.64) * mm, "end": v(19.9, -20.64) * mm});
            skLineSegment(sketch, "E6359", {"start": v(19.9, -20.64) * mm, "end": v(19.97, -20.64) * mm});
            skLineSegment(sketch, "E6360", {"start": v(19.97, -20.64) * mm, "end": v(20.04, -20.64) * mm});
            skLineSegment(sketch, "E6361", {"start": v(20.04, -20.64) * mm, "end": v(20.1, -20.64) * mm});
            skLineSegment(sketch, "E6362", {"start": v(20.1, -20.64) * mm, "end": v(20.18, -20.64) * mm});
            skLineSegment(sketch, "E6363", {"start": v(20.18, -20.64) * mm, "end": v(20.26, -20.64) * mm});
            skLineSegment(sketch, "E6364", {"start": v(20.26, -20.64) * mm, "end": v(20.33, -20.64) * mm});
            skLineSegment(sketch, "E6365", {"start": v(20.33, -20.64) * mm, "end": v(20.4, -20.63) * mm});
            skLineSegment(sketch, "E6366", {"start": v(20.4, -20.63) * mm, "end": v(20.48, -20.63) * mm});
            skLineSegment(sketch, "E6367", {"start": v(20.48, -20.63) * mm, "end": v(20.56, -20.63) * mm});
            skLineSegment(sketch, "E6368", {"start": v(20.56, -20.63) * mm, "end": v(20.64, -20.63) * mm});
            skLineSegment(sketch, "E6369", {"start": v(20.64, -20.63) * mm, "end": v(20.72, -20.62) * mm});
            skLineSegment(sketch, "E6370", {"start": v(20.72, -20.62) * mm, "end": v(20.8, -20.62) * mm});
            skLineSegment(sketch, "E6371", {"start": v(20.8, -20.62) * mm, "end": v(20.9, -20.61) * mm});
            skLineSegment(sketch, "E6372", {"start": v(20.9, -20.61) * mm, "end": v(20.98, -20.6) * mm});
            skLineSegment(sketch, "E6373", {"start": v(20.98, -20.6) * mm, "end": v(21.06, -20.6) * mm});
            skLineSegment(sketch, "E6374", {"start": v(21.06, -20.6) * mm, "end": v(21.15, -20.6) * mm});
            skLineSegment(sketch, "E6375", {"start": v(21.15, -20.6) * mm, "end": v(21.24, -20.6) * mm});
            skLineSegment(sketch, "E6376", {"start": v(21.24, -20.6) * mm, "end": v(21.33, -20.59) * mm});
            skLineSegment(sketch, "E6377", {"start": v(21.33, -20.59) * mm, "end": v(21.42, -20.58) * mm});
            skLineSegment(sketch, "E6378", {"start": v(21.42, -20.58) * mm, "end": v(21.5, -20.57) * mm});
            skLineSegment(sketch, "E6379", {"start": v(21.5, -20.57) * mm, "end": v(21.6, -20.56) * mm});
            skLineSegment(sketch, "E6380", {"start": v(21.6, -20.56) * mm, "end": v(21.7, -20.55) * mm});
            skLineSegment(sketch, "E6381", {"start": v(21.7, -20.55) * mm, "end": v(21.79, -20.54) * mm});
            skLineSegment(sketch, "E6382", {"start": v(21.79, -20.54) * mm, "end": v(21.89, -20.53) * mm});
            skLineSegment(sketch, "E6383", {"start": v(21.89, -20.53) * mm, "end": v(21.98, -20.52) * mm});
            skLineSegment(sketch, "E6384", {"start": v(21.98, -20.52) * mm, "end": v(22.08, -20.5) * mm});
            skLineSegment(sketch, "E6385", {"start": v(22.08, -20.5) * mm, "end": v(22.18, -20.5) * mm});
            skLineSegment(sketch, "E6386", {"start": v(22.18, -20.5) * mm, "end": v(22.28, -20.48) * mm});
            skLineSegment(sketch, "E6387", {"start": v(22.28, -20.48) * mm, "end": v(22.38, -20.47) * mm});
            skLineSegment(sketch, "E6388", {"start": v(22.38, -20.47) * mm, "end": v(22.49, -20.46) * mm});
            skLineSegment(sketch, "E6389", {"start": v(22.49, -20.46) * mm, "end": v(22.6, -20.44) * mm});
            skLineSegment(sketch, "E6390", {"start": v(22.6, -20.44) * mm, "end": v(22.7, -20.43) * mm});
            skLineSegment(sketch, "E6391", {"start": v(22.7, -20.43) * mm, "end": v(22.73, -20.39) * mm});
            skLineSegment(sketch, "E6392", {"start": v(22.73, -20.39) * mm, "end": v(23, -19.38) * mm});
            skLineSegment(sketch, "E6393", {"start": v(23, -19.38) * mm, "end": v(22.98, -19.33) * mm});
            skLineSegment(sketch, "E6394", {"start": v(22.98, -19.33) * mm, "end": v(22.9, -19.27) * mm});
            skLineSegment(sketch, "E6395", {"start": v(22.9, -19.27) * mm, "end": v(22.82, -19.2) * mm});
            skLineSegment(sketch, "E6396", {"start": v(22.82, -19.2) * mm, "end": v(22.73, -19.14) * mm});
            skLineSegment(sketch, "E6397", {"start": v(22.73, -19.14) * mm, "end": v(22.65, -19.08) * mm});
            skLineSegment(sketch, "E6398", {"start": v(22.65, -19.08) * mm, "end": v(22.57, -19.02) * mm});
            skLineSegment(sketch, "E6399", {"start": v(22.57, -19.02) * mm, "end": v(22.49, -18.96) * mm});
            skLineSegment(sketch, "E6400", {"start": v(22.49, -18.96) * mm, "end": v(22.4, -18.9) * mm});
            skLineSegment(sketch, "E6401", {"start": v(22.4, -18.9) * mm, "end": v(22.33, -18.84) * mm});
            skLineSegment(sketch, "E6402", {"start": v(22.33, -18.84) * mm, "end": v(22.25, -18.79) * mm});
            skLineSegment(sketch, "E6403", {"start": v(22.25, -18.79) * mm, "end": v(22.17, -18.73) * mm});
            skLineSegment(sketch, "E6404", {"start": v(22.17, -18.73) * mm, "end": v(22.1, -18.68) * mm});
            skLineSegment(sketch, "E6405", {"start": v(22.1, -18.68) * mm, "end": v(22.02, -18.62) * mm});
            skLineSegment(sketch, "E6406", {"start": v(22.02, -18.62) * mm, "end": v(21.94, -18.57) * mm});
            skLineSegment(sketch, "E6407", {"start": v(21.94, -18.57) * mm, "end": v(21.87, -18.52) * mm});
            skLineSegment(sketch, "E6408", {"start": v(21.87, -18.52) * mm, "end": v(21.8, -18.47) * mm});
            skLineSegment(sketch, "E6409", {"start": v(21.8, -18.47) * mm, "end": v(21.72, -18.42) * mm});
            skLineSegment(sketch, "E6410", {"start": v(21.72, -18.42) * mm, "end": v(21.65, -18.37) * mm});
            skLineSegment(sketch, "E6411", {"start": v(21.65, -18.37) * mm, "end": v(21.57, -18.33) * mm});
            skLineSegment(sketch, "E6412", {"start": v(21.57, -18.33) * mm, "end": v(21.5, -18.28) * mm});
            skLineSegment(sketch, "E6413", {"start": v(21.5, -18.28) * mm, "end": v(21.43, -18.24) * mm});
            skLineSegment(sketch, "E6414", {"start": v(21.43, -18.24) * mm, "end": v(21.36, -18.2) * mm});
            skLineSegment(sketch, "E6415", {"start": v(21.36, -18.2) * mm, "end": v(21.3, -18.15) * mm});
            skLineSegment(sketch, "E6416", {"start": v(21.3, -18.15) * mm, "end": v(21.23, -18.1) * mm});
            skLineSegment(sketch, "E6417", {"start": v(21.23, -18.1) * mm, "end": v(21.16, -18.07) * mm});
            skLineSegment(sketch, "E6418", {"start": v(21.16, -18.07) * mm, "end": v(21.1, -18.03) * mm});
            skLineSegment(sketch, "E6419", {"start": v(21.1, -18.03) * mm, "end": v(21.03, -17.99) * mm});
            skLineSegment(sketch, "E6420", {"start": v(21.03, -17.99) * mm, "end": v(20.96, -17.95) * mm});
            skLineSegment(sketch, "E6421", {"start": v(20.96, -17.95) * mm, "end": v(20.9, -17.91) * mm});
            skLineSegment(sketch, "E6422", {"start": v(20.9, -17.91) * mm, "end": v(20.84, -17.88) * mm});
            skLineSegment(sketch, "E6423", {"start": v(20.84, -17.88) * mm, "end": v(20.77, -17.84) * mm});
            skLineSegment(sketch, "E6424", {"start": v(20.77, -17.84) * mm, "end": v(20.71, -17.8) * mm});
            skLineSegment(sketch, "E6425", {"start": v(20.71, -17.8) * mm, "end": v(20.65, -17.77) * mm});
            skLineSegment(sketch, "E6426", {"start": v(20.65, -17.77) * mm, "end": v(20.6, -17.74) * mm});
            skLineSegment(sketch, "E6427", {"start": v(20.6, -17.74) * mm, "end": v(20.53, -17.7) * mm});
            skLineSegment(sketch, "E6428", {"start": v(20.53, -17.7) * mm, "end": v(20.48, -17.68) * mm});
            skLineSegment(sketch, "E6429", {"start": v(20.48, -17.68) * mm, "end": v(20.42, -17.65) * mm});
            skLineSegment(sketch, "E6430", {"start": v(20.42, -17.65) * mm, "end": v(20.36, -17.62) * mm});
            skLineSegment(sketch, "E6431", {"start": v(20.36, -17.62) * mm, "end": v(20.3, -17.6) * mm});
            skLineSegment(sketch, "E6432", {"start": v(20.3, -17.6) * mm, "end": v(20.25, -17.56) * mm});
            skLineSegment(sketch, "E6433", {"start": v(20.25, -17.56) * mm, "end": v(20.2, -17.54) * mm});
            skLineSegment(sketch, "E6434", {"start": v(20.2, -17.54) * mm, "end": v(20.24, -17.3) * mm});
            skLineSegment(sketch, "E6435", {"start": v(20.24, -17.3) * mm, "end": v(20.41, -16.52) * mm});
            skLineSegment(sketch, "E6436", {"start": v(20.41, -16.52) * mm, "end": v(20.47, -16.3) * mm});
            skLineSegment(sketch, "E6437", {"start": v(20.47, -16.3) * mm, "end": v(20.53, -16.29) * mm});
            skLineSegment(sketch, "E6438", {"start": v(20.53, -16.29) * mm, "end": v(20.59, -16.28) * mm});
            skLineSegment(sketch, "E6439", {"start": v(20.59, -16.28) * mm, "end": v(20.65, -16.28) * mm});
            skLineSegment(sketch, "E6440", {"start": v(20.65, -16.28) * mm, "end": v(20.71, -16.28) * mm});
            skLineSegment(sketch, "E6441", {"start": v(20.71, -16.28) * mm, "end": v(20.78, -16.27) * mm});
            skLineSegment(sketch, "E6442", {"start": v(20.78, -16.27) * mm, "end": v(20.84, -16.27) * mm});
            skLineSegment(sketch, "E6443", {"start": v(20.84, -16.27) * mm, "end": v(20.91, -16.26) * mm});
            skLineSegment(sketch, "E6444", {"start": v(20.91, -16.26) * mm, "end": v(20.98, -16.26) * mm});
            skLineSegment(sketch, "E6445", {"start": v(20.98, -16.26) * mm, "end": v(21.05, -16.25) * mm});
            skLineSegment(sketch, "E6446", {"start": v(21.05, -16.25) * mm, "end": v(21.12, -16.25) * mm});
            skLineSegment(sketch, "E6447", {"start": v(21.12, -16.25) * mm, "end": v(21.19, -16.24) * mm});
            skLineSegment(sketch, "E6448", {"start": v(21.19, -16.24) * mm, "end": v(21.26, -16.23) * mm});
            skLineSegment(sketch, "E6449", {"start": v(21.26, -16.23) * mm, "end": v(21.33, -16.23) * mm});
            skLineSegment(sketch, "E6450", {"start": v(21.33, -16.23) * mm, "end": v(21.4, -16.22) * mm});
            skLineSegment(sketch, "E6451", {"start": v(21.4, -16.22) * mm, "end": v(21.48, -16.2) * mm});
            skLineSegment(sketch, "E6452", {"start": v(21.48, -16.2) * mm, "end": v(21.56, -16.2) * mm});
            skLineSegment(sketch, "E6453", {"start": v(21.56, -16.2) * mm, "end": v(21.64, -16.2) * mm});
            skLineSegment(sketch, "E6454", {"start": v(21.64, -16.2) * mm, "end": v(21.72, -16.18) * mm});
            skLineSegment(sketch, "E6455", {"start": v(21.72, -16.18) * mm, "end": v(21.8, -16.17) * mm});
            skLineSegment(sketch, "E6456", {"start": v(21.8, -16.17) * mm, "end": v(21.88, -16.16) * mm});
            skLineSegment(sketch, "E6457", {"start": v(21.88, -16.16) * mm, "end": v(21.96, -16.15) * mm});
            skLineSegment(sketch, "E6458", {"start": v(21.96, -16.15) * mm, "end": v(22.05, -16.13) * mm});
            skLineSegment(sketch, "E6459", {"start": v(22.05, -16.13) * mm, "end": v(22.13, -16.12) * mm});
            skLineSegment(sketch, "E6460", {"start": v(22.13, -16.12) * mm, "end": v(22.22, -16.1) * mm});
            skLineSegment(sketch, "E6461", {"start": v(22.22, -16.1) * mm, "end": v(22.3, -16.1) * mm});
            skLineSegment(sketch, "E6462", {"start": v(22.3, -16.1) * mm, "end": v(22.4, -16.08) * mm});
            skLineSegment(sketch, "E6463", {"start": v(22.4, -16.08) * mm, "end": v(22.48, -16.06) * mm});
            skLineSegment(sketch, "E6464", {"start": v(22.48, -16.06) * mm, "end": v(22.57, -16.05) * mm});
            skLineSegment(sketch, "E6465", {"start": v(22.57, -16.05) * mm, "end": v(22.67, -16.03) * mm});
            skLineSegment(sketch, "E6466", {"start": v(22.67, -16.03) * mm, "end": v(22.76, -16.01) * mm});
            skLineSegment(sketch, "E6467", {"start": v(22.76, -16.01) * mm, "end": v(22.85, -16) * mm});
            skLineSegment(sketch, "E6468", {"start": v(22.85, -16) * mm, "end": v(22.95, -15.97) * mm});
            skLineSegment(sketch, "E6469", {"start": v(22.95, -15.97) * mm, "end": v(23.04, -15.96) * mm});
            skLineSegment(sketch, "E6470", {"start": v(23.04, -15.96) * mm, "end": v(23.14, -15.93) * mm});
            skLineSegment(sketch, "E6471", {"start": v(23.14, -15.93) * mm, "end": v(23.24, -15.91) * mm});
            skLineSegment(sketch, "E6472", {"start": v(23.24, -15.91) * mm, "end": v(23.34, -15.9) * mm});
            skLineSegment(sketch, "E6473", {"start": v(23.34, -15.9) * mm, "end": v(23.44, -15.87) * mm});
            skLineSegment(sketch, "E6474", {"start": v(23.44, -15.87) * mm, "end": v(23.54, -15.85) * mm});
            skLineSegment(sketch, "E6475", {"start": v(23.54, -15.85) * mm, "end": v(23.64, -15.82) * mm});
            skLineSegment(sketch, "E6476", {"start": v(23.64, -15.82) * mm, "end": v(23.74, -15.8) * mm});
            skLineSegment(sketch, "E6477", {"start": v(23.74, -15.8) * mm, "end": v(23.78, -15.76) * mm});
            skLineSegment(sketch, "E6478", {"start": v(23.78, -15.76) * mm, "end": v(23.95, -14.73) * mm});
            skLineSegment(sketch, "E6479", {"start": v(23.95, -14.73) * mm, "end": v(23.93, -14.68) * mm});
            skLineSegment(sketch, "E6480", {"start": v(23.93, -14.68) * mm, "end": v(23.84, -14.63) * mm});
            skLineSegment(sketch, "E6481", {"start": v(23.84, -14.63) * mm, "end": v(23.75, -14.57) * mm});
            skLineSegment(sketch, "E6482", {"start": v(23.75, -14.57) * mm, "end": v(23.67, -14.52) * mm});
            skLineSegment(sketch, "E6483", {"start": v(23.67, -14.52) * mm, "end": v(23.58, -14.46) * mm});
            skLineSegment(sketch, "E6484", {"start": v(23.58, -14.46) * mm, "end": v(23.5, -14.4) * mm});
            skLineSegment(sketch, "E6485", {"start": v(23.5, -14.4) * mm, "end": v(23.4, -14.36) * mm});
            skLineSegment(sketch, "E6486", {"start": v(23.4, -14.36) * mm, "end": v(23.32, -14.3) * mm});
            skLineSegment(sketch, "E6487", {"start": v(23.32, -14.3) * mm, "end": v(23.24, -14.25) * mm});
            skLineSegment(sketch, "E6488", {"start": v(23.24, -14.25) * mm, "end": v(23.15, -14.2) * mm});
            skLineSegment(sketch, "E6489", {"start": v(23.15, -14.2) * mm, "end": v(23.07, -14.16) * mm});
            skLineSegment(sketch, "E6490", {"start": v(23.07, -14.16) * mm, "end": v(22.99, -14.11) * mm});
            skLineSegment(sketch, "E6491", {"start": v(22.99, -14.11) * mm, "end": v(22.9, -14.06) * mm});
            skLineSegment(sketch, "E6492", {"start": v(22.9, -14.06) * mm, "end": v(22.83, -14.02) * mm});
            skLineSegment(sketch, "E6493", {"start": v(22.83, -14.02) * mm, "end": v(22.75, -13.98) * mm});
            skLineSegment(sketch, "E6494", {"start": v(22.75, -13.98) * mm, "end": v(22.67, -13.93) * mm});
            skLineSegment(sketch, "E6495", {"start": v(22.67, -13.93) * mm, "end": v(22.6, -13.89) * mm});
            skLineSegment(sketch, "E6496", {"start": v(22.6, -13.89) * mm, "end": v(22.52, -13.85) * mm});
            skLineSegment(sketch, "E6497", {"start": v(22.52, -13.85) * mm, "end": v(22.44, -13.8) * mm});
            skLineSegment(sketch, "E6498", {"start": v(22.44, -13.8) * mm, "end": v(22.37, -13.77) * mm});
            skLineSegment(sketch, "E6499", {"start": v(22.37, -13.77) * mm, "end": v(22.3, -13.73) * mm});
            skLineSegment(sketch, "E6500", {"start": v(22.3, -13.73) * mm, "end": v(22.22, -13.7) * mm});
            skLineSegment(sketch, "E6501", {"start": v(22.22, -13.7) * mm, "end": v(22.15, -13.66) * mm});
            skLineSegment(sketch, "E6502", {"start": v(22.15, -13.66) * mm, "end": v(22.07, -13.62) * mm});
            skLineSegment(sketch, "E6503", {"start": v(22.07, -13.62) * mm, "end": v(22, -13.59) * mm});
            skLineSegment(sketch, "E6504", {"start": v(22, -13.59) * mm, "end": v(21.93, -13.55) * mm});
            skLineSegment(sketch, "E6505", {"start": v(21.93, -13.55) * mm, "end": v(21.86, -13.52) * mm});
            skLineSegment(sketch, "E6506", {"start": v(21.86, -13.52) * mm, "end": v(21.8, -13.49) * mm});
            skLineSegment(sketch, "E6507", {"start": v(21.8, -13.49) * mm, "end": v(21.73, -13.46) * mm});
            skLineSegment(sketch, "E6508", {"start": v(21.73, -13.46) * mm, "end": v(21.66, -13.43) * mm});
            skLineSegment(sketch, "E6509", {"start": v(21.66, -13.43) * mm, "end": v(21.6, -13.4) * mm});
            skLineSegment(sketch, "E6510", {"start": v(21.6, -13.4) * mm, "end": v(21.53, -13.37) * mm});
            skLineSegment(sketch, "E6511", {"start": v(21.53, -13.37) * mm, "end": v(21.47, -13.34) * mm});
            skLineSegment(sketch, "E6512", {"start": v(21.47, -13.34) * mm, "end": v(21.4, -13.31) * mm});
            skLineSegment(sketch, "E6513", {"start": v(21.4, -13.31) * mm, "end": v(21.35, -13.29) * mm});
            skLineSegment(sketch, "E6514", {"start": v(21.35, -13.29) * mm, "end": v(21.29, -13.26) * mm});
            skLineSegment(sketch, "E6515", {"start": v(21.29, -13.26) * mm, "end": v(21.23, -13.23) * mm});
            skLineSegment(sketch, "E6516", {"start": v(21.23, -13.23) * mm, "end": v(21.17, -13.21) * mm});
            skLineSegment(sketch, "E6517", {"start": v(21.17, -13.21) * mm, "end": v(21.11, -13.19) * mm});
            skLineSegment(sketch, "E6518", {"start": v(21.11, -13.19) * mm, "end": v(21.06, -13.16) * mm});
            skLineSegment(sketch, "E6519", {"start": v(21.06, -13.16) * mm, "end": v(21, -13.14) * mm});
            skLineSegment(sketch, "E6520", {"start": v(21, -13.14) * mm, "end": v(21.02, -12.91) * mm});
            skLineSegment(sketch, "E6521", {"start": v(21.02, -12.91) * mm, "end": v(21.12, -12.1) * mm});
            skLineSegment(sketch, "E6522", {"start": v(21.12, -12.1) * mm, "end": v(21.16, -11.88) * mm});
            skLineSegment(sketch, "E6523", {"start": v(21.16, -11.88) * mm, "end": v(21.22, -11.87) * mm});
            skLineSegment(sketch, "E6524", {"start": v(21.22, -11.87) * mm, "end": v(21.28, -11.86) * mm});
            skLineSegment(sketch, "E6525", {"start": v(21.28, -11.86) * mm, "end": v(21.34, -11.85) * mm});
            skLineSegment(sketch, "E6526", {"start": v(21.34, -11.85) * mm, "end": v(21.4, -11.84) * mm});
            skLineSegment(sketch, "E6527", {"start": v(21.4, -11.84) * mm, "end": v(21.46, -11.83) * mm});
            skLineSegment(sketch, "E6528", {"start": v(21.46, -11.83) * mm, "end": v(21.53, -11.82) * mm});
            skLineSegment(sketch, "E6529", {"start": v(21.53, -11.82) * mm, "end": v(21.6, -11.81) * mm});
            skLineSegment(sketch, "E6530", {"start": v(21.6, -11.81) * mm, "end": v(21.66, -11.8) * mm});
            skLineSegment(sketch, "E6531", {"start": v(21.66, -11.8) * mm, "end": v(21.73, -11.79) * mm});
            skLineSegment(sketch, "E6532", {"start": v(21.73, -11.79) * mm, "end": v(21.8, -11.78) * mm});
            skLineSegment(sketch, "E6533", {"start": v(21.8, -11.78) * mm, "end": v(21.87, -11.76) * mm});
            skLineSegment(sketch, "E6534", {"start": v(21.87, -11.76) * mm, "end": v(21.94, -11.75) * mm});
            skLineSegment(sketch, "E6535", {"start": v(21.94, -11.75) * mm, "end": v(22.01, -11.74) * mm});
            skLineSegment(sketch, "E6536", {"start": v(22.01, -11.74) * mm, "end": v(22.09, -11.72) * mm});
            skLineSegment(sketch, "E6537", {"start": v(22.09, -11.72) * mm, "end": v(22.16, -11.7) * mm});
            skLineSegment(sketch, "E6538", {"start": v(22.16, -11.7) * mm, "end": v(22.24, -11.7) * mm});
            skLineSegment(sketch, "E6539", {"start": v(22.24, -11.7) * mm, "end": v(22.31, -11.67) * mm});
            skLineSegment(sketch, "E6540", {"start": v(22.31, -11.67) * mm, "end": v(22.4, -11.66) * mm});
            skLineSegment(sketch, "E6541", {"start": v(22.4, -11.66) * mm, "end": v(22.47, -11.64) * mm});
            skLineSegment(sketch, "E6542", {"start": v(22.47, -11.64) * mm, "end": v(22.55, -11.62) * mm});
            skLineSegment(sketch, "E6543", {"start": v(22.55, -11.62) * mm, "end": v(22.63, -11.6) * mm});
            skLineSegment(sketch, "E6544", {"start": v(22.63, -11.6) * mm, "end": v(22.71, -11.58) * mm});
            skLineSegment(sketch, "E6545", {"start": v(22.71, -11.58) * mm, "end": v(22.8, -11.56) * mm});
            skLineSegment(sketch, "E6546", {"start": v(22.8, -11.56) * mm, "end": v(22.88, -11.54) * mm});
            skLineSegment(sketch, "E6547", {"start": v(22.88, -11.54) * mm, "end": v(22.97, -11.52) * mm});
            skLineSegment(sketch, "E6548", {"start": v(22.97, -11.52) * mm, "end": v(23.05, -11.5) * mm});
            skLineSegment(sketch, "E6549", {"start": v(23.05, -11.5) * mm, "end": v(23.14, -11.47) * mm});
            skLineSegment(sketch, "E6550", {"start": v(23.14, -11.47) * mm, "end": v(23.23, -11.45) * mm});
            skLineSegment(sketch, "E6551", {"start": v(23.23, -11.45) * mm, "end": v(23.32, -11.42) * mm});
            skLineSegment(sketch, "E6552", {"start": v(23.32, -11.42) * mm, "end": v(23.41, -11.4) * mm});
            skLineSegment(sketch, "E6553", {"start": v(23.41, -11.4) * mm, "end": v(23.5, -11.37) * mm});
            skLineSegment(sketch, "E6554", {"start": v(23.5, -11.37) * mm, "end": v(23.6, -11.34) * mm});
            skLineSegment(sketch, "E6555", {"start": v(23.6, -11.34) * mm, "end": v(23.69, -11.31) * mm});
            skLineSegment(sketch, "E6556", {"start": v(23.69, -11.31) * mm, "end": v(23.78, -11.28) * mm});
            skLineSegment(sketch, "E6557", {"start": v(23.78, -11.28) * mm, "end": v(23.88, -11.26) * mm});
            skLineSegment(sketch, "E6558", {"start": v(23.88, -11.26) * mm, "end": v(23.98, -11.22) * mm});
            skLineSegment(sketch, "E6559", {"start": v(23.98, -11.22) * mm, "end": v(24.08, -11.2) * mm});
            skLineSegment(sketch, "E6560", {"start": v(24.08, -11.2) * mm, "end": v(24.17, -11.16) * mm});
            skLineSegment(sketch, "E6561", {"start": v(24.17, -11.16) * mm, "end": v(24.27, -11.13) * mm});
            skLineSegment(sketch, "E6562", {"start": v(24.27, -11.13) * mm, "end": v(24.37, -11.1) * mm});
            skLineSegment(sketch, "E6563", {"start": v(24.37, -11.1) * mm, "end": v(24.4, -11.05) * mm});
            skLineSegment(sketch, "E6564", {"start": v(24.4, -11.05) * mm, "end": v(24.48, -10.01) * mm});
            skLineSegment(sketch, "E6565", {"start": v(24.48, -10.01) * mm, "end": v(24.46, -9.97) * mm});
            skLineSegment(sketch, "E6566", {"start": v(24.46, -9.97) * mm, "end": v(24.37, -9.92) * mm});
            skLineSegment(sketch, "E6567", {"start": v(24.37, -9.92) * mm, "end": v(24.27, -9.87) * mm});
            skLineSegment(sketch, "E6568", {"start": v(24.27, -9.87) * mm, "end": v(24.18, -9.82) * mm});
            skLineSegment(sketch, "E6569", {"start": v(24.18, -9.82) * mm, "end": v(24.09, -9.78) * mm});
            skLineSegment(sketch, "E6570", {"start": v(24.09, -9.78) * mm, "end": v(24, -9.73) * mm});
            skLineSegment(sketch, "E6571", {"start": v(24, -9.73) * mm, "end": v(23.9, -9.69) * mm});
            skLineSegment(sketch, "E6572", {"start": v(23.9, -9.69) * mm, "end": v(23.82, -9.64) * mm});
            skLineSegment(sketch, "E6573", {"start": v(23.82, -9.64) * mm, "end": v(23.73, -9.6) * mm});
            skLineSegment(sketch, "E6574", {"start": v(23.73, -9.6) * mm, "end": v(23.64, -9.56) * mm});
            skLineSegment(sketch, "E6575", {"start": v(23.64, -9.56) * mm, "end": v(23.56, -9.52) * mm});
            skLineSegment(sketch, "E6576", {"start": v(23.56, -9.52) * mm, "end": v(23.47, -9.48) * mm});
            skLineSegment(sketch, "E6577", {"start": v(23.47, -9.48) * mm, "end": v(23.39, -9.44) * mm});
            skLineSegment(sketch, "E6578", {"start": v(23.39, -9.44) * mm, "end": v(23.3, -9.4) * mm});
            skLineSegment(sketch, "E6579", {"start": v(23.3, -9.4) * mm, "end": v(23.22, -9.37) * mm});
            skLineSegment(sketch, "E6580", {"start": v(23.22, -9.37) * mm, "end": v(23.14, -9.33) * mm});
            skLineSegment(sketch, "E6581", {"start": v(23.14, -9.33) * mm, "end": v(23.06, -9.3) * mm});
            skLineSegment(sketch, "E6582", {"start": v(23.06, -9.3) * mm, "end": v(22.98, -9.26) * mm});
            skLineSegment(sketch, "E6583", {"start": v(22.98, -9.26) * mm, "end": v(22.9, -9.23) * mm});
            skLineSegment(sketch, "E6584", {"start": v(22.9, -9.23) * mm, "end": v(22.82, -9.2) * mm});
            skLineSegment(sketch, "E6585", {"start": v(22.82, -9.2) * mm, "end": v(22.74, -9.17) * mm});
            skLineSegment(sketch, "E6586", {"start": v(22.74, -9.17) * mm, "end": v(22.66, -9.13) * mm});
            skLineSegment(sketch, "E6587", {"start": v(22.66, -9.13) * mm, "end": v(22.59, -9.1) * mm});
            skLineSegment(sketch, "E6588", {"start": v(22.59, -9.1) * mm, "end": v(22.52, -9.08) * mm});
            skLineSegment(sketch, "E6589", {"start": v(22.52, -9.08) * mm, "end": v(22.44, -9.05) * mm});
            skLineSegment(sketch, "E6590", {"start": v(22.44, -9.05) * mm, "end": v(22.37, -9.02) * mm});
            skLineSegment(sketch, "E6591", {"start": v(22.37, -9.02) * mm, "end": v(22.3, -9) * mm});
            skLineSegment(sketch, "E6592", {"start": v(22.3, -9) * mm, "end": v(22.23, -8.97) * mm});
            skLineSegment(sketch, "E6593", {"start": v(22.23, -8.97) * mm, "end": v(22.16, -8.94) * mm});
            skLineSegment(sketch, "E6594", {"start": v(22.16, -8.94) * mm, "end": v(22.09, -8.92) * mm});
            skLineSegment(sketch, "E6595", {"start": v(22.09, -8.92) * mm, "end": v(22.02, -8.9) * mm});
            skLineSegment(sketch, "E6596", {"start": v(22.02, -8.9) * mm, "end": v(21.95, -8.87) * mm});
            skLineSegment(sketch, "E6597", {"start": v(21.95, -8.87) * mm, "end": v(21.89, -8.85) * mm});
            skLineSegment(sketch, "E6598", {"start": v(21.89, -8.85) * mm, "end": v(21.83, -8.83) * mm});
            skLineSegment(sketch, "E6599", {"start": v(21.83, -8.83) * mm, "end": v(21.76, -8.8) * mm});
            skLineSegment(sketch, "E6600", {"start": v(21.76, -8.8) * mm, "end": v(21.7, -8.79) * mm});
            skLineSegment(sketch, "E6601", {"start": v(21.7, -8.79) * mm, "end": v(21.64, -8.77) * mm});
            skLineSegment(sketch, "E6602", {"start": v(21.64, -8.77) * mm, "end": v(21.58, -8.75) * mm});
            skLineSegment(sketch, "E6603", {"start": v(21.58, -8.75) * mm, "end": v(21.52, -8.73) * mm});
            skLineSegment(sketch, "E6604", {"start": v(21.52, -8.73) * mm, "end": v(21.46, -8.71) * mm});
            skLineSegment(sketch, "E6605", {"start": v(21.46, -8.71) * mm, "end": v(21.4, -8.7) * mm});
            skLineSegment(sketch, "E6606", {"start": v(21.4, -8.7) * mm, "end": v(21.4, -8.46) * mm});
            skLineSegment(sketch, "E6607", {"start": v(21.4, -8.46) * mm, "end": v(21.43, -7.66) * mm});
            skFitSpline(sketch, "E6608", {"points": [v(44.64, 52.01) * mm, v(44.2, 52.01) * mm, v(43.85, 52.37) * mm, v(43.85, 52.8) * mm, v(43.85, 53.24) * mm, v(44.2, 53.6) * mm, v(44.64, 53.6) * mm, v(45.08, 53.6) * mm, v(45.43, 53.24) * mm, v(45.43, 52.8) * mm, v(45.43, 52.37) * mm, v(45.08, 52.01) * mm, v(44.64, 52.01) * mm]});
            skFitSpline(sketch, "E6609", {"points": [v(44.64, 25) * mm, v(43.74, 25) * mm, v(43.01, 25.73) * mm, v(43.01, 26.62) * mm, v(43.01, 27.52) * mm, v(43.74, 28.25) * mm, v(44.64, 28.25) * mm, v(45.54, 28.25) * mm, v(46.27, 27.52) * mm, v(46.27, 26.62) * mm, v(46.27, 25.73) * mm, v(45.54, 25) * mm, v(44.64, 25) * mm]});
            skFitSpline(sketch, "E6610", {"points": [v(-28.31, -8.06) * mm, v(-29.2, -8.06) * mm, v(-29.94, -7.33) * mm, v(-29.94, -6.43) * mm, v(-29.94, -5.54) * mm, v(-29.2, -4.8) * mm, v(-28.31, -4.8) * mm, v(-27.41, -4.8) * mm, v(-26.69, -5.54) * mm, v(-26.69, -6.43) * mm, v(-26.69, -7.33) * mm, v(-27.41, -8.06) * mm, v(-28.31, -8.06) * mm]});
            skSolve(sketch);
        }
        {
            var Q0;
            Q0=qCreatedBy(makeId("Top.planeOp"),FACE);
            var sketch = newSketch(context, id + "F1", { "sketchPlane" : qUnion([Q0])});
            skFitSpline(sketch, "E6611", {"points": [v(-5.38, -69.8) * mm, v(-6.28, -69.8) * mm, v(-7, -69.08) * mm, v(-7, -68.18) * mm, v(-7, -67.28) * mm, v(-6.28, -66.55) * mm, v(-5.38, -66.55) * mm, v(-4.48, -66.55) * mm, v(-3.75, -67.28) * mm, v(-3.75, -68.18) * mm, v(-3.75, -69.08) * mm, v(-4.48, -69.8) * mm, v(-5.38, -69.8) * mm]});
            skSolve(sketch);
        }
        {
            var Q0;
            Q0 = qSketchRegion(id + "F0", true);
            extrude(context, id + "F2", {"entities" : qUnion([Q0]), "depth" : 6.35 * mm, "offsetDistance" : 25.4 * mm});
        }
        {
            var Q0;
            Q0 = qSketchRegion(id + "F1", true);
            extrude(context, id + "F3", {"entities" : qUnion([Q0]), "depth" : 50.8 * mm, "offsetDistance" : 25.4 * mm});
        }
    });
